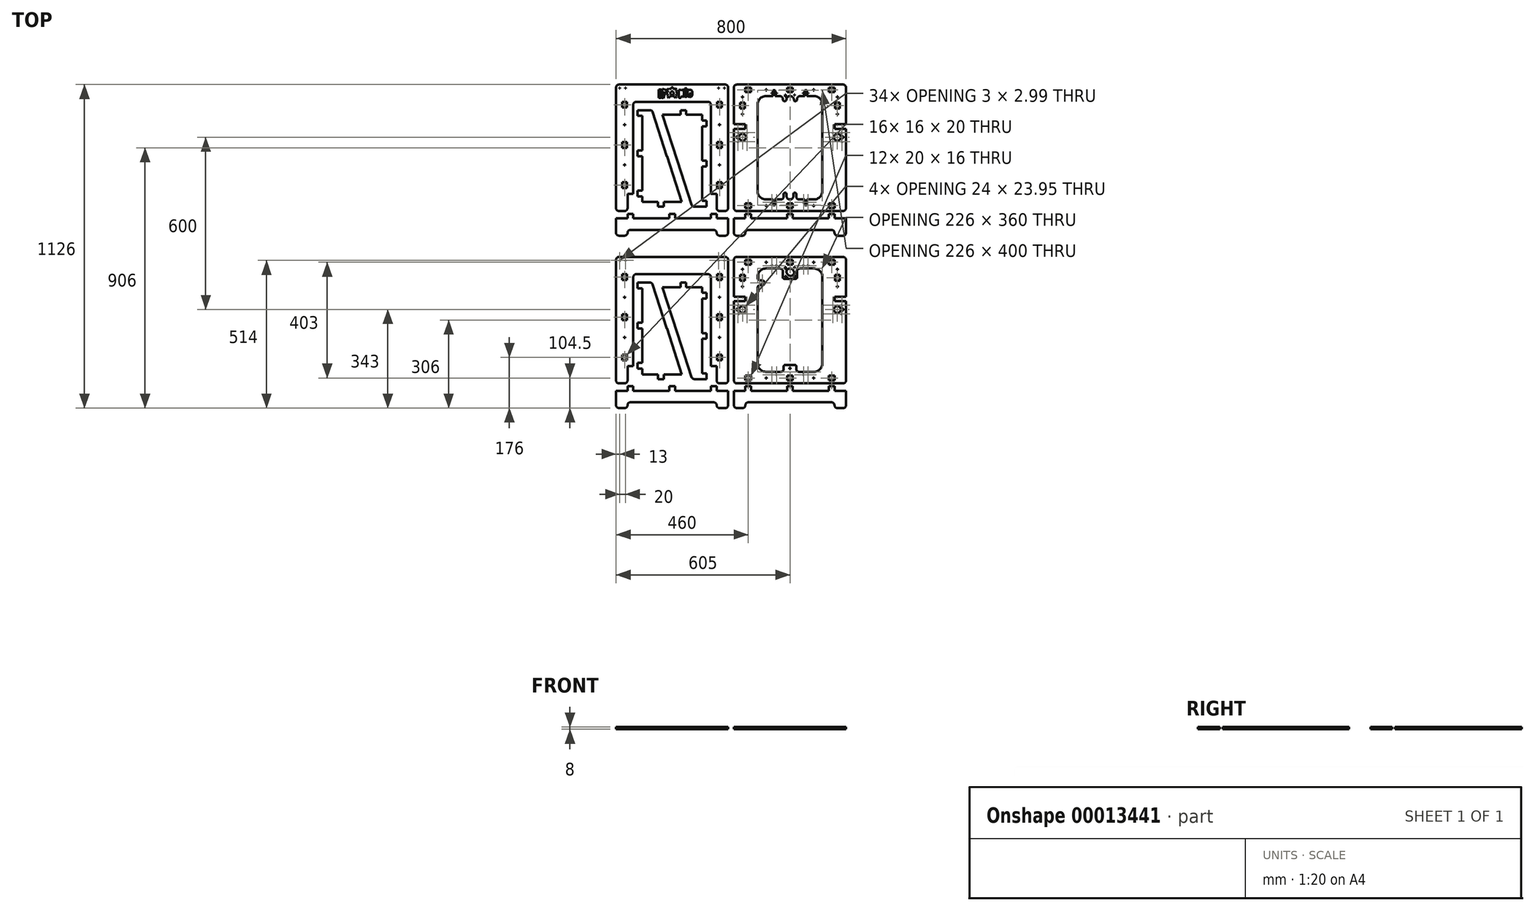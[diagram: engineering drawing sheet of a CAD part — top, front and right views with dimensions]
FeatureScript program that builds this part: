
annotation { "Feature Type Name" : "Feature", "Feature Type Description" : "" }
export const myFeature = defineFeature(function(context is Context, id is Id, definition is map)
    precondition{}
    {
        {
            var Q0;
            Q0=qCreatedBy(makeId("Top.planeOp"),FACE);
            var sketch = newSketch(context, id + "F0", { "sketchPlane" : qUnion([Q0])});
            skLineSegment(sketch, "E0", {"start": v(-368.75, 123.08) * mm, "end": v(-367.51, 123.31) * mm});
            skLineSegment(sketch, "E1", {"start": v(-367.51, 123.31) * mm, "end": v(-366.32, 123.7) * mm});
            skLineSegment(sketch, "E2", {"start": v(-366.32, 123.7) * mm, "end": v(-365.18, 124.24) * mm});
            skLineSegment(sketch, "E3", {"start": v(-365.18, 124.24) * mm, "end": v(-364.12, 124.9) * mm});
            skLineSegment(sketch, "E4", {"start": v(-364.12, 124.9) * mm, "end": v(-363.16, 125.7) * mm});
            skLineSegment(sketch, "E5", {"start": v(-363.16, 125.7) * mm, "end": v(-362.3, 126.63) * mm});
            skLineSegment(sketch, "E6", {"start": v(-362.3, 126.63) * mm, "end": v(-361.56, 127.64) * mm});
            skLineSegment(sketch, "E7", {"start": v(-361.56, 127.64) * mm, "end": v(-360.95, 128.74) * mm});
            skLineSegment(sketch, "E8", {"start": v(-360.95, 128.74) * mm, "end": v(-360.49, 129.9) * mm});
            skLineSegment(sketch, "E9", {"start": v(-360.49, 129.9) * mm, "end": v(-360.18, 131.13) * mm});
            skLineSegment(sketch, "E10", {"start": v(-360.18, 131.13) * mm, "end": v(-360.02, 132.37) * mm});
            skLineSegment(sketch, "E11", {"start": v(-360.02, 132.37) * mm, "end": v(-360.02, 133) * mm});
            skLineSegment(sketch, "E12", {"start": v(-360.02, 133) * mm, "end": v(-360, 133) * mm});
            skLineSegment(sketch, "E13", {"start": v(-360, 133) * mm, "end": v(-360, 183) * mm});
            skLineSegment(sketch, "E14", {"start": v(-360, 183) * mm, "end": v(-340, 183) * mm});
            skLineSegment(sketch, "E15", {"start": v(-340, 183) * mm, "end": v(-340, 493) * mm});
            skLineSegment(sketch, "E16", {"start": v(-340, 493) * mm, "end": v(-339.98, 493) * mm});
            skLineSegment(sketch, "E17", {"start": v(-339.98, 493) * mm, "end": v(-339.98, 493.63) * mm});
            skLineSegment(sketch, "E18", {"start": v(-339.98, 493.63) * mm, "end": v(-339.82, 494.87) * mm});
            skLineSegment(sketch, "E19", {"start": v(-339.82, 494.87) * mm, "end": v(-339.51, 496.09) * mm});
            skLineSegment(sketch, "E20", {"start": v(-339.51, 496.09) * mm, "end": v(-339.05, 497.26) * mm});
            skLineSegment(sketch, "E21", {"start": v(-339.05, 497.26) * mm, "end": v(-338.44, 498.36) * mm});
            skLineSegment(sketch, "E22", {"start": v(-338.44, 498.36) * mm, "end": v(-337.7, 499.37) * mm});
            skLineSegment(sketch, "E23", {"start": v(-337.7, 499.37) * mm, "end": v(-336.85, 500.3) * mm});
            skLineSegment(sketch, "E24", {"start": v(-336.85, 500.3) * mm, "end": v(-335.88, 501.1) * mm});
            skLineSegment(sketch, "E25", {"start": v(-335.88, 501.1) * mm, "end": v(-334.82, 501.76) * mm});
            skLineSegment(sketch, "E26", {"start": v(-334.82, 501.76) * mm, "end": v(-333.68, 502.3) * mm});
            skLineSegment(sketch, "E27", {"start": v(-333.68, 502.3) * mm, "end": v(-332.49, 502.7) * mm});
            skLineSegment(sketch, "E28", {"start": v(-332.49, 502.7) * mm, "end": v(-331.25, 502.92) * mm});
            skLineSegment(sketch, "E29", {"start": v(-331.25, 502.92) * mm, "end": v(-330, 503) * mm});
            skLineSegment(sketch, "E30", {"start": v(-330, 503) * mm, "end": v(-80, 503) * mm});
            skLineSegment(sketch, "E31", {"start": v(-80, 503) * mm, "end": v(-80, 502.98) * mm});
            skLineSegment(sketch, "E32", {"start": v(-80, 502.98) * mm, "end": v(-79.37, 502.98) * mm});
            skLineSegment(sketch, "E33", {"start": v(-79.37, 502.98) * mm, "end": v(-78.13, 502.82) * mm});
            skLineSegment(sketch, "E34", {"start": v(-78.13, 502.82) * mm, "end": v(-76.9, 502.5) * mm});
            skLineSegment(sketch, "E35", {"start": v(-76.9, 502.5) * mm, "end": v(-75.74, 502.05) * mm});
            skLineSegment(sketch, "E36", {"start": v(-75.74, 502.05) * mm, "end": v(-74.64, 501.44) * mm});
            skLineSegment(sketch, "E37", {"start": v(-74.64, 501.44) * mm, "end": v(-73.63, 500.7) * mm});
            skLineSegment(sketch, "E38", {"start": v(-73.63, 500.7) * mm, "end": v(-72.71, 499.85) * mm});
            skLineSegment(sketch, "E39", {"start": v(-72.71, 499.85) * mm, "end": v(-71.9, 498.88) * mm});
            skLineSegment(sketch, "E40", {"start": v(-71.9, 498.88) * mm, "end": v(-71.24, 497.82) * mm});
            skLineSegment(sketch, "E41", {"start": v(-71.24, 497.82) * mm, "end": v(-70.7, 496.68) * mm});
            skLineSegment(sketch, "E42", {"start": v(-70.7, 496.68) * mm, "end": v(-70.31, 495.5) * mm});
            skLineSegment(sketch, "E43", {"start": v(-70.31, 495.5) * mm, "end": v(-70.08, 494.25) * mm});
            skLineSegment(sketch, "E44", {"start": v(-70.08, 494.25) * mm, "end": v(-70, 493) * mm});
            skLineSegment(sketch, "E45", {"start": v(-70, 493) * mm, "end": v(-70, 183) * mm});
            skLineSegment(sketch, "E46", {"start": v(-70, 183) * mm, "end": v(-50, 183) * mm});
            skLineSegment(sketch, "E47", {"start": v(-50, 183) * mm, "end": v(-50, 133) * mm});
            skLineSegment(sketch, "E48", {"start": v(-50, 133) * mm, "end": v(-49.92, 131.75) * mm});
            skLineSegment(sketch, "E49", {"start": v(-49.92, 131.75) * mm, "end": v(-49.69, 130.51) * mm});
            skLineSegment(sketch, "E50", {"start": v(-49.69, 130.51) * mm, "end": v(-49.3, 129.32) * mm});
            skLineSegment(sketch, "E51", {"start": v(-49.3, 129.32) * mm, "end": v(-48.76, 128.18) * mm});
            skLineSegment(sketch, "E52", {"start": v(-48.76, 128.18) * mm, "end": v(-48.1, 127.12) * mm});
            skLineSegment(sketch, "E53", {"start": v(-48.1, 127.12) * mm, "end": v(-47.29, 126.16) * mm});
            skLineSegment(sketch, "E54", {"start": v(-47.29, 126.16) * mm, "end": v(-46.37, 125.3) * mm});
            skLineSegment(sketch, "E55", {"start": v(-46.37, 125.3) * mm, "end": v(-45.36, 124.56) * mm});
            skLineSegment(sketch, "E56", {"start": v(-45.36, 124.56) * mm, "end": v(-44.26, 123.95) * mm});
            skLineSegment(sketch, "E57", {"start": v(-44.26, 123.95) * mm, "end": v(-43.1, 123.49) * mm});
            skLineSegment(sketch, "E58", {"start": v(-43.1, 123.49) * mm, "end": v(-41.87, 123.18) * mm});
            skLineSegment(sketch, "E59", {"start": v(-41.87, 123.18) * mm, "end": v(-40.63, 123.02) * mm});
            skLineSegment(sketch, "E60", {"start": v(-40.63, 123.02) * mm, "end": v(-40, 123.02) * mm});
            skLineSegment(sketch, "E61", {"start": v(-40, 123.02) * mm, "end": v(-40, 123) * mm});
            skLineSegment(sketch, "E62", {"start": v(-40, 123) * mm, "end": v(-20, 123) * mm});
            skLineSegment(sketch, "E63", {"start": v(-20, 123) * mm, "end": v(-18.75, 123.08) * mm});
            skLineSegment(sketch, "E64", {"start": v(-18.75, 123.08) * mm, "end": v(-17.51, 123.31) * mm});
            skLineSegment(sketch, "E65", {"start": v(-17.51, 123.31) * mm, "end": v(-16.32, 123.7) * mm});
            skLineSegment(sketch, "E66", {"start": v(-16.32, 123.7) * mm, "end": v(-15.18, 124.24) * mm});
            skLineSegment(sketch, "E67", {"start": v(-15.18, 124.24) * mm, "end": v(-14.12, 124.9) * mm});
            skLineSegment(sketch, "E68", {"start": v(-14.12, 124.9) * mm, "end": v(-13.15, 125.7) * mm});
            skLineSegment(sketch, "E69", {"start": v(-13.15, 125.7) * mm, "end": v(-12.3, 126.63) * mm});
            skLineSegment(sketch, "E70", {"start": v(-12.3, 126.63) * mm, "end": v(-11.56, 127.64) * mm});
            skLineSegment(sketch, "E71", {"start": v(-11.56, 127.64) * mm, "end": v(-10.95, 128.74) * mm});
            skLineSegment(sketch, "E72", {"start": v(-10.95, 128.74) * mm, "end": v(-10.49, 129.9) * mm});
            skLineSegment(sketch, "E73", {"start": v(-10.49, 129.9) * mm, "end": v(-10.18, 131.13) * mm});
            skLineSegment(sketch, "E74", {"start": v(-10.18, 131.13) * mm, "end": v(-10.02, 132.37) * mm});
            skLineSegment(sketch, "E75", {"start": v(-10.02, 132.37) * mm, "end": v(-10.02, 133) * mm});
            skLineSegment(sketch, "E76", {"start": v(-10.02, 133) * mm, "end": v(-10, 133) * mm});
            skLineSegment(sketch, "E77", {"start": v(-10, 133) * mm, "end": v(-10, 553) * mm});
            skLineSegment(sketch, "E78", {"start": v(-10, 553) * mm, "end": v(-10.08, 554.25) * mm});
            skLineSegment(sketch, "E79", {"start": v(-10.08, 554.25) * mm, "end": v(-10.31, 555.5) * mm});
            skLineSegment(sketch, "E80", {"start": v(-10.31, 555.5) * mm, "end": v(-10.7, 556.68) * mm});
            skLineSegment(sketch, "E81", {"start": v(-10.7, 556.68) * mm, "end": v(-11.24, 557.82) * mm});
            skLineSegment(sketch, "E82", {"start": v(-11.24, 557.82) * mm, "end": v(-11.9, 558.88) * mm});
            skLineSegment(sketch, "E83", {"start": v(-11.9, 558.88) * mm, "end": v(-12.71, 559.85) * mm});
            skLineSegment(sketch, "E84", {"start": v(-12.71, 559.85) * mm, "end": v(-13.63, 560.7) * mm});
            skLineSegment(sketch, "E85", {"start": v(-13.63, 560.7) * mm, "end": v(-14.64, 561.44) * mm});
            skLineSegment(sketch, "E86", {"start": v(-14.64, 561.44) * mm, "end": v(-15.74, 562.05) * mm});
            skLineSegment(sketch, "E87", {"start": v(-15.74, 562.05) * mm, "end": v(-16.9, 562.5) * mm});
            skLineSegment(sketch, "E88", {"start": v(-16.9, 562.5) * mm, "end": v(-18.13, 562.82) * mm});
            skLineSegment(sketch, "E89", {"start": v(-18.13, 562.82) * mm, "end": v(-19.37, 562.98) * mm});
            skLineSegment(sketch, "E90", {"start": v(-19.37, 562.98) * mm, "end": v(-20, 562.98) * mm});
            skLineSegment(sketch, "E91", {"start": v(-20, 562.98) * mm, "end": v(-20, 563) * mm});
            skLineSegment(sketch, "E92", {"start": v(-20, 563) * mm, "end": v(-390, 563) * mm});
            skLineSegment(sketch, "E93", {"start": v(-390, 563) * mm, "end": v(-391.25, 562.92) * mm});
            skLineSegment(sketch, "E94", {"start": v(-391.25, 562.92) * mm, "end": v(-392.49, 562.7) * mm});
            skLineSegment(sketch, "E95", {"start": v(-392.49, 562.7) * mm, "end": v(-393.68, 562.3) * mm});
            skLineSegment(sketch, "E96", {"start": v(-393.68, 562.3) * mm, "end": v(-394.82, 561.76) * mm});
            skLineSegment(sketch, "E97", {"start": v(-394.82, 561.76) * mm, "end": v(-395.88, 561.1) * mm});
            skLineSegment(sketch, "E98", {"start": v(-395.88, 561.1) * mm, "end": v(-396.85, 560.3) * mm});
            skLineSegment(sketch, "E99", {"start": v(-396.85, 560.3) * mm, "end": v(-397.7, 559.37) * mm});
            skLineSegment(sketch, "E100", {"start": v(-397.7, 559.37) * mm, "end": v(-398.44, 558.36) * mm});
            skLineSegment(sketch, "E101", {"start": v(-398.44, 558.36) * mm, "end": v(-399.05, 557.26) * mm});
            skLineSegment(sketch, "E102", {"start": v(-399.05, 557.26) * mm, "end": v(-399.51, 556.1) * mm});
            skLineSegment(sketch, "E103", {"start": v(-399.51, 556.1) * mm, "end": v(-399.82, 554.87) * mm});
            skLineSegment(sketch, "E104", {"start": v(-399.82, 554.87) * mm, "end": v(-399.98, 553.63) * mm});
            skLineSegment(sketch, "E105", {"start": v(-399.98, 553.63) * mm, "end": v(-399.98, 553) * mm});
            skLineSegment(sketch, "E106", {"start": v(-399.98, 553) * mm, "end": v(-400, 553) * mm});
            skLineSegment(sketch, "E107", {"start": v(-400, 553) * mm, "end": v(-400, 133) * mm});
            skLineSegment(sketch, "E108", {"start": v(-400, 133) * mm, "end": v(-399.92, 131.75) * mm});
            skLineSegment(sketch, "E109", {"start": v(-399.92, 131.75) * mm, "end": v(-399.69, 130.51) * mm});
            skLineSegment(sketch, "E110", {"start": v(-399.69, 130.51) * mm, "end": v(-399.3, 129.32) * mm});
            skLineSegment(sketch, "E111", {"start": v(-399.3, 129.32) * mm, "end": v(-398.76, 128.18) * mm});
            skLineSegment(sketch, "E112", {"start": v(-398.76, 128.18) * mm, "end": v(-398.09, 127.12) * mm});
            skLineSegment(sketch, "E113", {"start": v(-398.09, 127.12) * mm, "end": v(-397.3, 126.16) * mm});
            skLineSegment(sketch, "E114", {"start": v(-397.3, 126.16) * mm, "end": v(-396.37, 125.3) * mm});
            skLineSegment(sketch, "E115", {"start": v(-396.37, 125.3) * mm, "end": v(-395.36, 124.56) * mm});
            skLineSegment(sketch, "E116", {"start": v(-395.36, 124.56) * mm, "end": v(-394.26, 123.95) * mm});
            skLineSegment(sketch, "E117", {"start": v(-394.26, 123.95) * mm, "end": v(-393.09, 123.49) * mm});
            skLineSegment(sketch, "E118", {"start": v(-393.09, 123.49) * mm, "end": v(-391.87, 123.18) * mm});
            skLineSegment(sketch, "E119", {"start": v(-391.87, 123.18) * mm, "end": v(-390.63, 123.02) * mm});
            skLineSegment(sketch, "E120", {"start": v(-390.63, 123.02) * mm, "end": v(-390, 123.02) * mm});
            skLineSegment(sketch, "E121", {"start": v(-390, 123.02) * mm, "end": v(-390, 123) * mm});
            skLineSegment(sketch, "E122", {"start": v(-390, 123) * mm, "end": v(-370, 123) * mm});
            skLineSegment(sketch, "E123", {"start": v(-370, 123) * mm, "end": v(-368.75, 123.08) * mm});
            skLineSegment(sketch, "E124", {"start": v(-197.12, 519.95) * mm, "end": v(-199.32, 519.32) * mm});
            skLineSegment(sketch, "E125", {"start": v(-199.32, 519.32) * mm, "end": v(-202.61, 528.04) * mm});
            skLineSegment(sketch, "E126", {"start": v(-202.61, 528.04) * mm, "end": v(-202.21, 528.24) * mm});
            skLineSegment(sketch, "E127", {"start": v(-202.21, 528.24) * mm, "end": v(-201.83, 528.48) * mm});
            skLineSegment(sketch, "E128", {"start": v(-201.83, 528.48) * mm, "end": v(-201.47, 528.74) * mm});
            skLineSegment(sketch, "E129", {"start": v(-201.47, 528.74) * mm, "end": v(-201.13, 529.03) * mm});
            skLineSegment(sketch, "E130", {"start": v(-201.13, 529.03) * mm, "end": v(-200.8, 529.35) * mm});
            skLineSegment(sketch, "E131", {"start": v(-200.8, 529.35) * mm, "end": v(-200.52, 529.7) * mm});
            skLineSegment(sketch, "E132", {"start": v(-200.52, 529.7) * mm, "end": v(-200.25, 530.05) * mm});
            skLineSegment(sketch, "E133", {"start": v(-200.25, 530.05) * mm, "end": v(-200.02, 530.43) * mm});
            skLineSegment(sketch, "E134", {"start": v(-200.02, 530.43) * mm, "end": v(-199.82, 530.83) * mm});
            skLineSegment(sketch, "E135", {"start": v(-199.82, 530.83) * mm, "end": v(-199.65, 531.25) * mm});
            skLineSegment(sketch, "E136", {"start": v(-199.65, 531.25) * mm, "end": v(-199.5, 531.67) * mm});
            skLineSegment(sketch, "E137", {"start": v(-199.5, 531.67) * mm, "end": v(-199.4, 532.1) * mm});
            skLineSegment(sketch, "E138", {"start": v(-199.4, 532.1) * mm, "end": v(-199.33, 532.55) * mm});
            skLineSegment(sketch, "E139", {"start": v(-199.33, 532.55) * mm, "end": v(-199.3, 533) * mm});
            skLineSegment(sketch, "E140", {"start": v(-199.3, 533) * mm, "end": v(-199.3, 533.45) * mm});
            skLineSegment(sketch, "E141", {"start": v(-199.3, 533.45) * mm, "end": v(-199.33, 533.9) * mm});
            skLineSegment(sketch, "E142", {"start": v(-199.33, 533.9) * mm, "end": v(-199.4, 534.34) * mm});
            skLineSegment(sketch, "E143", {"start": v(-199.4, 534.34) * mm, "end": v(-199.5, 534.77) * mm});
            skLineSegment(sketch, "E144", {"start": v(-199.5, 534.77) * mm, "end": v(-199.64, 535.2) * mm});
            skLineSegment(sketch, "E145", {"start": v(-199.64, 535.2) * mm, "end": v(-199.81, 535.62) * mm});
            skLineSegment(sketch, "E146", {"start": v(-199.81, 535.62) * mm, "end": v(-200.02, 536) * mm});
            skLineSegment(sketch, "E147", {"start": v(-200.02, 536) * mm, "end": v(-200.25, 536.4) * mm});
            skLineSegment(sketch, "E148", {"start": v(-200.25, 536.4) * mm, "end": v(-200.52, 536.76) * mm});
            skLineSegment(sketch, "E149", {"start": v(-200.52, 536.76) * mm, "end": v(-200.8, 537.1) * mm});
            skLineSegment(sketch, "E150", {"start": v(-200.8, 537.1) * mm, "end": v(-201.12, 537.42) * mm});
            skLineSegment(sketch, "E151", {"start": v(-201.12, 537.42) * mm, "end": v(-201.47, 537.7) * mm});
            skLineSegment(sketch, "E152", {"start": v(-201.47, 537.7) * mm, "end": v(-201.83, 537.97) * mm});
            skLineSegment(sketch, "E153", {"start": v(-201.83, 537.97) * mm, "end": v(-202.21, 538.2) * mm});
            skLineSegment(sketch, "E154", {"start": v(-202.21, 538.2) * mm, "end": v(-202.6, 538.4) * mm});
            skLineSegment(sketch, "E155", {"start": v(-202.6, 538.4) * mm, "end": v(-203.02, 538.58) * mm});
            skLineSegment(sketch, "E156", {"start": v(-203.02, 538.58) * mm, "end": v(-203.45, 538.72) * mm});
            skLineSegment(sketch, "E157", {"start": v(-203.45, 538.72) * mm, "end": v(-203.89, 538.83) * mm});
            skLineSegment(sketch, "E158", {"start": v(-203.89, 538.83) * mm, "end": v(-204.33, 538.9) * mm});
            skLineSegment(sketch, "E159", {"start": v(-204.33, 538.9) * mm, "end": v(-204.78, 538.93) * mm});
            skLineSegment(sketch, "E160", {"start": v(-204.78, 538.93) * mm, "end": v(-205.22, 538.93) * mm});
            skLineSegment(sketch, "E161", {"start": v(-205.22, 538.93) * mm, "end": v(-205.67, 538.9) * mm});
            skLineSegment(sketch, "E162", {"start": v(-205.67, 538.9) * mm, "end": v(-206.11, 538.83) * mm});
            skLineSegment(sketch, "E163", {"start": v(-206.11, 538.83) * mm, "end": v(-206.55, 538.72) * mm});
            skLineSegment(sketch, "E164", {"start": v(-206.55, 538.72) * mm, "end": v(-206.98, 538.58) * mm});
            skLineSegment(sketch, "E165", {"start": v(-206.98, 538.58) * mm, "end": v(-207.4, 538.4) * mm});
            skLineSegment(sketch, "E166", {"start": v(-207.4, 538.4) * mm, "end": v(-207.79, 538.2) * mm});
            skLineSegment(sketch, "E167", {"start": v(-207.79, 538.2) * mm, "end": v(-208.17, 537.97) * mm});
            skLineSegment(sketch, "E168", {"start": v(-208.17, 537.97) * mm, "end": v(-208.53, 537.7) * mm});
            skLineSegment(sketch, "E169", {"start": v(-208.53, 537.7) * mm, "end": v(-208.88, 537.42) * mm});
            skLineSegment(sketch, "E170", {"start": v(-208.88, 537.42) * mm, "end": v(-209.2, 537.1) * mm});
            skLineSegment(sketch, "E171", {"start": v(-209.2, 537.1) * mm, "end": v(-209.48, 536.76) * mm});
            skLineSegment(sketch, "E172", {"start": v(-209.48, 536.76) * mm, "end": v(-209.75, 536.4) * mm});
            skLineSegment(sketch, "E173", {"start": v(-209.75, 536.4) * mm, "end": v(-209.98, 536) * mm});
            skLineSegment(sketch, "E174", {"start": v(-209.98, 536) * mm, "end": v(-210.19, 535.62) * mm});
            skLineSegment(sketch, "E175", {"start": v(-210.19, 535.62) * mm, "end": v(-210.36, 535.2) * mm});
            skLineSegment(sketch, "E176", {"start": v(-210.36, 535.2) * mm, "end": v(-210.5, 534.77) * mm});
            skLineSegment(sketch, "E177", {"start": v(-210.5, 534.77) * mm, "end": v(-210.6, 534.34) * mm});
            skLineSegment(sketch, "E178", {"start": v(-210.6, 534.34) * mm, "end": v(-210.67, 533.9) * mm});
            skLineSegment(sketch, "E179", {"start": v(-210.67, 533.9) * mm, "end": v(-210.7, 533.45) * mm});
            skLineSegment(sketch, "E180", {"start": v(-210.7, 533.45) * mm, "end": v(-210.7, 533) * mm});
            skLineSegment(sketch, "E181", {"start": v(-210.7, 533) * mm, "end": v(-210.67, 532.55) * mm});
            skLineSegment(sketch, "E182", {"start": v(-210.67, 532.55) * mm, "end": v(-210.6, 532.1) * mm});
            skLineSegment(sketch, "E183", {"start": v(-210.6, 532.1) * mm, "end": v(-210.5, 531.67) * mm});
            skLineSegment(sketch, "E184", {"start": v(-210.5, 531.67) * mm, "end": v(-210.35, 531.25) * mm});
            skLineSegment(sketch, "E185", {"start": v(-210.35, 531.25) * mm, "end": v(-210.18, 530.83) * mm});
            skLineSegment(sketch, "E186", {"start": v(-210.18, 530.83) * mm, "end": v(-209.98, 530.43) * mm});
            skLineSegment(sketch, "E187", {"start": v(-209.98, 530.43) * mm, "end": v(-209.75, 530.05) * mm});
            skLineSegment(sketch, "E188", {"start": v(-209.75, 530.05) * mm, "end": v(-209.48, 529.7) * mm});
            skLineSegment(sketch, "E189", {"start": v(-209.48, 529.7) * mm, "end": v(-209.2, 529.35) * mm});
            skLineSegment(sketch, "E190", {"start": v(-209.2, 529.35) * mm, "end": v(-208.87, 529.03) * mm});
            skLineSegment(sketch, "E191", {"start": v(-208.87, 529.03) * mm, "end": v(-208.53, 528.74) * mm});
            skLineSegment(sketch, "E192", {"start": v(-208.53, 528.74) * mm, "end": v(-208.17, 528.48) * mm});
            skLineSegment(sketch, "E193", {"start": v(-208.17, 528.48) * mm, "end": v(-207.79, 528.24) * mm});
            skLineSegment(sketch, "E194", {"start": v(-207.79, 528.24) * mm, "end": v(-207.25, 527.7) * mm});
            skLineSegment(sketch, "E195", {"start": v(-207.25, 527.7) * mm, "end": v(-211.02, 519.18) * mm});
            skLineSegment(sketch, "E196", {"start": v(-211.02, 519.18) * mm, "end": v(-213.12, 519.92) * mm});
            skLineSegment(sketch, "E197", {"start": v(-213.12, 519.92) * mm, "end": v(-217.54, 517.2) * mm});
            skLineSegment(sketch, "E198", {"start": v(-217.54, 517.2) * mm, "end": v(-221.07, 521) * mm});
            skLineSegment(sketch, "E199", {"start": v(-221.07, 521) * mm, "end": v(-218.28, 525.35) * mm});
            skLineSegment(sketch, "E200", {"start": v(-218.28, 525.35) * mm, "end": v(-220.15, 529.57) * mm});
            skLineSegment(sketch, "E201", {"start": v(-220.15, 529.57) * mm, "end": v(-225.2, 530.76) * mm});
            skLineSegment(sketch, "E202", {"start": v(-225.2, 530.76) * mm, "end": v(-225, 535.95) * mm});
            skLineSegment(sketch, "E203", {"start": v(-225, 535.95) * mm, "end": v(-219.96, 537.04) * mm});
            skLineSegment(sketch, "E204", {"start": v(-219.96, 537.04) * mm, "end": v(-218.3, 541.35) * mm});
            skLineSegment(sketch, "E205", {"start": v(-218.3, 541.35) * mm, "end": v(-221.03, 545.77) * mm});
            skLineSegment(sketch, "E206", {"start": v(-221.03, 545.77) * mm, "end": v(-217.21, 549.3) * mm});
            skLineSegment(sketch, "E207", {"start": v(-217.21, 549.3) * mm, "end": v(-212.88, 546.5) * mm});
            skLineSegment(sketch, "E208", {"start": v(-212.88, 546.5) * mm, "end": v(-208.66, 548.38) * mm});
            skLineSegment(sketch, "E209", {"start": v(-208.66, 548.38) * mm, "end": v(-207.47, 553.43) * mm});
            skLineSegment(sketch, "E210", {"start": v(-207.47, 553.43) * mm, "end": v(-202.27, 553.22) * mm});
            skLineSegment(sketch, "E211", {"start": v(-202.27, 553.22) * mm, "end": v(-201.18, 548.18) * mm});
            skLineSegment(sketch, "E212", {"start": v(-201.18, 548.18) * mm, "end": v(-196.88, 546.53) * mm});
            skLineSegment(sketch, "E213", {"start": v(-196.88, 546.53) * mm, "end": v(-192.46, 549.26) * mm});
            skLineSegment(sketch, "E214", {"start": v(-192.46, 549.26) * mm, "end": v(-188.93, 545.44) * mm});
            skLineSegment(sketch, "E215", {"start": v(-188.93, 545.44) * mm, "end": v(-191.72, 541.1) * mm});
            skLineSegment(sketch, "E216", {"start": v(-191.72, 541.1) * mm, "end": v(-189.85, 536.9) * mm});
            skLineSegment(sketch, "E217", {"start": v(-189.85, 536.9) * mm, "end": v(-184.8, 535.7) * mm});
            skLineSegment(sketch, "E218", {"start": v(-184.8, 535.7) * mm, "end": v(-185, 530.5) * mm});
            skLineSegment(sketch, "E219", {"start": v(-185, 530.5) * mm, "end": v(-190.04, 529.4) * mm});
            skLineSegment(sketch, "E220", {"start": v(-190.04, 529.4) * mm, "end": v(-191.7, 525.1) * mm});
            skLineSegment(sketch, "E221", {"start": v(-191.7, 525.1) * mm, "end": v(-188.97, 520.68) * mm});
            skLineSegment(sketch, "E222", {"start": v(-188.97, 520.68) * mm, "end": v(-192.79, 517.16) * mm});
            skLineSegment(sketch, "E223", {"start": v(-192.79, 517.16) * mm, "end": v(-197.12, 519.95) * mm});
            skLineSegment(sketch, "E224", {"start": v(-367.1, 549.5) * mm, "end": v(-367.28, 549.53) * mm});
            skLineSegment(sketch, "E225", {"start": v(-367.28, 549.53) * mm, "end": v(-367.46, 549.57) * mm});
            skLineSegment(sketch, "E226", {"start": v(-367.46, 549.57) * mm, "end": v(-367.64, 549.64) * mm});
            skLineSegment(sketch, "E227", {"start": v(-367.64, 549.64) * mm, "end": v(-367.8, 549.73) * mm});
            skLineSegment(sketch, "E228", {"start": v(-367.8, 549.73) * mm, "end": v(-367.96, 549.84) * mm});
            skLineSegment(sketch, "E229", {"start": v(-367.96, 549.84) * mm, "end": v(-368.1, 549.97) * mm});
            skLineSegment(sketch, "E230", {"start": v(-368.1, 549.97) * mm, "end": v(-368.21, 550.12) * mm});
            skLineSegment(sketch, "E231", {"start": v(-368.21, 550.12) * mm, "end": v(-368.31, 550.28) * mm});
            skLineSegment(sketch, "E232", {"start": v(-368.31, 550.28) * mm, "end": v(-368.4, 550.45) * mm});
            skLineSegment(sketch, "E233", {"start": v(-368.4, 550.45) * mm, "end": v(-368.45, 550.63) * mm});
            skLineSegment(sketch, "E234", {"start": v(-368.45, 550.63) * mm, "end": v(-368.49, 550.8) * mm});
            skLineSegment(sketch, "E235", {"start": v(-368.49, 550.8) * mm, "end": v(-368.5, 551) * mm});
            skLineSegment(sketch, "E236", {"start": v(-368.5, 551) * mm, "end": v(-368.49, 551.2) * mm});
            skLineSegment(sketch, "E237", {"start": v(-368.49, 551.2) * mm, "end": v(-368.45, 551.37) * mm});
            skLineSegment(sketch, "E238", {"start": v(-368.45, 551.37) * mm, "end": v(-368.4, 551.55) * mm});
            skLineSegment(sketch, "E239", {"start": v(-368.4, 551.55) * mm, "end": v(-368.31, 551.72) * mm});
            skLineSegment(sketch, "E240", {"start": v(-368.31, 551.72) * mm, "end": v(-368.21, 551.88) * mm});
            skLineSegment(sketch, "E241", {"start": v(-368.21, 551.88) * mm, "end": v(-368.1, 552.03) * mm});
            skLineSegment(sketch, "E242", {"start": v(-368.1, 552.03) * mm, "end": v(-367.96, 552.16) * mm});
            skLineSegment(sketch, "E243", {"start": v(-367.96, 552.16) * mm, "end": v(-367.8, 552.27) * mm});
            skLineSegment(sketch, "E244", {"start": v(-367.8, 552.27) * mm, "end": v(-367.64, 552.36) * mm});
            skLineSegment(sketch, "E245", {"start": v(-367.64, 552.36) * mm, "end": v(-367.46, 552.43) * mm});
            skLineSegment(sketch, "E246", {"start": v(-367.46, 552.43) * mm, "end": v(-367.28, 552.47) * mm});
            skLineSegment(sketch, "E247", {"start": v(-367.28, 552.47) * mm, "end": v(-367.1, 552.5) * mm});
            skLineSegment(sketch, "E248", {"start": v(-367.1, 552.5) * mm, "end": v(-366.9, 552.5) * mm});
            skLineSegment(sketch, "E249", {"start": v(-366.9, 552.5) * mm, "end": v(-366.72, 552.47) * mm});
            skLineSegment(sketch, "E250", {"start": v(-366.72, 552.47) * mm, "end": v(-366.54, 552.43) * mm});
            skLineSegment(sketch, "E251", {"start": v(-366.54, 552.43) * mm, "end": v(-366.36, 552.36) * mm});
            skLineSegment(sketch, "E252", {"start": v(-366.36, 552.36) * mm, "end": v(-366.2, 552.27) * mm});
            skLineSegment(sketch, "E253", {"start": v(-366.2, 552.27) * mm, "end": v(-366.04, 552.16) * mm});
            skLineSegment(sketch, "E254", {"start": v(-366.04, 552.16) * mm, "end": v(-365.9, 552.03) * mm});
            skLineSegment(sketch, "E255", {"start": v(-365.9, 552.03) * mm, "end": v(-365.79, 551.88) * mm});
            skLineSegment(sketch, "E256", {"start": v(-365.79, 551.88) * mm, "end": v(-365.69, 551.72) * mm});
            skLineSegment(sketch, "E257", {"start": v(-365.69, 551.72) * mm, "end": v(-365.6, 551.55) * mm});
            skLineSegment(sketch, "E258", {"start": v(-365.6, 551.55) * mm, "end": v(-365.55, 551.37) * mm});
            skLineSegment(sketch, "E259", {"start": v(-365.55, 551.37) * mm, "end": v(-365.51, 551.2) * mm});
            skLineSegment(sketch, "E260", {"start": v(-365.51, 551.2) * mm, "end": v(-365.5, 551) * mm});
            skLineSegment(sketch, "E261", {"start": v(-365.5, 551) * mm, "end": v(-365.51, 550.8) * mm});
            skLineSegment(sketch, "E262", {"start": v(-365.51, 550.8) * mm, "end": v(-365.55, 550.63) * mm});
            skLineSegment(sketch, "E263", {"start": v(-365.55, 550.63) * mm, "end": v(-365.6, 550.45) * mm});
            skLineSegment(sketch, "E264", {"start": v(-365.6, 550.45) * mm, "end": v(-365.69, 550.28) * mm});
            skLineSegment(sketch, "E265", {"start": v(-365.69, 550.28) * mm, "end": v(-365.79, 550.12) * mm});
            skLineSegment(sketch, "E266", {"start": v(-365.79, 550.12) * mm, "end": v(-365.9, 549.97) * mm});
            skLineSegment(sketch, "E267", {"start": v(-365.9, 549.97) * mm, "end": v(-366.04, 549.84) * mm});
            skLineSegment(sketch, "E268", {"start": v(-366.04, 549.84) * mm, "end": v(-366.2, 549.73) * mm});
            skLineSegment(sketch, "E269", {"start": v(-366.2, 549.73) * mm, "end": v(-366.36, 549.64) * mm});
            skLineSegment(sketch, "E270", {"start": v(-366.36, 549.64) * mm, "end": v(-366.54, 549.57) * mm});
            skLineSegment(sketch, "E271", {"start": v(-366.54, 549.57) * mm, "end": v(-366.72, 549.53) * mm});
            skLineSegment(sketch, "E272", {"start": v(-366.72, 549.53) * mm, "end": v(-366.9, 549.5) * mm});
            skLineSegment(sketch, "E273", {"start": v(-366.9, 549.5) * mm, "end": v(-367.1, 549.5) * mm});
            skLineSegment(sketch, "E274", {"start": v(-43.1, 549.5) * mm, "end": v(-43.28, 549.53) * mm});
            skLineSegment(sketch, "E275", {"start": v(-43.28, 549.53) * mm, "end": v(-43.46, 549.57) * mm});
            skLineSegment(sketch, "E276", {"start": v(-43.46, 549.57) * mm, "end": v(-43.64, 549.64) * mm});
            skLineSegment(sketch, "E277", {"start": v(-43.64, 549.64) * mm, "end": v(-43.8, 549.73) * mm});
            skLineSegment(sketch, "E278", {"start": v(-43.8, 549.73) * mm, "end": v(-43.96, 549.84) * mm});
            skLineSegment(sketch, "E279", {"start": v(-43.96, 549.84) * mm, "end": v(-44.1, 549.97) * mm});
            skLineSegment(sketch, "E280", {"start": v(-44.1, 549.97) * mm, "end": v(-44.21, 550.12) * mm});
            skLineSegment(sketch, "E281", {"start": v(-44.21, 550.12) * mm, "end": v(-44.31, 550.28) * mm});
            skLineSegment(sketch, "E282", {"start": v(-44.31, 550.28) * mm, "end": v(-44.4, 550.45) * mm});
            skLineSegment(sketch, "E283", {"start": v(-44.4, 550.45) * mm, "end": v(-44.45, 550.63) * mm});
            skLineSegment(sketch, "E284", {"start": v(-44.45, 550.63) * mm, "end": v(-44.49, 550.8) * mm});
            skLineSegment(sketch, "E285", {"start": v(-44.49, 550.8) * mm, "end": v(-44.5, 551) * mm});
            skLineSegment(sketch, "E286", {"start": v(-44.5, 551) * mm, "end": v(-44.49, 551.2) * mm});
            skLineSegment(sketch, "E287", {"start": v(-44.49, 551.2) * mm, "end": v(-44.45, 551.37) * mm});
            skLineSegment(sketch, "E288", {"start": v(-44.45, 551.37) * mm, "end": v(-44.4, 551.55) * mm});
            skLineSegment(sketch, "E289", {"start": v(-44.4, 551.55) * mm, "end": v(-44.31, 551.72) * mm});
            skLineSegment(sketch, "E290", {"start": v(-44.31, 551.72) * mm, "end": v(-44.21, 551.88) * mm});
            skLineSegment(sketch, "E291", {"start": v(-44.21, 551.88) * mm, "end": v(-44.1, 552.03) * mm});
            skLineSegment(sketch, "E292", {"start": v(-44.1, 552.03) * mm, "end": v(-43.96, 552.16) * mm});
            skLineSegment(sketch, "E293", {"start": v(-43.96, 552.16) * mm, "end": v(-43.8, 552.27) * mm});
            skLineSegment(sketch, "E294", {"start": v(-43.8, 552.27) * mm, "end": v(-43.64, 552.36) * mm});
            skLineSegment(sketch, "E295", {"start": v(-43.64, 552.36) * mm, "end": v(-43.46, 552.43) * mm});
            skLineSegment(sketch, "E296", {"start": v(-43.46, 552.43) * mm, "end": v(-43.28, 552.47) * mm});
            skLineSegment(sketch, "E297", {"start": v(-43.28, 552.47) * mm, "end": v(-43.1, 552.5) * mm});
            skLineSegment(sketch, "E298", {"start": v(-43.1, 552.5) * mm, "end": v(-42.9, 552.5) * mm});
            skLineSegment(sketch, "E299", {"start": v(-42.9, 552.5) * mm, "end": v(-42.72, 552.47) * mm});
            skLineSegment(sketch, "E300", {"start": v(-42.72, 552.47) * mm, "end": v(-42.54, 552.43) * mm});
            skLineSegment(sketch, "E301", {"start": v(-42.54, 552.43) * mm, "end": v(-42.36, 552.36) * mm});
            skLineSegment(sketch, "E302", {"start": v(-42.36, 552.36) * mm, "end": v(-42.2, 552.27) * mm});
            skLineSegment(sketch, "E303", {"start": v(-42.2, 552.27) * mm, "end": v(-42.04, 552.16) * mm});
            skLineSegment(sketch, "E304", {"start": v(-42.04, 552.16) * mm, "end": v(-41.9, 552.03) * mm});
            skLineSegment(sketch, "E305", {"start": v(-41.9, 552.03) * mm, "end": v(-41.79, 551.88) * mm});
            skLineSegment(sketch, "E306", {"start": v(-41.79, 551.88) * mm, "end": v(-41.69, 551.72) * mm});
            skLineSegment(sketch, "E307", {"start": v(-41.69, 551.72) * mm, "end": v(-41.6, 551.55) * mm});
            skLineSegment(sketch, "E308", {"start": v(-41.6, 551.55) * mm, "end": v(-41.55, 551.37) * mm});
            skLineSegment(sketch, "E309", {"start": v(-41.55, 551.37) * mm, "end": v(-41.51, 551.2) * mm});
            skLineSegment(sketch, "E310", {"start": v(-41.51, 551.2) * mm, "end": v(-41.5, 551) * mm});
            skLineSegment(sketch, "E311", {"start": v(-41.5, 551) * mm, "end": v(-41.51, 550.8) * mm});
            skLineSegment(sketch, "E312", {"start": v(-41.51, 550.8) * mm, "end": v(-41.55, 550.63) * mm});
            skLineSegment(sketch, "E313", {"start": v(-41.55, 550.63) * mm, "end": v(-41.6, 550.45) * mm});
            skLineSegment(sketch, "E314", {"start": v(-41.6, 550.45) * mm, "end": v(-41.69, 550.28) * mm});
            skLineSegment(sketch, "E315", {"start": v(-41.69, 550.28) * mm, "end": v(-41.79, 550.12) * mm});
            skLineSegment(sketch, "E316", {"start": v(-41.79, 550.12) * mm, "end": v(-41.9, 549.97) * mm});
            skLineSegment(sketch, "E317", {"start": v(-41.9, 549.97) * mm, "end": v(-42.04, 549.84) * mm});
            skLineSegment(sketch, "E318", {"start": v(-42.04, 549.84) * mm, "end": v(-42.2, 549.73) * mm});
            skLineSegment(sketch, "E319", {"start": v(-42.2, 549.73) * mm, "end": v(-42.36, 549.64) * mm});
            skLineSegment(sketch, "E320", {"start": v(-42.36, 549.64) * mm, "end": v(-42.54, 549.57) * mm});
            skLineSegment(sketch, "E321", {"start": v(-42.54, 549.57) * mm, "end": v(-42.72, 549.53) * mm});
            skLineSegment(sketch, "E322", {"start": v(-42.72, 549.53) * mm, "end": v(-42.9, 549.5) * mm});
            skLineSegment(sketch, "E323", {"start": v(-42.9, 549.5) * mm, "end": v(-43.1, 549.5) * mm});
            skLineSegment(sketch, "E324", {"start": v(-23.1, 549.5) * mm, "end": v(-23.28, 549.53) * mm});
            skLineSegment(sketch, "E325", {"start": v(-23.28, 549.53) * mm, "end": v(-23.46, 549.57) * mm});
            skLineSegment(sketch, "E326", {"start": v(-23.46, 549.57) * mm, "end": v(-23.64, 549.64) * mm});
            skLineSegment(sketch, "E327", {"start": v(-23.64, 549.64) * mm, "end": v(-23.8, 549.73) * mm});
            skLineSegment(sketch, "E328", {"start": v(-23.8, 549.73) * mm, "end": v(-23.96, 549.84) * mm});
            skLineSegment(sketch, "E329", {"start": v(-23.96, 549.84) * mm, "end": v(-24.1, 549.97) * mm});
            skLineSegment(sketch, "E330", {"start": v(-24.1, 549.97) * mm, "end": v(-24.21, 550.12) * mm});
            skLineSegment(sketch, "E331", {"start": v(-24.21, 550.12) * mm, "end": v(-24.31, 550.28) * mm});
            skLineSegment(sketch, "E332", {"start": v(-24.31, 550.28) * mm, "end": v(-24.4, 550.45) * mm});
            skLineSegment(sketch, "E333", {"start": v(-24.4, 550.45) * mm, "end": v(-24.45, 550.63) * mm});
            skLineSegment(sketch, "E334", {"start": v(-24.45, 550.63) * mm, "end": v(-24.49, 550.8) * mm});
            skLineSegment(sketch, "E335", {"start": v(-24.49, 550.8) * mm, "end": v(-24.5, 551) * mm});
            skLineSegment(sketch, "E336", {"start": v(-24.5, 551) * mm, "end": v(-24.49, 551.2) * mm});
            skLineSegment(sketch, "E337", {"start": v(-24.49, 551.2) * mm, "end": v(-24.45, 551.37) * mm});
            skLineSegment(sketch, "E338", {"start": v(-24.45, 551.37) * mm, "end": v(-24.4, 551.55) * mm});
            skLineSegment(sketch, "E339", {"start": v(-24.4, 551.55) * mm, "end": v(-24.31, 551.72) * mm});
            skLineSegment(sketch, "E340", {"start": v(-24.31, 551.72) * mm, "end": v(-24.21, 551.88) * mm});
            skLineSegment(sketch, "E341", {"start": v(-24.21, 551.88) * mm, "end": v(-24.1, 552.03) * mm});
            skLineSegment(sketch, "E342", {"start": v(-24.1, 552.03) * mm, "end": v(-23.96, 552.16) * mm});
            skLineSegment(sketch, "E343", {"start": v(-23.96, 552.16) * mm, "end": v(-23.8, 552.27) * mm});
            skLineSegment(sketch, "E344", {"start": v(-23.8, 552.27) * mm, "end": v(-23.64, 552.36) * mm});
            skLineSegment(sketch, "E345", {"start": v(-23.64, 552.36) * mm, "end": v(-23.46, 552.43) * mm});
            skLineSegment(sketch, "E346", {"start": v(-23.46, 552.43) * mm, "end": v(-23.28, 552.47) * mm});
            skLineSegment(sketch, "E347", {"start": v(-23.28, 552.47) * mm, "end": v(-23.1, 552.5) * mm});
            skLineSegment(sketch, "E348", {"start": v(-23.1, 552.5) * mm, "end": v(-22.9, 552.5) * mm});
            skLineSegment(sketch, "E349", {"start": v(-22.9, 552.5) * mm, "end": v(-22.72, 552.47) * mm});
            skLineSegment(sketch, "E350", {"start": v(-22.72, 552.47) * mm, "end": v(-22.54, 552.43) * mm});
            skLineSegment(sketch, "E351", {"start": v(-22.54, 552.43) * mm, "end": v(-22.36, 552.36) * mm});
            skLineSegment(sketch, "E352", {"start": v(-22.36, 552.36) * mm, "end": v(-22.2, 552.27) * mm});
            skLineSegment(sketch, "E353", {"start": v(-22.2, 552.27) * mm, "end": v(-22.04, 552.16) * mm});
            skLineSegment(sketch, "E354", {"start": v(-22.04, 552.16) * mm, "end": v(-21.9, 552.03) * mm});
            skLineSegment(sketch, "E355", {"start": v(-21.9, 552.03) * mm, "end": v(-21.79, 551.88) * mm});
            skLineSegment(sketch, "E356", {"start": v(-21.79, 551.88) * mm, "end": v(-21.69, 551.72) * mm});
            skLineSegment(sketch, "E357", {"start": v(-21.69, 551.72) * mm, "end": v(-21.6, 551.55) * mm});
            skLineSegment(sketch, "E358", {"start": v(-21.6, 551.55) * mm, "end": v(-21.55, 551.37) * mm});
            skLineSegment(sketch, "E359", {"start": v(-21.55, 551.37) * mm, "end": v(-21.51, 551.2) * mm});
            skLineSegment(sketch, "E360", {"start": v(-21.51, 551.2) * mm, "end": v(-21.5, 551) * mm});
            skLineSegment(sketch, "E361", {"start": v(-21.5, 551) * mm, "end": v(-21.51, 550.8) * mm});
            skLineSegment(sketch, "E362", {"start": v(-21.51, 550.8) * mm, "end": v(-21.55, 550.63) * mm});
            skLineSegment(sketch, "E363", {"start": v(-21.55, 550.63) * mm, "end": v(-21.6, 550.45) * mm});
            skLineSegment(sketch, "E364", {"start": v(-21.6, 550.45) * mm, "end": v(-21.69, 550.28) * mm});
            skLineSegment(sketch, "E365", {"start": v(-21.69, 550.28) * mm, "end": v(-21.79, 550.12) * mm});
            skLineSegment(sketch, "E366", {"start": v(-21.79, 550.12) * mm, "end": v(-21.9, 549.97) * mm});
            skLineSegment(sketch, "E367", {"start": v(-21.9, 549.97) * mm, "end": v(-22.04, 549.84) * mm});
            skLineSegment(sketch, "E368", {"start": v(-22.04, 549.84) * mm, "end": v(-22.2, 549.73) * mm});
            skLineSegment(sketch, "E369", {"start": v(-22.2, 549.73) * mm, "end": v(-22.36, 549.64) * mm});
            skLineSegment(sketch, "E370", {"start": v(-22.36, 549.64) * mm, "end": v(-22.54, 549.57) * mm});
            skLineSegment(sketch, "E371", {"start": v(-22.54, 549.57) * mm, "end": v(-22.72, 549.53) * mm});
            skLineSegment(sketch, "E372", {"start": v(-22.72, 549.53) * mm, "end": v(-22.9, 549.5) * mm});
            skLineSegment(sketch, "E373", {"start": v(-22.9, 549.5) * mm, "end": v(-23.1, 549.5) * mm});
            skLineSegment(sketch, "E374", {"start": v(-387.1, 549.5) * mm, "end": v(-387.28, 549.53) * mm});
            skLineSegment(sketch, "E375", {"start": v(-387.28, 549.53) * mm, "end": v(-387.46, 549.57) * mm});
            skLineSegment(sketch, "E376", {"start": v(-387.46, 549.57) * mm, "end": v(-387.64, 549.64) * mm});
            skLineSegment(sketch, "E377", {"start": v(-387.64, 549.64) * mm, "end": v(-387.8, 549.73) * mm});
            skLineSegment(sketch, "E378", {"start": v(-387.8, 549.73) * mm, "end": v(-387.96, 549.84) * mm});
            skLineSegment(sketch, "E379", {"start": v(-387.96, 549.84) * mm, "end": v(-388.1, 549.97) * mm});
            skLineSegment(sketch, "E380", {"start": v(-388.1, 549.97) * mm, "end": v(-388.21, 550.12) * mm});
            skLineSegment(sketch, "E381", {"start": v(-388.21, 550.12) * mm, "end": v(-388.31, 550.28) * mm});
            skLineSegment(sketch, "E382", {"start": v(-388.31, 550.28) * mm, "end": v(-388.4, 550.45) * mm});
            skLineSegment(sketch, "E383", {"start": v(-388.4, 550.45) * mm, "end": v(-388.45, 550.63) * mm});
            skLineSegment(sketch, "E384", {"start": v(-388.45, 550.63) * mm, "end": v(-388.49, 550.8) * mm});
            skLineSegment(sketch, "E385", {"start": v(-388.49, 550.8) * mm, "end": v(-388.5, 551) * mm});
            skLineSegment(sketch, "E386", {"start": v(-388.5, 551) * mm, "end": v(-388.49, 551.2) * mm});
            skLineSegment(sketch, "E387", {"start": v(-388.49, 551.2) * mm, "end": v(-388.45, 551.37) * mm});
            skLineSegment(sketch, "E388", {"start": v(-388.45, 551.37) * mm, "end": v(-388.4, 551.55) * mm});
            skLineSegment(sketch, "E389", {"start": v(-388.4, 551.55) * mm, "end": v(-388.31, 551.72) * mm});
            skLineSegment(sketch, "E390", {"start": v(-388.31, 551.72) * mm, "end": v(-388.21, 551.88) * mm});
            skLineSegment(sketch, "E391", {"start": v(-388.21, 551.88) * mm, "end": v(-388.1, 552.03) * mm});
            skLineSegment(sketch, "E392", {"start": v(-388.1, 552.03) * mm, "end": v(-387.96, 552.16) * mm});
            skLineSegment(sketch, "E393", {"start": v(-387.96, 552.16) * mm, "end": v(-387.8, 552.27) * mm});
            skLineSegment(sketch, "E394", {"start": v(-387.8, 552.27) * mm, "end": v(-387.64, 552.36) * mm});
            skLineSegment(sketch, "E395", {"start": v(-387.64, 552.36) * mm, "end": v(-387.46, 552.43) * mm});
            skLineSegment(sketch, "E396", {"start": v(-387.46, 552.43) * mm, "end": v(-387.28, 552.47) * mm});
            skLineSegment(sketch, "E397", {"start": v(-387.28, 552.47) * mm, "end": v(-387.1, 552.5) * mm});
            skLineSegment(sketch, "E398", {"start": v(-387.1, 552.5) * mm, "end": v(-386.9, 552.5) * mm});
            skLineSegment(sketch, "E399", {"start": v(-386.9, 552.5) * mm, "end": v(-386.72, 552.47) * mm});
            skLineSegment(sketch, "E400", {"start": v(-386.72, 552.47) * mm, "end": v(-386.54, 552.43) * mm});
            skLineSegment(sketch, "E401", {"start": v(-386.54, 552.43) * mm, "end": v(-386.36, 552.36) * mm});
            skLineSegment(sketch, "E402", {"start": v(-386.36, 552.36) * mm, "end": v(-386.2, 552.27) * mm});
            skLineSegment(sketch, "E403", {"start": v(-386.2, 552.27) * mm, "end": v(-386.04, 552.16) * mm});
            skLineSegment(sketch, "E404", {"start": v(-386.04, 552.16) * mm, "end": v(-385.9, 552.03) * mm});
            skLineSegment(sketch, "E405", {"start": v(-385.9, 552.03) * mm, "end": v(-385.79, 551.88) * mm});
            skLineSegment(sketch, "E406", {"start": v(-385.79, 551.88) * mm, "end": v(-385.69, 551.72) * mm});
            skLineSegment(sketch, "E407", {"start": v(-385.69, 551.72) * mm, "end": v(-385.6, 551.55) * mm});
            skLineSegment(sketch, "E408", {"start": v(-385.6, 551.55) * mm, "end": v(-385.55, 551.37) * mm});
            skLineSegment(sketch, "E409", {"start": v(-385.55, 551.37) * mm, "end": v(-385.51, 551.2) * mm});
            skLineSegment(sketch, "E410", {"start": v(-385.51, 551.2) * mm, "end": v(-385.5, 551) * mm});
            skLineSegment(sketch, "E411", {"start": v(-385.5, 551) * mm, "end": v(-385.51, 550.8) * mm});
            skLineSegment(sketch, "E412", {"start": v(-385.51, 550.8) * mm, "end": v(-385.55, 550.63) * mm});
            skLineSegment(sketch, "E413", {"start": v(-385.55, 550.63) * mm, "end": v(-385.6, 550.45) * mm});
            skLineSegment(sketch, "E414", {"start": v(-385.6, 550.45) * mm, "end": v(-385.69, 550.28) * mm});
            skLineSegment(sketch, "E415", {"start": v(-385.69, 550.28) * mm, "end": v(-385.79, 550.12) * mm});
            skLineSegment(sketch, "E416", {"start": v(-385.79, 550.12) * mm, "end": v(-385.9, 549.97) * mm});
            skLineSegment(sketch, "E417", {"start": v(-385.9, 549.97) * mm, "end": v(-386.04, 549.84) * mm});
            skLineSegment(sketch, "E418", {"start": v(-386.04, 549.84) * mm, "end": v(-386.2, 549.73) * mm});
            skLineSegment(sketch, "E419", {"start": v(-386.2, 549.73) * mm, "end": v(-386.36, 549.64) * mm});
            skLineSegment(sketch, "E420", {"start": v(-386.36, 549.64) * mm, "end": v(-386.54, 549.57) * mm});
            skLineSegment(sketch, "E421", {"start": v(-386.54, 549.57) * mm, "end": v(-386.72, 549.53) * mm});
            skLineSegment(sketch, "E422", {"start": v(-386.72, 549.53) * mm, "end": v(-386.9, 549.5) * mm});
            skLineSegment(sketch, "E423", {"start": v(-386.9, 549.5) * mm, "end": v(-387.1, 549.5) * mm});
            skLineSegment(sketch, "E424", {"start": v(-162.03, 546.2) * mm, "end": v(-162.03, 550.1) * mm});
            skLineSegment(sketch, "E425", {"start": v(-162.03, 550.1) * mm, "end": v(-154.32, 550.1) * mm});
            skLineSegment(sketch, "E426", {"start": v(-154.32, 550.1) * mm, "end": v(-154.32, 546.2) * mm});
            skLineSegment(sketch, "E427", {"start": v(-154.32, 546.2) * mm, "end": v(-162.03, 546.2) * mm});
            skLineSegment(sketch, "E428", {"start": v(-242.1, 517.57) * mm, "end": v(-235.89, 540.74) * mm});
            skLineSegment(sketch, "E429", {"start": v(-235.89, 540.74) * mm, "end": v(-240.34, 541.94) * mm});
            skLineSegment(sketch, "E430", {"start": v(-240.34, 541.94) * mm, "end": v(-238.8, 547.74) * mm});
            skLineSegment(sketch, "E431", {"start": v(-238.8, 547.74) * mm, "end": v(-222.32, 543.33) * mm});
            skLineSegment(sketch, "E432", {"start": v(-222.32, 543.33) * mm, "end": v(-223.88, 537.53) * mm});
            skLineSegment(sketch, "E433", {"start": v(-223.88, 537.53) * mm, "end": v(-228.35, 538.73) * mm});
            skLineSegment(sketch, "E434", {"start": v(-228.35, 538.73) * mm, "end": v(-234.56, 515.55) * mm});
            skLineSegment(sketch, "E435", {"start": v(-234.56, 515.55) * mm, "end": v(-242.1, 517.57) * mm});
            skLineSegment(sketch, "E436", {"start": v(-252.18, 542.3) * mm, "end": v(-252.18, 546.2) * mm});
            skLineSegment(sketch, "E437", {"start": v(-252.18, 546.2) * mm, "end": v(-244.47, 546.2) * mm});
            skLineSegment(sketch, "E438", {"start": v(-244.47, 546.2) * mm, "end": v(-244.47, 542.3) * mm});
            skLineSegment(sketch, "E439", {"start": v(-244.47, 542.3) * mm, "end": v(-252.18, 542.3) * mm});
            skLineSegment(sketch, "E440", {"start": v(-181.72, 516.6) * mm, "end": v(-181.72, 544.7) * mm});
            skLineSegment(sketch, "E441", {"start": v(-181.72, 544.7) * mm, "end": v(-174.1, 544.7) * mm});
            skLineSegment(sketch, "E442", {"start": v(-174.1, 544.7) * mm, "end": v(-174.24, 542.5) * mm});
            skLineSegment(sketch, "E443", {"start": v(-174.24, 542.5) * mm, "end": v(-173.19, 543.66) * mm});
            skLineSegment(sketch, "E444", {"start": v(-173.19, 543.66) * mm, "end": v(-172.03, 544.48) * mm});
            skLineSegment(sketch, "E445", {"start": v(-172.03, 544.48) * mm, "end": v(-170.77, 544.97) * mm});
            skLineSegment(sketch, "E446", {"start": v(-170.77, 544.97) * mm, "end": v(-169.4, 545.13) * mm});
            skLineSegment(sketch, "E447", {"start": v(-169.4, 545.13) * mm, "end": v(-167.78, 544.9) * mm});
            skLineSegment(sketch, "E448", {"start": v(-167.78, 544.9) * mm, "end": v(-166.4, 544.2) * mm});
            skLineSegment(sketch, "E449", {"start": v(-166.4, 544.2) * mm, "end": v(-165.36, 543.2) * mm});
            skLineSegment(sketch, "E450", {"start": v(-165.36, 543.2) * mm, "end": v(-164.8, 542.04) * mm});
            skLineSegment(sketch, "E451", {"start": v(-164.8, 542.04) * mm, "end": v(-164.5, 537.9) * mm});
            skLineSegment(sketch, "E452", {"start": v(-164.5, 537.9) * mm, "end": v(-164.5, 527.53) * mm});
            skLineSegment(sketch, "E453", {"start": v(-164.5, 527.53) * mm, "end": v(-164.6, 524.66) * mm});
            skLineSegment(sketch, "E454", {"start": v(-164.6, 524.66) * mm, "end": v(-164.89, 522.76) * mm});
            skLineSegment(sketch, "E455", {"start": v(-164.89, 522.76) * mm, "end": v(-165.5, 521.48) * mm});
            skLineSegment(sketch, "E456", {"start": v(-165.5, 521.48) * mm, "end": v(-166.52, 520.5) * mm});
            skLineSegment(sketch, "E457", {"start": v(-166.52, 520.5) * mm, "end": v(-167.88, 519.86) * mm});
            skLineSegment(sketch, "E458", {"start": v(-167.88, 519.86) * mm, "end": v(-169.5, 519.65) * mm});
            skLineSegment(sketch, "E459", {"start": v(-169.5, 519.65) * mm, "end": v(-170.83, 519.8) * mm});
            skLineSegment(sketch, "E460", {"start": v(-170.83, 519.8) * mm, "end": v(-172.07, 520.3) * mm});
            skLineSegment(sketch, "E461", {"start": v(-172.07, 520.3) * mm, "end": v(-173.2, 521.11) * mm});
            skLineSegment(sketch, "E462", {"start": v(-173.2, 521.11) * mm, "end": v(-174.24, 522.23) * mm});
            skLineSegment(sketch, "E463", {"start": v(-174.24, 522.23) * mm, "end": v(-174.24, 516.6) * mm});
            skLineSegment(sketch, "E464", {"start": v(-174.24, 516.6) * mm, "end": v(-181.72, 516.6) * mm});
            skLineSegment(sketch, "E465", {"start": v(-172.47, 525.23) * mm, "end": v(-172.15, 525.62) * mm});
            skLineSegment(sketch, "E466", {"start": v(-172.15, 525.62) * mm, "end": v(-172, 527.75) * mm});
            skLineSegment(sketch, "E467", {"start": v(-172, 527.75) * mm, "end": v(-172, 536.82) * mm});
            skLineSegment(sketch, "E468", {"start": v(-172, 536.82) * mm, "end": v(-172.14, 539.2) * mm});
            skLineSegment(sketch, "E469", {"start": v(-172.14, 539.2) * mm, "end": v(-172.46, 539.56) * mm});
            skLineSegment(sketch, "E470", {"start": v(-172.46, 539.56) * mm, "end": v(-173.07, 539.68) * mm});
            skLineSegment(sketch, "E471", {"start": v(-173.07, 539.68) * mm, "end": v(-173.68, 539.54) * mm});
            skLineSegment(sketch, "E472", {"start": v(-173.68, 539.54) * mm, "end": v(-174.02, 539.12) * mm});
            skLineSegment(sketch, "E473", {"start": v(-174.02, 539.12) * mm, "end": v(-174.2, 536.81) * mm});
            skLineSegment(sketch, "E474", {"start": v(-174.2, 536.81) * mm, "end": v(-174.2, 528.05) * mm});
            skLineSegment(sketch, "E475", {"start": v(-174.2, 528.05) * mm, "end": v(-174.02, 525.66) * mm});
            skLineSegment(sketch, "E476", {"start": v(-174.02, 525.66) * mm, "end": v(-173.66, 525.25) * mm});
            skLineSegment(sketch, "E477", {"start": v(-173.66, 525.25) * mm, "end": v(-173.05, 525.11) * mm});
            skLineSegment(sketch, "E478", {"start": v(-173.05, 525.11) * mm, "end": v(-172.47, 525.23) * mm});
            skLineSegment(sketch, "E479", {"start": v(-145.28, 519.82) * mm, "end": v(-147.24, 520.34) * mm});
            skLineSegment(sketch, "E480", {"start": v(-147.24, 520.34) * mm, "end": v(-148.85, 521.15) * mm});
            skLineSegment(sketch, "E481", {"start": v(-148.85, 521.15) * mm, "end": v(-150.06, 522.22) * mm});
            skLineSegment(sketch, "E482", {"start": v(-150.06, 522.22) * mm, "end": v(-150.92, 523.47) * mm});
            skLineSegment(sketch, "E483", {"start": v(-150.92, 523.47) * mm, "end": v(-151.46, 524.85) * mm});
            skLineSegment(sketch, "E484", {"start": v(-151.46, 524.85) * mm, "end": v(-151.76, 526.6) * mm});
            skLineSegment(sketch, "E485", {"start": v(-151.76, 526.6) * mm, "end": v(-151.85, 529.03) * mm});
            skLineSegment(sketch, "E486", {"start": v(-151.85, 529.03) * mm, "end": v(-151.85, 536.2) * mm});
            skLineSegment(sketch, "E487", {"start": v(-151.85, 536.2) * mm, "end": v(-151.64, 539.08) * mm});
            skLineSegment(sketch, "E488", {"start": v(-151.64, 539.08) * mm, "end": v(-150.98, 541.3) * mm});
            skLineSegment(sketch, "E489", {"start": v(-150.98, 541.3) * mm, "end": v(-149.83, 542.93) * mm});
            skLineSegment(sketch, "E490", {"start": v(-149.83, 542.93) * mm, "end": v(-148.13, 544.14) * mm});
            skLineSegment(sketch, "E491", {"start": v(-148.13, 544.14) * mm, "end": v(-146, 544.88) * mm});
            skLineSegment(sketch, "E492", {"start": v(-146, 544.88) * mm, "end": v(-143.57, 545.13) * mm});
            skLineSegment(sketch, "E493", {"start": v(-143.57, 545.13) * mm, "end": v(-140.7, 544.83) * mm});
            skLineSegment(sketch, "E494", {"start": v(-140.7, 544.83) * mm, "end": v(-138.37, 543.94) * mm});
            skLineSegment(sketch, "E495", {"start": v(-138.37, 543.94) * mm, "end": v(-136.63, 542.55) * mm});
            skLineSegment(sketch, "E496", {"start": v(-136.63, 542.55) * mm, "end": v(-135.5, 540.77) * mm});
            skLineSegment(sketch, "E497", {"start": v(-135.5, 540.77) * mm, "end": v(-134.88, 538.4) * mm});
            skLineSegment(sketch, "E498", {"start": v(-134.88, 538.4) * mm, "end": v(-134.68, 535.22) * mm});
            skLineSegment(sketch, "E499", {"start": v(-134.68, 535.22) * mm, "end": v(-134.68, 531.96) * mm});
            skLineSegment(sketch, "E500", {"start": v(-134.68, 531.96) * mm, "end": v(-144.37, 531.96) * mm});
            skLineSegment(sketch, "E501", {"start": v(-144.37, 531.96) * mm, "end": v(-144.37, 526.64) * mm});
            skLineSegment(sketch, "E502", {"start": v(-144.37, 526.64) * mm, "end": v(-144.13, 524.5) * mm});
            skLineSegment(sketch, "E503", {"start": v(-144.13, 524.5) * mm, "end": v(-143.77, 524.13) * mm});
            skLineSegment(sketch, "E504", {"start": v(-143.77, 524.13) * mm, "end": v(-143.2, 524) * mm});
            skLineSegment(sketch, "E505", {"start": v(-143.2, 524) * mm, "end": v(-142.49, 524.17) * mm});
            skLineSegment(sketch, "E506", {"start": v(-142.49, 524.17) * mm, "end": v(-142.06, 524.65) * mm});
            skLineSegment(sketch, "E507", {"start": v(-142.06, 524.65) * mm, "end": v(-141.77, 527.12) * mm});
            skLineSegment(sketch, "E508", {"start": v(-141.77, 527.12) * mm, "end": v(-141.77, 530.36) * mm});
            skLineSegment(sketch, "E509", {"start": v(-141.77, 530.36) * mm, "end": v(-134.68, 530.36) * mm});
            skLineSegment(sketch, "E510", {"start": v(-134.68, 530.36) * mm, "end": v(-134.68, 528.55) * mm});
            skLineSegment(sketch, "E511", {"start": v(-134.68, 528.55) * mm, "end": v(-134.96, 525.04) * mm});
            skLineSegment(sketch, "E512", {"start": v(-134.96, 525.04) * mm, "end": v(-135.44, 523.78) * mm});
            skLineSegment(sketch, "E513", {"start": v(-135.44, 523.78) * mm, "end": v(-136.3, 522.43) * mm});
            skLineSegment(sketch, "E514", {"start": v(-136.3, 522.43) * mm, "end": v(-137.5, 521.22) * mm});
            skLineSegment(sketch, "E515", {"start": v(-137.5, 521.22) * mm, "end": v(-138.98, 520.35) * mm});
            skLineSegment(sketch, "E516", {"start": v(-138.98, 520.35) * mm, "end": v(-140.81, 519.83) * mm});
            skLineSegment(sketch, "E517", {"start": v(-140.81, 519.83) * mm, "end": v(-143.05, 519.65) * mm});
            skLineSegment(sketch, "E518", {"start": v(-143.05, 519.65) * mm, "end": v(-145.28, 519.82) * mm});
            skLineSegment(sketch, "E519", {"start": v(-142.18, 537.76) * mm, "end": v(-142.38, 540.22) * mm});
            skLineSegment(sketch, "E520", {"start": v(-142.38, 540.22) * mm, "end": v(-142.7, 540.64) * mm});
            skLineSegment(sketch, "E521", {"start": v(-142.7, 540.64) * mm, "end": v(-143.22, 540.78) * mm});
            skLineSegment(sketch, "E522", {"start": v(-143.22, 540.78) * mm, "end": v(-143.85, 540.66) * mm});
            skLineSegment(sketch, "E523", {"start": v(-143.85, 540.66) * mm, "end": v(-144.18, 540.3) * mm});
            skLineSegment(sketch, "E524", {"start": v(-144.18, 540.3) * mm, "end": v(-144.37, 537.76) * mm});
            skLineSegment(sketch, "E525", {"start": v(-144.37, 537.76) * mm, "end": v(-144.37, 535.96) * mm});
            skLineSegment(sketch, "E526", {"start": v(-144.37, 535.96) * mm, "end": v(-142.18, 535.96) * mm});
            skLineSegment(sketch, "E527", {"start": v(-142.18, 535.96) * mm, "end": v(-142.18, 537.76) * mm});
            skLineSegment(sketch, "E528", {"start": v(-162.03, 520.1) * mm, "end": v(-162.03, 544.7) * mm});
            skLineSegment(sketch, "E529", {"start": v(-162.03, 544.7) * mm, "end": v(-154.32, 544.7) * mm});
            skLineSegment(sketch, "E530", {"start": v(-154.32, 544.7) * mm, "end": v(-154.32, 520.1) * mm});
            skLineSegment(sketch, "E531", {"start": v(-154.32, 520.1) * mm, "end": v(-162.03, 520.1) * mm});
            skLineSegment(sketch, "E532", {"start": v(-252.18, 516.2) * mm, "end": v(-252.18, 540.8) * mm});
            skLineSegment(sketch, "E533", {"start": v(-252.18, 540.8) * mm, "end": v(-244.47, 540.8) * mm});
            skLineSegment(sketch, "E534", {"start": v(-244.47, 540.8) * mm, "end": v(-244.47, 516.2) * mm});
            skLineSegment(sketch, "E535", {"start": v(-244.47, 516.2) * mm, "end": v(-252.18, 516.2) * mm});
            skLineSegment(sketch, "E536", {"start": v(-378, 483) * mm, "end": v(-378, 503) * mm});
            skLineSegment(sketch, "E537", {"start": v(-378, 503) * mm, "end": v(-362, 503) * mm});
            skLineSegment(sketch, "E538", {"start": v(-362, 503) * mm, "end": v(-362, 483) * mm});
            skLineSegment(sketch, "E539", {"start": v(-362, 483) * mm, "end": v(-378, 483) * mm});
            skLineSegment(sketch, "E540", {"start": v(-48, 483) * mm, "end": v(-48, 503) * mm});
            skLineSegment(sketch, "E541", {"start": v(-48, 503) * mm, "end": v(-32, 503) * mm});
            skLineSegment(sketch, "E542", {"start": v(-32, 503) * mm, "end": v(-32, 483) * mm});
            skLineSegment(sketch, "E543", {"start": v(-32, 483) * mm, "end": v(-48, 483) * mm});
            skLineSegment(sketch, "E544", {"start": v(-40.13, 421) * mm, "end": v(-40.37, 421.04) * mm});
            skLineSegment(sketch, "E545", {"start": v(-40.37, 421.04) * mm, "end": v(-40.62, 421.1) * mm});
            skLineSegment(sketch, "E546", {"start": v(-40.62, 421.1) * mm, "end": v(-40.85, 421.2) * mm});
            skLineSegment(sketch, "E547", {"start": v(-40.85, 421.2) * mm, "end": v(-41.07, 421.31) * mm});
            skLineSegment(sketch, "E548", {"start": v(-41.07, 421.31) * mm, "end": v(-41.27, 421.46) * mm});
            skLineSegment(sketch, "E549", {"start": v(-41.27, 421.46) * mm, "end": v(-41.46, 421.63) * mm});
            skLineSegment(sketch, "E550", {"start": v(-41.46, 421.63) * mm, "end": v(-41.62, 421.82) * mm});
            skLineSegment(sketch, "E551", {"start": v(-41.62, 421.82) * mm, "end": v(-41.75, 422.04) * mm});
            skLineSegment(sketch, "E552", {"start": v(-41.75, 422.04) * mm, "end": v(-41.86, 422.26) * mm});
            skLineSegment(sketch, "E553", {"start": v(-41.86, 422.26) * mm, "end": v(-41.94, 422.5) * mm});
            skLineSegment(sketch, "E554", {"start": v(-41.94, 422.5) * mm, "end": v(-41.98, 422.75) * mm});
            skLineSegment(sketch, "E555", {"start": v(-41.98, 422.75) * mm, "end": v(-42, 423) * mm});
            skLineSegment(sketch, "E556", {"start": v(-42, 423) * mm, "end": v(-41.98, 423.25) * mm});
            skLineSegment(sketch, "E557", {"start": v(-41.98, 423.25) * mm, "end": v(-41.94, 423.5) * mm});
            skLineSegment(sketch, "E558", {"start": v(-41.94, 423.5) * mm, "end": v(-41.86, 423.74) * mm});
            skLineSegment(sketch, "E559", {"start": v(-41.86, 423.74) * mm, "end": v(-41.75, 423.96) * mm});
            skLineSegment(sketch, "E560", {"start": v(-41.75, 423.96) * mm, "end": v(-41.62, 424.18) * mm});
            skLineSegment(sketch, "E561", {"start": v(-41.62, 424.18) * mm, "end": v(-41.46, 424.37) * mm});
            skLineSegment(sketch, "E562", {"start": v(-41.46, 424.37) * mm, "end": v(-41.27, 424.54) * mm});
            skLineSegment(sketch, "E563", {"start": v(-41.27, 424.54) * mm, "end": v(-41.07, 424.69) * mm});
            skLineSegment(sketch, "E564", {"start": v(-41.07, 424.69) * mm, "end": v(-40.85, 424.8) * mm});
            skLineSegment(sketch, "E565", {"start": v(-40.85, 424.8) * mm, "end": v(-40.62, 424.9) * mm});
            skLineSegment(sketch, "E566", {"start": v(-40.62, 424.9) * mm, "end": v(-40.37, 424.96) * mm});
            skLineSegment(sketch, "E567", {"start": v(-40.37, 424.96) * mm, "end": v(-40.13, 425) * mm});
            skLineSegment(sketch, "E568", {"start": v(-40.13, 425) * mm, "end": v(-39.87, 425) * mm});
            skLineSegment(sketch, "E569", {"start": v(-39.87, 425) * mm, "end": v(-39.63, 424.96) * mm});
            skLineSegment(sketch, "E570", {"start": v(-39.63, 424.96) * mm, "end": v(-39.38, 424.9) * mm});
            skLineSegment(sketch, "E571", {"start": v(-39.38, 424.9) * mm, "end": v(-39.15, 424.8) * mm});
            skLineSegment(sketch, "E572", {"start": v(-39.15, 424.8) * mm, "end": v(-38.93, 424.69) * mm});
            skLineSegment(sketch, "E573", {"start": v(-38.93, 424.69) * mm, "end": v(-38.73, 424.54) * mm});
            skLineSegment(sketch, "E574", {"start": v(-38.73, 424.54) * mm, "end": v(-38.54, 424.37) * mm});
            skLineSegment(sketch, "E575", {"start": v(-38.54, 424.37) * mm, "end": v(-38.38, 424.18) * mm});
            skLineSegment(sketch, "E576", {"start": v(-38.38, 424.18) * mm, "end": v(-38.25, 423.96) * mm});
            skLineSegment(sketch, "E577", {"start": v(-38.25, 423.96) * mm, "end": v(-38.14, 423.74) * mm});
            skLineSegment(sketch, "E578", {"start": v(-38.14, 423.74) * mm, "end": v(-38.06, 423.5) * mm});
            skLineSegment(sketch, "E579", {"start": v(-38.06, 423.5) * mm, "end": v(-38.02, 423.25) * mm});
            skLineSegment(sketch, "E580", {"start": v(-38.02, 423.25) * mm, "end": v(-38, 423) * mm});
            skLineSegment(sketch, "E581", {"start": v(-38, 423) * mm, "end": v(-38.02, 422.75) * mm});
            skLineSegment(sketch, "E582", {"start": v(-38.02, 422.75) * mm, "end": v(-38.06, 422.5) * mm});
            skLineSegment(sketch, "E583", {"start": v(-38.06, 422.5) * mm, "end": v(-38.14, 422.26) * mm});
            skLineSegment(sketch, "E584", {"start": v(-38.14, 422.26) * mm, "end": v(-38.25, 422.04) * mm});
            skLineSegment(sketch, "E585", {"start": v(-38.25, 422.04) * mm, "end": v(-38.38, 421.82) * mm});
            skLineSegment(sketch, "E586", {"start": v(-38.38, 421.82) * mm, "end": v(-38.54, 421.63) * mm});
            skLineSegment(sketch, "E587", {"start": v(-38.54, 421.63) * mm, "end": v(-38.73, 421.46) * mm});
            skLineSegment(sketch, "E588", {"start": v(-38.73, 421.46) * mm, "end": v(-38.93, 421.31) * mm});
            skLineSegment(sketch, "E589", {"start": v(-38.93, 421.31) * mm, "end": v(-39.15, 421.2) * mm});
            skLineSegment(sketch, "E590", {"start": v(-39.15, 421.2) * mm, "end": v(-39.38, 421.1) * mm});
            skLineSegment(sketch, "E591", {"start": v(-39.38, 421.1) * mm, "end": v(-39.63, 421.04) * mm});
            skLineSegment(sketch, "E592", {"start": v(-39.63, 421.04) * mm, "end": v(-39.87, 421) * mm});
            skLineSegment(sketch, "E593", {"start": v(-39.87, 421) * mm, "end": v(-40.13, 421) * mm});
            skLineSegment(sketch, "E594", {"start": v(-370.13, 421) * mm, "end": v(-370.38, 421.04) * mm});
            skLineSegment(sketch, "E595", {"start": v(-370.38, 421.04) * mm, "end": v(-370.62, 421.1) * mm});
            skLineSegment(sketch, "E596", {"start": v(-370.62, 421.1) * mm, "end": v(-370.85, 421.2) * mm});
            skLineSegment(sketch, "E597", {"start": v(-370.85, 421.2) * mm, "end": v(-371.07, 421.31) * mm});
            skLineSegment(sketch, "E598", {"start": v(-371.07, 421.31) * mm, "end": v(-371.27, 421.46) * mm});
            skLineSegment(sketch, "E599", {"start": v(-371.27, 421.46) * mm, "end": v(-371.46, 421.63) * mm});
            skLineSegment(sketch, "E600", {"start": v(-371.46, 421.63) * mm, "end": v(-371.62, 421.82) * mm});
            skLineSegment(sketch, "E601", {"start": v(-371.62, 421.82) * mm, "end": v(-371.75, 422.04) * mm});
            skLineSegment(sketch, "E602", {"start": v(-371.75, 422.04) * mm, "end": v(-371.86, 422.26) * mm});
            skLineSegment(sketch, "E603", {"start": v(-371.86, 422.26) * mm, "end": v(-371.94, 422.5) * mm});
            skLineSegment(sketch, "E604", {"start": v(-371.94, 422.5) * mm, "end": v(-371.98, 422.75) * mm});
            skLineSegment(sketch, "E605", {"start": v(-371.98, 422.75) * mm, "end": v(-372, 423) * mm});
            skLineSegment(sketch, "E606", {"start": v(-372, 423) * mm, "end": v(-371.98, 423.25) * mm});
            skLineSegment(sketch, "E607", {"start": v(-371.98, 423.25) * mm, "end": v(-371.94, 423.5) * mm});
            skLineSegment(sketch, "E608", {"start": v(-371.94, 423.5) * mm, "end": v(-371.86, 423.74) * mm});
            skLineSegment(sketch, "E609", {"start": v(-371.86, 423.74) * mm, "end": v(-371.75, 423.96) * mm});
            skLineSegment(sketch, "E610", {"start": v(-371.75, 423.96) * mm, "end": v(-371.62, 424.18) * mm});
            skLineSegment(sketch, "E611", {"start": v(-371.62, 424.18) * mm, "end": v(-371.46, 424.37) * mm});
            skLineSegment(sketch, "E612", {"start": v(-371.46, 424.37) * mm, "end": v(-371.27, 424.54) * mm});
            skLineSegment(sketch, "E613", {"start": v(-371.27, 424.54) * mm, "end": v(-371.07, 424.69) * mm});
            skLineSegment(sketch, "E614", {"start": v(-371.07, 424.69) * mm, "end": v(-370.85, 424.8) * mm});
            skLineSegment(sketch, "E615", {"start": v(-370.85, 424.8) * mm, "end": v(-370.62, 424.9) * mm});
            skLineSegment(sketch, "E616", {"start": v(-370.62, 424.9) * mm, "end": v(-370.38, 424.96) * mm});
            skLineSegment(sketch, "E617", {"start": v(-370.38, 424.96) * mm, "end": v(-370.13, 425) * mm});
            skLineSegment(sketch, "E618", {"start": v(-370.13, 425) * mm, "end": v(-369.87, 425) * mm});
            skLineSegment(sketch, "E619", {"start": v(-369.87, 425) * mm, "end": v(-369.62, 424.96) * mm});
            skLineSegment(sketch, "E620", {"start": v(-369.62, 424.96) * mm, "end": v(-369.38, 424.9) * mm});
            skLineSegment(sketch, "E621", {"start": v(-369.38, 424.9) * mm, "end": v(-369.15, 424.8) * mm});
            skLineSegment(sketch, "E622", {"start": v(-369.15, 424.8) * mm, "end": v(-368.93, 424.69) * mm});
            skLineSegment(sketch, "E623", {"start": v(-368.93, 424.69) * mm, "end": v(-368.73, 424.54) * mm});
            skLineSegment(sketch, "E624", {"start": v(-368.73, 424.54) * mm, "end": v(-368.54, 424.37) * mm});
            skLineSegment(sketch, "E625", {"start": v(-368.54, 424.37) * mm, "end": v(-368.38, 424.18) * mm});
            skLineSegment(sketch, "E626", {"start": v(-368.38, 424.18) * mm, "end": v(-368.25, 423.96) * mm});
            skLineSegment(sketch, "E627", {"start": v(-368.25, 423.96) * mm, "end": v(-368.14, 423.74) * mm});
            skLineSegment(sketch, "E628", {"start": v(-368.14, 423.74) * mm, "end": v(-368.06, 423.5) * mm});
            skLineSegment(sketch, "E629", {"start": v(-368.06, 423.5) * mm, "end": v(-368.02, 423.25) * mm});
            skLineSegment(sketch, "E630", {"start": v(-368.02, 423.25) * mm, "end": v(-368, 423) * mm});
            skLineSegment(sketch, "E631", {"start": v(-368, 423) * mm, "end": v(-368.02, 422.75) * mm});
            skLineSegment(sketch, "E632", {"start": v(-368.02, 422.75) * mm, "end": v(-368.06, 422.5) * mm});
            skLineSegment(sketch, "E633", {"start": v(-368.06, 422.5) * mm, "end": v(-368.14, 422.26) * mm});
            skLineSegment(sketch, "E634", {"start": v(-368.14, 422.26) * mm, "end": v(-368.25, 422.04) * mm});
            skLineSegment(sketch, "E635", {"start": v(-368.25, 422.04) * mm, "end": v(-368.38, 421.82) * mm});
            skLineSegment(sketch, "E636", {"start": v(-368.38, 421.82) * mm, "end": v(-368.54, 421.63) * mm});
            skLineSegment(sketch, "E637", {"start": v(-368.54, 421.63) * mm, "end": v(-368.73, 421.46) * mm});
            skLineSegment(sketch, "E638", {"start": v(-368.73, 421.46) * mm, "end": v(-368.93, 421.31) * mm});
            skLineSegment(sketch, "E639", {"start": v(-368.93, 421.31) * mm, "end": v(-369.15, 421.2) * mm});
            skLineSegment(sketch, "E640", {"start": v(-369.15, 421.2) * mm, "end": v(-369.38, 421.1) * mm});
            skLineSegment(sketch, "E641", {"start": v(-369.38, 421.1) * mm, "end": v(-369.62, 421.04) * mm});
            skLineSegment(sketch, "E642", {"start": v(-369.62, 421.04) * mm, "end": v(-369.87, 421) * mm});
            skLineSegment(sketch, "E643", {"start": v(-369.87, 421) * mm, "end": v(-370.13, 421) * mm});
            skLineSegment(sketch, "E644", {"start": v(-48, 343) * mm, "end": v(-48, 363) * mm});
            skLineSegment(sketch, "E645", {"start": v(-48, 363) * mm, "end": v(-32, 363) * mm});
            skLineSegment(sketch, "E646", {"start": v(-32, 363) * mm, "end": v(-32, 343) * mm});
            skLineSegment(sketch, "E647", {"start": v(-32, 343) * mm, "end": v(-48, 343) * mm});
            skLineSegment(sketch, "E648", {"start": v(-378, 343) * mm, "end": v(-378, 363) * mm});
            skLineSegment(sketch, "E649", {"start": v(-378, 363) * mm, "end": v(-362, 363) * mm});
            skLineSegment(sketch, "E650", {"start": v(-362, 363) * mm, "end": v(-362, 343) * mm});
            skLineSegment(sketch, "E651", {"start": v(-362, 343) * mm, "end": v(-378, 343) * mm});
            skLineSegment(sketch, "E652", {"start": v(-370.13, 281) * mm, "end": v(-370.38, 281.04) * mm});
            skLineSegment(sketch, "E653", {"start": v(-370.38, 281.04) * mm, "end": v(-370.62, 281.1) * mm});
            skLineSegment(sketch, "E654", {"start": v(-370.62, 281.1) * mm, "end": v(-370.85, 281.2) * mm});
            skLineSegment(sketch, "E655", {"start": v(-370.85, 281.2) * mm, "end": v(-371.07, 281.31) * mm});
            skLineSegment(sketch, "E656", {"start": v(-371.07, 281.31) * mm, "end": v(-371.27, 281.46) * mm});
            skLineSegment(sketch, "E657", {"start": v(-371.27, 281.46) * mm, "end": v(-371.46, 281.63) * mm});
            skLineSegment(sketch, "E658", {"start": v(-371.46, 281.63) * mm, "end": v(-371.62, 281.82) * mm});
            skLineSegment(sketch, "E659", {"start": v(-371.62, 281.82) * mm, "end": v(-371.75, 282.04) * mm});
            skLineSegment(sketch, "E660", {"start": v(-371.75, 282.04) * mm, "end": v(-371.86, 282.26) * mm});
            skLineSegment(sketch, "E661", {"start": v(-371.86, 282.26) * mm, "end": v(-371.94, 282.5) * mm});
            skLineSegment(sketch, "E662", {"start": v(-371.94, 282.5) * mm, "end": v(-371.98, 282.75) * mm});
            skLineSegment(sketch, "E663", {"start": v(-371.98, 282.75) * mm, "end": v(-372, 283) * mm});
            skLineSegment(sketch, "E664", {"start": v(-372, 283) * mm, "end": v(-371.98, 283.25) * mm});
            skLineSegment(sketch, "E665", {"start": v(-371.98, 283.25) * mm, "end": v(-371.94, 283.5) * mm});
            skLineSegment(sketch, "E666", {"start": v(-371.94, 283.5) * mm, "end": v(-371.86, 283.74) * mm});
            skLineSegment(sketch, "E667", {"start": v(-371.86, 283.74) * mm, "end": v(-371.75, 283.96) * mm});
            skLineSegment(sketch, "E668", {"start": v(-371.75, 283.96) * mm, "end": v(-371.62, 284.18) * mm});
            skLineSegment(sketch, "E669", {"start": v(-371.62, 284.18) * mm, "end": v(-371.46, 284.37) * mm});
            skLineSegment(sketch, "E670", {"start": v(-371.46, 284.37) * mm, "end": v(-371.27, 284.54) * mm});
            skLineSegment(sketch, "E671", {"start": v(-371.27, 284.54) * mm, "end": v(-371.07, 284.69) * mm});
            skLineSegment(sketch, "E672", {"start": v(-371.07, 284.69) * mm, "end": v(-370.85, 284.8) * mm});
            skLineSegment(sketch, "E673", {"start": v(-370.85, 284.8) * mm, "end": v(-370.62, 284.9) * mm});
            skLineSegment(sketch, "E674", {"start": v(-370.62, 284.9) * mm, "end": v(-370.38, 284.96) * mm});
            skLineSegment(sketch, "E675", {"start": v(-370.38, 284.96) * mm, "end": v(-370.13, 285) * mm});
            skLineSegment(sketch, "E676", {"start": v(-370.13, 285) * mm, "end": v(-369.87, 285) * mm});
            skLineSegment(sketch, "E677", {"start": v(-369.87, 285) * mm, "end": v(-369.62, 284.96) * mm});
            skLineSegment(sketch, "E678", {"start": v(-369.62, 284.96) * mm, "end": v(-369.38, 284.9) * mm});
            skLineSegment(sketch, "E679", {"start": v(-369.38, 284.9) * mm, "end": v(-369.15, 284.8) * mm});
            skLineSegment(sketch, "E680", {"start": v(-369.15, 284.8) * mm, "end": v(-368.93, 284.69) * mm});
            skLineSegment(sketch, "E681", {"start": v(-368.93, 284.69) * mm, "end": v(-368.73, 284.54) * mm});
            skLineSegment(sketch, "E682", {"start": v(-368.73, 284.54) * mm, "end": v(-368.54, 284.37) * mm});
            skLineSegment(sketch, "E683", {"start": v(-368.54, 284.37) * mm, "end": v(-368.38, 284.18) * mm});
            skLineSegment(sketch, "E684", {"start": v(-368.38, 284.18) * mm, "end": v(-368.25, 283.96) * mm});
            skLineSegment(sketch, "E685", {"start": v(-368.25, 283.96) * mm, "end": v(-368.14, 283.74) * mm});
            skLineSegment(sketch, "E686", {"start": v(-368.14, 283.74) * mm, "end": v(-368.06, 283.5) * mm});
            skLineSegment(sketch, "E687", {"start": v(-368.06, 283.5) * mm, "end": v(-368.02, 283.25) * mm});
            skLineSegment(sketch, "E688", {"start": v(-368.02, 283.25) * mm, "end": v(-368, 283) * mm});
            skLineSegment(sketch, "E689", {"start": v(-368, 283) * mm, "end": v(-368.02, 282.75) * mm});
            skLineSegment(sketch, "E690", {"start": v(-368.02, 282.75) * mm, "end": v(-368.06, 282.5) * mm});
            skLineSegment(sketch, "E691", {"start": v(-368.06, 282.5) * mm, "end": v(-368.14, 282.26) * mm});
            skLineSegment(sketch, "E692", {"start": v(-368.14, 282.26) * mm, "end": v(-368.25, 282.04) * mm});
            skLineSegment(sketch, "E693", {"start": v(-368.25, 282.04) * mm, "end": v(-368.38, 281.82) * mm});
            skLineSegment(sketch, "E694", {"start": v(-368.38, 281.82) * mm, "end": v(-368.54, 281.63) * mm});
            skLineSegment(sketch, "E695", {"start": v(-368.54, 281.63) * mm, "end": v(-368.73, 281.46) * mm});
            skLineSegment(sketch, "E696", {"start": v(-368.73, 281.46) * mm, "end": v(-368.93, 281.31) * mm});
            skLineSegment(sketch, "E697", {"start": v(-368.93, 281.31) * mm, "end": v(-369.15, 281.2) * mm});
            skLineSegment(sketch, "E698", {"start": v(-369.15, 281.2) * mm, "end": v(-369.38, 281.1) * mm});
            skLineSegment(sketch, "E699", {"start": v(-369.38, 281.1) * mm, "end": v(-369.62, 281.04) * mm});
            skLineSegment(sketch, "E700", {"start": v(-369.62, 281.04) * mm, "end": v(-369.87, 281) * mm});
            skLineSegment(sketch, "E701", {"start": v(-369.87, 281) * mm, "end": v(-370.13, 281) * mm});
            skLineSegment(sketch, "E702", {"start": v(-40.13, 281) * mm, "end": v(-40.37, 281.04) * mm});
            skLineSegment(sketch, "E703", {"start": v(-40.37, 281.04) * mm, "end": v(-40.62, 281.1) * mm});
            skLineSegment(sketch, "E704", {"start": v(-40.62, 281.1) * mm, "end": v(-40.85, 281.2) * mm});
            skLineSegment(sketch, "E705", {"start": v(-40.85, 281.2) * mm, "end": v(-41.07, 281.31) * mm});
            skLineSegment(sketch, "E706", {"start": v(-41.07, 281.31) * mm, "end": v(-41.27, 281.46) * mm});
            skLineSegment(sketch, "E707", {"start": v(-41.27, 281.46) * mm, "end": v(-41.46, 281.63) * mm});
            skLineSegment(sketch, "E708", {"start": v(-41.46, 281.63) * mm, "end": v(-41.62, 281.82) * mm});
            skLineSegment(sketch, "E709", {"start": v(-41.62, 281.82) * mm, "end": v(-41.75, 282.04) * mm});
            skLineSegment(sketch, "E710", {"start": v(-41.75, 282.04) * mm, "end": v(-41.86, 282.26) * mm});
            skLineSegment(sketch, "E711", {"start": v(-41.86, 282.26) * mm, "end": v(-41.94, 282.5) * mm});
            skLineSegment(sketch, "E712", {"start": v(-41.94, 282.5) * mm, "end": v(-41.98, 282.75) * mm});
            skLineSegment(sketch, "E713", {"start": v(-41.98, 282.75) * mm, "end": v(-42, 283) * mm});
            skLineSegment(sketch, "E714", {"start": v(-42, 283) * mm, "end": v(-41.98, 283.25) * mm});
            skLineSegment(sketch, "E715", {"start": v(-41.98, 283.25) * mm, "end": v(-41.94, 283.5) * mm});
            skLineSegment(sketch, "E716", {"start": v(-41.94, 283.5) * mm, "end": v(-41.86, 283.74) * mm});
            skLineSegment(sketch, "E717", {"start": v(-41.86, 283.74) * mm, "end": v(-41.75, 283.96) * mm});
            skLineSegment(sketch, "E718", {"start": v(-41.75, 283.96) * mm, "end": v(-41.62, 284.18) * mm});
            skLineSegment(sketch, "E719", {"start": v(-41.62, 284.18) * mm, "end": v(-41.46, 284.37) * mm});
            skLineSegment(sketch, "E720", {"start": v(-41.46, 284.37) * mm, "end": v(-41.27, 284.54) * mm});
            skLineSegment(sketch, "E721", {"start": v(-41.27, 284.54) * mm, "end": v(-41.07, 284.69) * mm});
            skLineSegment(sketch, "E722", {"start": v(-41.07, 284.69) * mm, "end": v(-40.85, 284.8) * mm});
            skLineSegment(sketch, "E723", {"start": v(-40.85, 284.8) * mm, "end": v(-40.62, 284.9) * mm});
            skLineSegment(sketch, "E724", {"start": v(-40.62, 284.9) * mm, "end": v(-40.37, 284.96) * mm});
            skLineSegment(sketch, "E725", {"start": v(-40.37, 284.96) * mm, "end": v(-40.13, 285) * mm});
            skLineSegment(sketch, "E726", {"start": v(-40.13, 285) * mm, "end": v(-39.87, 285) * mm});
            skLineSegment(sketch, "E727", {"start": v(-39.87, 285) * mm, "end": v(-39.63, 284.96) * mm});
            skLineSegment(sketch, "E728", {"start": v(-39.63, 284.96) * mm, "end": v(-39.38, 284.9) * mm});
            skLineSegment(sketch, "E729", {"start": v(-39.38, 284.9) * mm, "end": v(-39.15, 284.8) * mm});
            skLineSegment(sketch, "E730", {"start": v(-39.15, 284.8) * mm, "end": v(-38.93, 284.69) * mm});
            skLineSegment(sketch, "E731", {"start": v(-38.93, 284.69) * mm, "end": v(-38.73, 284.54) * mm});
            skLineSegment(sketch, "E732", {"start": v(-38.73, 284.54) * mm, "end": v(-38.54, 284.37) * mm});
            skLineSegment(sketch, "E733", {"start": v(-38.54, 284.37) * mm, "end": v(-38.38, 284.18) * mm});
            skLineSegment(sketch, "E734", {"start": v(-38.38, 284.18) * mm, "end": v(-38.25, 283.96) * mm});
            skLineSegment(sketch, "E735", {"start": v(-38.25, 283.96) * mm, "end": v(-38.14, 283.74) * mm});
            skLineSegment(sketch, "E736", {"start": v(-38.14, 283.74) * mm, "end": v(-38.06, 283.5) * mm});
            skLineSegment(sketch, "E737", {"start": v(-38.06, 283.5) * mm, "end": v(-38.02, 283.25) * mm});
            skLineSegment(sketch, "E738", {"start": v(-38.02, 283.25) * mm, "end": v(-38, 283) * mm});
            skLineSegment(sketch, "E739", {"start": v(-38, 283) * mm, "end": v(-38.02, 282.75) * mm});
            skLineSegment(sketch, "E740", {"start": v(-38.02, 282.75) * mm, "end": v(-38.06, 282.5) * mm});
            skLineSegment(sketch, "E741", {"start": v(-38.06, 282.5) * mm, "end": v(-38.14, 282.26) * mm});
            skLineSegment(sketch, "E742", {"start": v(-38.14, 282.26) * mm, "end": v(-38.25, 282.04) * mm});
            skLineSegment(sketch, "E743", {"start": v(-38.25, 282.04) * mm, "end": v(-38.38, 281.82) * mm});
            skLineSegment(sketch, "E744", {"start": v(-38.38, 281.82) * mm, "end": v(-38.54, 281.63) * mm});
            skLineSegment(sketch, "E745", {"start": v(-38.54, 281.63) * mm, "end": v(-38.73, 281.46) * mm});
            skLineSegment(sketch, "E746", {"start": v(-38.73, 281.46) * mm, "end": v(-38.93, 281.31) * mm});
            skLineSegment(sketch, "E747", {"start": v(-38.93, 281.31) * mm, "end": v(-39.15, 281.2) * mm});
            skLineSegment(sketch, "E748", {"start": v(-39.15, 281.2) * mm, "end": v(-39.38, 281.1) * mm});
            skLineSegment(sketch, "E749", {"start": v(-39.38, 281.1) * mm, "end": v(-39.63, 281.04) * mm});
            skLineSegment(sketch, "E750", {"start": v(-39.63, 281.04) * mm, "end": v(-39.87, 281) * mm});
            skLineSegment(sketch, "E751", {"start": v(-39.87, 281) * mm, "end": v(-40.13, 281) * mm});
            skLineSegment(sketch, "E752", {"start": v(-378, 203) * mm, "end": v(-378, 223) * mm});
            skLineSegment(sketch, "E753", {"start": v(-378, 223) * mm, "end": v(-362, 223) * mm});
            skLineSegment(sketch, "E754", {"start": v(-362, 223) * mm, "end": v(-362, 203) * mm});
            skLineSegment(sketch, "E755", {"start": v(-362, 203) * mm, "end": v(-378, 203) * mm});
            skLineSegment(sketch, "E756", {"start": v(-48, 203) * mm, "end": v(-48, 223) * mm});
            skLineSegment(sketch, "E757", {"start": v(-48, 223) * mm, "end": v(-32, 223) * mm});
            skLineSegment(sketch, "E758", {"start": v(-32, 223) * mm, "end": v(-32, 203) * mm});
            skLineSegment(sketch, "E759", {"start": v(-32, 203) * mm, "end": v(-48, 203) * mm});
            skLineSegment(sketch, "E760", {"start": v(391.25, 123.08) * mm, "end": v(392.49, 123.31) * mm});
            skLineSegment(sketch, "E761", {"start": v(392.49, 123.31) * mm, "end": v(393.68, 123.7) * mm});
            skLineSegment(sketch, "E762", {"start": v(393.68, 123.7) * mm, "end": v(394.82, 124.24) * mm});
            skLineSegment(sketch, "E763", {"start": v(394.82, 124.24) * mm, "end": v(395.88, 124.9) * mm});
            skLineSegment(sketch, "E764", {"start": v(395.88, 124.9) * mm, "end": v(396.85, 125.7) * mm});
            skLineSegment(sketch, "E765", {"start": v(396.85, 125.7) * mm, "end": v(397.7, 126.63) * mm});
            skLineSegment(sketch, "E766", {"start": v(397.7, 126.63) * mm, "end": v(398.44, 127.64) * mm});
            skLineSegment(sketch, "E767", {"start": v(398.44, 127.64) * mm, "end": v(399.05, 128.74) * mm});
            skLineSegment(sketch, "E768", {"start": v(399.05, 128.74) * mm, "end": v(399.51, 129.9) * mm});
            skLineSegment(sketch, "E769", {"start": v(399.51, 129.9) * mm, "end": v(399.82, 131.13) * mm});
            skLineSegment(sketch, "E770", {"start": v(399.82, 131.13) * mm, "end": v(399.98, 132.37) * mm});
            skLineSegment(sketch, "E771", {"start": v(399.98, 132.37) * mm, "end": v(399.98, 133) * mm});
            skLineSegment(sketch, "E772", {"start": v(399.98, 133) * mm, "end": v(400, 133) * mm});
            skLineSegment(sketch, "E773", {"start": v(400, 133) * mm, "end": v(400, 409) * mm});
            skLineSegment(sketch, "E774", {"start": v(400, 409) * mm, "end": v(360, 409) * mm});
            skLineSegment(sketch, "E775", {"start": v(360, 409) * mm, "end": v(360, 425) * mm});
            skLineSegment(sketch, "E776", {"start": v(360, 425) * mm, "end": v(400, 425) * mm});
            skLineSegment(sketch, "E777", {"start": v(400, 425) * mm, "end": v(400, 553) * mm});
            skLineSegment(sketch, "E778", {"start": v(400, 553) * mm, "end": v(399.92, 554.25) * mm});
            skLineSegment(sketch, "E779", {"start": v(399.92, 554.25) * mm, "end": v(399.69, 555.5) * mm});
            skLineSegment(sketch, "E780", {"start": v(399.69, 555.5) * mm, "end": v(399.3, 556.68) * mm});
            skLineSegment(sketch, "E781", {"start": v(399.3, 556.68) * mm, "end": v(398.76, 557.82) * mm});
            skLineSegment(sketch, "E782", {"start": v(398.76, 557.82) * mm, "end": v(398.09, 558.88) * mm});
            skLineSegment(sketch, "E783", {"start": v(398.09, 558.88) * mm, "end": v(397.3, 559.85) * mm});
            skLineSegment(sketch, "E784", {"start": v(397.3, 559.85) * mm, "end": v(396.37, 560.7) * mm});
            skLineSegment(sketch, "E785", {"start": v(396.37, 560.7) * mm, "end": v(395.36, 561.44) * mm});
            skLineSegment(sketch, "E786", {"start": v(395.36, 561.44) * mm, "end": v(394.26, 562.05) * mm});
            skLineSegment(sketch, "E787", {"start": v(394.26, 562.05) * mm, "end": v(393.09, 562.5) * mm});
            skLineSegment(sketch, "E788", {"start": v(393.09, 562.5) * mm, "end": v(391.87, 562.82) * mm});
            skLineSegment(sketch, "E789", {"start": v(391.87, 562.82) * mm, "end": v(390.63, 562.98) * mm});
            skLineSegment(sketch, "E790", {"start": v(390.63, 562.98) * mm, "end": v(390, 562.98) * mm});
            skLineSegment(sketch, "E791", {"start": v(390, 562.98) * mm, "end": v(390, 563) * mm});
            skLineSegment(sketch, "E792", {"start": v(390, 563) * mm, "end": v(20, 563) * mm});
            skLineSegment(sketch, "E793", {"start": v(20, 563) * mm, "end": v(18.75, 562.92) * mm});
            skLineSegment(sketch, "E794", {"start": v(18.75, 562.92) * mm, "end": v(17.51, 562.7) * mm});
            skLineSegment(sketch, "E795", {"start": v(17.51, 562.7) * mm, "end": v(16.32, 562.3) * mm});
            skLineSegment(sketch, "E796", {"start": v(16.32, 562.3) * mm, "end": v(15.18, 561.76) * mm});
            skLineSegment(sketch, "E797", {"start": v(15.18, 561.76) * mm, "end": v(14.12, 561.1) * mm});
            skLineSegment(sketch, "E798", {"start": v(14.12, 561.1) * mm, "end": v(13.15, 560.3) * mm});
            skLineSegment(sketch, "E799", {"start": v(13.15, 560.3) * mm, "end": v(12.3, 559.37) * mm});
            skLineSegment(sketch, "E800", {"start": v(12.3, 559.37) * mm, "end": v(11.56, 558.36) * mm});
            skLineSegment(sketch, "E801", {"start": v(11.56, 558.36) * mm, "end": v(10.95, 557.26) * mm});
            skLineSegment(sketch, "E802", {"start": v(10.95, 557.26) * mm, "end": v(10.49, 556.1) * mm});
            skLineSegment(sketch, "E803", {"start": v(10.49, 556.1) * mm, "end": v(10.18, 554.87) * mm});
            skLineSegment(sketch, "E804", {"start": v(10.18, 554.87) * mm, "end": v(10.02, 553.63) * mm});
            skLineSegment(sketch, "E805", {"start": v(10.02, 553.63) * mm, "end": v(10.02, 553) * mm});
            skLineSegment(sketch, "E806", {"start": v(10.02, 553) * mm, "end": v(10, 553) * mm});
            skLineSegment(sketch, "E807", {"start": v(10, 553) * mm, "end": v(10, 425) * mm});
            skLineSegment(sketch, "E808", {"start": v(10, 425) * mm, "end": v(50, 425) * mm});
            skLineSegment(sketch, "E809", {"start": v(50, 425) * mm, "end": v(50, 409) * mm});
            skLineSegment(sketch, "E810", {"start": v(50, 409) * mm, "end": v(10, 409) * mm});
            skLineSegment(sketch, "E811", {"start": v(10, 409) * mm, "end": v(10, 133) * mm});
            skLineSegment(sketch, "E812", {"start": v(10, 133) * mm, "end": v(10.08, 131.75) * mm});
            skLineSegment(sketch, "E813", {"start": v(10.08, 131.75) * mm, "end": v(10.31, 130.51) * mm});
            skLineSegment(sketch, "E814", {"start": v(10.31, 130.51) * mm, "end": v(10.7, 129.32) * mm});
            skLineSegment(sketch, "E815", {"start": v(10.7, 129.32) * mm, "end": v(11.24, 128.18) * mm});
            skLineSegment(sketch, "E816", {"start": v(11.24, 128.18) * mm, "end": v(11.9, 127.12) * mm});
            skLineSegment(sketch, "E817", {"start": v(11.9, 127.12) * mm, "end": v(12.71, 126.16) * mm});
            skLineSegment(sketch, "E818", {"start": v(12.71, 126.16) * mm, "end": v(13.63, 125.3) * mm});
            skLineSegment(sketch, "E819", {"start": v(13.63, 125.3) * mm, "end": v(14.64, 124.56) * mm});
            skLineSegment(sketch, "E820", {"start": v(14.64, 124.56) * mm, "end": v(15.74, 123.95) * mm});
            skLineSegment(sketch, "E821", {"start": v(15.74, 123.95) * mm, "end": v(16.9, 123.49) * mm});
            skLineSegment(sketch, "E822", {"start": v(16.9, 123.49) * mm, "end": v(18.13, 123.18) * mm});
            skLineSegment(sketch, "E823", {"start": v(18.13, 123.18) * mm, "end": v(19.37, 123.02) * mm});
            skLineSegment(sketch, "E824", {"start": v(19.37, 123.02) * mm, "end": v(20, 123.02) * mm});
            skLineSegment(sketch, "E825", {"start": v(20, 123.02) * mm, "end": v(20, 123) * mm});
            skLineSegment(sketch, "E826", {"start": v(20, 123) * mm, "end": v(390, 123) * mm});
            skLineSegment(sketch, "E827", {"start": v(390, 123) * mm, "end": v(391.25, 123.08) * mm});
            skLineSegment(sketch, "E828", {"start": v(340, 536.5) * mm, "end": v(340, 552.5) * mm});
            skLineSegment(sketch, "E829", {"start": v(340, 552.5) * mm, "end": v(360, 552.5) * mm});
            skLineSegment(sketch, "E830", {"start": v(360, 552.5) * mm, "end": v(360, 536.5) * mm});
            skLineSegment(sketch, "E831", {"start": v(360, 536.5) * mm, "end": v(340, 536.5) * mm});
            skLineSegment(sketch, "E832", {"start": v(195, 536.5) * mm, "end": v(195, 552.5) * mm});
            skLineSegment(sketch, "E833", {"start": v(195, 552.5) * mm, "end": v(215, 552.5) * mm});
            skLineSegment(sketch, "E834", {"start": v(215, 552.5) * mm, "end": v(215, 536.5) * mm});
            skLineSegment(sketch, "E835", {"start": v(215, 536.5) * mm, "end": v(195, 536.5) * mm});
            skLineSegment(sketch, "E836", {"start": v(50, 536.5) * mm, "end": v(50, 552.5) * mm});
            skLineSegment(sketch, "E837", {"start": v(50, 552.5) * mm, "end": v(70, 552.5) * mm});
            skLineSegment(sketch, "E838", {"start": v(70, 552.5) * mm, "end": v(70, 536.5) * mm});
            skLineSegment(sketch, "E839", {"start": v(70, 536.5) * mm, "end": v(50, 536.5) * mm});
            skLineSegment(sketch, "E840", {"start": v(122.37, 542.5) * mm, "end": v(122.12, 542.54) * mm});
            skLineSegment(sketch, "E841", {"start": v(122.12, 542.54) * mm, "end": v(121.88, 542.6) * mm});
            skLineSegment(sketch, "E842", {"start": v(121.88, 542.6) * mm, "end": v(121.65, 542.7) * mm});
            skLineSegment(sketch, "E843", {"start": v(121.65, 542.7) * mm, "end": v(121.43, 542.8) * mm});
            skLineSegment(sketch, "E844", {"start": v(121.43, 542.8) * mm, "end": v(121.22, 542.96) * mm});
            skLineSegment(sketch, "E845", {"start": v(121.22, 542.96) * mm, "end": v(121.04, 543.13) * mm});
            skLineSegment(sketch, "E846", {"start": v(121.04, 543.13) * mm, "end": v(120.88, 543.32) * mm});
            skLineSegment(sketch, "E847", {"start": v(120.88, 543.32) * mm, "end": v(120.75, 543.54) * mm});
            skLineSegment(sketch, "E848", {"start": v(120.75, 543.54) * mm, "end": v(120.64, 543.76) * mm});
            skLineSegment(sketch, "E849", {"start": v(120.64, 543.76) * mm, "end": v(120.56, 544) * mm});
            skLineSegment(sketch, "E850", {"start": v(120.56, 544) * mm, "end": v(120.52, 544.25) * mm});
            skLineSegment(sketch, "E851", {"start": v(120.52, 544.25) * mm, "end": v(120.5, 544.5) * mm});
            skLineSegment(sketch, "E852", {"start": v(120.5, 544.5) * mm, "end": v(120.52, 544.75) * mm});
            skLineSegment(sketch, "E853", {"start": v(120.52, 544.75) * mm, "end": v(120.56, 545) * mm});
            skLineSegment(sketch, "E854", {"start": v(120.56, 545) * mm, "end": v(120.64, 545.24) * mm});
            skLineSegment(sketch, "E855", {"start": v(120.64, 545.24) * mm, "end": v(120.75, 545.46) * mm});
            skLineSegment(sketch, "E856", {"start": v(120.75, 545.46) * mm, "end": v(120.88, 545.68) * mm});
            skLineSegment(sketch, "E857", {"start": v(120.88, 545.68) * mm, "end": v(121.04, 545.87) * mm});
            skLineSegment(sketch, "E858", {"start": v(121.04, 545.87) * mm, "end": v(121.22, 546.04) * mm});
            skLineSegment(sketch, "E859", {"start": v(121.22, 546.04) * mm, "end": v(121.43, 546.2) * mm});
            skLineSegment(sketch, "E860", {"start": v(121.43, 546.2) * mm, "end": v(121.65, 546.3) * mm});
            skLineSegment(sketch, "E861", {"start": v(121.65, 546.3) * mm, "end": v(121.88, 546.4) * mm});
            skLineSegment(sketch, "E862", {"start": v(121.88, 546.4) * mm, "end": v(122.12, 546.46) * mm});
            skLineSegment(sketch, "E863", {"start": v(122.12, 546.46) * mm, "end": v(122.37, 546.5) * mm});
            skLineSegment(sketch, "E864", {"start": v(122.37, 546.5) * mm, "end": v(122.63, 546.5) * mm});
            skLineSegment(sketch, "E865", {"start": v(122.63, 546.5) * mm, "end": v(122.88, 546.46) * mm});
            skLineSegment(sketch, "E866", {"start": v(122.88, 546.46) * mm, "end": v(123.12, 546.4) * mm});
            skLineSegment(sketch, "E867", {"start": v(123.12, 546.4) * mm, "end": v(123.35, 546.3) * mm});
            skLineSegment(sketch, "E868", {"start": v(123.35, 546.3) * mm, "end": v(123.57, 546.2) * mm});
            skLineSegment(sketch, "E869", {"start": v(123.57, 546.2) * mm, "end": v(123.78, 546.04) * mm});
            skLineSegment(sketch, "E870", {"start": v(123.78, 546.04) * mm, "end": v(123.96, 545.87) * mm});
            skLineSegment(sketch, "E871", {"start": v(123.96, 545.87) * mm, "end": v(124.12, 545.68) * mm});
            skLineSegment(sketch, "E872", {"start": v(124.12, 545.68) * mm, "end": v(124.25, 545.46) * mm});
            skLineSegment(sketch, "E873", {"start": v(124.25, 545.46) * mm, "end": v(124.36, 545.24) * mm});
            skLineSegment(sketch, "E874", {"start": v(124.36, 545.24) * mm, "end": v(124.44, 545) * mm});
            skLineSegment(sketch, "E875", {"start": v(124.44, 545) * mm, "end": v(124.48, 544.75) * mm});
            skLineSegment(sketch, "E876", {"start": v(124.48, 544.75) * mm, "end": v(124.5, 544.5) * mm});
            skLineSegment(sketch, "E877", {"start": v(124.5, 544.5) * mm, "end": v(124.48, 544.25) * mm});
            skLineSegment(sketch, "E878", {"start": v(124.48, 544.25) * mm, "end": v(124.44, 544) * mm});
            skLineSegment(sketch, "E879", {"start": v(124.44, 544) * mm, "end": v(124.36, 543.76) * mm});
            skLineSegment(sketch, "E880", {"start": v(124.36, 543.76) * mm, "end": v(124.25, 543.54) * mm});
            skLineSegment(sketch, "E881", {"start": v(124.25, 543.54) * mm, "end": v(124.12, 543.32) * mm});
            skLineSegment(sketch, "E882", {"start": v(124.12, 543.32) * mm, "end": v(123.96, 543.13) * mm});
            skLineSegment(sketch, "E883", {"start": v(123.96, 543.13) * mm, "end": v(123.78, 542.96) * mm});
            skLineSegment(sketch, "E884", {"start": v(123.78, 542.96) * mm, "end": v(123.57, 542.8) * mm});
            skLineSegment(sketch, "E885", {"start": v(123.57, 542.8) * mm, "end": v(123.35, 542.7) * mm});
            skLineSegment(sketch, "E886", {"start": v(123.35, 542.7) * mm, "end": v(123.12, 542.6) * mm});
            skLineSegment(sketch, "E887", {"start": v(123.12, 542.6) * mm, "end": v(122.88, 542.54) * mm});
            skLineSegment(sketch, "E888", {"start": v(122.88, 542.54) * mm, "end": v(122.63, 542.5) * mm});
            skLineSegment(sketch, "E889", {"start": v(122.63, 542.5) * mm, "end": v(122.37, 542.5) * mm});
            skLineSegment(sketch, "E890", {"start": v(287.37, 542.5) * mm, "end": v(287.12, 542.54) * mm});
            skLineSegment(sketch, "E891", {"start": v(287.12, 542.54) * mm, "end": v(286.88, 542.6) * mm});
            skLineSegment(sketch, "E892", {"start": v(286.88, 542.6) * mm, "end": v(286.65, 542.7) * mm});
            skLineSegment(sketch, "E893", {"start": v(286.65, 542.7) * mm, "end": v(286.43, 542.8) * mm});
            skLineSegment(sketch, "E894", {"start": v(286.43, 542.8) * mm, "end": v(286.23, 542.96) * mm});
            skLineSegment(sketch, "E895", {"start": v(286.23, 542.96) * mm, "end": v(286.04, 543.13) * mm});
            skLineSegment(sketch, "E896", {"start": v(286.04, 543.13) * mm, "end": v(285.88, 543.32) * mm});
            skLineSegment(sketch, "E897", {"start": v(285.88, 543.32) * mm, "end": v(285.75, 543.54) * mm});
            skLineSegment(sketch, "E898", {"start": v(285.75, 543.54) * mm, "end": v(285.64, 543.76) * mm});
            skLineSegment(sketch, "E899", {"start": v(285.64, 543.76) * mm, "end": v(285.56, 544) * mm});
            skLineSegment(sketch, "E900", {"start": v(285.56, 544) * mm, "end": v(285.52, 544.25) * mm});
            skLineSegment(sketch, "E901", {"start": v(285.52, 544.25) * mm, "end": v(285.5, 544.5) * mm});
            skLineSegment(sketch, "E902", {"start": v(285.5, 544.5) * mm, "end": v(285.52, 544.75) * mm});
            skLineSegment(sketch, "E903", {"start": v(285.52, 544.75) * mm, "end": v(285.56, 545) * mm});
            skLineSegment(sketch, "E904", {"start": v(285.56, 545) * mm, "end": v(285.64, 545.24) * mm});
            skLineSegment(sketch, "E905", {"start": v(285.64, 545.24) * mm, "end": v(285.75, 545.46) * mm});
            skLineSegment(sketch, "E906", {"start": v(285.75, 545.46) * mm, "end": v(285.88, 545.68) * mm});
            skLineSegment(sketch, "E907", {"start": v(285.88, 545.68) * mm, "end": v(286.04, 545.87) * mm});
            skLineSegment(sketch, "E908", {"start": v(286.04, 545.87) * mm, "end": v(286.23, 546.04) * mm});
            skLineSegment(sketch, "E909", {"start": v(286.23, 546.04) * mm, "end": v(286.43, 546.2) * mm});
            skLineSegment(sketch, "E910", {"start": v(286.43, 546.2) * mm, "end": v(286.65, 546.3) * mm});
            skLineSegment(sketch, "E911", {"start": v(286.65, 546.3) * mm, "end": v(286.88, 546.4) * mm});
            skLineSegment(sketch, "E912", {"start": v(286.88, 546.4) * mm, "end": v(287.12, 546.46) * mm});
            skLineSegment(sketch, "E913", {"start": v(287.12, 546.46) * mm, "end": v(287.37, 546.5) * mm});
            skLineSegment(sketch, "E914", {"start": v(287.37, 546.5) * mm, "end": v(287.63, 546.5) * mm});
            skLineSegment(sketch, "E915", {"start": v(287.63, 546.5) * mm, "end": v(287.88, 546.46) * mm});
            skLineSegment(sketch, "E916", {"start": v(287.88, 546.46) * mm, "end": v(288.12, 546.4) * mm});
            skLineSegment(sketch, "E917", {"start": v(288.12, 546.4) * mm, "end": v(288.35, 546.3) * mm});
            skLineSegment(sketch, "E918", {"start": v(288.35, 546.3) * mm, "end": v(288.57, 546.2) * mm});
            skLineSegment(sketch, "E919", {"start": v(288.57, 546.2) * mm, "end": v(288.77, 546.04) * mm});
            skLineSegment(sketch, "E920", {"start": v(288.77, 546.04) * mm, "end": v(288.96, 545.87) * mm});
            skLineSegment(sketch, "E921", {"start": v(288.96, 545.87) * mm, "end": v(289.12, 545.68) * mm});
            skLineSegment(sketch, "E922", {"start": v(289.12, 545.68) * mm, "end": v(289.25, 545.46) * mm});
            skLineSegment(sketch, "E923", {"start": v(289.25, 545.46) * mm, "end": v(289.36, 545.24) * mm});
            skLineSegment(sketch, "E924", {"start": v(289.36, 545.24) * mm, "end": v(289.44, 545) * mm});
            skLineSegment(sketch, "E925", {"start": v(289.44, 545) * mm, "end": v(289.48, 544.75) * mm});
            skLineSegment(sketch, "E926", {"start": v(289.48, 544.75) * mm, "end": v(289.5, 544.5) * mm});
            skLineSegment(sketch, "E927", {"start": v(289.5, 544.5) * mm, "end": v(289.48, 544.25) * mm});
            skLineSegment(sketch, "E928", {"start": v(289.48, 544.25) * mm, "end": v(289.44, 544) * mm});
            skLineSegment(sketch, "E929", {"start": v(289.44, 544) * mm, "end": v(289.36, 543.76) * mm});
            skLineSegment(sketch, "E930", {"start": v(289.36, 543.76) * mm, "end": v(289.25, 543.54) * mm});
            skLineSegment(sketch, "E931", {"start": v(289.25, 543.54) * mm, "end": v(289.12, 543.32) * mm});
            skLineSegment(sketch, "E932", {"start": v(289.12, 543.32) * mm, "end": v(288.96, 543.13) * mm});
            skLineSegment(sketch, "E933", {"start": v(288.96, 543.13) * mm, "end": v(288.77, 542.96) * mm});
            skLineSegment(sketch, "E934", {"start": v(288.77, 542.96) * mm, "end": v(288.57, 542.8) * mm});
            skLineSegment(sketch, "E935", {"start": v(288.57, 542.8) * mm, "end": v(288.35, 542.7) * mm});
            skLineSegment(sketch, "E936", {"start": v(288.35, 542.7) * mm, "end": v(288.12, 542.6) * mm});
            skLineSegment(sketch, "E937", {"start": v(288.12, 542.6) * mm, "end": v(287.88, 542.54) * mm});
            skLineSegment(sketch, "E938", {"start": v(287.88, 542.54) * mm, "end": v(287.63, 542.5) * mm});
            skLineSegment(sketch, "E939", {"start": v(287.63, 542.5) * mm, "end": v(287.37, 542.5) * mm});
            skLineSegment(sketch, "E940", {"start": v(146, 143) * mm, "end": v(146, 163) * mm});
            skLineSegment(sketch, "E941", {"start": v(146, 163) * mm, "end": v(122, 163) * mm});
            skLineSegment(sketch, "E942", {"start": v(122, 163) * mm, "end": v(122, 163.06) * mm});
            skLineSegment(sketch, "E943", {"start": v(122, 163.06) * mm, "end": v(120.12, 163.06) * mm});
            skLineSegment(sketch, "E944", {"start": v(120.12, 163.06) * mm, "end": v(116.38, 163.53) * mm});
            skLineSegment(sketch, "E945", {"start": v(116.38, 163.53) * mm, "end": v(112.73, 164.47) * mm});
            skLineSegment(sketch, "E946", {"start": v(112.73, 164.47) * mm, "end": v(109.23, 165.85) * mm});
            skLineSegment(sketch, "E947", {"start": v(109.23, 165.85) * mm, "end": v(105.93, 167.67) * mm});
            skLineSegment(sketch, "E948", {"start": v(105.93, 167.67) * mm, "end": v(102.88, 169.89) * mm});
            skLineSegment(sketch, "E949", {"start": v(102.88, 169.89) * mm, "end": v(100.13, 172.46) * mm});
            skLineSegment(sketch, "E950", {"start": v(100.13, 172.46) * mm, "end": v(97.73, 175.37) * mm});
            skLineSegment(sketch, "E951", {"start": v(97.73, 175.37) * mm, "end": v(95.71, 178.55) * mm});
            skLineSegment(sketch, "E952", {"start": v(95.71, 178.55) * mm, "end": v(94.1, 181.96) * mm});
            skLineSegment(sketch, "E953", {"start": v(94.1, 181.96) * mm, "end": v(92.94, 185.54) * mm});
            skLineSegment(sketch, "E954", {"start": v(92.94, 185.54) * mm, "end": v(92.24, 189.24) * mm});
            skLineSegment(sketch, "E955", {"start": v(92.24, 189.24) * mm, "end": v(92, 193) * mm});
            skLineSegment(sketch, "E956", {"start": v(92, 193) * mm, "end": v(92, 493) * mm});
            skLineSegment(sketch, "E957", {"start": v(92, 493) * mm, "end": v(92.06, 493) * mm});
            skLineSegment(sketch, "E958", {"start": v(92.06, 493) * mm, "end": v(92.06, 494.88) * mm});
            skLineSegment(sketch, "E959", {"start": v(92.06, 494.88) * mm, "end": v(92.53, 498.62) * mm});
            skLineSegment(sketch, "E960", {"start": v(92.53, 498.62) * mm, "end": v(93.47, 502.27) * mm});
            skLineSegment(sketch, "E961", {"start": v(93.47, 502.27) * mm, "end": v(94.86, 505.77) * mm});
            skLineSegment(sketch, "E962", {"start": v(94.86, 505.77) * mm, "end": v(96.67, 509.07) * mm});
            skLineSegment(sketch, "E963", {"start": v(96.67, 509.07) * mm, "end": v(98.88, 512.12) * mm});
            skLineSegment(sketch, "E964", {"start": v(98.88, 512.12) * mm, "end": v(101.46, 514.87) * mm});
            skLineSegment(sketch, "E965", {"start": v(101.46, 514.87) * mm, "end": v(104.37, 517.27) * mm});
            skLineSegment(sketch, "E966", {"start": v(104.37, 517.27) * mm, "end": v(107.55, 519.3) * mm});
            skLineSegment(sketch, "E967", {"start": v(107.55, 519.3) * mm, "end": v(110.96, 520.9) * mm});
            skLineSegment(sketch, "E968", {"start": v(110.96, 520.9) * mm, "end": v(114.54, 522.06) * mm});
            skLineSegment(sketch, "E969", {"start": v(114.54, 522.06) * mm, "end": v(118.24, 522.76) * mm});
            skLineSegment(sketch, "E970", {"start": v(118.24, 522.76) * mm, "end": v(122, 523) * mm});
            skLineSegment(sketch, "E971", {"start": v(122, 523) * mm, "end": v(146, 523) * mm});
            skLineSegment(sketch, "E972", {"start": v(146, 523) * mm, "end": v(146, 543) * mm});
            skLineSegment(sketch, "E973", {"start": v(146, 543) * mm, "end": v(154, 543) * mm});
            skLineSegment(sketch, "E974", {"start": v(154, 543) * mm, "end": v(154, 523) * mm});
            skLineSegment(sketch, "E975", {"start": v(154, 523) * mm, "end": v(170, 523) * mm});
            skLineSegment(sketch, "E976", {"start": v(170, 523) * mm, "end": v(170, 522.98) * mm});
            skLineSegment(sketch, "E977", {"start": v(170, 522.98) * mm, "end": v(170.63, 522.98) * mm});
            skLineSegment(sketch, "E978", {"start": v(170.63, 522.98) * mm, "end": v(171.87, 522.82) * mm});
            skLineSegment(sketch, "E979", {"start": v(171.87, 522.82) * mm, "end": v(173.1, 522.5) * mm});
            skLineSegment(sketch, "E980", {"start": v(173.1, 522.5) * mm, "end": v(174.26, 522.05) * mm});
            skLineSegment(sketch, "E981", {"start": v(174.26, 522.05) * mm, "end": v(175.36, 521.44) * mm});
            skLineSegment(sketch, "E982", {"start": v(175.36, 521.44) * mm, "end": v(176.37, 520.7) * mm});
            skLineSegment(sketch, "E983", {"start": v(176.37, 520.7) * mm, "end": v(177.29, 519.85) * mm});
            skLineSegment(sketch, "E984", {"start": v(177.29, 519.85) * mm, "end": v(178.1, 518.88) * mm});
            skLineSegment(sketch, "E985", {"start": v(178.1, 518.88) * mm, "end": v(178.76, 517.82) * mm});
            skLineSegment(sketch, "E986", {"start": v(178.76, 517.82) * mm, "end": v(179.3, 516.68) * mm});
            skLineSegment(sketch, "E987", {"start": v(179.3, 516.68) * mm, "end": v(179.69, 515.5) * mm});
            skLineSegment(sketch, "E988", {"start": v(179.69, 515.5) * mm, "end": v(179.92, 514.25) * mm});
            skLineSegment(sketch, "E989", {"start": v(179.92, 514.25) * mm, "end": v(180, 513) * mm});
            skLineSegment(sketch, "E990", {"start": v(180, 513) * mm, "end": v(180, 511.5) * mm});
            skLineSegment(sketch, "E991", {"start": v(180, 511.5) * mm, "end": v(180.05, 510.7) * mm});
            skLineSegment(sketch, "E992", {"start": v(180.05, 510.7) * mm, "end": v(180.2, 509.88) * mm});
            skLineSegment(sketch, "E993", {"start": v(180.2, 509.88) * mm, "end": v(180.46, 509.11) * mm});
            skLineSegment(sketch, "E994", {"start": v(180.46, 509.11) * mm, "end": v(180.8, 508.37) * mm});
            skLineSegment(sketch, "E995", {"start": v(180.8, 508.37) * mm, "end": v(181.24, 507.68) * mm});
            skLineSegment(sketch, "E996", {"start": v(181.24, 507.68) * mm, "end": v(181.76, 507.05) * mm});
            skLineSegment(sketch, "E997", {"start": v(181.76, 507.05) * mm, "end": v(182.36, 506.5) * mm});
            skLineSegment(sketch, "E998", {"start": v(182.36, 506.5) * mm, "end": v(183.02, 506) * mm});
            skLineSegment(sketch, "E999", {"start": v(183.02, 506) * mm, "end": v(183.73, 505.62) * mm});
            skLineSegment(sketch, "E1000", {"start": v(183.73, 505.62) * mm, "end": v(184.5, 505.32) * mm});
            skLineSegment(sketch, "E1001", {"start": v(184.5, 505.32) * mm, "end": v(185.28, 505.12) * mm});
            skLineSegment(sketch, "E1002", {"start": v(185.28, 505.12) * mm, "end": v(186.1, 505) * mm});
            skLineSegment(sketch, "E1003", {"start": v(186.1, 505) * mm, "end": v(186.9, 505) * mm});
            skLineSegment(sketch, "E1004", {"start": v(186.9, 505) * mm, "end": v(187.72, 505.12) * mm});
            skLineSegment(sketch, "E1005", {"start": v(187.72, 505.12) * mm, "end": v(188.5, 505.32) * mm});
            skLineSegment(sketch, "E1006", {"start": v(188.5, 505.32) * mm, "end": v(189.27, 505.62) * mm});
            skLineSegment(sketch, "E1007", {"start": v(189.27, 505.62) * mm, "end": v(189.98, 506) * mm});
            skLineSegment(sketch, "E1008", {"start": v(189.98, 506) * mm, "end": v(190.64, 506.5) * mm});
            skLineSegment(sketch, "E1009", {"start": v(190.64, 506.5) * mm, "end": v(191.24, 507.05) * mm});
            skLineSegment(sketch, "E1010", {"start": v(191.24, 507.05) * mm, "end": v(191.76, 507.68) * mm});
            skLineSegment(sketch, "E1011", {"start": v(191.76, 507.68) * mm, "end": v(192.2, 508.37) * mm});
            skLineSegment(sketch, "E1012", {"start": v(192.2, 508.37) * mm, "end": v(192.54, 509.11) * mm});
            skLineSegment(sketch, "E1013", {"start": v(192.54, 509.11) * mm, "end": v(192.8, 509.88) * mm});
            skLineSegment(sketch, "E1014", {"start": v(192.8, 509.88) * mm, "end": v(192.95, 510.7) * mm});
            skLineSegment(sketch, "E1015", {"start": v(192.95, 510.7) * mm, "end": v(193, 511.5) * mm});
            skLineSegment(sketch, "E1016", {"start": v(193, 511.5) * mm, "end": v(193.03, 511.5) * mm});
            skLineSegment(sketch, "E1017", {"start": v(193.03, 511.5) * mm, "end": v(193.1, 512.5) * mm});
            skLineSegment(sketch, "E1018", {"start": v(193.1, 512.5) * mm, "end": v(193.38, 513.98) * mm});
            skLineSegment(sketch, "E1019", {"start": v(193.38, 513.98) * mm, "end": v(193.84, 515.42) * mm});
            skLineSegment(sketch, "E1020", {"start": v(193.84, 515.42) * mm, "end": v(194.48, 516.78) * mm});
            skLineSegment(sketch, "E1021", {"start": v(194.48, 516.78) * mm, "end": v(195.3, 518.05) * mm});
            skLineSegment(sketch, "E1022", {"start": v(195.3, 518.05) * mm, "end": v(196.25, 519.2) * mm});
            skLineSegment(sketch, "E1023", {"start": v(196.25, 519.2) * mm, "end": v(197.35, 520.25) * mm});
            skLineSegment(sketch, "E1024", {"start": v(197.35, 520.25) * mm, "end": v(198.57, 521.13) * mm});
            skLineSegment(sketch, "E1025", {"start": v(198.57, 521.13) * mm, "end": v(199.9, 521.86) * mm});
            skLineSegment(sketch, "E1026", {"start": v(199.9, 521.86) * mm, "end": v(201.3, 522.4) * mm});
            skLineSegment(sketch, "E1027", {"start": v(201.3, 522.4) * mm, "end": v(202.75, 522.8) * mm});
            skLineSegment(sketch, "E1028", {"start": v(202.75, 522.8) * mm, "end": v(204.25, 522.98) * mm});
            skLineSegment(sketch, "E1029", {"start": v(204.25, 522.98) * mm, "end": v(205.75, 522.98) * mm});
            skLineSegment(sketch, "E1030", {"start": v(205.75, 522.98) * mm, "end": v(207.25, 522.8) * mm});
            skLineSegment(sketch, "E1031", {"start": v(207.25, 522.8) * mm, "end": v(208.7, 522.4) * mm});
            skLineSegment(sketch, "E1032", {"start": v(208.7, 522.4) * mm, "end": v(210.1, 521.86) * mm});
            skLineSegment(sketch, "E1033", {"start": v(210.1, 521.86) * mm, "end": v(211.43, 521.13) * mm});
            skLineSegment(sketch, "E1034", {"start": v(211.43, 521.13) * mm, "end": v(212.65, 520.25) * mm});
            skLineSegment(sketch, "E1035", {"start": v(212.65, 520.25) * mm, "end": v(213.75, 519.2) * mm});
            skLineSegment(sketch, "E1036", {"start": v(213.75, 519.2) * mm, "end": v(213.88, 519.1) * mm});
            skLineSegment(sketch, "E1037", {"start": v(213.88, 519.1) * mm, "end": v(214, 518.98) * mm});
            skLineSegment(sketch, "E1038", {"start": v(214, 518.98) * mm, "end": v(214.14, 518.87) * mm});
            skLineSegment(sketch, "E1039", {"start": v(214.14, 518.87) * mm, "end": v(214.27, 518.76) * mm});
            skLineSegment(sketch, "E1040", {"start": v(214.27, 518.76) * mm, "end": v(214.4, 518.65) * mm});
            skLineSegment(sketch, "E1041", {"start": v(214.4, 518.65) * mm, "end": v(214.55, 518.55) * mm});
            skLineSegment(sketch, "E1042", {"start": v(214.55, 518.55) * mm, "end": v(214.69, 518.45) * mm});
            skLineSegment(sketch, "E1043", {"start": v(214.69, 518.45) * mm, "end": v(214.83, 518.35) * mm});
            skLineSegment(sketch, "E1044", {"start": v(214.83, 518.35) * mm, "end": v(215.94, 517.33) * mm});
            skLineSegment(sketch, "E1045", {"start": v(215.94, 517.33) * mm, "end": v(216.92, 516.18) * mm});
            skLineSegment(sketch, "E1046", {"start": v(216.92, 516.18) * mm, "end": v(217.74, 514.92) * mm});
            skLineSegment(sketch, "E1047", {"start": v(217.74, 514.92) * mm, "end": v(218.4, 513.57) * mm});
            skLineSegment(sketch, "E1048", {"start": v(218.4, 513.57) * mm, "end": v(218.89, 512.14) * mm});
            skLineSegment(sketch, "E1049", {"start": v(218.89, 512.14) * mm, "end": v(219.2, 510.66) * mm});
            skLineSegment(sketch, "E1050", {"start": v(219.2, 510.66) * mm, "end": v(219.3, 509.16) * mm});
            skLineSegment(sketch, "E1051", {"start": v(219.3, 509.16) * mm, "end": v(219.23, 507.66) * mm});
            skLineSegment(sketch, "E1052", {"start": v(219.23, 507.66) * mm, "end": v(219.07, 506.76) * mm});
            skLineSegment(sketch, "E1053", {"start": v(219.07, 506.76) * mm, "end": v(219.36, 506.5) * mm});
            skLineSegment(sketch, "E1054", {"start": v(219.36, 506.5) * mm, "end": v(220.02, 506) * mm});
            skLineSegment(sketch, "E1055", {"start": v(220.02, 506) * mm, "end": v(220.73, 505.62) * mm});
            skLineSegment(sketch, "E1056", {"start": v(220.73, 505.62) * mm, "end": v(221.5, 505.32) * mm});
            skLineSegment(sketch, "E1057", {"start": v(221.5, 505.32) * mm, "end": v(222.28, 505.12) * mm});
            skLineSegment(sketch, "E1058", {"start": v(222.28, 505.12) * mm, "end": v(223.1, 505) * mm});
            skLineSegment(sketch, "E1059", {"start": v(223.1, 505) * mm, "end": v(223.9, 505) * mm});
            skLineSegment(sketch, "E1060", {"start": v(223.9, 505) * mm, "end": v(224.72, 505.12) * mm});
            skLineSegment(sketch, "E1061", {"start": v(224.72, 505.12) * mm, "end": v(225.5, 505.32) * mm});
            skLineSegment(sketch, "E1062", {"start": v(225.5, 505.32) * mm, "end": v(226.27, 505.62) * mm});
            skLineSegment(sketch, "E1063", {"start": v(226.27, 505.62) * mm, "end": v(226.98, 506) * mm});
            skLineSegment(sketch, "E1064", {"start": v(226.98, 506) * mm, "end": v(227.64, 506.5) * mm});
            skLineSegment(sketch, "E1065", {"start": v(227.64, 506.5) * mm, "end": v(228.24, 507.05) * mm});
            skLineSegment(sketch, "E1066", {"start": v(228.24, 507.05) * mm, "end": v(228.76, 507.68) * mm});
            skLineSegment(sketch, "E1067", {"start": v(228.76, 507.68) * mm, "end": v(229.2, 508.37) * mm});
            skLineSegment(sketch, "E1068", {"start": v(229.2, 508.37) * mm, "end": v(229.54, 509.11) * mm});
            skLineSegment(sketch, "E1069", {"start": v(229.54, 509.11) * mm, "end": v(229.8, 509.88) * mm});
            skLineSegment(sketch, "E1070", {"start": v(229.8, 509.88) * mm, "end": v(229.95, 510.7) * mm});
            skLineSegment(sketch, "E1071", {"start": v(229.95, 510.7) * mm, "end": v(230, 511.5) * mm});
            skLineSegment(sketch, "E1072", {"start": v(230, 511.5) * mm, "end": v(230, 513) * mm});
            skLineSegment(sketch, "E1073", {"start": v(230, 513) * mm, "end": v(230.08, 514.25) * mm});
            skLineSegment(sketch, "E1074", {"start": v(230.08, 514.25) * mm, "end": v(230.31, 515.5) * mm});
            skLineSegment(sketch, "E1075", {"start": v(230.31, 515.5) * mm, "end": v(230.7, 516.68) * mm});
            skLineSegment(sketch, "E1076", {"start": v(230.7, 516.68) * mm, "end": v(231.24, 517.82) * mm});
            skLineSegment(sketch, "E1077", {"start": v(231.24, 517.82) * mm, "end": v(231.9, 518.88) * mm});
            skLineSegment(sketch, "E1078", {"start": v(231.9, 518.88) * mm, "end": v(232.71, 519.85) * mm});
            skLineSegment(sketch, "E1079", {"start": v(232.71, 519.85) * mm, "end": v(233.63, 520.7) * mm});
            skLineSegment(sketch, "E1080", {"start": v(233.63, 520.7) * mm, "end": v(234.64, 521.44) * mm});
            skLineSegment(sketch, "E1081", {"start": v(234.64, 521.44) * mm, "end": v(235.74, 522.05) * mm});
            skLineSegment(sketch, "E1082", {"start": v(235.74, 522.05) * mm, "end": v(236.9, 522.5) * mm});
            skLineSegment(sketch, "E1083", {"start": v(236.9, 522.5) * mm, "end": v(238.13, 522.82) * mm});
            skLineSegment(sketch, "E1084", {"start": v(238.13, 522.82) * mm, "end": v(239.37, 522.98) * mm});
            skLineSegment(sketch, "E1085", {"start": v(239.37, 522.98) * mm, "end": v(240, 522.98) * mm});
            skLineSegment(sketch, "E1086", {"start": v(240, 522.98) * mm, "end": v(240, 523) * mm});
            skLineSegment(sketch, "E1087", {"start": v(240, 523) * mm, "end": v(256, 523) * mm});
            skLineSegment(sketch, "E1088", {"start": v(256, 523) * mm, "end": v(256, 543) * mm});
            skLineSegment(sketch, "E1089", {"start": v(256, 543) * mm, "end": v(264, 543) * mm});
            skLineSegment(sketch, "E1090", {"start": v(264, 543) * mm, "end": v(264, 523) * mm});
            skLineSegment(sketch, "E1091", {"start": v(264, 523) * mm, "end": v(288, 523) * mm});
            skLineSegment(sketch, "E1092", {"start": v(288, 523) * mm, "end": v(288, 522.94) * mm});
            skLineSegment(sketch, "E1093", {"start": v(288, 522.94) * mm, "end": v(289.88, 522.94) * mm});
            skLineSegment(sketch, "E1094", {"start": v(289.88, 522.94) * mm, "end": v(293.62, 522.47) * mm});
            skLineSegment(sketch, "E1095", {"start": v(293.62, 522.47) * mm, "end": v(297.27, 521.53) * mm});
            skLineSegment(sketch, "E1096", {"start": v(297.27, 521.53) * mm, "end": v(300.77, 520.14) * mm});
            skLineSegment(sketch, "E1097", {"start": v(300.77, 520.14) * mm, "end": v(304.07, 518.33) * mm});
            skLineSegment(sketch, "E1098", {"start": v(304.07, 518.33) * mm, "end": v(307.12, 516.12) * mm});
            skLineSegment(sketch, "E1099", {"start": v(307.12, 516.12) * mm, "end": v(309.87, 513.54) * mm});
            skLineSegment(sketch, "E1100", {"start": v(309.87, 513.54) * mm, "end": v(312.27, 510.63) * mm});
            skLineSegment(sketch, "E1101", {"start": v(312.27, 510.63) * mm, "end": v(314.29, 507.45) * mm});
            skLineSegment(sketch, "E1102", {"start": v(314.29, 507.45) * mm, "end": v(315.9, 504.04) * mm});
            skLineSegment(sketch, "E1103", {"start": v(315.9, 504.04) * mm, "end": v(317.06, 500.46) * mm});
            skLineSegment(sketch, "E1104", {"start": v(317.06, 500.46) * mm, "end": v(317.76, 496.76) * mm});
            skLineSegment(sketch, "E1105", {"start": v(317.76, 496.76) * mm, "end": v(318, 493) * mm});
            skLineSegment(sketch, "E1106", {"start": v(318, 493) * mm, "end": v(318, 193) * mm});
            skLineSegment(sketch, "E1107", {"start": v(318, 193) * mm, "end": v(317.94, 193) * mm});
            skLineSegment(sketch, "E1108", {"start": v(317.94, 193) * mm, "end": v(317.94, 191.12) * mm});
            skLineSegment(sketch, "E1109", {"start": v(317.94, 191.12) * mm, "end": v(317.47, 187.38) * mm});
            skLineSegment(sketch, "E1110", {"start": v(317.47, 187.38) * mm, "end": v(316.53, 183.73) * mm});
            skLineSegment(sketch, "E1111", {"start": v(316.53, 183.73) * mm, "end": v(315.14, 180.23) * mm});
            skLineSegment(sketch, "E1112", {"start": v(315.14, 180.23) * mm, "end": v(313.33, 176.93) * mm});
            skLineSegment(sketch, "E1113", {"start": v(313.33, 176.93) * mm, "end": v(311.12, 173.88) * mm});
            skLineSegment(sketch, "E1114", {"start": v(311.12, 173.88) * mm, "end": v(308.54, 171.13) * mm});
            skLineSegment(sketch, "E1115", {"start": v(308.54, 171.13) * mm, "end": v(305.63, 168.73) * mm});
            skLineSegment(sketch, "E1116", {"start": v(305.63, 168.73) * mm, "end": v(302.45, 166.71) * mm});
            skLineSegment(sketch, "E1117", {"start": v(302.45, 166.71) * mm, "end": v(299.04, 165.1) * mm});
            skLineSegment(sketch, "E1118", {"start": v(299.04, 165.1) * mm, "end": v(295.46, 163.94) * mm});
            skLineSegment(sketch, "E1119", {"start": v(295.46, 163.94) * mm, "end": v(291.76, 163.24) * mm});
            skLineSegment(sketch, "E1120", {"start": v(291.76, 163.24) * mm, "end": v(288, 163) * mm});
            skLineSegment(sketch, "E1121", {"start": v(288, 163) * mm, "end": v(264, 163) * mm});
            skLineSegment(sketch, "E1122", {"start": v(264, 163) * mm, "end": v(264, 143) * mm});
            skLineSegment(sketch, "E1123", {"start": v(264, 143) * mm, "end": v(256, 143) * mm});
            skLineSegment(sketch, "E1124", {"start": v(256, 143) * mm, "end": v(256, 163) * mm});
            skLineSegment(sketch, "E1125", {"start": v(256, 163) * mm, "end": v(237, 163) * mm});
            skLineSegment(sketch, "E1126", {"start": v(237, 163) * mm, "end": v(237, 163.02) * mm});
            skLineSegment(sketch, "E1127", {"start": v(237, 163.02) * mm, "end": v(236.37, 163.02) * mm});
            skLineSegment(sketch, "E1128", {"start": v(236.37, 163.02) * mm, "end": v(235.13, 163.18) * mm});
            skLineSegment(sketch, "E1129", {"start": v(235.13, 163.18) * mm, "end": v(233.9, 163.49) * mm});
            skLineSegment(sketch, "E1130", {"start": v(233.9, 163.49) * mm, "end": v(232.74, 163.95) * mm});
            skLineSegment(sketch, "E1131", {"start": v(232.74, 163.95) * mm, "end": v(231.64, 164.56) * mm});
            skLineSegment(sketch, "E1132", {"start": v(231.64, 164.56) * mm, "end": v(230.63, 165.3) * mm});
            skLineSegment(sketch, "E1133", {"start": v(230.63, 165.3) * mm, "end": v(229.71, 166.16) * mm});
            skLineSegment(sketch, "E1134", {"start": v(229.71, 166.16) * mm, "end": v(228.9, 167.12) * mm});
            skLineSegment(sketch, "E1135", {"start": v(228.9, 167.12) * mm, "end": v(228.24, 168.18) * mm});
            skLineSegment(sketch, "E1136", {"start": v(228.24, 168.18) * mm, "end": v(227.7, 169.32) * mm});
            skLineSegment(sketch, "E1137", {"start": v(227.7, 169.32) * mm, "end": v(227.31, 170.51) * mm});
            skLineSegment(sketch, "E1138", {"start": v(227.31, 170.51) * mm, "end": v(227.08, 171.75) * mm});
            skLineSegment(sketch, "E1139", {"start": v(227.08, 171.75) * mm, "end": v(227, 173) * mm});
            skLineSegment(sketch, "E1140", {"start": v(227, 173) * mm, "end": v(227, 182) * mm});
            skLineSegment(sketch, "E1141", {"start": v(227, 182) * mm, "end": v(226.96, 182.63) * mm});
            skLineSegment(sketch, "E1142", {"start": v(226.96, 182.63) * mm, "end": v(226.84, 183.24) * mm});
            skLineSegment(sketch, "E1143", {"start": v(226.84, 183.24) * mm, "end": v(226.65, 183.84) * mm});
            skLineSegment(sketch, "E1144", {"start": v(226.65, 183.84) * mm, "end": v(226.38, 184.4) * mm});
            skLineSegment(sketch, "E1145", {"start": v(226.38, 184.4) * mm, "end": v(226.04, 184.94) * mm});
            skLineSegment(sketch, "E1146", {"start": v(226.04, 184.94) * mm, "end": v(225.65, 185.42) * mm});
            skLineSegment(sketch, "E1147", {"start": v(225.65, 185.42) * mm, "end": v(225.19, 185.85) * mm});
            skLineSegment(sketch, "E1148", {"start": v(225.19, 185.85) * mm, "end": v(224.68, 186.22) * mm});
            skLineSegment(sketch, "E1149", {"start": v(224.68, 186.22) * mm, "end": v(224.13, 186.52) * mm});
            skLineSegment(sketch, "E1150", {"start": v(224.13, 186.52) * mm, "end": v(223.54, 186.75) * mm});
            skLineSegment(sketch, "E1151", {"start": v(223.54, 186.75) * mm, "end": v(222.94, 186.91) * mm});
            skLineSegment(sketch, "E1152", {"start": v(222.94, 186.91) * mm, "end": v(222.31, 187) * mm});
            skLineSegment(sketch, "E1153", {"start": v(222.31, 187) * mm, "end": v(221.69, 187) * mm});
            skLineSegment(sketch, "E1154", {"start": v(221.69, 187) * mm, "end": v(221.06, 186.91) * mm});
            skLineSegment(sketch, "E1155", {"start": v(221.06, 186.91) * mm, "end": v(220.46, 186.75) * mm});
            skLineSegment(sketch, "E1156", {"start": v(220.46, 186.75) * mm, "end": v(219.87, 186.52) * mm});
            skLineSegment(sketch, "E1157", {"start": v(219.87, 186.52) * mm, "end": v(219.32, 186.22) * mm});
            skLineSegment(sketch, "E1158", {"start": v(219.32, 186.22) * mm, "end": v(218.81, 185.85) * mm});
            skLineSegment(sketch, "E1159", {"start": v(218.81, 185.85) * mm, "end": v(218.35, 185.42) * mm});
            skLineSegment(sketch, "E1160", {"start": v(218.35, 185.42) * mm, "end": v(217.96, 184.94) * mm});
            skLineSegment(sketch, "E1161", {"start": v(217.96, 184.94) * mm, "end": v(217.62, 184.4) * mm});
            skLineSegment(sketch, "E1162", {"start": v(217.62, 184.4) * mm, "end": v(217.35, 183.84) * mm});
            skLineSegment(sketch, "E1163", {"start": v(217.35, 183.84) * mm, "end": v(217.16, 183.24) * mm});
            skLineSegment(sketch, "E1164", {"start": v(217.16, 183.24) * mm, "end": v(217.04, 182.63) * mm});
            skLineSegment(sketch, "E1165", {"start": v(217.04, 182.63) * mm, "end": v(217, 182) * mm});
            skLineSegment(sketch, "E1166", {"start": v(217, 182) * mm, "end": v(217, 175) * mm});
            skLineSegment(sketch, "E1167", {"start": v(217, 175) * mm, "end": v(216.9, 173.5) * mm});
            skLineSegment(sketch, "E1168", {"start": v(216.9, 173.5) * mm, "end": v(216.62, 172.02) * mm});
            skLineSegment(sketch, "E1169", {"start": v(216.62, 172.02) * mm, "end": v(216.16, 170.58) * mm});
            skLineSegment(sketch, "E1170", {"start": v(216.16, 170.58) * mm, "end": v(215.52, 169.22) * mm});
            skLineSegment(sketch, "E1171", {"start": v(215.52, 169.22) * mm, "end": v(214.7, 167.95) * mm});
            skLineSegment(sketch, "E1172", {"start": v(214.7, 167.95) * mm, "end": v(213.75, 166.78) * mm});
            skLineSegment(sketch, "E1173", {"start": v(213.75, 166.78) * mm, "end": v(212.65, 165.75) * mm});
            skLineSegment(sketch, "E1174", {"start": v(212.65, 165.75) * mm, "end": v(211.43, 164.87) * mm});
            skLineSegment(sketch, "E1175", {"start": v(211.43, 164.87) * mm, "end": v(210.1, 164.14) * mm});
            skLineSegment(sketch, "E1176", {"start": v(210.1, 164.14) * mm, "end": v(208.7, 163.59) * mm});
            skLineSegment(sketch, "E1177", {"start": v(208.7, 163.59) * mm, "end": v(207.25, 163.21) * mm});
            skLineSegment(sketch, "E1178", {"start": v(207.25, 163.21) * mm, "end": v(205.75, 163.02) * mm});
            skLineSegment(sketch, "E1179", {"start": v(205.75, 163.02) * mm, "end": v(205, 163.02) * mm});
            skLineSegment(sketch, "E1180", {"start": v(205, 163.02) * mm, "end": v(205, 163) * mm});
            skLineSegment(sketch, "E1181", {"start": v(205, 163) * mm, "end": v(203.5, 163.1) * mm});
            skLineSegment(sketch, "E1182", {"start": v(203.5, 163.1) * mm, "end": v(202.02, 163.38) * mm});
            skLineSegment(sketch, "E1183", {"start": v(202.02, 163.38) * mm, "end": v(200.58, 163.84) * mm});
            skLineSegment(sketch, "E1184", {"start": v(200.58, 163.84) * mm, "end": v(199.22, 164.48) * mm});
            skLineSegment(sketch, "E1185", {"start": v(199.22, 164.48) * mm, "end": v(197.95, 165.3) * mm});
            skLineSegment(sketch, "E1186", {"start": v(197.95, 165.3) * mm, "end": v(196.78, 166.25) * mm});
            skLineSegment(sketch, "E1187", {"start": v(196.78, 166.25) * mm, "end": v(195.75, 167.35) * mm});
            skLineSegment(sketch, "E1188", {"start": v(195.75, 167.35) * mm, "end": v(194.87, 168.57) * mm});
            skLineSegment(sketch, "E1189", {"start": v(194.87, 168.57) * mm, "end": v(194.14, 169.9) * mm});
            skLineSegment(sketch, "E1190", {"start": v(194.14, 169.9) * mm, "end": v(193.59, 171.3) * mm});
            skLineSegment(sketch, "E1191", {"start": v(193.59, 171.3) * mm, "end": v(193.21, 172.75) * mm});
            skLineSegment(sketch, "E1192", {"start": v(193.21, 172.75) * mm, "end": v(193.02, 174.25) * mm});
            skLineSegment(sketch, "E1193", {"start": v(193.02, 174.25) * mm, "end": v(193.02, 175) * mm});
            skLineSegment(sketch, "E1194", {"start": v(193.02, 175) * mm, "end": v(193, 175) * mm});
            skLineSegment(sketch, "E1195", {"start": v(193, 175) * mm, "end": v(193, 182) * mm});
            skLineSegment(sketch, "E1196", {"start": v(193, 182) * mm, "end": v(192.96, 182.63) * mm});
            skLineSegment(sketch, "E1197", {"start": v(192.96, 182.63) * mm, "end": v(192.84, 183.24) * mm});
            skLineSegment(sketch, "E1198", {"start": v(192.84, 183.24) * mm, "end": v(192.65, 183.84) * mm});
            skLineSegment(sketch, "E1199", {"start": v(192.65, 183.84) * mm, "end": v(192.38, 184.4) * mm});
            skLineSegment(sketch, "E1200", {"start": v(192.38, 184.4) * mm, "end": v(192.04, 184.94) * mm});
            skLineSegment(sketch, "E1201", {"start": v(192.04, 184.94) * mm, "end": v(191.65, 185.42) * mm});
            skLineSegment(sketch, "E1202", {"start": v(191.65, 185.42) * mm, "end": v(191.19, 185.85) * mm});
            skLineSegment(sketch, "E1203", {"start": v(191.19, 185.85) * mm, "end": v(190.68, 186.22) * mm});
            skLineSegment(sketch, "E1204", {"start": v(190.68, 186.22) * mm, "end": v(190.13, 186.52) * mm});
            skLineSegment(sketch, "E1205", {"start": v(190.13, 186.52) * mm, "end": v(189.54, 186.75) * mm});
            skLineSegment(sketch, "E1206", {"start": v(189.54, 186.75) * mm, "end": v(188.94, 186.91) * mm});
            skLineSegment(sketch, "E1207", {"start": v(188.94, 186.91) * mm, "end": v(188.31, 187) * mm});
            skLineSegment(sketch, "E1208", {"start": v(188.31, 187) * mm, "end": v(188, 187) * mm});
            skLineSegment(sketch, "E1209", {"start": v(188, 187) * mm, "end": v(188, 187) * mm});
            skLineSegment(sketch, "E1210", {"start": v(188, 187) * mm, "end": v(187.37, 186.96) * mm});
            skLineSegment(sketch, "E1211", {"start": v(187.37, 186.96) * mm, "end": v(186.76, 186.84) * mm});
            skLineSegment(sketch, "E1212", {"start": v(186.76, 186.84) * mm, "end": v(186.16, 186.65) * mm});
            skLineSegment(sketch, "E1213", {"start": v(186.16, 186.65) * mm, "end": v(185.6, 186.38) * mm});
            skLineSegment(sketch, "E1214", {"start": v(185.6, 186.38) * mm, "end": v(185.06, 186.04) * mm});
            skLineSegment(sketch, "E1215", {"start": v(185.06, 186.04) * mm, "end": v(184.58, 185.65) * mm});
            skLineSegment(sketch, "E1216", {"start": v(184.58, 185.65) * mm, "end": v(184.15, 185.19) * mm});
            skLineSegment(sketch, "E1217", {"start": v(184.15, 185.19) * mm, "end": v(183.78, 184.68) * mm});
            skLineSegment(sketch, "E1218", {"start": v(183.78, 184.68) * mm, "end": v(183.48, 184.13) * mm});
            skLineSegment(sketch, "E1219", {"start": v(183.48, 184.13) * mm, "end": v(183.25, 183.54) * mm});
            skLineSegment(sketch, "E1220", {"start": v(183.25, 183.54) * mm, "end": v(183.09, 182.94) * mm});
            skLineSegment(sketch, "E1221", {"start": v(183.09, 182.94) * mm, "end": v(183.01, 182.31) * mm});
            skLineSegment(sketch, "E1222", {"start": v(183.01, 182.31) * mm, "end": v(183.01, 182) * mm});
            skLineSegment(sketch, "E1223", {"start": v(183.01, 182) * mm, "end": v(183, 182) * mm});
            skLineSegment(sketch, "E1224", {"start": v(183, 182) * mm, "end": v(183, 173) * mm});
            skLineSegment(sketch, "E1225", {"start": v(183, 173) * mm, "end": v(182.92, 171.75) * mm});
            skLineSegment(sketch, "E1226", {"start": v(182.92, 171.75) * mm, "end": v(182.69, 170.51) * mm});
            skLineSegment(sketch, "E1227", {"start": v(182.69, 170.51) * mm, "end": v(182.3, 169.32) * mm});
            skLineSegment(sketch, "E1228", {"start": v(182.3, 169.32) * mm, "end": v(181.76, 168.18) * mm});
            skLineSegment(sketch, "E1229", {"start": v(181.76, 168.18) * mm, "end": v(181.1, 167.12) * mm});
            skLineSegment(sketch, "E1230", {"start": v(181.1, 167.12) * mm, "end": v(180.29, 166.16) * mm});
            skLineSegment(sketch, "E1231", {"start": v(180.29, 166.16) * mm, "end": v(179.37, 165.3) * mm});
            skLineSegment(sketch, "E1232", {"start": v(179.37, 165.3) * mm, "end": v(178.36, 164.56) * mm});
            skLineSegment(sketch, "E1233", {"start": v(178.36, 164.56) * mm, "end": v(177.26, 163.95) * mm});
            skLineSegment(sketch, "E1234", {"start": v(177.26, 163.95) * mm, "end": v(176.1, 163.49) * mm});
            skLineSegment(sketch, "E1235", {"start": v(176.1, 163.49) * mm, "end": v(174.87, 163.18) * mm});
            skLineSegment(sketch, "E1236", {"start": v(174.87, 163.18) * mm, "end": v(173.63, 163.02) * mm});
            skLineSegment(sketch, "E1237", {"start": v(173.63, 163.02) * mm, "end": v(173, 163.02) * mm});
            skLineSegment(sketch, "E1238", {"start": v(173, 163.02) * mm, "end": v(173, 163) * mm});
            skLineSegment(sketch, "E1239", {"start": v(173, 163) * mm, "end": v(154, 163) * mm});
            skLineSegment(sketch, "E1240", {"start": v(154, 163) * mm, "end": v(154, 143) * mm});
            skLineSegment(sketch, "E1241", {"start": v(154, 143) * mm, "end": v(146, 143) * mm});
            skLineSegment(sketch, "E1242", {"start": v(141.9, 531.5) * mm, "end": v(141.72, 531.53) * mm});
            skLineSegment(sketch, "E1243", {"start": v(141.72, 531.53) * mm, "end": v(141.54, 531.57) * mm});
            skLineSegment(sketch, "E1244", {"start": v(141.54, 531.57) * mm, "end": v(141.36, 531.64) * mm});
            skLineSegment(sketch, "E1245", {"start": v(141.36, 531.64) * mm, "end": v(141.2, 531.73) * mm});
            skLineSegment(sketch, "E1246", {"start": v(141.2, 531.73) * mm, "end": v(141.04, 531.84) * mm});
            skLineSegment(sketch, "E1247", {"start": v(141.04, 531.84) * mm, "end": v(140.9, 531.97) * mm});
            skLineSegment(sketch, "E1248", {"start": v(140.9, 531.97) * mm, "end": v(140.79, 532.12) * mm});
            skLineSegment(sketch, "E1249", {"start": v(140.79, 532.12) * mm, "end": v(140.69, 532.28) * mm});
            skLineSegment(sketch, "E1250", {"start": v(140.69, 532.28) * mm, "end": v(140.6, 532.45) * mm});
            skLineSegment(sketch, "E1251", {"start": v(140.6, 532.45) * mm, "end": v(140.55, 532.63) * mm});
            skLineSegment(sketch, "E1252", {"start": v(140.55, 532.63) * mm, "end": v(140.51, 532.81) * mm});
            skLineSegment(sketch, "E1253", {"start": v(140.51, 532.81) * mm, "end": v(140.5, 533) * mm});
            skLineSegment(sketch, "E1254", {"start": v(140.5, 533) * mm, "end": v(140.51, 533.2) * mm});
            skLineSegment(sketch, "E1255", {"start": v(140.51, 533.2) * mm, "end": v(140.55, 533.37) * mm});
            skLineSegment(sketch, "E1256", {"start": v(140.55, 533.37) * mm, "end": v(140.6, 533.55) * mm});
            skLineSegment(sketch, "E1257", {"start": v(140.6, 533.55) * mm, "end": v(140.69, 533.72) * mm});
            skLineSegment(sketch, "E1258", {"start": v(140.69, 533.72) * mm, "end": v(140.79, 533.88) * mm});
            skLineSegment(sketch, "E1259", {"start": v(140.79, 533.88) * mm, "end": v(140.9, 534.03) * mm});
            skLineSegment(sketch, "E1260", {"start": v(140.9, 534.03) * mm, "end": v(141.04, 534.16) * mm});
            skLineSegment(sketch, "E1261", {"start": v(141.04, 534.16) * mm, "end": v(141.2, 534.27) * mm});
            skLineSegment(sketch, "E1262", {"start": v(141.2, 534.27) * mm, "end": v(141.36, 534.36) * mm});
            skLineSegment(sketch, "E1263", {"start": v(141.36, 534.36) * mm, "end": v(141.54, 534.43) * mm});
            skLineSegment(sketch, "E1264", {"start": v(141.54, 534.43) * mm, "end": v(141.72, 534.47) * mm});
            skLineSegment(sketch, "E1265", {"start": v(141.72, 534.47) * mm, "end": v(141.9, 534.5) * mm});
            skLineSegment(sketch, "E1266", {"start": v(141.9, 534.5) * mm, "end": v(142.1, 534.5) * mm});
            skLineSegment(sketch, "E1267", {"start": v(142.1, 534.5) * mm, "end": v(142.28, 534.47) * mm});
            skLineSegment(sketch, "E1268", {"start": v(142.28, 534.47) * mm, "end": v(142.46, 534.43) * mm});
            skLineSegment(sketch, "E1269", {"start": v(142.46, 534.43) * mm, "end": v(142.64, 534.36) * mm});
            skLineSegment(sketch, "E1270", {"start": v(142.64, 534.36) * mm, "end": v(142.8, 534.27) * mm});
            skLineSegment(sketch, "E1271", {"start": v(142.8, 534.27) * mm, "end": v(142.96, 534.16) * mm});
            skLineSegment(sketch, "E1272", {"start": v(142.96, 534.16) * mm, "end": v(143.1, 534.03) * mm});
            skLineSegment(sketch, "E1273", {"start": v(143.1, 534.03) * mm, "end": v(143.21, 533.88) * mm});
            skLineSegment(sketch, "E1274", {"start": v(143.21, 533.88) * mm, "end": v(143.31, 533.72) * mm});
            skLineSegment(sketch, "E1275", {"start": v(143.31, 533.72) * mm, "end": v(143.4, 533.55) * mm});
            skLineSegment(sketch, "E1276", {"start": v(143.4, 533.55) * mm, "end": v(143.45, 533.37) * mm});
            skLineSegment(sketch, "E1277", {"start": v(143.45, 533.37) * mm, "end": v(143.49, 533.2) * mm});
            skLineSegment(sketch, "E1278", {"start": v(143.49, 533.2) * mm, "end": v(143.5, 533) * mm});
            skLineSegment(sketch, "E1279", {"start": v(143.5, 533) * mm, "end": v(143.49, 532.81) * mm});
            skLineSegment(sketch, "E1280", {"start": v(143.49, 532.81) * mm, "end": v(143.45, 532.63) * mm});
            skLineSegment(sketch, "E1281", {"start": v(143.45, 532.63) * mm, "end": v(143.4, 532.45) * mm});
            skLineSegment(sketch, "E1282", {"start": v(143.4, 532.45) * mm, "end": v(143.31, 532.28) * mm});
            skLineSegment(sketch, "E1283", {"start": v(143.31, 532.28) * mm, "end": v(143.21, 532.12) * mm});
            skLineSegment(sketch, "E1284", {"start": v(143.21, 532.12) * mm, "end": v(143.1, 531.97) * mm});
            skLineSegment(sketch, "E1285", {"start": v(143.1, 531.97) * mm, "end": v(142.96, 531.84) * mm});
            skLineSegment(sketch, "E1286", {"start": v(142.96, 531.84) * mm, "end": v(142.8, 531.73) * mm});
            skLineSegment(sketch, "E1287", {"start": v(142.8, 531.73) * mm, "end": v(142.64, 531.64) * mm});
            skLineSegment(sketch, "E1288", {"start": v(142.64, 531.64) * mm, "end": v(142.46, 531.57) * mm});
            skLineSegment(sketch, "E1289", {"start": v(142.46, 531.57) * mm, "end": v(142.28, 531.53) * mm});
            skLineSegment(sketch, "E1290", {"start": v(142.28, 531.53) * mm, "end": v(142.1, 531.5) * mm});
            skLineSegment(sketch, "E1291", {"start": v(142.1, 531.5) * mm, "end": v(141.9, 531.5) * mm});
            skLineSegment(sketch, "E1292", {"start": v(267.9, 531.5) * mm, "end": v(267.72, 531.53) * mm});
            skLineSegment(sketch, "E1293", {"start": v(267.72, 531.53) * mm, "end": v(267.54, 531.57) * mm});
            skLineSegment(sketch, "E1294", {"start": v(267.54, 531.57) * mm, "end": v(267.36, 531.64) * mm});
            skLineSegment(sketch, "E1295", {"start": v(267.36, 531.64) * mm, "end": v(267.2, 531.73) * mm});
            skLineSegment(sketch, "E1296", {"start": v(267.2, 531.73) * mm, "end": v(267.04, 531.84) * mm});
            skLineSegment(sketch, "E1297", {"start": v(267.04, 531.84) * mm, "end": v(266.9, 531.97) * mm});
            skLineSegment(sketch, "E1298", {"start": v(266.9, 531.97) * mm, "end": v(266.79, 532.12) * mm});
            skLineSegment(sketch, "E1299", {"start": v(266.79, 532.12) * mm, "end": v(266.69, 532.28) * mm});
            skLineSegment(sketch, "E1300", {"start": v(266.69, 532.28) * mm, "end": v(266.6, 532.45) * mm});
            skLineSegment(sketch, "E1301", {"start": v(266.6, 532.45) * mm, "end": v(266.55, 532.63) * mm});
            skLineSegment(sketch, "E1302", {"start": v(266.55, 532.63) * mm, "end": v(266.51, 532.81) * mm});
            skLineSegment(sketch, "E1303", {"start": v(266.51, 532.81) * mm, "end": v(266.5, 533) * mm});
            skLineSegment(sketch, "E1304", {"start": v(266.5, 533) * mm, "end": v(266.51, 533.2) * mm});
            skLineSegment(sketch, "E1305", {"start": v(266.51, 533.2) * mm, "end": v(266.55, 533.37) * mm});
            skLineSegment(sketch, "E1306", {"start": v(266.55, 533.37) * mm, "end": v(266.6, 533.55) * mm});
            skLineSegment(sketch, "E1307", {"start": v(266.6, 533.55) * mm, "end": v(266.69, 533.72) * mm});
            skLineSegment(sketch, "E1308", {"start": v(266.69, 533.72) * mm, "end": v(266.79, 533.88) * mm});
            skLineSegment(sketch, "E1309", {"start": v(266.79, 533.88) * mm, "end": v(266.9, 534.03) * mm});
            skLineSegment(sketch, "E1310", {"start": v(266.9, 534.03) * mm, "end": v(267.04, 534.16) * mm});
            skLineSegment(sketch, "E1311", {"start": v(267.04, 534.16) * mm, "end": v(267.2, 534.27) * mm});
            skLineSegment(sketch, "E1312", {"start": v(267.2, 534.27) * mm, "end": v(267.36, 534.36) * mm});
            skLineSegment(sketch, "E1313", {"start": v(267.36, 534.36) * mm, "end": v(267.54, 534.43) * mm});
            skLineSegment(sketch, "E1314", {"start": v(267.54, 534.43) * mm, "end": v(267.72, 534.47) * mm});
            skLineSegment(sketch, "E1315", {"start": v(267.72, 534.47) * mm, "end": v(267.9, 534.5) * mm});
            skLineSegment(sketch, "E1316", {"start": v(267.9, 534.5) * mm, "end": v(268.1, 534.5) * mm});
            skLineSegment(sketch, "E1317", {"start": v(268.1, 534.5) * mm, "end": v(268.28, 534.47) * mm});
            skLineSegment(sketch, "E1318", {"start": v(268.28, 534.47) * mm, "end": v(268.46, 534.43) * mm});
            skLineSegment(sketch, "E1319", {"start": v(268.46, 534.43) * mm, "end": v(268.64, 534.36) * mm});
            skLineSegment(sketch, "E1320", {"start": v(268.64, 534.36) * mm, "end": v(268.8, 534.27) * mm});
            skLineSegment(sketch, "E1321", {"start": v(268.8, 534.27) * mm, "end": v(268.96, 534.16) * mm});
            skLineSegment(sketch, "E1322", {"start": v(268.96, 534.16) * mm, "end": v(269.1, 534.03) * mm});
            skLineSegment(sketch, "E1323", {"start": v(269.1, 534.03) * mm, "end": v(269.21, 533.88) * mm});
            skLineSegment(sketch, "E1324", {"start": v(269.21, 533.88) * mm, "end": v(269.31, 533.72) * mm});
            skLineSegment(sketch, "E1325", {"start": v(269.31, 533.72) * mm, "end": v(269.4, 533.55) * mm});
            skLineSegment(sketch, "E1326", {"start": v(269.4, 533.55) * mm, "end": v(269.45, 533.37) * mm});
            skLineSegment(sketch, "E1327", {"start": v(269.45, 533.37) * mm, "end": v(269.49, 533.2) * mm});
            skLineSegment(sketch, "E1328", {"start": v(269.49, 533.2) * mm, "end": v(269.5, 533) * mm});
            skLineSegment(sketch, "E1329", {"start": v(269.5, 533) * mm, "end": v(269.49, 532.81) * mm});
            skLineSegment(sketch, "E1330", {"start": v(269.49, 532.81) * mm, "end": v(269.45, 532.63) * mm});
            skLineSegment(sketch, "E1331", {"start": v(269.45, 532.63) * mm, "end": v(269.4, 532.45) * mm});
            skLineSegment(sketch, "E1332", {"start": v(269.4, 532.45) * mm, "end": v(269.31, 532.28) * mm});
            skLineSegment(sketch, "E1333", {"start": v(269.31, 532.28) * mm, "end": v(269.21, 532.12) * mm});
            skLineSegment(sketch, "E1334", {"start": v(269.21, 532.12) * mm, "end": v(269.1, 531.97) * mm});
            skLineSegment(sketch, "E1335", {"start": v(269.1, 531.97) * mm, "end": v(268.96, 531.84) * mm});
            skLineSegment(sketch, "E1336", {"start": v(268.96, 531.84) * mm, "end": v(268.8, 531.73) * mm});
            skLineSegment(sketch, "E1337", {"start": v(268.8, 531.73) * mm, "end": v(268.64, 531.64) * mm});
            skLineSegment(sketch, "E1338", {"start": v(268.64, 531.64) * mm, "end": v(268.46, 531.57) * mm});
            skLineSegment(sketch, "E1339", {"start": v(268.46, 531.57) * mm, "end": v(268.28, 531.53) * mm});
            skLineSegment(sketch, "E1340", {"start": v(268.28, 531.53) * mm, "end": v(268.1, 531.5) * mm});
            skLineSegment(sketch, "E1341", {"start": v(268.1, 531.5) * mm, "end": v(267.9, 531.5) * mm});
            skLineSegment(sketch, "E1342", {"start": v(251.9, 531.5) * mm, "end": v(251.72, 531.53) * mm});
            skLineSegment(sketch, "E1343", {"start": v(251.72, 531.53) * mm, "end": v(251.54, 531.57) * mm});
            skLineSegment(sketch, "E1344", {"start": v(251.54, 531.57) * mm, "end": v(251.36, 531.64) * mm});
            skLineSegment(sketch, "E1345", {"start": v(251.36, 531.64) * mm, "end": v(251.2, 531.73) * mm});
            skLineSegment(sketch, "E1346", {"start": v(251.2, 531.73) * mm, "end": v(251.04, 531.84) * mm});
            skLineSegment(sketch, "E1347", {"start": v(251.04, 531.84) * mm, "end": v(250.9, 531.97) * mm});
            skLineSegment(sketch, "E1348", {"start": v(250.9, 531.97) * mm, "end": v(250.79, 532.12) * mm});
            skLineSegment(sketch, "E1349", {"start": v(250.79, 532.12) * mm, "end": v(250.69, 532.28) * mm});
            skLineSegment(sketch, "E1350", {"start": v(250.69, 532.28) * mm, "end": v(250.6, 532.45) * mm});
            skLineSegment(sketch, "E1351", {"start": v(250.6, 532.45) * mm, "end": v(250.55, 532.63) * mm});
            skLineSegment(sketch, "E1352", {"start": v(250.55, 532.63) * mm, "end": v(250.51, 532.81) * mm});
            skLineSegment(sketch, "E1353", {"start": v(250.51, 532.81) * mm, "end": v(250.5, 533) * mm});
            skLineSegment(sketch, "E1354", {"start": v(250.5, 533) * mm, "end": v(250.51, 533.2) * mm});
            skLineSegment(sketch, "E1355", {"start": v(250.51, 533.2) * mm, "end": v(250.55, 533.37) * mm});
            skLineSegment(sketch, "E1356", {"start": v(250.55, 533.37) * mm, "end": v(250.6, 533.55) * mm});
            skLineSegment(sketch, "E1357", {"start": v(250.6, 533.55) * mm, "end": v(250.69, 533.72) * mm});
            skLineSegment(sketch, "E1358", {"start": v(250.69, 533.72) * mm, "end": v(250.79, 533.88) * mm});
            skLineSegment(sketch, "E1359", {"start": v(250.79, 533.88) * mm, "end": v(250.9, 534.03) * mm});
            skLineSegment(sketch, "E1360", {"start": v(250.9, 534.03) * mm, "end": v(251.04, 534.16) * mm});
            skLineSegment(sketch, "E1361", {"start": v(251.04, 534.16) * mm, "end": v(251.2, 534.27) * mm});
            skLineSegment(sketch, "E1362", {"start": v(251.2, 534.27) * mm, "end": v(251.36, 534.36) * mm});
            skLineSegment(sketch, "E1363", {"start": v(251.36, 534.36) * mm, "end": v(251.54, 534.43) * mm});
            skLineSegment(sketch, "E1364", {"start": v(251.54, 534.43) * mm, "end": v(251.72, 534.47) * mm});
            skLineSegment(sketch, "E1365", {"start": v(251.72, 534.47) * mm, "end": v(251.9, 534.5) * mm});
            skLineSegment(sketch, "E1366", {"start": v(251.9, 534.5) * mm, "end": v(252.1, 534.5) * mm});
            skLineSegment(sketch, "E1367", {"start": v(252.1, 534.5) * mm, "end": v(252.28, 534.47) * mm});
            skLineSegment(sketch, "E1368", {"start": v(252.28, 534.47) * mm, "end": v(252.46, 534.43) * mm});
            skLineSegment(sketch, "E1369", {"start": v(252.46, 534.43) * mm, "end": v(252.64, 534.36) * mm});
            skLineSegment(sketch, "E1370", {"start": v(252.64, 534.36) * mm, "end": v(252.8, 534.27) * mm});
            skLineSegment(sketch, "E1371", {"start": v(252.8, 534.27) * mm, "end": v(252.96, 534.16) * mm});
            skLineSegment(sketch, "E1372", {"start": v(252.96, 534.16) * mm, "end": v(253.1, 534.03) * mm});
            skLineSegment(sketch, "E1373", {"start": v(253.1, 534.03) * mm, "end": v(253.21, 533.88) * mm});
            skLineSegment(sketch, "E1374", {"start": v(253.21, 533.88) * mm, "end": v(253.31, 533.72) * mm});
            skLineSegment(sketch, "E1375", {"start": v(253.31, 533.72) * mm, "end": v(253.4, 533.55) * mm});
            skLineSegment(sketch, "E1376", {"start": v(253.4, 533.55) * mm, "end": v(253.45, 533.37) * mm});
            skLineSegment(sketch, "E1377", {"start": v(253.45, 533.37) * mm, "end": v(253.49, 533.2) * mm});
            skLineSegment(sketch, "E1378", {"start": v(253.49, 533.2) * mm, "end": v(253.5, 533) * mm});
            skLineSegment(sketch, "E1379", {"start": v(253.5, 533) * mm, "end": v(253.49, 532.81) * mm});
            skLineSegment(sketch, "E1380", {"start": v(253.49, 532.81) * mm, "end": v(253.45, 532.63) * mm});
            skLineSegment(sketch, "E1381", {"start": v(253.45, 532.63) * mm, "end": v(253.4, 532.45) * mm});
            skLineSegment(sketch, "E1382", {"start": v(253.4, 532.45) * mm, "end": v(253.31, 532.28) * mm});
            skLineSegment(sketch, "E1383", {"start": v(253.31, 532.28) * mm, "end": v(253.21, 532.12) * mm});
            skLineSegment(sketch, "E1384", {"start": v(253.21, 532.12) * mm, "end": v(253.1, 531.97) * mm});
            skLineSegment(sketch, "E1385", {"start": v(253.1, 531.97) * mm, "end": v(252.96, 531.84) * mm});
            skLineSegment(sketch, "E1386", {"start": v(252.96, 531.84) * mm, "end": v(252.8, 531.73) * mm});
            skLineSegment(sketch, "E1387", {"start": v(252.8, 531.73) * mm, "end": v(252.64, 531.64) * mm});
            skLineSegment(sketch, "E1388", {"start": v(252.64, 531.64) * mm, "end": v(252.46, 531.57) * mm});
            skLineSegment(sketch, "E1389", {"start": v(252.46, 531.57) * mm, "end": v(252.28, 531.53) * mm});
            skLineSegment(sketch, "E1390", {"start": v(252.28, 531.53) * mm, "end": v(252.1, 531.5) * mm});
            skLineSegment(sketch, "E1391", {"start": v(252.1, 531.5) * mm, "end": v(251.9, 531.5) * mm});
            skLineSegment(sketch, "E1392", {"start": v(157.9, 531.5) * mm, "end": v(157.72, 531.53) * mm});
            skLineSegment(sketch, "E1393", {"start": v(157.72, 531.53) * mm, "end": v(157.54, 531.57) * mm});
            skLineSegment(sketch, "E1394", {"start": v(157.54, 531.57) * mm, "end": v(157.36, 531.64) * mm});
            skLineSegment(sketch, "E1395", {"start": v(157.36, 531.64) * mm, "end": v(157.2, 531.73) * mm});
            skLineSegment(sketch, "E1396", {"start": v(157.2, 531.73) * mm, "end": v(157.04, 531.84) * mm});
            skLineSegment(sketch, "E1397", {"start": v(157.04, 531.84) * mm, "end": v(156.9, 531.97) * mm});
            skLineSegment(sketch, "E1398", {"start": v(156.9, 531.97) * mm, "end": v(156.79, 532.12) * mm});
            skLineSegment(sketch, "E1399", {"start": v(156.79, 532.12) * mm, "end": v(156.69, 532.28) * mm});
            skLineSegment(sketch, "E1400", {"start": v(156.69, 532.28) * mm, "end": v(156.6, 532.45) * mm});
            skLineSegment(sketch, "E1401", {"start": v(156.6, 532.45) * mm, "end": v(156.55, 532.63) * mm});
            skLineSegment(sketch, "E1402", {"start": v(156.55, 532.63) * mm, "end": v(156.51, 532.81) * mm});
            skLineSegment(sketch, "E1403", {"start": v(156.51, 532.81) * mm, "end": v(156.5, 533) * mm});
            skLineSegment(sketch, "E1404", {"start": v(156.5, 533) * mm, "end": v(156.51, 533.2) * mm});
            skLineSegment(sketch, "E1405", {"start": v(156.51, 533.2) * mm, "end": v(156.55, 533.37) * mm});
            skLineSegment(sketch, "E1406", {"start": v(156.55, 533.37) * mm, "end": v(156.6, 533.55) * mm});
            skLineSegment(sketch, "E1407", {"start": v(156.6, 533.55) * mm, "end": v(156.69, 533.72) * mm});
            skLineSegment(sketch, "E1408", {"start": v(156.69, 533.72) * mm, "end": v(156.79, 533.88) * mm});
            skLineSegment(sketch, "E1409", {"start": v(156.79, 533.88) * mm, "end": v(156.9, 534.03) * mm});
            skLineSegment(sketch, "E1410", {"start": v(156.9, 534.03) * mm, "end": v(157.04, 534.16) * mm});
            skLineSegment(sketch, "E1411", {"start": v(157.04, 534.16) * mm, "end": v(157.2, 534.27) * mm});
            skLineSegment(sketch, "E1412", {"start": v(157.2, 534.27) * mm, "end": v(157.36, 534.36) * mm});
            skLineSegment(sketch, "E1413", {"start": v(157.36, 534.36) * mm, "end": v(157.54, 534.43) * mm});
            skLineSegment(sketch, "E1414", {"start": v(157.54, 534.43) * mm, "end": v(157.72, 534.47) * mm});
            skLineSegment(sketch, "E1415", {"start": v(157.72, 534.47) * mm, "end": v(157.9, 534.5) * mm});
            skLineSegment(sketch, "E1416", {"start": v(157.9, 534.5) * mm, "end": v(158.1, 534.5) * mm});
            skLineSegment(sketch, "E1417", {"start": v(158.1, 534.5) * mm, "end": v(158.28, 534.47) * mm});
            skLineSegment(sketch, "E1418", {"start": v(158.28, 534.47) * mm, "end": v(158.46, 534.43) * mm});
            skLineSegment(sketch, "E1419", {"start": v(158.46, 534.43) * mm, "end": v(158.64, 534.36) * mm});
            skLineSegment(sketch, "E1420", {"start": v(158.64, 534.36) * mm, "end": v(158.8, 534.27) * mm});
            skLineSegment(sketch, "E1421", {"start": v(158.8, 534.27) * mm, "end": v(158.96, 534.16) * mm});
            skLineSegment(sketch, "E1422", {"start": v(158.96, 534.16) * mm, "end": v(159.1, 534.03) * mm});
            skLineSegment(sketch, "E1423", {"start": v(159.1, 534.03) * mm, "end": v(159.21, 533.88) * mm});
            skLineSegment(sketch, "E1424", {"start": v(159.21, 533.88) * mm, "end": v(159.31, 533.72) * mm});
            skLineSegment(sketch, "E1425", {"start": v(159.31, 533.72) * mm, "end": v(159.4, 533.55) * mm});
            skLineSegment(sketch, "E1426", {"start": v(159.4, 533.55) * mm, "end": v(159.45, 533.37) * mm});
            skLineSegment(sketch, "E1427", {"start": v(159.45, 533.37) * mm, "end": v(159.49, 533.2) * mm});
            skLineSegment(sketch, "E1428", {"start": v(159.49, 533.2) * mm, "end": v(159.5, 533) * mm});
            skLineSegment(sketch, "E1429", {"start": v(159.5, 533) * mm, "end": v(159.49, 532.81) * mm});
            skLineSegment(sketch, "E1430", {"start": v(159.49, 532.81) * mm, "end": v(159.45, 532.63) * mm});
            skLineSegment(sketch, "E1431", {"start": v(159.45, 532.63) * mm, "end": v(159.4, 532.45) * mm});
            skLineSegment(sketch, "E1432", {"start": v(159.4, 532.45) * mm, "end": v(159.31, 532.28) * mm});
            skLineSegment(sketch, "E1433", {"start": v(159.31, 532.28) * mm, "end": v(159.21, 532.12) * mm});
            skLineSegment(sketch, "E1434", {"start": v(159.21, 532.12) * mm, "end": v(159.1, 531.97) * mm});
            skLineSegment(sketch, "E1435", {"start": v(159.1, 531.97) * mm, "end": v(158.96, 531.84) * mm});
            skLineSegment(sketch, "E1436", {"start": v(158.96, 531.84) * mm, "end": v(158.8, 531.73) * mm});
            skLineSegment(sketch, "E1437", {"start": v(158.8, 531.73) * mm, "end": v(158.64, 531.64) * mm});
            skLineSegment(sketch, "E1438", {"start": v(158.64, 531.64) * mm, "end": v(158.46, 531.57) * mm});
            skLineSegment(sketch, "E1439", {"start": v(158.46, 531.57) * mm, "end": v(158.28, 531.53) * mm});
            skLineSegment(sketch, "E1440", {"start": v(158.28, 531.53) * mm, "end": v(158.1, 531.5) * mm});
            skLineSegment(sketch, "E1441", {"start": v(158.1, 531.5) * mm, "end": v(157.9, 531.5) * mm});
            skLineSegment(sketch, "E1442", {"start": v(220.4, 525) * mm, "end": v(220.32, 525) * mm});
            skLineSegment(sketch, "E1443", {"start": v(220.32, 525) * mm, "end": v(220.22, 525.03) * mm});
            skLineSegment(sketch, "E1444", {"start": v(220.22, 525.03) * mm, "end": v(220.19, 525.03) * mm});
            skLineSegment(sketch, "E1445", {"start": v(220.19, 525.03) * mm, "end": v(220.06, 525.07) * mm});
            skLineSegment(sketch, "E1446", {"start": v(220.06, 525.07) * mm, "end": v(219.93, 525.11) * mm});
            skLineSegment(sketch, "E1447", {"start": v(219.93, 525.11) * mm, "end": v(219.86, 525.14) * mm});
            skLineSegment(sketch, "E1448", {"start": v(219.86, 525.14) * mm, "end": v(219.8, 525.17) * mm});
            skLineSegment(sketch, "E1449", {"start": v(219.8, 525.17) * mm, "end": v(219.7, 525.23) * mm});
            skLineSegment(sketch, "E1450", {"start": v(219.7, 525.23) * mm, "end": v(219.59, 525.3) * mm});
            skLineSegment(sketch, "E1451", {"start": v(219.59, 525.3) * mm, "end": v(219.54, 525.34) * mm});
            skLineSegment(sketch, "E1452", {"start": v(219.54, 525.34) * mm, "end": v(219.48, 525.4) * mm});
            skLineSegment(sketch, "E1453", {"start": v(219.48, 525.4) * mm, "end": v(219.4, 525.47) * mm});
            skLineSegment(sketch, "E1454", {"start": v(219.4, 525.47) * mm, "end": v(219.38, 525.5) * mm});
            skLineSegment(sketch, "E1455", {"start": v(219.38, 525.5) * mm, "end": v(219.3, 525.6) * mm});
            skLineSegment(sketch, "E1456", {"start": v(219.3, 525.6) * mm, "end": v(219.22, 525.7) * mm});
            skLineSegment(sketch, "E1457", {"start": v(219.22, 525.7) * mm, "end": v(219.2, 525.75) * mm});
            skLineSegment(sketch, "E1458", {"start": v(219.2, 525.75) * mm, "end": v(219.19, 525.78) * mm});
            skLineSegment(sketch, "E1459", {"start": v(219.19, 525.78) * mm, "end": v(219.16, 525.83) * mm});
            skLineSegment(sketch, "E1460", {"start": v(219.16, 525.83) * mm, "end": v(219.1, 525.95) * mm});
            skLineSegment(sketch, "E1461", {"start": v(219.1, 525.95) * mm, "end": v(219.06, 526.08) * mm});
            skLineSegment(sketch, "E1462", {"start": v(219.06, 526.08) * mm, "end": v(219.05, 526.13) * mm});
            skLineSegment(sketch, "E1463", {"start": v(219.05, 526.13) * mm, "end": v(219.03, 526.2) * mm});
            skLineSegment(sketch, "E1464", {"start": v(219.03, 526.2) * mm, "end": v(219.01, 526.3) * mm});
            skLineSegment(sketch, "E1465", {"start": v(219.01, 526.3) * mm, "end": v(219, 526.34) * mm});
            skLineSegment(sketch, "E1466", {"start": v(219, 526.34) * mm, "end": v(219, 526.47) * mm});
            skLineSegment(sketch, "E1467", {"start": v(219, 526.47) * mm, "end": v(219, 526.6) * mm});
            skLineSegment(sketch, "E1468", {"start": v(219, 526.6) * mm, "end": v(219, 526.66) * mm});
            skLineSegment(sketch, "E1469", {"start": v(219, 526.66) * mm, "end": v(219.01, 526.7) * mm});
            skLineSegment(sketch, "E1470", {"start": v(219.01, 526.7) * mm, "end": v(219.02, 526.74) * mm});
            skLineSegment(sketch, "E1471", {"start": v(219.02, 526.74) * mm, "end": v(219.05, 526.87) * mm});
            skLineSegment(sketch, "E1472", {"start": v(219.05, 526.87) * mm, "end": v(219.09, 527) * mm});
            skLineSegment(sketch, "E1473", {"start": v(219.09, 527) * mm, "end": v(219.1, 527.05) * mm});
            skLineSegment(sketch, "E1474", {"start": v(219.1, 527.05) * mm, "end": v(219.14, 527.13) * mm});
            skLineSegment(sketch, "E1475", {"start": v(219.14, 527.13) * mm, "end": v(219.19, 527.22) * mm});
            skLineSegment(sketch, "E1476", {"start": v(219.19, 527.22) * mm, "end": v(219.2, 527.25) * mm});
            skLineSegment(sketch, "E1477", {"start": v(219.2, 527.25) * mm, "end": v(219.27, 527.36) * mm});
            skLineSegment(sketch, "E1478", {"start": v(219.27, 527.36) * mm, "end": v(219.35, 527.47) * mm});
            skLineSegment(sketch, "E1479", {"start": v(219.35, 527.47) * mm, "end": v(219.4, 527.53) * mm});
            skLineSegment(sketch, "E1480", {"start": v(219.4, 527.53) * mm, "end": v(219.45, 527.57) * mm});
            skLineSegment(sketch, "E1481", {"start": v(219.45, 527.57) * mm, "end": v(219.54, 527.66) * mm});
            skLineSegment(sketch, "E1482", {"start": v(219.54, 527.66) * mm, "end": v(219.65, 527.74) * mm});
            skLineSegment(sketch, "E1483", {"start": v(219.65, 527.74) * mm, "end": v(219.7, 527.77) * mm});
            skLineSegment(sketch, "E1484", {"start": v(219.7, 527.77) * mm, "end": v(219.77, 527.8) * mm});
            skLineSegment(sketch, "E1485", {"start": v(219.77, 527.8) * mm, "end": v(219.86, 527.86) * mm});
            skLineSegment(sketch, "E1486", {"start": v(219.86, 527.86) * mm, "end": v(219.9, 527.87) * mm});
            skLineSegment(sketch, "E1487", {"start": v(219.9, 527.87) * mm, "end": v(220.01, 527.92) * mm});
            skLineSegment(sketch, "E1488", {"start": v(220.01, 527.92) * mm, "end": v(220.14, 527.96) * mm});
            skLineSegment(sketch, "E1489", {"start": v(220.14, 527.96) * mm, "end": v(220.22, 527.97) * mm});
            skLineSegment(sketch, "E1490", {"start": v(220.22, 527.97) * mm, "end": v(220.28, 527.98) * mm});
            skLineSegment(sketch, "E1491", {"start": v(220.28, 527.98) * mm, "end": v(220.4, 528) * mm});
            skLineSegment(sketch, "E1492", {"start": v(220.4, 528) * mm, "end": v(220.54, 528) * mm});
            skLineSegment(sketch, "E1493", {"start": v(220.54, 528) * mm, "end": v(220.6, 528) * mm});
            skLineSegment(sketch, "E1494", {"start": v(220.6, 528) * mm, "end": v(220.68, 528) * mm});
            skLineSegment(sketch, "E1495", {"start": v(220.68, 528) * mm, "end": v(220.78, 527.97) * mm});
            skLineSegment(sketch, "E1496", {"start": v(220.78, 527.97) * mm, "end": v(220.81, 527.97) * mm});
            skLineSegment(sketch, "E1497", {"start": v(220.81, 527.97) * mm, "end": v(220.94, 527.93) * mm});
            skLineSegment(sketch, "E1498", {"start": v(220.94, 527.93) * mm, "end": v(221.07, 527.9) * mm});
            skLineSegment(sketch, "E1499", {"start": v(221.07, 527.9) * mm, "end": v(221.14, 527.86) * mm});
            skLineSegment(sketch, "E1500", {"start": v(221.14, 527.86) * mm, "end": v(221.2, 527.83) * mm});
            skLineSegment(sketch, "E1501", {"start": v(221.2, 527.83) * mm, "end": v(221.3, 527.77) * mm});
            skLineSegment(sketch, "E1502", {"start": v(221.3, 527.77) * mm, "end": v(221.41, 527.7) * mm});
            skLineSegment(sketch, "E1503", {"start": v(221.41, 527.7) * mm, "end": v(221.46, 527.66) * mm});
            skLineSegment(sketch, "E1504", {"start": v(221.46, 527.66) * mm, "end": v(221.52, 527.6) * mm});
            skLineSegment(sketch, "E1505", {"start": v(221.52, 527.6) * mm, "end": v(221.6, 527.53) * mm});
            skLineSegment(sketch, "E1506", {"start": v(221.6, 527.53) * mm, "end": v(221.62, 527.5) * mm});
            skLineSegment(sketch, "E1507", {"start": v(221.62, 527.5) * mm, "end": v(221.7, 527.4) * mm});
            skLineSegment(sketch, "E1508", {"start": v(221.7, 527.4) * mm, "end": v(221.78, 527.3) * mm});
            skLineSegment(sketch, "E1509", {"start": v(221.78, 527.3) * mm, "end": v(221.81, 527.22) * mm});
            skLineSegment(sketch, "E1510", {"start": v(221.81, 527.22) * mm, "end": v(221.84, 527.17) * mm});
            skLineSegment(sketch, "E1511", {"start": v(221.84, 527.17) * mm, "end": v(221.9, 527.05) * mm});
            skLineSegment(sketch, "E1512", {"start": v(221.9, 527.05) * mm, "end": v(221.94, 526.92) * mm});
            skLineSegment(sketch, "E1513", {"start": v(221.94, 526.92) * mm, "end": v(221.95, 526.87) * mm});
            skLineSegment(sketch, "E1514", {"start": v(221.95, 526.87) * mm, "end": v(221.97, 526.8) * mm});
            skLineSegment(sketch, "E1515", {"start": v(221.97, 526.8) * mm, "end": v(221.99, 526.7) * mm});
            skLineSegment(sketch, "E1516", {"start": v(221.99, 526.7) * mm, "end": v(222, 526.66) * mm});
            skLineSegment(sketch, "E1517", {"start": v(222, 526.66) * mm, "end": v(222, 526.53) * mm});
            skLineSegment(sketch, "E1518", {"start": v(222, 526.53) * mm, "end": v(222, 526.4) * mm});
            skLineSegment(sketch, "E1519", {"start": v(222, 526.4) * mm, "end": v(221.99, 526.3) * mm});
            skLineSegment(sketch, "E1520", {"start": v(221.99, 526.3) * mm, "end": v(221.98, 526.26) * mm});
            skLineSegment(sketch, "E1521", {"start": v(221.98, 526.26) * mm, "end": v(221.95, 526.13) * mm});
            skLineSegment(sketch, "E1522", {"start": v(221.95, 526.13) * mm, "end": v(221.91, 526) * mm});
            skLineSegment(sketch, "E1523", {"start": v(221.91, 526) * mm, "end": v(221.9, 525.95) * mm});
            skLineSegment(sketch, "E1524", {"start": v(221.9, 525.95) * mm, "end": v(221.86, 525.87) * mm});
            skLineSegment(sketch, "E1525", {"start": v(221.86, 525.87) * mm, "end": v(221.81, 525.78) * mm});
            skLineSegment(sketch, "E1526", {"start": v(221.81, 525.78) * mm, "end": v(221.8, 525.75) * mm});
            skLineSegment(sketch, "E1527", {"start": v(221.8, 525.75) * mm, "end": v(221.73, 525.64) * mm});
            skLineSegment(sketch, "E1528", {"start": v(221.73, 525.64) * mm, "end": v(221.65, 525.53) * mm});
            skLineSegment(sketch, "E1529", {"start": v(221.65, 525.53) * mm, "end": v(221.6, 525.47) * mm});
            skLineSegment(sketch, "E1530", {"start": v(221.6, 525.47) * mm, "end": v(221.55, 525.43) * mm});
            skLineSegment(sketch, "E1531", {"start": v(221.55, 525.43) * mm, "end": v(221.46, 525.34) * mm});
            skLineSegment(sketch, "E1532", {"start": v(221.46, 525.34) * mm, "end": v(221.35, 525.26) * mm});
            skLineSegment(sketch, "E1533", {"start": v(221.35, 525.26) * mm, "end": v(221.3, 525.23) * mm});
            skLineSegment(sketch, "E1534", {"start": v(221.3, 525.23) * mm, "end": v(221.23, 525.2) * mm});
            skLineSegment(sketch, "E1535", {"start": v(221.23, 525.2) * mm, "end": v(221.14, 525.14) * mm});
            skLineSegment(sketch, "E1536", {"start": v(221.14, 525.14) * mm, "end": v(221.11, 525.13) * mm});
            skLineSegment(sketch, "E1537", {"start": v(221.11, 525.13) * mm, "end": v(220.99, 525.08) * mm});
            skLineSegment(sketch, "E1538", {"start": v(220.99, 525.08) * mm, "end": v(220.86, 525.04) * mm});
            skLineSegment(sketch, "E1539", {"start": v(220.86, 525.04) * mm, "end": v(220.8, 525.03) * mm});
            skLineSegment(sketch, "E1540", {"start": v(220.8, 525.03) * mm, "end": v(220.78, 525.03) * mm});
            skLineSegment(sketch, "E1541", {"start": v(220.78, 525.03) * mm, "end": v(220.72, 525.02) * mm});
            skLineSegment(sketch, "E1542", {"start": v(220.72, 525.02) * mm, "end": v(220.6, 525) * mm});
            skLineSegment(sketch, "E1543", {"start": v(220.6, 525) * mm, "end": v(220.46, 525) * mm});
            skLineSegment(sketch, "E1544", {"start": v(220.46, 525) * mm, "end": v(220.4, 525) * mm});
            skLineSegment(sketch, "E1545", {"start": v(189.54, 520.7) * mm, "end": v(189.36, 520.75) * mm});
            skLineSegment(sketch, "E1546", {"start": v(189.36, 520.75) * mm, "end": v(189.18, 520.82) * mm});
            skLineSegment(sketch, "E1547", {"start": v(189.18, 520.82) * mm, "end": v(189.02, 520.9) * mm});
            skLineSegment(sketch, "E1548", {"start": v(189.02, 520.9) * mm, "end": v(188.86, 521.02) * mm});
            skLineSegment(sketch, "E1549", {"start": v(188.86, 521.02) * mm, "end": v(188.72, 521.14) * mm});
            skLineSegment(sketch, "E1550", {"start": v(188.72, 521.14) * mm, "end": v(188.6, 521.3) * mm});
            skLineSegment(sketch, "E1551", {"start": v(188.6, 521.3) * mm, "end": v(188.5, 521.44) * mm});
            skLineSegment(sketch, "E1552", {"start": v(188.5, 521.44) * mm, "end": v(188.41, 521.6) * mm});
            skLineSegment(sketch, "E1553", {"start": v(188.41, 521.6) * mm, "end": v(188.35, 521.8) * mm});
            skLineSegment(sketch, "E1554", {"start": v(188.35, 521.8) * mm, "end": v(188.32, 521.98) * mm});
            skLineSegment(sketch, "E1555", {"start": v(188.32, 521.98) * mm, "end": v(188.3, 522.16) * mm});
            skLineSegment(sketch, "E1556", {"start": v(188.3, 522.16) * mm, "end": v(188.3, 522.26) * mm});
            skLineSegment(sketch, "E1557", {"start": v(188.3, 522.26) * mm, "end": v(188.28, 522.35) * mm});
            skLineSegment(sketch, "E1558", {"start": v(188.28, 522.35) * mm, "end": v(188.24, 522.54) * mm});
            skLineSegment(sketch, "E1559", {"start": v(188.24, 522.54) * mm, "end": v(188.23, 522.73) * mm});
            skLineSegment(sketch, "E1560", {"start": v(188.23, 522.73) * mm, "end": v(188.24, 522.82) * mm});
            skLineSegment(sketch, "E1561", {"start": v(188.24, 522.82) * mm, "end": v(188.2, 522.92) * mm});
            skLineSegment(sketch, "E1562", {"start": v(188.2, 522.92) * mm, "end": v(188.18, 523.1) * mm});
            skLineSegment(sketch, "E1563", {"start": v(188.18, 523.1) * mm, "end": v(188.17, 523.3) * mm});
            skLineSegment(sketch, "E1564", {"start": v(188.17, 523.3) * mm, "end": v(188.18, 523.4) * mm});
            skLineSegment(sketch, "E1565", {"start": v(188.18, 523.4) * mm, "end": v(188.15, 523.48) * mm});
            skLineSegment(sketch, "E1566", {"start": v(188.15, 523.48) * mm, "end": v(188.12, 523.67) * mm});
            skLineSegment(sketch, "E1567", {"start": v(188.12, 523.67) * mm, "end": v(188.12, 523.86) * mm});
            skLineSegment(sketch, "E1568", {"start": v(188.12, 523.86) * mm, "end": v(188.13, 523.95) * mm});
            skLineSegment(sketch, "E1569", {"start": v(188.13, 523.95) * mm, "end": v(188.1, 524.05) * mm});
            skLineSegment(sketch, "E1570", {"start": v(188.1, 524.05) * mm, "end": v(188.08, 524.23) * mm});
            skLineSegment(sketch, "E1571", {"start": v(188.08, 524.23) * mm, "end": v(188.08, 524.42) * mm});
            skLineSegment(sketch, "E1572", {"start": v(188.08, 524.42) * mm, "end": v(188.09, 524.52) * mm});
            skLineSegment(sketch, "E1573", {"start": v(188.09, 524.52) * mm, "end": v(188.07, 524.6) * mm});
            skLineSegment(sketch, "E1574", {"start": v(188.07, 524.6) * mm, "end": v(188.04, 524.8) * mm});
            skLineSegment(sketch, "E1575", {"start": v(188.04, 524.8) * mm, "end": v(188.05, 525) * mm});
            skLineSegment(sketch, "E1576", {"start": v(188.05, 525) * mm, "end": v(188.06, 525.08) * mm});
            skLineSegment(sketch, "E1577", {"start": v(188.06, 525.08) * mm, "end": v(188.04, 525.18) * mm});
            skLineSegment(sketch, "E1578", {"start": v(188.04, 525.18) * mm, "end": v(188.02, 525.37) * mm});
            skLineSegment(sketch, "E1579", {"start": v(188.02, 525.37) * mm, "end": v(188.03, 525.55) * mm});
            skLineSegment(sketch, "E1580", {"start": v(188.03, 525.55) * mm, "end": v(188.04, 525.65) * mm});
            skLineSegment(sketch, "E1581", {"start": v(188.04, 525.65) * mm, "end": v(188.02, 525.75) * mm});
            skLineSegment(sketch, "E1582", {"start": v(188.02, 525.75) * mm, "end": v(188, 525.93) * mm});
            skLineSegment(sketch, "E1583", {"start": v(188, 525.93) * mm, "end": v(188.01, 526.12) * mm});
            skLineSegment(sketch, "E1584", {"start": v(188.01, 526.12) * mm, "end": v(188.03, 526.22) * mm});
            skLineSegment(sketch, "E1585", {"start": v(188.03, 526.22) * mm, "end": v(188.01, 526.3) * mm});
            skLineSegment(sketch, "E1586", {"start": v(188.01, 526.3) * mm, "end": v(188, 526.5) * mm});
            skLineSegment(sketch, "E1587", {"start": v(188, 526.5) * mm, "end": v(188.01, 526.7) * mm});
            skLineSegment(sketch, "E1588", {"start": v(188.01, 526.7) * mm, "end": v(188.05, 526.87) * mm});
            skLineSegment(sketch, "E1589", {"start": v(188.05, 526.87) * mm, "end": v(188.1, 527.05) * mm});
            skLineSegment(sketch, "E1590", {"start": v(188.1, 527.05) * mm, "end": v(188.19, 527.22) * mm});
            skLineSegment(sketch, "E1591", {"start": v(188.19, 527.22) * mm, "end": v(188.29, 527.38) * mm});
            skLineSegment(sketch, "E1592", {"start": v(188.29, 527.38) * mm, "end": v(188.4, 527.53) * mm});
            skLineSegment(sketch, "E1593", {"start": v(188.4, 527.53) * mm, "end": v(188.54, 527.66) * mm});
            skLineSegment(sketch, "E1594", {"start": v(188.54, 527.66) * mm, "end": v(188.7, 527.77) * mm});
            skLineSegment(sketch, "E1595", {"start": v(188.7, 527.77) * mm, "end": v(188.86, 527.86) * mm});
            skLineSegment(sketch, "E1596", {"start": v(188.86, 527.86) * mm, "end": v(189.04, 527.93) * mm});
            skLineSegment(sketch, "E1597", {"start": v(189.04, 527.93) * mm, "end": v(189.22, 527.97) * mm});
            skLineSegment(sketch, "E1598", {"start": v(189.22, 527.97) * mm, "end": v(189.4, 528) * mm});
            skLineSegment(sketch, "E1599", {"start": v(189.4, 528) * mm, "end": v(189.6, 528) * mm});
            skLineSegment(sketch, "E1600", {"start": v(189.6, 528) * mm, "end": v(189.78, 527.97) * mm});
            skLineSegment(sketch, "E1601", {"start": v(189.78, 527.97) * mm, "end": v(189.96, 527.93) * mm});
            skLineSegment(sketch, "E1602", {"start": v(189.96, 527.93) * mm, "end": v(190.14, 527.86) * mm});
            skLineSegment(sketch, "E1603", {"start": v(190.14, 527.86) * mm, "end": v(190.3, 527.77) * mm});
            skLineSegment(sketch, "E1604", {"start": v(190.3, 527.77) * mm, "end": v(190.46, 527.66) * mm});
            skLineSegment(sketch, "E1605", {"start": v(190.46, 527.66) * mm, "end": v(190.6, 527.53) * mm});
            skLineSegment(sketch, "E1606", {"start": v(190.6, 527.53) * mm, "end": v(190.71, 527.38) * mm});
            skLineSegment(sketch, "E1607", {"start": v(190.71, 527.38) * mm, "end": v(190.81, 527.22) * mm});
            skLineSegment(sketch, "E1608", {"start": v(190.81, 527.22) * mm, "end": v(190.9, 527.05) * mm});
            skLineSegment(sketch, "E1609", {"start": v(190.9, 527.05) * mm, "end": v(190.95, 526.87) * mm});
            skLineSegment(sketch, "E1610", {"start": v(190.95, 526.87) * mm, "end": v(190.99, 526.7) * mm});
            skLineSegment(sketch, "E1611", {"start": v(190.99, 526.7) * mm, "end": v(191, 526.5) * mm});
            skLineSegment(sketch, "E1612", {"start": v(191, 526.5) * mm, "end": v(190.99, 526.3) * mm});
            skLineSegment(sketch, "E1613", {"start": v(190.99, 526.3) * mm, "end": v(190.97, 526.24) * mm});
            skLineSegment(sketch, "E1614", {"start": v(190.97, 526.24) * mm, "end": v(190.99, 526.17) * mm});
            skLineSegment(sketch, "E1615", {"start": v(190.99, 526.17) * mm, "end": v(191, 526) * mm});
            skLineSegment(sketch, "E1616", {"start": v(191, 526) * mm, "end": v(191, 525.8) * mm});
            skLineSegment(sketch, "E1617", {"start": v(191, 525.8) * mm, "end": v(190.98, 525.73) * mm});
            skLineSegment(sketch, "E1618", {"start": v(190.98, 525.73) * mm, "end": v(191, 525.66) * mm});
            skLineSegment(sketch, "E1619", {"start": v(191, 525.66) * mm, "end": v(191.02, 525.47) * mm});
            skLineSegment(sketch, "E1620", {"start": v(191.02, 525.47) * mm, "end": v(191.01, 525.28) * mm});
            skLineSegment(sketch, "E1621", {"start": v(191.01, 525.28) * mm, "end": v(191, 525.2) * mm});
            skLineSegment(sketch, "E1622", {"start": v(191, 525.2) * mm, "end": v(191.02, 525.14) * mm});
            skLineSegment(sketch, "E1623", {"start": v(191.02, 525.14) * mm, "end": v(191.04, 524.96) * mm});
            skLineSegment(sketch, "E1624", {"start": v(191.04, 524.96) * mm, "end": v(191.04, 524.77) * mm});
            skLineSegment(sketch, "E1625", {"start": v(191.04, 524.77) * mm, "end": v(191.03, 524.7) * mm});
            skLineSegment(sketch, "E1626", {"start": v(191.03, 524.7) * mm, "end": v(191.05, 524.63) * mm});
            skLineSegment(sketch, "E1627", {"start": v(191.05, 524.63) * mm, "end": v(191.07, 524.44) * mm});
            skLineSegment(sketch, "E1628", {"start": v(191.07, 524.44) * mm, "end": v(191.07, 524.25) * mm});
            skLineSegment(sketch, "E1629", {"start": v(191.07, 524.25) * mm, "end": v(191.07, 524.18) * mm});
            skLineSegment(sketch, "E1630", {"start": v(191.07, 524.18) * mm, "end": v(191.08, 524.12) * mm});
            skLineSegment(sketch, "E1631", {"start": v(191.08, 524.12) * mm, "end": v(191.11, 523.93) * mm});
            skLineSegment(sketch, "E1632", {"start": v(191.11, 523.93) * mm, "end": v(191.12, 523.74) * mm});
            skLineSegment(sketch, "E1633", {"start": v(191.12, 523.74) * mm, "end": v(191.11, 523.67) * mm});
            skLineSegment(sketch, "E1634", {"start": v(191.11, 523.67) * mm, "end": v(191.13, 523.6) * mm});
            skLineSegment(sketch, "E1635", {"start": v(191.13, 523.6) * mm, "end": v(191.16, 523.42) * mm});
            skLineSegment(sketch, "E1636", {"start": v(191.16, 523.42) * mm, "end": v(191.17, 523.23) * mm});
            skLineSegment(sketch, "E1637", {"start": v(191.17, 523.23) * mm, "end": v(191.16, 523.16) * mm});
            skLineSegment(sketch, "E1638", {"start": v(191.16, 523.16) * mm, "end": v(191.19, 523.1) * mm});
            skLineSegment(sketch, "E1639", {"start": v(191.19, 523.1) * mm, "end": v(191.22, 522.9) * mm});
            skLineSegment(sketch, "E1640", {"start": v(191.22, 522.9) * mm, "end": v(191.23, 522.72) * mm});
            skLineSegment(sketch, "E1641", {"start": v(191.23, 522.72) * mm, "end": v(191.23, 522.65) * mm});
            skLineSegment(sketch, "E1642", {"start": v(191.23, 522.65) * mm, "end": v(191.25, 522.58) * mm});
            skLineSegment(sketch, "E1643", {"start": v(191.25, 522.58) * mm, "end": v(191.29, 522.4) * mm});
            skLineSegment(sketch, "E1644", {"start": v(191.29, 522.4) * mm, "end": v(191.3, 522.2) * mm});
            skLineSegment(sketch, "E1645", {"start": v(191.3, 522.2) * mm, "end": v(191.3, 522.02) * mm});
            skLineSegment(sketch, "E1646", {"start": v(191.3, 522.02) * mm, "end": v(191.26, 521.83) * mm});
            skLineSegment(sketch, "E1647", {"start": v(191.26, 521.83) * mm, "end": v(191.2, 521.65) * mm});
            skLineSegment(sketch, "E1648", {"start": v(191.2, 521.65) * mm, "end": v(191.13, 521.48) * mm});
            skLineSegment(sketch, "E1649", {"start": v(191.13, 521.48) * mm, "end": v(191.03, 521.32) * mm});
            skLineSegment(sketch, "E1650", {"start": v(191.03, 521.32) * mm, "end": v(190.9, 521.17) * mm});
            skLineSegment(sketch, "E1651", {"start": v(190.9, 521.17) * mm, "end": v(190.77, 521.04) * mm});
            skLineSegment(sketch, "E1652", {"start": v(190.77, 521.04) * mm, "end": v(190.62, 520.93) * mm});
            skLineSegment(sketch, "E1653", {"start": v(190.62, 520.93) * mm, "end": v(190.46, 520.84) * mm});
            skLineSegment(sketch, "E1654", {"start": v(190.46, 520.84) * mm, "end": v(190.28, 520.77) * mm});
            skLineSegment(sketch, "E1655", {"start": v(190.28, 520.77) * mm, "end": v(190.1, 520.72) * mm});
            skLineSegment(sketch, "E1656", {"start": v(190.1, 520.72) * mm, "end": v(189.92, 520.7) * mm});
            skLineSegment(sketch, "E1657", {"start": v(189.92, 520.7) * mm, "end": v(189.73, 520.7) * mm});
            skLineSegment(sketch, "E1658", {"start": v(189.73, 520.7) * mm, "end": v(189.54, 520.7) * mm});
            skLineSegment(sketch, "E1659", {"start": v(369.87, 518) * mm, "end": v(369.62, 518.04) * mm});
            skLineSegment(sketch, "E1660", {"start": v(369.62, 518.04) * mm, "end": v(369.38, 518.1) * mm});
            skLineSegment(sketch, "E1661", {"start": v(369.38, 518.1) * mm, "end": v(369.15, 518.2) * mm});
            skLineSegment(sketch, "E1662", {"start": v(369.15, 518.2) * mm, "end": v(368.93, 518.3) * mm});
            skLineSegment(sketch, "E1663", {"start": v(368.93, 518.3) * mm, "end": v(368.73, 518.46) * mm});
            skLineSegment(sketch, "E1664", {"start": v(368.73, 518.46) * mm, "end": v(368.54, 518.63) * mm});
            skLineSegment(sketch, "E1665", {"start": v(368.54, 518.63) * mm, "end": v(368.38, 518.82) * mm});
            skLineSegment(sketch, "E1666", {"start": v(368.38, 518.82) * mm, "end": v(368.25, 519.04) * mm});
            skLineSegment(sketch, "E1667", {"start": v(368.25, 519.04) * mm, "end": v(368.14, 519.26) * mm});
            skLineSegment(sketch, "E1668", {"start": v(368.14, 519.26) * mm, "end": v(368.06, 519.5) * mm});
            skLineSegment(sketch, "E1669", {"start": v(368.06, 519.5) * mm, "end": v(368.02, 519.75) * mm});
            skLineSegment(sketch, "E1670", {"start": v(368.02, 519.75) * mm, "end": v(368, 520) * mm});
            skLineSegment(sketch, "E1671", {"start": v(368, 520) * mm, "end": v(368.02, 520.25) * mm});
            skLineSegment(sketch, "E1672", {"start": v(368.02, 520.25) * mm, "end": v(368.06, 520.5) * mm});
            skLineSegment(sketch, "E1673", {"start": v(368.06, 520.5) * mm, "end": v(368.14, 520.74) * mm});
            skLineSegment(sketch, "E1674", {"start": v(368.14, 520.74) * mm, "end": v(368.25, 520.96) * mm});
            skLineSegment(sketch, "E1675", {"start": v(368.25, 520.96) * mm, "end": v(368.38, 521.18) * mm});
            skLineSegment(sketch, "E1676", {"start": v(368.38, 521.18) * mm, "end": v(368.54, 521.37) * mm});
            skLineSegment(sketch, "E1677", {"start": v(368.54, 521.37) * mm, "end": v(368.73, 521.54) * mm});
            skLineSegment(sketch, "E1678", {"start": v(368.73, 521.54) * mm, "end": v(368.93, 521.7) * mm});
            skLineSegment(sketch, "E1679", {"start": v(368.93, 521.7) * mm, "end": v(369.15, 521.8) * mm});
            skLineSegment(sketch, "E1680", {"start": v(369.15, 521.8) * mm, "end": v(369.38, 521.9) * mm});
            skLineSegment(sketch, "E1681", {"start": v(369.38, 521.9) * mm, "end": v(369.62, 521.96) * mm});
            skLineSegment(sketch, "E1682", {"start": v(369.62, 521.96) * mm, "end": v(369.87, 522) * mm});
            skLineSegment(sketch, "E1683", {"start": v(369.87, 522) * mm, "end": v(370.13, 522) * mm});
            skLineSegment(sketch, "E1684", {"start": v(370.13, 522) * mm, "end": v(370.38, 521.96) * mm});
            skLineSegment(sketch, "E1685", {"start": v(370.38, 521.96) * mm, "end": v(370.62, 521.9) * mm});
            skLineSegment(sketch, "E1686", {"start": v(370.62, 521.9) * mm, "end": v(370.85, 521.8) * mm});
            skLineSegment(sketch, "E1687", {"start": v(370.85, 521.8) * mm, "end": v(371.07, 521.7) * mm});
            skLineSegment(sketch, "E1688", {"start": v(371.07, 521.7) * mm, "end": v(371.27, 521.54) * mm});
            skLineSegment(sketch, "E1689", {"start": v(371.27, 521.54) * mm, "end": v(371.46, 521.37) * mm});
            skLineSegment(sketch, "E1690", {"start": v(371.46, 521.37) * mm, "end": v(371.62, 521.18) * mm});
            skLineSegment(sketch, "E1691", {"start": v(371.62, 521.18) * mm, "end": v(371.75, 520.96) * mm});
            skLineSegment(sketch, "E1692", {"start": v(371.75, 520.96) * mm, "end": v(371.86, 520.74) * mm});
            skLineSegment(sketch, "E1693", {"start": v(371.86, 520.74) * mm, "end": v(371.94, 520.5) * mm});
            skLineSegment(sketch, "E1694", {"start": v(371.94, 520.5) * mm, "end": v(371.98, 520.25) * mm});
            skLineSegment(sketch, "E1695", {"start": v(371.98, 520.25) * mm, "end": v(372, 520) * mm});
            skLineSegment(sketch, "E1696", {"start": v(372, 520) * mm, "end": v(371.98, 519.75) * mm});
            skLineSegment(sketch, "E1697", {"start": v(371.98, 519.75) * mm, "end": v(371.94, 519.5) * mm});
            skLineSegment(sketch, "E1698", {"start": v(371.94, 519.5) * mm, "end": v(371.86, 519.26) * mm});
            skLineSegment(sketch, "E1699", {"start": v(371.86, 519.26) * mm, "end": v(371.75, 519.04) * mm});
            skLineSegment(sketch, "E1700", {"start": v(371.75, 519.04) * mm, "end": v(371.62, 518.82) * mm});
            skLineSegment(sketch, "E1701", {"start": v(371.62, 518.82) * mm, "end": v(371.46, 518.63) * mm});
            skLineSegment(sketch, "E1702", {"start": v(371.46, 518.63) * mm, "end": v(371.27, 518.46) * mm});
            skLineSegment(sketch, "E1703", {"start": v(371.27, 518.46) * mm, "end": v(371.07, 518.3) * mm});
            skLineSegment(sketch, "E1704", {"start": v(371.07, 518.3) * mm, "end": v(370.85, 518.2) * mm});
            skLineSegment(sketch, "E1705", {"start": v(370.85, 518.2) * mm, "end": v(370.62, 518.1) * mm});
            skLineSegment(sketch, "E1706", {"start": v(370.62, 518.1) * mm, "end": v(370.38, 518.04) * mm});
            skLineSegment(sketch, "E1707", {"start": v(370.38, 518.04) * mm, "end": v(370.13, 518) * mm});
            skLineSegment(sketch, "E1708", {"start": v(370.13, 518) * mm, "end": v(369.87, 518) * mm});
            skLineSegment(sketch, "E1709", {"start": v(39.87, 518) * mm, "end": v(39.63, 518.04) * mm});
            skLineSegment(sketch, "E1710", {"start": v(39.63, 518.04) * mm, "end": v(39.38, 518.1) * mm});
            skLineSegment(sketch, "E1711", {"start": v(39.38, 518.1) * mm, "end": v(39.15, 518.2) * mm});
            skLineSegment(sketch, "E1712", {"start": v(39.15, 518.2) * mm, "end": v(38.93, 518.3) * mm});
            skLineSegment(sketch, "E1713", {"start": v(38.93, 518.3) * mm, "end": v(38.73, 518.46) * mm});
            skLineSegment(sketch, "E1714", {"start": v(38.73, 518.46) * mm, "end": v(38.54, 518.63) * mm});
            skLineSegment(sketch, "E1715", {"start": v(38.54, 518.63) * mm, "end": v(38.38, 518.82) * mm});
            skLineSegment(sketch, "E1716", {"start": v(38.38, 518.82) * mm, "end": v(38.25, 519.04) * mm});
            skLineSegment(sketch, "E1717", {"start": v(38.25, 519.04) * mm, "end": v(38.14, 519.26) * mm});
            skLineSegment(sketch, "E1718", {"start": v(38.14, 519.26) * mm, "end": v(38.06, 519.5) * mm});
            skLineSegment(sketch, "E1719", {"start": v(38.06, 519.5) * mm, "end": v(38.02, 519.75) * mm});
            skLineSegment(sketch, "E1720", {"start": v(38.02, 519.75) * mm, "end": v(38, 520) * mm});
            skLineSegment(sketch, "E1721", {"start": v(38, 520) * mm, "end": v(38.02, 520.25) * mm});
            skLineSegment(sketch, "E1722", {"start": v(38.02, 520.25) * mm, "end": v(38.06, 520.5) * mm});
            skLineSegment(sketch, "E1723", {"start": v(38.06, 520.5) * mm, "end": v(38.14, 520.74) * mm});
            skLineSegment(sketch, "E1724", {"start": v(38.14, 520.74) * mm, "end": v(38.25, 520.96) * mm});
            skLineSegment(sketch, "E1725", {"start": v(38.25, 520.96) * mm, "end": v(38.38, 521.18) * mm});
            skLineSegment(sketch, "E1726", {"start": v(38.38, 521.18) * mm, "end": v(38.54, 521.37) * mm});
            skLineSegment(sketch, "E1727", {"start": v(38.54, 521.37) * mm, "end": v(38.73, 521.54) * mm});
            skLineSegment(sketch, "E1728", {"start": v(38.73, 521.54) * mm, "end": v(38.93, 521.7) * mm});
            skLineSegment(sketch, "E1729", {"start": v(38.93, 521.7) * mm, "end": v(39.15, 521.8) * mm});
            skLineSegment(sketch, "E1730", {"start": v(39.15, 521.8) * mm, "end": v(39.38, 521.9) * mm});
            skLineSegment(sketch, "E1731", {"start": v(39.38, 521.9) * mm, "end": v(39.63, 521.96) * mm});
            skLineSegment(sketch, "E1732", {"start": v(39.63, 521.96) * mm, "end": v(39.87, 522) * mm});
            skLineSegment(sketch, "E1733", {"start": v(39.87, 522) * mm, "end": v(40.13, 522) * mm});
            skLineSegment(sketch, "E1734", {"start": v(40.13, 522) * mm, "end": v(40.37, 521.96) * mm});
            skLineSegment(sketch, "E1735", {"start": v(40.37, 521.96) * mm, "end": v(40.62, 521.9) * mm});
            skLineSegment(sketch, "E1736", {"start": v(40.62, 521.9) * mm, "end": v(40.85, 521.8) * mm});
            skLineSegment(sketch, "E1737", {"start": v(40.85, 521.8) * mm, "end": v(41.07, 521.7) * mm});
            skLineSegment(sketch, "E1738", {"start": v(41.07, 521.7) * mm, "end": v(41.27, 521.54) * mm});
            skLineSegment(sketch, "E1739", {"start": v(41.27, 521.54) * mm, "end": v(41.46, 521.37) * mm});
            skLineSegment(sketch, "E1740", {"start": v(41.46, 521.37) * mm, "end": v(41.62, 521.18) * mm});
            skLineSegment(sketch, "E1741", {"start": v(41.62, 521.18) * mm, "end": v(41.75, 520.96) * mm});
            skLineSegment(sketch, "E1742", {"start": v(41.75, 520.96) * mm, "end": v(41.86, 520.74) * mm});
            skLineSegment(sketch, "E1743", {"start": v(41.86, 520.74) * mm, "end": v(41.94, 520.5) * mm});
            skLineSegment(sketch, "E1744", {"start": v(41.94, 520.5) * mm, "end": v(41.98, 520.25) * mm});
            skLineSegment(sketch, "E1745", {"start": v(41.98, 520.25) * mm, "end": v(42, 520) * mm});
            skLineSegment(sketch, "E1746", {"start": v(42, 520) * mm, "end": v(41.98, 519.75) * mm});
            skLineSegment(sketch, "E1747", {"start": v(41.98, 519.75) * mm, "end": v(41.94, 519.5) * mm});
            skLineSegment(sketch, "E1748", {"start": v(41.94, 519.5) * mm, "end": v(41.86, 519.26) * mm});
            skLineSegment(sketch, "E1749", {"start": v(41.86, 519.26) * mm, "end": v(41.75, 519.04) * mm});
            skLineSegment(sketch, "E1750", {"start": v(41.75, 519.04) * mm, "end": v(41.62, 518.82) * mm});
            skLineSegment(sketch, "E1751", {"start": v(41.62, 518.82) * mm, "end": v(41.46, 518.63) * mm});
            skLineSegment(sketch, "E1752", {"start": v(41.46, 518.63) * mm, "end": v(41.27, 518.46) * mm});
            skLineSegment(sketch, "E1753", {"start": v(41.27, 518.46) * mm, "end": v(41.07, 518.3) * mm});
            skLineSegment(sketch, "E1754", {"start": v(41.07, 518.3) * mm, "end": v(40.85, 518.2) * mm});
            skLineSegment(sketch, "E1755", {"start": v(40.85, 518.2) * mm, "end": v(40.62, 518.1) * mm});
            skLineSegment(sketch, "E1756", {"start": v(40.62, 518.1) * mm, "end": v(40.37, 518.04) * mm});
            skLineSegment(sketch, "E1757", {"start": v(40.37, 518.04) * mm, "end": v(40.13, 518) * mm});
            skLineSegment(sketch, "E1758", {"start": v(40.13, 518) * mm, "end": v(39.87, 518) * mm});
            skLineSegment(sketch, "E1759", {"start": v(32, 480) * mm, "end": v(32, 500) * mm});
            skLineSegment(sketch, "E1760", {"start": v(32, 500) * mm, "end": v(48, 500) * mm});
            skLineSegment(sketch, "E1761", {"start": v(48, 500) * mm, "end": v(48, 480) * mm});
            skLineSegment(sketch, "E1762", {"start": v(48, 480) * mm, "end": v(32, 480) * mm});
            skLineSegment(sketch, "E1763", {"start": v(362, 480) * mm, "end": v(362, 500) * mm});
            skLineSegment(sketch, "E1764", {"start": v(362, 500) * mm, "end": v(378, 500) * mm});
            skLineSegment(sketch, "E1765", {"start": v(378, 500) * mm, "end": v(378, 480) * mm});
            skLineSegment(sketch, "E1766", {"start": v(378, 480) * mm, "end": v(362, 480) * mm});
            skLineSegment(sketch, "E1767", {"start": v(39.87, 458) * mm, "end": v(39.63, 458.04) * mm});
            skLineSegment(sketch, "E1768", {"start": v(39.63, 458.04) * mm, "end": v(39.38, 458.1) * mm});
            skLineSegment(sketch, "E1769", {"start": v(39.38, 458.1) * mm, "end": v(39.15, 458.2) * mm});
            skLineSegment(sketch, "E1770", {"start": v(39.15, 458.2) * mm, "end": v(38.93, 458.3) * mm});
            skLineSegment(sketch, "E1771", {"start": v(38.93, 458.3) * mm, "end": v(38.73, 458.46) * mm});
            skLineSegment(sketch, "E1772", {"start": v(38.73, 458.46) * mm, "end": v(38.54, 458.63) * mm});
            skLineSegment(sketch, "E1773", {"start": v(38.54, 458.63) * mm, "end": v(38.38, 458.82) * mm});
            skLineSegment(sketch, "E1774", {"start": v(38.38, 458.82) * mm, "end": v(38.25, 459.04) * mm});
            skLineSegment(sketch, "E1775", {"start": v(38.25, 459.04) * mm, "end": v(38.14, 459.26) * mm});
            skLineSegment(sketch, "E1776", {"start": v(38.14, 459.26) * mm, "end": v(38.06, 459.5) * mm});
            skLineSegment(sketch, "E1777", {"start": v(38.06, 459.5) * mm, "end": v(38.02, 459.75) * mm});
            skLineSegment(sketch, "E1778", {"start": v(38.02, 459.75) * mm, "end": v(38, 460) * mm});
            skLineSegment(sketch, "E1779", {"start": v(38, 460) * mm, "end": v(38.02, 460.25) * mm});
            skLineSegment(sketch, "E1780", {"start": v(38.02, 460.25) * mm, "end": v(38.06, 460.5) * mm});
            skLineSegment(sketch, "E1781", {"start": v(38.06, 460.5) * mm, "end": v(38.14, 460.74) * mm});
            skLineSegment(sketch, "E1782", {"start": v(38.14, 460.74) * mm, "end": v(38.25, 460.96) * mm});
            skLineSegment(sketch, "E1783", {"start": v(38.25, 460.96) * mm, "end": v(38.38, 461.18) * mm});
            skLineSegment(sketch, "E1784", {"start": v(38.38, 461.18) * mm, "end": v(38.54, 461.37) * mm});
            skLineSegment(sketch, "E1785", {"start": v(38.54, 461.37) * mm, "end": v(38.73, 461.54) * mm});
            skLineSegment(sketch, "E1786", {"start": v(38.73, 461.54) * mm, "end": v(38.93, 461.7) * mm});
            skLineSegment(sketch, "E1787", {"start": v(38.93, 461.7) * mm, "end": v(39.15, 461.8) * mm});
            skLineSegment(sketch, "E1788", {"start": v(39.15, 461.8) * mm, "end": v(39.38, 461.9) * mm});
            skLineSegment(sketch, "E1789", {"start": v(39.38, 461.9) * mm, "end": v(39.63, 461.96) * mm});
            skLineSegment(sketch, "E1790", {"start": v(39.63, 461.96) * mm, "end": v(39.87, 462) * mm});
            skLineSegment(sketch, "E1791", {"start": v(39.87, 462) * mm, "end": v(40.13, 462) * mm});
            skLineSegment(sketch, "E1792", {"start": v(40.13, 462) * mm, "end": v(40.37, 461.96) * mm});
            skLineSegment(sketch, "E1793", {"start": v(40.37, 461.96) * mm, "end": v(40.62, 461.9) * mm});
            skLineSegment(sketch, "E1794", {"start": v(40.62, 461.9) * mm, "end": v(40.85, 461.8) * mm});
            skLineSegment(sketch, "E1795", {"start": v(40.85, 461.8) * mm, "end": v(41.07, 461.7) * mm});
            skLineSegment(sketch, "E1796", {"start": v(41.07, 461.7) * mm, "end": v(41.27, 461.54) * mm});
            skLineSegment(sketch, "E1797", {"start": v(41.27, 461.54) * mm, "end": v(41.46, 461.37) * mm});
            skLineSegment(sketch, "E1798", {"start": v(41.46, 461.37) * mm, "end": v(41.62, 461.18) * mm});
            skLineSegment(sketch, "E1799", {"start": v(41.62, 461.18) * mm, "end": v(41.75, 460.96) * mm});
            skLineSegment(sketch, "E1800", {"start": v(41.75, 460.96) * mm, "end": v(41.86, 460.74) * mm});
            skLineSegment(sketch, "E1801", {"start": v(41.86, 460.74) * mm, "end": v(41.94, 460.5) * mm});
            skLineSegment(sketch, "E1802", {"start": v(41.94, 460.5) * mm, "end": v(41.98, 460.25) * mm});
            skLineSegment(sketch, "E1803", {"start": v(41.98, 460.25) * mm, "end": v(42, 460) * mm});
            skLineSegment(sketch, "E1804", {"start": v(42, 460) * mm, "end": v(41.98, 459.75) * mm});
            skLineSegment(sketch, "E1805", {"start": v(41.98, 459.75) * mm, "end": v(41.94, 459.5) * mm});
            skLineSegment(sketch, "E1806", {"start": v(41.94, 459.5) * mm, "end": v(41.86, 459.26) * mm});
            skLineSegment(sketch, "E1807", {"start": v(41.86, 459.26) * mm, "end": v(41.75, 459.04) * mm});
            skLineSegment(sketch, "E1808", {"start": v(41.75, 459.04) * mm, "end": v(41.62, 458.82) * mm});
            skLineSegment(sketch, "E1809", {"start": v(41.62, 458.82) * mm, "end": v(41.46, 458.63) * mm});
            skLineSegment(sketch, "E1810", {"start": v(41.46, 458.63) * mm, "end": v(41.27, 458.46) * mm});
            skLineSegment(sketch, "E1811", {"start": v(41.27, 458.46) * mm, "end": v(41.07, 458.3) * mm});
            skLineSegment(sketch, "E1812", {"start": v(41.07, 458.3) * mm, "end": v(40.85, 458.2) * mm});
            skLineSegment(sketch, "E1813", {"start": v(40.85, 458.2) * mm, "end": v(40.62, 458.1) * mm});
            skLineSegment(sketch, "E1814", {"start": v(40.62, 458.1) * mm, "end": v(40.37, 458.04) * mm});
            skLineSegment(sketch, "E1815", {"start": v(40.37, 458.04) * mm, "end": v(40.13, 458) * mm});
            skLineSegment(sketch, "E1816", {"start": v(40.13, 458) * mm, "end": v(39.87, 458) * mm});
            skLineSegment(sketch, "E1817", {"start": v(369.87, 458) * mm, "end": v(369.62, 458.04) * mm});
            skLineSegment(sketch, "E1818", {"start": v(369.62, 458.04) * mm, "end": v(369.38, 458.1) * mm});
            skLineSegment(sketch, "E1819", {"start": v(369.38, 458.1) * mm, "end": v(369.15, 458.2) * mm});
            skLineSegment(sketch, "E1820", {"start": v(369.15, 458.2) * mm, "end": v(368.93, 458.3) * mm});
            skLineSegment(sketch, "E1821", {"start": v(368.93, 458.3) * mm, "end": v(368.73, 458.46) * mm});
            skLineSegment(sketch, "E1822", {"start": v(368.73, 458.46) * mm, "end": v(368.54, 458.63) * mm});
            skLineSegment(sketch, "E1823", {"start": v(368.54, 458.63) * mm, "end": v(368.38, 458.82) * mm});
            skLineSegment(sketch, "E1824", {"start": v(368.38, 458.82) * mm, "end": v(368.25, 459.04) * mm});
            skLineSegment(sketch, "E1825", {"start": v(368.25, 459.04) * mm, "end": v(368.14, 459.26) * mm});
            skLineSegment(sketch, "E1826", {"start": v(368.14, 459.26) * mm, "end": v(368.06, 459.5) * mm});
            skLineSegment(sketch, "E1827", {"start": v(368.06, 459.5) * mm, "end": v(368.02, 459.75) * mm});
            skLineSegment(sketch, "E1828", {"start": v(368.02, 459.75) * mm, "end": v(368, 460) * mm});
            skLineSegment(sketch, "E1829", {"start": v(368, 460) * mm, "end": v(368.02, 460.25) * mm});
            skLineSegment(sketch, "E1830", {"start": v(368.02, 460.25) * mm, "end": v(368.06, 460.5) * mm});
            skLineSegment(sketch, "E1831", {"start": v(368.06, 460.5) * mm, "end": v(368.14, 460.74) * mm});
            skLineSegment(sketch, "E1832", {"start": v(368.14, 460.74) * mm, "end": v(368.25, 460.96) * mm});
            skLineSegment(sketch, "E1833", {"start": v(368.25, 460.96) * mm, "end": v(368.38, 461.18) * mm});
            skLineSegment(sketch, "E1834", {"start": v(368.38, 461.18) * mm, "end": v(368.54, 461.37) * mm});
            skLineSegment(sketch, "E1835", {"start": v(368.54, 461.37) * mm, "end": v(368.73, 461.54) * mm});
            skLineSegment(sketch, "E1836", {"start": v(368.73, 461.54) * mm, "end": v(368.93, 461.7) * mm});
            skLineSegment(sketch, "E1837", {"start": v(368.93, 461.7) * mm, "end": v(369.15, 461.8) * mm});
            skLineSegment(sketch, "E1838", {"start": v(369.15, 461.8) * mm, "end": v(369.38, 461.9) * mm});
            skLineSegment(sketch, "E1839", {"start": v(369.38, 461.9) * mm, "end": v(369.62, 461.96) * mm});
            skLineSegment(sketch, "E1840", {"start": v(369.62, 461.96) * mm, "end": v(369.87, 462) * mm});
            skLineSegment(sketch, "E1841", {"start": v(369.87, 462) * mm, "end": v(370.13, 462) * mm});
            skLineSegment(sketch, "E1842", {"start": v(370.13, 462) * mm, "end": v(370.38, 461.96) * mm});
            skLineSegment(sketch, "E1843", {"start": v(370.38, 461.96) * mm, "end": v(370.62, 461.9) * mm});
            skLineSegment(sketch, "E1844", {"start": v(370.62, 461.9) * mm, "end": v(370.85, 461.8) * mm});
            skLineSegment(sketch, "E1845", {"start": v(370.85, 461.8) * mm, "end": v(371.07, 461.7) * mm});
            skLineSegment(sketch, "E1846", {"start": v(371.07, 461.7) * mm, "end": v(371.27, 461.54) * mm});
            skLineSegment(sketch, "E1847", {"start": v(371.27, 461.54) * mm, "end": v(371.46, 461.37) * mm});
            skLineSegment(sketch, "E1848", {"start": v(371.46, 461.37) * mm, "end": v(371.62, 461.18) * mm});
            skLineSegment(sketch, "E1849", {"start": v(371.62, 461.18) * mm, "end": v(371.75, 460.96) * mm});
            skLineSegment(sketch, "E1850", {"start": v(371.75, 460.96) * mm, "end": v(371.86, 460.74) * mm});
            skLineSegment(sketch, "E1851", {"start": v(371.86, 460.74) * mm, "end": v(371.94, 460.5) * mm});
            skLineSegment(sketch, "E1852", {"start": v(371.94, 460.5) * mm, "end": v(371.98, 460.25) * mm});
            skLineSegment(sketch, "E1853", {"start": v(371.98, 460.25) * mm, "end": v(372, 460) * mm});
            skLineSegment(sketch, "E1854", {"start": v(372, 460) * mm, "end": v(371.98, 459.75) * mm});
            skLineSegment(sketch, "E1855", {"start": v(371.98, 459.75) * mm, "end": v(371.94, 459.5) * mm});
            skLineSegment(sketch, "E1856", {"start": v(371.94, 459.5) * mm, "end": v(371.86, 459.26) * mm});
            skLineSegment(sketch, "E1857", {"start": v(371.86, 459.26) * mm, "end": v(371.75, 459.04) * mm});
            skLineSegment(sketch, "E1858", {"start": v(371.75, 459.04) * mm, "end": v(371.62, 458.82) * mm});
            skLineSegment(sketch, "E1859", {"start": v(371.62, 458.82) * mm, "end": v(371.46, 458.63) * mm});
            skLineSegment(sketch, "E1860", {"start": v(371.46, 458.63) * mm, "end": v(371.27, 458.46) * mm});
            skLineSegment(sketch, "E1861", {"start": v(371.27, 458.46) * mm, "end": v(371.07, 458.3) * mm});
            skLineSegment(sketch, "E1862", {"start": v(371.07, 458.3) * mm, "end": v(370.85, 458.2) * mm});
            skLineSegment(sketch, "E1863", {"start": v(370.85, 458.2) * mm, "end": v(370.62, 458.1) * mm});
            skLineSegment(sketch, "E1864", {"start": v(370.62, 458.1) * mm, "end": v(370.38, 458.04) * mm});
            skLineSegment(sketch, "E1865", {"start": v(370.38, 458.04) * mm, "end": v(370.13, 458) * mm});
            skLineSegment(sketch, "E1866", {"start": v(370.13, 458) * mm, "end": v(369.87, 458) * mm});
            skLineSegment(sketch, "E1867", {"start": v(354.4, 394) * mm, "end": v(354.22, 394.03) * mm});
            skLineSegment(sketch, "E1868", {"start": v(354.22, 394.03) * mm, "end": v(354.04, 394.07) * mm});
            skLineSegment(sketch, "E1869", {"start": v(354.04, 394.07) * mm, "end": v(353.86, 394.14) * mm});
            skLineSegment(sketch, "E1870", {"start": v(353.86, 394.14) * mm, "end": v(353.7, 394.23) * mm});
            skLineSegment(sketch, "E1871", {"start": v(353.7, 394.23) * mm, "end": v(353.54, 394.34) * mm});
            skLineSegment(sketch, "E1872", {"start": v(353.54, 394.34) * mm, "end": v(353.4, 394.47) * mm});
            skLineSegment(sketch, "E1873", {"start": v(353.4, 394.47) * mm, "end": v(353.29, 394.62) * mm});
            skLineSegment(sketch, "E1874", {"start": v(353.29, 394.62) * mm, "end": v(353.19, 394.78) * mm});
            skLineSegment(sketch, "E1875", {"start": v(353.19, 394.78) * mm, "end": v(353.1, 394.95) * mm});
            skLineSegment(sketch, "E1876", {"start": v(353.1, 394.95) * mm, "end": v(353.05, 395.13) * mm});
            skLineSegment(sketch, "E1877", {"start": v(353.05, 395.13) * mm, "end": v(353.01, 395.31) * mm});
            skLineSegment(sketch, "E1878", {"start": v(353.01, 395.31) * mm, "end": v(353, 395.5) * mm});
            skLineSegment(sketch, "E1879", {"start": v(353, 395.5) * mm, "end": v(353.01, 395.69) * mm});
            skLineSegment(sketch, "E1880", {"start": v(353.01, 395.69) * mm, "end": v(353.05, 395.87) * mm});
            skLineSegment(sketch, "E1881", {"start": v(353.05, 395.87) * mm, "end": v(353.1, 396.05) * mm});
            skLineSegment(sketch, "E1882", {"start": v(353.1, 396.05) * mm, "end": v(353.19, 396.22) * mm});
            skLineSegment(sketch, "E1883", {"start": v(353.19, 396.22) * mm, "end": v(353.29, 396.38) * mm});
            skLineSegment(sketch, "E1884", {"start": v(353.29, 396.38) * mm, "end": v(353.4, 396.53) * mm});
            skLineSegment(sketch, "E1885", {"start": v(353.4, 396.53) * mm, "end": v(353.54, 396.66) * mm});
            skLineSegment(sketch, "E1886", {"start": v(353.54, 396.66) * mm, "end": v(353.7, 396.77) * mm});
            skLineSegment(sketch, "E1887", {"start": v(353.7, 396.77) * mm, "end": v(353.86, 396.86) * mm});
            skLineSegment(sketch, "E1888", {"start": v(353.86, 396.86) * mm, "end": v(354.04, 396.93) * mm});
            skLineSegment(sketch, "E1889", {"start": v(354.04, 396.93) * mm, "end": v(354.22, 396.97) * mm});
            skLineSegment(sketch, "E1890", {"start": v(354.22, 396.97) * mm, "end": v(354.4, 397) * mm});
            skLineSegment(sketch, "E1891", {"start": v(354.4, 397) * mm, "end": v(354.6, 397) * mm});
            skLineSegment(sketch, "E1892", {"start": v(354.6, 397) * mm, "end": v(354.78, 396.97) * mm});
            skLineSegment(sketch, "E1893", {"start": v(354.78, 396.97) * mm, "end": v(354.96, 396.93) * mm});
            skLineSegment(sketch, "E1894", {"start": v(354.96, 396.93) * mm, "end": v(355.14, 396.86) * mm});
            skLineSegment(sketch, "E1895", {"start": v(355.14, 396.86) * mm, "end": v(355.3, 396.77) * mm});
            skLineSegment(sketch, "E1896", {"start": v(355.3, 396.77) * mm, "end": v(355.46, 396.66) * mm});
            skLineSegment(sketch, "E1897", {"start": v(355.46, 396.66) * mm, "end": v(355.6, 396.53) * mm});
            skLineSegment(sketch, "E1898", {"start": v(355.6, 396.53) * mm, "end": v(355.71, 396.38) * mm});
            skLineSegment(sketch, "E1899", {"start": v(355.71, 396.38) * mm, "end": v(355.81, 396.22) * mm});
            skLineSegment(sketch, "E1900", {"start": v(355.81, 396.22) * mm, "end": v(355.9, 396.05) * mm});
            skLineSegment(sketch, "E1901", {"start": v(355.9, 396.05) * mm, "end": v(355.95, 395.87) * mm});
            skLineSegment(sketch, "E1902", {"start": v(355.95, 395.87) * mm, "end": v(355.99, 395.69) * mm});
            skLineSegment(sketch, "E1903", {"start": v(355.99, 395.69) * mm, "end": v(356, 395.5) * mm});
            skLineSegment(sketch, "E1904", {"start": v(356, 395.5) * mm, "end": v(355.99, 395.31) * mm});
            skLineSegment(sketch, "E1905", {"start": v(355.99, 395.31) * mm, "end": v(355.95, 395.13) * mm});
            skLineSegment(sketch, "E1906", {"start": v(355.95, 395.13) * mm, "end": v(355.9, 394.95) * mm});
            skLineSegment(sketch, "E1907", {"start": v(355.9, 394.95) * mm, "end": v(355.81, 394.78) * mm});
            skLineSegment(sketch, "E1908", {"start": v(355.81, 394.78) * mm, "end": v(355.71, 394.62) * mm});
            skLineSegment(sketch, "E1909", {"start": v(355.71, 394.62) * mm, "end": v(355.6, 394.47) * mm});
            skLineSegment(sketch, "E1910", {"start": v(355.6, 394.47) * mm, "end": v(355.46, 394.34) * mm});
            skLineSegment(sketch, "E1911", {"start": v(355.46, 394.34) * mm, "end": v(355.3, 394.23) * mm});
            skLineSegment(sketch, "E1912", {"start": v(355.3, 394.23) * mm, "end": v(355.14, 394.14) * mm});
            skLineSegment(sketch, "E1913", {"start": v(355.14, 394.14) * mm, "end": v(354.96, 394.07) * mm});
            skLineSegment(sketch, "E1914", {"start": v(354.96, 394.07) * mm, "end": v(354.78, 394.03) * mm});
            skLineSegment(sketch, "E1915", {"start": v(354.78, 394.03) * mm, "end": v(354.6, 394) * mm});
            skLineSegment(sketch, "E1916", {"start": v(354.6, 394) * mm, "end": v(354.4, 394) * mm});
            skLineSegment(sketch, "E1917", {"start": v(24.4, 394) * mm, "end": v(24.22, 394.03) * mm});
            skLineSegment(sketch, "E1918", {"start": v(24.22, 394.03) * mm, "end": v(24.04, 394.07) * mm});
            skLineSegment(sketch, "E1919", {"start": v(24.04, 394.07) * mm, "end": v(23.86, 394.14) * mm});
            skLineSegment(sketch, "E1920", {"start": v(23.86, 394.14) * mm, "end": v(23.7, 394.23) * mm});
            skLineSegment(sketch, "E1921", {"start": v(23.7, 394.23) * mm, "end": v(23.54, 394.34) * mm});
            skLineSegment(sketch, "E1922", {"start": v(23.54, 394.34) * mm, "end": v(23.4, 394.47) * mm});
            skLineSegment(sketch, "E1923", {"start": v(23.4, 394.47) * mm, "end": v(23.29, 394.62) * mm});
            skLineSegment(sketch, "E1924", {"start": v(23.29, 394.62) * mm, "end": v(23.19, 394.78) * mm});
            skLineSegment(sketch, "E1925", {"start": v(23.19, 394.78) * mm, "end": v(23.1, 394.95) * mm});
            skLineSegment(sketch, "E1926", {"start": v(23.1, 394.95) * mm, "end": v(23.05, 395.13) * mm});
            skLineSegment(sketch, "E1927", {"start": v(23.05, 395.13) * mm, "end": v(23.01, 395.31) * mm});
            skLineSegment(sketch, "E1928", {"start": v(23.01, 395.31) * mm, "end": v(23, 395.5) * mm});
            skLineSegment(sketch, "E1929", {"start": v(23, 395.5) * mm, "end": v(23.01, 395.69) * mm});
            skLineSegment(sketch, "E1930", {"start": v(23.01, 395.69) * mm, "end": v(23.05, 395.87) * mm});
            skLineSegment(sketch, "E1931", {"start": v(23.05, 395.87) * mm, "end": v(23.1, 396.05) * mm});
            skLineSegment(sketch, "E1932", {"start": v(23.1, 396.05) * mm, "end": v(23.19, 396.22) * mm});
            skLineSegment(sketch, "E1933", {"start": v(23.19, 396.22) * mm, "end": v(23.29, 396.38) * mm});
            skLineSegment(sketch, "E1934", {"start": v(23.29, 396.38) * mm, "end": v(23.4, 396.53) * mm});
            skLineSegment(sketch, "E1935", {"start": v(23.4, 396.53) * mm, "end": v(23.54, 396.66) * mm});
            skLineSegment(sketch, "E1936", {"start": v(23.54, 396.66) * mm, "end": v(23.7, 396.77) * mm});
            skLineSegment(sketch, "E1937", {"start": v(23.7, 396.77) * mm, "end": v(23.86, 396.86) * mm});
            skLineSegment(sketch, "E1938", {"start": v(23.86, 396.86) * mm, "end": v(24.04, 396.93) * mm});
            skLineSegment(sketch, "E1939", {"start": v(24.04, 396.93) * mm, "end": v(24.22, 396.97) * mm});
            skLineSegment(sketch, "E1940", {"start": v(24.22, 396.97) * mm, "end": v(24.4, 397) * mm});
            skLineSegment(sketch, "E1941", {"start": v(24.4, 397) * mm, "end": v(24.6, 397) * mm});
            skLineSegment(sketch, "E1942", {"start": v(24.6, 397) * mm, "end": v(24.78, 396.97) * mm});
            skLineSegment(sketch, "E1943", {"start": v(24.78, 396.97) * mm, "end": v(24.96, 396.93) * mm});
            skLineSegment(sketch, "E1944", {"start": v(24.96, 396.93) * mm, "end": v(25.14, 396.86) * mm});
            skLineSegment(sketch, "E1945", {"start": v(25.14, 396.86) * mm, "end": v(25.3, 396.77) * mm});
            skLineSegment(sketch, "E1946", {"start": v(25.3, 396.77) * mm, "end": v(25.46, 396.66) * mm});
            skLineSegment(sketch, "E1947", {"start": v(25.46, 396.66) * mm, "end": v(25.6, 396.53) * mm});
            skLineSegment(sketch, "E1948", {"start": v(25.6, 396.53) * mm, "end": v(25.71, 396.38) * mm});
            skLineSegment(sketch, "E1949", {"start": v(25.71, 396.38) * mm, "end": v(25.81, 396.22) * mm});
            skLineSegment(sketch, "E1950", {"start": v(25.81, 396.22) * mm, "end": v(25.9, 396.05) * mm});
            skLineSegment(sketch, "E1951", {"start": v(25.9, 396.05) * mm, "end": v(25.95, 395.87) * mm});
            skLineSegment(sketch, "E1952", {"start": v(25.95, 395.87) * mm, "end": v(25.99, 395.69) * mm});
            skLineSegment(sketch, "E1953", {"start": v(25.99, 395.69) * mm, "end": v(26, 395.5) * mm});
            skLineSegment(sketch, "E1954", {"start": v(26, 395.5) * mm, "end": v(25.99, 395.31) * mm});
            skLineSegment(sketch, "E1955", {"start": v(25.99, 395.31) * mm, "end": v(25.95, 395.13) * mm});
            skLineSegment(sketch, "E1956", {"start": v(25.95, 395.13) * mm, "end": v(25.9, 394.95) * mm});
            skLineSegment(sketch, "E1957", {"start": v(25.9, 394.95) * mm, "end": v(25.81, 394.78) * mm});
            skLineSegment(sketch, "E1958", {"start": v(25.81, 394.78) * mm, "end": v(25.71, 394.62) * mm});
            skLineSegment(sketch, "E1959", {"start": v(25.71, 394.62) * mm, "end": v(25.6, 394.47) * mm});
            skLineSegment(sketch, "E1960", {"start": v(25.6, 394.47) * mm, "end": v(25.46, 394.34) * mm});
            skLineSegment(sketch, "E1961", {"start": v(25.46, 394.34) * mm, "end": v(25.3, 394.23) * mm});
            skLineSegment(sketch, "E1962", {"start": v(25.3, 394.23) * mm, "end": v(25.14, 394.14) * mm});
            skLineSegment(sketch, "E1963", {"start": v(25.14, 394.14) * mm, "end": v(24.96, 394.07) * mm});
            skLineSegment(sketch, "E1964", {"start": v(24.96, 394.07) * mm, "end": v(24.78, 394.03) * mm});
            skLineSegment(sketch, "E1965", {"start": v(24.78, 394.03) * mm, "end": v(24.6, 394) * mm});
            skLineSegment(sketch, "E1966", {"start": v(24.6, 394) * mm, "end": v(24.4, 394) * mm});
            skLineSegment(sketch, "E1967", {"start": v(385.4, 394) * mm, "end": v(385.22, 394.03) * mm});
            skLineSegment(sketch, "E1968", {"start": v(385.22, 394.03) * mm, "end": v(385.04, 394.07) * mm});
            skLineSegment(sketch, "E1969", {"start": v(385.04, 394.07) * mm, "end": v(384.86, 394.14) * mm});
            skLineSegment(sketch, "E1970", {"start": v(384.86, 394.14) * mm, "end": v(384.7, 394.23) * mm});
            skLineSegment(sketch, "E1971", {"start": v(384.7, 394.23) * mm, "end": v(384.54, 394.34) * mm});
            skLineSegment(sketch, "E1972", {"start": v(384.54, 394.34) * mm, "end": v(384.4, 394.47) * mm});
            skLineSegment(sketch, "E1973", {"start": v(384.4, 394.47) * mm, "end": v(384.29, 394.62) * mm});
            skLineSegment(sketch, "E1974", {"start": v(384.29, 394.62) * mm, "end": v(384.19, 394.78) * mm});
            skLineSegment(sketch, "E1975", {"start": v(384.19, 394.78) * mm, "end": v(384.1, 394.95) * mm});
            skLineSegment(sketch, "E1976", {"start": v(384.1, 394.95) * mm, "end": v(384.05, 395.13) * mm});
            skLineSegment(sketch, "E1977", {"start": v(384.05, 395.13) * mm, "end": v(384.01, 395.31) * mm});
            skLineSegment(sketch, "E1978", {"start": v(384.01, 395.31) * mm, "end": v(384, 395.5) * mm});
            skLineSegment(sketch, "E1979", {"start": v(384, 395.5) * mm, "end": v(384.01, 395.69) * mm});
            skLineSegment(sketch, "E1980", {"start": v(384.01, 395.69) * mm, "end": v(384.05, 395.87) * mm});
            skLineSegment(sketch, "E1981", {"start": v(384.05, 395.87) * mm, "end": v(384.1, 396.05) * mm});
            skLineSegment(sketch, "E1982", {"start": v(384.1, 396.05) * mm, "end": v(384.19, 396.22) * mm});
            skLineSegment(sketch, "E1983", {"start": v(384.19, 396.22) * mm, "end": v(384.29, 396.38) * mm});
            skLineSegment(sketch, "E1984", {"start": v(384.29, 396.38) * mm, "end": v(384.4, 396.53) * mm});
            skLineSegment(sketch, "E1985", {"start": v(384.4, 396.53) * mm, "end": v(384.54, 396.66) * mm});
            skLineSegment(sketch, "E1986", {"start": v(384.54, 396.66) * mm, "end": v(384.7, 396.77) * mm});
            skLineSegment(sketch, "E1987", {"start": v(384.7, 396.77) * mm, "end": v(384.86, 396.86) * mm});
            skLineSegment(sketch, "E1988", {"start": v(384.86, 396.86) * mm, "end": v(385.04, 396.93) * mm});
            skLineSegment(sketch, "E1989", {"start": v(385.04, 396.93) * mm, "end": v(385.22, 396.97) * mm});
            skLineSegment(sketch, "E1990", {"start": v(385.22, 396.97) * mm, "end": v(385.4, 397) * mm});
            skLineSegment(sketch, "E1991", {"start": v(385.4, 397) * mm, "end": v(385.6, 397) * mm});
            skLineSegment(sketch, "E1992", {"start": v(385.6, 397) * mm, "end": v(385.78, 396.97) * mm});
            skLineSegment(sketch, "E1993", {"start": v(385.78, 396.97) * mm, "end": v(385.96, 396.93) * mm});
            skLineSegment(sketch, "E1994", {"start": v(385.96, 396.93) * mm, "end": v(386.14, 396.86) * mm});
            skLineSegment(sketch, "E1995", {"start": v(386.14, 396.86) * mm, "end": v(386.3, 396.77) * mm});
            skLineSegment(sketch, "E1996", {"start": v(386.3, 396.77) * mm, "end": v(386.46, 396.66) * mm});
            skLineSegment(sketch, "E1997", {"start": v(386.46, 396.66) * mm, "end": v(386.6, 396.53) * mm});
            skLineSegment(sketch, "E1998", {"start": v(386.6, 396.53) * mm, "end": v(386.71, 396.38) * mm});
            skLineSegment(sketch, "E1999", {"start": v(386.71, 396.38) * mm, "end": v(386.81, 396.22) * mm});
            skLineSegment(sketch, "E2000", {"start": v(386.81, 396.22) * mm, "end": v(386.9, 396.05) * mm});
            skLineSegment(sketch, "E2001", {"start": v(386.9, 396.05) * mm, "end": v(386.95, 395.87) * mm});
            skLineSegment(sketch, "E2002", {"start": v(386.95, 395.87) * mm, "end": v(386.99, 395.69) * mm});
            skLineSegment(sketch, "E2003", {"start": v(386.99, 395.69) * mm, "end": v(387, 395.5) * mm});
            skLineSegment(sketch, "E2004", {"start": v(387, 395.5) * mm, "end": v(386.99, 395.31) * mm});
            skLineSegment(sketch, "E2005", {"start": v(386.99, 395.31) * mm, "end": v(386.95, 395.13) * mm});
            skLineSegment(sketch, "E2006", {"start": v(386.95, 395.13) * mm, "end": v(386.9, 394.95) * mm});
            skLineSegment(sketch, "E2007", {"start": v(386.9, 394.95) * mm, "end": v(386.81, 394.78) * mm});
            skLineSegment(sketch, "E2008", {"start": v(386.81, 394.78) * mm, "end": v(386.71, 394.62) * mm});
            skLineSegment(sketch, "E2009", {"start": v(386.71, 394.62) * mm, "end": v(386.6, 394.47) * mm});
            skLineSegment(sketch, "E2010", {"start": v(386.6, 394.47) * mm, "end": v(386.46, 394.34) * mm});
            skLineSegment(sketch, "E2011", {"start": v(386.46, 394.34) * mm, "end": v(386.3, 394.23) * mm});
            skLineSegment(sketch, "E2012", {"start": v(386.3, 394.23) * mm, "end": v(386.14, 394.14) * mm});
            skLineSegment(sketch, "E2013", {"start": v(386.14, 394.14) * mm, "end": v(385.96, 394.07) * mm});
            skLineSegment(sketch, "E2014", {"start": v(385.96, 394.07) * mm, "end": v(385.78, 394.03) * mm});
            skLineSegment(sketch, "E2015", {"start": v(385.78, 394.03) * mm, "end": v(385.6, 394) * mm});
            skLineSegment(sketch, "E2016", {"start": v(385.6, 394) * mm, "end": v(385.4, 394) * mm});
            skLineSegment(sketch, "E2017", {"start": v(55.4, 394) * mm, "end": v(55.22, 394.03) * mm});
            skLineSegment(sketch, "E2018", {"start": v(55.22, 394.03) * mm, "end": v(55.04, 394.07) * mm});
            skLineSegment(sketch, "E2019", {"start": v(55.04, 394.07) * mm, "end": v(54.86, 394.14) * mm});
            skLineSegment(sketch, "E2020", {"start": v(54.86, 394.14) * mm, "end": v(54.7, 394.23) * mm});
            skLineSegment(sketch, "E2021", {"start": v(54.7, 394.23) * mm, "end": v(54.54, 394.34) * mm});
            skLineSegment(sketch, "E2022", {"start": v(54.54, 394.34) * mm, "end": v(54.4, 394.47) * mm});
            skLineSegment(sketch, "E2023", {"start": v(54.4, 394.47) * mm, "end": v(54.29, 394.62) * mm});
            skLineSegment(sketch, "E2024", {"start": v(54.29, 394.62) * mm, "end": v(54.19, 394.78) * mm});
            skLineSegment(sketch, "E2025", {"start": v(54.19, 394.78) * mm, "end": v(54.1, 394.95) * mm});
            skLineSegment(sketch, "E2026", {"start": v(54.1, 394.95) * mm, "end": v(54.05, 395.13) * mm});
            skLineSegment(sketch, "E2027", {"start": v(54.05, 395.13) * mm, "end": v(54.01, 395.31) * mm});
            skLineSegment(sketch, "E2028", {"start": v(54.01, 395.31) * mm, "end": v(54, 395.5) * mm});
            skLineSegment(sketch, "E2029", {"start": v(54, 395.5) * mm, "end": v(54.01, 395.69) * mm});
            skLineSegment(sketch, "E2030", {"start": v(54.01, 395.69) * mm, "end": v(54.05, 395.87) * mm});
            skLineSegment(sketch, "E2031", {"start": v(54.05, 395.87) * mm, "end": v(54.1, 396.05) * mm});
            skLineSegment(sketch, "E2032", {"start": v(54.1, 396.05) * mm, "end": v(54.19, 396.22) * mm});
            skLineSegment(sketch, "E2033", {"start": v(54.19, 396.22) * mm, "end": v(54.29, 396.38) * mm});
            skLineSegment(sketch, "E2034", {"start": v(54.29, 396.38) * mm, "end": v(54.4, 396.53) * mm});
            skLineSegment(sketch, "E2035", {"start": v(54.4, 396.53) * mm, "end": v(54.54, 396.66) * mm});
            skLineSegment(sketch, "E2036", {"start": v(54.54, 396.66) * mm, "end": v(54.7, 396.77) * mm});
            skLineSegment(sketch, "E2037", {"start": v(54.7, 396.77) * mm, "end": v(54.86, 396.86) * mm});
            skLineSegment(sketch, "E2038", {"start": v(54.86, 396.86) * mm, "end": v(55.04, 396.93) * mm});
            skLineSegment(sketch, "E2039", {"start": v(55.04, 396.93) * mm, "end": v(55.22, 396.97) * mm});
            skLineSegment(sketch, "E2040", {"start": v(55.22, 396.97) * mm, "end": v(55.4, 397) * mm});
            skLineSegment(sketch, "E2041", {"start": v(55.4, 397) * mm, "end": v(55.6, 397) * mm});
            skLineSegment(sketch, "E2042", {"start": v(55.6, 397) * mm, "end": v(55.78, 396.97) * mm});
            skLineSegment(sketch, "E2043", {"start": v(55.78, 396.97) * mm, "end": v(55.96, 396.93) * mm});
            skLineSegment(sketch, "E2044", {"start": v(55.96, 396.93) * mm, "end": v(56.14, 396.86) * mm});
            skLineSegment(sketch, "E2045", {"start": v(56.14, 396.86) * mm, "end": v(56.3, 396.77) * mm});
            skLineSegment(sketch, "E2046", {"start": v(56.3, 396.77) * mm, "end": v(56.46, 396.66) * mm});
            skLineSegment(sketch, "E2047", {"start": v(56.46, 396.66) * mm, "end": v(56.6, 396.53) * mm});
            skLineSegment(sketch, "E2048", {"start": v(56.6, 396.53) * mm, "end": v(56.71, 396.38) * mm});
            skLineSegment(sketch, "E2049", {"start": v(56.71, 396.38) * mm, "end": v(56.81, 396.22) * mm});
            skLineSegment(sketch, "E2050", {"start": v(56.81, 396.22) * mm, "end": v(56.9, 396.05) * mm});
            skLineSegment(sketch, "E2051", {"start": v(56.9, 396.05) * mm, "end": v(56.95, 395.87) * mm});
            skLineSegment(sketch, "E2052", {"start": v(56.95, 395.87) * mm, "end": v(56.99, 395.69) * mm});
            skLineSegment(sketch, "E2053", {"start": v(56.99, 395.69) * mm, "end": v(57, 395.5) * mm});
            skLineSegment(sketch, "E2054", {"start": v(57, 395.5) * mm, "end": v(56.99, 395.31) * mm});
            skLineSegment(sketch, "E2055", {"start": v(56.99, 395.31) * mm, "end": v(56.95, 395.13) * mm});
            skLineSegment(sketch, "E2056", {"start": v(56.95, 395.13) * mm, "end": v(56.9, 394.95) * mm});
            skLineSegment(sketch, "E2057", {"start": v(56.9, 394.95) * mm, "end": v(56.81, 394.78) * mm});
            skLineSegment(sketch, "E2058", {"start": v(56.81, 394.78) * mm, "end": v(56.71, 394.62) * mm});
            skLineSegment(sketch, "E2059", {"start": v(56.71, 394.62) * mm, "end": v(56.6, 394.47) * mm});
            skLineSegment(sketch, "E2060", {"start": v(56.6, 394.47) * mm, "end": v(56.46, 394.34) * mm});
            skLineSegment(sketch, "E2061", {"start": v(56.46, 394.34) * mm, "end": v(56.3, 394.23) * mm});
            skLineSegment(sketch, "E2062", {"start": v(56.3, 394.23) * mm, "end": v(56.14, 394.14) * mm});
            skLineSegment(sketch, "E2063", {"start": v(56.14, 394.14) * mm, "end": v(55.96, 394.07) * mm});
            skLineSegment(sketch, "E2064", {"start": v(55.96, 394.07) * mm, "end": v(55.78, 394.03) * mm});
            skLineSegment(sketch, "E2065", {"start": v(55.78, 394.03) * mm, "end": v(55.6, 394) * mm});
            skLineSegment(sketch, "E2066", {"start": v(55.6, 394) * mm, "end": v(55.4, 394) * mm});
            skLineSegment(sketch, "E2067", {"start": v(369.25, 368.02) * mm, "end": v(367.75, 368.21) * mm});
            skLineSegment(sketch, "E2068", {"start": v(367.75, 368.21) * mm, "end": v(366.3, 368.59) * mm});
            skLineSegment(sketch, "E2069", {"start": v(366.3, 368.59) * mm, "end": v(364.9, 369.14) * mm});
            skLineSegment(sketch, "E2070", {"start": v(364.9, 369.14) * mm, "end": v(363.57, 369.87) * mm});
            skLineSegment(sketch, "E2071", {"start": v(363.57, 369.87) * mm, "end": v(362.35, 370.75) * mm});
            skLineSegment(sketch, "E2072", {"start": v(362.35, 370.75) * mm, "end": v(361.25, 371.79) * mm});
            skLineSegment(sketch, "E2073", {"start": v(361.25, 371.79) * mm, "end": v(360.3, 372.95) * mm});
            skLineSegment(sketch, "E2074", {"start": v(360.3, 372.95) * mm, "end": v(359.48, 374.22) * mm});
            skLineSegment(sketch, "E2075", {"start": v(359.48, 374.22) * mm, "end": v(358.84, 375.58) * mm});
            skLineSegment(sketch, "E2076", {"start": v(358.84, 375.58) * mm, "end": v(358.38, 377.02) * mm});
            skLineSegment(sketch, "E2077", {"start": v(358.38, 377.02) * mm, "end": v(358.1, 378.5) * mm});
            skLineSegment(sketch, "E2078", {"start": v(358.1, 378.5) * mm, "end": v(358, 380) * mm});
            skLineSegment(sketch, "E2079", {"start": v(358, 380) * mm, "end": v(358.1, 381.5) * mm});
            skLineSegment(sketch, "E2080", {"start": v(358.1, 381.5) * mm, "end": v(358.38, 382.98) * mm});
            skLineSegment(sketch, "E2081", {"start": v(358.38, 382.98) * mm, "end": v(358.84, 384.42) * mm});
            skLineSegment(sketch, "E2082", {"start": v(358.84, 384.42) * mm, "end": v(359.48, 385.78) * mm});
            skLineSegment(sketch, "E2083", {"start": v(359.48, 385.78) * mm, "end": v(360.3, 387.05) * mm});
            skLineSegment(sketch, "E2084", {"start": v(360.3, 387.05) * mm, "end": v(361.25, 388.21) * mm});
            skLineSegment(sketch, "E2085", {"start": v(361.25, 388.21) * mm, "end": v(362.35, 389.25) * mm});
            skLineSegment(sketch, "E2086", {"start": v(362.35, 389.25) * mm, "end": v(363.57, 390.13) * mm});
            skLineSegment(sketch, "E2087", {"start": v(363.57, 390.13) * mm, "end": v(364.9, 390.86) * mm});
            skLineSegment(sketch, "E2088", {"start": v(364.9, 390.86) * mm, "end": v(366.3, 391.41) * mm});
            skLineSegment(sketch, "E2089", {"start": v(366.3, 391.41) * mm, "end": v(367.75, 391.79) * mm});
            skLineSegment(sketch, "E2090", {"start": v(367.75, 391.79) * mm, "end": v(369.25, 391.98) * mm});
            skLineSegment(sketch, "E2091", {"start": v(369.25, 391.98) * mm, "end": v(370.75, 391.98) * mm});
            skLineSegment(sketch, "E2092", {"start": v(370.75, 391.98) * mm, "end": v(372.25, 391.79) * mm});
            skLineSegment(sketch, "E2093", {"start": v(372.25, 391.79) * mm, "end": v(373.7, 391.41) * mm});
            skLineSegment(sketch, "E2094", {"start": v(373.7, 391.41) * mm, "end": v(375.1, 390.86) * mm});
            skLineSegment(sketch, "E2095", {"start": v(375.1, 390.86) * mm, "end": v(376.43, 390.13) * mm});
            skLineSegment(sketch, "E2096", {"start": v(376.43, 390.13) * mm, "end": v(377.65, 389.25) * mm});
            skLineSegment(sketch, "E2097", {"start": v(377.65, 389.25) * mm, "end": v(378.75, 388.21) * mm});
            skLineSegment(sketch, "E2098", {"start": v(378.75, 388.21) * mm, "end": v(379.7, 387.05) * mm});
            skLineSegment(sketch, "E2099", {"start": v(379.7, 387.05) * mm, "end": v(380.52, 385.78) * mm});
            skLineSegment(sketch, "E2100", {"start": v(380.52, 385.78) * mm, "end": v(381.16, 384.42) * mm});
            skLineSegment(sketch, "E2101", {"start": v(381.16, 384.42) * mm, "end": v(381.62, 382.98) * mm});
            skLineSegment(sketch, "E2102", {"start": v(381.62, 382.98) * mm, "end": v(381.9, 381.5) * mm});
            skLineSegment(sketch, "E2103", {"start": v(381.9, 381.5) * mm, "end": v(382, 380) * mm});
            skLineSegment(sketch, "E2104", {"start": v(382, 380) * mm, "end": v(381.9, 378.5) * mm});
            skLineSegment(sketch, "E2105", {"start": v(381.9, 378.5) * mm, "end": v(381.62, 377.02) * mm});
            skLineSegment(sketch, "E2106", {"start": v(381.62, 377.02) * mm, "end": v(381.16, 375.58) * mm});
            skLineSegment(sketch, "E2107", {"start": v(381.16, 375.58) * mm, "end": v(380.52, 374.22) * mm});
            skLineSegment(sketch, "E2108", {"start": v(380.52, 374.22) * mm, "end": v(379.7, 372.95) * mm});
            skLineSegment(sketch, "E2109", {"start": v(379.7, 372.95) * mm, "end": v(378.75, 371.79) * mm});
            skLineSegment(sketch, "E2110", {"start": v(378.75, 371.79) * mm, "end": v(377.65, 370.75) * mm});
            skLineSegment(sketch, "E2111", {"start": v(377.65, 370.75) * mm, "end": v(376.43, 369.87) * mm});
            skLineSegment(sketch, "E2112", {"start": v(376.43, 369.87) * mm, "end": v(375.1, 369.14) * mm});
            skLineSegment(sketch, "E2113", {"start": v(375.1, 369.14) * mm, "end": v(373.7, 368.59) * mm});
            skLineSegment(sketch, "E2114", {"start": v(373.7, 368.59) * mm, "end": v(372.25, 368.21) * mm});
            skLineSegment(sketch, "E2115", {"start": v(372.25, 368.21) * mm, "end": v(370.75, 368.02) * mm});
            skLineSegment(sketch, "E2116", {"start": v(370.75, 368.02) * mm, "end": v(369.25, 368.02) * mm});
            skLineSegment(sketch, "E2117", {"start": v(39.25, 368.02) * mm, "end": v(37.75, 368.21) * mm});
            skLineSegment(sketch, "E2118", {"start": v(37.75, 368.21) * mm, "end": v(36.3, 368.59) * mm});
            skLineSegment(sketch, "E2119", {"start": v(36.3, 368.59) * mm, "end": v(34.9, 369.14) * mm});
            skLineSegment(sketch, "E2120", {"start": v(34.9, 369.14) * mm, "end": v(33.57, 369.87) * mm});
            skLineSegment(sketch, "E2121", {"start": v(33.57, 369.87) * mm, "end": v(32.35, 370.75) * mm});
            skLineSegment(sketch, "E2122", {"start": v(32.35, 370.75) * mm, "end": v(31.25, 371.79) * mm});
            skLineSegment(sketch, "E2123", {"start": v(31.25, 371.79) * mm, "end": v(30.3, 372.95) * mm});
            skLineSegment(sketch, "E2124", {"start": v(30.3, 372.95) * mm, "end": v(29.48, 374.22) * mm});
            skLineSegment(sketch, "E2125", {"start": v(29.48, 374.22) * mm, "end": v(28.84, 375.58) * mm});
            skLineSegment(sketch, "E2126", {"start": v(28.84, 375.58) * mm, "end": v(28.38, 377.02) * mm});
            skLineSegment(sketch, "E2127", {"start": v(28.38, 377.02) * mm, "end": v(28.1, 378.5) * mm});
            skLineSegment(sketch, "E2128", {"start": v(28.1, 378.5) * mm, "end": v(28, 380) * mm});
            skLineSegment(sketch, "E2129", {"start": v(28, 380) * mm, "end": v(28.1, 381.5) * mm});
            skLineSegment(sketch, "E2130", {"start": v(28.1, 381.5) * mm, "end": v(28.38, 382.98) * mm});
            skLineSegment(sketch, "E2131", {"start": v(28.38, 382.98) * mm, "end": v(28.84, 384.42) * mm});
            skLineSegment(sketch, "E2132", {"start": v(28.84, 384.42) * mm, "end": v(29.48, 385.78) * mm});
            skLineSegment(sketch, "E2133", {"start": v(29.48, 385.78) * mm, "end": v(30.3, 387.05) * mm});
            skLineSegment(sketch, "E2134", {"start": v(30.3, 387.05) * mm, "end": v(31.25, 388.21) * mm});
            skLineSegment(sketch, "E2135", {"start": v(31.25, 388.21) * mm, "end": v(32.35, 389.25) * mm});
            skLineSegment(sketch, "E2136", {"start": v(32.35, 389.25) * mm, "end": v(33.57, 390.13) * mm});
            skLineSegment(sketch, "E2137", {"start": v(33.57, 390.13) * mm, "end": v(34.9, 390.86) * mm});
            skLineSegment(sketch, "E2138", {"start": v(34.9, 390.86) * mm, "end": v(36.3, 391.41) * mm});
            skLineSegment(sketch, "E2139", {"start": v(36.3, 391.41) * mm, "end": v(37.75, 391.79) * mm});
            skLineSegment(sketch, "E2140", {"start": v(37.75, 391.79) * mm, "end": v(39.25, 391.98) * mm});
            skLineSegment(sketch, "E2141", {"start": v(39.25, 391.98) * mm, "end": v(40.75, 391.98) * mm});
            skLineSegment(sketch, "E2142", {"start": v(40.75, 391.98) * mm, "end": v(42.25, 391.79) * mm});
            skLineSegment(sketch, "E2143", {"start": v(42.25, 391.79) * mm, "end": v(43.7, 391.41) * mm});
            skLineSegment(sketch, "E2144", {"start": v(43.7, 391.41) * mm, "end": v(45.1, 390.86) * mm});
            skLineSegment(sketch, "E2145", {"start": v(45.1, 390.86) * mm, "end": v(46.43, 390.13) * mm});
            skLineSegment(sketch, "E2146", {"start": v(46.43, 390.13) * mm, "end": v(47.65, 389.25) * mm});
            skLineSegment(sketch, "E2147", {"start": v(47.65, 389.25) * mm, "end": v(48.75, 388.21) * mm});
            skLineSegment(sketch, "E2148", {"start": v(48.75, 388.21) * mm, "end": v(49.7, 387.05) * mm});
            skLineSegment(sketch, "E2149", {"start": v(49.7, 387.05) * mm, "end": v(50.52, 385.78) * mm});
            skLineSegment(sketch, "E2150", {"start": v(50.52, 385.78) * mm, "end": v(51.16, 384.42) * mm});
            skLineSegment(sketch, "E2151", {"start": v(51.16, 384.42) * mm, "end": v(51.62, 382.98) * mm});
            skLineSegment(sketch, "E2152", {"start": v(51.62, 382.98) * mm, "end": v(51.9, 381.5) * mm});
            skLineSegment(sketch, "E2153", {"start": v(51.9, 381.5) * mm, "end": v(52, 380) * mm});
            skLineSegment(sketch, "E2154", {"start": v(52, 380) * mm, "end": v(51.9, 378.5) * mm});
            skLineSegment(sketch, "E2155", {"start": v(51.9, 378.5) * mm, "end": v(51.62, 377.02) * mm});
            skLineSegment(sketch, "E2156", {"start": v(51.62, 377.02) * mm, "end": v(51.16, 375.58) * mm});
            skLineSegment(sketch, "E2157", {"start": v(51.16, 375.58) * mm, "end": v(50.52, 374.22) * mm});
            skLineSegment(sketch, "E2158", {"start": v(50.52, 374.22) * mm, "end": v(49.7, 372.95) * mm});
            skLineSegment(sketch, "E2159", {"start": v(49.7, 372.95) * mm, "end": v(48.75, 371.79) * mm});
            skLineSegment(sketch, "E2160", {"start": v(48.75, 371.79) * mm, "end": v(47.65, 370.75) * mm});
            skLineSegment(sketch, "E2161", {"start": v(47.65, 370.75) * mm, "end": v(46.43, 369.87) * mm});
            skLineSegment(sketch, "E2162", {"start": v(46.43, 369.87) * mm, "end": v(45.1, 369.14) * mm});
            skLineSegment(sketch, "E2163", {"start": v(45.1, 369.14) * mm, "end": v(43.7, 368.59) * mm});
            skLineSegment(sketch, "E2164", {"start": v(43.7, 368.59) * mm, "end": v(42.25, 368.21) * mm});
            skLineSegment(sketch, "E2165", {"start": v(42.25, 368.21) * mm, "end": v(40.75, 368.02) * mm});
            skLineSegment(sketch, "E2166", {"start": v(40.75, 368.02) * mm, "end": v(39.25, 368.02) * mm});
            skLineSegment(sketch, "E2167", {"start": v(22.75, 376) * mm, "end": v(22.25, 376.07) * mm});
            skLineSegment(sketch, "E2168", {"start": v(22.25, 376.07) * mm, "end": v(21.76, 376.2) * mm});
            skLineSegment(sketch, "E2169", {"start": v(21.76, 376.2) * mm, "end": v(21.3, 376.38) * mm});
            skLineSegment(sketch, "E2170", {"start": v(21.3, 376.38) * mm, "end": v(20.86, 376.62) * mm});
            skLineSegment(sketch, "E2171", {"start": v(20.86, 376.62) * mm, "end": v(20.45, 376.92) * mm});
            skLineSegment(sketch, "E2172", {"start": v(20.45, 376.92) * mm, "end": v(20.08, 377.26) * mm});
            skLineSegment(sketch, "E2173", {"start": v(20.08, 377.26) * mm, "end": v(19.76, 377.65) * mm});
            skLineSegment(sketch, "E2174", {"start": v(19.76, 377.65) * mm, "end": v(19.5, 378.07) * mm});
            skLineSegment(sketch, "E2175", {"start": v(19.5, 378.07) * mm, "end": v(19.28, 378.53) * mm});
            skLineSegment(sketch, "E2176", {"start": v(19.28, 378.53) * mm, "end": v(19.13, 379) * mm});
            skLineSegment(sketch, "E2177", {"start": v(19.13, 379) * mm, "end": v(19.03, 379.5) * mm});
            skLineSegment(sketch, "E2178", {"start": v(19.03, 379.5) * mm, "end": v(19, 380) * mm});
            skLineSegment(sketch, "E2179", {"start": v(19, 380) * mm, "end": v(19.03, 380.5) * mm});
            skLineSegment(sketch, "E2180", {"start": v(19.03, 380.5) * mm, "end": v(19.13, 381) * mm});
            skLineSegment(sketch, "E2181", {"start": v(19.13, 381) * mm, "end": v(19.28, 381.47) * mm});
            skLineSegment(sketch, "E2182", {"start": v(19.28, 381.47) * mm, "end": v(19.5, 381.93) * mm});
            skLineSegment(sketch, "E2183", {"start": v(19.5, 381.93) * mm, "end": v(19.76, 382.35) * mm});
            skLineSegment(sketch, "E2184", {"start": v(19.76, 382.35) * mm, "end": v(20.08, 382.74) * mm});
            skLineSegment(sketch, "E2185", {"start": v(20.08, 382.74) * mm, "end": v(20.45, 383.08) * mm});
            skLineSegment(sketch, "E2186", {"start": v(20.45, 383.08) * mm, "end": v(20.86, 383.38) * mm});
            skLineSegment(sketch, "E2187", {"start": v(20.86, 383.38) * mm, "end": v(21.3, 383.62) * mm});
            skLineSegment(sketch, "E2188", {"start": v(21.3, 383.62) * mm, "end": v(21.76, 383.8) * mm});
            skLineSegment(sketch, "E2189", {"start": v(21.76, 383.8) * mm, "end": v(22.25, 383.93) * mm});
            skLineSegment(sketch, "E2190", {"start": v(22.25, 383.93) * mm, "end": v(22.75, 384) * mm});
            skLineSegment(sketch, "E2191", {"start": v(22.75, 384) * mm, "end": v(23.25, 384) * mm});
            skLineSegment(sketch, "E2192", {"start": v(23.25, 384) * mm, "end": v(23.75, 383.93) * mm});
            skLineSegment(sketch, "E2193", {"start": v(23.75, 383.93) * mm, "end": v(24.24, 383.8) * mm});
            skLineSegment(sketch, "E2194", {"start": v(24.24, 383.8) * mm, "end": v(24.7, 383.62) * mm});
            skLineSegment(sketch, "E2195", {"start": v(24.7, 383.62) * mm, "end": v(25.14, 383.38) * mm});
            skLineSegment(sketch, "E2196", {"start": v(25.14, 383.38) * mm, "end": v(25.55, 383.08) * mm});
            skLineSegment(sketch, "E2197", {"start": v(25.55, 383.08) * mm, "end": v(25.92, 382.74) * mm});
            skLineSegment(sketch, "E2198", {"start": v(25.92, 382.74) * mm, "end": v(26.24, 382.35) * mm});
            skLineSegment(sketch, "E2199", {"start": v(26.24, 382.35) * mm, "end": v(26.5, 381.93) * mm});
            skLineSegment(sketch, "E2200", {"start": v(26.5, 381.93) * mm, "end": v(26.72, 381.47) * mm});
            skLineSegment(sketch, "E2201", {"start": v(26.72, 381.47) * mm, "end": v(26.87, 381) * mm});
            skLineSegment(sketch, "E2202", {"start": v(26.87, 381) * mm, "end": v(26.97, 380.5) * mm});
            skLineSegment(sketch, "E2203", {"start": v(26.97, 380.5) * mm, "end": v(27, 380) * mm});
            skLineSegment(sketch, "E2204", {"start": v(27, 380) * mm, "end": v(26.97, 379.5) * mm});
            skLineSegment(sketch, "E2205", {"start": v(26.97, 379.5) * mm, "end": v(26.87, 379) * mm});
            skLineSegment(sketch, "E2206", {"start": v(26.87, 379) * mm, "end": v(26.72, 378.53) * mm});
            skLineSegment(sketch, "E2207", {"start": v(26.72, 378.53) * mm, "end": v(26.5, 378.07) * mm});
            skLineSegment(sketch, "E2208", {"start": v(26.5, 378.07) * mm, "end": v(26.24, 377.65) * mm});
            skLineSegment(sketch, "E2209", {"start": v(26.24, 377.65) * mm, "end": v(25.92, 377.26) * mm});
            skLineSegment(sketch, "E2210", {"start": v(25.92, 377.26) * mm, "end": v(25.55, 376.92) * mm});
            skLineSegment(sketch, "E2211", {"start": v(25.55, 376.92) * mm, "end": v(25.14, 376.62) * mm});
            skLineSegment(sketch, "E2212", {"start": v(25.14, 376.62) * mm, "end": v(24.7, 376.38) * mm});
            skLineSegment(sketch, "E2213", {"start": v(24.7, 376.38) * mm, "end": v(24.24, 376.2) * mm});
            skLineSegment(sketch, "E2214", {"start": v(24.24, 376.2) * mm, "end": v(23.75, 376.07) * mm});
            skLineSegment(sketch, "E2215", {"start": v(23.75, 376.07) * mm, "end": v(23.25, 376) * mm});
            skLineSegment(sketch, "E2216", {"start": v(23.25, 376) * mm, "end": v(22.75, 376) * mm});
            skLineSegment(sketch, "E2217", {"start": v(386.75, 376) * mm, "end": v(386.25, 376.07) * mm});
            skLineSegment(sketch, "E2218", {"start": v(386.25, 376.07) * mm, "end": v(385.76, 376.2) * mm});
            skLineSegment(sketch, "E2219", {"start": v(385.76, 376.2) * mm, "end": v(385.3, 376.38) * mm});
            skLineSegment(sketch, "E2220", {"start": v(385.3, 376.38) * mm, "end": v(384.86, 376.62) * mm});
            skLineSegment(sketch, "E2221", {"start": v(384.86, 376.62) * mm, "end": v(384.45, 376.92) * mm});
            skLineSegment(sketch, "E2222", {"start": v(384.45, 376.92) * mm, "end": v(384.08, 377.26) * mm});
            skLineSegment(sketch, "E2223", {"start": v(384.08, 377.26) * mm, "end": v(383.76, 377.65) * mm});
            skLineSegment(sketch, "E2224", {"start": v(383.76, 377.65) * mm, "end": v(383.5, 378.07) * mm});
            skLineSegment(sketch, "E2225", {"start": v(383.5, 378.07) * mm, "end": v(383.28, 378.53) * mm});
            skLineSegment(sketch, "E2226", {"start": v(383.28, 378.53) * mm, "end": v(383.13, 379) * mm});
            skLineSegment(sketch, "E2227", {"start": v(383.13, 379) * mm, "end": v(383.03, 379.5) * mm});
            skLineSegment(sketch, "E2228", {"start": v(383.03, 379.5) * mm, "end": v(383, 380) * mm});
            skLineSegment(sketch, "E2229", {"start": v(383, 380) * mm, "end": v(383.03, 380.5) * mm});
            skLineSegment(sketch, "E2230", {"start": v(383.03, 380.5) * mm, "end": v(383.13, 381) * mm});
            skLineSegment(sketch, "E2231", {"start": v(383.13, 381) * mm, "end": v(383.28, 381.47) * mm});
            skLineSegment(sketch, "E2232", {"start": v(383.28, 381.47) * mm, "end": v(383.5, 381.93) * mm});
            skLineSegment(sketch, "E2233", {"start": v(383.5, 381.93) * mm, "end": v(383.76, 382.35) * mm});
            skLineSegment(sketch, "E2234", {"start": v(383.76, 382.35) * mm, "end": v(384.08, 382.74) * mm});
            skLineSegment(sketch, "E2235", {"start": v(384.08, 382.74) * mm, "end": v(384.45, 383.08) * mm});
            skLineSegment(sketch, "E2236", {"start": v(384.45, 383.08) * mm, "end": v(384.86, 383.38) * mm});
            skLineSegment(sketch, "E2237", {"start": v(384.86, 383.38) * mm, "end": v(385.3, 383.62) * mm});
            skLineSegment(sketch, "E2238", {"start": v(385.3, 383.62) * mm, "end": v(385.76, 383.8) * mm});
            skLineSegment(sketch, "E2239", {"start": v(385.76, 383.8) * mm, "end": v(386.25, 383.93) * mm});
            skLineSegment(sketch, "E2240", {"start": v(386.25, 383.93) * mm, "end": v(386.75, 384) * mm});
            skLineSegment(sketch, "E2241", {"start": v(386.75, 384) * mm, "end": v(387.25, 384) * mm});
            skLineSegment(sketch, "E2242", {"start": v(387.25, 384) * mm, "end": v(387.75, 383.93) * mm});
            skLineSegment(sketch, "E2243", {"start": v(387.75, 383.93) * mm, "end": v(388.24, 383.8) * mm});
            skLineSegment(sketch, "E2244", {"start": v(388.24, 383.8) * mm, "end": v(388.7, 383.62) * mm});
            skLineSegment(sketch, "E2245", {"start": v(388.7, 383.62) * mm, "end": v(389.14, 383.38) * mm});
            skLineSegment(sketch, "E2246", {"start": v(389.14, 383.38) * mm, "end": v(389.55, 383.08) * mm});
            skLineSegment(sketch, "E2247", {"start": v(389.55, 383.08) * mm, "end": v(389.92, 382.74) * mm});
            skLineSegment(sketch, "E2248", {"start": v(389.92, 382.74) * mm, "end": v(390.24, 382.35) * mm});
            skLineSegment(sketch, "E2249", {"start": v(390.24, 382.35) * mm, "end": v(390.5, 381.93) * mm});
            skLineSegment(sketch, "E2250", {"start": v(390.5, 381.93) * mm, "end": v(390.72, 381.47) * mm});
            skLineSegment(sketch, "E2251", {"start": v(390.72, 381.47) * mm, "end": v(390.87, 381) * mm});
            skLineSegment(sketch, "E2252", {"start": v(390.87, 381) * mm, "end": v(390.97, 380.5) * mm});
            skLineSegment(sketch, "E2253", {"start": v(390.97, 380.5) * mm, "end": v(391, 380) * mm});
            skLineSegment(sketch, "E2254", {"start": v(391, 380) * mm, "end": v(390.97, 379.5) * mm});
            skLineSegment(sketch, "E2255", {"start": v(390.97, 379.5) * mm, "end": v(390.87, 379) * mm});
            skLineSegment(sketch, "E2256", {"start": v(390.87, 379) * mm, "end": v(390.72, 378.53) * mm});
            skLineSegment(sketch, "E2257", {"start": v(390.72, 378.53) * mm, "end": v(390.5, 378.07) * mm});
            skLineSegment(sketch, "E2258", {"start": v(390.5, 378.07) * mm, "end": v(390.24, 377.65) * mm});
            skLineSegment(sketch, "E2259", {"start": v(390.24, 377.65) * mm, "end": v(389.92, 377.26) * mm});
            skLineSegment(sketch, "E2260", {"start": v(389.92, 377.26) * mm, "end": v(389.55, 376.92) * mm});
            skLineSegment(sketch, "E2261", {"start": v(389.55, 376.92) * mm, "end": v(389.14, 376.62) * mm});
            skLineSegment(sketch, "E2262", {"start": v(389.14, 376.62) * mm, "end": v(388.7, 376.38) * mm});
            skLineSegment(sketch, "E2263", {"start": v(388.7, 376.38) * mm, "end": v(388.24, 376.2) * mm});
            skLineSegment(sketch, "E2264", {"start": v(388.24, 376.2) * mm, "end": v(387.75, 376.07) * mm});
            skLineSegment(sketch, "E2265", {"start": v(387.75, 376.07) * mm, "end": v(387.25, 376) * mm});
            skLineSegment(sketch, "E2266", {"start": v(387.25, 376) * mm, "end": v(386.75, 376) * mm});
            skLineSegment(sketch, "E2267", {"start": v(354.4, 363) * mm, "end": v(354.22, 363.03) * mm});
            skLineSegment(sketch, "E2268", {"start": v(354.22, 363.03) * mm, "end": v(354.04, 363.07) * mm});
            skLineSegment(sketch, "E2269", {"start": v(354.04, 363.07) * mm, "end": v(353.86, 363.14) * mm});
            skLineSegment(sketch, "E2270", {"start": v(353.86, 363.14) * mm, "end": v(353.7, 363.23) * mm});
            skLineSegment(sketch, "E2271", {"start": v(353.7, 363.23) * mm, "end": v(353.54, 363.34) * mm});
            skLineSegment(sketch, "E2272", {"start": v(353.54, 363.34) * mm, "end": v(353.4, 363.47) * mm});
            skLineSegment(sketch, "E2273", {"start": v(353.4, 363.47) * mm, "end": v(353.29, 363.62) * mm});
            skLineSegment(sketch, "E2274", {"start": v(353.29, 363.62) * mm, "end": v(353.19, 363.78) * mm});
            skLineSegment(sketch, "E2275", {"start": v(353.19, 363.78) * mm, "end": v(353.1, 363.95) * mm});
            skLineSegment(sketch, "E2276", {"start": v(353.1, 363.95) * mm, "end": v(353.05, 364.13) * mm});
            skLineSegment(sketch, "E2277", {"start": v(353.05, 364.13) * mm, "end": v(353.01, 364.31) * mm});
            skLineSegment(sketch, "E2278", {"start": v(353.01, 364.31) * mm, "end": v(353, 364.5) * mm});
            skLineSegment(sketch, "E2279", {"start": v(353, 364.5) * mm, "end": v(353.01, 364.69) * mm});
            skLineSegment(sketch, "E2280", {"start": v(353.01, 364.69) * mm, "end": v(353.05, 364.87) * mm});
            skLineSegment(sketch, "E2281", {"start": v(353.05, 364.87) * mm, "end": v(353.1, 365.05) * mm});
            skLineSegment(sketch, "E2282", {"start": v(353.1, 365.05) * mm, "end": v(353.19, 365.22) * mm});
            skLineSegment(sketch, "E2283", {"start": v(353.19, 365.22) * mm, "end": v(353.29, 365.38) * mm});
            skLineSegment(sketch, "E2284", {"start": v(353.29, 365.38) * mm, "end": v(353.4, 365.53) * mm});
            skLineSegment(sketch, "E2285", {"start": v(353.4, 365.53) * mm, "end": v(353.54, 365.66) * mm});
            skLineSegment(sketch, "E2286", {"start": v(353.54, 365.66) * mm, "end": v(353.7, 365.77) * mm});
            skLineSegment(sketch, "E2287", {"start": v(353.7, 365.77) * mm, "end": v(353.86, 365.86) * mm});
            skLineSegment(sketch, "E2288", {"start": v(353.86, 365.86) * mm, "end": v(354.04, 365.93) * mm});
            skLineSegment(sketch, "E2289", {"start": v(354.04, 365.93) * mm, "end": v(354.22, 365.97) * mm});
            skLineSegment(sketch, "E2290", {"start": v(354.22, 365.97) * mm, "end": v(354.4, 366) * mm});
            skLineSegment(sketch, "E2291", {"start": v(354.4, 366) * mm, "end": v(354.6, 366) * mm});
            skLineSegment(sketch, "E2292", {"start": v(354.6, 366) * mm, "end": v(354.78, 365.97) * mm});
            skLineSegment(sketch, "E2293", {"start": v(354.78, 365.97) * mm, "end": v(354.96, 365.93) * mm});
            skLineSegment(sketch, "E2294", {"start": v(354.96, 365.93) * mm, "end": v(355.14, 365.86) * mm});
            skLineSegment(sketch, "E2295", {"start": v(355.14, 365.86) * mm, "end": v(355.3, 365.77) * mm});
            skLineSegment(sketch, "E2296", {"start": v(355.3, 365.77) * mm, "end": v(355.46, 365.66) * mm});
            skLineSegment(sketch, "E2297", {"start": v(355.46, 365.66) * mm, "end": v(355.6, 365.53) * mm});
            skLineSegment(sketch, "E2298", {"start": v(355.6, 365.53) * mm, "end": v(355.71, 365.38) * mm});
            skLineSegment(sketch, "E2299", {"start": v(355.71, 365.38) * mm, "end": v(355.81, 365.22) * mm});
            skLineSegment(sketch, "E2300", {"start": v(355.81, 365.22) * mm, "end": v(355.9, 365.05) * mm});
            skLineSegment(sketch, "E2301", {"start": v(355.9, 365.05) * mm, "end": v(355.95, 364.87) * mm});
            skLineSegment(sketch, "E2302", {"start": v(355.95, 364.87) * mm, "end": v(355.99, 364.69) * mm});
            skLineSegment(sketch, "E2303", {"start": v(355.99, 364.69) * mm, "end": v(356, 364.5) * mm});
            skLineSegment(sketch, "E2304", {"start": v(356, 364.5) * mm, "end": v(355.99, 364.31) * mm});
            skLineSegment(sketch, "E2305", {"start": v(355.99, 364.31) * mm, "end": v(355.95, 364.13) * mm});
            skLineSegment(sketch, "E2306", {"start": v(355.95, 364.13) * mm, "end": v(355.9, 363.95) * mm});
            skLineSegment(sketch, "E2307", {"start": v(355.9, 363.95) * mm, "end": v(355.81, 363.78) * mm});
            skLineSegment(sketch, "E2308", {"start": v(355.81, 363.78) * mm, "end": v(355.71, 363.62) * mm});
            skLineSegment(sketch, "E2309", {"start": v(355.71, 363.62) * mm, "end": v(355.6, 363.47) * mm});
            skLineSegment(sketch, "E2310", {"start": v(355.6, 363.47) * mm, "end": v(355.46, 363.34) * mm});
            skLineSegment(sketch, "E2311", {"start": v(355.46, 363.34) * mm, "end": v(355.3, 363.23) * mm});
            skLineSegment(sketch, "E2312", {"start": v(355.3, 363.23) * mm, "end": v(355.14, 363.14) * mm});
            skLineSegment(sketch, "E2313", {"start": v(355.14, 363.14) * mm, "end": v(354.96, 363.07) * mm});
            skLineSegment(sketch, "E2314", {"start": v(354.96, 363.07) * mm, "end": v(354.78, 363.03) * mm});
            skLineSegment(sketch, "E2315", {"start": v(354.78, 363.03) * mm, "end": v(354.6, 363) * mm});
            skLineSegment(sketch, "E2316", {"start": v(354.6, 363) * mm, "end": v(354.4, 363) * mm});
            skLineSegment(sketch, "E2317", {"start": v(24.4, 363) * mm, "end": v(24.22, 363.03) * mm});
            skLineSegment(sketch, "E2318", {"start": v(24.22, 363.03) * mm, "end": v(24.04, 363.07) * mm});
            skLineSegment(sketch, "E2319", {"start": v(24.04, 363.07) * mm, "end": v(23.86, 363.14) * mm});
            skLineSegment(sketch, "E2320", {"start": v(23.86, 363.14) * mm, "end": v(23.7, 363.23) * mm});
            skLineSegment(sketch, "E2321", {"start": v(23.7, 363.23) * mm, "end": v(23.54, 363.34) * mm});
            skLineSegment(sketch, "E2322", {"start": v(23.54, 363.34) * mm, "end": v(23.4, 363.47) * mm});
            skLineSegment(sketch, "E2323", {"start": v(23.4, 363.47) * mm, "end": v(23.29, 363.62) * mm});
            skLineSegment(sketch, "E2324", {"start": v(23.29, 363.62) * mm, "end": v(23.19, 363.78) * mm});
            skLineSegment(sketch, "E2325", {"start": v(23.19, 363.78) * mm, "end": v(23.1, 363.95) * mm});
            skLineSegment(sketch, "E2326", {"start": v(23.1, 363.95) * mm, "end": v(23.05, 364.13) * mm});
            skLineSegment(sketch, "E2327", {"start": v(23.05, 364.13) * mm, "end": v(23.01, 364.31) * mm});
            skLineSegment(sketch, "E2328", {"start": v(23.01, 364.31) * mm, "end": v(23, 364.5) * mm});
            skLineSegment(sketch, "E2329", {"start": v(23, 364.5) * mm, "end": v(23.01, 364.69) * mm});
            skLineSegment(sketch, "E2330", {"start": v(23.01, 364.69) * mm, "end": v(23.05, 364.87) * mm});
            skLineSegment(sketch, "E2331", {"start": v(23.05, 364.87) * mm, "end": v(23.1, 365.05) * mm});
            skLineSegment(sketch, "E2332", {"start": v(23.1, 365.05) * mm, "end": v(23.19, 365.22) * mm});
            skLineSegment(sketch, "E2333", {"start": v(23.19, 365.22) * mm, "end": v(23.29, 365.38) * mm});
            skLineSegment(sketch, "E2334", {"start": v(23.29, 365.38) * mm, "end": v(23.4, 365.53) * mm});
            skLineSegment(sketch, "E2335", {"start": v(23.4, 365.53) * mm, "end": v(23.54, 365.66) * mm});
            skLineSegment(sketch, "E2336", {"start": v(23.54, 365.66) * mm, "end": v(23.7, 365.77) * mm});
            skLineSegment(sketch, "E2337", {"start": v(23.7, 365.77) * mm, "end": v(23.86, 365.86) * mm});
            skLineSegment(sketch, "E2338", {"start": v(23.86, 365.86) * mm, "end": v(24.04, 365.93) * mm});
            skLineSegment(sketch, "E2339", {"start": v(24.04, 365.93) * mm, "end": v(24.22, 365.97) * mm});
            skLineSegment(sketch, "E2340", {"start": v(24.22, 365.97) * mm, "end": v(24.4, 366) * mm});
            skLineSegment(sketch, "E2341", {"start": v(24.4, 366) * mm, "end": v(24.6, 366) * mm});
            skLineSegment(sketch, "E2342", {"start": v(24.6, 366) * mm, "end": v(24.78, 365.97) * mm});
            skLineSegment(sketch, "E2343", {"start": v(24.78, 365.97) * mm, "end": v(24.96, 365.93) * mm});
            skLineSegment(sketch, "E2344", {"start": v(24.96, 365.93) * mm, "end": v(25.14, 365.86) * mm});
            skLineSegment(sketch, "E2345", {"start": v(25.14, 365.86) * mm, "end": v(25.3, 365.77) * mm});
            skLineSegment(sketch, "E2346", {"start": v(25.3, 365.77) * mm, "end": v(25.46, 365.66) * mm});
            skLineSegment(sketch, "E2347", {"start": v(25.46, 365.66) * mm, "end": v(25.6, 365.53) * mm});
            skLineSegment(sketch, "E2348", {"start": v(25.6, 365.53) * mm, "end": v(25.71, 365.38) * mm});
            skLineSegment(sketch, "E2349", {"start": v(25.71, 365.38) * mm, "end": v(25.81, 365.22) * mm});
            skLineSegment(sketch, "E2350", {"start": v(25.81, 365.22) * mm, "end": v(25.9, 365.05) * mm});
            skLineSegment(sketch, "E2351", {"start": v(25.9, 365.05) * mm, "end": v(25.95, 364.87) * mm});
            skLineSegment(sketch, "E2352", {"start": v(25.95, 364.87) * mm, "end": v(25.99, 364.69) * mm});
            skLineSegment(sketch, "E2353", {"start": v(25.99, 364.69) * mm, "end": v(26, 364.5) * mm});
            skLineSegment(sketch, "E2354", {"start": v(26, 364.5) * mm, "end": v(25.99, 364.31) * mm});
            skLineSegment(sketch, "E2355", {"start": v(25.99, 364.31) * mm, "end": v(25.95, 364.13) * mm});
            skLineSegment(sketch, "E2356", {"start": v(25.95, 364.13) * mm, "end": v(25.9, 363.95) * mm});
            skLineSegment(sketch, "E2357", {"start": v(25.9, 363.95) * mm, "end": v(25.81, 363.78) * mm});
            skLineSegment(sketch, "E2358", {"start": v(25.81, 363.78) * mm, "end": v(25.71, 363.62) * mm});
            skLineSegment(sketch, "E2359", {"start": v(25.71, 363.62) * mm, "end": v(25.6, 363.47) * mm});
            skLineSegment(sketch, "E2360", {"start": v(25.6, 363.47) * mm, "end": v(25.46, 363.34) * mm});
            skLineSegment(sketch, "E2361", {"start": v(25.46, 363.34) * mm, "end": v(25.3, 363.23) * mm});
            skLineSegment(sketch, "E2362", {"start": v(25.3, 363.23) * mm, "end": v(25.14, 363.14) * mm});
            skLineSegment(sketch, "E2363", {"start": v(25.14, 363.14) * mm, "end": v(24.96, 363.07) * mm});
            skLineSegment(sketch, "E2364", {"start": v(24.96, 363.07) * mm, "end": v(24.78, 363.03) * mm});
            skLineSegment(sketch, "E2365", {"start": v(24.78, 363.03) * mm, "end": v(24.6, 363) * mm});
            skLineSegment(sketch, "E2366", {"start": v(24.6, 363) * mm, "end": v(24.4, 363) * mm});
            skLineSegment(sketch, "E2367", {"start": v(385.4, 363) * mm, "end": v(385.22, 363.03) * mm});
            skLineSegment(sketch, "E2368", {"start": v(385.22, 363.03) * mm, "end": v(385.04, 363.07) * mm});
            skLineSegment(sketch, "E2369", {"start": v(385.04, 363.07) * mm, "end": v(384.86, 363.14) * mm});
            skLineSegment(sketch, "E2370", {"start": v(384.86, 363.14) * mm, "end": v(384.7, 363.23) * mm});
            skLineSegment(sketch, "E2371", {"start": v(384.7, 363.23) * mm, "end": v(384.54, 363.34) * mm});
            skLineSegment(sketch, "E2372", {"start": v(384.54, 363.34) * mm, "end": v(384.4, 363.47) * mm});
            skLineSegment(sketch, "E2373", {"start": v(384.4, 363.47) * mm, "end": v(384.29, 363.62) * mm});
            skLineSegment(sketch, "E2374", {"start": v(384.29, 363.62) * mm, "end": v(384.19, 363.78) * mm});
            skLineSegment(sketch, "E2375", {"start": v(384.19, 363.78) * mm, "end": v(384.1, 363.95) * mm});
            skLineSegment(sketch, "E2376", {"start": v(384.1, 363.95) * mm, "end": v(384.05, 364.13) * mm});
            skLineSegment(sketch, "E2377", {"start": v(384.05, 364.13) * mm, "end": v(384.01, 364.31) * mm});
            skLineSegment(sketch, "E2378", {"start": v(384.01, 364.31) * mm, "end": v(384, 364.5) * mm});
            skLineSegment(sketch, "E2379", {"start": v(384, 364.5) * mm, "end": v(384.01, 364.69) * mm});
            skLineSegment(sketch, "E2380", {"start": v(384.01, 364.69) * mm, "end": v(384.05, 364.87) * mm});
            skLineSegment(sketch, "E2381", {"start": v(384.05, 364.87) * mm, "end": v(384.1, 365.05) * mm});
            skLineSegment(sketch, "E2382", {"start": v(384.1, 365.05) * mm, "end": v(384.19, 365.22) * mm});
            skLineSegment(sketch, "E2383", {"start": v(384.19, 365.22) * mm, "end": v(384.29, 365.38) * mm});
            skLineSegment(sketch, "E2384", {"start": v(384.29, 365.38) * mm, "end": v(384.4, 365.53) * mm});
            skLineSegment(sketch, "E2385", {"start": v(384.4, 365.53) * mm, "end": v(384.54, 365.66) * mm});
            skLineSegment(sketch, "E2386", {"start": v(384.54, 365.66) * mm, "end": v(384.7, 365.77) * mm});
            skLineSegment(sketch, "E2387", {"start": v(384.7, 365.77) * mm, "end": v(384.86, 365.86) * mm});
            skLineSegment(sketch, "E2388", {"start": v(384.86, 365.86) * mm, "end": v(385.04, 365.93) * mm});
            skLineSegment(sketch, "E2389", {"start": v(385.04, 365.93) * mm, "end": v(385.22, 365.97) * mm});
            skLineSegment(sketch, "E2390", {"start": v(385.22, 365.97) * mm, "end": v(385.4, 366) * mm});
            skLineSegment(sketch, "E2391", {"start": v(385.4, 366) * mm, "end": v(385.6, 366) * mm});
            skLineSegment(sketch, "E2392", {"start": v(385.6, 366) * mm, "end": v(385.78, 365.97) * mm});
            skLineSegment(sketch, "E2393", {"start": v(385.78, 365.97) * mm, "end": v(385.96, 365.93) * mm});
            skLineSegment(sketch, "E2394", {"start": v(385.96, 365.93) * mm, "end": v(386.14, 365.86) * mm});
            skLineSegment(sketch, "E2395", {"start": v(386.14, 365.86) * mm, "end": v(386.3, 365.77) * mm});
            skLineSegment(sketch, "E2396", {"start": v(386.3, 365.77) * mm, "end": v(386.46, 365.66) * mm});
            skLineSegment(sketch, "E2397", {"start": v(386.46, 365.66) * mm, "end": v(386.6, 365.53) * mm});
            skLineSegment(sketch, "E2398", {"start": v(386.6, 365.53) * mm, "end": v(386.71, 365.38) * mm});
            skLineSegment(sketch, "E2399", {"start": v(386.71, 365.38) * mm, "end": v(386.81, 365.22) * mm});
            skLineSegment(sketch, "E2400", {"start": v(386.81, 365.22) * mm, "end": v(386.9, 365.05) * mm});
            skLineSegment(sketch, "E2401", {"start": v(386.9, 365.05) * mm, "end": v(386.95, 364.87) * mm});
            skLineSegment(sketch, "E2402", {"start": v(386.95, 364.87) * mm, "end": v(386.99, 364.69) * mm});
            skLineSegment(sketch, "E2403", {"start": v(386.99, 364.69) * mm, "end": v(387, 364.5) * mm});
            skLineSegment(sketch, "E2404", {"start": v(387, 364.5) * mm, "end": v(386.99, 364.31) * mm});
            skLineSegment(sketch, "E2405", {"start": v(386.99, 364.31) * mm, "end": v(386.95, 364.13) * mm});
            skLineSegment(sketch, "E2406", {"start": v(386.95, 364.13) * mm, "end": v(386.9, 363.95) * mm});
            skLineSegment(sketch, "E2407", {"start": v(386.9, 363.95) * mm, "end": v(386.81, 363.78) * mm});
            skLineSegment(sketch, "E2408", {"start": v(386.81, 363.78) * mm, "end": v(386.71, 363.62) * mm});
            skLineSegment(sketch, "E2409", {"start": v(386.71, 363.62) * mm, "end": v(386.6, 363.47) * mm});
            skLineSegment(sketch, "E2410", {"start": v(386.6, 363.47) * mm, "end": v(386.46, 363.34) * mm});
            skLineSegment(sketch, "E2411", {"start": v(386.46, 363.34) * mm, "end": v(386.3, 363.23) * mm});
            skLineSegment(sketch, "E2412", {"start": v(386.3, 363.23) * mm, "end": v(386.14, 363.14) * mm});
            skLineSegment(sketch, "E2413", {"start": v(386.14, 363.14) * mm, "end": v(385.96, 363.07) * mm});
            skLineSegment(sketch, "E2414", {"start": v(385.96, 363.07) * mm, "end": v(385.78, 363.03) * mm});
            skLineSegment(sketch, "E2415", {"start": v(385.78, 363.03) * mm, "end": v(385.6, 363) * mm});
            skLineSegment(sketch, "E2416", {"start": v(385.6, 363) * mm, "end": v(385.4, 363) * mm});
            skLineSegment(sketch, "E2417", {"start": v(55.4, 363) * mm, "end": v(55.22, 363.03) * mm});
            skLineSegment(sketch, "E2418", {"start": v(55.22, 363.03) * mm, "end": v(55.04, 363.07) * mm});
            skLineSegment(sketch, "E2419", {"start": v(55.04, 363.07) * mm, "end": v(54.86, 363.14) * mm});
            skLineSegment(sketch, "E2420", {"start": v(54.86, 363.14) * mm, "end": v(54.7, 363.23) * mm});
            skLineSegment(sketch, "E2421", {"start": v(54.7, 363.23) * mm, "end": v(54.54, 363.34) * mm});
            skLineSegment(sketch, "E2422", {"start": v(54.54, 363.34) * mm, "end": v(54.4, 363.47) * mm});
            skLineSegment(sketch, "E2423", {"start": v(54.4, 363.47) * mm, "end": v(54.29, 363.62) * mm});
            skLineSegment(sketch, "E2424", {"start": v(54.29, 363.62) * mm, "end": v(54.19, 363.78) * mm});
            skLineSegment(sketch, "E2425", {"start": v(54.19, 363.78) * mm, "end": v(54.1, 363.95) * mm});
            skLineSegment(sketch, "E2426", {"start": v(54.1, 363.95) * mm, "end": v(54.05, 364.13) * mm});
            skLineSegment(sketch, "E2427", {"start": v(54.05, 364.13) * mm, "end": v(54.01, 364.31) * mm});
            skLineSegment(sketch, "E2428", {"start": v(54.01, 364.31) * mm, "end": v(54, 364.5) * mm});
            skLineSegment(sketch, "E2429", {"start": v(54, 364.5) * mm, "end": v(54.01, 364.69) * mm});
            skLineSegment(sketch, "E2430", {"start": v(54.01, 364.69) * mm, "end": v(54.05, 364.87) * mm});
            skLineSegment(sketch, "E2431", {"start": v(54.05, 364.87) * mm, "end": v(54.1, 365.05) * mm});
            skLineSegment(sketch, "E2432", {"start": v(54.1, 365.05) * mm, "end": v(54.19, 365.22) * mm});
            skLineSegment(sketch, "E2433", {"start": v(54.19, 365.22) * mm, "end": v(54.29, 365.38) * mm});
            skLineSegment(sketch, "E2434", {"start": v(54.29, 365.38) * mm, "end": v(54.4, 365.53) * mm});
            skLineSegment(sketch, "E2435", {"start": v(54.4, 365.53) * mm, "end": v(54.54, 365.66) * mm});
            skLineSegment(sketch, "E2436", {"start": v(54.54, 365.66) * mm, "end": v(54.7, 365.77) * mm});
            skLineSegment(sketch, "E2437", {"start": v(54.7, 365.77) * mm, "end": v(54.86, 365.86) * mm});
            skLineSegment(sketch, "E2438", {"start": v(54.86, 365.86) * mm, "end": v(55.04, 365.93) * mm});
            skLineSegment(sketch, "E2439", {"start": v(55.04, 365.93) * mm, "end": v(55.22, 365.97) * mm});
            skLineSegment(sketch, "E2440", {"start": v(55.22, 365.97) * mm, "end": v(55.4, 366) * mm});
            skLineSegment(sketch, "E2441", {"start": v(55.4, 366) * mm, "end": v(55.6, 366) * mm});
            skLineSegment(sketch, "E2442", {"start": v(55.6, 366) * mm, "end": v(55.78, 365.97) * mm});
            skLineSegment(sketch, "E2443", {"start": v(55.78, 365.97) * mm, "end": v(55.96, 365.93) * mm});
            skLineSegment(sketch, "E2444", {"start": v(55.96, 365.93) * mm, "end": v(56.14, 365.86) * mm});
            skLineSegment(sketch, "E2445", {"start": v(56.14, 365.86) * mm, "end": v(56.3, 365.77) * mm});
            skLineSegment(sketch, "E2446", {"start": v(56.3, 365.77) * mm, "end": v(56.46, 365.66) * mm});
            skLineSegment(sketch, "E2447", {"start": v(56.46, 365.66) * mm, "end": v(56.6, 365.53) * mm});
            skLineSegment(sketch, "E2448", {"start": v(56.6, 365.53) * mm, "end": v(56.71, 365.38) * mm});
            skLineSegment(sketch, "E2449", {"start": v(56.71, 365.38) * mm, "end": v(56.81, 365.22) * mm});
            skLineSegment(sketch, "E2450", {"start": v(56.81, 365.22) * mm, "end": v(56.9, 365.05) * mm});
            skLineSegment(sketch, "E2451", {"start": v(56.9, 365.05) * mm, "end": v(56.95, 364.87) * mm});
            skLineSegment(sketch, "E2452", {"start": v(56.95, 364.87) * mm, "end": v(56.99, 364.69) * mm});
            skLineSegment(sketch, "E2453", {"start": v(56.99, 364.69) * mm, "end": v(57, 364.5) * mm});
            skLineSegment(sketch, "E2454", {"start": v(57, 364.5) * mm, "end": v(56.99, 364.31) * mm});
            skLineSegment(sketch, "E2455", {"start": v(56.99, 364.31) * mm, "end": v(56.95, 364.13) * mm});
            skLineSegment(sketch, "E2456", {"start": v(56.95, 364.13) * mm, "end": v(56.9, 363.95) * mm});
            skLineSegment(sketch, "E2457", {"start": v(56.9, 363.95) * mm, "end": v(56.81, 363.78) * mm});
            skLineSegment(sketch, "E2458", {"start": v(56.81, 363.78) * mm, "end": v(56.71, 363.62) * mm});
            skLineSegment(sketch, "E2459", {"start": v(56.71, 363.62) * mm, "end": v(56.6, 363.47) * mm});
            skLineSegment(sketch, "E2460", {"start": v(56.6, 363.47) * mm, "end": v(56.46, 363.34) * mm});
            skLineSegment(sketch, "E2461", {"start": v(56.46, 363.34) * mm, "end": v(56.3, 363.23) * mm});
            skLineSegment(sketch, "E2462", {"start": v(56.3, 363.23) * mm, "end": v(56.14, 363.14) * mm});
            skLineSegment(sketch, "E2463", {"start": v(56.14, 363.14) * mm, "end": v(55.96, 363.07) * mm});
            skLineSegment(sketch, "E2464", {"start": v(55.96, 363.07) * mm, "end": v(55.78, 363.03) * mm});
            skLineSegment(sketch, "E2465", {"start": v(55.78, 363.03) * mm, "end": v(55.6, 363) * mm});
            skLineSegment(sketch, "E2466", {"start": v(55.6, 363) * mm, "end": v(55.4, 363) * mm});
            skLineSegment(sketch, "E2467", {"start": v(267.9, 151.5) * mm, "end": v(267.72, 151.53) * mm});
            skLineSegment(sketch, "E2468", {"start": v(267.72, 151.53) * mm, "end": v(267.54, 151.57) * mm});
            skLineSegment(sketch, "E2469", {"start": v(267.54, 151.57) * mm, "end": v(267.36, 151.64) * mm});
            skLineSegment(sketch, "E2470", {"start": v(267.36, 151.64) * mm, "end": v(267.2, 151.73) * mm});
            skLineSegment(sketch, "E2471", {"start": v(267.2, 151.73) * mm, "end": v(267.04, 151.84) * mm});
            skLineSegment(sketch, "E2472", {"start": v(267.04, 151.84) * mm, "end": v(266.9, 151.97) * mm});
            skLineSegment(sketch, "E2473", {"start": v(266.9, 151.97) * mm, "end": v(266.79, 152.12) * mm});
            skLineSegment(sketch, "E2474", {"start": v(266.79, 152.12) * mm, "end": v(266.69, 152.28) * mm});
            skLineSegment(sketch, "E2475", {"start": v(266.69, 152.28) * mm, "end": v(266.6, 152.45) * mm});
            skLineSegment(sketch, "E2476", {"start": v(266.6, 152.45) * mm, "end": v(266.55, 152.63) * mm});
            skLineSegment(sketch, "E2477", {"start": v(266.55, 152.63) * mm, "end": v(266.51, 152.81) * mm});
            skLineSegment(sketch, "E2478", {"start": v(266.51, 152.81) * mm, "end": v(266.5, 153) * mm});
            skLineSegment(sketch, "E2479", {"start": v(266.5, 153) * mm, "end": v(266.51, 153.19) * mm});
            skLineSegment(sketch, "E2480", {"start": v(266.51, 153.19) * mm, "end": v(266.55, 153.37) * mm});
            skLineSegment(sketch, "E2481", {"start": v(266.55, 153.37) * mm, "end": v(266.6, 153.55) * mm});
            skLineSegment(sketch, "E2482", {"start": v(266.6, 153.55) * mm, "end": v(266.69, 153.72) * mm});
            skLineSegment(sketch, "E2483", {"start": v(266.69, 153.72) * mm, "end": v(266.79, 153.88) * mm});
            skLineSegment(sketch, "E2484", {"start": v(266.79, 153.88) * mm, "end": v(266.9, 154.03) * mm});
            skLineSegment(sketch, "E2485", {"start": v(266.9, 154.03) * mm, "end": v(267.04, 154.16) * mm});
            skLineSegment(sketch, "E2486", {"start": v(267.04, 154.16) * mm, "end": v(267.2, 154.27) * mm});
            skLineSegment(sketch, "E2487", {"start": v(267.2, 154.27) * mm, "end": v(267.36, 154.36) * mm});
            skLineSegment(sketch, "E2488", {"start": v(267.36, 154.36) * mm, "end": v(267.54, 154.43) * mm});
            skLineSegment(sketch, "E2489", {"start": v(267.54, 154.43) * mm, "end": v(267.72, 154.47) * mm});
            skLineSegment(sketch, "E2490", {"start": v(267.72, 154.47) * mm, "end": v(267.9, 154.5) * mm});
            skLineSegment(sketch, "E2491", {"start": v(267.9, 154.5) * mm, "end": v(268.1, 154.5) * mm});
            skLineSegment(sketch, "E2492", {"start": v(268.1, 154.5) * mm, "end": v(268.28, 154.47) * mm});
            skLineSegment(sketch, "E2493", {"start": v(268.28, 154.47) * mm, "end": v(268.46, 154.43) * mm});
            skLineSegment(sketch, "E2494", {"start": v(268.46, 154.43) * mm, "end": v(268.64, 154.36) * mm});
            skLineSegment(sketch, "E2495", {"start": v(268.64, 154.36) * mm, "end": v(268.8, 154.27) * mm});
            skLineSegment(sketch, "E2496", {"start": v(268.8, 154.27) * mm, "end": v(268.96, 154.16) * mm});
            skLineSegment(sketch, "E2497", {"start": v(268.96, 154.16) * mm, "end": v(269.1, 154.03) * mm});
            skLineSegment(sketch, "E2498", {"start": v(269.1, 154.03) * mm, "end": v(269.21, 153.88) * mm});
            skLineSegment(sketch, "E2499", {"start": v(269.21, 153.88) * mm, "end": v(269.31, 153.72) * mm});
            skLineSegment(sketch, "E2500", {"start": v(269.31, 153.72) * mm, "end": v(269.4, 153.55) * mm});
            skLineSegment(sketch, "E2501", {"start": v(269.4, 153.55) * mm, "end": v(269.45, 153.37) * mm});
            skLineSegment(sketch, "E2502", {"start": v(269.45, 153.37) * mm, "end": v(269.49, 153.19) * mm});
            skLineSegment(sketch, "E2503", {"start": v(269.49, 153.19) * mm, "end": v(269.5, 153) * mm});
            skLineSegment(sketch, "E2504", {"start": v(269.5, 153) * mm, "end": v(269.49, 152.81) * mm});
            skLineSegment(sketch, "E2505", {"start": v(269.49, 152.81) * mm, "end": v(269.45, 152.63) * mm});
            skLineSegment(sketch, "E2506", {"start": v(269.45, 152.63) * mm, "end": v(269.4, 152.45) * mm});
            skLineSegment(sketch, "E2507", {"start": v(269.4, 152.45) * mm, "end": v(269.31, 152.28) * mm});
            skLineSegment(sketch, "E2508", {"start": v(269.31, 152.28) * mm, "end": v(269.21, 152.12) * mm});
            skLineSegment(sketch, "E2509", {"start": v(269.21, 152.12) * mm, "end": v(269.1, 151.97) * mm});
            skLineSegment(sketch, "E2510", {"start": v(269.1, 151.97) * mm, "end": v(268.96, 151.84) * mm});
            skLineSegment(sketch, "E2511", {"start": v(268.96, 151.84) * mm, "end": v(268.8, 151.73) * mm});
            skLineSegment(sketch, "E2512", {"start": v(268.8, 151.73) * mm, "end": v(268.64, 151.64) * mm});
            skLineSegment(sketch, "E2513", {"start": v(268.64, 151.64) * mm, "end": v(268.46, 151.57) * mm});
            skLineSegment(sketch, "E2514", {"start": v(268.46, 151.57) * mm, "end": v(268.28, 151.53) * mm});
            skLineSegment(sketch, "E2515", {"start": v(268.28, 151.53) * mm, "end": v(268.1, 151.5) * mm});
            skLineSegment(sketch, "E2516", {"start": v(268.1, 151.5) * mm, "end": v(267.9, 151.5) * mm});
            skLineSegment(sketch, "E2517", {"start": v(251.9, 151.5) * mm, "end": v(251.72, 151.53) * mm});
            skLineSegment(sketch, "E2518", {"start": v(251.72, 151.53) * mm, "end": v(251.54, 151.57) * mm});
            skLineSegment(sketch, "E2519", {"start": v(251.54, 151.57) * mm, "end": v(251.36, 151.64) * mm});
            skLineSegment(sketch, "E2520", {"start": v(251.36, 151.64) * mm, "end": v(251.2, 151.73) * mm});
            skLineSegment(sketch, "E2521", {"start": v(251.2, 151.73) * mm, "end": v(251.04, 151.84) * mm});
            skLineSegment(sketch, "E2522", {"start": v(251.04, 151.84) * mm, "end": v(250.9, 151.97) * mm});
            skLineSegment(sketch, "E2523", {"start": v(250.9, 151.97) * mm, "end": v(250.79, 152.12) * mm});
            skLineSegment(sketch, "E2524", {"start": v(250.79, 152.12) * mm, "end": v(250.69, 152.28) * mm});
            skLineSegment(sketch, "E2525", {"start": v(250.69, 152.28) * mm, "end": v(250.6, 152.45) * mm});
            skLineSegment(sketch, "E2526", {"start": v(250.6, 152.45) * mm, "end": v(250.55, 152.63) * mm});
            skLineSegment(sketch, "E2527", {"start": v(250.55, 152.63) * mm, "end": v(250.51, 152.81) * mm});
            skLineSegment(sketch, "E2528", {"start": v(250.51, 152.81) * mm, "end": v(250.5, 153) * mm});
            skLineSegment(sketch, "E2529", {"start": v(250.5, 153) * mm, "end": v(250.51, 153.19) * mm});
            skLineSegment(sketch, "E2530", {"start": v(250.51, 153.19) * mm, "end": v(250.55, 153.37) * mm});
            skLineSegment(sketch, "E2531", {"start": v(250.55, 153.37) * mm, "end": v(250.6, 153.55) * mm});
            skLineSegment(sketch, "E2532", {"start": v(250.6, 153.55) * mm, "end": v(250.69, 153.72) * mm});
            skLineSegment(sketch, "E2533", {"start": v(250.69, 153.72) * mm, "end": v(250.79, 153.88) * mm});
            skLineSegment(sketch, "E2534", {"start": v(250.79, 153.88) * mm, "end": v(250.9, 154.03) * mm});
            skLineSegment(sketch, "E2535", {"start": v(250.9, 154.03) * mm, "end": v(251.04, 154.16) * mm});
            skLineSegment(sketch, "E2536", {"start": v(251.04, 154.16) * mm, "end": v(251.2, 154.27) * mm});
            skLineSegment(sketch, "E2537", {"start": v(251.2, 154.27) * mm, "end": v(251.36, 154.36) * mm});
            skLineSegment(sketch, "E2538", {"start": v(251.36, 154.36) * mm, "end": v(251.54, 154.43) * mm});
            skLineSegment(sketch, "E2539", {"start": v(251.54, 154.43) * mm, "end": v(251.72, 154.47) * mm});
            skLineSegment(sketch, "E2540", {"start": v(251.72, 154.47) * mm, "end": v(251.9, 154.5) * mm});
            skLineSegment(sketch, "E2541", {"start": v(251.9, 154.5) * mm, "end": v(252.1, 154.5) * mm});
            skLineSegment(sketch, "E2542", {"start": v(252.1, 154.5) * mm, "end": v(252.28, 154.47) * mm});
            skLineSegment(sketch, "E2543", {"start": v(252.28, 154.47) * mm, "end": v(252.46, 154.43) * mm});
            skLineSegment(sketch, "E2544", {"start": v(252.46, 154.43) * mm, "end": v(252.64, 154.36) * mm});
            skLineSegment(sketch, "E2545", {"start": v(252.64, 154.36) * mm, "end": v(252.8, 154.27) * mm});
            skLineSegment(sketch, "E2546", {"start": v(252.8, 154.27) * mm, "end": v(252.96, 154.16) * mm});
            skLineSegment(sketch, "E2547", {"start": v(252.96, 154.16) * mm, "end": v(253.1, 154.03) * mm});
            skLineSegment(sketch, "E2548", {"start": v(253.1, 154.03) * mm, "end": v(253.21, 153.88) * mm});
            skLineSegment(sketch, "E2549", {"start": v(253.21, 153.88) * mm, "end": v(253.31, 153.72) * mm});
            skLineSegment(sketch, "E2550", {"start": v(253.31, 153.72) * mm, "end": v(253.4, 153.55) * mm});
            skLineSegment(sketch, "E2551", {"start": v(253.4, 153.55) * mm, "end": v(253.45, 153.37) * mm});
            skLineSegment(sketch, "E2552", {"start": v(253.45, 153.37) * mm, "end": v(253.49, 153.19) * mm});
            skLineSegment(sketch, "E2553", {"start": v(253.49, 153.19) * mm, "end": v(253.5, 153) * mm});
            skLineSegment(sketch, "E2554", {"start": v(253.5, 153) * mm, "end": v(253.49, 152.81) * mm});
            skLineSegment(sketch, "E2555", {"start": v(253.49, 152.81) * mm, "end": v(253.45, 152.63) * mm});
            skLineSegment(sketch, "E2556", {"start": v(253.45, 152.63) * mm, "end": v(253.4, 152.45) * mm});
            skLineSegment(sketch, "E2557", {"start": v(253.4, 152.45) * mm, "end": v(253.31, 152.28) * mm});
            skLineSegment(sketch, "E2558", {"start": v(253.31, 152.28) * mm, "end": v(253.21, 152.12) * mm});
            skLineSegment(sketch, "E2559", {"start": v(253.21, 152.12) * mm, "end": v(253.1, 151.97) * mm});
            skLineSegment(sketch, "E2560", {"start": v(253.1, 151.97) * mm, "end": v(252.96, 151.84) * mm});
            skLineSegment(sketch, "E2561", {"start": v(252.96, 151.84) * mm, "end": v(252.8, 151.73) * mm});
            skLineSegment(sketch, "E2562", {"start": v(252.8, 151.73) * mm, "end": v(252.64, 151.64) * mm});
            skLineSegment(sketch, "E2563", {"start": v(252.64, 151.64) * mm, "end": v(252.46, 151.57) * mm});
            skLineSegment(sketch, "E2564", {"start": v(252.46, 151.57) * mm, "end": v(252.28, 151.53) * mm});
            skLineSegment(sketch, "E2565", {"start": v(252.28, 151.53) * mm, "end": v(252.1, 151.5) * mm});
            skLineSegment(sketch, "E2566", {"start": v(252.1, 151.5) * mm, "end": v(251.9, 151.5) * mm});
            skLineSegment(sketch, "E2567", {"start": v(157.9, 151.5) * mm, "end": v(157.72, 151.53) * mm});
            skLineSegment(sketch, "E2568", {"start": v(157.72, 151.53) * mm, "end": v(157.54, 151.57) * mm});
            skLineSegment(sketch, "E2569", {"start": v(157.54, 151.57) * mm, "end": v(157.36, 151.64) * mm});
            skLineSegment(sketch, "E2570", {"start": v(157.36, 151.64) * mm, "end": v(157.2, 151.73) * mm});
            skLineSegment(sketch, "E2571", {"start": v(157.2, 151.73) * mm, "end": v(157.04, 151.84) * mm});
            skLineSegment(sketch, "E2572", {"start": v(157.04, 151.84) * mm, "end": v(156.9, 151.97) * mm});
            skLineSegment(sketch, "E2573", {"start": v(156.9, 151.97) * mm, "end": v(156.79, 152.12) * mm});
            skLineSegment(sketch, "E2574", {"start": v(156.79, 152.12) * mm, "end": v(156.69, 152.28) * mm});
            skLineSegment(sketch, "E2575", {"start": v(156.69, 152.28) * mm, "end": v(156.6, 152.45) * mm});
            skLineSegment(sketch, "E2576", {"start": v(156.6, 152.45) * mm, "end": v(156.55, 152.63) * mm});
            skLineSegment(sketch, "E2577", {"start": v(156.55, 152.63) * mm, "end": v(156.51, 152.81) * mm});
            skLineSegment(sketch, "E2578", {"start": v(156.51, 152.81) * mm, "end": v(156.5, 153) * mm});
            skLineSegment(sketch, "E2579", {"start": v(156.5, 153) * mm, "end": v(156.51, 153.19) * mm});
            skLineSegment(sketch, "E2580", {"start": v(156.51, 153.19) * mm, "end": v(156.55, 153.37) * mm});
            skLineSegment(sketch, "E2581", {"start": v(156.55, 153.37) * mm, "end": v(156.6, 153.55) * mm});
            skLineSegment(sketch, "E2582", {"start": v(156.6, 153.55) * mm, "end": v(156.69, 153.72) * mm});
            skLineSegment(sketch, "E2583", {"start": v(156.69, 153.72) * mm, "end": v(156.79, 153.88) * mm});
            skLineSegment(sketch, "E2584", {"start": v(156.79, 153.88) * mm, "end": v(156.9, 154.03) * mm});
            skLineSegment(sketch, "E2585", {"start": v(156.9, 154.03) * mm, "end": v(157.04, 154.16) * mm});
            skLineSegment(sketch, "E2586", {"start": v(157.04, 154.16) * mm, "end": v(157.2, 154.27) * mm});
            skLineSegment(sketch, "E2587", {"start": v(157.2, 154.27) * mm, "end": v(157.36, 154.36) * mm});
            skLineSegment(sketch, "E2588", {"start": v(157.36, 154.36) * mm, "end": v(157.54, 154.43) * mm});
            skLineSegment(sketch, "E2589", {"start": v(157.54, 154.43) * mm, "end": v(157.72, 154.47) * mm});
            skLineSegment(sketch, "E2590", {"start": v(157.72, 154.47) * mm, "end": v(157.9, 154.5) * mm});
            skLineSegment(sketch, "E2591", {"start": v(157.9, 154.5) * mm, "end": v(158.1, 154.5) * mm});
            skLineSegment(sketch, "E2592", {"start": v(158.1, 154.5) * mm, "end": v(158.28, 154.47) * mm});
            skLineSegment(sketch, "E2593", {"start": v(158.28, 154.47) * mm, "end": v(158.46, 154.43) * mm});
            skLineSegment(sketch, "E2594", {"start": v(158.46, 154.43) * mm, "end": v(158.64, 154.36) * mm});
            skLineSegment(sketch, "E2595", {"start": v(158.64, 154.36) * mm, "end": v(158.8, 154.27) * mm});
            skLineSegment(sketch, "E2596", {"start": v(158.8, 154.27) * mm, "end": v(158.96, 154.16) * mm});
            skLineSegment(sketch, "E2597", {"start": v(158.96, 154.16) * mm, "end": v(159.1, 154.03) * mm});
            skLineSegment(sketch, "E2598", {"start": v(159.1, 154.03) * mm, "end": v(159.21, 153.88) * mm});
            skLineSegment(sketch, "E2599", {"start": v(159.21, 153.88) * mm, "end": v(159.31, 153.72) * mm});
            skLineSegment(sketch, "E2600", {"start": v(159.31, 153.72) * mm, "end": v(159.4, 153.55) * mm});
            skLineSegment(sketch, "E2601", {"start": v(159.4, 153.55) * mm, "end": v(159.45, 153.37) * mm});
            skLineSegment(sketch, "E2602", {"start": v(159.45, 153.37) * mm, "end": v(159.49, 153.19) * mm});
            skLineSegment(sketch, "E2603", {"start": v(159.49, 153.19) * mm, "end": v(159.5, 153) * mm});
            skLineSegment(sketch, "E2604", {"start": v(159.5, 153) * mm, "end": v(159.49, 152.81) * mm});
            skLineSegment(sketch, "E2605", {"start": v(159.49, 152.81) * mm, "end": v(159.45, 152.63) * mm});
            skLineSegment(sketch, "E2606", {"start": v(159.45, 152.63) * mm, "end": v(159.4, 152.45) * mm});
            skLineSegment(sketch, "E2607", {"start": v(159.4, 152.45) * mm, "end": v(159.31, 152.28) * mm});
            skLineSegment(sketch, "E2608", {"start": v(159.31, 152.28) * mm, "end": v(159.21, 152.12) * mm});
            skLineSegment(sketch, "E2609", {"start": v(159.21, 152.12) * mm, "end": v(159.1, 151.97) * mm});
            skLineSegment(sketch, "E2610", {"start": v(159.1, 151.97) * mm, "end": v(158.96, 151.84) * mm});
            skLineSegment(sketch, "E2611", {"start": v(158.96, 151.84) * mm, "end": v(158.8, 151.73) * mm});
            skLineSegment(sketch, "E2612", {"start": v(158.8, 151.73) * mm, "end": v(158.64, 151.64) * mm});
            skLineSegment(sketch, "E2613", {"start": v(158.64, 151.64) * mm, "end": v(158.46, 151.57) * mm});
            skLineSegment(sketch, "E2614", {"start": v(158.46, 151.57) * mm, "end": v(158.28, 151.53) * mm});
            skLineSegment(sketch, "E2615", {"start": v(158.28, 151.53) * mm, "end": v(158.1, 151.5) * mm});
            skLineSegment(sketch, "E2616", {"start": v(158.1, 151.5) * mm, "end": v(157.9, 151.5) * mm});
            skLineSegment(sketch, "E2617", {"start": v(141.9, 151.5) * mm, "end": v(141.72, 151.53) * mm});
            skLineSegment(sketch, "E2618", {"start": v(141.72, 151.53) * mm, "end": v(141.54, 151.57) * mm});
            skLineSegment(sketch, "E2619", {"start": v(141.54, 151.57) * mm, "end": v(141.36, 151.64) * mm});
            skLineSegment(sketch, "E2620", {"start": v(141.36, 151.64) * mm, "end": v(141.2, 151.73) * mm});
            skLineSegment(sketch, "E2621", {"start": v(141.2, 151.73) * mm, "end": v(141.04, 151.84) * mm});
            skLineSegment(sketch, "E2622", {"start": v(141.04, 151.84) * mm, "end": v(140.9, 151.97) * mm});
            skLineSegment(sketch, "E2623", {"start": v(140.9, 151.97) * mm, "end": v(140.79, 152.12) * mm});
            skLineSegment(sketch, "E2624", {"start": v(140.79, 152.12) * mm, "end": v(140.69, 152.28) * mm});
            skLineSegment(sketch, "E2625", {"start": v(140.69, 152.28) * mm, "end": v(140.6, 152.45) * mm});
            skLineSegment(sketch, "E2626", {"start": v(140.6, 152.45) * mm, "end": v(140.55, 152.63) * mm});
            skLineSegment(sketch, "E2627", {"start": v(140.55, 152.63) * mm, "end": v(140.51, 152.81) * mm});
            skLineSegment(sketch, "E2628", {"start": v(140.51, 152.81) * mm, "end": v(140.5, 153) * mm});
            skLineSegment(sketch, "E2629", {"start": v(140.5, 153) * mm, "end": v(140.51, 153.19) * mm});
            skLineSegment(sketch, "E2630", {"start": v(140.51, 153.19) * mm, "end": v(140.55, 153.37) * mm});
            skLineSegment(sketch, "E2631", {"start": v(140.55, 153.37) * mm, "end": v(140.6, 153.55) * mm});
            skLineSegment(sketch, "E2632", {"start": v(140.6, 153.55) * mm, "end": v(140.69, 153.72) * mm});
            skLineSegment(sketch, "E2633", {"start": v(140.69, 153.72) * mm, "end": v(140.79, 153.88) * mm});
            skLineSegment(sketch, "E2634", {"start": v(140.79, 153.88) * mm, "end": v(140.9, 154.03) * mm});
            skLineSegment(sketch, "E2635", {"start": v(140.9, 154.03) * mm, "end": v(141.04, 154.16) * mm});
            skLineSegment(sketch, "E2636", {"start": v(141.04, 154.16) * mm, "end": v(141.2, 154.27) * mm});
            skLineSegment(sketch, "E2637", {"start": v(141.2, 154.27) * mm, "end": v(141.36, 154.36) * mm});
            skLineSegment(sketch, "E2638", {"start": v(141.36, 154.36) * mm, "end": v(141.54, 154.43) * mm});
            skLineSegment(sketch, "E2639", {"start": v(141.54, 154.43) * mm, "end": v(141.72, 154.47) * mm});
            skLineSegment(sketch, "E2640", {"start": v(141.72, 154.47) * mm, "end": v(141.9, 154.5) * mm});
            skLineSegment(sketch, "E2641", {"start": v(141.9, 154.5) * mm, "end": v(142.1, 154.5) * mm});
            skLineSegment(sketch, "E2642", {"start": v(142.1, 154.5) * mm, "end": v(142.28, 154.47) * mm});
            skLineSegment(sketch, "E2643", {"start": v(142.28, 154.47) * mm, "end": v(142.46, 154.43) * mm});
            skLineSegment(sketch, "E2644", {"start": v(142.46, 154.43) * mm, "end": v(142.64, 154.36) * mm});
            skLineSegment(sketch, "E2645", {"start": v(142.64, 154.36) * mm, "end": v(142.8, 154.27) * mm});
            skLineSegment(sketch, "E2646", {"start": v(142.8, 154.27) * mm, "end": v(142.96, 154.16) * mm});
            skLineSegment(sketch, "E2647", {"start": v(142.96, 154.16) * mm, "end": v(143.1, 154.03) * mm});
            skLineSegment(sketch, "E2648", {"start": v(143.1, 154.03) * mm, "end": v(143.21, 153.88) * mm});
            skLineSegment(sketch, "E2649", {"start": v(143.21, 153.88) * mm, "end": v(143.31, 153.72) * mm});
            skLineSegment(sketch, "E2650", {"start": v(143.31, 153.72) * mm, "end": v(143.4, 153.55) * mm});
            skLineSegment(sketch, "E2651", {"start": v(143.4, 153.55) * mm, "end": v(143.45, 153.37) * mm});
            skLineSegment(sketch, "E2652", {"start": v(143.45, 153.37) * mm, "end": v(143.49, 153.19) * mm});
            skLineSegment(sketch, "E2653", {"start": v(143.49, 153.19) * mm, "end": v(143.5, 153) * mm});
            skLineSegment(sketch, "E2654", {"start": v(143.5, 153) * mm, "end": v(143.49, 152.81) * mm});
            skLineSegment(sketch, "E2655", {"start": v(143.49, 152.81) * mm, "end": v(143.45, 152.63) * mm});
            skLineSegment(sketch, "E2656", {"start": v(143.45, 152.63) * mm, "end": v(143.4, 152.45) * mm});
            skLineSegment(sketch, "E2657", {"start": v(143.4, 152.45) * mm, "end": v(143.31, 152.28) * mm});
            skLineSegment(sketch, "E2658", {"start": v(143.31, 152.28) * mm, "end": v(143.21, 152.12) * mm});
            skLineSegment(sketch, "E2659", {"start": v(143.21, 152.12) * mm, "end": v(143.1, 151.97) * mm});
            skLineSegment(sketch, "E2660", {"start": v(143.1, 151.97) * mm, "end": v(142.96, 151.84) * mm});
            skLineSegment(sketch, "E2661", {"start": v(142.96, 151.84) * mm, "end": v(142.8, 151.73) * mm});
            skLineSegment(sketch, "E2662", {"start": v(142.8, 151.73) * mm, "end": v(142.64, 151.64) * mm});
            skLineSegment(sketch, "E2663", {"start": v(142.64, 151.64) * mm, "end": v(142.46, 151.57) * mm});
            skLineSegment(sketch, "E2664", {"start": v(142.46, 151.57) * mm, "end": v(142.28, 151.53) * mm});
            skLineSegment(sketch, "E2665", {"start": v(142.28, 151.53) * mm, "end": v(142.1, 151.5) * mm});
            skLineSegment(sketch, "E2666", {"start": v(142.1, 151.5) * mm, "end": v(141.9, 151.5) * mm});
            skLineSegment(sketch, "E2667", {"start": v(50, 133.5) * mm, "end": v(50, 149.5) * mm});
            skLineSegment(sketch, "E2668", {"start": v(50, 149.5) * mm, "end": v(70, 149.5) * mm});
            skLineSegment(sketch, "E2669", {"start": v(70, 149.5) * mm, "end": v(70, 133.5) * mm});
            skLineSegment(sketch, "E2670", {"start": v(70, 133.5) * mm, "end": v(50, 133.5) * mm});
            skLineSegment(sketch, "E2671", {"start": v(340, 133.5) * mm, "end": v(340, 149.5) * mm});
            skLineSegment(sketch, "E2672", {"start": v(340, 149.5) * mm, "end": v(360, 149.5) * mm});
            skLineSegment(sketch, "E2673", {"start": v(360, 149.5) * mm, "end": v(360, 133.5) * mm});
            skLineSegment(sketch, "E2674", {"start": v(360, 133.5) * mm, "end": v(340, 133.5) * mm});
            skLineSegment(sketch, "E2675", {"start": v(195, 133.5) * mm, "end": v(195, 149.5) * mm});
            skLineSegment(sketch, "E2676", {"start": v(195, 149.5) * mm, "end": v(215, 149.5) * mm});
            skLineSegment(sketch, "E2677", {"start": v(215, 149.5) * mm, "end": v(215, 133.5) * mm});
            skLineSegment(sketch, "E2678", {"start": v(215, 133.5) * mm, "end": v(195, 133.5) * mm});
            skLineSegment(sketch, "E2679", {"start": v(122.37, 139.5) * mm, "end": v(122.12, 139.53) * mm});
            skLineSegment(sketch, "E2680", {"start": v(122.12, 139.53) * mm, "end": v(121.88, 139.6) * mm});
            skLineSegment(sketch, "E2681", {"start": v(121.88, 139.6) * mm, "end": v(121.65, 139.7) * mm});
            skLineSegment(sketch, "E2682", {"start": v(121.65, 139.7) * mm, "end": v(121.43, 139.81) * mm});
            skLineSegment(sketch, "E2683", {"start": v(121.43, 139.81) * mm, "end": v(121.22, 139.96) * mm});
            skLineSegment(sketch, "E2684", {"start": v(121.22, 139.96) * mm, "end": v(121.04, 140.13) * mm});
            skLineSegment(sketch, "E2685", {"start": v(121.04, 140.13) * mm, "end": v(120.88, 140.32) * mm});
            skLineSegment(sketch, "E2686", {"start": v(120.88, 140.32) * mm, "end": v(120.75, 140.54) * mm});
            skLineSegment(sketch, "E2687", {"start": v(120.75, 140.54) * mm, "end": v(120.64, 140.76) * mm});
            skLineSegment(sketch, "E2688", {"start": v(120.64, 140.76) * mm, "end": v(120.56, 141) * mm});
            skLineSegment(sketch, "E2689", {"start": v(120.56, 141) * mm, "end": v(120.52, 141.25) * mm});
            skLineSegment(sketch, "E2690", {"start": v(120.52, 141.25) * mm, "end": v(120.5, 141.5) * mm});
            skLineSegment(sketch, "E2691", {"start": v(120.5, 141.5) * mm, "end": v(120.52, 141.75) * mm});
            skLineSegment(sketch, "E2692", {"start": v(120.52, 141.75) * mm, "end": v(120.56, 142) * mm});
            skLineSegment(sketch, "E2693", {"start": v(120.56, 142) * mm, "end": v(120.64, 142.24) * mm});
            skLineSegment(sketch, "E2694", {"start": v(120.64, 142.24) * mm, "end": v(120.75, 142.46) * mm});
            skLineSegment(sketch, "E2695", {"start": v(120.75, 142.46) * mm, "end": v(120.88, 142.68) * mm});
            skLineSegment(sketch, "E2696", {"start": v(120.88, 142.68) * mm, "end": v(121.04, 142.87) * mm});
            skLineSegment(sketch, "E2697", {"start": v(121.04, 142.87) * mm, "end": v(121.22, 143.04) * mm});
            skLineSegment(sketch, "E2698", {"start": v(121.22, 143.04) * mm, "end": v(121.43, 143.19) * mm});
            skLineSegment(sketch, "E2699", {"start": v(121.43, 143.19) * mm, "end": v(121.65, 143.3) * mm});
            skLineSegment(sketch, "E2700", {"start": v(121.65, 143.3) * mm, "end": v(121.88, 143.4) * mm});
            skLineSegment(sketch, "E2701", {"start": v(121.88, 143.4) * mm, "end": v(122.12, 143.47) * mm});
            skLineSegment(sketch, "E2702", {"start": v(122.12, 143.47) * mm, "end": v(122.37, 143.5) * mm});
            skLineSegment(sketch, "E2703", {"start": v(122.37, 143.5) * mm, "end": v(122.63, 143.5) * mm});
            skLineSegment(sketch, "E2704", {"start": v(122.63, 143.5) * mm, "end": v(122.88, 143.47) * mm});
            skLineSegment(sketch, "E2705", {"start": v(122.88, 143.47) * mm, "end": v(123.12, 143.4) * mm});
            skLineSegment(sketch, "E2706", {"start": v(123.12, 143.4) * mm, "end": v(123.35, 143.3) * mm});
            skLineSegment(sketch, "E2707", {"start": v(123.35, 143.3) * mm, "end": v(123.57, 143.19) * mm});
            skLineSegment(sketch, "E2708", {"start": v(123.57, 143.19) * mm, "end": v(123.78, 143.04) * mm});
            skLineSegment(sketch, "E2709", {"start": v(123.78, 143.04) * mm, "end": v(123.96, 142.87) * mm});
            skLineSegment(sketch, "E2710", {"start": v(123.96, 142.87) * mm, "end": v(124.12, 142.68) * mm});
            skLineSegment(sketch, "E2711", {"start": v(124.12, 142.68) * mm, "end": v(124.25, 142.46) * mm});
            skLineSegment(sketch, "E2712", {"start": v(124.25, 142.46) * mm, "end": v(124.36, 142.24) * mm});
            skLineSegment(sketch, "E2713", {"start": v(124.36, 142.24) * mm, "end": v(124.44, 142) * mm});
            skLineSegment(sketch, "E2714", {"start": v(124.44, 142) * mm, "end": v(124.48, 141.75) * mm});
            skLineSegment(sketch, "E2715", {"start": v(124.48, 141.75) * mm, "end": v(124.5, 141.5) * mm});
            skLineSegment(sketch, "E2716", {"start": v(124.5, 141.5) * mm, "end": v(124.48, 141.25) * mm});
            skLineSegment(sketch, "E2717", {"start": v(124.48, 141.25) * mm, "end": v(124.44, 141) * mm});
            skLineSegment(sketch, "E2718", {"start": v(124.44, 141) * mm, "end": v(124.36, 140.76) * mm});
            skLineSegment(sketch, "E2719", {"start": v(124.36, 140.76) * mm, "end": v(124.25, 140.54) * mm});
            skLineSegment(sketch, "E2720", {"start": v(124.25, 140.54) * mm, "end": v(124.12, 140.32) * mm});
            skLineSegment(sketch, "E2721", {"start": v(124.12, 140.32) * mm, "end": v(123.96, 140.13) * mm});
            skLineSegment(sketch, "E2722", {"start": v(123.96, 140.13) * mm, "end": v(123.78, 139.96) * mm});
            skLineSegment(sketch, "E2723", {"start": v(123.78, 139.96) * mm, "end": v(123.57, 139.81) * mm});
            skLineSegment(sketch, "E2724", {"start": v(123.57, 139.81) * mm, "end": v(123.35, 139.7) * mm});
            skLineSegment(sketch, "E2725", {"start": v(123.35, 139.7) * mm, "end": v(123.12, 139.6) * mm});
            skLineSegment(sketch, "E2726", {"start": v(123.12, 139.6) * mm, "end": v(122.88, 139.53) * mm});
            skLineSegment(sketch, "E2727", {"start": v(122.88, 139.53) * mm, "end": v(122.63, 139.5) * mm});
            skLineSegment(sketch, "E2728", {"start": v(122.63, 139.5) * mm, "end": v(122.37, 139.5) * mm});
            skLineSegment(sketch, "E2729", {"start": v(287.37, 139.5) * mm, "end": v(287.12, 139.53) * mm});
            skLineSegment(sketch, "E2730", {"start": v(287.12, 139.53) * mm, "end": v(286.88, 139.6) * mm});
            skLineSegment(sketch, "E2731", {"start": v(286.88, 139.6) * mm, "end": v(286.65, 139.7) * mm});
            skLineSegment(sketch, "E2732", {"start": v(286.65, 139.7) * mm, "end": v(286.43, 139.81) * mm});
            skLineSegment(sketch, "E2733", {"start": v(286.43, 139.81) * mm, "end": v(286.23, 139.96) * mm});
            skLineSegment(sketch, "E2734", {"start": v(286.23, 139.96) * mm, "end": v(286.04, 140.13) * mm});
            skLineSegment(sketch, "E2735", {"start": v(286.04, 140.13) * mm, "end": v(285.88, 140.32) * mm});
            skLineSegment(sketch, "E2736", {"start": v(285.88, 140.32) * mm, "end": v(285.75, 140.54) * mm});
            skLineSegment(sketch, "E2737", {"start": v(285.75, 140.54) * mm, "end": v(285.64, 140.76) * mm});
            skLineSegment(sketch, "E2738", {"start": v(285.64, 140.76) * mm, "end": v(285.56, 141) * mm});
            skLineSegment(sketch, "E2739", {"start": v(285.56, 141) * mm, "end": v(285.52, 141.25) * mm});
            skLineSegment(sketch, "E2740", {"start": v(285.52, 141.25) * mm, "end": v(285.5, 141.5) * mm});
            skLineSegment(sketch, "E2741", {"start": v(285.5, 141.5) * mm, "end": v(285.52, 141.75) * mm});
            skLineSegment(sketch, "E2742", {"start": v(285.52, 141.75) * mm, "end": v(285.56, 142) * mm});
            skLineSegment(sketch, "E2743", {"start": v(285.56, 142) * mm, "end": v(285.64, 142.24) * mm});
            skLineSegment(sketch, "E2744", {"start": v(285.64, 142.24) * mm, "end": v(285.75, 142.46) * mm});
            skLineSegment(sketch, "E2745", {"start": v(285.75, 142.46) * mm, "end": v(285.88, 142.68) * mm});
            skLineSegment(sketch, "E2746", {"start": v(285.88, 142.68) * mm, "end": v(286.04, 142.87) * mm});
            skLineSegment(sketch, "E2747", {"start": v(286.04, 142.87) * mm, "end": v(286.23, 143.04) * mm});
            skLineSegment(sketch, "E2748", {"start": v(286.23, 143.04) * mm, "end": v(286.43, 143.19) * mm});
            skLineSegment(sketch, "E2749", {"start": v(286.43, 143.19) * mm, "end": v(286.65, 143.3) * mm});
            skLineSegment(sketch, "E2750", {"start": v(286.65, 143.3) * mm, "end": v(286.88, 143.4) * mm});
            skLineSegment(sketch, "E2751", {"start": v(286.88, 143.4) * mm, "end": v(287.12, 143.47) * mm});
            skLineSegment(sketch, "E2752", {"start": v(287.12, 143.47) * mm, "end": v(287.37, 143.5) * mm});
            skLineSegment(sketch, "E2753", {"start": v(287.37, 143.5) * mm, "end": v(287.63, 143.5) * mm});
            skLineSegment(sketch, "E2754", {"start": v(287.63, 143.5) * mm, "end": v(287.88, 143.47) * mm});
            skLineSegment(sketch, "E2755", {"start": v(287.88, 143.47) * mm, "end": v(288.12, 143.4) * mm});
            skLineSegment(sketch, "E2756", {"start": v(288.12, 143.4) * mm, "end": v(288.35, 143.3) * mm});
            skLineSegment(sketch, "E2757", {"start": v(288.35, 143.3) * mm, "end": v(288.57, 143.19) * mm});
            skLineSegment(sketch, "E2758", {"start": v(288.57, 143.19) * mm, "end": v(288.77, 143.04) * mm});
            skLineSegment(sketch, "E2759", {"start": v(288.77, 143.04) * mm, "end": v(288.96, 142.87) * mm});
            skLineSegment(sketch, "E2760", {"start": v(288.96, 142.87) * mm, "end": v(289.12, 142.68) * mm});
            skLineSegment(sketch, "E2761", {"start": v(289.12, 142.68) * mm, "end": v(289.25, 142.46) * mm});
            skLineSegment(sketch, "E2762", {"start": v(289.25, 142.46) * mm, "end": v(289.36, 142.24) * mm});
            skLineSegment(sketch, "E2763", {"start": v(289.36, 142.24) * mm, "end": v(289.44, 142) * mm});
            skLineSegment(sketch, "E2764", {"start": v(289.44, 142) * mm, "end": v(289.48, 141.75) * mm});
            skLineSegment(sketch, "E2765", {"start": v(289.48, 141.75) * mm, "end": v(289.5, 141.5) * mm});
            skLineSegment(sketch, "E2766", {"start": v(289.5, 141.5) * mm, "end": v(289.48, 141.25) * mm});
            skLineSegment(sketch, "E2767", {"start": v(289.48, 141.25) * mm, "end": v(289.44, 141) * mm});
            skLineSegment(sketch, "E2768", {"start": v(289.44, 141) * mm, "end": v(289.36, 140.76) * mm});
            skLineSegment(sketch, "E2769", {"start": v(289.36, 140.76) * mm, "end": v(289.25, 140.54) * mm});
            skLineSegment(sketch, "E2770", {"start": v(289.25, 140.54) * mm, "end": v(289.12, 140.32) * mm});
            skLineSegment(sketch, "E2771", {"start": v(289.12, 140.32) * mm, "end": v(288.96, 140.13) * mm});
            skLineSegment(sketch, "E2772", {"start": v(288.96, 140.13) * mm, "end": v(288.77, 139.96) * mm});
            skLineSegment(sketch, "E2773", {"start": v(288.77, 139.96) * mm, "end": v(288.57, 139.81) * mm});
            skLineSegment(sketch, "E2774", {"start": v(288.57, 139.81) * mm, "end": v(288.35, 139.7) * mm});
            skLineSegment(sketch, "E2775", {"start": v(288.35, 139.7) * mm, "end": v(288.12, 139.6) * mm});
            skLineSegment(sketch, "E2776", {"start": v(288.12, 139.6) * mm, "end": v(287.88, 139.53) * mm});
            skLineSegment(sketch, "E2777", {"start": v(287.88, 139.53) * mm, "end": v(287.63, 139.5) * mm});
            skLineSegment(sketch, "E2778", {"start": v(287.63, 139.5) * mm, "end": v(287.37, 139.5) * mm});
            skLineSegment(sketch, "E2779", {"start": v(-234, 154) * mm, "end": v(-171, 154) * mm});
            skLineSegment(sketch, "E2780", {"start": v(-171, 154) * mm, "end": v(-222.99, 314) * mm});
            skLineSegment(sketch, "E2781", {"start": v(-222.99, 314) * mm, "end": v(-223, 314) * mm});
            skLineSegment(sketch, "E2782", {"start": v(-223, 314) * mm, "end": v(-272.94, 467.68) * mm});
            skLineSegment(sketch, "E2783", {"start": v(-272.94, 467.68) * mm, "end": v(-273.48, 468.82) * mm});
            skLineSegment(sketch, "E2784", {"start": v(-273.48, 468.82) * mm, "end": v(-274.15, 469.88) * mm});
            skLineSegment(sketch, "E2785", {"start": v(-274.15, 469.88) * mm, "end": v(-274.95, 470.85) * mm});
            skLineSegment(sketch, "E2786", {"start": v(-274.95, 470.85) * mm, "end": v(-275.87, 471.7) * mm});
            skLineSegment(sketch, "E2787", {"start": v(-275.87, 471.7) * mm, "end": v(-276.88, 472.44) * mm});
            skLineSegment(sketch, "E2788", {"start": v(-276.88, 472.44) * mm, "end": v(-277.98, 473.05) * mm});
            skLineSegment(sketch, "E2789", {"start": v(-277.98, 473.05) * mm, "end": v(-279.15, 473.5) * mm});
            skLineSegment(sketch, "E2790", {"start": v(-279.15, 473.5) * mm, "end": v(-280.37, 473.82) * mm});
            skLineSegment(sketch, "E2791", {"start": v(-280.37, 473.82) * mm, "end": v(-281.61, 473.98) * mm});
            skLineSegment(sketch, "E2792", {"start": v(-281.61, 473.98) * mm, "end": v(-299, 473.98) * mm});
            skLineSegment(sketch, "E2793", {"start": v(-299, 473.98) * mm, "end": v(-299, 474) * mm});
            skLineSegment(sketch, "E2794", {"start": v(-299, 474) * mm, "end": v(-325, 474) * mm});
            skLineSegment(sketch, "E2795", {"start": v(-325, 474) * mm, "end": v(-325, 454) * mm});
            skLineSegment(sketch, "E2796", {"start": v(-325, 454) * mm, "end": v(-309, 454) * mm});
            skLineSegment(sketch, "E2797", {"start": v(-309, 454) * mm, "end": v(-309, 334) * mm});
            skLineSegment(sketch, "E2798", {"start": v(-309, 334) * mm, "end": v(-325, 334) * mm});
            skLineSegment(sketch, "E2799", {"start": v(-325, 334) * mm, "end": v(-325, 314) * mm});
            skLineSegment(sketch, "E2800", {"start": v(-325, 314) * mm, "end": v(-309, 314) * mm});
            skLineSegment(sketch, "E2801", {"start": v(-309, 314) * mm, "end": v(-309, 194) * mm});
            skLineSegment(sketch, "E2802", {"start": v(-309, 194) * mm, "end": v(-325, 194) * mm});
            skLineSegment(sketch, "E2803", {"start": v(-325, 194) * mm, "end": v(-325, 174) * mm});
            skLineSegment(sketch, "E2804", {"start": v(-325, 174) * mm, "end": v(-309, 174) * mm});
            skLineSegment(sketch, "E2805", {"start": v(-309, 174) * mm, "end": v(-309, 154) * mm});
            skLineSegment(sketch, "E2806", {"start": v(-309, 154) * mm, "end": v(-254, 154) * mm});
            skLineSegment(sketch, "E2807", {"start": v(-254, 154) * mm, "end": v(-254, 138) * mm});
            skLineSegment(sketch, "E2808", {"start": v(-254, 138) * mm, "end": v(-234, 138) * mm});
            skLineSegment(sketch, "E2809", {"start": v(-234, 138) * mm, "end": v(-234, 154) * mm});
            skLineSegment(sketch, "E2810", {"start": v(-85, 158) * mm, "end": v(-101, 158) * mm});
            skLineSegment(sketch, "E2811", {"start": v(-101, 158) * mm, "end": v(-101, 278) * mm});
            skLineSegment(sketch, "E2812", {"start": v(-101, 278) * mm, "end": v(-85, 278) * mm});
            skLineSegment(sketch, "E2813", {"start": v(-85, 278) * mm, "end": v(-85, 298) * mm});
            skLineSegment(sketch, "E2814", {"start": v(-85, 298) * mm, "end": v(-101, 298) * mm});
            skLineSegment(sketch, "E2815", {"start": v(-101, 298) * mm, "end": v(-101, 418) * mm});
            skLineSegment(sketch, "E2816", {"start": v(-101, 418) * mm, "end": v(-85, 418) * mm});
            skLineSegment(sketch, "E2817", {"start": v(-85, 418) * mm, "end": v(-85, 438) * mm});
            skLineSegment(sketch, "E2818", {"start": v(-85, 438) * mm, "end": v(-101, 438) * mm});
            skLineSegment(sketch, "E2819", {"start": v(-101, 438) * mm, "end": v(-101, 458) * mm});
            skLineSegment(sketch, "E2820", {"start": v(-101, 458) * mm, "end": v(-156, 458) * mm});
            skLineSegment(sketch, "E2821", {"start": v(-156, 458) * mm, "end": v(-156, 474) * mm});
            skLineSegment(sketch, "E2822", {"start": v(-156, 474) * mm, "end": v(-176, 474) * mm});
            skLineSegment(sketch, "E2823", {"start": v(-176, 474) * mm, "end": v(-176, 458) * mm});
            skLineSegment(sketch, "E2824", {"start": v(-176, 458) * mm, "end": v(-239, 458) * mm});
            skLineSegment(sketch, "E2825", {"start": v(-239, 458) * mm, "end": v(-187.01, 298) * mm});
            skLineSegment(sketch, "E2826", {"start": v(-187.01, 298) * mm, "end": v(-187, 298) * mm});
            skLineSegment(sketch, "E2827", {"start": v(-187, 298) * mm, "end": v(-137.06, 144.32) * mm});
            skLineSegment(sketch, "E2828", {"start": v(-137.06, 144.32) * mm, "end": v(-136.52, 143.18) * mm});
            skLineSegment(sketch, "E2829", {"start": v(-136.52, 143.18) * mm, "end": v(-135.85, 142.12) * mm});
            skLineSegment(sketch, "E2830", {"start": v(-135.85, 142.12) * mm, "end": v(-135.05, 141.16) * mm});
            skLineSegment(sketch, "E2831", {"start": v(-135.05, 141.16) * mm, "end": v(-134.13, 140.3) * mm});
            skLineSegment(sketch, "E2832", {"start": v(-134.13, 140.3) * mm, "end": v(-133.12, 139.56) * mm});
            skLineSegment(sketch, "E2833", {"start": v(-133.12, 139.56) * mm, "end": v(-132.02, 138.95) * mm});
            skLineSegment(sketch, "E2834", {"start": v(-132.02, 138.95) * mm, "end": v(-130.85, 138.49) * mm});
            skLineSegment(sketch, "E2835", {"start": v(-130.85, 138.49) * mm, "end": v(-129.63, 138.18) * mm});
            skLineSegment(sketch, "E2836", {"start": v(-129.63, 138.18) * mm, "end": v(-128.39, 138.02) * mm});
            skLineSegment(sketch, "E2837", {"start": v(-128.39, 138.02) * mm, "end": v(-111, 138.02) * mm});
            skLineSegment(sketch, "E2838", {"start": v(-111, 138.02) * mm, "end": v(-111, 138) * mm});
            skLineSegment(sketch, "E2839", {"start": v(-111, 138) * mm, "end": v(-85, 138) * mm});
            skLineSegment(sketch, "E2840", {"start": v(-85, 138) * mm, "end": v(-85, 158) * mm});
            skLineSegment(sketch, "E2841", {"start": v(-370, 37.02) * mm, "end": v(-369.37, 37.02) * mm});
            skLineSegment(sketch, "E2842", {"start": v(-369.37, 37.02) * mm, "end": v(-368.13, 37.18) * mm});
            skLineSegment(sketch, "E2843", {"start": v(-368.13, 37.18) * mm, "end": v(-366.91, 37.49) * mm});
            skLineSegment(sketch, "E2844", {"start": v(-366.91, 37.49) * mm, "end": v(-365.74, 37.95) * mm});
            skLineSegment(sketch, "E2845", {"start": v(-365.74, 37.95) * mm, "end": v(-364.64, 38.56) * mm});
            skLineSegment(sketch, "E2846", {"start": v(-364.64, 38.56) * mm, "end": v(-363.63, 39.3) * mm});
            skLineSegment(sketch, "E2847", {"start": v(-363.63, 39.3) * mm, "end": v(-362.7, 40.16) * mm});
            skLineSegment(sketch, "E2848", {"start": v(-362.7, 40.16) * mm, "end": v(-361.91, 41.12) * mm});
            skLineSegment(sketch, "E2849", {"start": v(-361.91, 41.12) * mm, "end": v(-361.24, 42.18) * mm});
            skLineSegment(sketch, "E2850", {"start": v(-361.24, 42.18) * mm, "end": v(-360.7, 43.32) * mm});
            skLineSegment(sketch, "E2851", {"start": v(-360.7, 43.32) * mm, "end": v(-360.31, 44.51) * mm});
            skLineSegment(sketch, "E2852", {"start": v(-360.31, 44.51) * mm, "end": v(-360.08, 45.75) * mm});
            skLineSegment(sketch, "E2853", {"start": v(-360.08, 45.75) * mm, "end": v(-360, 47) * mm});
            skLineSegment(sketch, "E2854", {"start": v(-360, 47) * mm, "end": v(-359.98, 47) * mm});
            skLineSegment(sketch, "E2855", {"start": v(-359.98, 47) * mm, "end": v(-359.98, 47.63) * mm});
            skLineSegment(sketch, "E2856", {"start": v(-359.98, 47.63) * mm, "end": v(-359.82, 48.87) * mm});
            skLineSegment(sketch, "E2857", {"start": v(-359.82, 48.87) * mm, "end": v(-359.51, 50.1) * mm});
            skLineSegment(sketch, "E2858", {"start": v(-359.51, 50.1) * mm, "end": v(-359.05, 51.26) * mm});
            skLineSegment(sketch, "E2859", {"start": v(-359.05, 51.26) * mm, "end": v(-358.44, 52.36) * mm});
            skLineSegment(sketch, "E2860", {"start": v(-358.44, 52.36) * mm, "end": v(-357.7, 53.37) * mm});
            skLineSegment(sketch, "E2861", {"start": v(-357.7, 53.37) * mm, "end": v(-356.85, 54.3) * mm});
            skLineSegment(sketch, "E2862", {"start": v(-356.85, 54.3) * mm, "end": v(-355.88, 55.1) * mm});
            skLineSegment(sketch, "E2863", {"start": v(-355.88, 55.1) * mm, "end": v(-354.82, 55.76) * mm});
            skLineSegment(sketch, "E2864", {"start": v(-354.82, 55.76) * mm, "end": v(-353.68, 56.3) * mm});
            skLineSegment(sketch, "E2865", {"start": v(-353.68, 56.3) * mm, "end": v(-352.49, 56.69) * mm});
            skLineSegment(sketch, "E2866", {"start": v(-352.49, 56.69) * mm, "end": v(-351.25, 56.92) * mm});
            skLineSegment(sketch, "E2867", {"start": v(-351.25, 56.92) * mm, "end": v(-350, 57) * mm});
            skLineSegment(sketch, "E2868", {"start": v(-350, 57) * mm, "end": v(-60, 57) * mm});
            skLineSegment(sketch, "E2869", {"start": v(-60, 57) * mm, "end": v(-60, 56.98) * mm});
            skLineSegment(sketch, "E2870", {"start": v(-60, 56.98) * mm, "end": v(-59.37, 56.98) * mm});
            skLineSegment(sketch, "E2871", {"start": v(-59.37, 56.98) * mm, "end": v(-58.13, 56.82) * mm});
            skLineSegment(sketch, "E2872", {"start": v(-58.13, 56.82) * mm, "end": v(-56.9, 56.51) * mm});
            skLineSegment(sketch, "E2873", {"start": v(-56.9, 56.51) * mm, "end": v(-55.74, 56.05) * mm});
            skLineSegment(sketch, "E2874", {"start": v(-55.74, 56.05) * mm, "end": v(-54.64, 55.44) * mm});
            skLineSegment(sketch, "E2875", {"start": v(-54.64, 55.44) * mm, "end": v(-53.63, 54.7) * mm});
            skLineSegment(sketch, "E2876", {"start": v(-53.63, 54.7) * mm, "end": v(-52.71, 53.84) * mm});
            skLineSegment(sketch, "E2877", {"start": v(-52.71, 53.84) * mm, "end": v(-51.9, 52.88) * mm});
            skLineSegment(sketch, "E2878", {"start": v(-51.9, 52.88) * mm, "end": v(-51.24, 51.82) * mm});
            skLineSegment(sketch, "E2879", {"start": v(-51.24, 51.82) * mm, "end": v(-50.7, 50.68) * mm});
            skLineSegment(sketch, "E2880", {"start": v(-50.7, 50.68) * mm, "end": v(-50.31, 49.49) * mm});
            skLineSegment(sketch, "E2881", {"start": v(-50.31, 49.49) * mm, "end": v(-50.08, 48.25) * mm});
            skLineSegment(sketch, "E2882", {"start": v(-50.08, 48.25) * mm, "end": v(-49.92, 45.75) * mm});
            skLineSegment(sketch, "E2883", {"start": v(-49.92, 45.75) * mm, "end": v(-49.69, 44.51) * mm});
            skLineSegment(sketch, "E2884", {"start": v(-49.69, 44.51) * mm, "end": v(-49.3, 43.32) * mm});
            skLineSegment(sketch, "E2885", {"start": v(-49.3, 43.32) * mm, "end": v(-48.76, 42.18) * mm});
            skLineSegment(sketch, "E2886", {"start": v(-48.76, 42.18) * mm, "end": v(-48.1, 41.12) * mm});
            skLineSegment(sketch, "E2887", {"start": v(-48.1, 41.12) * mm, "end": v(-47.29, 40.16) * mm});
            skLineSegment(sketch, "E2888", {"start": v(-47.29, 40.16) * mm, "end": v(-46.37, 39.3) * mm});
            skLineSegment(sketch, "E2889", {"start": v(-46.37, 39.3) * mm, "end": v(-45.36, 38.56) * mm});
            skLineSegment(sketch, "E2890", {"start": v(-45.36, 38.56) * mm, "end": v(-44.26, 37.95) * mm});
            skLineSegment(sketch, "E2891", {"start": v(-44.26, 37.95) * mm, "end": v(-43.1, 37.49) * mm});
            skLineSegment(sketch, "E2892", {"start": v(-43.1, 37.49) * mm, "end": v(-41.87, 37.18) * mm});
            skLineSegment(sketch, "E2893", {"start": v(-41.87, 37.18) * mm, "end": v(-40.63, 37.02) * mm});
            skLineSegment(sketch, "E2894", {"start": v(-40.63, 37.02) * mm, "end": v(-40, 37.02) * mm});
            skLineSegment(sketch, "E2895", {"start": v(-40, 37.02) * mm, "end": v(-40, 37) * mm});
            skLineSegment(sketch, "E2896", {"start": v(-40, 37) * mm, "end": v(-20, 37) * mm});
            skLineSegment(sketch, "E2897", {"start": v(-20, 37) * mm, "end": v(-18.75, 37.08) * mm});
            skLineSegment(sketch, "E2898", {"start": v(-18.75, 37.08) * mm, "end": v(-17.51, 37.31) * mm});
            skLineSegment(sketch, "E2899", {"start": v(-17.51, 37.31) * mm, "end": v(-16.32, 37.7) * mm});
            skLineSegment(sketch, "E2900", {"start": v(-16.32, 37.7) * mm, "end": v(-15.18, 38.24) * mm});
            skLineSegment(sketch, "E2901", {"start": v(-15.18, 38.24) * mm, "end": v(-14.12, 38.9) * mm});
            skLineSegment(sketch, "E2902", {"start": v(-14.12, 38.9) * mm, "end": v(-13.15, 39.7) * mm});
            skLineSegment(sketch, "E2903", {"start": v(-13.15, 39.7) * mm, "end": v(-12.3, 40.63) * mm});
            skLineSegment(sketch, "E2904", {"start": v(-12.3, 40.63) * mm, "end": v(-11.56, 41.64) * mm});
            skLineSegment(sketch, "E2905", {"start": v(-11.56, 41.64) * mm, "end": v(-10.95, 42.74) * mm});
            skLineSegment(sketch, "E2906", {"start": v(-10.95, 42.74) * mm, "end": v(-10.49, 43.9) * mm});
            skLineSegment(sketch, "E2907", {"start": v(-10.49, 43.9) * mm, "end": v(-10.18, 45.13) * mm});
            skLineSegment(sketch, "E2908", {"start": v(-10.18, 45.13) * mm, "end": v(-10.02, 46.37) * mm});
            skLineSegment(sketch, "E2909", {"start": v(-10.02, 46.37) * mm, "end": v(-10.02, 47) * mm});
            skLineSegment(sketch, "E2910", {"start": v(-10.02, 47) * mm, "end": v(-10, 47) * mm});
            skLineSegment(sketch, "E2911", {"start": v(-10, 47) * mm, "end": v(-10, 97) * mm});
            skLineSegment(sketch, "E2912", {"start": v(-10, 97) * mm, "end": v(-50, 97) * mm});
            skLineSegment(sketch, "E2913", {"start": v(-50, 97) * mm, "end": v(-50, 113) * mm});
            skLineSegment(sketch, "E2914", {"start": v(-50, 113) * mm, "end": v(-70, 113) * mm});
            skLineSegment(sketch, "E2915", {"start": v(-70, 113) * mm, "end": v(-70, 97) * mm});
            skLineSegment(sketch, "E2916", {"start": v(-70, 97) * mm, "end": v(-195, 97) * mm});
            skLineSegment(sketch, "E2917", {"start": v(-195, 97) * mm, "end": v(-195, 113) * mm});
            skLineSegment(sketch, "E2918", {"start": v(-195, 113) * mm, "end": v(-215, 113) * mm});
            skLineSegment(sketch, "E2919", {"start": v(-215, 113) * mm, "end": v(-215, 97) * mm});
            skLineSegment(sketch, "E2920", {"start": v(-215, 97) * mm, "end": v(-340, 97) * mm});
            skLineSegment(sketch, "E2921", {"start": v(-340, 97) * mm, "end": v(-340, 113) * mm});
            skLineSegment(sketch, "E2922", {"start": v(-340, 113) * mm, "end": v(-360, 113) * mm});
            skLineSegment(sketch, "E2923", {"start": v(-360, 113) * mm, "end": v(-360, 97) * mm});
            skLineSegment(sketch, "E2924", {"start": v(-360, 97) * mm, "end": v(-400, 97) * mm});
            skLineSegment(sketch, "E2925", {"start": v(-400, 97) * mm, "end": v(-400, 47) * mm});
            skLineSegment(sketch, "E2926", {"start": v(-400, 47) * mm, "end": v(-399.92, 45.75) * mm});
            skLineSegment(sketch, "E2927", {"start": v(-399.92, 45.75) * mm, "end": v(-399.69, 44.51) * mm});
            skLineSegment(sketch, "E2928", {"start": v(-399.69, 44.51) * mm, "end": v(-399.3, 43.32) * mm});
            skLineSegment(sketch, "E2929", {"start": v(-399.3, 43.32) * mm, "end": v(-398.76, 42.18) * mm});
            skLineSegment(sketch, "E2930", {"start": v(-398.76, 42.18) * mm, "end": v(-398.09, 41.12) * mm});
            skLineSegment(sketch, "E2931", {"start": v(-398.09, 41.12) * mm, "end": v(-397.3, 40.16) * mm});
            skLineSegment(sketch, "E2932", {"start": v(-397.3, 40.16) * mm, "end": v(-396.37, 39.3) * mm});
            skLineSegment(sketch, "E2933", {"start": v(-396.37, 39.3) * mm, "end": v(-395.36, 38.56) * mm});
            skLineSegment(sketch, "E2934", {"start": v(-395.36, 38.56) * mm, "end": v(-394.26, 37.95) * mm});
            skLineSegment(sketch, "E2935", {"start": v(-394.26, 37.95) * mm, "end": v(-393.09, 37.49) * mm});
            skLineSegment(sketch, "E2936", {"start": v(-393.09, 37.49) * mm, "end": v(-391.87, 37.18) * mm});
            skLineSegment(sketch, "E2937", {"start": v(-391.87, 37.18) * mm, "end": v(-390.63, 37.02) * mm});
            skLineSegment(sketch, "E2938", {"start": v(-390.63, 37.02) * mm, "end": v(-390, 37.02) * mm});
            skLineSegment(sketch, "E2939", {"start": v(-390, 37.02) * mm, "end": v(-390, 37) * mm});
            skLineSegment(sketch, "E2940", {"start": v(-390, 37) * mm, "end": v(-370, 37) * mm});
            skLineSegment(sketch, "E2941", {"start": v(-370, 37) * mm, "end": v(-370, 37.02) * mm});
            skLineSegment(sketch, "E2942", {"start": v(40, 37.02) * mm, "end": v(40.63, 37.02) * mm});
            skLineSegment(sketch, "E2943", {"start": v(40.63, 37.02) * mm, "end": v(41.87, 37.18) * mm});
            skLineSegment(sketch, "E2944", {"start": v(41.87, 37.18) * mm, "end": v(43.1, 37.49) * mm});
            skLineSegment(sketch, "E2945", {"start": v(43.1, 37.49) * mm, "end": v(44.26, 37.95) * mm});
            skLineSegment(sketch, "E2946", {"start": v(44.26, 37.95) * mm, "end": v(45.36, 38.56) * mm});
            skLineSegment(sketch, "E2947", {"start": v(45.36, 38.56) * mm, "end": v(46.37, 39.3) * mm});
            skLineSegment(sketch, "E2948", {"start": v(46.37, 39.3) * mm, "end": v(47.29, 40.16) * mm});
            skLineSegment(sketch, "E2949", {"start": v(47.29, 40.16) * mm, "end": v(48.1, 41.12) * mm});
            skLineSegment(sketch, "E2950", {"start": v(48.1, 41.12) * mm, "end": v(48.76, 42.18) * mm});
            skLineSegment(sketch, "E2951", {"start": v(48.76, 42.18) * mm, "end": v(49.3, 43.32) * mm});
            skLineSegment(sketch, "E2952", {"start": v(49.3, 43.32) * mm, "end": v(49.69, 44.51) * mm});
            skLineSegment(sketch, "E2953", {"start": v(49.69, 44.51) * mm, "end": v(49.92, 45.75) * mm});
            skLineSegment(sketch, "E2954", {"start": v(49.92, 45.75) * mm, "end": v(50, 47) * mm});
            skLineSegment(sketch, "E2955", {"start": v(50, 47) * mm, "end": v(50.02, 47) * mm});
            skLineSegment(sketch, "E2956", {"start": v(50.02, 47) * mm, "end": v(50.02, 47.63) * mm});
            skLineSegment(sketch, "E2957", {"start": v(50.02, 47.63) * mm, "end": v(50.18, 48.87) * mm});
            skLineSegment(sketch, "E2958", {"start": v(50.18, 48.87) * mm, "end": v(50.49, 50.1) * mm});
            skLineSegment(sketch, "E2959", {"start": v(50.49, 50.1) * mm, "end": v(50.95, 51.26) * mm});
            skLineSegment(sketch, "E2960", {"start": v(50.95, 51.26) * mm, "end": v(51.56, 52.36) * mm});
            skLineSegment(sketch, "E2961", {"start": v(51.56, 52.36) * mm, "end": v(52.3, 53.37) * mm});
            skLineSegment(sketch, "E2962", {"start": v(52.3, 53.37) * mm, "end": v(53.15, 54.3) * mm});
            skLineSegment(sketch, "E2963", {"start": v(53.15, 54.3) * mm, "end": v(54.12, 55.1) * mm});
            skLineSegment(sketch, "E2964", {"start": v(54.12, 55.1) * mm, "end": v(55.18, 55.76) * mm});
            skLineSegment(sketch, "E2965", {"start": v(55.18, 55.76) * mm, "end": v(56.32, 56.3) * mm});
            skLineSegment(sketch, "E2966", {"start": v(56.32, 56.3) * mm, "end": v(57.51, 56.69) * mm});
            skLineSegment(sketch, "E2967", {"start": v(57.51, 56.69) * mm, "end": v(58.75, 56.92) * mm});
            skLineSegment(sketch, "E2968", {"start": v(58.75, 56.92) * mm, "end": v(60, 57) * mm});
            skLineSegment(sketch, "E2969", {"start": v(60, 57) * mm, "end": v(350, 57) * mm});
            skLineSegment(sketch, "E2970", {"start": v(350, 57) * mm, "end": v(350, 56.98) * mm});
            skLineSegment(sketch, "E2971", {"start": v(350, 56.98) * mm, "end": v(350.63, 56.98) * mm});
            skLineSegment(sketch, "E2972", {"start": v(350.63, 56.98) * mm, "end": v(351.87, 56.82) * mm});
            skLineSegment(sketch, "E2973", {"start": v(351.87, 56.82) * mm, "end": v(353.09, 56.51) * mm});
            skLineSegment(sketch, "E2974", {"start": v(353.09, 56.51) * mm, "end": v(354.26, 56.05) * mm});
            skLineSegment(sketch, "E2975", {"start": v(354.26, 56.05) * mm, "end": v(355.36, 55.44) * mm});
            skLineSegment(sketch, "E2976", {"start": v(355.36, 55.44) * mm, "end": v(356.37, 54.7) * mm});
            skLineSegment(sketch, "E2977", {"start": v(356.37, 54.7) * mm, "end": v(357.3, 53.84) * mm});
            skLineSegment(sketch, "E2978", {"start": v(357.3, 53.84) * mm, "end": v(358.09, 52.88) * mm});
            skLineSegment(sketch, "E2979", {"start": v(358.09, 52.88) * mm, "end": v(358.76, 51.82) * mm});
            skLineSegment(sketch, "E2980", {"start": v(358.76, 51.82) * mm, "end": v(359.3, 50.68) * mm});
            skLineSegment(sketch, "E2981", {"start": v(359.3, 50.68) * mm, "end": v(359.69, 49.49) * mm});
            skLineSegment(sketch, "E2982", {"start": v(359.69, 49.49) * mm, "end": v(359.92, 48.25) * mm});
            skLineSegment(sketch, "E2983", {"start": v(359.92, 48.25) * mm, "end": v(360.08, 45.75) * mm});
            skLineSegment(sketch, "E2984", {"start": v(360.08, 45.75) * mm, "end": v(360.31, 44.51) * mm});
            skLineSegment(sketch, "E2985", {"start": v(360.31, 44.51) * mm, "end": v(360.7, 43.32) * mm});
            skLineSegment(sketch, "E2986", {"start": v(360.7, 43.32) * mm, "end": v(361.24, 42.18) * mm});
            skLineSegment(sketch, "E2987", {"start": v(361.24, 42.18) * mm, "end": v(361.91, 41.12) * mm});
            skLineSegment(sketch, "E2988", {"start": v(361.91, 41.12) * mm, "end": v(362.7, 40.16) * mm});
            skLineSegment(sketch, "E2989", {"start": v(362.7, 40.16) * mm, "end": v(363.63, 39.3) * mm});
            skLineSegment(sketch, "E2990", {"start": v(363.63, 39.3) * mm, "end": v(364.64, 38.56) * mm});
            skLineSegment(sketch, "E2991", {"start": v(364.64, 38.56) * mm, "end": v(365.74, 37.95) * mm});
            skLineSegment(sketch, "E2992", {"start": v(365.74, 37.95) * mm, "end": v(366.91, 37.49) * mm});
            skLineSegment(sketch, "E2993", {"start": v(366.91, 37.49) * mm, "end": v(368.13, 37.18) * mm});
            skLineSegment(sketch, "E2994", {"start": v(368.13, 37.18) * mm, "end": v(369.37, 37.02) * mm});
            skLineSegment(sketch, "E2995", {"start": v(369.37, 37.02) * mm, "end": v(370, 37.02) * mm});
            skLineSegment(sketch, "E2996", {"start": v(370, 37.02) * mm, "end": v(370, 37) * mm});
            skLineSegment(sketch, "E2997", {"start": v(370, 37) * mm, "end": v(390, 37) * mm});
            skLineSegment(sketch, "E2998", {"start": v(390, 37) * mm, "end": v(391.25, 37.08) * mm});
            skLineSegment(sketch, "E2999", {"start": v(391.25, 37.08) * mm, "end": v(392.49, 37.31) * mm});
            skLineSegment(sketch, "E3000", {"start": v(392.49, 37.31) * mm, "end": v(393.68, 37.7) * mm});
            skLineSegment(sketch, "E3001", {"start": v(393.68, 37.7) * mm, "end": v(394.82, 38.24) * mm});
            skLineSegment(sketch, "E3002", {"start": v(394.82, 38.24) * mm, "end": v(395.88, 38.9) * mm});
            skLineSegment(sketch, "E3003", {"start": v(395.88, 38.9) * mm, "end": v(396.85, 39.7) * mm});
            skLineSegment(sketch, "E3004", {"start": v(396.85, 39.7) * mm, "end": v(397.7, 40.63) * mm});
            skLineSegment(sketch, "E3005", {"start": v(397.7, 40.63) * mm, "end": v(398.44, 41.64) * mm});
            skLineSegment(sketch, "E3006", {"start": v(398.44, 41.64) * mm, "end": v(399.05, 42.74) * mm});
            skLineSegment(sketch, "E3007", {"start": v(399.05, 42.74) * mm, "end": v(399.51, 43.9) * mm});
            skLineSegment(sketch, "E3008", {"start": v(399.51, 43.9) * mm, "end": v(399.82, 45.13) * mm});
            skLineSegment(sketch, "E3009", {"start": v(399.82, 45.13) * mm, "end": v(399.98, 46.37) * mm});
            skLineSegment(sketch, "E3010", {"start": v(399.98, 46.37) * mm, "end": v(399.98, 47) * mm});
            skLineSegment(sketch, "E3011", {"start": v(399.98, 47) * mm, "end": v(400, 47) * mm});
            skLineSegment(sketch, "E3012", {"start": v(400, 47) * mm, "end": v(400, 97) * mm});
            skLineSegment(sketch, "E3013", {"start": v(400, 97) * mm, "end": v(360, 97) * mm});
            skLineSegment(sketch, "E3014", {"start": v(360, 97) * mm, "end": v(360, 113) * mm});
            skLineSegment(sketch, "E3015", {"start": v(360, 113) * mm, "end": v(340, 113) * mm});
            skLineSegment(sketch, "E3016", {"start": v(340, 113) * mm, "end": v(340, 97) * mm});
            skLineSegment(sketch, "E3017", {"start": v(340, 97) * mm, "end": v(215, 97) * mm});
            skLineSegment(sketch, "E3018", {"start": v(215, 97) * mm, "end": v(215, 113) * mm});
            skLineSegment(sketch, "E3019", {"start": v(215, 113) * mm, "end": v(195, 113) * mm});
            skLineSegment(sketch, "E3020", {"start": v(195, 113) * mm, "end": v(195, 97) * mm});
            skLineSegment(sketch, "E3021", {"start": v(195, 97) * mm, "end": v(70, 97) * mm});
            skLineSegment(sketch, "E3022", {"start": v(70, 97) * mm, "end": v(70, 113) * mm});
            skLineSegment(sketch, "E3023", {"start": v(70, 113) * mm, "end": v(50, 113) * mm});
            skLineSegment(sketch, "E3024", {"start": v(50, 113) * mm, "end": v(50, 97) * mm});
            skLineSegment(sketch, "E3025", {"start": v(50, 97) * mm, "end": v(10, 97) * mm});
            skLineSegment(sketch, "E3026", {"start": v(10, 97) * mm, "end": v(10, 47) * mm});
            skLineSegment(sketch, "E3027", {"start": v(10, 47) * mm, "end": v(10.08, 45.75) * mm});
            skLineSegment(sketch, "E3028", {"start": v(10.08, 45.75) * mm, "end": v(10.31, 44.51) * mm});
            skLineSegment(sketch, "E3029", {"start": v(10.31, 44.51) * mm, "end": v(10.7, 43.32) * mm});
            skLineSegment(sketch, "E3030", {"start": v(10.7, 43.32) * mm, "end": v(11.24, 42.18) * mm});
            skLineSegment(sketch, "E3031", {"start": v(11.24, 42.18) * mm, "end": v(11.9, 41.12) * mm});
            skLineSegment(sketch, "E3032", {"start": v(11.9, 41.12) * mm, "end": v(12.71, 40.16) * mm});
            skLineSegment(sketch, "E3033", {"start": v(12.71, 40.16) * mm, "end": v(13.63, 39.3) * mm});
            skLineSegment(sketch, "E3034", {"start": v(13.63, 39.3) * mm, "end": v(14.64, 38.56) * mm});
            skLineSegment(sketch, "E3035", {"start": v(14.64, 38.56) * mm, "end": v(15.74, 37.95) * mm});
            skLineSegment(sketch, "E3036", {"start": v(15.74, 37.95) * mm, "end": v(16.9, 37.49) * mm});
            skLineSegment(sketch, "E3037", {"start": v(16.9, 37.49) * mm, "end": v(18.13, 37.18) * mm});
            skLineSegment(sketch, "E3038", {"start": v(18.13, 37.18) * mm, "end": v(19.37, 37.02) * mm});
            skLineSegment(sketch, "E3039", {"start": v(19.37, 37.02) * mm, "end": v(20, 37.02) * mm});
            skLineSegment(sketch, "E3040", {"start": v(20, 37.02) * mm, "end": v(20, 37) * mm});
            skLineSegment(sketch, "E3041", {"start": v(20, 37) * mm, "end": v(40, 37) * mm});
            skLineSegment(sketch, "E3042", {"start": v(40, 37) * mm, "end": v(40, 37.02) * mm});
            skLineSegment(sketch, "E3043", {"start": v(-368.75, -476.92) * mm, "end": v(-367.51, -476.69) * mm});
            skLineSegment(sketch, "E3044", {"start": v(-367.51, -476.69) * mm, "end": v(-366.32, -476.3) * mm});
            skLineSegment(sketch, "E3045", {"start": v(-366.32, -476.3) * mm, "end": v(-365.18, -475.76) * mm});
            skLineSegment(sketch, "E3046", {"start": v(-365.18, -475.76) * mm, "end": v(-364.12, -475.1) * mm});
            skLineSegment(sketch, "E3047", {"start": v(-364.12, -475.1) * mm, "end": v(-363.16, -474.29) * mm});
            skLineSegment(sketch, "E3048", {"start": v(-363.16, -474.29) * mm, "end": v(-362.3, -473.37) * mm});
            skLineSegment(sketch, "E3049", {"start": v(-362.3, -473.37) * mm, "end": v(-361.56, -472.36) * mm});
            skLineSegment(sketch, "E3050", {"start": v(-361.56, -472.36) * mm, "end": v(-360.95, -471.26) * mm});
            skLineSegment(sketch, "E3051", {"start": v(-360.95, -471.26) * mm, "end": v(-360.49, -470.1) * mm});
            skLineSegment(sketch, "E3052", {"start": v(-360.49, -470.1) * mm, "end": v(-360.18, -468.87) * mm});
            skLineSegment(sketch, "E3053", {"start": v(-360.18, -468.87) * mm, "end": v(-360.02, -467.63) * mm});
            skLineSegment(sketch, "E3054", {"start": v(-360.02, -467.63) * mm, "end": v(-360.02, -467) * mm});
            skLineSegment(sketch, "E3055", {"start": v(-360.02, -467) * mm, "end": v(-360, -467) * mm});
            skLineSegment(sketch, "E3056", {"start": v(-360, -467) * mm, "end": v(-360, -417) * mm});
            skLineSegment(sketch, "E3057", {"start": v(-360, -417) * mm, "end": v(-340, -417) * mm});
            skLineSegment(sketch, "E3058", {"start": v(-340, -417) * mm, "end": v(-340, -107) * mm});
            skLineSegment(sketch, "E3059", {"start": v(-340, -107) * mm, "end": v(-339.98, -107) * mm});
            skLineSegment(sketch, "E3060", {"start": v(-339.98, -107) * mm, "end": v(-339.98, -106.37) * mm});
            skLineSegment(sketch, "E3061", {"start": v(-339.98, -106.37) * mm, "end": v(-339.82, -105.13) * mm});
            skLineSegment(sketch, "E3062", {"start": v(-339.82, -105.13) * mm, "end": v(-339.51, -103.9) * mm});
            skLineSegment(sketch, "E3063", {"start": v(-339.51, -103.9) * mm, "end": v(-339.05, -102.74) * mm});
            skLineSegment(sketch, "E3064", {"start": v(-339.05, -102.74) * mm, "end": v(-338.44, -101.64) * mm});
            skLineSegment(sketch, "E3065", {"start": v(-338.44, -101.64) * mm, "end": v(-337.7, -100.63) * mm});
            skLineSegment(sketch, "E3066", {"start": v(-337.7, -100.63) * mm, "end": v(-336.85, -99.7) * mm});
            skLineSegment(sketch, "E3067", {"start": v(-336.85, -99.7) * mm, "end": v(-335.88, -98.9) * mm});
            skLineSegment(sketch, "E3068", {"start": v(-335.88, -98.9) * mm, "end": v(-334.82, -98.24) * mm});
            skLineSegment(sketch, "E3069", {"start": v(-334.82, -98.24) * mm, "end": v(-333.68, -97.7) * mm});
            skLineSegment(sketch, "E3070", {"start": v(-333.68, -97.7) * mm, "end": v(-332.49, -97.31) * mm});
            skLineSegment(sketch, "E3071", {"start": v(-332.49, -97.31) * mm, "end": v(-331.25, -97.08) * mm});
            skLineSegment(sketch, "E3072", {"start": v(-331.25, -97.08) * mm, "end": v(-330, -97) * mm});
            skLineSegment(sketch, "E3073", {"start": v(-330, -97) * mm, "end": v(-80, -97) * mm});
            skLineSegment(sketch, "E3074", {"start": v(-80, -97) * mm, "end": v(-80, -97.02) * mm});
            skLineSegment(sketch, "E3075", {"start": v(-80, -97.02) * mm, "end": v(-79.37, -97.02) * mm});
            skLineSegment(sketch, "E3076", {"start": v(-79.37, -97.02) * mm, "end": v(-78.13, -97.18) * mm});
            skLineSegment(sketch, "E3077", {"start": v(-78.13, -97.18) * mm, "end": v(-76.9, -97.49) * mm});
            skLineSegment(sketch, "E3078", {"start": v(-76.9, -97.49) * mm, "end": v(-75.74, -97.95) * mm});
            skLineSegment(sketch, "E3079", {"start": v(-75.74, -97.95) * mm, "end": v(-74.64, -98.56) * mm});
            skLineSegment(sketch, "E3080", {"start": v(-74.64, -98.56) * mm, "end": v(-73.63, -99.3) * mm});
            skLineSegment(sketch, "E3081", {"start": v(-73.63, -99.3) * mm, "end": v(-72.71, -100.16) * mm});
            skLineSegment(sketch, "E3082", {"start": v(-72.71, -100.16) * mm, "end": v(-71.9, -101.12) * mm});
            skLineSegment(sketch, "E3083", {"start": v(-71.9, -101.12) * mm, "end": v(-71.24, -102.18) * mm});
            skLineSegment(sketch, "E3084", {"start": v(-71.24, -102.18) * mm, "end": v(-70.7, -103.32) * mm});
            skLineSegment(sketch, "E3085", {"start": v(-70.7, -103.32) * mm, "end": v(-70.31, -104.51) * mm});
            skLineSegment(sketch, "E3086", {"start": v(-70.31, -104.51) * mm, "end": v(-70.08, -105.75) * mm});
            skLineSegment(sketch, "E3087", {"start": v(-70.08, -105.75) * mm, "end": v(-70, -107) * mm});
            skLineSegment(sketch, "E3088", {"start": v(-70, -107) * mm, "end": v(-70, -417) * mm});
            skLineSegment(sketch, "E3089", {"start": v(-70, -417) * mm, "end": v(-50, -417) * mm});
            skLineSegment(sketch, "E3090", {"start": v(-50, -417) * mm, "end": v(-50, -467) * mm});
            skLineSegment(sketch, "E3091", {"start": v(-50, -467) * mm, "end": v(-49.92, -468.25) * mm});
            skLineSegment(sketch, "E3092", {"start": v(-49.92, -468.25) * mm, "end": v(-49.69, -469.49) * mm});
            skLineSegment(sketch, "E3093", {"start": v(-49.69, -469.49) * mm, "end": v(-49.3, -470.68) * mm});
            skLineSegment(sketch, "E3094", {"start": v(-49.3, -470.68) * mm, "end": v(-48.76, -471.82) * mm});
            skLineSegment(sketch, "E3095", {"start": v(-48.76, -471.82) * mm, "end": v(-48.1, -472.88) * mm});
            skLineSegment(sketch, "E3096", {"start": v(-48.1, -472.88) * mm, "end": v(-47.29, -473.85) * mm});
            skLineSegment(sketch, "E3097", {"start": v(-47.29, -473.85) * mm, "end": v(-46.37, -474.7) * mm});
            skLineSegment(sketch, "E3098", {"start": v(-46.37, -474.7) * mm, "end": v(-45.36, -475.44) * mm});
            skLineSegment(sketch, "E3099", {"start": v(-45.36, -475.44) * mm, "end": v(-44.26, -476.05) * mm});
            skLineSegment(sketch, "E3100", {"start": v(-44.26, -476.05) * mm, "end": v(-43.1, -476.51) * mm});
            skLineSegment(sketch, "E3101", {"start": v(-43.1, -476.51) * mm, "end": v(-41.87, -476.82) * mm});
            skLineSegment(sketch, "E3102", {"start": v(-41.87, -476.82) * mm, "end": v(-40.63, -476.98) * mm});
            skLineSegment(sketch, "E3103", {"start": v(-40.63, -476.98) * mm, "end": v(-40, -476.98) * mm});
            skLineSegment(sketch, "E3104", {"start": v(-40, -476.98) * mm, "end": v(-40, -477) * mm});
            skLineSegment(sketch, "E3105", {"start": v(-40, -477) * mm, "end": v(-20, -477) * mm});
            skLineSegment(sketch, "E3106", {"start": v(-20, -477) * mm, "end": v(-18.75, -476.92) * mm});
            skLineSegment(sketch, "E3107", {"start": v(-18.75, -476.92) * mm, "end": v(-17.51, -476.69) * mm});
            skLineSegment(sketch, "E3108", {"start": v(-17.51, -476.69) * mm, "end": v(-16.32, -476.3) * mm});
            skLineSegment(sketch, "E3109", {"start": v(-16.32, -476.3) * mm, "end": v(-15.18, -475.76) * mm});
            skLineSegment(sketch, "E3110", {"start": v(-15.18, -475.76) * mm, "end": v(-14.12, -475.1) * mm});
            skLineSegment(sketch, "E3111", {"start": v(-14.12, -475.1) * mm, "end": v(-13.15, -474.29) * mm});
            skLineSegment(sketch, "E3112", {"start": v(-13.15, -474.29) * mm, "end": v(-12.3, -473.37) * mm});
            skLineSegment(sketch, "E3113", {"start": v(-12.3, -473.37) * mm, "end": v(-11.56, -472.36) * mm});
            skLineSegment(sketch, "E3114", {"start": v(-11.56, -472.36) * mm, "end": v(-10.95, -471.26) * mm});
            skLineSegment(sketch, "E3115", {"start": v(-10.95, -471.26) * mm, "end": v(-10.49, -470.1) * mm});
            skLineSegment(sketch, "E3116", {"start": v(-10.49, -470.1) * mm, "end": v(-10.18, -468.87) * mm});
            skLineSegment(sketch, "E3117", {"start": v(-10.18, -468.87) * mm, "end": v(-10.02, -467.63) * mm});
            skLineSegment(sketch, "E3118", {"start": v(-10.02, -467.63) * mm, "end": v(-10.02, -467) * mm});
            skLineSegment(sketch, "E3119", {"start": v(-10.02, -467) * mm, "end": v(-10, -467) * mm});
            skLineSegment(sketch, "E3120", {"start": v(-10, -467) * mm, "end": v(-10, -47) * mm});
            skLineSegment(sketch, "E3121", {"start": v(-10, -47) * mm, "end": v(-10.08, -45.75) * mm});
            skLineSegment(sketch, "E3122", {"start": v(-10.08, -45.75) * mm, "end": v(-10.31, -44.51) * mm});
            skLineSegment(sketch, "E3123", {"start": v(-10.31, -44.51) * mm, "end": v(-10.7, -43.32) * mm});
            skLineSegment(sketch, "E3124", {"start": v(-10.7, -43.32) * mm, "end": v(-11.24, -42.18) * mm});
            skLineSegment(sketch, "E3125", {"start": v(-11.24, -42.18) * mm, "end": v(-11.9, -41.12) * mm});
            skLineSegment(sketch, "E3126", {"start": v(-11.9, -41.12) * mm, "end": v(-12.71, -40.16) * mm});
            skLineSegment(sketch, "E3127", {"start": v(-12.71, -40.16) * mm, "end": v(-13.63, -39.3) * mm});
            skLineSegment(sketch, "E3128", {"start": v(-13.63, -39.3) * mm, "end": v(-14.64, -38.56) * mm});
            skLineSegment(sketch, "E3129", {"start": v(-14.64, -38.56) * mm, "end": v(-15.74, -37.95) * mm});
            skLineSegment(sketch, "E3130", {"start": v(-15.74, -37.95) * mm, "end": v(-16.9, -37.49) * mm});
            skLineSegment(sketch, "E3131", {"start": v(-16.9, -37.49) * mm, "end": v(-18.13, -37.18) * mm});
            skLineSegment(sketch, "E3132", {"start": v(-18.13, -37.18) * mm, "end": v(-19.37, -37.02) * mm});
            skLineSegment(sketch, "E3133", {"start": v(-19.37, -37.02) * mm, "end": v(-20, -37.02) * mm});
            skLineSegment(sketch, "E3134", {"start": v(-20, -37.02) * mm, "end": v(-20, -37) * mm});
            skLineSegment(sketch, "E3135", {"start": v(-20, -37) * mm, "end": v(-390, -37) * mm});
            skLineSegment(sketch, "E3136", {"start": v(-390, -37) * mm, "end": v(-391.25, -37.08) * mm});
            skLineSegment(sketch, "E3137", {"start": v(-391.25, -37.08) * mm, "end": v(-392.49, -37.31) * mm});
            skLineSegment(sketch, "E3138", {"start": v(-392.49, -37.31) * mm, "end": v(-393.68, -37.7) * mm});
            skLineSegment(sketch, "E3139", {"start": v(-393.68, -37.7) * mm, "end": v(-394.82, -38.24) * mm});
            skLineSegment(sketch, "E3140", {"start": v(-394.82, -38.24) * mm, "end": v(-395.88, -38.9) * mm});
            skLineSegment(sketch, "E3141", {"start": v(-395.88, -38.9) * mm, "end": v(-396.85, -39.7) * mm});
            skLineSegment(sketch, "E3142", {"start": v(-396.85, -39.7) * mm, "end": v(-397.7, -40.63) * mm});
            skLineSegment(sketch, "E3143", {"start": v(-397.7, -40.63) * mm, "end": v(-398.44, -41.64) * mm});
            skLineSegment(sketch, "E3144", {"start": v(-398.44, -41.64) * mm, "end": v(-399.05, -42.74) * mm});
            skLineSegment(sketch, "E3145", {"start": v(-399.05, -42.74) * mm, "end": v(-399.51, -43.9) * mm});
            skLineSegment(sketch, "E3146", {"start": v(-399.51, -43.9) * mm, "end": v(-399.82, -45.13) * mm});
            skLineSegment(sketch, "E3147", {"start": v(-399.82, -45.13) * mm, "end": v(-399.98, -46.37) * mm});
            skLineSegment(sketch, "E3148", {"start": v(-399.98, -46.37) * mm, "end": v(-399.98, -47) * mm});
            skLineSegment(sketch, "E3149", {"start": v(-399.98, -47) * mm, "end": v(-400, -47) * mm});
            skLineSegment(sketch, "E3150", {"start": v(-400, -47) * mm, "end": v(-400, -467) * mm});
            skLineSegment(sketch, "E3151", {"start": v(-400, -467) * mm, "end": v(-399.92, -468.25) * mm});
            skLineSegment(sketch, "E3152", {"start": v(-399.92, -468.25) * mm, "end": v(-399.69, -469.49) * mm});
            skLineSegment(sketch, "E3153", {"start": v(-399.69, -469.49) * mm, "end": v(-399.3, -470.68) * mm});
            skLineSegment(sketch, "E3154", {"start": v(-399.3, -470.68) * mm, "end": v(-398.76, -471.82) * mm});
            skLineSegment(sketch, "E3155", {"start": v(-398.76, -471.82) * mm, "end": v(-398.09, -472.88) * mm});
            skLineSegment(sketch, "E3156", {"start": v(-398.09, -472.88) * mm, "end": v(-397.3, -473.85) * mm});
            skLineSegment(sketch, "E3157", {"start": v(-397.3, -473.85) * mm, "end": v(-396.37, -474.7) * mm});
            skLineSegment(sketch, "E3158", {"start": v(-396.37, -474.7) * mm, "end": v(-395.36, -475.44) * mm});
            skLineSegment(sketch, "E3159", {"start": v(-395.36, -475.44) * mm, "end": v(-394.26, -476.05) * mm});
            skLineSegment(sketch, "E3160", {"start": v(-394.26, -476.05) * mm, "end": v(-393.09, -476.51) * mm});
            skLineSegment(sketch, "E3161", {"start": v(-393.09, -476.51) * mm, "end": v(-391.87, -476.82) * mm});
            skLineSegment(sketch, "E3162", {"start": v(-391.87, -476.82) * mm, "end": v(-390.63, -476.98) * mm});
            skLineSegment(sketch, "E3163", {"start": v(-390.63, -476.98) * mm, "end": v(-390, -476.98) * mm});
            skLineSegment(sketch, "E3164", {"start": v(-390, -476.98) * mm, "end": v(-390, -477) * mm});
            skLineSegment(sketch, "E3165", {"start": v(-390, -477) * mm, "end": v(-370, -477) * mm});
            skLineSegment(sketch, "E3166", {"start": v(-370, -477) * mm, "end": v(-368.75, -476.92) * mm});
            skLineSegment(sketch, "E3167", {"start": v(-23.1, -50.5) * mm, "end": v(-23.28, -50.47) * mm});
            skLineSegment(sketch, "E3168", {"start": v(-23.28, -50.47) * mm, "end": v(-23.46, -50.43) * mm});
            skLineSegment(sketch, "E3169", {"start": v(-23.46, -50.43) * mm, "end": v(-23.64, -50.36) * mm});
            skLineSegment(sketch, "E3170", {"start": v(-23.64, -50.36) * mm, "end": v(-23.8, -50.27) * mm});
            skLineSegment(sketch, "E3171", {"start": v(-23.8, -50.27) * mm, "end": v(-23.96, -50.16) * mm});
            skLineSegment(sketch, "E3172", {"start": v(-23.96, -50.16) * mm, "end": v(-24.1, -50.03) * mm});
            skLineSegment(sketch, "E3173", {"start": v(-24.1, -50.03) * mm, "end": v(-24.21, -49.88) * mm});
            skLineSegment(sketch, "E3174", {"start": v(-24.21, -49.88) * mm, "end": v(-24.31, -49.72) * mm});
            skLineSegment(sketch, "E3175", {"start": v(-24.31, -49.72) * mm, "end": v(-24.4, -49.55) * mm});
            skLineSegment(sketch, "E3176", {"start": v(-24.4, -49.55) * mm, "end": v(-24.45, -49.37) * mm});
            skLineSegment(sketch, "E3177", {"start": v(-24.45, -49.37) * mm, "end": v(-24.49, -49.19) * mm});
            skLineSegment(sketch, "E3178", {"start": v(-24.49, -49.19) * mm, "end": v(-24.5, -49) * mm});
            skLineSegment(sketch, "E3179", {"start": v(-24.5, -49) * mm, "end": v(-24.49, -48.81) * mm});
            skLineSegment(sketch, "E3180", {"start": v(-24.49, -48.81) * mm, "end": v(-24.45, -48.63) * mm});
            skLineSegment(sketch, "E3181", {"start": v(-24.45, -48.63) * mm, "end": v(-24.4, -48.45) * mm});
            skLineSegment(sketch, "E3182", {"start": v(-24.4, -48.45) * mm, "end": v(-24.31, -48.28) * mm});
            skLineSegment(sketch, "E3183", {"start": v(-24.31, -48.28) * mm, "end": v(-24.21, -48.12) * mm});
            skLineSegment(sketch, "E3184", {"start": v(-24.21, -48.12) * mm, "end": v(-24.1, -47.97) * mm});
            skLineSegment(sketch, "E3185", {"start": v(-24.1, -47.97) * mm, "end": v(-23.96, -47.84) * mm});
            skLineSegment(sketch, "E3186", {"start": v(-23.96, -47.84) * mm, "end": v(-23.8, -47.73) * mm});
            skLineSegment(sketch, "E3187", {"start": v(-23.8, -47.73) * mm, "end": v(-23.64, -47.64) * mm});
            skLineSegment(sketch, "E3188", {"start": v(-23.64, -47.64) * mm, "end": v(-23.46, -47.57) * mm});
            skLineSegment(sketch, "E3189", {"start": v(-23.46, -47.57) * mm, "end": v(-23.28, -47.53) * mm});
            skLineSegment(sketch, "E3190", {"start": v(-23.28, -47.53) * mm, "end": v(-23.1, -47.5) * mm});
            skLineSegment(sketch, "E3191", {"start": v(-23.1, -47.5) * mm, "end": v(-22.9, -47.5) * mm});
            skLineSegment(sketch, "E3192", {"start": v(-22.9, -47.5) * mm, "end": v(-22.72, -47.53) * mm});
            skLineSegment(sketch, "E3193", {"start": v(-22.72, -47.53) * mm, "end": v(-22.54, -47.57) * mm});
            skLineSegment(sketch, "E3194", {"start": v(-22.54, -47.57) * mm, "end": v(-22.36, -47.64) * mm});
            skLineSegment(sketch, "E3195", {"start": v(-22.36, -47.64) * mm, "end": v(-22.2, -47.73) * mm});
            skLineSegment(sketch, "E3196", {"start": v(-22.2, -47.73) * mm, "end": v(-22.04, -47.84) * mm});
            skLineSegment(sketch, "E3197", {"start": v(-22.04, -47.84) * mm, "end": v(-21.9, -47.97) * mm});
            skLineSegment(sketch, "E3198", {"start": v(-21.9, -47.97) * mm, "end": v(-21.79, -48.12) * mm});
            skLineSegment(sketch, "E3199", {"start": v(-21.79, -48.12) * mm, "end": v(-21.69, -48.28) * mm});
            skLineSegment(sketch, "E3200", {"start": v(-21.69, -48.28) * mm, "end": v(-21.6, -48.45) * mm});
            skLineSegment(sketch, "E3201", {"start": v(-21.6, -48.45) * mm, "end": v(-21.55, -48.63) * mm});
            skLineSegment(sketch, "E3202", {"start": v(-21.55, -48.63) * mm, "end": v(-21.51, -48.81) * mm});
            skLineSegment(sketch, "E3203", {"start": v(-21.51, -48.81) * mm, "end": v(-21.5, -49) * mm});
            skLineSegment(sketch, "E3204", {"start": v(-21.5, -49) * mm, "end": v(-21.51, -49.19) * mm});
            skLineSegment(sketch, "E3205", {"start": v(-21.51, -49.19) * mm, "end": v(-21.55, -49.37) * mm});
            skLineSegment(sketch, "E3206", {"start": v(-21.55, -49.37) * mm, "end": v(-21.6, -49.55) * mm});
            skLineSegment(sketch, "E3207", {"start": v(-21.6, -49.55) * mm, "end": v(-21.69, -49.72) * mm});
            skLineSegment(sketch, "E3208", {"start": v(-21.69, -49.72) * mm, "end": v(-21.79, -49.88) * mm});
            skLineSegment(sketch, "E3209", {"start": v(-21.79, -49.88) * mm, "end": v(-21.9, -50.03) * mm});
            skLineSegment(sketch, "E3210", {"start": v(-21.9, -50.03) * mm, "end": v(-22.04, -50.16) * mm});
            skLineSegment(sketch, "E3211", {"start": v(-22.04, -50.16) * mm, "end": v(-22.2, -50.27) * mm});
            skLineSegment(sketch, "E3212", {"start": v(-22.2, -50.27) * mm, "end": v(-22.36, -50.36) * mm});
            skLineSegment(sketch, "E3213", {"start": v(-22.36, -50.36) * mm, "end": v(-22.54, -50.43) * mm});
            skLineSegment(sketch, "E3214", {"start": v(-22.54, -50.43) * mm, "end": v(-22.72, -50.47) * mm});
            skLineSegment(sketch, "E3215", {"start": v(-22.72, -50.47) * mm, "end": v(-22.9, -50.5) * mm});
            skLineSegment(sketch, "E3216", {"start": v(-22.9, -50.5) * mm, "end": v(-23.1, -50.5) * mm});
            skLineSegment(sketch, "E3217", {"start": v(-387.1, -50.5) * mm, "end": v(-387.28, -50.47) * mm});
            skLineSegment(sketch, "E3218", {"start": v(-387.28, -50.47) * mm, "end": v(-387.46, -50.43) * mm});
            skLineSegment(sketch, "E3219", {"start": v(-387.46, -50.43) * mm, "end": v(-387.64, -50.36) * mm});
            skLineSegment(sketch, "E3220", {"start": v(-387.64, -50.36) * mm, "end": v(-387.8, -50.27) * mm});
            skLineSegment(sketch, "E3221", {"start": v(-387.8, -50.27) * mm, "end": v(-387.96, -50.16) * mm});
            skLineSegment(sketch, "E3222", {"start": v(-387.96, -50.16) * mm, "end": v(-388.1, -50.03) * mm});
            skLineSegment(sketch, "E3223", {"start": v(-388.1, -50.03) * mm, "end": v(-388.21, -49.88) * mm});
            skLineSegment(sketch, "E3224", {"start": v(-388.21, -49.88) * mm, "end": v(-388.31, -49.72) * mm});
            skLineSegment(sketch, "E3225", {"start": v(-388.31, -49.72) * mm, "end": v(-388.4, -49.55) * mm});
            skLineSegment(sketch, "E3226", {"start": v(-388.4, -49.55) * mm, "end": v(-388.45, -49.37) * mm});
            skLineSegment(sketch, "E3227", {"start": v(-388.45, -49.37) * mm, "end": v(-388.49, -49.19) * mm});
            skLineSegment(sketch, "E3228", {"start": v(-388.49, -49.19) * mm, "end": v(-388.5, -49) * mm});
            skLineSegment(sketch, "E3229", {"start": v(-388.5, -49) * mm, "end": v(-388.49, -48.81) * mm});
            skLineSegment(sketch, "E3230", {"start": v(-388.49, -48.81) * mm, "end": v(-388.45, -48.63) * mm});
            skLineSegment(sketch, "E3231", {"start": v(-388.45, -48.63) * mm, "end": v(-388.4, -48.45) * mm});
            skLineSegment(sketch, "E3232", {"start": v(-388.4, -48.45) * mm, "end": v(-388.31, -48.28) * mm});
            skLineSegment(sketch, "E3233", {"start": v(-388.31, -48.28) * mm, "end": v(-388.21, -48.12) * mm});
            skLineSegment(sketch, "E3234", {"start": v(-388.21, -48.12) * mm, "end": v(-388.1, -47.97) * mm});
            skLineSegment(sketch, "E3235", {"start": v(-388.1, -47.97) * mm, "end": v(-387.96, -47.84) * mm});
            skLineSegment(sketch, "E3236", {"start": v(-387.96, -47.84) * mm, "end": v(-387.8, -47.73) * mm});
            skLineSegment(sketch, "E3237", {"start": v(-387.8, -47.73) * mm, "end": v(-387.64, -47.64) * mm});
            skLineSegment(sketch, "E3238", {"start": v(-387.64, -47.64) * mm, "end": v(-387.46, -47.57) * mm});
            skLineSegment(sketch, "E3239", {"start": v(-387.46, -47.57) * mm, "end": v(-387.28, -47.53) * mm});
            skLineSegment(sketch, "E3240", {"start": v(-387.28, -47.53) * mm, "end": v(-387.1, -47.5) * mm});
            skLineSegment(sketch, "E3241", {"start": v(-387.1, -47.5) * mm, "end": v(-386.9, -47.5) * mm});
            skLineSegment(sketch, "E3242", {"start": v(-386.9, -47.5) * mm, "end": v(-386.72, -47.53) * mm});
            skLineSegment(sketch, "E3243", {"start": v(-386.72, -47.53) * mm, "end": v(-386.54, -47.57) * mm});
            skLineSegment(sketch, "E3244", {"start": v(-386.54, -47.57) * mm, "end": v(-386.36, -47.64) * mm});
            skLineSegment(sketch, "E3245", {"start": v(-386.36, -47.64) * mm, "end": v(-386.2, -47.73) * mm});
            skLineSegment(sketch, "E3246", {"start": v(-386.2, -47.73) * mm, "end": v(-386.04, -47.84) * mm});
            skLineSegment(sketch, "E3247", {"start": v(-386.04, -47.84) * mm, "end": v(-385.9, -47.97) * mm});
            skLineSegment(sketch, "E3248", {"start": v(-385.9, -47.97) * mm, "end": v(-385.79, -48.12) * mm});
            skLineSegment(sketch, "E3249", {"start": v(-385.79, -48.12) * mm, "end": v(-385.69, -48.28) * mm});
            skLineSegment(sketch, "E3250", {"start": v(-385.69, -48.28) * mm, "end": v(-385.6, -48.45) * mm});
            skLineSegment(sketch, "E3251", {"start": v(-385.6, -48.45) * mm, "end": v(-385.55, -48.63) * mm});
            skLineSegment(sketch, "E3252", {"start": v(-385.55, -48.63) * mm, "end": v(-385.51, -48.81) * mm});
            skLineSegment(sketch, "E3253", {"start": v(-385.51, -48.81) * mm, "end": v(-385.5, -49) * mm});
            skLineSegment(sketch, "E3254", {"start": v(-385.5, -49) * mm, "end": v(-385.51, -49.19) * mm});
            skLineSegment(sketch, "E3255", {"start": v(-385.51, -49.19) * mm, "end": v(-385.55, -49.37) * mm});
            skLineSegment(sketch, "E3256", {"start": v(-385.55, -49.37) * mm, "end": v(-385.6, -49.55) * mm});
            skLineSegment(sketch, "E3257", {"start": v(-385.6, -49.55) * mm, "end": v(-385.69, -49.72) * mm});
            skLineSegment(sketch, "E3258", {"start": v(-385.69, -49.72) * mm, "end": v(-385.79, -49.88) * mm});
            skLineSegment(sketch, "E3259", {"start": v(-385.79, -49.88) * mm, "end": v(-385.9, -50.03) * mm});
            skLineSegment(sketch, "E3260", {"start": v(-385.9, -50.03) * mm, "end": v(-386.04, -50.16) * mm});
            skLineSegment(sketch, "E3261", {"start": v(-386.04, -50.16) * mm, "end": v(-386.2, -50.27) * mm});
            skLineSegment(sketch, "E3262", {"start": v(-386.2, -50.27) * mm, "end": v(-386.36, -50.36) * mm});
            skLineSegment(sketch, "E3263", {"start": v(-386.36, -50.36) * mm, "end": v(-386.54, -50.43) * mm});
            skLineSegment(sketch, "E3264", {"start": v(-386.54, -50.43) * mm, "end": v(-386.72, -50.47) * mm});
            skLineSegment(sketch, "E3265", {"start": v(-386.72, -50.47) * mm, "end": v(-386.9, -50.5) * mm});
            skLineSegment(sketch, "E3266", {"start": v(-386.9, -50.5) * mm, "end": v(-387.1, -50.5) * mm});
            skLineSegment(sketch, "E3267", {"start": v(-367.1, -50.5) * mm, "end": v(-367.28, -50.47) * mm});
            skLineSegment(sketch, "E3268", {"start": v(-367.28, -50.47) * mm, "end": v(-367.46, -50.43) * mm});
            skLineSegment(sketch, "E3269", {"start": v(-367.46, -50.43) * mm, "end": v(-367.64, -50.36) * mm});
            skLineSegment(sketch, "E3270", {"start": v(-367.64, -50.36) * mm, "end": v(-367.8, -50.27) * mm});
            skLineSegment(sketch, "E3271", {"start": v(-367.8, -50.27) * mm, "end": v(-367.96, -50.16) * mm});
            skLineSegment(sketch, "E3272", {"start": v(-367.96, -50.16) * mm, "end": v(-368.1, -50.03) * mm});
            skLineSegment(sketch, "E3273", {"start": v(-368.1, -50.03) * mm, "end": v(-368.21, -49.88) * mm});
            skLineSegment(sketch, "E3274", {"start": v(-368.21, -49.88) * mm, "end": v(-368.31, -49.72) * mm});
            skLineSegment(sketch, "E3275", {"start": v(-368.31, -49.72) * mm, "end": v(-368.4, -49.55) * mm});
            skLineSegment(sketch, "E3276", {"start": v(-368.4, -49.55) * mm, "end": v(-368.45, -49.37) * mm});
            skLineSegment(sketch, "E3277", {"start": v(-368.45, -49.37) * mm, "end": v(-368.49, -49.19) * mm});
            skLineSegment(sketch, "E3278", {"start": v(-368.49, -49.19) * mm, "end": v(-368.5, -49) * mm});
            skLineSegment(sketch, "E3279", {"start": v(-368.5, -49) * mm, "end": v(-368.49, -48.81) * mm});
            skLineSegment(sketch, "E3280", {"start": v(-368.49, -48.81) * mm, "end": v(-368.45, -48.63) * mm});
            skLineSegment(sketch, "E3281", {"start": v(-368.45, -48.63) * mm, "end": v(-368.4, -48.45) * mm});
            skLineSegment(sketch, "E3282", {"start": v(-368.4, -48.45) * mm, "end": v(-368.31, -48.28) * mm});
            skLineSegment(sketch, "E3283", {"start": v(-368.31, -48.28) * mm, "end": v(-368.21, -48.12) * mm});
            skLineSegment(sketch, "E3284", {"start": v(-368.21, -48.12) * mm, "end": v(-368.1, -47.97) * mm});
            skLineSegment(sketch, "E3285", {"start": v(-368.1, -47.97) * mm, "end": v(-367.96, -47.84) * mm});
            skLineSegment(sketch, "E3286", {"start": v(-367.96, -47.84) * mm, "end": v(-367.8, -47.73) * mm});
            skLineSegment(sketch, "E3287", {"start": v(-367.8, -47.73) * mm, "end": v(-367.64, -47.64) * mm});
            skLineSegment(sketch, "E3288", {"start": v(-367.64, -47.64) * mm, "end": v(-367.46, -47.57) * mm});
            skLineSegment(sketch, "E3289", {"start": v(-367.46, -47.57) * mm, "end": v(-367.28, -47.53) * mm});
            skLineSegment(sketch, "E3290", {"start": v(-367.28, -47.53) * mm, "end": v(-367.1, -47.5) * mm});
            skLineSegment(sketch, "E3291", {"start": v(-367.1, -47.5) * mm, "end": v(-366.9, -47.5) * mm});
            skLineSegment(sketch, "E3292", {"start": v(-366.9, -47.5) * mm, "end": v(-366.72, -47.53) * mm});
            skLineSegment(sketch, "E3293", {"start": v(-366.72, -47.53) * mm, "end": v(-366.54, -47.57) * mm});
            skLineSegment(sketch, "E3294", {"start": v(-366.54, -47.57) * mm, "end": v(-366.36, -47.64) * mm});
            skLineSegment(sketch, "E3295", {"start": v(-366.36, -47.64) * mm, "end": v(-366.2, -47.73) * mm});
            skLineSegment(sketch, "E3296", {"start": v(-366.2, -47.73) * mm, "end": v(-366.04, -47.84) * mm});
            skLineSegment(sketch, "E3297", {"start": v(-366.04, -47.84) * mm, "end": v(-365.9, -47.97) * mm});
            skLineSegment(sketch, "E3298", {"start": v(-365.9, -47.97) * mm, "end": v(-365.79, -48.12) * mm});
            skLineSegment(sketch, "E3299", {"start": v(-365.79, -48.12) * mm, "end": v(-365.69, -48.28) * mm});
            skLineSegment(sketch, "E3300", {"start": v(-365.69, -48.28) * mm, "end": v(-365.6, -48.45) * mm});
            skLineSegment(sketch, "E3301", {"start": v(-365.6, -48.45) * mm, "end": v(-365.55, -48.63) * mm});
            skLineSegment(sketch, "E3302", {"start": v(-365.55, -48.63) * mm, "end": v(-365.51, -48.81) * mm});
            skLineSegment(sketch, "E3303", {"start": v(-365.51, -48.81) * mm, "end": v(-365.5, -49) * mm});
            skLineSegment(sketch, "E3304", {"start": v(-365.5, -49) * mm, "end": v(-365.51, -49.19) * mm});
            skLineSegment(sketch, "E3305", {"start": v(-365.51, -49.19) * mm, "end": v(-365.55, -49.37) * mm});
            skLineSegment(sketch, "E3306", {"start": v(-365.55, -49.37) * mm, "end": v(-365.6, -49.55) * mm});
            skLineSegment(sketch, "E3307", {"start": v(-365.6, -49.55) * mm, "end": v(-365.69, -49.72) * mm});
            skLineSegment(sketch, "E3308", {"start": v(-365.69, -49.72) * mm, "end": v(-365.79, -49.88) * mm});
            skLineSegment(sketch, "E3309", {"start": v(-365.79, -49.88) * mm, "end": v(-365.9, -50.03) * mm});
            skLineSegment(sketch, "E3310", {"start": v(-365.9, -50.03) * mm, "end": v(-366.04, -50.16) * mm});
            skLineSegment(sketch, "E3311", {"start": v(-366.04, -50.16) * mm, "end": v(-366.2, -50.27) * mm});
            skLineSegment(sketch, "E3312", {"start": v(-366.2, -50.27) * mm, "end": v(-366.36, -50.36) * mm});
            skLineSegment(sketch, "E3313", {"start": v(-366.36, -50.36) * mm, "end": v(-366.54, -50.43) * mm});
            skLineSegment(sketch, "E3314", {"start": v(-366.54, -50.43) * mm, "end": v(-366.72, -50.47) * mm});
            skLineSegment(sketch, "E3315", {"start": v(-366.72, -50.47) * mm, "end": v(-366.9, -50.5) * mm});
            skLineSegment(sketch, "E3316", {"start": v(-366.9, -50.5) * mm, "end": v(-367.1, -50.5) * mm});
            skLineSegment(sketch, "E3317", {"start": v(-43.1, -50.5) * mm, "end": v(-43.28, -50.47) * mm});
            skLineSegment(sketch, "E3318", {"start": v(-43.28, -50.47) * mm, "end": v(-43.46, -50.43) * mm});
            skLineSegment(sketch, "E3319", {"start": v(-43.46, -50.43) * mm, "end": v(-43.64, -50.36) * mm});
            skLineSegment(sketch, "E3320", {"start": v(-43.64, -50.36) * mm, "end": v(-43.8, -50.27) * mm});
            skLineSegment(sketch, "E3321", {"start": v(-43.8, -50.27) * mm, "end": v(-43.96, -50.16) * mm});
            skLineSegment(sketch, "E3322", {"start": v(-43.96, -50.16) * mm, "end": v(-44.1, -50.03) * mm});
            skLineSegment(sketch, "E3323", {"start": v(-44.1, -50.03) * mm, "end": v(-44.21, -49.88) * mm});
            skLineSegment(sketch, "E3324", {"start": v(-44.21, -49.88) * mm, "end": v(-44.31, -49.72) * mm});
            skLineSegment(sketch, "E3325", {"start": v(-44.31, -49.72) * mm, "end": v(-44.4, -49.55) * mm});
            skLineSegment(sketch, "E3326", {"start": v(-44.4, -49.55) * mm, "end": v(-44.45, -49.37) * mm});
            skLineSegment(sketch, "E3327", {"start": v(-44.45, -49.37) * mm, "end": v(-44.49, -49.19) * mm});
            skLineSegment(sketch, "E3328", {"start": v(-44.49, -49.19) * mm, "end": v(-44.5, -49) * mm});
            skLineSegment(sketch, "E3329", {"start": v(-44.5, -49) * mm, "end": v(-44.49, -48.81) * mm});
            skLineSegment(sketch, "E3330", {"start": v(-44.49, -48.81) * mm, "end": v(-44.45, -48.63) * mm});
            skLineSegment(sketch, "E3331", {"start": v(-44.45, -48.63) * mm, "end": v(-44.4, -48.45) * mm});
            skLineSegment(sketch, "E3332", {"start": v(-44.4, -48.45) * mm, "end": v(-44.31, -48.28) * mm});
            skLineSegment(sketch, "E3333", {"start": v(-44.31, -48.28) * mm, "end": v(-44.21, -48.12) * mm});
            skLineSegment(sketch, "E3334", {"start": v(-44.21, -48.12) * mm, "end": v(-44.1, -47.97) * mm});
            skLineSegment(sketch, "E3335", {"start": v(-44.1, -47.97) * mm, "end": v(-43.96, -47.84) * mm});
            skLineSegment(sketch, "E3336", {"start": v(-43.96, -47.84) * mm, "end": v(-43.8, -47.73) * mm});
            skLineSegment(sketch, "E3337", {"start": v(-43.8, -47.73) * mm, "end": v(-43.64, -47.64) * mm});
            skLineSegment(sketch, "E3338", {"start": v(-43.64, -47.64) * mm, "end": v(-43.46, -47.57) * mm});
            skLineSegment(sketch, "E3339", {"start": v(-43.46, -47.57) * mm, "end": v(-43.28, -47.53) * mm});
            skLineSegment(sketch, "E3340", {"start": v(-43.28, -47.53) * mm, "end": v(-43.1, -47.5) * mm});
            skLineSegment(sketch, "E3341", {"start": v(-43.1, -47.5) * mm, "end": v(-42.9, -47.5) * mm});
            skLineSegment(sketch, "E3342", {"start": v(-42.9, -47.5) * mm, "end": v(-42.72, -47.53) * mm});
            skLineSegment(sketch, "E3343", {"start": v(-42.72, -47.53) * mm, "end": v(-42.54, -47.57) * mm});
            skLineSegment(sketch, "E3344", {"start": v(-42.54, -47.57) * mm, "end": v(-42.36, -47.64) * mm});
            skLineSegment(sketch, "E3345", {"start": v(-42.36, -47.64) * mm, "end": v(-42.2, -47.73) * mm});
            skLineSegment(sketch, "E3346", {"start": v(-42.2, -47.73) * mm, "end": v(-42.04, -47.84) * mm});
            skLineSegment(sketch, "E3347", {"start": v(-42.04, -47.84) * mm, "end": v(-41.9, -47.97) * mm});
            skLineSegment(sketch, "E3348", {"start": v(-41.9, -47.97) * mm, "end": v(-41.79, -48.12) * mm});
            skLineSegment(sketch, "E3349", {"start": v(-41.79, -48.12) * mm, "end": v(-41.69, -48.28) * mm});
            skLineSegment(sketch, "E3350", {"start": v(-41.69, -48.28) * mm, "end": v(-41.6, -48.45) * mm});
            skLineSegment(sketch, "E3351", {"start": v(-41.6, -48.45) * mm, "end": v(-41.55, -48.63) * mm});
            skLineSegment(sketch, "E3352", {"start": v(-41.55, -48.63) * mm, "end": v(-41.51, -48.81) * mm});
            skLineSegment(sketch, "E3353", {"start": v(-41.51, -48.81) * mm, "end": v(-41.5, -49) * mm});
            skLineSegment(sketch, "E3354", {"start": v(-41.5, -49) * mm, "end": v(-41.51, -49.19) * mm});
            skLineSegment(sketch, "E3355", {"start": v(-41.51, -49.19) * mm, "end": v(-41.55, -49.37) * mm});
            skLineSegment(sketch, "E3356", {"start": v(-41.55, -49.37) * mm, "end": v(-41.6, -49.55) * mm});
            skLineSegment(sketch, "E3357", {"start": v(-41.6, -49.55) * mm, "end": v(-41.69, -49.72) * mm});
            skLineSegment(sketch, "E3358", {"start": v(-41.69, -49.72) * mm, "end": v(-41.79, -49.88) * mm});
            skLineSegment(sketch, "E3359", {"start": v(-41.79, -49.88) * mm, "end": v(-41.9, -50.03) * mm});
            skLineSegment(sketch, "E3360", {"start": v(-41.9, -50.03) * mm, "end": v(-42.04, -50.16) * mm});
            skLineSegment(sketch, "E3361", {"start": v(-42.04, -50.16) * mm, "end": v(-42.2, -50.27) * mm});
            skLineSegment(sketch, "E3362", {"start": v(-42.2, -50.27) * mm, "end": v(-42.36, -50.36) * mm});
            skLineSegment(sketch, "E3363", {"start": v(-42.36, -50.36) * mm, "end": v(-42.54, -50.43) * mm});
            skLineSegment(sketch, "E3364", {"start": v(-42.54, -50.43) * mm, "end": v(-42.72, -50.47) * mm});
            skLineSegment(sketch, "E3365", {"start": v(-42.72, -50.47) * mm, "end": v(-42.9, -50.5) * mm});
            skLineSegment(sketch, "E3366", {"start": v(-42.9, -50.5) * mm, "end": v(-43.1, -50.5) * mm});
            skLineSegment(sketch, "E3367", {"start": v(-378, -117) * mm, "end": v(-378, -97) * mm});
            skLineSegment(sketch, "E3368", {"start": v(-378, -97) * mm, "end": v(-362, -97) * mm});
            skLineSegment(sketch, "E3369", {"start": v(-362, -97) * mm, "end": v(-362, -117) * mm});
            skLineSegment(sketch, "E3370", {"start": v(-362, -117) * mm, "end": v(-378, -117) * mm});
            skLineSegment(sketch, "E3371", {"start": v(-48, -117) * mm, "end": v(-48, -97) * mm});
            skLineSegment(sketch, "E3372", {"start": v(-48, -97) * mm, "end": v(-32, -97) * mm});
            skLineSegment(sketch, "E3373", {"start": v(-32, -97) * mm, "end": v(-32, -117) * mm});
            skLineSegment(sketch, "E3374", {"start": v(-32, -117) * mm, "end": v(-48, -117) * mm});
            skLineSegment(sketch, "E3375", {"start": v(-370.13, -179) * mm, "end": v(-370.38, -178.97) * mm});
            skLineSegment(sketch, "E3376", {"start": v(-370.38, -178.97) * mm, "end": v(-370.62, -178.9) * mm});
            skLineSegment(sketch, "E3377", {"start": v(-370.62, -178.9) * mm, "end": v(-370.85, -178.8) * mm});
            skLineSegment(sketch, "E3378", {"start": v(-370.85, -178.8) * mm, "end": v(-371.07, -178.69) * mm});
            skLineSegment(sketch, "E3379", {"start": v(-371.07, -178.69) * mm, "end": v(-371.27, -178.54) * mm});
            skLineSegment(sketch, "E3380", {"start": v(-371.27, -178.54) * mm, "end": v(-371.46, -178.37) * mm});
            skLineSegment(sketch, "E3381", {"start": v(-371.46, -178.37) * mm, "end": v(-371.62, -178.18) * mm});
            skLineSegment(sketch, "E3382", {"start": v(-371.62, -178.18) * mm, "end": v(-371.75, -177.96) * mm});
            skLineSegment(sketch, "E3383", {"start": v(-371.75, -177.96) * mm, "end": v(-371.86, -177.74) * mm});
            skLineSegment(sketch, "E3384", {"start": v(-371.86, -177.74) * mm, "end": v(-371.94, -177.5) * mm});
            skLineSegment(sketch, "E3385", {"start": v(-371.94, -177.5) * mm, "end": v(-371.98, -177.25) * mm});
            skLineSegment(sketch, "E3386", {"start": v(-371.98, -177.25) * mm, "end": v(-372, -177) * mm});
            skLineSegment(sketch, "E3387", {"start": v(-372, -177) * mm, "end": v(-371.98, -176.75) * mm});
            skLineSegment(sketch, "E3388", {"start": v(-371.98, -176.75) * mm, "end": v(-371.94, -176.5) * mm});
            skLineSegment(sketch, "E3389", {"start": v(-371.94, -176.5) * mm, "end": v(-371.86, -176.26) * mm});
            skLineSegment(sketch, "E3390", {"start": v(-371.86, -176.26) * mm, "end": v(-371.75, -176.04) * mm});
            skLineSegment(sketch, "E3391", {"start": v(-371.75, -176.04) * mm, "end": v(-371.62, -175.82) * mm});
            skLineSegment(sketch, "E3392", {"start": v(-371.62, -175.82) * mm, "end": v(-371.46, -175.63) * mm});
            skLineSegment(sketch, "E3393", {"start": v(-371.46, -175.63) * mm, "end": v(-371.27, -175.46) * mm});
            skLineSegment(sketch, "E3394", {"start": v(-371.27, -175.46) * mm, "end": v(-371.07, -175.31) * mm});
            skLineSegment(sketch, "E3395", {"start": v(-371.07, -175.31) * mm, "end": v(-370.85, -175.2) * mm});
            skLineSegment(sketch, "E3396", {"start": v(-370.85, -175.2) * mm, "end": v(-370.62, -175.1) * mm});
            skLineSegment(sketch, "E3397", {"start": v(-370.62, -175.1) * mm, "end": v(-370.38, -175.03) * mm});
            skLineSegment(sketch, "E3398", {"start": v(-370.38, -175.03) * mm, "end": v(-370.13, -175) * mm});
            skLineSegment(sketch, "E3399", {"start": v(-370.13, -175) * mm, "end": v(-369.87, -175) * mm});
            skLineSegment(sketch, "E3400", {"start": v(-369.87, -175) * mm, "end": v(-369.62, -175.03) * mm});
            skLineSegment(sketch, "E3401", {"start": v(-369.62, -175.03) * mm, "end": v(-369.38, -175.1) * mm});
            skLineSegment(sketch, "E3402", {"start": v(-369.38, -175.1) * mm, "end": v(-369.15, -175.2) * mm});
            skLineSegment(sketch, "E3403", {"start": v(-369.15, -175.2) * mm, "end": v(-368.93, -175.31) * mm});
            skLineSegment(sketch, "E3404", {"start": v(-368.93, -175.31) * mm, "end": v(-368.73, -175.46) * mm});
            skLineSegment(sketch, "E3405", {"start": v(-368.73, -175.46) * mm, "end": v(-368.54, -175.63) * mm});
            skLineSegment(sketch, "E3406", {"start": v(-368.54, -175.63) * mm, "end": v(-368.38, -175.82) * mm});
            skLineSegment(sketch, "E3407", {"start": v(-368.38, -175.82) * mm, "end": v(-368.25, -176.04) * mm});
            skLineSegment(sketch, "E3408", {"start": v(-368.25, -176.04) * mm, "end": v(-368.14, -176.26) * mm});
            skLineSegment(sketch, "E3409", {"start": v(-368.14, -176.26) * mm, "end": v(-368.06, -176.5) * mm});
            skLineSegment(sketch, "E3410", {"start": v(-368.06, -176.5) * mm, "end": v(-368.02, -176.75) * mm});
            skLineSegment(sketch, "E3411", {"start": v(-368.02, -176.75) * mm, "end": v(-368, -177) * mm});
            skLineSegment(sketch, "E3412", {"start": v(-368, -177) * mm, "end": v(-368.02, -177.25) * mm});
            skLineSegment(sketch, "E3413", {"start": v(-368.02, -177.25) * mm, "end": v(-368.06, -177.5) * mm});
            skLineSegment(sketch, "E3414", {"start": v(-368.06, -177.5) * mm, "end": v(-368.14, -177.74) * mm});
            skLineSegment(sketch, "E3415", {"start": v(-368.14, -177.74) * mm, "end": v(-368.25, -177.96) * mm});
            skLineSegment(sketch, "E3416", {"start": v(-368.25, -177.96) * mm, "end": v(-368.38, -178.18) * mm});
            skLineSegment(sketch, "E3417", {"start": v(-368.38, -178.18) * mm, "end": v(-368.54, -178.37) * mm});
            skLineSegment(sketch, "E3418", {"start": v(-368.54, -178.37) * mm, "end": v(-368.73, -178.54) * mm});
            skLineSegment(sketch, "E3419", {"start": v(-368.73, -178.54) * mm, "end": v(-368.93, -178.69) * mm});
            skLineSegment(sketch, "E3420", {"start": v(-368.93, -178.69) * mm, "end": v(-369.15, -178.8) * mm});
            skLineSegment(sketch, "E3421", {"start": v(-369.15, -178.8) * mm, "end": v(-369.38, -178.9) * mm});
            skLineSegment(sketch, "E3422", {"start": v(-369.38, -178.9) * mm, "end": v(-369.62, -178.97) * mm});
            skLineSegment(sketch, "E3423", {"start": v(-369.62, -178.97) * mm, "end": v(-369.87, -179) * mm});
            skLineSegment(sketch, "E3424", {"start": v(-369.87, -179) * mm, "end": v(-370.13, -179) * mm});
            skLineSegment(sketch, "E3425", {"start": v(-40.13, -179) * mm, "end": v(-40.37, -178.97) * mm});
            skLineSegment(sketch, "E3426", {"start": v(-40.37, -178.97) * mm, "end": v(-40.62, -178.9) * mm});
            skLineSegment(sketch, "E3427", {"start": v(-40.62, -178.9) * mm, "end": v(-40.85, -178.8) * mm});
            skLineSegment(sketch, "E3428", {"start": v(-40.85, -178.8) * mm, "end": v(-41.07, -178.69) * mm});
            skLineSegment(sketch, "E3429", {"start": v(-41.07, -178.69) * mm, "end": v(-41.27, -178.54) * mm});
            skLineSegment(sketch, "E3430", {"start": v(-41.27, -178.54) * mm, "end": v(-41.46, -178.37) * mm});
            skLineSegment(sketch, "E3431", {"start": v(-41.46, -178.37) * mm, "end": v(-41.62, -178.18) * mm});
            skLineSegment(sketch, "E3432", {"start": v(-41.62, -178.18) * mm, "end": v(-41.75, -177.96) * mm});
            skLineSegment(sketch, "E3433", {"start": v(-41.75, -177.96) * mm, "end": v(-41.86, -177.74) * mm});
            skLineSegment(sketch, "E3434", {"start": v(-41.86, -177.74) * mm, "end": v(-41.94, -177.5) * mm});
            skLineSegment(sketch, "E3435", {"start": v(-41.94, -177.5) * mm, "end": v(-41.98, -177.25) * mm});
            skLineSegment(sketch, "E3436", {"start": v(-41.98, -177.25) * mm, "end": v(-42, -177) * mm});
            skLineSegment(sketch, "E3437", {"start": v(-42, -177) * mm, "end": v(-41.98, -176.75) * mm});
            skLineSegment(sketch, "E3438", {"start": v(-41.98, -176.75) * mm, "end": v(-41.94, -176.5) * mm});
            skLineSegment(sketch, "E3439", {"start": v(-41.94, -176.5) * mm, "end": v(-41.86, -176.26) * mm});
            skLineSegment(sketch, "E3440", {"start": v(-41.86, -176.26) * mm, "end": v(-41.75, -176.04) * mm});
            skLineSegment(sketch, "E3441", {"start": v(-41.75, -176.04) * mm, "end": v(-41.62, -175.82) * mm});
            skLineSegment(sketch, "E3442", {"start": v(-41.62, -175.82) * mm, "end": v(-41.46, -175.63) * mm});
            skLineSegment(sketch, "E3443", {"start": v(-41.46, -175.63) * mm, "end": v(-41.27, -175.46) * mm});
            skLineSegment(sketch, "E3444", {"start": v(-41.27, -175.46) * mm, "end": v(-41.07, -175.31) * mm});
            skLineSegment(sketch, "E3445", {"start": v(-41.07, -175.31) * mm, "end": v(-40.85, -175.2) * mm});
            skLineSegment(sketch, "E3446", {"start": v(-40.85, -175.2) * mm, "end": v(-40.62, -175.1) * mm});
            skLineSegment(sketch, "E3447", {"start": v(-40.62, -175.1) * mm, "end": v(-40.37, -175.03) * mm});
            skLineSegment(sketch, "E3448", {"start": v(-40.37, -175.03) * mm, "end": v(-40.13, -175) * mm});
            skLineSegment(sketch, "E3449", {"start": v(-40.13, -175) * mm, "end": v(-39.87, -175) * mm});
            skLineSegment(sketch, "E3450", {"start": v(-39.87, -175) * mm, "end": v(-39.63, -175.03) * mm});
            skLineSegment(sketch, "E3451", {"start": v(-39.63, -175.03) * mm, "end": v(-39.38, -175.1) * mm});
            skLineSegment(sketch, "E3452", {"start": v(-39.38, -175.1) * mm, "end": v(-39.15, -175.2) * mm});
            skLineSegment(sketch, "E3453", {"start": v(-39.15, -175.2) * mm, "end": v(-38.93, -175.31) * mm});
            skLineSegment(sketch, "E3454", {"start": v(-38.93, -175.31) * mm, "end": v(-38.73, -175.46) * mm});
            skLineSegment(sketch, "E3455", {"start": v(-38.73, -175.46) * mm, "end": v(-38.54, -175.63) * mm});
            skLineSegment(sketch, "E3456", {"start": v(-38.54, -175.63) * mm, "end": v(-38.38, -175.82) * mm});
            skLineSegment(sketch, "E3457", {"start": v(-38.38, -175.82) * mm, "end": v(-38.25, -176.04) * mm});
            skLineSegment(sketch, "E3458", {"start": v(-38.25, -176.04) * mm, "end": v(-38.14, -176.26) * mm});
            skLineSegment(sketch, "E3459", {"start": v(-38.14, -176.26) * mm, "end": v(-38.06, -176.5) * mm});
            skLineSegment(sketch, "E3460", {"start": v(-38.06, -176.5) * mm, "end": v(-38.02, -176.75) * mm});
            skLineSegment(sketch, "E3461", {"start": v(-38.02, -176.75) * mm, "end": v(-38, -177) * mm});
            skLineSegment(sketch, "E3462", {"start": v(-38, -177) * mm, "end": v(-38.02, -177.25) * mm});
            skLineSegment(sketch, "E3463", {"start": v(-38.02, -177.25) * mm, "end": v(-38.06, -177.5) * mm});
            skLineSegment(sketch, "E3464", {"start": v(-38.06, -177.5) * mm, "end": v(-38.14, -177.74) * mm});
            skLineSegment(sketch, "E3465", {"start": v(-38.14, -177.74) * mm, "end": v(-38.25, -177.96) * mm});
            skLineSegment(sketch, "E3466", {"start": v(-38.25, -177.96) * mm, "end": v(-38.38, -178.18) * mm});
            skLineSegment(sketch, "E3467", {"start": v(-38.38, -178.18) * mm, "end": v(-38.54, -178.37) * mm});
            skLineSegment(sketch, "E3468", {"start": v(-38.54, -178.37) * mm, "end": v(-38.73, -178.54) * mm});
            skLineSegment(sketch, "E3469", {"start": v(-38.73, -178.54) * mm, "end": v(-38.93, -178.69) * mm});
            skLineSegment(sketch, "E3470", {"start": v(-38.93, -178.69) * mm, "end": v(-39.15, -178.8) * mm});
            skLineSegment(sketch, "E3471", {"start": v(-39.15, -178.8) * mm, "end": v(-39.38, -178.9) * mm});
            skLineSegment(sketch, "E3472", {"start": v(-39.38, -178.9) * mm, "end": v(-39.63, -178.97) * mm});
            skLineSegment(sketch, "E3473", {"start": v(-39.63, -178.97) * mm, "end": v(-39.87, -179) * mm});
            skLineSegment(sketch, "E3474", {"start": v(-39.87, -179) * mm, "end": v(-40.13, -179) * mm});
            skLineSegment(sketch, "E3475", {"start": v(-48, -257) * mm, "end": v(-48, -237) * mm});
            skLineSegment(sketch, "E3476", {"start": v(-48, -237) * mm, "end": v(-32, -237) * mm});
            skLineSegment(sketch, "E3477", {"start": v(-32, -237) * mm, "end": v(-32, -257) * mm});
            skLineSegment(sketch, "E3478", {"start": v(-32, -257) * mm, "end": v(-48, -257) * mm});
            skLineSegment(sketch, "E3479", {"start": v(-378, -257) * mm, "end": v(-378, -237) * mm});
            skLineSegment(sketch, "E3480", {"start": v(-378, -237) * mm, "end": v(-362, -237) * mm});
            skLineSegment(sketch, "E3481", {"start": v(-362, -237) * mm, "end": v(-362, -257) * mm});
            skLineSegment(sketch, "E3482", {"start": v(-362, -257) * mm, "end": v(-378, -257) * mm});
            skLineSegment(sketch, "E3483", {"start": v(-40.13, -319) * mm, "end": v(-40.37, -318.96) * mm});
            skLineSegment(sketch, "E3484", {"start": v(-40.37, -318.96) * mm, "end": v(-40.62, -318.9) * mm});
            skLineSegment(sketch, "E3485", {"start": v(-40.62, -318.9) * mm, "end": v(-40.85, -318.8) * mm});
            skLineSegment(sketch, "E3486", {"start": v(-40.85, -318.8) * mm, "end": v(-41.07, -318.69) * mm});
            skLineSegment(sketch, "E3487", {"start": v(-41.07, -318.69) * mm, "end": v(-41.27, -318.54) * mm});
            skLineSegment(sketch, "E3488", {"start": v(-41.27, -318.54) * mm, "end": v(-41.46, -318.37) * mm});
            skLineSegment(sketch, "E3489", {"start": v(-41.46, -318.37) * mm, "end": v(-41.62, -318.18) * mm});
            skLineSegment(sketch, "E3490", {"start": v(-41.62, -318.18) * mm, "end": v(-41.75, -317.96) * mm});
            skLineSegment(sketch, "E3491", {"start": v(-41.75, -317.96) * mm, "end": v(-41.86, -317.74) * mm});
            skLineSegment(sketch, "E3492", {"start": v(-41.86, -317.74) * mm, "end": v(-41.94, -317.5) * mm});
            skLineSegment(sketch, "E3493", {"start": v(-41.94, -317.5) * mm, "end": v(-41.98, -317.25) * mm});
            skLineSegment(sketch, "E3494", {"start": v(-41.98, -317.25) * mm, "end": v(-42, -317) * mm});
            skLineSegment(sketch, "E3495", {"start": v(-42, -317) * mm, "end": v(-41.98, -316.75) * mm});
            skLineSegment(sketch, "E3496", {"start": v(-41.98, -316.75) * mm, "end": v(-41.94, -316.5) * mm});
            skLineSegment(sketch, "E3497", {"start": v(-41.94, -316.5) * mm, "end": v(-41.86, -316.26) * mm});
            skLineSegment(sketch, "E3498", {"start": v(-41.86, -316.26) * mm, "end": v(-41.75, -316.04) * mm});
            skLineSegment(sketch, "E3499", {"start": v(-41.75, -316.04) * mm, "end": v(-41.62, -315.82) * mm});
            skLineSegment(sketch, "E3500", {"start": v(-41.62, -315.82) * mm, "end": v(-41.46, -315.63) * mm});
            skLineSegment(sketch, "E3501", {"start": v(-41.46, -315.63) * mm, "end": v(-41.27, -315.46) * mm});
            skLineSegment(sketch, "E3502", {"start": v(-41.27, -315.46) * mm, "end": v(-41.07, -315.31) * mm});
            skLineSegment(sketch, "E3503", {"start": v(-41.07, -315.31) * mm, "end": v(-40.85, -315.2) * mm});
            skLineSegment(sketch, "E3504", {"start": v(-40.85, -315.2) * mm, "end": v(-40.62, -315.1) * mm});
            skLineSegment(sketch, "E3505", {"start": v(-40.62, -315.1) * mm, "end": v(-40.37, -315.04) * mm});
            skLineSegment(sketch, "E3506", {"start": v(-40.37, -315.04) * mm, "end": v(-40.13, -315) * mm});
            skLineSegment(sketch, "E3507", {"start": v(-40.13, -315) * mm, "end": v(-39.87, -315) * mm});
            skLineSegment(sketch, "E3508", {"start": v(-39.87, -315) * mm, "end": v(-39.63, -315.04) * mm});
            skLineSegment(sketch, "E3509", {"start": v(-39.63, -315.04) * mm, "end": v(-39.38, -315.1) * mm});
            skLineSegment(sketch, "E3510", {"start": v(-39.38, -315.1) * mm, "end": v(-39.15, -315.2) * mm});
            skLineSegment(sketch, "E3511", {"start": v(-39.15, -315.2) * mm, "end": v(-38.93, -315.31) * mm});
            skLineSegment(sketch, "E3512", {"start": v(-38.93, -315.31) * mm, "end": v(-38.73, -315.46) * mm});
            skLineSegment(sketch, "E3513", {"start": v(-38.73, -315.46) * mm, "end": v(-38.54, -315.63) * mm});
            skLineSegment(sketch, "E3514", {"start": v(-38.54, -315.63) * mm, "end": v(-38.38, -315.82) * mm});
            skLineSegment(sketch, "E3515", {"start": v(-38.38, -315.82) * mm, "end": v(-38.25, -316.04) * mm});
            skLineSegment(sketch, "E3516", {"start": v(-38.25, -316.04) * mm, "end": v(-38.14, -316.26) * mm});
            skLineSegment(sketch, "E3517", {"start": v(-38.14, -316.26) * mm, "end": v(-38.06, -316.5) * mm});
            skLineSegment(sketch, "E3518", {"start": v(-38.06, -316.5) * mm, "end": v(-38.02, -316.75) * mm});
            skLineSegment(sketch, "E3519", {"start": v(-38.02, -316.75) * mm, "end": v(-38, -317) * mm});
            skLineSegment(sketch, "E3520", {"start": v(-38, -317) * mm, "end": v(-38.02, -317.25) * mm});
            skLineSegment(sketch, "E3521", {"start": v(-38.02, -317.25) * mm, "end": v(-38.06, -317.5) * mm});
            skLineSegment(sketch, "E3522", {"start": v(-38.06, -317.5) * mm, "end": v(-38.14, -317.74) * mm});
            skLineSegment(sketch, "E3523", {"start": v(-38.14, -317.74) * mm, "end": v(-38.25, -317.96) * mm});
            skLineSegment(sketch, "E3524", {"start": v(-38.25, -317.96) * mm, "end": v(-38.38, -318.18) * mm});
            skLineSegment(sketch, "E3525", {"start": v(-38.38, -318.18) * mm, "end": v(-38.54, -318.37) * mm});
            skLineSegment(sketch, "E3526", {"start": v(-38.54, -318.37) * mm, "end": v(-38.73, -318.54) * mm});
            skLineSegment(sketch, "E3527", {"start": v(-38.73, -318.54) * mm, "end": v(-38.93, -318.69) * mm});
            skLineSegment(sketch, "E3528", {"start": v(-38.93, -318.69) * mm, "end": v(-39.15, -318.8) * mm});
            skLineSegment(sketch, "E3529", {"start": v(-39.15, -318.8) * mm, "end": v(-39.38, -318.9) * mm});
            skLineSegment(sketch, "E3530", {"start": v(-39.38, -318.9) * mm, "end": v(-39.63, -318.96) * mm});
            skLineSegment(sketch, "E3531", {"start": v(-39.63, -318.96) * mm, "end": v(-39.87, -319) * mm});
            skLineSegment(sketch, "E3532", {"start": v(-39.87, -319) * mm, "end": v(-40.13, -319) * mm});
            skLineSegment(sketch, "E3533", {"start": v(-370.13, -319) * mm, "end": v(-370.38, -318.96) * mm});
            skLineSegment(sketch, "E3534", {"start": v(-370.38, -318.96) * mm, "end": v(-370.62, -318.9) * mm});
            skLineSegment(sketch, "E3535", {"start": v(-370.62, -318.9) * mm, "end": v(-370.85, -318.8) * mm});
            skLineSegment(sketch, "E3536", {"start": v(-370.85, -318.8) * mm, "end": v(-371.07, -318.69) * mm});
            skLineSegment(sketch, "E3537", {"start": v(-371.07, -318.69) * mm, "end": v(-371.27, -318.54) * mm});
            skLineSegment(sketch, "E3538", {"start": v(-371.27, -318.54) * mm, "end": v(-371.46, -318.37) * mm});
            skLineSegment(sketch, "E3539", {"start": v(-371.46, -318.37) * mm, "end": v(-371.62, -318.18) * mm});
            skLineSegment(sketch, "E3540", {"start": v(-371.62, -318.18) * mm, "end": v(-371.75, -317.96) * mm});
            skLineSegment(sketch, "E3541", {"start": v(-371.75, -317.96) * mm, "end": v(-371.86, -317.74) * mm});
            skLineSegment(sketch, "E3542", {"start": v(-371.86, -317.74) * mm, "end": v(-371.94, -317.5) * mm});
            skLineSegment(sketch, "E3543", {"start": v(-371.94, -317.5) * mm, "end": v(-371.98, -317.25) * mm});
            skLineSegment(sketch, "E3544", {"start": v(-371.98, -317.25) * mm, "end": v(-372, -317) * mm});
            skLineSegment(sketch, "E3545", {"start": v(-372, -317) * mm, "end": v(-371.98, -316.75) * mm});
            skLineSegment(sketch, "E3546", {"start": v(-371.98, -316.75) * mm, "end": v(-371.94, -316.5) * mm});
            skLineSegment(sketch, "E3547", {"start": v(-371.94, -316.5) * mm, "end": v(-371.86, -316.26) * mm});
            skLineSegment(sketch, "E3548", {"start": v(-371.86, -316.26) * mm, "end": v(-371.75, -316.04) * mm});
            skLineSegment(sketch, "E3549", {"start": v(-371.75, -316.04) * mm, "end": v(-371.62, -315.82) * mm});
            skLineSegment(sketch, "E3550", {"start": v(-371.62, -315.82) * mm, "end": v(-371.46, -315.63) * mm});
            skLineSegment(sketch, "E3551", {"start": v(-371.46, -315.63) * mm, "end": v(-371.27, -315.46) * mm});
            skLineSegment(sketch, "E3552", {"start": v(-371.27, -315.46) * mm, "end": v(-371.07, -315.31) * mm});
            skLineSegment(sketch, "E3553", {"start": v(-371.07, -315.31) * mm, "end": v(-370.85, -315.2) * mm});
            skLineSegment(sketch, "E3554", {"start": v(-370.85, -315.2) * mm, "end": v(-370.62, -315.1) * mm});
            skLineSegment(sketch, "E3555", {"start": v(-370.62, -315.1) * mm, "end": v(-370.38, -315.04) * mm});
            skLineSegment(sketch, "E3556", {"start": v(-370.38, -315.04) * mm, "end": v(-370.13, -315) * mm});
            skLineSegment(sketch, "E3557", {"start": v(-370.13, -315) * mm, "end": v(-369.87, -315) * mm});
            skLineSegment(sketch, "E3558", {"start": v(-369.87, -315) * mm, "end": v(-369.62, -315.04) * mm});
            skLineSegment(sketch, "E3559", {"start": v(-369.62, -315.04) * mm, "end": v(-369.38, -315.1) * mm});
            skLineSegment(sketch, "E3560", {"start": v(-369.38, -315.1) * mm, "end": v(-369.15, -315.2) * mm});
            skLineSegment(sketch, "E3561", {"start": v(-369.15, -315.2) * mm, "end": v(-368.93, -315.31) * mm});
            skLineSegment(sketch, "E3562", {"start": v(-368.93, -315.31) * mm, "end": v(-368.73, -315.46) * mm});
            skLineSegment(sketch, "E3563", {"start": v(-368.73, -315.46) * mm, "end": v(-368.54, -315.63) * mm});
            skLineSegment(sketch, "E3564", {"start": v(-368.54, -315.63) * mm, "end": v(-368.38, -315.82) * mm});
            skLineSegment(sketch, "E3565", {"start": v(-368.38, -315.82) * mm, "end": v(-368.25, -316.04) * mm});
            skLineSegment(sketch, "E3566", {"start": v(-368.25, -316.04) * mm, "end": v(-368.14, -316.26) * mm});
            skLineSegment(sketch, "E3567", {"start": v(-368.14, -316.26) * mm, "end": v(-368.06, -316.5) * mm});
            skLineSegment(sketch, "E3568", {"start": v(-368.06, -316.5) * mm, "end": v(-368.02, -316.75) * mm});
            skLineSegment(sketch, "E3569", {"start": v(-368.02, -316.75) * mm, "end": v(-368, -317) * mm});
            skLineSegment(sketch, "E3570", {"start": v(-368, -317) * mm, "end": v(-368.02, -317.25) * mm});
            skLineSegment(sketch, "E3571", {"start": v(-368.02, -317.25) * mm, "end": v(-368.06, -317.5) * mm});
            skLineSegment(sketch, "E3572", {"start": v(-368.06, -317.5) * mm, "end": v(-368.14, -317.74) * mm});
            skLineSegment(sketch, "E3573", {"start": v(-368.14, -317.74) * mm, "end": v(-368.25, -317.96) * mm});
            skLineSegment(sketch, "E3574", {"start": v(-368.25, -317.96) * mm, "end": v(-368.38, -318.18) * mm});
            skLineSegment(sketch, "E3575", {"start": v(-368.38, -318.18) * mm, "end": v(-368.54, -318.37) * mm});
            skLineSegment(sketch, "E3576", {"start": v(-368.54, -318.37) * mm, "end": v(-368.73, -318.54) * mm});
            skLineSegment(sketch, "E3577", {"start": v(-368.73, -318.54) * mm, "end": v(-368.93, -318.69) * mm});
            skLineSegment(sketch, "E3578", {"start": v(-368.93, -318.69) * mm, "end": v(-369.15, -318.8) * mm});
            skLineSegment(sketch, "E3579", {"start": v(-369.15, -318.8) * mm, "end": v(-369.38, -318.9) * mm});
            skLineSegment(sketch, "E3580", {"start": v(-369.38, -318.9) * mm, "end": v(-369.62, -318.96) * mm});
            skLineSegment(sketch, "E3581", {"start": v(-369.62, -318.96) * mm, "end": v(-369.87, -319) * mm});
            skLineSegment(sketch, "E3582", {"start": v(-369.87, -319) * mm, "end": v(-370.13, -319) * mm});
            skLineSegment(sketch, "E3583", {"start": v(-48, -397) * mm, "end": v(-48, -377) * mm});
            skLineSegment(sketch, "E3584", {"start": v(-48, -377) * mm, "end": v(-32, -377) * mm});
            skLineSegment(sketch, "E3585", {"start": v(-32, -377) * mm, "end": v(-32, -397) * mm});
            skLineSegment(sketch, "E3586", {"start": v(-32, -397) * mm, "end": v(-48, -397) * mm});
            skLineSegment(sketch, "E3587", {"start": v(-378, -397) * mm, "end": v(-378, -377) * mm});
            skLineSegment(sketch, "E3588", {"start": v(-378, -377) * mm, "end": v(-362, -377) * mm});
            skLineSegment(sketch, "E3589", {"start": v(-362, -377) * mm, "end": v(-362, -397) * mm});
            skLineSegment(sketch, "E3590", {"start": v(-362, -397) * mm, "end": v(-378, -397) * mm});
            skLineSegment(sketch, "E3591", {"start": v(-85, -442) * mm, "end": v(-101, -442) * mm});
            skLineSegment(sketch, "E3592", {"start": v(-101, -442) * mm, "end": v(-101, -322) * mm});
            skLineSegment(sketch, "E3593", {"start": v(-101, -322) * mm, "end": v(-85, -322) * mm});
            skLineSegment(sketch, "E3594", {"start": v(-85, -322) * mm, "end": v(-85, -302) * mm});
            skLineSegment(sketch, "E3595", {"start": v(-85, -302) * mm, "end": v(-101, -302) * mm});
            skLineSegment(sketch, "E3596", {"start": v(-101, -302) * mm, "end": v(-101, -182) * mm});
            skLineSegment(sketch, "E3597", {"start": v(-101, -182) * mm, "end": v(-85, -182) * mm});
            skLineSegment(sketch, "E3598", {"start": v(-85, -182) * mm, "end": v(-85, -162) * mm});
            skLineSegment(sketch, "E3599", {"start": v(-85, -162) * mm, "end": v(-101, -162) * mm});
            skLineSegment(sketch, "E3600", {"start": v(-101, -162) * mm, "end": v(-101, -142) * mm});
            skLineSegment(sketch, "E3601", {"start": v(-101, -142) * mm, "end": v(-156, -142) * mm});
            skLineSegment(sketch, "E3602", {"start": v(-156, -142) * mm, "end": v(-156, -126) * mm});
            skLineSegment(sketch, "E3603", {"start": v(-156, -126) * mm, "end": v(-176, -126) * mm});
            skLineSegment(sketch, "E3604", {"start": v(-176, -126) * mm, "end": v(-176, -142) * mm});
            skLineSegment(sketch, "E3605", {"start": v(-176, -142) * mm, "end": v(-239, -142) * mm});
            skLineSegment(sketch, "E3606", {"start": v(-239, -142) * mm, "end": v(-187.01, -302) * mm});
            skLineSegment(sketch, "E3607", {"start": v(-187.01, -302) * mm, "end": v(-187, -302) * mm});
            skLineSegment(sketch, "E3608", {"start": v(-187, -302) * mm, "end": v(-137.06, -455.68) * mm});
            skLineSegment(sketch, "E3609", {"start": v(-137.06, -455.68) * mm, "end": v(-136.52, -456.82) * mm});
            skLineSegment(sketch, "E3610", {"start": v(-136.52, -456.82) * mm, "end": v(-135.85, -457.88) * mm});
            skLineSegment(sketch, "E3611", {"start": v(-135.85, -457.88) * mm, "end": v(-135.05, -458.85) * mm});
            skLineSegment(sketch, "E3612", {"start": v(-135.05, -458.85) * mm, "end": v(-134.13, -459.7) * mm});
            skLineSegment(sketch, "E3613", {"start": v(-134.13, -459.7) * mm, "end": v(-133.12, -460.44) * mm});
            skLineSegment(sketch, "E3614", {"start": v(-133.12, -460.44) * mm, "end": v(-132.02, -461.05) * mm});
            skLineSegment(sketch, "E3615", {"start": v(-132.02, -461.05) * mm, "end": v(-130.85, -461.51) * mm});
            skLineSegment(sketch, "E3616", {"start": v(-130.85, -461.51) * mm, "end": v(-129.63, -461.82) * mm});
            skLineSegment(sketch, "E3617", {"start": v(-129.63, -461.82) * mm, "end": v(-128.39, -461.98) * mm});
            skLineSegment(sketch, "E3618", {"start": v(-128.39, -461.98) * mm, "end": v(-111, -461.98) * mm});
            skLineSegment(sketch, "E3619", {"start": v(-111, -461.98) * mm, "end": v(-111, -462) * mm});
            skLineSegment(sketch, "E3620", {"start": v(-111, -462) * mm, "end": v(-85, -462) * mm});
            skLineSegment(sketch, "E3621", {"start": v(-85, -462) * mm, "end": v(-85, -442) * mm});
            skLineSegment(sketch, "E3622", {"start": v(-234, -446) * mm, "end": v(-171, -446) * mm});
            skLineSegment(sketch, "E3623", {"start": v(-171, -446) * mm, "end": v(-222.99, -286) * mm});
            skLineSegment(sketch, "E3624", {"start": v(-222.99, -286) * mm, "end": v(-223, -286) * mm});
            skLineSegment(sketch, "E3625", {"start": v(-223, -286) * mm, "end": v(-272.94, -132.32) * mm});
            skLineSegment(sketch, "E3626", {"start": v(-272.94, -132.32) * mm, "end": v(-273.48, -131.18) * mm});
            skLineSegment(sketch, "E3627", {"start": v(-273.48, -131.18) * mm, "end": v(-274.15, -130.12) * mm});
            skLineSegment(sketch, "E3628", {"start": v(-274.15, -130.12) * mm, "end": v(-274.95, -129.16) * mm});
            skLineSegment(sketch, "E3629", {"start": v(-274.95, -129.16) * mm, "end": v(-275.87, -128.3) * mm});
            skLineSegment(sketch, "E3630", {"start": v(-275.87, -128.3) * mm, "end": v(-276.88, -127.56) * mm});
            skLineSegment(sketch, "E3631", {"start": v(-276.88, -127.56) * mm, "end": v(-277.98, -126.95) * mm});
            skLineSegment(sketch, "E3632", {"start": v(-277.98, -126.95) * mm, "end": v(-279.15, -126.49) * mm});
            skLineSegment(sketch, "E3633", {"start": v(-279.15, -126.49) * mm, "end": v(-280.37, -126.18) * mm});
            skLineSegment(sketch, "E3634", {"start": v(-280.37, -126.18) * mm, "end": v(-281.61, -126.02) * mm});
            skLineSegment(sketch, "E3635", {"start": v(-281.61, -126.02) * mm, "end": v(-299, -126.02) * mm});
            skLineSegment(sketch, "E3636", {"start": v(-299, -126.02) * mm, "end": v(-299, -126) * mm});
            skLineSegment(sketch, "E3637", {"start": v(-299, -126) * mm, "end": v(-325, -126) * mm});
            skLineSegment(sketch, "E3638", {"start": v(-325, -126) * mm, "end": v(-325, -146) * mm});
            skLineSegment(sketch, "E3639", {"start": v(-325, -146) * mm, "end": v(-309, -146) * mm});
            skLineSegment(sketch, "E3640", {"start": v(-309, -146) * mm, "end": v(-309, -266) * mm});
            skLineSegment(sketch, "E3641", {"start": v(-309, -266) * mm, "end": v(-325, -266) * mm});
            skLineSegment(sketch, "E3642", {"start": v(-325, -266) * mm, "end": v(-325, -286) * mm});
            skLineSegment(sketch, "E3643", {"start": v(-325, -286) * mm, "end": v(-309, -286) * mm});
            skLineSegment(sketch, "E3644", {"start": v(-309, -286) * mm, "end": v(-309, -406) * mm});
            skLineSegment(sketch, "E3645", {"start": v(-309, -406) * mm, "end": v(-325, -406) * mm});
            skLineSegment(sketch, "E3646", {"start": v(-325, -406) * mm, "end": v(-325, -426) * mm});
            skLineSegment(sketch, "E3647", {"start": v(-325, -426) * mm, "end": v(-309, -426) * mm});
            skLineSegment(sketch, "E3648", {"start": v(-309, -426) * mm, "end": v(-309, -446) * mm});
            skLineSegment(sketch, "E3649", {"start": v(-309, -446) * mm, "end": v(-254, -446) * mm});
            skLineSegment(sketch, "E3650", {"start": v(-254, -446) * mm, "end": v(-254, -462) * mm});
            skLineSegment(sketch, "E3651", {"start": v(-254, -462) * mm, "end": v(-234, -462) * mm});
            skLineSegment(sketch, "E3652", {"start": v(-234, -462) * mm, "end": v(-234, -446) * mm});
            skLineSegment(sketch, "E3653", {"start": v(-370, -562.98) * mm, "end": v(-369.37, -562.98) * mm});
            skLineSegment(sketch, "E3654", {"start": v(-369.37, -562.98) * mm, "end": v(-368.13, -562.82) * mm});
            skLineSegment(sketch, "E3655", {"start": v(-368.13, -562.82) * mm, "end": v(-366.91, -562.51) * mm});
            skLineSegment(sketch, "E3656", {"start": v(-366.91, -562.51) * mm, "end": v(-365.74, -562.05) * mm});
            skLineSegment(sketch, "E3657", {"start": v(-365.74, -562.05) * mm, "end": v(-364.64, -561.44) * mm});
            skLineSegment(sketch, "E3658", {"start": v(-364.64, -561.44) * mm, "end": v(-363.63, -560.7) * mm});
            skLineSegment(sketch, "E3659", {"start": v(-363.63, -560.7) * mm, "end": v(-362.7, -559.85) * mm});
            skLineSegment(sketch, "E3660", {"start": v(-362.7, -559.85) * mm, "end": v(-361.91, -558.88) * mm});
            skLineSegment(sketch, "E3661", {"start": v(-361.91, -558.88) * mm, "end": v(-361.24, -557.82) * mm});
            skLineSegment(sketch, "E3662", {"start": v(-361.24, -557.82) * mm, "end": v(-360.7, -556.68) * mm});
            skLineSegment(sketch, "E3663", {"start": v(-360.7, -556.68) * mm, "end": v(-360.31, -555.49) * mm});
            skLineSegment(sketch, "E3664", {"start": v(-360.31, -555.49) * mm, "end": v(-360.08, -554.25) * mm});
            skLineSegment(sketch, "E3665", {"start": v(-360.08, -554.25) * mm, "end": v(-360, -553) * mm});
            skLineSegment(sketch, "E3666", {"start": v(-360, -553) * mm, "end": v(-359.98, -553) * mm});
            skLineSegment(sketch, "E3667", {"start": v(-359.98, -553) * mm, "end": v(-359.98, -552.37) * mm});
            skLineSegment(sketch, "E3668", {"start": v(-359.98, -552.37) * mm, "end": v(-359.82, -551.13) * mm});
            skLineSegment(sketch, "E3669", {"start": v(-359.82, -551.13) * mm, "end": v(-359.51, -549.9) * mm});
            skLineSegment(sketch, "E3670", {"start": v(-359.51, -549.9) * mm, "end": v(-359.05, -548.74) * mm});
            skLineSegment(sketch, "E3671", {"start": v(-359.05, -548.74) * mm, "end": v(-358.44, -547.64) * mm});
            skLineSegment(sketch, "E3672", {"start": v(-358.44, -547.64) * mm, "end": v(-357.7, -546.63) * mm});
            skLineSegment(sketch, "E3673", {"start": v(-357.7, -546.63) * mm, "end": v(-356.85, -545.71) * mm});
            skLineSegment(sketch, "E3674", {"start": v(-356.85, -545.71) * mm, "end": v(-355.88, -544.9) * mm});
            skLineSegment(sketch, "E3675", {"start": v(-355.88, -544.9) * mm, "end": v(-354.82, -544.24) * mm});
            skLineSegment(sketch, "E3676", {"start": v(-354.82, -544.24) * mm, "end": v(-353.68, -543.7) * mm});
            skLineSegment(sketch, "E3677", {"start": v(-353.68, -543.7) * mm, "end": v(-352.49, -543.31) * mm});
            skLineSegment(sketch, "E3678", {"start": v(-352.49, -543.31) * mm, "end": v(-351.25, -543.08) * mm});
            skLineSegment(sketch, "E3679", {"start": v(-351.25, -543.08) * mm, "end": v(-350, -543) * mm});
            skLineSegment(sketch, "E3680", {"start": v(-350, -543) * mm, "end": v(-60, -543) * mm});
            skLineSegment(sketch, "E3681", {"start": v(-60, -543) * mm, "end": v(-60, -543.02) * mm});
            skLineSegment(sketch, "E3682", {"start": v(-60, -543.02) * mm, "end": v(-59.37, -543.02) * mm});
            skLineSegment(sketch, "E3683", {"start": v(-59.37, -543.02) * mm, "end": v(-58.13, -543.18) * mm});
            skLineSegment(sketch, "E3684", {"start": v(-58.13, -543.18) * mm, "end": v(-56.9, -543.49) * mm});
            skLineSegment(sketch, "E3685", {"start": v(-56.9, -543.49) * mm, "end": v(-55.74, -543.95) * mm});
            skLineSegment(sketch, "E3686", {"start": v(-55.74, -543.95) * mm, "end": v(-54.64, -544.56) * mm});
            skLineSegment(sketch, "E3687", {"start": v(-54.64, -544.56) * mm, "end": v(-53.63, -545.3) * mm});
            skLineSegment(sketch, "E3688", {"start": v(-53.63, -545.3) * mm, "end": v(-52.71, -546.15) * mm});
            skLineSegment(sketch, "E3689", {"start": v(-52.71, -546.15) * mm, "end": v(-51.9, -547.12) * mm});
            skLineSegment(sketch, "E3690", {"start": v(-51.9, -547.12) * mm, "end": v(-51.24, -548.18) * mm});
            skLineSegment(sketch, "E3691", {"start": v(-51.24, -548.18) * mm, "end": v(-50.7, -549.32) * mm});
            skLineSegment(sketch, "E3692", {"start": v(-50.7, -549.32) * mm, "end": v(-50.31, -550.51) * mm});
            skLineSegment(sketch, "E3693", {"start": v(-50.31, -550.51) * mm, "end": v(-50.08, -551.75) * mm});
            skLineSegment(sketch, "E3694", {"start": v(-50.08, -551.75) * mm, "end": v(-49.92, -554.25) * mm});
            skLineSegment(sketch, "E3695", {"start": v(-49.92, -554.25) * mm, "end": v(-49.69, -555.49) * mm});
            skLineSegment(sketch, "E3696", {"start": v(-49.69, -555.49) * mm, "end": v(-49.3, -556.68) * mm});
            skLineSegment(sketch, "E3697", {"start": v(-49.3, -556.68) * mm, "end": v(-48.76, -557.82) * mm});
            skLineSegment(sketch, "E3698", {"start": v(-48.76, -557.82) * mm, "end": v(-48.1, -558.88) * mm});
            skLineSegment(sketch, "E3699", {"start": v(-48.1, -558.88) * mm, "end": v(-47.29, -559.85) * mm});
            skLineSegment(sketch, "E3700", {"start": v(-47.29, -559.85) * mm, "end": v(-46.37, -560.7) * mm});
            skLineSegment(sketch, "E3701", {"start": v(-46.37, -560.7) * mm, "end": v(-45.36, -561.44) * mm});
            skLineSegment(sketch, "E3702", {"start": v(-45.36, -561.44) * mm, "end": v(-44.26, -562.05) * mm});
            skLineSegment(sketch, "E3703", {"start": v(-44.26, -562.05) * mm, "end": v(-43.1, -562.51) * mm});
            skLineSegment(sketch, "E3704", {"start": v(-43.1, -562.51) * mm, "end": v(-41.87, -562.82) * mm});
            skLineSegment(sketch, "E3705", {"start": v(-41.87, -562.82) * mm, "end": v(-40.63, -562.98) * mm});
            skLineSegment(sketch, "E3706", {"start": v(-40.63, -562.98) * mm, "end": v(-40, -562.98) * mm});
            skLineSegment(sketch, "E3707", {"start": v(-40, -562.98) * mm, "end": v(-40, -563) * mm});
            skLineSegment(sketch, "E3708", {"start": v(-40, -563) * mm, "end": v(-20, -563) * mm});
            skLineSegment(sketch, "E3709", {"start": v(-20, -563) * mm, "end": v(-18.75, -562.92) * mm});
            skLineSegment(sketch, "E3710", {"start": v(-18.75, -562.92) * mm, "end": v(-17.51, -562.69) * mm});
            skLineSegment(sketch, "E3711", {"start": v(-17.51, -562.69) * mm, "end": v(-16.32, -562.3) * mm});
            skLineSegment(sketch, "E3712", {"start": v(-16.32, -562.3) * mm, "end": v(-15.18, -561.76) * mm});
            skLineSegment(sketch, "E3713", {"start": v(-15.18, -561.76) * mm, "end": v(-14.12, -561.1) * mm});
            skLineSegment(sketch, "E3714", {"start": v(-14.12, -561.1) * mm, "end": v(-13.15, -560.29) * mm});
            skLineSegment(sketch, "E3715", {"start": v(-13.15, -560.29) * mm, "end": v(-12.3, -559.37) * mm});
            skLineSegment(sketch, "E3716", {"start": v(-12.3, -559.37) * mm, "end": v(-11.56, -558.36) * mm});
            skLineSegment(sketch, "E3717", {"start": v(-11.56, -558.36) * mm, "end": v(-10.95, -557.26) * mm});
            skLineSegment(sketch, "E3718", {"start": v(-10.95, -557.26) * mm, "end": v(-10.49, -556.1) * mm});
            skLineSegment(sketch, "E3719", {"start": v(-10.49, -556.1) * mm, "end": v(-10.18, -554.87) * mm});
            skLineSegment(sketch, "E3720", {"start": v(-10.18, -554.87) * mm, "end": v(-10.02, -553.63) * mm});
            skLineSegment(sketch, "E3721", {"start": v(-10.02, -553.63) * mm, "end": v(-10.02, -553) * mm});
            skLineSegment(sketch, "E3722", {"start": v(-10.02, -553) * mm, "end": v(-10, -553) * mm});
            skLineSegment(sketch, "E3723", {"start": v(-10, -553) * mm, "end": v(-10, -503) * mm});
            skLineSegment(sketch, "E3724", {"start": v(-10, -503) * mm, "end": v(-50, -503) * mm});
            skLineSegment(sketch, "E3725", {"start": v(-50, -503) * mm, "end": v(-50, -487) * mm});
            skLineSegment(sketch, "E3726", {"start": v(-50, -487) * mm, "end": v(-70, -487) * mm});
            skLineSegment(sketch, "E3727", {"start": v(-70, -487) * mm, "end": v(-70, -503) * mm});
            skLineSegment(sketch, "E3728", {"start": v(-70, -503) * mm, "end": v(-195, -503) * mm});
            skLineSegment(sketch, "E3729", {"start": v(-195, -503) * mm, "end": v(-195, -487) * mm});
            skLineSegment(sketch, "E3730", {"start": v(-195, -487) * mm, "end": v(-215, -487) * mm});
            skLineSegment(sketch, "E3731", {"start": v(-215, -487) * mm, "end": v(-215, -503) * mm});
            skLineSegment(sketch, "E3732", {"start": v(-215, -503) * mm, "end": v(-340, -503) * mm});
            skLineSegment(sketch, "E3733", {"start": v(-340, -503) * mm, "end": v(-340, -487) * mm});
            skLineSegment(sketch, "E3734", {"start": v(-340, -487) * mm, "end": v(-360, -487) * mm});
            skLineSegment(sketch, "E3735", {"start": v(-360, -487) * mm, "end": v(-360, -503) * mm});
            skLineSegment(sketch, "E3736", {"start": v(-360, -503) * mm, "end": v(-400, -503) * mm});
            skLineSegment(sketch, "E3737", {"start": v(-400, -503) * mm, "end": v(-400, -553) * mm});
            skLineSegment(sketch, "E3738", {"start": v(-400, -553) * mm, "end": v(-399.92, -554.25) * mm});
            skLineSegment(sketch, "E3739", {"start": v(-399.92, -554.25) * mm, "end": v(-399.69, -555.49) * mm});
            skLineSegment(sketch, "E3740", {"start": v(-399.69, -555.49) * mm, "end": v(-399.3, -556.68) * mm});
            skLineSegment(sketch, "E3741", {"start": v(-399.3, -556.68) * mm, "end": v(-398.76, -557.82) * mm});
            skLineSegment(sketch, "E3742", {"start": v(-398.76, -557.82) * mm, "end": v(-398.09, -558.88) * mm});
            skLineSegment(sketch, "E3743", {"start": v(-398.09, -558.88) * mm, "end": v(-397.3, -559.85) * mm});
            skLineSegment(sketch, "E3744", {"start": v(-397.3, -559.85) * mm, "end": v(-396.37, -560.7) * mm});
            skLineSegment(sketch, "E3745", {"start": v(-396.37, -560.7) * mm, "end": v(-395.36, -561.44) * mm});
            skLineSegment(sketch, "E3746", {"start": v(-395.36, -561.44) * mm, "end": v(-394.26, -562.05) * mm});
            skLineSegment(sketch, "E3747", {"start": v(-394.26, -562.05) * mm, "end": v(-393.09, -562.51) * mm});
            skLineSegment(sketch, "E3748", {"start": v(-393.09, -562.51) * mm, "end": v(-391.87, -562.82) * mm});
            skLineSegment(sketch, "E3749", {"start": v(-391.87, -562.82) * mm, "end": v(-390.63, -562.98) * mm});
            skLineSegment(sketch, "E3750", {"start": v(-390.63, -562.98) * mm, "end": v(-390, -562.98) * mm});
            skLineSegment(sketch, "E3751", {"start": v(-390, -562.98) * mm, "end": v(-390, -563) * mm});
            skLineSegment(sketch, "E3752", {"start": v(-390, -563) * mm, "end": v(-370, -563) * mm});
            skLineSegment(sketch, "E3753", {"start": v(-370, -563) * mm, "end": v(-370, -562.98) * mm});
            skLineSegment(sketch, "E3754", {"start": v(40, -562.98) * mm, "end": v(40.63, -562.98) * mm});
            skLineSegment(sketch, "E3755", {"start": v(40.63, -562.98) * mm, "end": v(41.87, -562.82) * mm});
            skLineSegment(sketch, "E3756", {"start": v(41.87, -562.82) * mm, "end": v(43.1, -562.51) * mm});
            skLineSegment(sketch, "E3757", {"start": v(43.1, -562.51) * mm, "end": v(44.26, -562.05) * mm});
            skLineSegment(sketch, "E3758", {"start": v(44.26, -562.05) * mm, "end": v(45.36, -561.44) * mm});
            skLineSegment(sketch, "E3759", {"start": v(45.36, -561.44) * mm, "end": v(46.37, -560.7) * mm});
            skLineSegment(sketch, "E3760", {"start": v(46.37, -560.7) * mm, "end": v(47.29, -559.85) * mm});
            skLineSegment(sketch, "E3761", {"start": v(47.29, -559.85) * mm, "end": v(48.1, -558.88) * mm});
            skLineSegment(sketch, "E3762", {"start": v(48.1, -558.88) * mm, "end": v(48.76, -557.82) * mm});
            skLineSegment(sketch, "E3763", {"start": v(48.76, -557.82) * mm, "end": v(49.3, -556.68) * mm});
            skLineSegment(sketch, "E3764", {"start": v(49.3, -556.68) * mm, "end": v(49.69, -555.49) * mm});
            skLineSegment(sketch, "E3765", {"start": v(49.69, -555.49) * mm, "end": v(49.92, -554.25) * mm});
            skLineSegment(sketch, "E3766", {"start": v(49.92, -554.25) * mm, "end": v(50, -553) * mm});
            skLineSegment(sketch, "E3767", {"start": v(50, -553) * mm, "end": v(50.02, -553) * mm});
            skLineSegment(sketch, "E3768", {"start": v(50.02, -553) * mm, "end": v(50.02, -552.37) * mm});
            skLineSegment(sketch, "E3769", {"start": v(50.02, -552.37) * mm, "end": v(50.18, -551.13) * mm});
            skLineSegment(sketch, "E3770", {"start": v(50.18, -551.13) * mm, "end": v(50.49, -549.9) * mm});
            skLineSegment(sketch, "E3771", {"start": v(50.49, -549.9) * mm, "end": v(50.95, -548.74) * mm});
            skLineSegment(sketch, "E3772", {"start": v(50.95, -548.74) * mm, "end": v(51.56, -547.64) * mm});
            skLineSegment(sketch, "E3773", {"start": v(51.56, -547.64) * mm, "end": v(52.3, -546.63) * mm});
            skLineSegment(sketch, "E3774", {"start": v(52.3, -546.63) * mm, "end": v(53.15, -545.71) * mm});
            skLineSegment(sketch, "E3775", {"start": v(53.15, -545.71) * mm, "end": v(54.12, -544.9) * mm});
            skLineSegment(sketch, "E3776", {"start": v(54.12, -544.9) * mm, "end": v(55.18, -544.24) * mm});
            skLineSegment(sketch, "E3777", {"start": v(55.18, -544.24) * mm, "end": v(56.32, -543.7) * mm});
            skLineSegment(sketch, "E3778", {"start": v(56.32, -543.7) * mm, "end": v(57.51, -543.31) * mm});
            skLineSegment(sketch, "E3779", {"start": v(57.51, -543.31) * mm, "end": v(58.75, -543.08) * mm});
            skLineSegment(sketch, "E3780", {"start": v(58.75, -543.08) * mm, "end": v(60, -543) * mm});
            skLineSegment(sketch, "E3781", {"start": v(60, -543) * mm, "end": v(350, -543) * mm});
            skLineSegment(sketch, "E3782", {"start": v(350, -543) * mm, "end": v(350, -543.02) * mm});
            skLineSegment(sketch, "E3783", {"start": v(350, -543.02) * mm, "end": v(350.63, -543.02) * mm});
            skLineSegment(sketch, "E3784", {"start": v(350.63, -543.02) * mm, "end": v(351.87, -543.18) * mm});
            skLineSegment(sketch, "E3785", {"start": v(351.87, -543.18) * mm, "end": v(353.09, -543.49) * mm});
            skLineSegment(sketch, "E3786", {"start": v(353.09, -543.49) * mm, "end": v(354.26, -543.95) * mm});
            skLineSegment(sketch, "E3787", {"start": v(354.26, -543.95) * mm, "end": v(355.36, -544.56) * mm});
            skLineSegment(sketch, "E3788", {"start": v(355.36, -544.56) * mm, "end": v(356.37, -545.3) * mm});
            skLineSegment(sketch, "E3789", {"start": v(356.37, -545.3) * mm, "end": v(357.3, -546.15) * mm});
            skLineSegment(sketch, "E3790", {"start": v(357.3, -546.15) * mm, "end": v(358.09, -547.12) * mm});
            skLineSegment(sketch, "E3791", {"start": v(358.09, -547.12) * mm, "end": v(358.76, -548.18) * mm});
            skLineSegment(sketch, "E3792", {"start": v(358.76, -548.18) * mm, "end": v(359.3, -549.32) * mm});
            skLineSegment(sketch, "E3793", {"start": v(359.3, -549.32) * mm, "end": v(359.69, -550.51) * mm});
            skLineSegment(sketch, "E3794", {"start": v(359.69, -550.51) * mm, "end": v(359.92, -551.75) * mm});
            skLineSegment(sketch, "E3795", {"start": v(359.92, -551.75) * mm, "end": v(360.08, -554.25) * mm});
            skLineSegment(sketch, "E3796", {"start": v(360.08, -554.25) * mm, "end": v(360.31, -555.49) * mm});
            skLineSegment(sketch, "E3797", {"start": v(360.31, -555.49) * mm, "end": v(360.7, -556.68) * mm});
            skLineSegment(sketch, "E3798", {"start": v(360.7, -556.68) * mm, "end": v(361.24, -557.82) * mm});
            skLineSegment(sketch, "E3799", {"start": v(361.24, -557.82) * mm, "end": v(361.91, -558.88) * mm});
            skLineSegment(sketch, "E3800", {"start": v(361.91, -558.88) * mm, "end": v(362.7, -559.85) * mm});
            skLineSegment(sketch, "E3801", {"start": v(362.7, -559.85) * mm, "end": v(363.63, -560.7) * mm});
            skLineSegment(sketch, "E3802", {"start": v(363.63, -560.7) * mm, "end": v(364.64, -561.44) * mm});
            skLineSegment(sketch, "E3803", {"start": v(364.64, -561.44) * mm, "end": v(365.74, -562.05) * mm});
            skLineSegment(sketch, "E3804", {"start": v(365.74, -562.05) * mm, "end": v(366.91, -562.51) * mm});
            skLineSegment(sketch, "E3805", {"start": v(366.91, -562.51) * mm, "end": v(368.13, -562.82) * mm});
            skLineSegment(sketch, "E3806", {"start": v(368.13, -562.82) * mm, "end": v(369.37, -562.98) * mm});
            skLineSegment(sketch, "E3807", {"start": v(369.37, -562.98) * mm, "end": v(370, -562.98) * mm});
            skLineSegment(sketch, "E3808", {"start": v(370, -562.98) * mm, "end": v(370, -563) * mm});
            skLineSegment(sketch, "E3809", {"start": v(370, -563) * mm, "end": v(390, -563) * mm});
            skLineSegment(sketch, "E3810", {"start": v(390, -563) * mm, "end": v(391.25, -562.92) * mm});
            skLineSegment(sketch, "E3811", {"start": v(391.25, -562.92) * mm, "end": v(392.49, -562.69) * mm});
            skLineSegment(sketch, "E3812", {"start": v(392.49, -562.69) * mm, "end": v(393.68, -562.3) * mm});
            skLineSegment(sketch, "E3813", {"start": v(393.68, -562.3) * mm, "end": v(394.82, -561.76) * mm});
            skLineSegment(sketch, "E3814", {"start": v(394.82, -561.76) * mm, "end": v(395.88, -561.1) * mm});
            skLineSegment(sketch, "E3815", {"start": v(395.88, -561.1) * mm, "end": v(396.85, -560.29) * mm});
            skLineSegment(sketch, "E3816", {"start": v(396.85, -560.29) * mm, "end": v(397.7, -559.37) * mm});
            skLineSegment(sketch, "E3817", {"start": v(397.7, -559.37) * mm, "end": v(398.44, -558.36) * mm});
            skLineSegment(sketch, "E3818", {"start": v(398.44, -558.36) * mm, "end": v(399.05, -557.26) * mm});
            skLineSegment(sketch, "E3819", {"start": v(399.05, -557.26) * mm, "end": v(399.51, -556.1) * mm});
            skLineSegment(sketch, "E3820", {"start": v(399.51, -556.1) * mm, "end": v(399.82, -554.87) * mm});
            skLineSegment(sketch, "E3821", {"start": v(399.82, -554.87) * mm, "end": v(399.98, -553.63) * mm});
            skLineSegment(sketch, "E3822", {"start": v(399.98, -553.63) * mm, "end": v(399.98, -553) * mm});
            skLineSegment(sketch, "E3823", {"start": v(399.98, -553) * mm, "end": v(400, -553) * mm});
            skLineSegment(sketch, "E3824", {"start": v(400, -553) * mm, "end": v(400, -503) * mm});
            skLineSegment(sketch, "E3825", {"start": v(400, -503) * mm, "end": v(360, -503) * mm});
            skLineSegment(sketch, "E3826", {"start": v(360, -503) * mm, "end": v(360, -487) * mm});
            skLineSegment(sketch, "E3827", {"start": v(340, -487) * mm, "end": v(340, -503) * mm});
            skLineSegment(sketch, "E3828", {"start": v(340, -503) * mm, "end": v(215, -503) * mm});
            skLineSegment(sketch, "E3829", {"start": v(215, -503) * mm, "end": v(215, -487) * mm});
            skLineSegment(sketch, "E3830", {"start": v(195, -487) * mm, "end": v(195, -503) * mm});
            skLineSegment(sketch, "E3831", {"start": v(195, -503) * mm, "end": v(70, -503) * mm});
            skLineSegment(sketch, "E3832", {"start": v(70, -503) * mm, "end": v(70, -487) * mm});
            skLineSegment(sketch, "E3833", {"start": v(391.25, -476.92) * mm, "end": v(392.49, -476.69) * mm});
            skLineSegment(sketch, "E3834", {"start": v(392.49, -476.69) * mm, "end": v(393.68, -476.3) * mm});
            skLineSegment(sketch, "E3835", {"start": v(393.68, -476.3) * mm, "end": v(394.82, -475.76) * mm});
            skLineSegment(sketch, "E3836", {"start": v(394.82, -475.76) * mm, "end": v(395.88, -475.1) * mm});
            skLineSegment(sketch, "E3837", {"start": v(395.88, -475.1) * mm, "end": v(396.85, -474.29) * mm});
            skLineSegment(sketch, "E3838", {"start": v(396.85, -474.29) * mm, "end": v(397.7, -473.37) * mm});
            skLineSegment(sketch, "E3839", {"start": v(397.7, -473.37) * mm, "end": v(398.44, -472.36) * mm});
            skLineSegment(sketch, "E3840", {"start": v(398.44, -472.36) * mm, "end": v(399.05, -471.26) * mm});
            skLineSegment(sketch, "E3841", {"start": v(399.05, -471.26) * mm, "end": v(399.51, -470.1) * mm});
            skLineSegment(sketch, "E3842", {"start": v(399.51, -470.1) * mm, "end": v(399.82, -468.87) * mm});
            skLineSegment(sketch, "E3843", {"start": v(399.82, -468.87) * mm, "end": v(399.98, -467.63) * mm});
            skLineSegment(sketch, "E3844", {"start": v(399.98, -467.63) * mm, "end": v(399.98, -467) * mm});
            skLineSegment(sketch, "E3845", {"start": v(399.98, -467) * mm, "end": v(400, -467) * mm});
            skLineSegment(sketch, "E3846", {"start": v(400, -467) * mm, "end": v(400, -191) * mm});
            skLineSegment(sketch, "E3847", {"start": v(400, -191) * mm, "end": v(360, -191) * mm});
            skLineSegment(sketch, "E3848", {"start": v(360, -191) * mm, "end": v(360, -175) * mm});
            skLineSegment(sketch, "E3849", {"start": v(360, -175) * mm, "end": v(400, -175) * mm});
            skLineSegment(sketch, "E3850", {"start": v(400, -175) * mm, "end": v(400, -47) * mm});
            skLineSegment(sketch, "E3851", {"start": v(400, -47) * mm, "end": v(399.92, -45.75) * mm});
            skLineSegment(sketch, "E3852", {"start": v(399.92, -45.75) * mm, "end": v(399.69, -44.51) * mm});
            skLineSegment(sketch, "E3853", {"start": v(399.69, -44.51) * mm, "end": v(399.3, -43.32) * mm});
            skLineSegment(sketch, "E3854", {"start": v(399.3, -43.32) * mm, "end": v(398.76, -42.18) * mm});
            skLineSegment(sketch, "E3855", {"start": v(398.76, -42.18) * mm, "end": v(398.09, -41.12) * mm});
            skLineSegment(sketch, "E3856", {"start": v(398.09, -41.12) * mm, "end": v(397.3, -40.16) * mm});
            skLineSegment(sketch, "E3857", {"start": v(397.3, -40.16) * mm, "end": v(396.37, -39.3) * mm});
            skLineSegment(sketch, "E3858", {"start": v(396.37, -39.3) * mm, "end": v(395.36, -38.56) * mm});
            skLineSegment(sketch, "E3859", {"start": v(395.36, -38.56) * mm, "end": v(394.26, -37.95) * mm});
            skLineSegment(sketch, "E3860", {"start": v(394.26, -37.95) * mm, "end": v(393.09, -37.49) * mm});
            skLineSegment(sketch, "E3861", {"start": v(393.09, -37.49) * mm, "end": v(391.87, -37.18) * mm});
            skLineSegment(sketch, "E3862", {"start": v(391.87, -37.18) * mm, "end": v(390.63, -37.02) * mm});
            skLineSegment(sketch, "E3863", {"start": v(390.63, -37.02) * mm, "end": v(390, -37.02) * mm});
            skLineSegment(sketch, "E3864", {"start": v(390, -37.02) * mm, "end": v(390, -37) * mm});
            skLineSegment(sketch, "E3865", {"start": v(390, -37) * mm, "end": v(20, -37) * mm});
            skLineSegment(sketch, "E3866", {"start": v(20, -37) * mm, "end": v(18.75, -37.08) * mm});
            skLineSegment(sketch, "E3867", {"start": v(18.75, -37.08) * mm, "end": v(17.51, -37.31) * mm});
            skLineSegment(sketch, "E3868", {"start": v(17.51, -37.31) * mm, "end": v(16.32, -37.7) * mm});
            skLineSegment(sketch, "E3869", {"start": v(16.32, -37.7) * mm, "end": v(15.18, -38.24) * mm});
            skLineSegment(sketch, "E3870", {"start": v(15.18, -38.24) * mm, "end": v(14.12, -38.9) * mm});
            skLineSegment(sketch, "E3871", {"start": v(14.12, -38.9) * mm, "end": v(13.15, -39.7) * mm});
            skLineSegment(sketch, "E3872", {"start": v(13.15, -39.7) * mm, "end": v(12.3, -40.63) * mm});
            skLineSegment(sketch, "E3873", {"start": v(12.3, -40.63) * mm, "end": v(11.56, -41.64) * mm});
            skLineSegment(sketch, "E3874", {"start": v(11.56, -41.64) * mm, "end": v(10.95, -42.74) * mm});
            skLineSegment(sketch, "E3875", {"start": v(10.95, -42.74) * mm, "end": v(10.49, -43.9) * mm});
            skLineSegment(sketch, "E3876", {"start": v(10.49, -43.9) * mm, "end": v(10.18, -45.13) * mm});
            skLineSegment(sketch, "E3877", {"start": v(10.18, -45.13) * mm, "end": v(10.02, -46.37) * mm});
            skLineSegment(sketch, "E3878", {"start": v(10.02, -46.37) * mm, "end": v(10.02, -47) * mm});
            skLineSegment(sketch, "E3879", {"start": v(10.02, -47) * mm, "end": v(10, -47) * mm});
            skLineSegment(sketch, "E3880", {"start": v(10, -47) * mm, "end": v(10, -175) * mm});
            skLineSegment(sketch, "E3881", {"start": v(10, -175) * mm, "end": v(50, -175) * mm});
            skLineSegment(sketch, "E3882", {"start": v(50, -175) * mm, "end": v(50, -191) * mm});
            skLineSegment(sketch, "E3883", {"start": v(50, -191) * mm, "end": v(10, -191) * mm});
            skLineSegment(sketch, "E3884", {"start": v(10, -191) * mm, "end": v(10, -467) * mm});
            skLineSegment(sketch, "E3885", {"start": v(10, -467) * mm, "end": v(10.08, -468.25) * mm});
            skLineSegment(sketch, "E3886", {"start": v(10.08, -468.25) * mm, "end": v(10.31, -469.49) * mm});
            skLineSegment(sketch, "E3887", {"start": v(10.31, -469.49) * mm, "end": v(10.7, -470.68) * mm});
            skLineSegment(sketch, "E3888", {"start": v(10.7, -470.68) * mm, "end": v(11.24, -471.82) * mm});
            skLineSegment(sketch, "E3889", {"start": v(11.24, -471.82) * mm, "end": v(11.9, -472.88) * mm});
            skLineSegment(sketch, "E3890", {"start": v(11.9, -472.88) * mm, "end": v(12.71, -473.85) * mm});
            skLineSegment(sketch, "E3891", {"start": v(12.71, -473.85) * mm, "end": v(13.63, -474.7) * mm});
            skLineSegment(sketch, "E3892", {"start": v(13.63, -474.7) * mm, "end": v(14.64, -475.44) * mm});
            skLineSegment(sketch, "E3893", {"start": v(14.64, -475.44) * mm, "end": v(15.74, -476.05) * mm});
            skLineSegment(sketch, "E3894", {"start": v(15.74, -476.05) * mm, "end": v(16.9, -476.51) * mm});
            skLineSegment(sketch, "E3895", {"start": v(16.9, -476.51) * mm, "end": v(18.13, -476.82) * mm});
            skLineSegment(sketch, "E3896", {"start": v(18.13, -476.82) * mm, "end": v(19.37, -476.98) * mm});
            skLineSegment(sketch, "E3897", {"start": v(19.37, -476.98) * mm, "end": v(20, -476.98) * mm});
            skLineSegment(sketch, "E3898", {"start": v(20, -476.98) * mm, "end": v(20, -477) * mm});
            skLineSegment(sketch, "E3899", {"start": v(20, -477) * mm, "end": v(390, -477) * mm});
            skLineSegment(sketch, "E3900", {"start": v(390, -477) * mm, "end": v(391.25, -476.92) * mm});
            skLineSegment(sketch, "E3901", {"start": v(340, -63.5) * mm, "end": v(340, -47.5) * mm});
            skLineSegment(sketch, "E3902", {"start": v(340, -47.5) * mm, "end": v(360, -47.5) * mm});
            skLineSegment(sketch, "E3903", {"start": v(360, -47.5) * mm, "end": v(360, -63.5) * mm});
            skLineSegment(sketch, "E3904", {"start": v(360, -63.5) * mm, "end": v(340, -63.5) * mm});
            skLineSegment(sketch, "E3905", {"start": v(195, -63.5) * mm, "end": v(195, -47.5) * mm});
            skLineSegment(sketch, "E3906", {"start": v(195, -47.5) * mm, "end": v(215, -47.5) * mm});
            skLineSegment(sketch, "E3907", {"start": v(215, -47.5) * mm, "end": v(215, -63.5) * mm});
            skLineSegment(sketch, "E3908", {"start": v(215, -63.5) * mm, "end": v(195, -63.5) * mm});
            skLineSegment(sketch, "E3909", {"start": v(50, -63.5) * mm, "end": v(50, -47.5) * mm});
            skLineSegment(sketch, "E3910", {"start": v(50, -47.5) * mm, "end": v(70, -47.5) * mm});
            skLineSegment(sketch, "E3911", {"start": v(70, -47.5) * mm, "end": v(70, -63.5) * mm});
            skLineSegment(sketch, "E3912", {"start": v(70, -63.5) * mm, "end": v(50, -63.5) * mm});
            skLineSegment(sketch, "E3913", {"start": v(122.37, -57.5) * mm, "end": v(122.12, -57.47) * mm});
            skLineSegment(sketch, "E3914", {"start": v(122.12, -57.47) * mm, "end": v(121.88, -57.4) * mm});
            skLineSegment(sketch, "E3915", {"start": v(121.88, -57.4) * mm, "end": v(121.65, -57.31) * mm});
            skLineSegment(sketch, "E3916", {"start": v(121.65, -57.31) * mm, "end": v(121.43, -57.19) * mm});
            skLineSegment(sketch, "E3917", {"start": v(121.43, -57.19) * mm, "end": v(121.22, -57.04) * mm});
            skLineSegment(sketch, "E3918", {"start": v(121.22, -57.04) * mm, "end": v(121.04, -56.87) * mm});
            skLineSegment(sketch, "E3919", {"start": v(121.04, -56.87) * mm, "end": v(120.88, -56.68) * mm});
            skLineSegment(sketch, "E3920", {"start": v(120.88, -56.68) * mm, "end": v(120.75, -56.46) * mm});
            skLineSegment(sketch, "E3921", {"start": v(120.75, -56.46) * mm, "end": v(120.64, -56.24) * mm});
            skLineSegment(sketch, "E3922", {"start": v(120.64, -56.24) * mm, "end": v(120.56, -56) * mm});
            skLineSegment(sketch, "E3923", {"start": v(120.56, -56) * mm, "end": v(120.52, -55.75) * mm});
            skLineSegment(sketch, "E3924", {"start": v(120.52, -55.75) * mm, "end": v(120.5, -55.5) * mm});
            skLineSegment(sketch, "E3925", {"start": v(120.5, -55.5) * mm, "end": v(120.52, -55.25) * mm});
            skLineSegment(sketch, "E3926", {"start": v(120.52, -55.25) * mm, "end": v(120.56, -55) * mm});
            skLineSegment(sketch, "E3927", {"start": v(120.56, -55) * mm, "end": v(120.64, -54.76) * mm});
            skLineSegment(sketch, "E3928", {"start": v(120.64, -54.76) * mm, "end": v(120.75, -54.54) * mm});
            skLineSegment(sketch, "E3929", {"start": v(120.75, -54.54) * mm, "end": v(120.88, -54.32) * mm});
            skLineSegment(sketch, "E3930", {"start": v(120.88, -54.32) * mm, "end": v(121.04, -54.13) * mm});
            skLineSegment(sketch, "E3931", {"start": v(121.04, -54.13) * mm, "end": v(121.22, -53.96) * mm});
            skLineSegment(sketch, "E3932", {"start": v(121.22, -53.96) * mm, "end": v(121.43, -53.81) * mm});
            skLineSegment(sketch, "E3933", {"start": v(121.43, -53.81) * mm, "end": v(121.65, -53.7) * mm});
            skLineSegment(sketch, "E3934", {"start": v(121.65, -53.7) * mm, "end": v(121.88, -53.6) * mm});
            skLineSegment(sketch, "E3935", {"start": v(121.88, -53.6) * mm, "end": v(122.12, -53.53) * mm});
            skLineSegment(sketch, "E3936", {"start": v(122.12, -53.53) * mm, "end": v(122.37, -53.5) * mm});
            skLineSegment(sketch, "E3937", {"start": v(122.37, -53.5) * mm, "end": v(122.63, -53.5) * mm});
            skLineSegment(sketch, "E3938", {"start": v(122.63, -53.5) * mm, "end": v(122.88, -53.53) * mm});
            skLineSegment(sketch, "E3939", {"start": v(122.88, -53.53) * mm, "end": v(123.12, -53.6) * mm});
            skLineSegment(sketch, "E3940", {"start": v(123.12, -53.6) * mm, "end": v(123.35, -53.7) * mm});
            skLineSegment(sketch, "E3941", {"start": v(123.35, -53.7) * mm, "end": v(123.57, -53.81) * mm});
            skLineSegment(sketch, "E3942", {"start": v(123.57, -53.81) * mm, "end": v(123.78, -53.96) * mm});
            skLineSegment(sketch, "E3943", {"start": v(123.78, -53.96) * mm, "end": v(123.96, -54.13) * mm});
            skLineSegment(sketch, "E3944", {"start": v(123.96, -54.13) * mm, "end": v(124.12, -54.32) * mm});
            skLineSegment(sketch, "E3945", {"start": v(124.12, -54.32) * mm, "end": v(124.25, -54.54) * mm});
            skLineSegment(sketch, "E3946", {"start": v(124.25, -54.54) * mm, "end": v(124.36, -54.76) * mm});
            skLineSegment(sketch, "E3947", {"start": v(124.36, -54.76) * mm, "end": v(124.44, -55) * mm});
            skLineSegment(sketch, "E3948", {"start": v(124.44, -55) * mm, "end": v(124.48, -55.25) * mm});
            skLineSegment(sketch, "E3949", {"start": v(124.48, -55.25) * mm, "end": v(124.5, -55.5) * mm});
            skLineSegment(sketch, "E3950", {"start": v(124.5, -55.5) * mm, "end": v(124.48, -55.75) * mm});
            skLineSegment(sketch, "E3951", {"start": v(124.48, -55.75) * mm, "end": v(124.44, -56) * mm});
            skLineSegment(sketch, "E3952", {"start": v(124.44, -56) * mm, "end": v(124.36, -56.24) * mm});
            skLineSegment(sketch, "E3953", {"start": v(124.36, -56.24) * mm, "end": v(124.25, -56.46) * mm});
            skLineSegment(sketch, "E3954", {"start": v(124.25, -56.46) * mm, "end": v(124.12, -56.68) * mm});
            skLineSegment(sketch, "E3955", {"start": v(124.12, -56.68) * mm, "end": v(123.96, -56.87) * mm});
            skLineSegment(sketch, "E3956", {"start": v(123.96, -56.87) * mm, "end": v(123.78, -57.04) * mm});
            skLineSegment(sketch, "E3957", {"start": v(123.78, -57.04) * mm, "end": v(123.57, -57.19) * mm});
            skLineSegment(sketch, "E3958", {"start": v(123.57, -57.19) * mm, "end": v(123.35, -57.31) * mm});
            skLineSegment(sketch, "E3959", {"start": v(123.35, -57.31) * mm, "end": v(123.12, -57.4) * mm});
            skLineSegment(sketch, "E3960", {"start": v(123.12, -57.4) * mm, "end": v(122.88, -57.47) * mm});
            skLineSegment(sketch, "E3961", {"start": v(122.88, -57.47) * mm, "end": v(122.63, -57.5) * mm});
            skLineSegment(sketch, "E3962", {"start": v(122.63, -57.5) * mm, "end": v(122.37, -57.5) * mm});
            skLineSegment(sketch, "E3963", {"start": v(287.37, -57.5) * mm, "end": v(287.12, -57.47) * mm});
            skLineSegment(sketch, "E3964", {"start": v(287.12, -57.47) * mm, "end": v(286.88, -57.4) * mm});
            skLineSegment(sketch, "E3965", {"start": v(286.88, -57.4) * mm, "end": v(286.65, -57.31) * mm});
            skLineSegment(sketch, "E3966", {"start": v(286.65, -57.31) * mm, "end": v(286.43, -57.19) * mm});
            skLineSegment(sketch, "E3967", {"start": v(286.43, -57.19) * mm, "end": v(286.23, -57.04) * mm});
            skLineSegment(sketch, "E3968", {"start": v(286.23, -57.04) * mm, "end": v(286.04, -56.87) * mm});
            skLineSegment(sketch, "E3969", {"start": v(286.04, -56.87) * mm, "end": v(285.88, -56.68) * mm});
            skLineSegment(sketch, "E3970", {"start": v(285.88, -56.68) * mm, "end": v(285.75, -56.46) * mm});
            skLineSegment(sketch, "E3971", {"start": v(285.75, -56.46) * mm, "end": v(285.64, -56.24) * mm});
            skLineSegment(sketch, "E3972", {"start": v(285.64, -56.24) * mm, "end": v(285.56, -56) * mm});
            skLineSegment(sketch, "E3973", {"start": v(285.56, -56) * mm, "end": v(285.52, -55.75) * mm});
            skLineSegment(sketch, "E3974", {"start": v(285.52, -55.75) * mm, "end": v(285.5, -55.5) * mm});
            skLineSegment(sketch, "E3975", {"start": v(285.5, -55.5) * mm, "end": v(285.52, -55.25) * mm});
            skLineSegment(sketch, "E3976", {"start": v(285.52, -55.25) * mm, "end": v(285.56, -55) * mm});
            skLineSegment(sketch, "E3977", {"start": v(285.56, -55) * mm, "end": v(285.64, -54.76) * mm});
            skLineSegment(sketch, "E3978", {"start": v(285.64, -54.76) * mm, "end": v(285.75, -54.54) * mm});
            skLineSegment(sketch, "E3979", {"start": v(285.75, -54.54) * mm, "end": v(285.88, -54.32) * mm});
            skLineSegment(sketch, "E3980", {"start": v(285.88, -54.32) * mm, "end": v(286.04, -54.13) * mm});
            skLineSegment(sketch, "E3981", {"start": v(286.04, -54.13) * mm, "end": v(286.23, -53.96) * mm});
            skLineSegment(sketch, "E3982", {"start": v(286.23, -53.96) * mm, "end": v(286.43, -53.81) * mm});
            skLineSegment(sketch, "E3983", {"start": v(286.43, -53.81) * mm, "end": v(286.65, -53.7) * mm});
            skLineSegment(sketch, "E3984", {"start": v(286.65, -53.7) * mm, "end": v(286.88, -53.6) * mm});
            skLineSegment(sketch, "E3985", {"start": v(286.88, -53.6) * mm, "end": v(287.12, -53.53) * mm});
            skLineSegment(sketch, "E3986", {"start": v(287.12, -53.53) * mm, "end": v(287.37, -53.5) * mm});
            skLineSegment(sketch, "E3987", {"start": v(287.37, -53.5) * mm, "end": v(287.63, -53.5) * mm});
            skLineSegment(sketch, "E3988", {"start": v(287.63, -53.5) * mm, "end": v(287.88, -53.53) * mm});
            skLineSegment(sketch, "E3989", {"start": v(287.88, -53.53) * mm, "end": v(288.12, -53.6) * mm});
            skLineSegment(sketch, "E3990", {"start": v(288.12, -53.6) * mm, "end": v(288.35, -53.7) * mm});
            skLineSegment(sketch, "E3991", {"start": v(288.35, -53.7) * mm, "end": v(288.57, -53.81) * mm});
            skLineSegment(sketch, "E3992", {"start": v(288.57, -53.81) * mm, "end": v(288.77, -53.96) * mm});
            skLineSegment(sketch, "E3993", {"start": v(288.77, -53.96) * mm, "end": v(288.96, -54.13) * mm});
            skLineSegment(sketch, "E3994", {"start": v(288.96, -54.13) * mm, "end": v(289.12, -54.32) * mm});
            skLineSegment(sketch, "E3995", {"start": v(289.12, -54.32) * mm, "end": v(289.25, -54.54) * mm});
            skLineSegment(sketch, "E3996", {"start": v(289.25, -54.54) * mm, "end": v(289.36, -54.76) * mm});
            skLineSegment(sketch, "E3997", {"start": v(289.36, -54.76) * mm, "end": v(289.44, -55) * mm});
            skLineSegment(sketch, "E3998", {"start": v(289.44, -55) * mm, "end": v(289.48, -55.25) * mm});
            skLineSegment(sketch, "E3999", {"start": v(289.48, -55.25) * mm, "end": v(289.5, -55.5) * mm});
            skLineSegment(sketch, "E4000", {"start": v(289.5, -55.5) * mm, "end": v(289.48, -55.75) * mm});
            skLineSegment(sketch, "E4001", {"start": v(289.48, -55.75) * mm, "end": v(289.44, -56) * mm});
            skLineSegment(sketch, "E4002", {"start": v(289.44, -56) * mm, "end": v(289.36, -56.24) * mm});
            skLineSegment(sketch, "E4003", {"start": v(289.36, -56.24) * mm, "end": v(289.25, -56.46) * mm});
            skLineSegment(sketch, "E4004", {"start": v(289.25, -56.46) * mm, "end": v(289.12, -56.68) * mm});
            skLineSegment(sketch, "E4005", {"start": v(289.12, -56.68) * mm, "end": v(288.96, -56.87) * mm});
            skLineSegment(sketch, "E4006", {"start": v(288.96, -56.87) * mm, "end": v(288.77, -57.04) * mm});
            skLineSegment(sketch, "E4007", {"start": v(288.77, -57.04) * mm, "end": v(288.57, -57.19) * mm});
            skLineSegment(sketch, "E4008", {"start": v(288.57, -57.19) * mm, "end": v(288.35, -57.31) * mm});
            skLineSegment(sketch, "E4009", {"start": v(288.35, -57.31) * mm, "end": v(288.12, -57.4) * mm});
            skLineSegment(sketch, "E4010", {"start": v(288.12, -57.4) * mm, "end": v(287.88, -57.47) * mm});
            skLineSegment(sketch, "E4011", {"start": v(287.88, -57.47) * mm, "end": v(287.63, -57.5) * mm});
            skLineSegment(sketch, "E4012", {"start": v(287.63, -57.5) * mm, "end": v(287.37, -57.5) * mm});
            skLineSegment(sketch, "E4013", {"start": v(157.9, -68.5) * mm, "end": v(157.72, -68.47) * mm});
            skLineSegment(sketch, "E4014", {"start": v(157.72, -68.47) * mm, "end": v(157.54, -68.43) * mm});
            skLineSegment(sketch, "E4015", {"start": v(157.54, -68.43) * mm, "end": v(157.36, -68.36) * mm});
            skLineSegment(sketch, "E4016", {"start": v(157.36, -68.36) * mm, "end": v(157.2, -68.27) * mm});
            skLineSegment(sketch, "E4017", {"start": v(157.2, -68.27) * mm, "end": v(157.04, -68.16) * mm});
            skLineSegment(sketch, "E4018", {"start": v(157.04, -68.16) * mm, "end": v(156.9, -68.03) * mm});
            skLineSegment(sketch, "E4019", {"start": v(156.9, -68.03) * mm, "end": v(156.79, -67.88) * mm});
            skLineSegment(sketch, "E4020", {"start": v(156.79, -67.88) * mm, "end": v(156.69, -67.72) * mm});
            skLineSegment(sketch, "E4021", {"start": v(156.69, -67.72) * mm, "end": v(156.6, -67.55) * mm});
            skLineSegment(sketch, "E4022", {"start": v(156.6, -67.55) * mm, "end": v(156.55, -67.37) * mm});
            skLineSegment(sketch, "E4023", {"start": v(156.55, -67.37) * mm, "end": v(156.51, -67.19) * mm});
            skLineSegment(sketch, "E4024", {"start": v(156.51, -67.19) * mm, "end": v(156.5, -67) * mm});
            skLineSegment(sketch, "E4025", {"start": v(156.5, -67) * mm, "end": v(156.51, -66.81) * mm});
            skLineSegment(sketch, "E4026", {"start": v(156.51, -66.81) * mm, "end": v(156.55, -66.63) * mm});
            skLineSegment(sketch, "E4027", {"start": v(156.55, -66.63) * mm, "end": v(156.6, -66.45) * mm});
            skLineSegment(sketch, "E4028", {"start": v(156.6, -66.45) * mm, "end": v(156.69, -66.28) * mm});
            skLineSegment(sketch, "E4029", {"start": v(156.69, -66.28) * mm, "end": v(156.79, -66.12) * mm});
            skLineSegment(sketch, "E4030", {"start": v(156.79, -66.12) * mm, "end": v(156.9, -65.97) * mm});
            skLineSegment(sketch, "E4031", {"start": v(156.9, -65.97) * mm, "end": v(157.04, -65.84) * mm});
            skLineSegment(sketch, "E4032", {"start": v(157.04, -65.84) * mm, "end": v(157.2, -65.73) * mm});
            skLineSegment(sketch, "E4033", {"start": v(157.2, -65.73) * mm, "end": v(157.36, -65.64) * mm});
            skLineSegment(sketch, "E4034", {"start": v(157.36, -65.64) * mm, "end": v(157.54, -65.57) * mm});
            skLineSegment(sketch, "E4035", {"start": v(157.54, -65.57) * mm, "end": v(157.72, -65.53) * mm});
            skLineSegment(sketch, "E4036", {"start": v(157.72, -65.53) * mm, "end": v(157.9, -65.5) * mm});
            skLineSegment(sketch, "E4037", {"start": v(157.9, -65.5) * mm, "end": v(158.1, -65.5) * mm});
            skLineSegment(sketch, "E4038", {"start": v(158.1, -65.5) * mm, "end": v(158.28, -65.53) * mm});
            skLineSegment(sketch, "E4039", {"start": v(158.28, -65.53) * mm, "end": v(158.46, -65.57) * mm});
            skLineSegment(sketch, "E4040", {"start": v(158.46, -65.57) * mm, "end": v(158.64, -65.64) * mm});
            skLineSegment(sketch, "E4041", {"start": v(158.64, -65.64) * mm, "end": v(158.8, -65.73) * mm});
            skLineSegment(sketch, "E4042", {"start": v(158.8, -65.73) * mm, "end": v(158.96, -65.84) * mm});
            skLineSegment(sketch, "E4043", {"start": v(158.96, -65.84) * mm, "end": v(159.1, -65.97) * mm});
            skLineSegment(sketch, "E4044", {"start": v(159.1, -65.97) * mm, "end": v(159.21, -66.12) * mm});
            skLineSegment(sketch, "E4045", {"start": v(159.21, -66.12) * mm, "end": v(159.31, -66.28) * mm});
            skLineSegment(sketch, "E4046", {"start": v(159.31, -66.28) * mm, "end": v(159.4, -66.45) * mm});
            skLineSegment(sketch, "E4047", {"start": v(159.4, -66.45) * mm, "end": v(159.45, -66.63) * mm});
            skLineSegment(sketch, "E4048", {"start": v(159.45, -66.63) * mm, "end": v(159.49, -66.81) * mm});
            skLineSegment(sketch, "E4049", {"start": v(159.49, -66.81) * mm, "end": v(159.5, -67) * mm});
            skLineSegment(sketch, "E4050", {"start": v(159.5, -67) * mm, "end": v(159.49, -67.19) * mm});
            skLineSegment(sketch, "E4051", {"start": v(159.49, -67.19) * mm, "end": v(159.45, -67.37) * mm});
            skLineSegment(sketch, "E4052", {"start": v(159.45, -67.37) * mm, "end": v(159.4, -67.55) * mm});
            skLineSegment(sketch, "E4053", {"start": v(159.4, -67.55) * mm, "end": v(159.31, -67.72) * mm});
            skLineSegment(sketch, "E4054", {"start": v(159.31, -67.72) * mm, "end": v(159.21, -67.88) * mm});
            skLineSegment(sketch, "E4055", {"start": v(159.21, -67.88) * mm, "end": v(159.1, -68.03) * mm});
            skLineSegment(sketch, "E4056", {"start": v(159.1, -68.03) * mm, "end": v(158.96, -68.16) * mm});
            skLineSegment(sketch, "E4057", {"start": v(158.96, -68.16) * mm, "end": v(158.8, -68.27) * mm});
            skLineSegment(sketch, "E4058", {"start": v(158.8, -68.27) * mm, "end": v(158.64, -68.36) * mm});
            skLineSegment(sketch, "E4059", {"start": v(158.64, -68.36) * mm, "end": v(158.46, -68.43) * mm});
            skLineSegment(sketch, "E4060", {"start": v(158.46, -68.43) * mm, "end": v(158.28, -68.47) * mm});
            skLineSegment(sketch, "E4061", {"start": v(158.28, -68.47) * mm, "end": v(158.1, -68.5) * mm});
            skLineSegment(sketch, "E4062", {"start": v(158.1, -68.5) * mm, "end": v(157.9, -68.5) * mm});
            skLineSegment(sketch, "E4063", {"start": v(141.9, -68.5) * mm, "end": v(141.72, -68.47) * mm});
            skLineSegment(sketch, "E4064", {"start": v(141.72, -68.47) * mm, "end": v(141.54, -68.43) * mm});
            skLineSegment(sketch, "E4065", {"start": v(141.54, -68.43) * mm, "end": v(141.36, -68.36) * mm});
            skLineSegment(sketch, "E4066", {"start": v(141.36, -68.36) * mm, "end": v(141.2, -68.27) * mm});
            skLineSegment(sketch, "E4067", {"start": v(141.2, -68.27) * mm, "end": v(141.04, -68.16) * mm});
            skLineSegment(sketch, "E4068", {"start": v(141.04, -68.16) * mm, "end": v(140.9, -68.03) * mm});
            skLineSegment(sketch, "E4069", {"start": v(140.9, -68.03) * mm, "end": v(140.79, -67.88) * mm});
            skLineSegment(sketch, "E4070", {"start": v(140.79, -67.88) * mm, "end": v(140.69, -67.72) * mm});
            skLineSegment(sketch, "E4071", {"start": v(140.69, -67.72) * mm, "end": v(140.6, -67.55) * mm});
            skLineSegment(sketch, "E4072", {"start": v(140.6, -67.55) * mm, "end": v(140.55, -67.37) * mm});
            skLineSegment(sketch, "E4073", {"start": v(140.55, -67.37) * mm, "end": v(140.51, -67.19) * mm});
            skLineSegment(sketch, "E4074", {"start": v(140.51, -67.19) * mm, "end": v(140.5, -67) * mm});
            skLineSegment(sketch, "E4075", {"start": v(140.5, -67) * mm, "end": v(140.51, -66.81) * mm});
            skLineSegment(sketch, "E4076", {"start": v(140.51, -66.81) * mm, "end": v(140.55, -66.63) * mm});
            skLineSegment(sketch, "E4077", {"start": v(140.55, -66.63) * mm, "end": v(140.6, -66.45) * mm});
            skLineSegment(sketch, "E4078", {"start": v(140.6, -66.45) * mm, "end": v(140.69, -66.28) * mm});
            skLineSegment(sketch, "E4079", {"start": v(140.69, -66.28) * mm, "end": v(140.79, -66.12) * mm});
            skLineSegment(sketch, "E4080", {"start": v(140.79, -66.12) * mm, "end": v(140.9, -65.97) * mm});
            skLineSegment(sketch, "E4081", {"start": v(140.9, -65.97) * mm, "end": v(141.04, -65.84) * mm});
            skLineSegment(sketch, "E4082", {"start": v(141.04, -65.84) * mm, "end": v(141.2, -65.73) * mm});
            skLineSegment(sketch, "E4083", {"start": v(141.2, -65.73) * mm, "end": v(141.36, -65.64) * mm});
            skLineSegment(sketch, "E4084", {"start": v(141.36, -65.64) * mm, "end": v(141.54, -65.57) * mm});
            skLineSegment(sketch, "E4085", {"start": v(141.54, -65.57) * mm, "end": v(141.72, -65.53) * mm});
            skLineSegment(sketch, "E4086", {"start": v(141.72, -65.53) * mm, "end": v(141.9, -65.5) * mm});
            skLineSegment(sketch, "E4087", {"start": v(141.9, -65.5) * mm, "end": v(142.1, -65.5) * mm});
            skLineSegment(sketch, "E4088", {"start": v(142.1, -65.5) * mm, "end": v(142.28, -65.53) * mm});
            skLineSegment(sketch, "E4089", {"start": v(142.28, -65.53) * mm, "end": v(142.46, -65.57) * mm});
            skLineSegment(sketch, "E4090", {"start": v(142.46, -65.57) * mm, "end": v(142.64, -65.64) * mm});
            skLineSegment(sketch, "E4091", {"start": v(142.64, -65.64) * mm, "end": v(142.8, -65.73) * mm});
            skLineSegment(sketch, "E4092", {"start": v(142.8, -65.73) * mm, "end": v(142.96, -65.84) * mm});
            skLineSegment(sketch, "E4093", {"start": v(142.96, -65.84) * mm, "end": v(143.1, -65.97) * mm});
            skLineSegment(sketch, "E4094", {"start": v(143.1, -65.97) * mm, "end": v(143.21, -66.12) * mm});
            skLineSegment(sketch, "E4095", {"start": v(143.21, -66.12) * mm, "end": v(143.31, -66.28) * mm});
            skLineSegment(sketch, "E4096", {"start": v(143.31, -66.28) * mm, "end": v(143.4, -66.45) * mm});
            skLineSegment(sketch, "E4097", {"start": v(143.4, -66.45) * mm, "end": v(143.45, -66.63) * mm});
            skLineSegment(sketch, "E4098", {"start": v(143.45, -66.63) * mm, "end": v(143.49, -66.81) * mm});
            skLineSegment(sketch, "E4099", {"start": v(143.49, -66.81) * mm, "end": v(143.5, -67) * mm});
            skLineSegment(sketch, "E4100", {"start": v(143.5, -67) * mm, "end": v(143.49, -67.19) * mm});
            skLineSegment(sketch, "E4101", {"start": v(143.49, -67.19) * mm, "end": v(143.45, -67.37) * mm});
            skLineSegment(sketch, "E4102", {"start": v(143.45, -67.37) * mm, "end": v(143.4, -67.55) * mm});
            skLineSegment(sketch, "E4103", {"start": v(143.4, -67.55) * mm, "end": v(143.31, -67.72) * mm});
            skLineSegment(sketch, "E4104", {"start": v(143.31, -67.72) * mm, "end": v(143.21, -67.88) * mm});
            skLineSegment(sketch, "E4105", {"start": v(143.21, -67.88) * mm, "end": v(143.1, -68.03) * mm});
            skLineSegment(sketch, "E4106", {"start": v(143.1, -68.03) * mm, "end": v(142.96, -68.16) * mm});
            skLineSegment(sketch, "E4107", {"start": v(142.96, -68.16) * mm, "end": v(142.8, -68.27) * mm});
            skLineSegment(sketch, "E4108", {"start": v(142.8, -68.27) * mm, "end": v(142.64, -68.36) * mm});
            skLineSegment(sketch, "E4109", {"start": v(142.64, -68.36) * mm, "end": v(142.46, -68.43) * mm});
            skLineSegment(sketch, "E4110", {"start": v(142.46, -68.43) * mm, "end": v(142.28, -68.47) * mm});
            skLineSegment(sketch, "E4111", {"start": v(142.28, -68.47) * mm, "end": v(142.1, -68.5) * mm});
            skLineSegment(sketch, "E4112", {"start": v(142.1, -68.5) * mm, "end": v(141.9, -68.5) * mm});
            skLineSegment(sketch, "E4113", {"start": v(267.9, -68.5) * mm, "end": v(267.72, -68.47) * mm});
            skLineSegment(sketch, "E4114", {"start": v(267.72, -68.47) * mm, "end": v(267.54, -68.43) * mm});
            skLineSegment(sketch, "E4115", {"start": v(267.54, -68.43) * mm, "end": v(267.36, -68.36) * mm});
            skLineSegment(sketch, "E4116", {"start": v(267.36, -68.36) * mm, "end": v(267.2, -68.27) * mm});
            skLineSegment(sketch, "E4117", {"start": v(267.2, -68.27) * mm, "end": v(267.04, -68.16) * mm});
            skLineSegment(sketch, "E4118", {"start": v(267.04, -68.16) * mm, "end": v(266.9, -68.03) * mm});
            skLineSegment(sketch, "E4119", {"start": v(266.9, -68.03) * mm, "end": v(266.79, -67.88) * mm});
            skLineSegment(sketch, "E4120", {"start": v(266.79, -67.88) * mm, "end": v(266.69, -67.72) * mm});
            skLineSegment(sketch, "E4121", {"start": v(266.69, -67.72) * mm, "end": v(266.6, -67.55) * mm});
            skLineSegment(sketch, "E4122", {"start": v(266.6, -67.55) * mm, "end": v(266.55, -67.37) * mm});
            skLineSegment(sketch, "E4123", {"start": v(266.55, -67.37) * mm, "end": v(266.51, -67.19) * mm});
            skLineSegment(sketch, "E4124", {"start": v(266.51, -67.19) * mm, "end": v(266.5, -67) * mm});
            skLineSegment(sketch, "E4125", {"start": v(266.5, -67) * mm, "end": v(266.51, -66.81) * mm});
            skLineSegment(sketch, "E4126", {"start": v(266.51, -66.81) * mm, "end": v(266.55, -66.63) * mm});
            skLineSegment(sketch, "E4127", {"start": v(266.55, -66.63) * mm, "end": v(266.6, -66.45) * mm});
            skLineSegment(sketch, "E4128", {"start": v(266.6, -66.45) * mm, "end": v(266.69, -66.28) * mm});
            skLineSegment(sketch, "E4129", {"start": v(266.69, -66.28) * mm, "end": v(266.79, -66.12) * mm});
            skLineSegment(sketch, "E4130", {"start": v(266.79, -66.12) * mm, "end": v(266.9, -65.97) * mm});
            skLineSegment(sketch, "E4131", {"start": v(266.9, -65.97) * mm, "end": v(267.04, -65.84) * mm});
            skLineSegment(sketch, "E4132", {"start": v(267.04, -65.84) * mm, "end": v(267.2, -65.73) * mm});
            skLineSegment(sketch, "E4133", {"start": v(267.2, -65.73) * mm, "end": v(267.36, -65.64) * mm});
            skLineSegment(sketch, "E4134", {"start": v(267.36, -65.64) * mm, "end": v(267.54, -65.57) * mm});
            skLineSegment(sketch, "E4135", {"start": v(267.54, -65.57) * mm, "end": v(267.72, -65.53) * mm});
            skLineSegment(sketch, "E4136", {"start": v(267.72, -65.53) * mm, "end": v(267.9, -65.5) * mm});
            skLineSegment(sketch, "E4137", {"start": v(267.9, -65.5) * mm, "end": v(268.1, -65.5) * mm});
            skLineSegment(sketch, "E4138", {"start": v(268.1, -65.5) * mm, "end": v(268.28, -65.53) * mm});
            skLineSegment(sketch, "E4139", {"start": v(268.28, -65.53) * mm, "end": v(268.46, -65.57) * mm});
            skLineSegment(sketch, "E4140", {"start": v(268.46, -65.57) * mm, "end": v(268.64, -65.64) * mm});
            skLineSegment(sketch, "E4141", {"start": v(268.64, -65.64) * mm, "end": v(268.8, -65.73) * mm});
            skLineSegment(sketch, "E4142", {"start": v(268.8, -65.73) * mm, "end": v(268.96, -65.84) * mm});
            skLineSegment(sketch, "E4143", {"start": v(268.96, -65.84) * mm, "end": v(269.1, -65.97) * mm});
            skLineSegment(sketch, "E4144", {"start": v(269.1, -65.97) * mm, "end": v(269.21, -66.12) * mm});
            skLineSegment(sketch, "E4145", {"start": v(269.21, -66.12) * mm, "end": v(269.31, -66.28) * mm});
            skLineSegment(sketch, "E4146", {"start": v(269.31, -66.28) * mm, "end": v(269.4, -66.45) * mm});
            skLineSegment(sketch, "E4147", {"start": v(269.4, -66.45) * mm, "end": v(269.45, -66.63) * mm});
            skLineSegment(sketch, "E4148", {"start": v(269.45, -66.63) * mm, "end": v(269.49, -66.81) * mm});
            skLineSegment(sketch, "E4149", {"start": v(269.49, -66.81) * mm, "end": v(269.5, -67) * mm});
            skLineSegment(sketch, "E4150", {"start": v(269.5, -67) * mm, "end": v(269.49, -67.19) * mm});
            skLineSegment(sketch, "E4151", {"start": v(269.49, -67.19) * mm, "end": v(269.45, -67.37) * mm});
            skLineSegment(sketch, "E4152", {"start": v(269.45, -67.37) * mm, "end": v(269.4, -67.55) * mm});
            skLineSegment(sketch, "E4153", {"start": v(269.4, -67.55) * mm, "end": v(269.31, -67.72) * mm});
            skLineSegment(sketch, "E4154", {"start": v(269.31, -67.72) * mm, "end": v(269.21, -67.88) * mm});
            skLineSegment(sketch, "E4155", {"start": v(269.21, -67.88) * mm, "end": v(269.1, -68.03) * mm});
            skLineSegment(sketch, "E4156", {"start": v(269.1, -68.03) * mm, "end": v(268.96, -68.16) * mm});
            skLineSegment(sketch, "E4157", {"start": v(268.96, -68.16) * mm, "end": v(268.8, -68.27) * mm});
            skLineSegment(sketch, "E4158", {"start": v(268.8, -68.27) * mm, "end": v(268.64, -68.36) * mm});
            skLineSegment(sketch, "E4159", {"start": v(268.64, -68.36) * mm, "end": v(268.46, -68.43) * mm});
            skLineSegment(sketch, "E4160", {"start": v(268.46, -68.43) * mm, "end": v(268.28, -68.47) * mm});
            skLineSegment(sketch, "E4161", {"start": v(268.28, -68.47) * mm, "end": v(268.1, -68.5) * mm});
            skLineSegment(sketch, "E4162", {"start": v(268.1, -68.5) * mm, "end": v(267.9, -68.5) * mm});
            skLineSegment(sketch, "E4163", {"start": v(251.9, -68.5) * mm, "end": v(251.72, -68.47) * mm});
            skLineSegment(sketch, "E4164", {"start": v(251.72, -68.47) * mm, "end": v(251.54, -68.43) * mm});
            skLineSegment(sketch, "E4165", {"start": v(251.54, -68.43) * mm, "end": v(251.36, -68.36) * mm});
            skLineSegment(sketch, "E4166", {"start": v(251.36, -68.36) * mm, "end": v(251.2, -68.27) * mm});
            skLineSegment(sketch, "E4167", {"start": v(251.2, -68.27) * mm, "end": v(251.04, -68.16) * mm});
            skLineSegment(sketch, "E4168", {"start": v(251.04, -68.16) * mm, "end": v(250.9, -68.03) * mm});
            skLineSegment(sketch, "E4169", {"start": v(250.9, -68.03) * mm, "end": v(250.79, -67.88) * mm});
            skLineSegment(sketch, "E4170", {"start": v(250.79, -67.88) * mm, "end": v(250.69, -67.72) * mm});
            skLineSegment(sketch, "E4171", {"start": v(250.69, -67.72) * mm, "end": v(250.6, -67.55) * mm});
            skLineSegment(sketch, "E4172", {"start": v(250.6, -67.55) * mm, "end": v(250.55, -67.37) * mm});
            skLineSegment(sketch, "E4173", {"start": v(250.55, -67.37) * mm, "end": v(250.51, -67.19) * mm});
            skLineSegment(sketch, "E4174", {"start": v(250.51, -67.19) * mm, "end": v(250.5, -67) * mm});
            skLineSegment(sketch, "E4175", {"start": v(250.5, -67) * mm, "end": v(250.51, -66.81) * mm});
            skLineSegment(sketch, "E4176", {"start": v(250.51, -66.81) * mm, "end": v(250.55, -66.63) * mm});
            skLineSegment(sketch, "E4177", {"start": v(250.55, -66.63) * mm, "end": v(250.6, -66.45) * mm});
            skLineSegment(sketch, "E4178", {"start": v(250.6, -66.45) * mm, "end": v(250.69, -66.28) * mm});
            skLineSegment(sketch, "E4179", {"start": v(250.69, -66.28) * mm, "end": v(250.79, -66.12) * mm});
            skLineSegment(sketch, "E4180", {"start": v(250.79, -66.12) * mm, "end": v(250.9, -65.97) * mm});
            skLineSegment(sketch, "E4181", {"start": v(250.9, -65.97) * mm, "end": v(251.04, -65.84) * mm});
            skLineSegment(sketch, "E4182", {"start": v(251.04, -65.84) * mm, "end": v(251.2, -65.73) * mm});
            skLineSegment(sketch, "E4183", {"start": v(251.2, -65.73) * mm, "end": v(251.36, -65.64) * mm});
            skLineSegment(sketch, "E4184", {"start": v(251.36, -65.64) * mm, "end": v(251.54, -65.57) * mm});
            skLineSegment(sketch, "E4185", {"start": v(251.54, -65.57) * mm, "end": v(251.72, -65.53) * mm});
            skLineSegment(sketch, "E4186", {"start": v(251.72, -65.53) * mm, "end": v(251.9, -65.5) * mm});
            skLineSegment(sketch, "E4187", {"start": v(251.9, -65.5) * mm, "end": v(252.1, -65.5) * mm});
            skLineSegment(sketch, "E4188", {"start": v(252.1, -65.5) * mm, "end": v(252.28, -65.53) * mm});
            skLineSegment(sketch, "E4189", {"start": v(252.28, -65.53) * mm, "end": v(252.46, -65.57) * mm});
            skLineSegment(sketch, "E4190", {"start": v(252.46, -65.57) * mm, "end": v(252.64, -65.64) * mm});
            skLineSegment(sketch, "E4191", {"start": v(252.64, -65.64) * mm, "end": v(252.8, -65.73) * mm});
            skLineSegment(sketch, "E4192", {"start": v(252.8, -65.73) * mm, "end": v(252.96, -65.84) * mm});
            skLineSegment(sketch, "E4193", {"start": v(252.96, -65.84) * mm, "end": v(253.1, -65.97) * mm});
            skLineSegment(sketch, "E4194", {"start": v(253.1, -65.97) * mm, "end": v(253.21, -66.12) * mm});
            skLineSegment(sketch, "E4195", {"start": v(253.21, -66.12) * mm, "end": v(253.31, -66.28) * mm});
            skLineSegment(sketch, "E4196", {"start": v(253.31, -66.28) * mm, "end": v(253.4, -66.45) * mm});
            skLineSegment(sketch, "E4197", {"start": v(253.4, -66.45) * mm, "end": v(253.45, -66.63) * mm});
            skLineSegment(sketch, "E4198", {"start": v(253.45, -66.63) * mm, "end": v(253.49, -66.81) * mm});
            skLineSegment(sketch, "E4199", {"start": v(253.49, -66.81) * mm, "end": v(253.5, -67) * mm});
            skLineSegment(sketch, "E4200", {"start": v(253.5, -67) * mm, "end": v(253.49, -67.19) * mm});
            skLineSegment(sketch, "E4201", {"start": v(253.49, -67.19) * mm, "end": v(253.45, -67.37) * mm});
            skLineSegment(sketch, "E4202", {"start": v(253.45, -67.37) * mm, "end": v(253.4, -67.55) * mm});
            skLineSegment(sketch, "E4203", {"start": v(253.4, -67.55) * mm, "end": v(253.31, -67.72) * mm});
            skLineSegment(sketch, "E4204", {"start": v(253.31, -67.72) * mm, "end": v(253.21, -67.88) * mm});
            skLineSegment(sketch, "E4205", {"start": v(253.21, -67.88) * mm, "end": v(253.1, -68.03) * mm});
            skLineSegment(sketch, "E4206", {"start": v(253.1, -68.03) * mm, "end": v(252.96, -68.16) * mm});
            skLineSegment(sketch, "E4207", {"start": v(252.96, -68.16) * mm, "end": v(252.8, -68.27) * mm});
            skLineSegment(sketch, "E4208", {"start": v(252.8, -68.27) * mm, "end": v(252.64, -68.36) * mm});
            skLineSegment(sketch, "E4209", {"start": v(252.64, -68.36) * mm, "end": v(252.46, -68.43) * mm});
            skLineSegment(sketch, "E4210", {"start": v(252.46, -68.43) * mm, "end": v(252.28, -68.47) * mm});
            skLineSegment(sketch, "E4211", {"start": v(252.28, -68.47) * mm, "end": v(252.1, -68.5) * mm});
            skLineSegment(sketch, "E4212", {"start": v(252.1, -68.5) * mm, "end": v(251.9, -68.5) * mm});
            skLineSegment(sketch, "E4213", {"start": v(220.4, -75) * mm, "end": v(220.32, -74.99) * mm});
            skLineSegment(sketch, "E4214", {"start": v(220.32, -74.99) * mm, "end": v(220.22, -74.97) * mm});
            skLineSegment(sketch, "E4215", {"start": v(220.22, -74.97) * mm, "end": v(220.19, -74.97) * mm});
            skLineSegment(sketch, "E4216", {"start": v(220.19, -74.97) * mm, "end": v(220.06, -74.93) * mm});
            skLineSegment(sketch, "E4217", {"start": v(220.06, -74.93) * mm, "end": v(219.93, -74.89) * mm});
            skLineSegment(sketch, "E4218", {"start": v(219.93, -74.89) * mm, "end": v(219.86, -74.86) * mm});
            skLineSegment(sketch, "E4219", {"start": v(219.86, -74.86) * mm, "end": v(219.8, -74.83) * mm});
            skLineSegment(sketch, "E4220", {"start": v(219.8, -74.83) * mm, "end": v(219.7, -74.77) * mm});
            skLineSegment(sketch, "E4221", {"start": v(219.7, -74.77) * mm, "end": v(219.59, -74.69) * mm});
            skLineSegment(sketch, "E4222", {"start": v(219.59, -74.69) * mm, "end": v(219.54, -74.66) * mm});
            skLineSegment(sketch, "E4223", {"start": v(219.54, -74.66) * mm, "end": v(219.48, -74.6) * mm});
            skLineSegment(sketch, "E4224", {"start": v(219.48, -74.6) * mm, "end": v(219.4, -74.53) * mm});
            skLineSegment(sketch, "E4225", {"start": v(219.4, -74.53) * mm, "end": v(219.38, -74.5) * mm});
            skLineSegment(sketch, "E4226", {"start": v(219.38, -74.5) * mm, "end": v(219.3, -74.4) * mm});
            skLineSegment(sketch, "E4227", {"start": v(219.3, -74.4) * mm, "end": v(219.22, -74.3) * mm});
            skLineSegment(sketch, "E4228", {"start": v(219.22, -74.3) * mm, "end": v(219.2, -74.25) * mm});
            skLineSegment(sketch, "E4229", {"start": v(219.2, -74.25) * mm, "end": v(219.19, -74.22) * mm});
            skLineSegment(sketch, "E4230", {"start": v(219.19, -74.22) * mm, "end": v(219.16, -74.17) * mm});
            skLineSegment(sketch, "E4231", {"start": v(219.16, -74.17) * mm, "end": v(219.1, -74.05) * mm});
            skLineSegment(sketch, "E4232", {"start": v(219.1, -74.05) * mm, "end": v(219.06, -73.92) * mm});
            skLineSegment(sketch, "E4233", {"start": v(219.06, -73.92) * mm, "end": v(219.05, -73.87) * mm});
            skLineSegment(sketch, "E4234", {"start": v(219.05, -73.87) * mm, "end": v(219.03, -73.8) * mm});
            skLineSegment(sketch, "E4235", {"start": v(219.03, -73.8) * mm, "end": v(219.01, -73.69) * mm});
            skLineSegment(sketch, "E4236", {"start": v(219.01, -73.69) * mm, "end": v(219, -73.66) * mm});
            skLineSegment(sketch, "E4237", {"start": v(219, -73.66) * mm, "end": v(219, -73.53) * mm});
            skLineSegment(sketch, "E4238", {"start": v(219, -73.53) * mm, "end": v(219, -73.39) * mm});
            skLineSegment(sketch, "E4239", {"start": v(219, -73.39) * mm, "end": v(219, -73.34) * mm});
            skLineSegment(sketch, "E4240", {"start": v(219, -73.34) * mm, "end": v(219.01, -73.31) * mm});
            skLineSegment(sketch, "E4241", {"start": v(219.01, -73.31) * mm, "end": v(219.02, -73.25) * mm});
            skLineSegment(sketch, "E4242", {"start": v(219.02, -73.25) * mm, "end": v(219.05, -73.13) * mm});
            skLineSegment(sketch, "E4243", {"start": v(219.05, -73.13) * mm, "end": v(219.09, -73) * mm});
            skLineSegment(sketch, "E4244", {"start": v(219.09, -73) * mm, "end": v(219.1, -72.95) * mm});
            skLineSegment(sketch, "E4245", {"start": v(219.1, -72.95) * mm, "end": v(219.14, -72.87) * mm});
            skLineSegment(sketch, "E4246", {"start": v(219.14, -72.87) * mm, "end": v(219.19, -72.78) * mm});
            skLineSegment(sketch, "E4247", {"start": v(219.19, -72.78) * mm, "end": v(219.2, -72.75) * mm});
            skLineSegment(sketch, "E4248", {"start": v(219.2, -72.75) * mm, "end": v(219.27, -72.64) * mm});
            skLineSegment(sketch, "E4249", {"start": v(219.27, -72.64) * mm, "end": v(219.35, -72.53) * mm});
            skLineSegment(sketch, "E4250", {"start": v(219.35, -72.53) * mm, "end": v(219.4, -72.47) * mm});
            skLineSegment(sketch, "E4251", {"start": v(219.4, -72.47) * mm, "end": v(219.45, -72.43) * mm});
            skLineSegment(sketch, "E4252", {"start": v(219.45, -72.43) * mm, "end": v(219.54, -72.34) * mm});
            skLineSegment(sketch, "E4253", {"start": v(219.54, -72.34) * mm, "end": v(219.65, -72.26) * mm});
            skLineSegment(sketch, "E4254", {"start": v(219.65, -72.26) * mm, "end": v(219.7, -72.23) * mm});
            skLineSegment(sketch, "E4255", {"start": v(219.7, -72.23) * mm, "end": v(219.77, -72.2) * mm});
            skLineSegment(sketch, "E4256", {"start": v(219.77, -72.2) * mm, "end": v(219.86, -72.14) * mm});
            skLineSegment(sketch, "E4257", {"start": v(219.86, -72.14) * mm, "end": v(219.9, -72.13) * mm});
            skLineSegment(sketch, "E4258", {"start": v(219.9, -72.13) * mm, "end": v(220.01, -72.08) * mm});
            skLineSegment(sketch, "E4259", {"start": v(220.01, -72.08) * mm, "end": v(220.14, -72.04) * mm});
            skLineSegment(sketch, "E4260", {"start": v(220.14, -72.04) * mm, "end": v(220.22, -72.03) * mm});
            skLineSegment(sketch, "E4261", {"start": v(220.22, -72.03) * mm, "end": v(220.28, -72.02) * mm});
            skLineSegment(sketch, "E4262", {"start": v(220.28, -72.02) * mm, "end": v(220.4, -72) * mm});
            skLineSegment(sketch, "E4263", {"start": v(220.4, -72) * mm, "end": v(220.54, -72) * mm});
            skLineSegment(sketch, "E4264", {"start": v(220.54, -72) * mm, "end": v(220.6, -72) * mm});
            skLineSegment(sketch, "E4265", {"start": v(220.6, -72) * mm, "end": v(220.68, -72.01) * mm});
            skLineSegment(sketch, "E4266", {"start": v(220.68, -72.01) * mm, "end": v(220.78, -72.03) * mm});
            skLineSegment(sketch, "E4267", {"start": v(220.78, -72.03) * mm, "end": v(220.81, -72.03) * mm});
            skLineSegment(sketch, "E4268", {"start": v(220.81, -72.03) * mm, "end": v(220.94, -72.07) * mm});
            skLineSegment(sketch, "E4269", {"start": v(220.94, -72.07) * mm, "end": v(221.07, -72.11) * mm});
            skLineSegment(sketch, "E4270", {"start": v(221.07, -72.11) * mm, "end": v(221.14, -72.14) * mm});
            skLineSegment(sketch, "E4271", {"start": v(221.14, -72.14) * mm, "end": v(221.2, -72.17) * mm});
            skLineSegment(sketch, "E4272", {"start": v(221.2, -72.17) * mm, "end": v(221.3, -72.23) * mm});
            skLineSegment(sketch, "E4273", {"start": v(221.3, -72.23) * mm, "end": v(221.41, -72.31) * mm});
            skLineSegment(sketch, "E4274", {"start": v(221.41, -72.31) * mm, "end": v(221.46, -72.34) * mm});
            skLineSegment(sketch, "E4275", {"start": v(221.46, -72.34) * mm, "end": v(221.52, -72.4) * mm});
            skLineSegment(sketch, "E4276", {"start": v(221.52, -72.4) * mm, "end": v(221.6, -72.47) * mm});
            skLineSegment(sketch, "E4277", {"start": v(221.6, -72.47) * mm, "end": v(221.62, -72.5) * mm});
            skLineSegment(sketch, "E4278", {"start": v(221.62, -72.5) * mm, "end": v(221.7, -72.6) * mm});
            skLineSegment(sketch, "E4279", {"start": v(221.7, -72.6) * mm, "end": v(221.78, -72.7) * mm});
            skLineSegment(sketch, "E4280", {"start": v(221.78, -72.7) * mm, "end": v(221.81, -72.78) * mm});
            skLineSegment(sketch, "E4281", {"start": v(221.81, -72.78) * mm, "end": v(221.84, -72.83) * mm});
            skLineSegment(sketch, "E4282", {"start": v(221.84, -72.83) * mm, "end": v(221.9, -72.95) * mm});
            skLineSegment(sketch, "E4283", {"start": v(221.9, -72.95) * mm, "end": v(221.94, -73.08) * mm});
            skLineSegment(sketch, "E4284", {"start": v(221.94, -73.08) * mm, "end": v(221.95, -73.13) * mm});
            skLineSegment(sketch, "E4285", {"start": v(221.95, -73.13) * mm, "end": v(221.97, -73.2) * mm});
            skLineSegment(sketch, "E4286", {"start": v(221.97, -73.2) * mm, "end": v(221.99, -73.31) * mm});
            skLineSegment(sketch, "E4287", {"start": v(221.99, -73.31) * mm, "end": v(222, -73.34) * mm});
            skLineSegment(sketch, "E4288", {"start": v(222, -73.34) * mm, "end": v(222, -73.47) * mm});
            skLineSegment(sketch, "E4289", {"start": v(222, -73.47) * mm, "end": v(222, -73.61) * mm});
            skLineSegment(sketch, "E4290", {"start": v(222, -73.61) * mm, "end": v(221.99, -73.69) * mm});
            skLineSegment(sketch, "E4291", {"start": v(221.99, -73.69) * mm, "end": v(221.98, -73.75) * mm});
            skLineSegment(sketch, "E4292", {"start": v(221.98, -73.75) * mm, "end": v(221.95, -73.87) * mm});
            skLineSegment(sketch, "E4293", {"start": v(221.95, -73.87) * mm, "end": v(221.91, -74) * mm});
            skLineSegment(sketch, "E4294", {"start": v(221.91, -74) * mm, "end": v(221.9, -74.05) * mm});
            skLineSegment(sketch, "E4295", {"start": v(221.9, -74.05) * mm, "end": v(221.86, -74.13) * mm});
            skLineSegment(sketch, "E4296", {"start": v(221.86, -74.13) * mm, "end": v(221.81, -74.22) * mm});
            skLineSegment(sketch, "E4297", {"start": v(221.81, -74.22) * mm, "end": v(221.8, -74.25) * mm});
            skLineSegment(sketch, "E4298", {"start": v(221.8, -74.25) * mm, "end": v(221.73, -74.36) * mm});
            skLineSegment(sketch, "E4299", {"start": v(221.73, -74.36) * mm, "end": v(221.65, -74.47) * mm});
            skLineSegment(sketch, "E4300", {"start": v(221.65, -74.47) * mm, "end": v(221.6, -74.53) * mm});
            skLineSegment(sketch, "E4301", {"start": v(221.6, -74.53) * mm, "end": v(221.55, -74.57) * mm});
            skLineSegment(sketch, "E4302", {"start": v(221.55, -74.57) * mm, "end": v(221.46, -74.66) * mm});
            skLineSegment(sketch, "E4303", {"start": v(221.46, -74.66) * mm, "end": v(221.35, -74.74) * mm});
            skLineSegment(sketch, "E4304", {"start": v(221.35, -74.74) * mm, "end": v(221.3, -74.77) * mm});
            skLineSegment(sketch, "E4305", {"start": v(221.3, -74.77) * mm, "end": v(221.23, -74.8) * mm});
            skLineSegment(sketch, "E4306", {"start": v(221.23, -74.8) * mm, "end": v(221.14, -74.86) * mm});
            skLineSegment(sketch, "E4307", {"start": v(221.14, -74.86) * mm, "end": v(221.11, -74.87) * mm});
            skLineSegment(sketch, "E4308", {"start": v(221.11, -74.87) * mm, "end": v(220.99, -74.92) * mm});
            skLineSegment(sketch, "E4309", {"start": v(220.99, -74.92) * mm, "end": v(220.86, -74.96) * mm});
            skLineSegment(sketch, "E4310", {"start": v(220.86, -74.96) * mm, "end": v(220.8, -74.97) * mm});
            skLineSegment(sketch, "E4311", {"start": v(220.8, -74.97) * mm, "end": v(220.78, -74.97) * mm});
            skLineSegment(sketch, "E4312", {"start": v(220.78, -74.97) * mm, "end": v(220.72, -74.98) * mm});
            skLineSegment(sketch, "E4313", {"start": v(220.72, -74.98) * mm, "end": v(220.6, -75) * mm});
            skLineSegment(sketch, "E4314", {"start": v(220.6, -75) * mm, "end": v(220.46, -75) * mm});
            skLineSegment(sketch, "E4315", {"start": v(220.46, -75) * mm, "end": v(220.4, -75) * mm});
            skLineSegment(sketch, "E4316", {"start": v(189.54, -79.3) * mm, "end": v(189.36, -79.25) * mm});
            skLineSegment(sketch, "E4317", {"start": v(189.36, -79.25) * mm, "end": v(189.18, -79.18) * mm});
            skLineSegment(sketch, "E4318", {"start": v(189.18, -79.18) * mm, "end": v(189.02, -79.1) * mm});
            skLineSegment(sketch, "E4319", {"start": v(189.02, -79.1) * mm, "end": v(188.86, -78.98) * mm});
            skLineSegment(sketch, "E4320", {"start": v(188.86, -78.98) * mm, "end": v(188.72, -78.86) * mm});
            skLineSegment(sketch, "E4321", {"start": v(188.72, -78.86) * mm, "end": v(188.6, -78.71) * mm});
            skLineSegment(sketch, "E4322", {"start": v(188.6, -78.71) * mm, "end": v(188.5, -78.56) * mm});
            skLineSegment(sketch, "E4323", {"start": v(188.5, -78.56) * mm, "end": v(188.41, -78.39) * mm});
            skLineSegment(sketch, "E4324", {"start": v(188.41, -78.39) * mm, "end": v(188.35, -78.2) * mm});
            skLineSegment(sketch, "E4325", {"start": v(188.35, -78.2) * mm, "end": v(188.32, -78.02) * mm});
            skLineSegment(sketch, "E4326", {"start": v(188.32, -78.02) * mm, "end": v(188.3, -77.84) * mm});
            skLineSegment(sketch, "E4327", {"start": v(188.3, -77.84) * mm, "end": v(188.3, -77.74) * mm});
            skLineSegment(sketch, "E4328", {"start": v(188.3, -77.74) * mm, "end": v(188.28, -77.65) * mm});
            skLineSegment(sketch, "E4329", {"start": v(188.28, -77.65) * mm, "end": v(188.24, -77.46) * mm});
            skLineSegment(sketch, "E4330", {"start": v(188.24, -77.46) * mm, "end": v(188.23, -77.27) * mm});
            skLineSegment(sketch, "E4331", {"start": v(188.23, -77.27) * mm, "end": v(188.24, -77.18) * mm});
            skLineSegment(sketch, "E4332", {"start": v(188.24, -77.18) * mm, "end": v(188.2, -77.08) * mm});
            skLineSegment(sketch, "E4333", {"start": v(188.2, -77.08) * mm, "end": v(188.18, -76.9) * mm});
            skLineSegment(sketch, "E4334", {"start": v(188.18, -76.9) * mm, "end": v(188.17, -76.7) * mm});
            skLineSegment(sketch, "E4335", {"start": v(188.17, -76.7) * mm, "end": v(188.18, -76.61) * mm});
            skLineSegment(sketch, "E4336", {"start": v(188.18, -76.61) * mm, "end": v(188.15, -76.52) * mm});
            skLineSegment(sketch, "E4337", {"start": v(188.15, -76.52) * mm, "end": v(188.12, -76.33) * mm});
            skLineSegment(sketch, "E4338", {"start": v(188.12, -76.33) * mm, "end": v(188.12, -76.14) * mm});
            skLineSegment(sketch, "E4339", {"start": v(188.12, -76.14) * mm, "end": v(188.13, -76.05) * mm});
            skLineSegment(sketch, "E4340", {"start": v(188.13, -76.05) * mm, "end": v(188.1, -75.95) * mm});
            skLineSegment(sketch, "E4341", {"start": v(188.1, -75.95) * mm, "end": v(188.08, -75.77) * mm});
            skLineSegment(sketch, "E4342", {"start": v(188.08, -75.77) * mm, "end": v(188.08, -75.58) * mm});
            skLineSegment(sketch, "E4343", {"start": v(188.08, -75.58) * mm, "end": v(188.09, -75.48) * mm});
            skLineSegment(sketch, "E4344", {"start": v(188.09, -75.48) * mm, "end": v(188.07, -75.39) * mm});
            skLineSegment(sketch, "E4345", {"start": v(188.07, -75.39) * mm, "end": v(188.04, -75.2) * mm});
            skLineSegment(sketch, "E4346", {"start": v(188.04, -75.2) * mm, "end": v(188.05, -75.01) * mm});
            skLineSegment(sketch, "E4347", {"start": v(188.05, -75.01) * mm, "end": v(188.06, -74.92) * mm});
            skLineSegment(sketch, "E4348", {"start": v(188.06, -74.92) * mm, "end": v(188.04, -74.82) * mm});
            skLineSegment(sketch, "E4349", {"start": v(188.04, -74.82) * mm, "end": v(188.02, -74.63) * mm});
            skLineSegment(sketch, "E4350", {"start": v(188.02, -74.63) * mm, "end": v(188.03, -74.45) * mm});
            skLineSegment(sketch, "E4351", {"start": v(188.03, -74.45) * mm, "end": v(188.04, -74.35) * mm});
            skLineSegment(sketch, "E4352", {"start": v(188.04, -74.35) * mm, "end": v(188.02, -74.25) * mm});
            skLineSegment(sketch, "E4353", {"start": v(188.02, -74.25) * mm, "end": v(188, -74.07) * mm});
            skLineSegment(sketch, "E4354", {"start": v(188, -74.07) * mm, "end": v(188.01, -73.88) * mm});
            skLineSegment(sketch, "E4355", {"start": v(188.01, -73.88) * mm, "end": v(188.03, -73.78) * mm});
            skLineSegment(sketch, "E4356", {"start": v(188.03, -73.78) * mm, "end": v(188.01, -73.69) * mm});
            skLineSegment(sketch, "E4357", {"start": v(188.01, -73.69) * mm, "end": v(188, -73.5) * mm});
            skLineSegment(sketch, "E4358", {"start": v(188, -73.5) * mm, "end": v(188.01, -73.31) * mm});
            skLineSegment(sketch, "E4359", {"start": v(188.01, -73.31) * mm, "end": v(188.05, -73.13) * mm});
            skLineSegment(sketch, "E4360", {"start": v(188.05, -73.13) * mm, "end": v(188.1, -72.95) * mm});
            skLineSegment(sketch, "E4361", {"start": v(188.1, -72.95) * mm, "end": v(188.19, -72.78) * mm});
            skLineSegment(sketch, "E4362", {"start": v(188.19, -72.78) * mm, "end": v(188.29, -72.62) * mm});
            skLineSegment(sketch, "E4363", {"start": v(188.29, -72.62) * mm, "end": v(188.4, -72.47) * mm});
            skLineSegment(sketch, "E4364", {"start": v(188.4, -72.47) * mm, "end": v(188.54, -72.34) * mm});
            skLineSegment(sketch, "E4365", {"start": v(188.54, -72.34) * mm, "end": v(188.7, -72.23) * mm});
            skLineSegment(sketch, "E4366", {"start": v(188.7, -72.23) * mm, "end": v(188.86, -72.14) * mm});
            skLineSegment(sketch, "E4367", {"start": v(188.86, -72.14) * mm, "end": v(189.04, -72.07) * mm});
            skLineSegment(sketch, "E4368", {"start": v(189.04, -72.07) * mm, "end": v(189.22, -72.03) * mm});
            skLineSegment(sketch, "E4369", {"start": v(189.22, -72.03) * mm, "end": v(189.4, -72) * mm});
            skLineSegment(sketch, "E4370", {"start": v(189.4, -72) * mm, "end": v(189.6, -72) * mm});
            skLineSegment(sketch, "E4371", {"start": v(189.6, -72) * mm, "end": v(189.78, -72.03) * mm});
            skLineSegment(sketch, "E4372", {"start": v(189.78, -72.03) * mm, "end": v(189.96, -72.07) * mm});
            skLineSegment(sketch, "E4373", {"start": v(189.96, -72.07) * mm, "end": v(190.14, -72.14) * mm});
            skLineSegment(sketch, "E4374", {"start": v(190.14, -72.14) * mm, "end": v(190.3, -72.23) * mm});
            skLineSegment(sketch, "E4375", {"start": v(190.3, -72.23) * mm, "end": v(190.46, -72.34) * mm});
            skLineSegment(sketch, "E4376", {"start": v(190.46, -72.34) * mm, "end": v(190.6, -72.47) * mm});
            skLineSegment(sketch, "E4377", {"start": v(190.6, -72.47) * mm, "end": v(190.71, -72.62) * mm});
            skLineSegment(sketch, "E4378", {"start": v(190.71, -72.62) * mm, "end": v(190.81, -72.78) * mm});
            skLineSegment(sketch, "E4379", {"start": v(190.81, -72.78) * mm, "end": v(190.9, -72.95) * mm});
            skLineSegment(sketch, "E4380", {"start": v(190.9, -72.95) * mm, "end": v(190.95, -73.13) * mm});
            skLineSegment(sketch, "E4381", {"start": v(190.95, -73.13) * mm, "end": v(190.99, -73.31) * mm});
            skLineSegment(sketch, "E4382", {"start": v(190.99, -73.31) * mm, "end": v(191, -73.5) * mm});
            skLineSegment(sketch, "E4383", {"start": v(191, -73.5) * mm, "end": v(190.99, -73.69) * mm});
            skLineSegment(sketch, "E4384", {"start": v(190.99, -73.69) * mm, "end": v(190.97, -73.76) * mm});
            skLineSegment(sketch, "E4385", {"start": v(190.97, -73.76) * mm, "end": v(190.99, -73.83) * mm});
            skLineSegment(sketch, "E4386", {"start": v(190.99, -73.83) * mm, "end": v(191, -74.02) * mm});
            skLineSegment(sketch, "E4387", {"start": v(191, -74.02) * mm, "end": v(191, -74.2) * mm});
            skLineSegment(sketch, "E4388", {"start": v(191, -74.2) * mm, "end": v(190.98, -74.27) * mm});
            skLineSegment(sketch, "E4389", {"start": v(190.98, -74.27) * mm, "end": v(191, -74.34) * mm});
            skLineSegment(sketch, "E4390", {"start": v(191, -74.34) * mm, "end": v(191.02, -74.53) * mm});
            skLineSegment(sketch, "E4391", {"start": v(191.02, -74.53) * mm, "end": v(191.01, -74.72) * mm});
            skLineSegment(sketch, "E4392", {"start": v(191.01, -74.72) * mm, "end": v(191, -74.79) * mm});
            skLineSegment(sketch, "E4393", {"start": v(191, -74.79) * mm, "end": v(191.02, -74.86) * mm});
            skLineSegment(sketch, "E4394", {"start": v(191.02, -74.86) * mm, "end": v(191.04, -75.04) * mm});
            skLineSegment(sketch, "E4395", {"start": v(191.04, -75.04) * mm, "end": v(191.04, -75.23) * mm});
            skLineSegment(sketch, "E4396", {"start": v(191.04, -75.23) * mm, "end": v(191.03, -75.3) * mm});
            skLineSegment(sketch, "E4397", {"start": v(191.03, -75.3) * mm, "end": v(191.05, -75.37) * mm});
            skLineSegment(sketch, "E4398", {"start": v(191.05, -75.37) * mm, "end": v(191.07, -75.56) * mm});
            skLineSegment(sketch, "E4399", {"start": v(191.07, -75.56) * mm, "end": v(191.07, -75.75) * mm});
            skLineSegment(sketch, "E4400", {"start": v(191.07, -75.75) * mm, "end": v(191.07, -75.82) * mm});
            skLineSegment(sketch, "E4401", {"start": v(191.07, -75.82) * mm, "end": v(191.08, -75.89) * mm});
            skLineSegment(sketch, "E4402", {"start": v(191.08, -75.89) * mm, "end": v(191.11, -76.07) * mm});
            skLineSegment(sketch, "E4403", {"start": v(191.11, -76.07) * mm, "end": v(191.12, -76.26) * mm});
            skLineSegment(sketch, "E4404", {"start": v(191.12, -76.26) * mm, "end": v(191.11, -76.33) * mm});
            skLineSegment(sketch, "E4405", {"start": v(191.11, -76.33) * mm, "end": v(191.13, -76.4) * mm});
            skLineSegment(sketch, "E4406", {"start": v(191.13, -76.4) * mm, "end": v(191.16, -76.58) * mm});
            skLineSegment(sketch, "E4407", {"start": v(191.16, -76.58) * mm, "end": v(191.17, -76.77) * mm});
            skLineSegment(sketch, "E4408", {"start": v(191.17, -76.77) * mm, "end": v(191.16, -76.84) * mm});
            skLineSegment(sketch, "E4409", {"start": v(191.16, -76.84) * mm, "end": v(191.19, -76.9) * mm});
            skLineSegment(sketch, "E4410", {"start": v(191.19, -76.9) * mm, "end": v(191.22, -77.1) * mm});
            skLineSegment(sketch, "E4411", {"start": v(191.22, -77.1) * mm, "end": v(191.23, -77.28) * mm});
            skLineSegment(sketch, "E4412", {"start": v(191.23, -77.28) * mm, "end": v(191.23, -77.35) * mm});
            skLineSegment(sketch, "E4413", {"start": v(191.23, -77.35) * mm, "end": v(191.25, -77.42) * mm});
            skLineSegment(sketch, "E4414", {"start": v(191.25, -77.42) * mm, "end": v(191.29, -77.6) * mm});
            skLineSegment(sketch, "E4415", {"start": v(191.29, -77.6) * mm, "end": v(191.3, -77.8) * mm});
            skLineSegment(sketch, "E4416", {"start": v(191.3, -77.8) * mm, "end": v(191.3, -77.98) * mm});
            skLineSegment(sketch, "E4417", {"start": v(191.3, -77.98) * mm, "end": v(191.26, -78.17) * mm});
            skLineSegment(sketch, "E4418", {"start": v(191.26, -78.17) * mm, "end": v(191.2, -78.35) * mm});
            skLineSegment(sketch, "E4419", {"start": v(191.2, -78.35) * mm, "end": v(191.13, -78.52) * mm});
            skLineSegment(sketch, "E4420", {"start": v(191.13, -78.52) * mm, "end": v(191.03, -78.68) * mm});
            skLineSegment(sketch, "E4421", {"start": v(191.03, -78.68) * mm, "end": v(190.9, -78.83) * mm});
            skLineSegment(sketch, "E4422", {"start": v(190.9, -78.83) * mm, "end": v(190.77, -78.96) * mm});
            skLineSegment(sketch, "E4423", {"start": v(190.77, -78.96) * mm, "end": v(190.62, -79.07) * mm});
            skLineSegment(sketch, "E4424", {"start": v(190.62, -79.07) * mm, "end": v(190.46, -79.16) * mm});
            skLineSegment(sketch, "E4425", {"start": v(190.46, -79.16) * mm, "end": v(190.28, -79.23) * mm});
            skLineSegment(sketch, "E4426", {"start": v(190.28, -79.23) * mm, "end": v(190.1, -79.28) * mm});
            skLineSegment(sketch, "E4427", {"start": v(190.1, -79.28) * mm, "end": v(189.92, -79.31) * mm});
            skLineSegment(sketch, "E4428", {"start": v(189.92, -79.31) * mm, "end": v(189.73, -79.31) * mm});
            skLineSegment(sketch, "E4429", {"start": v(189.73, -79.31) * mm, "end": v(189.54, -79.3) * mm});
            skLineSegment(sketch, "E4430", {"start": v(122, -437) * mm, "end": v(122, -436.94) * mm});
            skLineSegment(sketch, "E4431", {"start": v(122, -436.94) * mm, "end": v(120.12, -436.94) * mm});
            skLineSegment(sketch, "E4432", {"start": v(120.12, -436.94) * mm, "end": v(116.38, -436.47) * mm});
            skLineSegment(sketch, "E4433", {"start": v(116.38, -436.47) * mm, "end": v(112.73, -435.53) * mm});
            skLineSegment(sketch, "E4434", {"start": v(112.73, -435.53) * mm, "end": v(109.23, -434.14) * mm});
            skLineSegment(sketch, "E4435", {"start": v(109.23, -434.14) * mm, "end": v(105.93, -432.33) * mm});
            skLineSegment(sketch, "E4436", {"start": v(105.93, -432.33) * mm, "end": v(102.88, -430.12) * mm});
            skLineSegment(sketch, "E4437", {"start": v(102.88, -430.12) * mm, "end": v(100.13, -427.54) * mm});
            skLineSegment(sketch, "E4438", {"start": v(100.13, -427.54) * mm, "end": v(97.73, -424.63) * mm});
            skLineSegment(sketch, "E4439", {"start": v(97.73, -424.63) * mm, "end": v(95.71, -421.45) * mm});
            skLineSegment(sketch, "E4440", {"start": v(95.71, -421.45) * mm, "end": v(94.1, -418.04) * mm});
            skLineSegment(sketch, "E4441", {"start": v(94.1, -418.04) * mm, "end": v(92.94, -414.46) * mm});
            skLineSegment(sketch, "E4442", {"start": v(92.94, -414.46) * mm, "end": v(92.24, -410.76) * mm});
            skLineSegment(sketch, "E4443", {"start": v(92.24, -410.76) * mm, "end": v(92, -407) * mm});
            skLineSegment(sketch, "E4444", {"start": v(92, -407) * mm, "end": v(92, -145.4) * mm});
            skLineSegment(sketch, "E4445", {"start": v(92, -145.4) * mm, "end": v(92.02, -145.4) * mm});
            skLineSegment(sketch, "E4446", {"start": v(92.02, -145.4) * mm, "end": v(92.02, -144.77) * mm});
            skLineSegment(sketch, "E4447", {"start": v(92.02, -144.77) * mm, "end": v(92.18, -143.53) * mm});
            skLineSegment(sketch, "E4448", {"start": v(92.18, -143.53) * mm, "end": v(92.49, -142.3) * mm});
            skLineSegment(sketch, "E4449", {"start": v(92.49, -142.3) * mm, "end": v(92.95, -141.14) * mm});
            skLineSegment(sketch, "E4450", {"start": v(92.95, -141.14) * mm, "end": v(93.56, -140.04) * mm});
            skLineSegment(sketch, "E4451", {"start": v(93.56, -140.04) * mm, "end": v(94.3, -139.03) * mm});
            skLineSegment(sketch, "E4452", {"start": v(94.3, -139.03) * mm, "end": v(95.15, -138.11) * mm});
            skLineSegment(sketch, "E4453", {"start": v(95.15, -138.11) * mm, "end": v(96.12, -137.3) * mm});
            skLineSegment(sketch, "E4454", {"start": v(96.12, -137.3) * mm, "end": v(97.18, -136.64) * mm});
            skLineSegment(sketch, "E4455", {"start": v(97.18, -136.64) * mm, "end": v(98.32, -136.1) * mm});
            skLineSegment(sketch, "E4456", {"start": v(98.32, -136.1) * mm, "end": v(99.51, -135.71) * mm});
            skLineSegment(sketch, "E4457", {"start": v(99.51, -135.71) * mm, "end": v(100.75, -135.48) * mm});
            skLineSegment(sketch, "E4458", {"start": v(100.75, -135.48) * mm, "end": v(102, -135.4) * mm});
            skLineSegment(sketch, "E4459", {"start": v(102, -135.4) * mm, "end": v(108.8, -135.4) * mm});
            skLineSegment(sketch, "E4460", {"start": v(108.8, -135.4) * mm, "end": v(109.83, -135.34) * mm});
            skLineSegment(sketch, "E4461", {"start": v(109.83, -135.34) * mm, "end": v(110.84, -135.14) * mm});
            skLineSegment(sketch, "E4462", {"start": v(110.84, -135.14) * mm, "end": v(111.82, -134.82) * mm});
            skLineSegment(sketch, "E4463", {"start": v(111.82, -134.82) * mm, "end": v(112.75, -134.39) * mm});
            skLineSegment(sketch, "E4464", {"start": v(112.75, -134.39) * mm, "end": v(113.62, -133.83) * mm});
            skLineSegment(sketch, "E4465", {"start": v(113.62, -133.83) * mm, "end": v(114.41, -133.18) * mm});
            skLineSegment(sketch, "E4466", {"start": v(114.41, -133.18) * mm, "end": v(115.12, -132.43) * mm});
            skLineSegment(sketch, "E4467", {"start": v(115.12, -132.43) * mm, "end": v(115.72, -131.6) * mm});
            skLineSegment(sketch, "E4468", {"start": v(115.72, -131.6) * mm, "end": v(116.22, -130.7) * mm});
            skLineSegment(sketch, "E4469", {"start": v(116.22, -130.7) * mm, "end": v(116.6, -129.73) * mm});
            skLineSegment(sketch, "E4470", {"start": v(116.6, -129.73) * mm, "end": v(116.86, -128.74) * mm});
            skLineSegment(sketch, "E4471", {"start": v(116.86, -128.74) * mm, "end": v(116.98, -127.71) * mm});
            skLineSegment(sketch, "E4472", {"start": v(116.98, -127.71) * mm, "end": v(116.98, -127.2) * mm});
            skLineSegment(sketch, "E4473", {"start": v(116.98, -127.2) * mm, "end": v(117, -127.2) * mm});
            skLineSegment(sketch, "E4474", {"start": v(117, -127.2) * mm, "end": v(116.94, -126.17) * mm});
            skLineSegment(sketch, "E4475", {"start": v(116.94, -126.17) * mm, "end": v(116.74, -125.16) * mm});
            skLineSegment(sketch, "E4476", {"start": v(116.74, -125.16) * mm, "end": v(116.42, -124.18) * mm});
            skLineSegment(sketch, "E4477", {"start": v(116.42, -124.18) * mm, "end": v(115.99, -123.25) * mm});
            skLineSegment(sketch, "E4478", {"start": v(115.99, -123.25) * mm, "end": v(115.43, -122.38) * mm});
            skLineSegment(sketch, "E4479", {"start": v(115.43, -122.38) * mm, "end": v(114.78, -121.59) * mm});
            skLineSegment(sketch, "E4480", {"start": v(114.78, -121.59) * mm, "end": v(114.03, -120.88) * mm});
            skLineSegment(sketch, "E4481", {"start": v(114.03, -120.88) * mm, "end": v(113.2, -120.28) * mm});
            skLineSegment(sketch, "E4482", {"start": v(113.2, -120.28) * mm, "end": v(112.3, -119.78) * mm});
            skLineSegment(sketch, "E4483", {"start": v(112.3, -119.78) * mm, "end": v(111.33, -119.4) * mm});
            skLineSegment(sketch, "E4484", {"start": v(111.33, -119.4) * mm, "end": v(110.34, -119.14) * mm});
            skLineSegment(sketch, "E4485", {"start": v(110.34, -119.14) * mm, "end": v(109.31, -119.02) * mm});
            skLineSegment(sketch, "E4486", {"start": v(109.31, -119.02) * mm, "end": v(108.8, -119.02) * mm});
            skLineSegment(sketch, "E4487", {"start": v(108.8, -119.02) * mm, "end": v(108.8, -119) * mm});
            skLineSegment(sketch, "E4488", {"start": v(108.8, -119) * mm, "end": v(102, -119) * mm});
            skLineSegment(sketch, "E4489", {"start": v(102, -119) * mm, "end": v(100.75, -118.92) * mm});
            skLineSegment(sketch, "E4490", {"start": v(100.75, -118.92) * mm, "end": v(99.51, -118.69) * mm});
            skLineSegment(sketch, "E4491", {"start": v(99.51, -118.69) * mm, "end": v(98.32, -118.3) * mm});
            skLineSegment(sketch, "E4492", {"start": v(98.32, -118.3) * mm, "end": v(97.18, -117.76) * mm});
            skLineSegment(sketch, "E4493", {"start": v(97.18, -117.76) * mm, "end": v(96.12, -117.1) * mm});
            skLineSegment(sketch, "E4494", {"start": v(96.12, -117.1) * mm, "end": v(95.15, -116.3) * mm});
            skLineSegment(sketch, "E4495", {"start": v(95.15, -116.3) * mm, "end": v(94.3, -115.37) * mm});
            skLineSegment(sketch, "E4496", {"start": v(94.3, -115.37) * mm, "end": v(93.56, -114.36) * mm});
            skLineSegment(sketch, "E4497", {"start": v(93.56, -114.36) * mm, "end": v(92.95, -113.26) * mm});
            skLineSegment(sketch, "E4498", {"start": v(92.95, -113.26) * mm, "end": v(92.49, -112.1) * mm});
            skLineSegment(sketch, "E4499", {"start": v(92.49, -112.1) * mm, "end": v(92.18, -110.87) * mm});
            skLineSegment(sketch, "E4500", {"start": v(92.18, -110.87) * mm, "end": v(92.02, -109.63) * mm});
            skLineSegment(sketch, "E4501", {"start": v(92.02, -109.63) * mm, "end": v(92.02, -109) * mm});
            skLineSegment(sketch, "E4502", {"start": v(92.02, -109) * mm, "end": v(92, -109) * mm});
            skLineSegment(sketch, "E4503", {"start": v(92, -109) * mm, "end": v(92, -107) * mm});
            skLineSegment(sketch, "E4504", {"start": v(92, -107) * mm, "end": v(92.06, -107) * mm});
            skLineSegment(sketch, "E4505", {"start": v(92.06, -107) * mm, "end": v(92.06, -105.12) * mm});
            skLineSegment(sketch, "E4506", {"start": v(92.06, -105.12) * mm, "end": v(92.53, -101.38) * mm});
            skLineSegment(sketch, "E4507", {"start": v(92.53, -101.38) * mm, "end": v(93.47, -97.73) * mm});
            skLineSegment(sketch, "E4508", {"start": v(93.47, -97.73) * mm, "end": v(94.86, -94.23) * mm});
            skLineSegment(sketch, "E4509", {"start": v(94.86, -94.23) * mm, "end": v(96.67, -90.93) * mm});
            skLineSegment(sketch, "E4510", {"start": v(96.67, -90.93) * mm, "end": v(98.88, -87.88) * mm});
            skLineSegment(sketch, "E4511", {"start": v(98.88, -87.88) * mm, "end": v(101.46, -85.13) * mm});
            skLineSegment(sketch, "E4512", {"start": v(101.46, -85.13) * mm, "end": v(104.37, -82.73) * mm});
            skLineSegment(sketch, "E4513", {"start": v(104.37, -82.73) * mm, "end": v(107.55, -80.71) * mm});
            skLineSegment(sketch, "E4514", {"start": v(107.55, -80.71) * mm, "end": v(110.96, -79.1) * mm});
            skLineSegment(sketch, "E4515", {"start": v(110.96, -79.1) * mm, "end": v(114.54, -77.94) * mm});
            skLineSegment(sketch, "E4516", {"start": v(114.54, -77.94) * mm, "end": v(118.24, -77.24) * mm});
            skLineSegment(sketch, "E4517", {"start": v(118.24, -77.24) * mm, "end": v(122, -77) * mm});
            skLineSegment(sketch, "E4518", {"start": v(122, -77) * mm, "end": v(170, -77) * mm});
            skLineSegment(sketch, "E4519", {"start": v(170, -77) * mm, "end": v(170, -77.02) * mm});
            skLineSegment(sketch, "E4520", {"start": v(170, -77.02) * mm, "end": v(170.63, -77.02) * mm});
            skLineSegment(sketch, "E4521", {"start": v(170.63, -77.02) * mm, "end": v(171.87, -77.18) * mm});
            skLineSegment(sketch, "E4522", {"start": v(171.87, -77.18) * mm, "end": v(173.1, -77.49) * mm});
            skLineSegment(sketch, "E4523", {"start": v(173.1, -77.49) * mm, "end": v(174.26, -77.95) * mm});
            skLineSegment(sketch, "E4524", {"start": v(174.26, -77.95) * mm, "end": v(175.36, -78.56) * mm});
            skLineSegment(sketch, "E4525", {"start": v(175.36, -78.56) * mm, "end": v(176.37, -79.3) * mm});
            skLineSegment(sketch, "E4526", {"start": v(176.37, -79.3) * mm, "end": v(177.29, -80.16) * mm});
            skLineSegment(sketch, "E4527", {"start": v(177.29, -80.16) * mm, "end": v(178.1, -81.12) * mm});
            skLineSegment(sketch, "E4528", {"start": v(178.1, -81.12) * mm, "end": v(178.76, -82.18) * mm});
            skLineSegment(sketch, "E4529", {"start": v(178.76, -82.18) * mm, "end": v(179.3, -83.32) * mm});
            skLineSegment(sketch, "E4530", {"start": v(179.3, -83.32) * mm, "end": v(179.69, -84.51) * mm});
            skLineSegment(sketch, "E4531", {"start": v(179.69, -84.51) * mm, "end": v(179.92, -85.75) * mm});
            skLineSegment(sketch, "E4532", {"start": v(179.92, -85.75) * mm, "end": v(180, -87) * mm});
            skLineSegment(sketch, "E4533", {"start": v(180, -87) * mm, "end": v(180, -108) * mm});
            skLineSegment(sketch, "E4534", {"start": v(180, -108) * mm, "end": v(180, -108) * mm});
            skLineSegment(sketch, "E4535", {"start": v(180, -108) * mm, "end": v(180, -108.31) * mm});
            skLineSegment(sketch, "E4536", {"start": v(180, -108.31) * mm, "end": v(180.09, -108.94) * mm});
            skLineSegment(sketch, "E4537", {"start": v(180.09, -108.94) * mm, "end": v(180.25, -109.55) * mm});
            skLineSegment(sketch, "E4538", {"start": v(180.25, -109.55) * mm, "end": v(180.48, -110.13) * mm});
            skLineSegment(sketch, "E4539", {"start": v(180.48, -110.13) * mm, "end": v(180.78, -110.68) * mm});
            skLineSegment(sketch, "E4540", {"start": v(180.78, -110.68) * mm, "end": v(181.15, -111.19) * mm});
            skLineSegment(sketch, "E4541", {"start": v(181.15, -111.19) * mm, "end": v(181.58, -111.64) * mm});
            skLineSegment(sketch, "E4542", {"start": v(181.58, -111.64) * mm, "end": v(182.06, -112.05) * mm});
            skLineSegment(sketch, "E4543", {"start": v(182.06, -112.05) * mm, "end": v(182.6, -112.38) * mm});
            skLineSegment(sketch, "E4544", {"start": v(182.6, -112.38) * mm, "end": v(183.16, -112.65) * mm});
            skLineSegment(sketch, "E4545", {"start": v(183.16, -112.65) * mm, "end": v(183.76, -112.84) * mm});
            skLineSegment(sketch, "E4546", {"start": v(183.76, -112.84) * mm, "end": v(184.37, -112.96) * mm});
            skLineSegment(sketch, "E4547", {"start": v(184.37, -112.96) * mm, "end": v(185, -113) * mm});
            skLineSegment(sketch, "E4548", {"start": v(185, -113) * mm, "end": v(225, -113) * mm});
            skLineSegment(sketch, "E4549", {"start": v(225, -113) * mm, "end": v(225, -112.99) * mm});
            skLineSegment(sketch, "E4550", {"start": v(225, -112.99) * mm, "end": v(225.31, -112.99) * mm});
            skLineSegment(sketch, "E4551", {"start": v(225.31, -112.99) * mm, "end": v(225.94, -112.91) * mm});
            skLineSegment(sketch, "E4552", {"start": v(225.94, -112.91) * mm, "end": v(226.54, -112.75) * mm});
            skLineSegment(sketch, "E4553", {"start": v(226.54, -112.75) * mm, "end": v(227.13, -112.52) * mm});
            skLineSegment(sketch, "E4554", {"start": v(227.13, -112.52) * mm, "end": v(227.68, -112.22) * mm});
            skLineSegment(sketch, "E4555", {"start": v(227.68, -112.22) * mm, "end": v(228.19, -111.85) * mm});
            skLineSegment(sketch, "E4556", {"start": v(228.19, -111.85) * mm, "end": v(228.65, -111.42) * mm});
            skLineSegment(sketch, "E4557", {"start": v(228.65, -111.42) * mm, "end": v(229.04, -110.94) * mm});
            skLineSegment(sketch, "E4558", {"start": v(229.04, -110.94) * mm, "end": v(229.38, -110.4) * mm});
            skLineSegment(sketch, "E4559", {"start": v(229.38, -110.4) * mm, "end": v(229.65, -109.84) * mm});
            skLineSegment(sketch, "E4560", {"start": v(229.65, -109.84) * mm, "end": v(229.84, -109.24) * mm});
            skLineSegment(sketch, "E4561", {"start": v(229.84, -109.24) * mm, "end": v(229.96, -108.63) * mm});
            skLineSegment(sketch, "E4562", {"start": v(229.96, -108.63) * mm, "end": v(230, -108) * mm});
            skLineSegment(sketch, "E4563", {"start": v(230, -108) * mm, "end": v(230, -87) * mm});
            skLineSegment(sketch, "E4564", {"start": v(230, -87) * mm, "end": v(230.08, -85.75) * mm});
            skLineSegment(sketch, "E4565", {"start": v(230.08, -85.75) * mm, "end": v(230.31, -84.51) * mm});
            skLineSegment(sketch, "E4566", {"start": v(230.31, -84.51) * mm, "end": v(230.7, -83.32) * mm});
            skLineSegment(sketch, "E4567", {"start": v(230.7, -83.32) * mm, "end": v(231.24, -82.18) * mm});
            skLineSegment(sketch, "E4568", {"start": v(231.24, -82.18) * mm, "end": v(231.9, -81.12) * mm});
            skLineSegment(sketch, "E4569", {"start": v(231.9, -81.12) * mm, "end": v(232.71, -80.16) * mm});
            skLineSegment(sketch, "E4570", {"start": v(232.71, -80.16) * mm, "end": v(233.63, -79.3) * mm});
            skLineSegment(sketch, "E4571", {"start": v(233.63, -79.3) * mm, "end": v(234.64, -78.56) * mm});
            skLineSegment(sketch, "E4572", {"start": v(234.64, -78.56) * mm, "end": v(235.74, -77.95) * mm});
            skLineSegment(sketch, "E4573", {"start": v(235.74, -77.95) * mm, "end": v(236.9, -77.49) * mm});
            skLineSegment(sketch, "E4574", {"start": v(236.9, -77.49) * mm, "end": v(238.13, -77.18) * mm});
            skLineSegment(sketch, "E4575", {"start": v(238.13, -77.18) * mm, "end": v(239.37, -77.02) * mm});
            skLineSegment(sketch, "E4576", {"start": v(239.37, -77.02) * mm, "end": v(240, -77.02) * mm});
            skLineSegment(sketch, "E4577", {"start": v(240, -77.02) * mm, "end": v(240, -77) * mm});
            skLineSegment(sketch, "E4578", {"start": v(240, -77) * mm, "end": v(288, -77) * mm});
            skLineSegment(sketch, "E4579", {"start": v(288, -77) * mm, "end": v(288, -77.06) * mm});
            skLineSegment(sketch, "E4580", {"start": v(288, -77.06) * mm, "end": v(289.88, -77.06) * mm});
            skLineSegment(sketch, "E4581", {"start": v(289.88, -77.06) * mm, "end": v(293.62, -77.53) * mm});
            skLineSegment(sketch, "E4582", {"start": v(293.62, -77.53) * mm, "end": v(297.27, -78.47) * mm});
            skLineSegment(sketch, "E4583", {"start": v(297.27, -78.47) * mm, "end": v(300.77, -79.86) * mm});
            skLineSegment(sketch, "E4584", {"start": v(300.77, -79.86) * mm, "end": v(304.07, -81.67) * mm});
            skLineSegment(sketch, "E4585", {"start": v(304.07, -81.67) * mm, "end": v(307.12, -83.89) * mm});
            skLineSegment(sketch, "E4586", {"start": v(307.12, -83.89) * mm, "end": v(309.87, -86.46) * mm});
            skLineSegment(sketch, "E4587", {"start": v(309.87, -86.46) * mm, "end": v(312.27, -89.37) * mm});
            skLineSegment(sketch, "E4588", {"start": v(312.27, -89.37) * mm, "end": v(314.29, -92.55) * mm});
            skLineSegment(sketch, "E4589", {"start": v(314.29, -92.55) * mm, "end": v(315.9, -95.96) * mm});
            skLineSegment(sketch, "E4590", {"start": v(315.9, -95.96) * mm, "end": v(317.06, -99.54) * mm});
            skLineSegment(sketch, "E4591", {"start": v(317.06, -99.54) * mm, "end": v(317.76, -103.24) * mm});
            skLineSegment(sketch, "E4592", {"start": v(317.76, -103.24) * mm, "end": v(318, -107) * mm});
            skLineSegment(sketch, "E4593", {"start": v(318, -107) * mm, "end": v(318, -407) * mm});
            skLineSegment(sketch, "E4594", {"start": v(318, -407) * mm, "end": v(317.94, -407) * mm});
            skLineSegment(sketch, "E4595", {"start": v(317.94, -407) * mm, "end": v(317.94, -408.88) * mm});
            skLineSegment(sketch, "E4596", {"start": v(317.94, -408.88) * mm, "end": v(317.47, -412.62) * mm});
            skLineSegment(sketch, "E4597", {"start": v(317.47, -412.62) * mm, "end": v(316.53, -416.27) * mm});
            skLineSegment(sketch, "E4598", {"start": v(316.53, -416.27) * mm, "end": v(315.14, -419.77) * mm});
            skLineSegment(sketch, "E4599", {"start": v(315.14, -419.77) * mm, "end": v(313.33, -423.07) * mm});
            skLineSegment(sketch, "E4600", {"start": v(313.33, -423.07) * mm, "end": v(311.12, -426.12) * mm});
            skLineSegment(sketch, "E4601", {"start": v(311.12, -426.12) * mm, "end": v(308.54, -428.87) * mm});
            skLineSegment(sketch, "E4602", {"start": v(308.54, -428.87) * mm, "end": v(305.63, -431.27) * mm});
            skLineSegment(sketch, "E4603", {"start": v(305.63, -431.27) * mm, "end": v(302.45, -433.29) * mm});
            skLineSegment(sketch, "E4604", {"start": v(302.45, -433.29) * mm, "end": v(299.04, -434.9) * mm});
            skLineSegment(sketch, "E4605", {"start": v(299.04, -434.9) * mm, "end": v(295.46, -436.06) * mm});
            skLineSegment(sketch, "E4606", {"start": v(295.46, -436.06) * mm, "end": v(291.76, -436.76) * mm});
            skLineSegment(sketch, "E4607", {"start": v(291.76, -436.76) * mm, "end": v(288, -437) * mm});
            skLineSegment(sketch, "E4608", {"start": v(288, -437) * mm, "end": v(237, -437) * mm});
            skLineSegment(sketch, "E4609", {"start": v(237, -437) * mm, "end": v(237, -436.98) * mm});
            skLineSegment(sketch, "E4610", {"start": v(237, -436.98) * mm, "end": v(236.37, -436.98) * mm});
            skLineSegment(sketch, "E4611", {"start": v(236.37, -436.98) * mm, "end": v(235.13, -436.82) * mm});
            skLineSegment(sketch, "E4612", {"start": v(235.13, -436.82) * mm, "end": v(233.9, -436.51) * mm});
            skLineSegment(sketch, "E4613", {"start": v(233.9, -436.51) * mm, "end": v(232.74, -436.05) * mm});
            skLineSegment(sketch, "E4614", {"start": v(232.74, -436.05) * mm, "end": v(231.64, -435.44) * mm});
            skLineSegment(sketch, "E4615", {"start": v(231.64, -435.44) * mm, "end": v(230.63, -434.7) * mm});
            skLineSegment(sketch, "E4616", {"start": v(230.63, -434.7) * mm, "end": v(229.71, -433.85) * mm});
            skLineSegment(sketch, "E4617", {"start": v(229.71, -433.85) * mm, "end": v(228.9, -432.88) * mm});
            skLineSegment(sketch, "E4618", {"start": v(228.9, -432.88) * mm, "end": v(228.24, -431.82) * mm});
            skLineSegment(sketch, "E4619", {"start": v(228.24, -431.82) * mm, "end": v(227.7, -430.68) * mm});
            skLineSegment(sketch, "E4620", {"start": v(227.7, -430.68) * mm, "end": v(227.31, -429.49) * mm});
            skLineSegment(sketch, "E4621", {"start": v(227.31, -429.49) * mm, "end": v(227.08, -428.25) * mm});
            skLineSegment(sketch, "E4622", {"start": v(227.08, -428.25) * mm, "end": v(227, -427) * mm});
            skLineSegment(sketch, "E4623", {"start": v(227, -427) * mm, "end": v(227, -418) * mm});
            skLineSegment(sketch, "E4624", {"start": v(227, -418) * mm, "end": v(226.96, -417.37) * mm});
            skLineSegment(sketch, "E4625", {"start": v(226.96, -417.37) * mm, "end": v(226.84, -416.76) * mm});
            skLineSegment(sketch, "E4626", {"start": v(226.84, -416.76) * mm, "end": v(226.65, -416.16) * mm});
            skLineSegment(sketch, "E4627", {"start": v(226.65, -416.16) * mm, "end": v(226.38, -415.6) * mm});
            skLineSegment(sketch, "E4628", {"start": v(226.38, -415.6) * mm, "end": v(226.04, -415.06) * mm});
            skLineSegment(sketch, "E4629", {"start": v(226.04, -415.06) * mm, "end": v(225.65, -414.58) * mm});
            skLineSegment(sketch, "E4630", {"start": v(225.65, -414.58) * mm, "end": v(225.19, -414.15) * mm});
            skLineSegment(sketch, "E4631", {"start": v(225.19, -414.15) * mm, "end": v(224.68, -413.78) * mm});
            skLineSegment(sketch, "E4632", {"start": v(224.68, -413.78) * mm, "end": v(224.13, -413.48) * mm});
            skLineSegment(sketch, "E4633", {"start": v(224.13, -413.48) * mm, "end": v(223.54, -413.25) * mm});
            skLineSegment(sketch, "E4634", {"start": v(223.54, -413.25) * mm, "end": v(222.94, -413.09) * mm});
            skLineSegment(sketch, "E4635", {"start": v(222.94, -413.09) * mm, "end": v(222.31, -413) * mm});
            skLineSegment(sketch, "E4636", {"start": v(222.31, -413) * mm, "end": v(222, -413) * mm});
            skLineSegment(sketch, "E4637", {"start": v(222, -413) * mm, "end": v(222, -413) * mm});
            skLineSegment(sketch, "E4638", {"start": v(222, -413) * mm, "end": v(188, -413) * mm});
            skLineSegment(sketch, "E4639", {"start": v(188, -413) * mm, "end": v(187.37, -413.04) * mm});
            skLineSegment(sketch, "E4640", {"start": v(187.37, -413.04) * mm, "end": v(186.76, -413.16) * mm});
            skLineSegment(sketch, "E4641", {"start": v(186.76, -413.16) * mm, "end": v(186.16, -413.35) * mm});
            skLineSegment(sketch, "E4642", {"start": v(186.16, -413.35) * mm, "end": v(185.6, -413.62) * mm});
            skLineSegment(sketch, "E4643", {"start": v(185.6, -413.62) * mm, "end": v(185.06, -413.96) * mm});
            skLineSegment(sketch, "E4644", {"start": v(185.06, -413.96) * mm, "end": v(184.58, -414.36) * mm});
            skLineSegment(sketch, "E4645", {"start": v(184.58, -414.36) * mm, "end": v(184.15, -414.81) * mm});
            skLineSegment(sketch, "E4646", {"start": v(184.15, -414.81) * mm, "end": v(183.78, -415.32) * mm});
            skLineSegment(sketch, "E4647", {"start": v(183.78, -415.32) * mm, "end": v(183.48, -415.87) * mm});
            skLineSegment(sketch, "E4648", {"start": v(183.48, -415.87) * mm, "end": v(183.25, -416.46) * mm});
            skLineSegment(sketch, "E4649", {"start": v(183.25, -416.46) * mm, "end": v(183.09, -417.06) * mm});
            skLineSegment(sketch, "E4650", {"start": v(183.09, -417.06) * mm, "end": v(183.01, -417.69) * mm});
            skLineSegment(sketch, "E4651", {"start": v(183.01, -417.69) * mm, "end": v(183.01, -418) * mm});
            skLineSegment(sketch, "E4652", {"start": v(183.01, -418) * mm, "end": v(183, -418) * mm});
            skLineSegment(sketch, "E4653", {"start": v(183, -418) * mm, "end": v(183, -427) * mm});
            skLineSegment(sketch, "E4654", {"start": v(183, -427) * mm, "end": v(182.92, -428.25) * mm});
            skLineSegment(sketch, "E4655", {"start": v(182.92, -428.25) * mm, "end": v(182.69, -429.49) * mm});
            skLineSegment(sketch, "E4656", {"start": v(182.69, -429.49) * mm, "end": v(182.3, -430.68) * mm});
            skLineSegment(sketch, "E4657", {"start": v(182.3, -430.68) * mm, "end": v(181.76, -431.82) * mm});
            skLineSegment(sketch, "E4658", {"start": v(181.76, -431.82) * mm, "end": v(181.1, -432.88) * mm});
            skLineSegment(sketch, "E4659", {"start": v(181.1, -432.88) * mm, "end": v(180.29, -433.85) * mm});
            skLineSegment(sketch, "E4660", {"start": v(180.29, -433.85) * mm, "end": v(179.37, -434.7) * mm});
            skLineSegment(sketch, "E4661", {"start": v(179.37, -434.7) * mm, "end": v(178.36, -435.44) * mm});
            skLineSegment(sketch, "E4662", {"start": v(178.36, -435.44) * mm, "end": v(177.26, -436.05) * mm});
            skLineSegment(sketch, "E4663", {"start": v(177.26, -436.05) * mm, "end": v(176.1, -436.51) * mm});
            skLineSegment(sketch, "E4664", {"start": v(176.1, -436.51) * mm, "end": v(174.87, -436.82) * mm});
            skLineSegment(sketch, "E4665", {"start": v(174.87, -436.82) * mm, "end": v(173.63, -436.98) * mm});
            skLineSegment(sketch, "E4666", {"start": v(173.63, -436.98) * mm, "end": v(173, -436.98) * mm});
            skLineSegment(sketch, "E4667", {"start": v(173, -436.98) * mm, "end": v(173, -437) * mm});
            skLineSegment(sketch, "E4668", {"start": v(173, -437) * mm, "end": v(122, -437) * mm});
            skLineSegment(sketch, "E4669", {"start": v(205.22, -102.82) * mm, "end": v(203.76, -102.47) * mm});
            skLineSegment(sketch, "E4670", {"start": v(203.76, -102.47) * mm, "end": v(202.35, -101.94) * mm});
            skLineSegment(sketch, "E4671", {"start": v(202.35, -101.94) * mm, "end": v(201.02, -101.23) * mm});
            skLineSegment(sketch, "E4672", {"start": v(201.02, -101.23) * mm, "end": v(199.79, -100.36) * mm});
            skLineSegment(sketch, "E4673", {"start": v(199.79, -100.36) * mm, "end": v(199.65, -100.23) * mm});
            skLineSegment(sketch, "E4674", {"start": v(199.65, -100.23) * mm, "end": v(199.32, -100) * mm});
            skLineSegment(sketch, "E4675", {"start": v(199.32, -100) * mm, "end": v(199.19, -99.87) * mm});
            skLineSegment(sketch, "E4676", {"start": v(199.19, -99.87) * mm, "end": v(198.86, -99.62) * mm});
            skLineSegment(sketch, "E4677", {"start": v(198.86, -99.62) * mm, "end": v(198.73, -99.49) * mm});
            skLineSegment(sketch, "E4678", {"start": v(198.73, -99.49) * mm, "end": v(198.41, -99.24) * mm});
            skLineSegment(sketch, "E4679", {"start": v(198.41, -99.24) * mm, "end": v(198.28, -99.1) * mm});
            skLineSegment(sketch, "E4680", {"start": v(198.28, -99.1) * mm, "end": v(197.97, -98.85) * mm});
            skLineSegment(sketch, "E4681", {"start": v(197.97, -98.85) * mm, "end": v(197.84, -98.71) * mm});
            skLineSegment(sketch, "E4682", {"start": v(197.84, -98.71) * mm, "end": v(197.53, -98.45) * mm});
            skLineSegment(sketch, "E4683", {"start": v(197.53, -98.45) * mm, "end": v(197.4, -98.31) * mm});
            skLineSegment(sketch, "E4684", {"start": v(197.4, -98.31) * mm, "end": v(197.1, -98.05) * mm});
            skLineSegment(sketch, "E4685", {"start": v(197.1, -98.05) * mm, "end": v(196.97, -97.9) * mm});
            skLineSegment(sketch, "E4686", {"start": v(196.97, -97.9) * mm, "end": v(196.67, -97.63) * mm});
            skLineSegment(sketch, "E4687", {"start": v(196.67, -97.63) * mm, "end": v(196.55, -97.5) * mm});
            skLineSegment(sketch, "E4688", {"start": v(196.55, -97.5) * mm, "end": v(196.25, -97.22) * mm});
            skLineSegment(sketch, "E4689", {"start": v(196.25, -97.22) * mm, "end": v(195.3, -96.05) * mm});
            skLineSegment(sketch, "E4690", {"start": v(195.3, -96.05) * mm, "end": v(194.48, -94.78) * mm});
            skLineSegment(sketch, "E4691", {"start": v(194.48, -94.78) * mm, "end": v(193.84, -93.42) * mm});
            skLineSegment(sketch, "E4692", {"start": v(193.84, -93.42) * mm, "end": v(193.38, -91.98) * mm});
            skLineSegment(sketch, "E4693", {"start": v(193.38, -91.98) * mm, "end": v(193.1, -90.5) * mm});
            skLineSegment(sketch, "E4694", {"start": v(193.1, -90.5) * mm, "end": v(193, -89) * mm});
            skLineSegment(sketch, "E4695", {"start": v(193, -89) * mm, "end": v(193.1, -87.5) * mm});
            skLineSegment(sketch, "E4696", {"start": v(193.1, -87.5) * mm, "end": v(193.38, -86.02) * mm});
            skLineSegment(sketch, "E4697", {"start": v(193.38, -86.02) * mm, "end": v(193.84, -84.58) * mm});
            skLineSegment(sketch, "E4698", {"start": v(193.84, -84.58) * mm, "end": v(194.48, -83.22) * mm});
            skLineSegment(sketch, "E4699", {"start": v(194.48, -83.22) * mm, "end": v(195.3, -81.95) * mm});
            skLineSegment(sketch, "E4700", {"start": v(195.3, -81.95) * mm, "end": v(196.25, -80.78) * mm});
            skLineSegment(sketch, "E4701", {"start": v(196.25, -80.78) * mm, "end": v(197.35, -79.75) * mm});
            skLineSegment(sketch, "E4702", {"start": v(197.35, -79.75) * mm, "end": v(198.57, -78.87) * mm});
            skLineSegment(sketch, "E4703", {"start": v(198.57, -78.87) * mm, "end": v(199.9, -78.14) * mm});
            skLineSegment(sketch, "E4704", {"start": v(199.9, -78.14) * mm, "end": v(201.3, -77.59) * mm});
            skLineSegment(sketch, "E4705", {"start": v(201.3, -77.59) * mm, "end": v(202.75, -77.21) * mm});
            skLineSegment(sketch, "E4706", {"start": v(202.75, -77.21) * mm, "end": v(204.25, -77.02) * mm});
            skLineSegment(sketch, "E4707", {"start": v(204.25, -77.02) * mm, "end": v(205.75, -77.02) * mm});
            skLineSegment(sketch, "E4708", {"start": v(205.75, -77.02) * mm, "end": v(207.25, -77.21) * mm});
            skLineSegment(sketch, "E4709", {"start": v(207.25, -77.21) * mm, "end": v(208.7, -77.59) * mm});
            skLineSegment(sketch, "E4710", {"start": v(208.7, -77.59) * mm, "end": v(210.1, -78.14) * mm});
            skLineSegment(sketch, "E4711", {"start": v(210.1, -78.14) * mm, "end": v(211.43, -78.87) * mm});
            skLineSegment(sketch, "E4712", {"start": v(211.43, -78.87) * mm, "end": v(212.65, -79.75) * mm});
            skLineSegment(sketch, "E4713", {"start": v(212.65, -79.75) * mm, "end": v(213.75, -80.78) * mm});
            skLineSegment(sketch, "E4714", {"start": v(213.75, -80.78) * mm, "end": v(213.88, -80.9) * mm});
            skLineSegment(sketch, "E4715", {"start": v(213.88, -80.9) * mm, "end": v(214, -81.02) * mm});
            skLineSegment(sketch, "E4716", {"start": v(214, -81.02) * mm, "end": v(214.14, -81.13) * mm});
            skLineSegment(sketch, "E4717", {"start": v(214.14, -81.13) * mm, "end": v(214.27, -81.24) * mm});
            skLineSegment(sketch, "E4718", {"start": v(214.27, -81.24) * mm, "end": v(214.4, -81.35) * mm});
            skLineSegment(sketch, "E4719", {"start": v(214.4, -81.35) * mm, "end": v(214.55, -81.45) * mm});
            skLineSegment(sketch, "E4720", {"start": v(214.55, -81.45) * mm, "end": v(214.69, -81.55) * mm});
            skLineSegment(sketch, "E4721", {"start": v(214.69, -81.55) * mm, "end": v(214.83, -81.65) * mm});
            skLineSegment(sketch, "E4722", {"start": v(214.83, -81.65) * mm, "end": v(215.94, -82.67) * mm});
            skLineSegment(sketch, "E4723", {"start": v(215.94, -82.67) * mm, "end": v(216.92, -83.82) * mm});
            skLineSegment(sketch, "E4724", {"start": v(216.92, -83.82) * mm, "end": v(217.74, -85.08) * mm});
            skLineSegment(sketch, "E4725", {"start": v(217.74, -85.08) * mm, "end": v(218.4, -86.43) * mm});
            skLineSegment(sketch, "E4726", {"start": v(218.4, -86.43) * mm, "end": v(218.89, -87.86) * mm});
            skLineSegment(sketch, "E4727", {"start": v(218.89, -87.86) * mm, "end": v(219.2, -89.34) * mm});
            skLineSegment(sketch, "E4728", {"start": v(219.2, -89.34) * mm, "end": v(219.3, -90.84) * mm});
            skLineSegment(sketch, "E4729", {"start": v(219.3, -90.84) * mm, "end": v(219.23, -92.34) * mm});
            skLineSegment(sketch, "E4730", {"start": v(219.23, -92.34) * mm, "end": v(218.97, -93.83) * mm});
            skLineSegment(sketch, "E4731", {"start": v(218.97, -93.83) * mm, "end": v(218.53, -95.27) * mm});
            skLineSegment(sketch, "E4732", {"start": v(218.53, -95.27) * mm, "end": v(217.9, -96.64) * mm});
            skLineSegment(sketch, "E4733", {"start": v(217.9, -96.64) * mm, "end": v(217.11, -97.92) * mm});
            skLineSegment(sketch, "E4734", {"start": v(217.11, -97.92) * mm, "end": v(216.17, -99.1) * mm});
            skLineSegment(sketch, "E4735", {"start": v(216.17, -99.1) * mm, "end": v(215.09, -100.14) * mm});
            skLineSegment(sketch, "E4736", {"start": v(215.09, -100.14) * mm, "end": v(213.88, -101.05) * mm});
            skLineSegment(sketch, "E4737", {"start": v(213.88, -101.05) * mm, "end": v(212.57, -101.8) * mm});
            skLineSegment(sketch, "E4738", {"start": v(212.57, -101.8) * mm, "end": v(211.18, -102.37) * mm});
            skLineSegment(sketch, "E4739", {"start": v(211.18, -102.37) * mm, "end": v(209.72, -102.76) * mm});
            skLineSegment(sketch, "E4740", {"start": v(209.72, -102.76) * mm, "end": v(208.23, -102.97) * mm});
            skLineSegment(sketch, "E4741", {"start": v(208.23, -102.97) * mm, "end": v(206.72, -103) * mm});
            skLineSegment(sketch, "E4742", {"start": v(206.72, -103) * mm, "end": v(205.22, -102.82) * mm});
            skLineSegment(sketch, "E4743", {"start": v(369.87, -82) * mm, "end": v(369.62, -81.97) * mm});
            skLineSegment(sketch, "E4744", {"start": v(369.62, -81.97) * mm, "end": v(369.38, -81.9) * mm});
            skLineSegment(sketch, "E4745", {"start": v(369.38, -81.9) * mm, "end": v(369.15, -81.81) * mm});
            skLineSegment(sketch, "E4746", {"start": v(369.15, -81.81) * mm, "end": v(368.93, -81.69) * mm});
            skLineSegment(sketch, "E4747", {"start": v(368.93, -81.69) * mm, "end": v(368.73, -81.54) * mm});
            skLineSegment(sketch, "E4748", {"start": v(368.73, -81.54) * mm, "end": v(368.54, -81.37) * mm});
            skLineSegment(sketch, "E4749", {"start": v(368.54, -81.37) * mm, "end": v(368.38, -81.18) * mm});
            skLineSegment(sketch, "E4750", {"start": v(368.38, -81.18) * mm, "end": v(368.25, -80.96) * mm});
            skLineSegment(sketch, "E4751", {"start": v(368.25, -80.96) * mm, "end": v(368.14, -80.74) * mm});
            skLineSegment(sketch, "E4752", {"start": v(368.14, -80.74) * mm, "end": v(368.06, -80.5) * mm});
            skLineSegment(sketch, "E4753", {"start": v(368.06, -80.5) * mm, "end": v(368.02, -80.25) * mm});
            skLineSegment(sketch, "E4754", {"start": v(368.02, -80.25) * mm, "end": v(368, -80) * mm});
            skLineSegment(sketch, "E4755", {"start": v(368, -80) * mm, "end": v(368.02, -79.75) * mm});
            skLineSegment(sketch, "E4756", {"start": v(368.02, -79.75) * mm, "end": v(368.06, -79.5) * mm});
            skLineSegment(sketch, "E4757", {"start": v(368.06, -79.5) * mm, "end": v(368.14, -79.26) * mm});
            skLineSegment(sketch, "E4758", {"start": v(368.14, -79.26) * mm, "end": v(368.25, -79.04) * mm});
            skLineSegment(sketch, "E4759", {"start": v(368.25, -79.04) * mm, "end": v(368.38, -78.82) * mm});
            skLineSegment(sketch, "E4760", {"start": v(368.38, -78.82) * mm, "end": v(368.54, -78.63) * mm});
            skLineSegment(sketch, "E4761", {"start": v(368.54, -78.63) * mm, "end": v(368.73, -78.46) * mm});
            skLineSegment(sketch, "E4762", {"start": v(368.73, -78.46) * mm, "end": v(368.93, -78.31) * mm});
            skLineSegment(sketch, "E4763", {"start": v(368.93, -78.31) * mm, "end": v(369.15, -78.19) * mm});
            skLineSegment(sketch, "E4764", {"start": v(369.15, -78.19) * mm, "end": v(369.38, -78.1) * mm});
            skLineSegment(sketch, "E4765", {"start": v(369.38, -78.1) * mm, "end": v(369.62, -78.03) * mm});
            skLineSegment(sketch, "E4766", {"start": v(369.62, -78.03) * mm, "end": v(369.87, -78) * mm});
            skLineSegment(sketch, "E4767", {"start": v(369.87, -78) * mm, "end": v(370.13, -78) * mm});
            skLineSegment(sketch, "E4768", {"start": v(370.13, -78) * mm, "end": v(370.38, -78.03) * mm});
            skLineSegment(sketch, "E4769", {"start": v(370.38, -78.03) * mm, "end": v(370.62, -78.1) * mm});
            skLineSegment(sketch, "E4770", {"start": v(370.62, -78.1) * mm, "end": v(370.85, -78.19) * mm});
            skLineSegment(sketch, "E4771", {"start": v(370.85, -78.19) * mm, "end": v(371.07, -78.31) * mm});
            skLineSegment(sketch, "E4772", {"start": v(371.07, -78.31) * mm, "end": v(371.27, -78.46) * mm});
            skLineSegment(sketch, "E4773", {"start": v(371.27, -78.46) * mm, "end": v(371.46, -78.63) * mm});
            skLineSegment(sketch, "E4774", {"start": v(371.46, -78.63) * mm, "end": v(371.62, -78.82) * mm});
            skLineSegment(sketch, "E4775", {"start": v(371.62, -78.82) * mm, "end": v(371.75, -79.04) * mm});
            skLineSegment(sketch, "E4776", {"start": v(371.75, -79.04) * mm, "end": v(371.86, -79.26) * mm});
            skLineSegment(sketch, "E4777", {"start": v(371.86, -79.26) * mm, "end": v(371.94, -79.5) * mm});
            skLineSegment(sketch, "E4778", {"start": v(371.94, -79.5) * mm, "end": v(371.98, -79.75) * mm});
            skLineSegment(sketch, "E4779", {"start": v(371.98, -79.75) * mm, "end": v(372, -80) * mm});
            skLineSegment(sketch, "E4780", {"start": v(372, -80) * mm, "end": v(371.98, -80.25) * mm});
            skLineSegment(sketch, "E4781", {"start": v(371.98, -80.25) * mm, "end": v(371.94, -80.5) * mm});
            skLineSegment(sketch, "E4782", {"start": v(371.94, -80.5) * mm, "end": v(371.86, -80.74) * mm});
            skLineSegment(sketch, "E4783", {"start": v(371.86, -80.74) * mm, "end": v(371.75, -80.96) * mm});
            skLineSegment(sketch, "E4784", {"start": v(371.75, -80.96) * mm, "end": v(371.62, -81.18) * mm});
            skLineSegment(sketch, "E4785", {"start": v(371.62, -81.18) * mm, "end": v(371.46, -81.37) * mm});
            skLineSegment(sketch, "E4786", {"start": v(371.46, -81.37) * mm, "end": v(371.27, -81.54) * mm});
            skLineSegment(sketch, "E4787", {"start": v(371.27, -81.54) * mm, "end": v(371.07, -81.69) * mm});
            skLineSegment(sketch, "E4788", {"start": v(371.07, -81.69) * mm, "end": v(370.85, -81.81) * mm});
            skLineSegment(sketch, "E4789", {"start": v(370.85, -81.81) * mm, "end": v(370.62, -81.9) * mm});
            skLineSegment(sketch, "E4790", {"start": v(370.62, -81.9) * mm, "end": v(370.38, -81.97) * mm});
            skLineSegment(sketch, "E4791", {"start": v(370.38, -81.97) * mm, "end": v(370.13, -82) * mm});
            skLineSegment(sketch, "E4792", {"start": v(370.13, -82) * mm, "end": v(369.87, -82) * mm});
            skLineSegment(sketch, "E4793", {"start": v(39.87, -82) * mm, "end": v(39.63, -81.97) * mm});
            skLineSegment(sketch, "E4794", {"start": v(39.63, -81.97) * mm, "end": v(39.38, -81.9) * mm});
            skLineSegment(sketch, "E4795", {"start": v(39.38, -81.9) * mm, "end": v(39.15, -81.81) * mm});
            skLineSegment(sketch, "E4796", {"start": v(39.15, -81.81) * mm, "end": v(38.93, -81.69) * mm});
            skLineSegment(sketch, "E4797", {"start": v(38.93, -81.69) * mm, "end": v(38.73, -81.54) * mm});
            skLineSegment(sketch, "E4798", {"start": v(38.73, -81.54) * mm, "end": v(38.54, -81.37) * mm});
            skLineSegment(sketch, "E4799", {"start": v(38.54, -81.37) * mm, "end": v(38.38, -81.18) * mm});
            skLineSegment(sketch, "E4800", {"start": v(38.38, -81.18) * mm, "end": v(38.25, -80.96) * mm});
            skLineSegment(sketch, "E4801", {"start": v(38.25, -80.96) * mm, "end": v(38.14, -80.74) * mm});
            skLineSegment(sketch, "E4802", {"start": v(38.14, -80.74) * mm, "end": v(38.06, -80.5) * mm});
            skLineSegment(sketch, "E4803", {"start": v(38.06, -80.5) * mm, "end": v(38.02, -80.25) * mm});
            skLineSegment(sketch, "E4804", {"start": v(38.02, -80.25) * mm, "end": v(38, -80) * mm});
            skLineSegment(sketch, "E4805", {"start": v(38, -80) * mm, "end": v(38.02, -79.75) * mm});
            skLineSegment(sketch, "E4806", {"start": v(38.02, -79.75) * mm, "end": v(38.06, -79.5) * mm});
            skLineSegment(sketch, "E4807", {"start": v(38.06, -79.5) * mm, "end": v(38.14, -79.26) * mm});
            skLineSegment(sketch, "E4808", {"start": v(38.14, -79.26) * mm, "end": v(38.25, -79.04) * mm});
            skLineSegment(sketch, "E4809", {"start": v(38.25, -79.04) * mm, "end": v(38.38, -78.82) * mm});
            skLineSegment(sketch, "E4810", {"start": v(38.38, -78.82) * mm, "end": v(38.54, -78.63) * mm});
            skLineSegment(sketch, "E4811", {"start": v(38.54, -78.63) * mm, "end": v(38.73, -78.46) * mm});
            skLineSegment(sketch, "E4812", {"start": v(38.73, -78.46) * mm, "end": v(38.93, -78.31) * mm});
            skLineSegment(sketch, "E4813", {"start": v(38.93, -78.31) * mm, "end": v(39.15, -78.19) * mm});
            skLineSegment(sketch, "E4814", {"start": v(39.15, -78.19) * mm, "end": v(39.38, -78.1) * mm});
            skLineSegment(sketch, "E4815", {"start": v(39.38, -78.1) * mm, "end": v(39.63, -78.03) * mm});
            skLineSegment(sketch, "E4816", {"start": v(39.63, -78.03) * mm, "end": v(39.87, -78) * mm});
            skLineSegment(sketch, "E4817", {"start": v(39.87, -78) * mm, "end": v(40.13, -78) * mm});
            skLineSegment(sketch, "E4818", {"start": v(40.13, -78) * mm, "end": v(40.37, -78.03) * mm});
            skLineSegment(sketch, "E4819", {"start": v(40.37, -78.03) * mm, "end": v(40.62, -78.1) * mm});
            skLineSegment(sketch, "E4820", {"start": v(40.62, -78.1) * mm, "end": v(40.85, -78.19) * mm});
            skLineSegment(sketch, "E4821", {"start": v(40.85, -78.19) * mm, "end": v(41.07, -78.31) * mm});
            skLineSegment(sketch, "E4822", {"start": v(41.07, -78.31) * mm, "end": v(41.27, -78.46) * mm});
            skLineSegment(sketch, "E4823", {"start": v(41.27, -78.46) * mm, "end": v(41.46, -78.63) * mm});
            skLineSegment(sketch, "E4824", {"start": v(41.46, -78.63) * mm, "end": v(41.62, -78.82) * mm});
            skLineSegment(sketch, "E4825", {"start": v(41.62, -78.82) * mm, "end": v(41.75, -79.04) * mm});
            skLineSegment(sketch, "E4826", {"start": v(41.75, -79.04) * mm, "end": v(41.86, -79.26) * mm});
            skLineSegment(sketch, "E4827", {"start": v(41.86, -79.26) * mm, "end": v(41.94, -79.5) * mm});
            skLineSegment(sketch, "E4828", {"start": v(41.94, -79.5) * mm, "end": v(41.98, -79.75) * mm});
            skLineSegment(sketch, "E4829", {"start": v(41.98, -79.75) * mm, "end": v(42, -80) * mm});
            skLineSegment(sketch, "E4830", {"start": v(42, -80) * mm, "end": v(41.98, -80.25) * mm});
            skLineSegment(sketch, "E4831", {"start": v(41.98, -80.25) * mm, "end": v(41.94, -80.5) * mm});
            skLineSegment(sketch, "E4832", {"start": v(41.94, -80.5) * mm, "end": v(41.86, -80.74) * mm});
            skLineSegment(sketch, "E4833", {"start": v(41.86, -80.74) * mm, "end": v(41.75, -80.96) * mm});
            skLineSegment(sketch, "E4834", {"start": v(41.75, -80.96) * mm, "end": v(41.62, -81.18) * mm});
            skLineSegment(sketch, "E4835", {"start": v(41.62, -81.18) * mm, "end": v(41.46, -81.37) * mm});
            skLineSegment(sketch, "E4836", {"start": v(41.46, -81.37) * mm, "end": v(41.27, -81.54) * mm});
            skLineSegment(sketch, "E4837", {"start": v(41.27, -81.54) * mm, "end": v(41.07, -81.69) * mm});
            skLineSegment(sketch, "E4838", {"start": v(41.07, -81.69) * mm, "end": v(40.85, -81.81) * mm});
            skLineSegment(sketch, "E4839", {"start": v(40.85, -81.81) * mm, "end": v(40.62, -81.9) * mm});
            skLineSegment(sketch, "E4840", {"start": v(40.62, -81.9) * mm, "end": v(40.37, -81.97) * mm});
            skLineSegment(sketch, "E4841", {"start": v(40.37, -81.97) * mm, "end": v(40.13, -82) * mm});
            skLineSegment(sketch, "E4842", {"start": v(40.13, -82) * mm, "end": v(39.87, -82) * mm});
            skLineSegment(sketch, "E4843", {"start": v(32, -120) * mm, "end": v(32, -100) * mm});
            skLineSegment(sketch, "E4844", {"start": v(32, -100) * mm, "end": v(48, -100) * mm});
            skLineSegment(sketch, "E4845", {"start": v(48, -100) * mm, "end": v(48, -120) * mm});
            skLineSegment(sketch, "E4846", {"start": v(48, -120) * mm, "end": v(32, -120) * mm});
            skLineSegment(sketch, "E4847", {"start": v(362, -120) * mm, "end": v(362, -100) * mm});
            skLineSegment(sketch, "E4848", {"start": v(362, -100) * mm, "end": v(378, -100) * mm});
            skLineSegment(sketch, "E4849", {"start": v(378, -100) * mm, "end": v(378, -120) * mm});
            skLineSegment(sketch, "E4850", {"start": v(378, -120) * mm, "end": v(362, -120) * mm});
            skLineSegment(sketch, "E4851", {"start": v(220.4, -106) * mm, "end": v(220.22, -105.97) * mm});
            skLineSegment(sketch, "E4852", {"start": v(220.22, -105.97) * mm, "end": v(220.04, -105.93) * mm});
            skLineSegment(sketch, "E4853", {"start": v(220.04, -105.93) * mm, "end": v(219.86, -105.86) * mm});
            skLineSegment(sketch, "E4854", {"start": v(219.86, -105.86) * mm, "end": v(219.7, -105.77) * mm});
            skLineSegment(sketch, "E4855", {"start": v(219.7, -105.77) * mm, "end": v(219.54, -105.66) * mm});
            skLineSegment(sketch, "E4856", {"start": v(219.54, -105.66) * mm, "end": v(219.4, -105.53) * mm});
            skLineSegment(sketch, "E4857", {"start": v(219.4, -105.53) * mm, "end": v(219.29, -105.38) * mm});
            skLineSegment(sketch, "E4858", {"start": v(219.29, -105.38) * mm, "end": v(219.19, -105.22) * mm});
            skLineSegment(sketch, "E4859", {"start": v(219.19, -105.22) * mm, "end": v(219.1, -105.05) * mm});
            skLineSegment(sketch, "E4860", {"start": v(219.1, -105.05) * mm, "end": v(219.05, -104.87) * mm});
            skLineSegment(sketch, "E4861", {"start": v(219.05, -104.87) * mm, "end": v(219.01, -104.69) * mm});
            skLineSegment(sketch, "E4862", {"start": v(219.01, -104.69) * mm, "end": v(219, -104.5) * mm});
            skLineSegment(sketch, "E4863", {"start": v(219, -104.5) * mm, "end": v(219.01, -104.31) * mm});
            skLineSegment(sketch, "E4864", {"start": v(219.01, -104.31) * mm, "end": v(219.05, -104.13) * mm});
            skLineSegment(sketch, "E4865", {"start": v(219.05, -104.13) * mm, "end": v(219.1, -103.95) * mm});
            skLineSegment(sketch, "E4866", {"start": v(219.1, -103.95) * mm, "end": v(219.19, -103.78) * mm});
            skLineSegment(sketch, "E4867", {"start": v(219.19, -103.78) * mm, "end": v(219.29, -103.62) * mm});
            skLineSegment(sketch, "E4868", {"start": v(219.29, -103.62) * mm, "end": v(219.4, -103.47) * mm});
            skLineSegment(sketch, "E4869", {"start": v(219.4, -103.47) * mm, "end": v(219.54, -103.34) * mm});
            skLineSegment(sketch, "E4870", {"start": v(219.54, -103.34) * mm, "end": v(219.7, -103.23) * mm});
            skLineSegment(sketch, "E4871", {"start": v(219.7, -103.23) * mm, "end": v(219.86, -103.14) * mm});
            skLineSegment(sketch, "E4872", {"start": v(219.86, -103.14) * mm, "end": v(220.04, -103.07) * mm});
            skLineSegment(sketch, "E4873", {"start": v(220.04, -103.07) * mm, "end": v(220.22, -103.03) * mm});
            skLineSegment(sketch, "E4874", {"start": v(220.22, -103.03) * mm, "end": v(220.4, -103) * mm});
            skLineSegment(sketch, "E4875", {"start": v(220.4, -103) * mm, "end": v(220.6, -103) * mm});
            skLineSegment(sketch, "E4876", {"start": v(220.6, -103) * mm, "end": v(220.76, -103.02) * mm});
            skLineSegment(sketch, "E4877", {"start": v(220.76, -103.02) * mm, "end": v(220.92, -103) * mm});
            skLineSegment(sketch, "E4878", {"start": v(220.92, -103) * mm, "end": v(221.1, -103) * mm});
            skLineSegment(sketch, "E4879", {"start": v(221.1, -103) * mm, "end": v(221.27, -103.02) * mm});
            skLineSegment(sketch, "E4880", {"start": v(221.27, -103.02) * mm, "end": v(221.44, -102.99) * mm});
            skLineSegment(sketch, "E4881", {"start": v(221.44, -102.99) * mm, "end": v(221.62, -102.98) * mm});
            skLineSegment(sketch, "E4882", {"start": v(221.62, -102.98) * mm, "end": v(221.79, -103) * mm});
            skLineSegment(sketch, "E4883", {"start": v(221.79, -103) * mm, "end": v(221.95, -102.97) * mm});
            skLineSegment(sketch, "E4884", {"start": v(221.95, -102.97) * mm, "end": v(222.14, -102.96) * mm});
            skLineSegment(sketch, "E4885", {"start": v(222.14, -102.96) * mm, "end": v(222.3, -102.97) * mm});
            skLineSegment(sketch, "E4886", {"start": v(222.3, -102.97) * mm, "end": v(222.46, -102.94) * mm});
            skLineSegment(sketch, "E4887", {"start": v(222.46, -102.94) * mm, "end": v(222.65, -102.92) * mm});
            skLineSegment(sketch, "E4888", {"start": v(222.65, -102.92) * mm, "end": v(222.82, -102.93) * mm});
            skLineSegment(sketch, "E4889", {"start": v(222.82, -102.93) * mm, "end": v(222.98, -102.9) * mm});
            skLineSegment(sketch, "E4890", {"start": v(222.98, -102.9) * mm, "end": v(223.16, -102.88) * mm});
            skLineSegment(sketch, "E4891", {"start": v(223.16, -102.88) * mm, "end": v(223.33, -102.89) * mm});
            skLineSegment(sketch, "E4892", {"start": v(223.33, -102.89) * mm, "end": v(223.5, -102.85) * mm});
            skLineSegment(sketch, "E4893", {"start": v(223.5, -102.85) * mm, "end": v(223.68, -102.83) * mm});
            skLineSegment(sketch, "E4894", {"start": v(223.68, -102.83) * mm, "end": v(223.84, -102.83) * mm});
            skLineSegment(sketch, "E4895", {"start": v(223.84, -102.83) * mm, "end": v(224, -102.8) * mm});
            skLineSegment(sketch, "E4896", {"start": v(224, -102.8) * mm, "end": v(224.19, -102.77) * mm});
            skLineSegment(sketch, "E4897", {"start": v(224.19, -102.77) * mm, "end": v(224.35, -102.77) * mm});
            skLineSegment(sketch, "E4898", {"start": v(224.35, -102.77) * mm, "end": v(224.51, -102.73) * mm});
            skLineSegment(sketch, "E4899", {"start": v(224.51, -102.73) * mm, "end": v(224.7, -102.7) * mm});
            skLineSegment(sketch, "E4900", {"start": v(224.7, -102.7) * mm, "end": v(224.89, -102.7) * mm});
            skLineSegment(sketch, "E4901", {"start": v(224.89, -102.7) * mm, "end": v(225.07, -102.72) * mm});
            skLineSegment(sketch, "E4902", {"start": v(225.07, -102.72) * mm, "end": v(225.26, -102.77) * mm});
            skLineSegment(sketch, "E4903", {"start": v(225.26, -102.77) * mm, "end": v(225.43, -102.83) * mm});
            skLineSegment(sketch, "E4904", {"start": v(225.43, -102.83) * mm, "end": v(225.6, -102.92) * mm});
            skLineSegment(sketch, "E4905", {"start": v(225.6, -102.92) * mm, "end": v(225.75, -103.03) * mm});
            skLineSegment(sketch, "E4906", {"start": v(225.75, -103.03) * mm, "end": v(225.9, -103.16) * mm});
            skLineSegment(sketch, "E4907", {"start": v(225.9, -103.16) * mm, "end": v(226.01, -103.3) * mm});
            skLineSegment(sketch, "E4908", {"start": v(226.01, -103.3) * mm, "end": v(226.12, -103.46) * mm});
            skLineSegment(sketch, "E4909", {"start": v(226.12, -103.46) * mm, "end": v(226.2, -103.63) * mm});
            skLineSegment(sketch, "E4910", {"start": v(226.2, -103.63) * mm, "end": v(226.26, -103.8) * mm});
            skLineSegment(sketch, "E4911", {"start": v(226.26, -103.8) * mm, "end": v(226.3, -103.99) * mm});
            skLineSegment(sketch, "E4912", {"start": v(226.3, -103.99) * mm, "end": v(226.31, -104.18) * mm});
            skLineSegment(sketch, "E4913", {"start": v(226.31, -104.18) * mm, "end": v(226.3, -104.37) * mm});
            skLineSegment(sketch, "E4914", {"start": v(226.3, -104.37) * mm, "end": v(226.27, -104.55) * mm});
            skLineSegment(sketch, "E4915", {"start": v(226.27, -104.55) * mm, "end": v(226.22, -104.73) * mm});
            skLineSegment(sketch, "E4916", {"start": v(226.22, -104.73) * mm, "end": v(226.14, -104.9) * mm});
            skLineSegment(sketch, "E4917", {"start": v(226.14, -104.9) * mm, "end": v(226.04, -105.06) * mm});
            skLineSegment(sketch, "E4918", {"start": v(226.04, -105.06) * mm, "end": v(225.92, -105.2) * mm});
            skLineSegment(sketch, "E4919", {"start": v(225.92, -105.2) * mm, "end": v(225.79, -105.34) * mm});
            skLineSegment(sketch, "E4920", {"start": v(225.79, -105.34) * mm, "end": v(225.64, -105.45) * mm});
            skLineSegment(sketch, "E4921", {"start": v(225.64, -105.45) * mm, "end": v(225.47, -105.55) * mm});
            skLineSegment(sketch, "E4922", {"start": v(225.47, -105.55) * mm, "end": v(225.3, -105.62) * mm});
            skLineSegment(sketch, "E4923", {"start": v(225.3, -105.62) * mm, "end": v(225.12, -105.67) * mm});
            skLineSegment(sketch, "E4924", {"start": v(225.12, -105.67) * mm, "end": v(224.93, -105.7) * mm});
            skLineSegment(sketch, "E4925", {"start": v(224.93, -105.7) * mm, "end": v(224.74, -105.7) * mm});
            skLineSegment(sketch, "E4926", {"start": v(224.74, -105.7) * mm, "end": v(224.55, -105.74) * mm});
            skLineSegment(sketch, "E4927", {"start": v(224.55, -105.74) * mm, "end": v(224.37, -105.77) * mm});
            skLineSegment(sketch, "E4928", {"start": v(224.37, -105.77) * mm, "end": v(224.18, -105.77) * mm});
            skLineSegment(sketch, "E4929", {"start": v(224.18, -105.77) * mm, "end": v(224, -105.8) * mm});
            skLineSegment(sketch, "E4930", {"start": v(224, -105.8) * mm, "end": v(223.8, -105.83) * mm});
            skLineSegment(sketch, "E4931", {"start": v(223.8, -105.83) * mm, "end": v(223.62, -105.83) * mm});
            skLineSegment(sketch, "E4932", {"start": v(223.62, -105.83) * mm, "end": v(223.43, -105.86) * mm});
            skLineSegment(sketch, "E4933", {"start": v(223.43, -105.86) * mm, "end": v(223.24, -105.88) * mm});
            skLineSegment(sketch, "E4934", {"start": v(223.24, -105.88) * mm, "end": v(223.05, -105.87) * mm});
            skLineSegment(sketch, "E4935", {"start": v(223.05, -105.87) * mm, "end": v(222.86, -105.91) * mm});
            skLineSegment(sketch, "E4936", {"start": v(222.86, -105.91) * mm, "end": v(222.67, -105.92) * mm});
            skLineSegment(sketch, "E4937", {"start": v(222.67, -105.92) * mm, "end": v(222.49, -105.91) * mm});
            skLineSegment(sketch, "E4938", {"start": v(222.49, -105.91) * mm, "end": v(222.3, -105.95) * mm});
            skLineSegment(sketch, "E4939", {"start": v(222.3, -105.95) * mm, "end": v(222.1, -105.96) * mm});
            skLineSegment(sketch, "E4940", {"start": v(222.1, -105.96) * mm, "end": v(221.92, -105.94) * mm});
            skLineSegment(sketch, "E4941", {"start": v(221.92, -105.94) * mm, "end": v(221.73, -105.97) * mm});
            skLineSegment(sketch, "E4942", {"start": v(221.73, -105.97) * mm, "end": v(221.54, -105.98) * mm});
            skLineSegment(sketch, "E4943", {"start": v(221.54, -105.98) * mm, "end": v(221.35, -105.96) * mm});
            skLineSegment(sketch, "E4944", {"start": v(221.35, -105.96) * mm, "end": v(221.16, -105.99) * mm});
            skLineSegment(sketch, "E4945", {"start": v(221.16, -105.99) * mm, "end": v(220.97, -106) * mm});
            skLineSegment(sketch, "E4946", {"start": v(220.97, -106) * mm, "end": v(220.79, -105.97) * mm});
            skLineSegment(sketch, "E4947", {"start": v(220.79, -105.97) * mm, "end": v(220.6, -106) * mm});
            skLineSegment(sketch, "E4948", {"start": v(220.6, -106) * mm, "end": v(220.4, -106) * mm});
            skLineSegment(sketch, "E4949", {"start": v(193.86, -109.99) * mm, "end": v(193.67, -109.95) * mm});
            skLineSegment(sketch, "E4950", {"start": v(193.67, -109.95) * mm, "end": v(193.5, -109.88) * mm});
            skLineSegment(sketch, "E4951", {"start": v(193.5, -109.88) * mm, "end": v(193.33, -109.8) * mm});
            skLineSegment(sketch, "E4952", {"start": v(193.33, -109.8) * mm, "end": v(193.18, -109.68) * mm});
            skLineSegment(sketch, "E4953", {"start": v(193.18, -109.68) * mm, "end": v(193.04, -109.56) * mm});
            skLineSegment(sketch, "E4954", {"start": v(193.04, -109.56) * mm, "end": v(192.93, -109.43) * mm});
            skLineSegment(sketch, "E4955", {"start": v(192.93, -109.43) * mm, "end": v(192.87, -109.4) * mm});
            skLineSegment(sketch, "E4956", {"start": v(192.87, -109.4) * mm, "end": v(192.7, -109.31) * mm});
            skLineSegment(sketch, "E4957", {"start": v(192.7, -109.31) * mm, "end": v(192.55, -109.2) * mm});
            skLineSegment(sketch, "E4958", {"start": v(192.55, -109.2) * mm, "end": v(192.41, -109.07) * mm});
            skLineSegment(sketch, "E4959", {"start": v(192.41, -109.07) * mm, "end": v(192.3, -108.94) * mm});
            skLineSegment(sketch, "E4960", {"start": v(192.3, -108.94) * mm, "end": v(192.24, -108.91) * mm});
            skLineSegment(sketch, "E4961", {"start": v(192.24, -108.91) * mm, "end": v(192.08, -108.82) * mm});
            skLineSegment(sketch, "E4962", {"start": v(192.08, -108.82) * mm, "end": v(191.93, -108.7) * mm});
            skLineSegment(sketch, "E4963", {"start": v(191.93, -108.7) * mm, "end": v(191.8, -108.57) * mm});
            skLineSegment(sketch, "E4964", {"start": v(191.8, -108.57) * mm, "end": v(191.7, -108.44) * mm});
            skLineSegment(sketch, "E4965", {"start": v(191.7, -108.44) * mm, "end": v(191.63, -108.42) * mm});
            skLineSegment(sketch, "E4966", {"start": v(191.63, -108.42) * mm, "end": v(191.47, -108.32) * mm});
            skLineSegment(sketch, "E4967", {"start": v(191.47, -108.32) * mm, "end": v(191.32, -108.2) * mm});
            skLineSegment(sketch, "E4968", {"start": v(191.32, -108.2) * mm, "end": v(191.19, -108.07) * mm});
            skLineSegment(sketch, "E4969", {"start": v(191.19, -108.07) * mm, "end": v(191.09, -107.94) * mm});
            skLineSegment(sketch, "E4970", {"start": v(191.09, -107.94) * mm, "end": v(191.03, -107.9) * mm});
            skLineSegment(sketch, "E4971", {"start": v(191.03, -107.9) * mm, "end": v(190.87, -107.8) * mm});
            skLineSegment(sketch, "E4972", {"start": v(190.87, -107.8) * mm, "end": v(190.72, -107.69) * mm});
            skLineSegment(sketch, "E4973", {"start": v(190.72, -107.69) * mm, "end": v(190.59, -107.55) * mm});
            skLineSegment(sketch, "E4974", {"start": v(190.59, -107.55) * mm, "end": v(190.49, -107.42) * mm});
            skLineSegment(sketch, "E4975", {"start": v(190.49, -107.42) * mm, "end": v(190.43, -107.39) * mm});
            skLineSegment(sketch, "E4976", {"start": v(190.43, -107.39) * mm, "end": v(190.27, -107.28) * mm});
            skLineSegment(sketch, "E4977", {"start": v(190.27, -107.28) * mm, "end": v(190.13, -107.16) * mm});
            skLineSegment(sketch, "E4978", {"start": v(190.13, -107.16) * mm, "end": v(190, -107.02) * mm});
            skLineSegment(sketch, "E4979", {"start": v(190, -107.02) * mm, "end": v(189.9, -106.89) * mm});
            skLineSegment(sketch, "E4980", {"start": v(189.9, -106.89) * mm, "end": v(189.84, -106.86) * mm});
            skLineSegment(sketch, "E4981", {"start": v(189.84, -106.86) * mm, "end": v(189.69, -106.75) * mm});
            skLineSegment(sketch, "E4982", {"start": v(189.69, -106.75) * mm, "end": v(189.54, -106.63) * mm});
            skLineSegment(sketch, "E4983", {"start": v(189.54, -106.63) * mm, "end": v(189.42, -106.49) * mm});
            skLineSegment(sketch, "E4984", {"start": v(189.42, -106.49) * mm, "end": v(189.32, -106.35) * mm});
            skLineSegment(sketch, "E4985", {"start": v(189.32, -106.35) * mm, "end": v(189.26, -106.32) * mm});
            skLineSegment(sketch, "E4986", {"start": v(189.26, -106.32) * mm, "end": v(189.11, -106.2) * mm});
            skLineSegment(sketch, "E4987", {"start": v(189.11, -106.2) * mm, "end": v(188.97, -106.08) * mm});
            skLineSegment(sketch, "E4988", {"start": v(188.97, -106.08) * mm, "end": v(188.85, -105.94) * mm});
            skLineSegment(sketch, "E4989", {"start": v(188.85, -105.94) * mm, "end": v(188.76, -105.8) * mm});
            skLineSegment(sketch, "E4990", {"start": v(188.76, -105.8) * mm, "end": v(188.7, -105.77) * mm});
            skLineSegment(sketch, "E4991", {"start": v(188.7, -105.77) * mm, "end": v(188.54, -105.66) * mm});
            skLineSegment(sketch, "E4992", {"start": v(188.54, -105.66) * mm, "end": v(188.4, -105.53) * mm});
            skLineSegment(sketch, "E4993", {"start": v(188.4, -105.53) * mm, "end": v(188.29, -105.38) * mm});
            skLineSegment(sketch, "E4994", {"start": v(188.29, -105.38) * mm, "end": v(188.19, -105.22) * mm});
            skLineSegment(sketch, "E4995", {"start": v(188.19, -105.22) * mm, "end": v(188.1, -105.05) * mm});
            skLineSegment(sketch, "E4996", {"start": v(188.1, -105.05) * mm, "end": v(188.05, -104.87) * mm});
            skLineSegment(sketch, "E4997", {"start": v(188.05, -104.87) * mm, "end": v(188.01, -104.69) * mm});
            skLineSegment(sketch, "E4998", {"start": v(188.01, -104.69) * mm, "end": v(188, -104.5) * mm});
            skLineSegment(sketch, "E4999", {"start": v(188, -104.5) * mm, "end": v(188.01, -104.31) * mm});
            skLineSegment(sketch, "E5000", {"start": v(188.01, -104.31) * mm, "end": v(188.05, -104.13) * mm});
            skLineSegment(sketch, "E5001", {"start": v(188.05, -104.13) * mm, "end": v(188.1, -103.95) * mm});
            skLineSegment(sketch, "E5002", {"start": v(188.1, -103.95) * mm, "end": v(188.19, -103.78) * mm});
            skLineSegment(sketch, "E5003", {"start": v(188.19, -103.78) * mm, "end": v(188.29, -103.62) * mm});
            skLineSegment(sketch, "E5004", {"start": v(188.29, -103.62) * mm, "end": v(188.4, -103.47) * mm});
            skLineSegment(sketch, "E5005", {"start": v(188.4, -103.47) * mm, "end": v(188.54, -103.34) * mm});
            skLineSegment(sketch, "E5006", {"start": v(188.54, -103.34) * mm, "end": v(188.7, -103.23) * mm});
            skLineSegment(sketch, "E5007", {"start": v(188.7, -103.23) * mm, "end": v(188.86, -103.14) * mm});
            skLineSegment(sketch, "E5008", {"start": v(188.86, -103.14) * mm, "end": v(189.04, -103.07) * mm});
            skLineSegment(sketch, "E5009", {"start": v(189.04, -103.07) * mm, "end": v(189.22, -103.03) * mm});
            skLineSegment(sketch, "E5010", {"start": v(189.22, -103.03) * mm, "end": v(189.4, -103) * mm});
            skLineSegment(sketch, "E5011", {"start": v(189.4, -103) * mm, "end": v(189.6, -103) * mm});
            skLineSegment(sketch, "E5012", {"start": v(189.6, -103) * mm, "end": v(189.78, -103.03) * mm});
            skLineSegment(sketch, "E5013", {"start": v(189.78, -103.03) * mm, "end": v(189.96, -103.07) * mm});
            skLineSegment(sketch, "E5014", {"start": v(189.96, -103.07) * mm, "end": v(190.14, -103.14) * mm});
            skLineSegment(sketch, "E5015", {"start": v(190.14, -103.14) * mm, "end": v(190.3, -103.23) * mm});
            skLineSegment(sketch, "E5016", {"start": v(190.3, -103.23) * mm, "end": v(190.46, -103.34) * mm});
            skLineSegment(sketch, "E5017", {"start": v(190.46, -103.34) * mm, "end": v(190.6, -103.47) * mm});
            skLineSegment(sketch, "E5018", {"start": v(190.6, -103.47) * mm, "end": v(190.71, -103.62) * mm});
            skLineSegment(sketch, "E5019", {"start": v(190.71, -103.62) * mm, "end": v(190.79, -103.74) * mm});
            skLineSegment(sketch, "E5020", {"start": v(190.79, -103.74) * mm, "end": v(190.83, -103.76) * mm});
            skLineSegment(sketch, "E5021", {"start": v(190.83, -103.76) * mm, "end": v(190.98, -103.86) * mm});
            skLineSegment(sketch, "E5022", {"start": v(190.98, -103.86) * mm, "end": v(191.12, -104) * mm});
            skLineSegment(sketch, "E5023", {"start": v(191.12, -104) * mm, "end": v(191.24, -104.13) * mm});
            skLineSegment(sketch, "E5024", {"start": v(191.24, -104.13) * mm, "end": v(191.32, -104.25) * mm});
            skLineSegment(sketch, "E5025", {"start": v(191.32, -104.25) * mm, "end": v(191.36, -104.27) * mm});
            skLineSegment(sketch, "E5026", {"start": v(191.36, -104.27) * mm, "end": v(191.52, -104.38) * mm});
            skLineSegment(sketch, "E5027", {"start": v(191.52, -104.38) * mm, "end": v(191.66, -104.5) * mm});
            skLineSegment(sketch, "E5028", {"start": v(191.66, -104.5) * mm, "end": v(191.78, -104.64) * mm});
            skLineSegment(sketch, "E5029", {"start": v(191.78, -104.64) * mm, "end": v(191.86, -104.75) * mm});
            skLineSegment(sketch, "E5030", {"start": v(191.86, -104.75) * mm, "end": v(191.9, -104.77) * mm});
            skLineSegment(sketch, "E5031", {"start": v(191.9, -104.77) * mm, "end": v(192.06, -104.88) * mm});
            skLineSegment(sketch, "E5032", {"start": v(192.06, -104.88) * mm, "end": v(192.2, -105) * mm});
            skLineSegment(sketch, "E5033", {"start": v(192.2, -105) * mm, "end": v(192.33, -105.14) * mm});
            skLineSegment(sketch, "E5034", {"start": v(192.33, -105.14) * mm, "end": v(192.41, -105.25) * mm});
            skLineSegment(sketch, "E5035", {"start": v(192.41, -105.25) * mm, "end": v(192.45, -105.27) * mm});
            skLineSegment(sketch, "E5036", {"start": v(192.45, -105.27) * mm, "end": v(192.61, -105.37) * mm});
            skLineSegment(sketch, "E5037", {"start": v(192.61, -105.37) * mm, "end": v(192.76, -105.49) * mm});
            skLineSegment(sketch, "E5038", {"start": v(192.76, -105.49) * mm, "end": v(192.89, -105.62) * mm});
            skLineSegment(sketch, "E5039", {"start": v(192.89, -105.62) * mm, "end": v(192.97, -105.73) * mm});
            skLineSegment(sketch, "E5040", {"start": v(192.97, -105.73) * mm, "end": v(193, -105.75) * mm});
            skLineSegment(sketch, "E5041", {"start": v(193, -105.75) * mm, "end": v(193.17, -105.85) * mm});
            skLineSegment(sketch, "E5042", {"start": v(193.17, -105.85) * mm, "end": v(193.32, -105.97) * mm});
            skLineSegment(sketch, "E5043", {"start": v(193.32, -105.97) * mm, "end": v(193.45, -106.1) * mm});
            skLineSegment(sketch, "E5044", {"start": v(193.45, -106.1) * mm, "end": v(193.54, -106.2) * mm});
            skLineSegment(sketch, "E5045", {"start": v(193.54, -106.2) * mm, "end": v(193.58, -106.23) * mm});
            skLineSegment(sketch, "E5046", {"start": v(193.58, -106.23) * mm, "end": v(193.74, -106.32) * mm});
            skLineSegment(sketch, "E5047", {"start": v(193.74, -106.32) * mm, "end": v(193.89, -106.44) * mm});
            skLineSegment(sketch, "E5048", {"start": v(193.89, -106.44) * mm, "end": v(194.03, -106.57) * mm});
            skLineSegment(sketch, "E5049", {"start": v(194.03, -106.57) * mm, "end": v(194.11, -106.68) * mm});
            skLineSegment(sketch, "E5050", {"start": v(194.11, -106.68) * mm, "end": v(194.15, -106.7) * mm});
            skLineSegment(sketch, "E5051", {"start": v(194.15, -106.7) * mm, "end": v(194.32, -106.78) * mm});
            skLineSegment(sketch, "E5052", {"start": v(194.32, -106.78) * mm, "end": v(194.47, -106.9) * mm});
            skLineSegment(sketch, "E5053", {"start": v(194.47, -106.9) * mm, "end": v(194.6, -107.02) * mm});
            skLineSegment(sketch, "E5054", {"start": v(194.6, -107.02) * mm, "end": v(194.7, -107.13) * mm});
            skLineSegment(sketch, "E5055", {"start": v(194.7, -107.13) * mm, "end": v(194.74, -107.15) * mm});
            skLineSegment(sketch, "E5056", {"start": v(194.74, -107.15) * mm, "end": v(194.9, -107.23) * mm});
            skLineSegment(sketch, "E5057", {"start": v(194.9, -107.23) * mm, "end": v(195.06, -107.34) * mm});
            skLineSegment(sketch, "E5058", {"start": v(195.06, -107.34) * mm, "end": v(195.2, -107.47) * mm});
            skLineSegment(sketch, "E5059", {"start": v(195.2, -107.47) * mm, "end": v(195.32, -107.61) * mm});
            skLineSegment(sketch, "E5060", {"start": v(195.32, -107.61) * mm, "end": v(195.42, -107.77) * mm});
            skLineSegment(sketch, "E5061", {"start": v(195.42, -107.77) * mm, "end": v(195.5, -107.94) * mm});
            skLineSegment(sketch, "E5062", {"start": v(195.5, -107.94) * mm, "end": v(195.56, -108.12) * mm});
            skLineSegment(sketch, "E5063", {"start": v(195.56, -108.12) * mm, "end": v(195.6, -108.3) * mm});
            skLineSegment(sketch, "E5064", {"start": v(195.6, -108.3) * mm, "end": v(195.62, -108.5) * mm});
            skLineSegment(sketch, "E5065", {"start": v(195.62, -108.5) * mm, "end": v(195.6, -108.68) * mm});
            skLineSegment(sketch, "E5066", {"start": v(195.6, -108.68) * mm, "end": v(195.57, -108.87) * mm});
            skLineSegment(sketch, "E5067", {"start": v(195.57, -108.87) * mm, "end": v(195.52, -109.05) * mm});
            skLineSegment(sketch, "E5068", {"start": v(195.52, -109.05) * mm, "end": v(195.44, -109.22) * mm});
            skLineSegment(sketch, "E5069", {"start": v(195.44, -109.22) * mm, "end": v(195.34, -109.38) * mm});
            skLineSegment(sketch, "E5070", {"start": v(195.34, -109.38) * mm, "end": v(195.22, -109.52) * mm});
            skLineSegment(sketch, "E5071", {"start": v(195.22, -109.52) * mm, "end": v(195.09, -109.66) * mm});
            skLineSegment(sketch, "E5072", {"start": v(195.09, -109.66) * mm, "end": v(194.94, -109.77) * mm});
            skLineSegment(sketch, "E5073", {"start": v(194.94, -109.77) * mm, "end": v(194.77, -109.86) * mm});
            skLineSegment(sketch, "E5074", {"start": v(194.77, -109.86) * mm, "end": v(194.6, -109.93) * mm});
            skLineSegment(sketch, "E5075", {"start": v(194.6, -109.93) * mm, "end": v(194.42, -109.98) * mm});
            skLineSegment(sketch, "E5076", {"start": v(194.42, -109.98) * mm, "end": v(194.23, -110) * mm});
            skLineSegment(sketch, "E5077", {"start": v(194.23, -110) * mm, "end": v(194.04, -110.01) * mm});
            skLineSegment(sketch, "E5078", {"start": v(194.04, -110.01) * mm, "end": v(193.86, -109.99) * mm});
            skLineSegment(sketch, "E5079", {"start": v(108.4, -128.7) * mm, "end": v(108.22, -128.67) * mm});
            skLineSegment(sketch, "E5080", {"start": v(108.22, -128.67) * mm, "end": v(108.04, -128.63) * mm});
            skLineSegment(sketch, "E5081", {"start": v(108.04, -128.63) * mm, "end": v(107.86, -128.56) * mm});
            skLineSegment(sketch, "E5082", {"start": v(107.86, -128.56) * mm, "end": v(107.7, -128.47) * mm});
            skLineSegment(sketch, "E5083", {"start": v(107.7, -128.47) * mm, "end": v(107.54, -128.36) * mm});
            skLineSegment(sketch, "E5084", {"start": v(107.54, -128.36) * mm, "end": v(107.4, -128.23) * mm});
            skLineSegment(sketch, "E5085", {"start": v(107.4, -128.23) * mm, "end": v(107.29, -128.08) * mm});
            skLineSegment(sketch, "E5086", {"start": v(107.29, -128.08) * mm, "end": v(107.19, -127.92) * mm});
            skLineSegment(sketch, "E5087", {"start": v(107.19, -127.92) * mm, "end": v(107.1, -127.75) * mm});
            skLineSegment(sketch, "E5088", {"start": v(107.1, -127.75) * mm, "end": v(107.05, -127.57) * mm});
            skLineSegment(sketch, "E5089", {"start": v(107.05, -127.57) * mm, "end": v(107.01, -127.39) * mm});
            skLineSegment(sketch, "E5090", {"start": v(107.01, -127.39) * mm, "end": v(107, -127.2) * mm});
            skLineSegment(sketch, "E5091", {"start": v(107, -127.2) * mm, "end": v(107.01, -127.01) * mm});
            skLineSegment(sketch, "E5092", {"start": v(107.01, -127.01) * mm, "end": v(107.05, -126.83) * mm});
            skLineSegment(sketch, "E5093", {"start": v(107.05, -126.83) * mm, "end": v(107.1, -126.65) * mm});
            skLineSegment(sketch, "E5094", {"start": v(107.1, -126.65) * mm, "end": v(107.19, -126.48) * mm});
            skLineSegment(sketch, "E5095", {"start": v(107.19, -126.48) * mm, "end": v(107.29, -126.32) * mm});
            skLineSegment(sketch, "E5096", {"start": v(107.29, -126.32) * mm, "end": v(107.4, -126.17) * mm});
            skLineSegment(sketch, "E5097", {"start": v(107.4, -126.17) * mm, "end": v(107.54, -126.04) * mm});
            skLineSegment(sketch, "E5098", {"start": v(107.54, -126.04) * mm, "end": v(107.7, -125.93) * mm});
            skLineSegment(sketch, "E5099", {"start": v(107.7, -125.93) * mm, "end": v(107.86, -125.84) * mm});
            skLineSegment(sketch, "E5100", {"start": v(107.86, -125.84) * mm, "end": v(108.04, -125.77) * mm});
            skLineSegment(sketch, "E5101", {"start": v(108.04, -125.77) * mm, "end": v(108.22, -125.73) * mm});
            skLineSegment(sketch, "E5102", {"start": v(108.22, -125.73) * mm, "end": v(108.4, -125.7) * mm});
            skLineSegment(sketch, "E5103", {"start": v(108.4, -125.7) * mm, "end": v(108.6, -125.7) * mm});
            skLineSegment(sketch, "E5104", {"start": v(108.6, -125.7) * mm, "end": v(108.78, -125.73) * mm});
            skLineSegment(sketch, "E5105", {"start": v(108.78, -125.73) * mm, "end": v(108.96, -125.77) * mm});
            skLineSegment(sketch, "E5106", {"start": v(108.96, -125.77) * mm, "end": v(109.14, -125.84) * mm});
            skLineSegment(sketch, "E5107", {"start": v(109.14, -125.84) * mm, "end": v(109.3, -125.93) * mm});
            skLineSegment(sketch, "E5108", {"start": v(109.3, -125.93) * mm, "end": v(109.46, -126.04) * mm});
            skLineSegment(sketch, "E5109", {"start": v(109.46, -126.04) * mm, "end": v(109.6, -126.17) * mm});
            skLineSegment(sketch, "E5110", {"start": v(109.6, -126.17) * mm, "end": v(109.71, -126.32) * mm});
            skLineSegment(sketch, "E5111", {"start": v(109.71, -126.32) * mm, "end": v(109.81, -126.48) * mm});
            skLineSegment(sketch, "E5112", {"start": v(109.81, -126.48) * mm, "end": v(109.9, -126.65) * mm});
            skLineSegment(sketch, "E5113", {"start": v(109.9, -126.65) * mm, "end": v(109.95, -126.83) * mm});
            skLineSegment(sketch, "E5114", {"start": v(109.95, -126.83) * mm, "end": v(109.99, -127.01) * mm});
            skLineSegment(sketch, "E5115", {"start": v(109.99, -127.01) * mm, "end": v(110, -127.2) * mm});
            skLineSegment(sketch, "E5116", {"start": v(110, -127.2) * mm, "end": v(109.99, -127.39) * mm});
            skLineSegment(sketch, "E5117", {"start": v(109.99, -127.39) * mm, "end": v(109.95, -127.57) * mm});
            skLineSegment(sketch, "E5118", {"start": v(109.95, -127.57) * mm, "end": v(109.9, -127.75) * mm});
            skLineSegment(sketch, "E5119", {"start": v(109.9, -127.75) * mm, "end": v(109.81, -127.92) * mm});
            skLineSegment(sketch, "E5120", {"start": v(109.81, -127.92) * mm, "end": v(109.71, -128.08) * mm});
            skLineSegment(sketch, "E5121", {"start": v(109.71, -128.08) * mm, "end": v(109.6, -128.23) * mm});
            skLineSegment(sketch, "E5122", {"start": v(109.6, -128.23) * mm, "end": v(109.46, -128.36) * mm});
            skLineSegment(sketch, "E5123", {"start": v(109.46, -128.36) * mm, "end": v(109.3, -128.47) * mm});
            skLineSegment(sketch, "E5124", {"start": v(109.3, -128.47) * mm, "end": v(109.14, -128.56) * mm});
            skLineSegment(sketch, "E5125", {"start": v(109.14, -128.56) * mm, "end": v(108.96, -128.63) * mm});
            skLineSegment(sketch, "E5126", {"start": v(108.96, -128.63) * mm, "end": v(108.78, -128.67) * mm});
            skLineSegment(sketch, "E5127", {"start": v(108.78, -128.67) * mm, "end": v(108.6, -128.7) * mm});
            skLineSegment(sketch, "E5128", {"start": v(108.6, -128.7) * mm, "end": v(108.4, -128.7) * mm});
            skLineSegment(sketch, "E5129", {"start": v(98.9, -128.7) * mm, "end": v(98.72, -128.67) * mm});
            skLineSegment(sketch, "E5130", {"start": v(98.72, -128.67) * mm, "end": v(98.54, -128.63) * mm});
            skLineSegment(sketch, "E5131", {"start": v(98.54, -128.63) * mm, "end": v(98.36, -128.56) * mm});
            skLineSegment(sketch, "E5132", {"start": v(98.36, -128.56) * mm, "end": v(98.2, -128.47) * mm});
            skLineSegment(sketch, "E5133", {"start": v(98.2, -128.47) * mm, "end": v(98.04, -128.36) * mm});
            skLineSegment(sketch, "E5134", {"start": v(98.04, -128.36) * mm, "end": v(97.9, -128.23) * mm});
            skLineSegment(sketch, "E5135", {"start": v(97.9, -128.23) * mm, "end": v(97.79, -128.08) * mm});
            skLineSegment(sketch, "E5136", {"start": v(97.79, -128.08) * mm, "end": v(97.69, -127.92) * mm});
            skLineSegment(sketch, "E5137", {"start": v(97.69, -127.92) * mm, "end": v(97.6, -127.75) * mm});
            skLineSegment(sketch, "E5138", {"start": v(97.6, -127.75) * mm, "end": v(97.55, -127.57) * mm});
            skLineSegment(sketch, "E5139", {"start": v(97.55, -127.57) * mm, "end": v(97.51, -127.39) * mm});
            skLineSegment(sketch, "E5140", {"start": v(97.51, -127.39) * mm, "end": v(97.5, -127.2) * mm});
            skLineSegment(sketch, "E5141", {"start": v(97.5, -127.2) * mm, "end": v(97.51, -127.01) * mm});
            skLineSegment(sketch, "E5142", {"start": v(97.51, -127.01) * mm, "end": v(97.55, -126.83) * mm});
            skLineSegment(sketch, "E5143", {"start": v(97.55, -126.83) * mm, "end": v(97.6, -126.65) * mm});
            skLineSegment(sketch, "E5144", {"start": v(97.6, -126.65) * mm, "end": v(97.69, -126.48) * mm});
            skLineSegment(sketch, "E5145", {"start": v(97.69, -126.48) * mm, "end": v(97.79, -126.32) * mm});
            skLineSegment(sketch, "E5146", {"start": v(97.79, -126.32) * mm, "end": v(97.9, -126.17) * mm});
            skLineSegment(sketch, "E5147", {"start": v(97.9, -126.17) * mm, "end": v(98.04, -126.04) * mm});
            skLineSegment(sketch, "E5148", {"start": v(98.04, -126.04) * mm, "end": v(98.2, -125.93) * mm});
            skLineSegment(sketch, "E5149", {"start": v(98.2, -125.93) * mm, "end": v(98.36, -125.84) * mm});
            skLineSegment(sketch, "E5150", {"start": v(98.36, -125.84) * mm, "end": v(98.54, -125.77) * mm});
            skLineSegment(sketch, "E5151", {"start": v(98.54, -125.77) * mm, "end": v(98.72, -125.73) * mm});
            skLineSegment(sketch, "E5152", {"start": v(98.72, -125.73) * mm, "end": v(98.9, -125.7) * mm});
            skLineSegment(sketch, "E5153", {"start": v(98.9, -125.7) * mm, "end": v(99.1, -125.7) * mm});
            skLineSegment(sketch, "E5154", {"start": v(99.1, -125.7) * mm, "end": v(99.28, -125.73) * mm});
            skLineSegment(sketch, "E5155", {"start": v(99.28, -125.73) * mm, "end": v(99.46, -125.77) * mm});
            skLineSegment(sketch, "E5156", {"start": v(99.46, -125.77) * mm, "end": v(99.64, -125.84) * mm});
            skLineSegment(sketch, "E5157", {"start": v(99.64, -125.84) * mm, "end": v(99.8, -125.93) * mm});
            skLineSegment(sketch, "E5158", {"start": v(99.8, -125.93) * mm, "end": v(99.96, -126.04) * mm});
            skLineSegment(sketch, "E5159", {"start": v(99.96, -126.04) * mm, "end": v(100.1, -126.17) * mm});
            skLineSegment(sketch, "E5160", {"start": v(100.1, -126.17) * mm, "end": v(100.21, -126.32) * mm});
            skLineSegment(sketch, "E5161", {"start": v(100.21, -126.32) * mm, "end": v(100.31, -126.48) * mm});
            skLineSegment(sketch, "E5162", {"start": v(100.31, -126.48) * mm, "end": v(100.4, -126.65) * mm});
            skLineSegment(sketch, "E5163", {"start": v(100.4, -126.65) * mm, "end": v(100.45, -126.83) * mm});
            skLineSegment(sketch, "E5164", {"start": v(100.45, -126.83) * mm, "end": v(100.49, -127.01) * mm});
            skLineSegment(sketch, "E5165", {"start": v(100.49, -127.01) * mm, "end": v(100.5, -127.2) * mm});
            skLineSegment(sketch, "E5166", {"start": v(100.5, -127.2) * mm, "end": v(100.49, -127.39) * mm});
            skLineSegment(sketch, "E5167", {"start": v(100.49, -127.39) * mm, "end": v(100.45, -127.57) * mm});
            skLineSegment(sketch, "E5168", {"start": v(100.45, -127.57) * mm, "end": v(100.4, -127.75) * mm});
            skLineSegment(sketch, "E5169", {"start": v(100.4, -127.75) * mm, "end": v(100.31, -127.92) * mm});
            skLineSegment(sketch, "E5170", {"start": v(100.31, -127.92) * mm, "end": v(100.21, -128.08) * mm});
            skLineSegment(sketch, "E5171", {"start": v(100.21, -128.08) * mm, "end": v(100.1, -128.23) * mm});
            skLineSegment(sketch, "E5172", {"start": v(100.1, -128.23) * mm, "end": v(99.96, -128.36) * mm});
            skLineSegment(sketch, "E5173", {"start": v(99.96, -128.36) * mm, "end": v(99.8, -128.47) * mm});
            skLineSegment(sketch, "E5174", {"start": v(99.8, -128.47) * mm, "end": v(99.64, -128.56) * mm});
            skLineSegment(sketch, "E5175", {"start": v(99.64, -128.56) * mm, "end": v(99.46, -128.63) * mm});
            skLineSegment(sketch, "E5176", {"start": v(99.46, -128.63) * mm, "end": v(99.28, -128.67) * mm});
            skLineSegment(sketch, "E5177", {"start": v(99.28, -128.67) * mm, "end": v(99.1, -128.7) * mm});
            skLineSegment(sketch, "E5178", {"start": v(99.1, -128.7) * mm, "end": v(98.9, -128.7) * mm});
            skLineSegment(sketch, "E5179", {"start": v(369.87, -142) * mm, "end": v(369.62, -141.97) * mm});
            skLineSegment(sketch, "E5180", {"start": v(369.62, -141.97) * mm, "end": v(369.38, -141.9) * mm});
            skLineSegment(sketch, "E5181", {"start": v(369.38, -141.9) * mm, "end": v(369.15, -141.8) * mm});
            skLineSegment(sketch, "E5182", {"start": v(369.15, -141.8) * mm, "end": v(368.93, -141.69) * mm});
            skLineSegment(sketch, "E5183", {"start": v(368.93, -141.69) * mm, "end": v(368.73, -141.54) * mm});
            skLineSegment(sketch, "E5184", {"start": v(368.73, -141.54) * mm, "end": v(368.54, -141.37) * mm});
            skLineSegment(sketch, "E5185", {"start": v(368.54, -141.37) * mm, "end": v(368.38, -141.18) * mm});
            skLineSegment(sketch, "E5186", {"start": v(368.38, -141.18) * mm, "end": v(368.25, -140.96) * mm});
            skLineSegment(sketch, "E5187", {"start": v(368.25, -140.96) * mm, "end": v(368.14, -140.74) * mm});
            skLineSegment(sketch, "E5188", {"start": v(368.14, -140.74) * mm, "end": v(368.06, -140.5) * mm});
            skLineSegment(sketch, "E5189", {"start": v(368.06, -140.5) * mm, "end": v(368.02, -140.25) * mm});
            skLineSegment(sketch, "E5190", {"start": v(368.02, -140.25) * mm, "end": v(368, -140) * mm});
            skLineSegment(sketch, "E5191", {"start": v(368, -140) * mm, "end": v(368.02, -139.75) * mm});
            skLineSegment(sketch, "E5192", {"start": v(368.02, -139.75) * mm, "end": v(368.06, -139.5) * mm});
            skLineSegment(sketch, "E5193", {"start": v(368.06, -139.5) * mm, "end": v(368.14, -139.26) * mm});
            skLineSegment(sketch, "E5194", {"start": v(368.14, -139.26) * mm, "end": v(368.25, -139.04) * mm});
            skLineSegment(sketch, "E5195", {"start": v(368.25, -139.04) * mm, "end": v(368.38, -138.82) * mm});
            skLineSegment(sketch, "E5196", {"start": v(368.38, -138.82) * mm, "end": v(368.54, -138.63) * mm});
            skLineSegment(sketch, "E5197", {"start": v(368.54, -138.63) * mm, "end": v(368.73, -138.46) * mm});
            skLineSegment(sketch, "E5198", {"start": v(368.73, -138.46) * mm, "end": v(368.93, -138.31) * mm});
            skLineSegment(sketch, "E5199", {"start": v(368.93, -138.31) * mm, "end": v(369.15, -138.2) * mm});
            skLineSegment(sketch, "E5200", {"start": v(369.15, -138.2) * mm, "end": v(369.38, -138.1) * mm});
            skLineSegment(sketch, "E5201", {"start": v(369.38, -138.1) * mm, "end": v(369.62, -138.03) * mm});
            skLineSegment(sketch, "E5202", {"start": v(369.62, -138.03) * mm, "end": v(369.87, -138) * mm});
            skLineSegment(sketch, "E5203", {"start": v(369.87, -138) * mm, "end": v(370.13, -138) * mm});
            skLineSegment(sketch, "E5204", {"start": v(370.13, -138) * mm, "end": v(370.38, -138.03) * mm});
            skLineSegment(sketch, "E5205", {"start": v(370.38, -138.03) * mm, "end": v(370.62, -138.1) * mm});
            skLineSegment(sketch, "E5206", {"start": v(370.62, -138.1) * mm, "end": v(370.85, -138.2) * mm});
            skLineSegment(sketch, "E5207", {"start": v(370.85, -138.2) * mm, "end": v(371.07, -138.31) * mm});
            skLineSegment(sketch, "E5208", {"start": v(371.07, -138.31) * mm, "end": v(371.27, -138.46) * mm});
            skLineSegment(sketch, "E5209", {"start": v(371.27, -138.46) * mm, "end": v(371.46, -138.63) * mm});
            skLineSegment(sketch, "E5210", {"start": v(371.46, -138.63) * mm, "end": v(371.62, -138.82) * mm});
            skLineSegment(sketch, "E5211", {"start": v(371.62, -138.82) * mm, "end": v(371.75, -139.04) * mm});
            skLineSegment(sketch, "E5212", {"start": v(371.75, -139.04) * mm, "end": v(371.86, -139.26) * mm});
            skLineSegment(sketch, "E5213", {"start": v(371.86, -139.26) * mm, "end": v(371.94, -139.5) * mm});
            skLineSegment(sketch, "E5214", {"start": v(371.94, -139.5) * mm, "end": v(371.98, -139.75) * mm});
            skLineSegment(sketch, "E5215", {"start": v(371.98, -139.75) * mm, "end": v(372, -140) * mm});
            skLineSegment(sketch, "E5216", {"start": v(372, -140) * mm, "end": v(371.98, -140.25) * mm});
            skLineSegment(sketch, "E5217", {"start": v(371.98, -140.25) * mm, "end": v(371.94, -140.5) * mm});
            skLineSegment(sketch, "E5218", {"start": v(371.94, -140.5) * mm, "end": v(371.86, -140.74) * mm});
            skLineSegment(sketch, "E5219", {"start": v(371.86, -140.74) * mm, "end": v(371.75, -140.96) * mm});
            skLineSegment(sketch, "E5220", {"start": v(371.75, -140.96) * mm, "end": v(371.62, -141.18) * mm});
            skLineSegment(sketch, "E5221", {"start": v(371.62, -141.18) * mm, "end": v(371.46, -141.37) * mm});
            skLineSegment(sketch, "E5222", {"start": v(371.46, -141.37) * mm, "end": v(371.27, -141.54) * mm});
            skLineSegment(sketch, "E5223", {"start": v(371.27, -141.54) * mm, "end": v(371.07, -141.69) * mm});
            skLineSegment(sketch, "E5224", {"start": v(371.07, -141.69) * mm, "end": v(370.85, -141.8) * mm});
            skLineSegment(sketch, "E5225", {"start": v(370.85, -141.8) * mm, "end": v(370.62, -141.9) * mm});
            skLineSegment(sketch, "E5226", {"start": v(370.62, -141.9) * mm, "end": v(370.38, -141.97) * mm});
            skLineSegment(sketch, "E5227", {"start": v(370.38, -141.97) * mm, "end": v(370.13, -142) * mm});
            skLineSegment(sketch, "E5228", {"start": v(370.13, -142) * mm, "end": v(369.87, -142) * mm});
            skLineSegment(sketch, "E5229", {"start": v(39.87, -142) * mm, "end": v(39.63, -141.97) * mm});
            skLineSegment(sketch, "E5230", {"start": v(39.63, -141.97) * mm, "end": v(39.38, -141.9) * mm});
            skLineSegment(sketch, "E5231", {"start": v(39.38, -141.9) * mm, "end": v(39.15, -141.8) * mm});
            skLineSegment(sketch, "E5232", {"start": v(39.15, -141.8) * mm, "end": v(38.93, -141.69) * mm});
            skLineSegment(sketch, "E5233", {"start": v(38.93, -141.69) * mm, "end": v(38.73, -141.54) * mm});
            skLineSegment(sketch, "E5234", {"start": v(38.73, -141.54) * mm, "end": v(38.54, -141.37) * mm});
            skLineSegment(sketch, "E5235", {"start": v(38.54, -141.37) * mm, "end": v(38.38, -141.18) * mm});
            skLineSegment(sketch, "E5236", {"start": v(38.38, -141.18) * mm, "end": v(38.25, -140.96) * mm});
            skLineSegment(sketch, "E5237", {"start": v(38.25, -140.96) * mm, "end": v(38.14, -140.74) * mm});
            skLineSegment(sketch, "E5238", {"start": v(38.14, -140.74) * mm, "end": v(38.06, -140.5) * mm});
            skLineSegment(sketch, "E5239", {"start": v(38.06, -140.5) * mm, "end": v(38.02, -140.25) * mm});
            skLineSegment(sketch, "E5240", {"start": v(38.02, -140.25) * mm, "end": v(38, -140) * mm});
            skLineSegment(sketch, "E5241", {"start": v(38, -140) * mm, "end": v(38.02, -139.75) * mm});
            skLineSegment(sketch, "E5242", {"start": v(38.02, -139.75) * mm, "end": v(38.06, -139.5) * mm});
            skLineSegment(sketch, "E5243", {"start": v(38.06, -139.5) * mm, "end": v(38.14, -139.26) * mm});
            skLineSegment(sketch, "E5244", {"start": v(38.14, -139.26) * mm, "end": v(38.25, -139.04) * mm});
            skLineSegment(sketch, "E5245", {"start": v(38.25, -139.04) * mm, "end": v(38.38, -138.82) * mm});
            skLineSegment(sketch, "E5246", {"start": v(38.38, -138.82) * mm, "end": v(38.54, -138.63) * mm});
            skLineSegment(sketch, "E5247", {"start": v(38.54, -138.63) * mm, "end": v(38.73, -138.46) * mm});
            skLineSegment(sketch, "E5248", {"start": v(38.73, -138.46) * mm, "end": v(38.93, -138.31) * mm});
            skLineSegment(sketch, "E5249", {"start": v(38.93, -138.31) * mm, "end": v(39.15, -138.2) * mm});
            skLineSegment(sketch, "E5250", {"start": v(39.15, -138.2) * mm, "end": v(39.38, -138.1) * mm});
            skLineSegment(sketch, "E5251", {"start": v(39.38, -138.1) * mm, "end": v(39.63, -138.03) * mm});
            skLineSegment(sketch, "E5252", {"start": v(39.63, -138.03) * mm, "end": v(39.87, -138) * mm});
            skLineSegment(sketch, "E5253", {"start": v(39.87, -138) * mm, "end": v(40.13, -138) * mm});
            skLineSegment(sketch, "E5254", {"start": v(40.13, -138) * mm, "end": v(40.37, -138.03) * mm});
            skLineSegment(sketch, "E5255", {"start": v(40.37, -138.03) * mm, "end": v(40.62, -138.1) * mm});
            skLineSegment(sketch, "E5256", {"start": v(40.62, -138.1) * mm, "end": v(40.85, -138.2) * mm});
            skLineSegment(sketch, "E5257", {"start": v(40.85, -138.2) * mm, "end": v(41.07, -138.31) * mm});
            skLineSegment(sketch, "E5258", {"start": v(41.07, -138.31) * mm, "end": v(41.27, -138.46) * mm});
            skLineSegment(sketch, "E5259", {"start": v(41.27, -138.46) * mm, "end": v(41.46, -138.63) * mm});
            skLineSegment(sketch, "E5260", {"start": v(41.46, -138.63) * mm, "end": v(41.62, -138.82) * mm});
            skLineSegment(sketch, "E5261", {"start": v(41.62, -138.82) * mm, "end": v(41.75, -139.04) * mm});
            skLineSegment(sketch, "E5262", {"start": v(41.75, -139.04) * mm, "end": v(41.86, -139.26) * mm});
            skLineSegment(sketch, "E5263", {"start": v(41.86, -139.26) * mm, "end": v(41.94, -139.5) * mm});
            skLineSegment(sketch, "E5264", {"start": v(41.94, -139.5) * mm, "end": v(41.98, -139.75) * mm});
            skLineSegment(sketch, "E5265", {"start": v(41.98, -139.75) * mm, "end": v(42, -140) * mm});
            skLineSegment(sketch, "E5266", {"start": v(42, -140) * mm, "end": v(41.98, -140.25) * mm});
            skLineSegment(sketch, "E5267", {"start": v(41.98, -140.25) * mm, "end": v(41.94, -140.5) * mm});
            skLineSegment(sketch, "E5268", {"start": v(41.94, -140.5) * mm, "end": v(41.86, -140.74) * mm});
            skLineSegment(sketch, "E5269", {"start": v(41.86, -140.74) * mm, "end": v(41.75, -140.96) * mm});
            skLineSegment(sketch, "E5270", {"start": v(41.75, -140.96) * mm, "end": v(41.62, -141.18) * mm});
            skLineSegment(sketch, "E5271", {"start": v(41.62, -141.18) * mm, "end": v(41.46, -141.37) * mm});
            skLineSegment(sketch, "E5272", {"start": v(41.46, -141.37) * mm, "end": v(41.27, -141.54) * mm});
            skLineSegment(sketch, "E5273", {"start": v(41.27, -141.54) * mm, "end": v(41.07, -141.69) * mm});
            skLineSegment(sketch, "E5274", {"start": v(41.07, -141.69) * mm, "end": v(40.85, -141.8) * mm});
            skLineSegment(sketch, "E5275", {"start": v(40.85, -141.8) * mm, "end": v(40.62, -141.9) * mm});
            skLineSegment(sketch, "E5276", {"start": v(40.62, -141.9) * mm, "end": v(40.37, -141.97) * mm});
            skLineSegment(sketch, "E5277", {"start": v(40.37, -141.97) * mm, "end": v(40.13, -142) * mm});
            skLineSegment(sketch, "E5278", {"start": v(40.13, -142) * mm, "end": v(39.87, -142) * mm});
            skLineSegment(sketch, "E5279", {"start": v(55.4, -206) * mm, "end": v(55.22, -205.97) * mm});
            skLineSegment(sketch, "E5280", {"start": v(55.22, -205.97) * mm, "end": v(55.04, -205.93) * mm});
            skLineSegment(sketch, "E5281", {"start": v(55.04, -205.93) * mm, "end": v(54.86, -205.86) * mm});
            skLineSegment(sketch, "E5282", {"start": v(54.86, -205.86) * mm, "end": v(54.7, -205.77) * mm});
            skLineSegment(sketch, "E5283", {"start": v(54.7, -205.77) * mm, "end": v(54.54, -205.66) * mm});
            skLineSegment(sketch, "E5284", {"start": v(54.54, -205.66) * mm, "end": v(54.4, -205.53) * mm});
            skLineSegment(sketch, "E5285", {"start": v(54.4, -205.53) * mm, "end": v(54.29, -205.38) * mm});
            skLineSegment(sketch, "E5286", {"start": v(54.29, -205.38) * mm, "end": v(54.19, -205.22) * mm});
            skLineSegment(sketch, "E5287", {"start": v(54.19, -205.22) * mm, "end": v(54.1, -205.05) * mm});
            skLineSegment(sketch, "E5288", {"start": v(54.1, -205.05) * mm, "end": v(54.05, -204.87) * mm});
            skLineSegment(sketch, "E5289", {"start": v(54.05, -204.87) * mm, "end": v(54.01, -204.69) * mm});
            skLineSegment(sketch, "E5290", {"start": v(54.01, -204.69) * mm, "end": v(54, -204.5) * mm});
            skLineSegment(sketch, "E5291", {"start": v(54, -204.5) * mm, "end": v(54.01, -204.31) * mm});
            skLineSegment(sketch, "E5292", {"start": v(54.01, -204.31) * mm, "end": v(54.05, -204.13) * mm});
            skLineSegment(sketch, "E5293", {"start": v(54.05, -204.13) * mm, "end": v(54.1, -203.95) * mm});
            skLineSegment(sketch, "E5294", {"start": v(54.1, -203.95) * mm, "end": v(54.19, -203.78) * mm});
            skLineSegment(sketch, "E5295", {"start": v(54.19, -203.78) * mm, "end": v(54.29, -203.62) * mm});
            skLineSegment(sketch, "E5296", {"start": v(54.29, -203.62) * mm, "end": v(54.4, -203.47) * mm});
            skLineSegment(sketch, "E5297", {"start": v(54.4, -203.47) * mm, "end": v(54.54, -203.34) * mm});
            skLineSegment(sketch, "E5298", {"start": v(54.54, -203.34) * mm, "end": v(54.7, -203.23) * mm});
            skLineSegment(sketch, "E5299", {"start": v(54.7, -203.23) * mm, "end": v(54.86, -203.14) * mm});
            skLineSegment(sketch, "E5300", {"start": v(54.86, -203.14) * mm, "end": v(55.04, -203.07) * mm});
            skLineSegment(sketch, "E5301", {"start": v(55.04, -203.07) * mm, "end": v(55.22, -203.03) * mm});
            skLineSegment(sketch, "E5302", {"start": v(55.22, -203.03) * mm, "end": v(55.4, -203) * mm});
            skLineSegment(sketch, "E5303", {"start": v(55.4, -203) * mm, "end": v(55.6, -203) * mm});
            skLineSegment(sketch, "E5304", {"start": v(55.6, -203) * mm, "end": v(55.78, -203.03) * mm});
            skLineSegment(sketch, "E5305", {"start": v(55.78, -203.03) * mm, "end": v(55.96, -203.07) * mm});
            skLineSegment(sketch, "E5306", {"start": v(55.96, -203.07) * mm, "end": v(56.14, -203.14) * mm});
            skLineSegment(sketch, "E5307", {"start": v(56.14, -203.14) * mm, "end": v(56.3, -203.23) * mm});
            skLineSegment(sketch, "E5308", {"start": v(56.3, -203.23) * mm, "end": v(56.46, -203.34) * mm});
            skLineSegment(sketch, "E5309", {"start": v(56.46, -203.34) * mm, "end": v(56.6, -203.47) * mm});
            skLineSegment(sketch, "E5310", {"start": v(56.6, -203.47) * mm, "end": v(56.71, -203.62) * mm});
            skLineSegment(sketch, "E5311", {"start": v(56.71, -203.62) * mm, "end": v(56.81, -203.78) * mm});
            skLineSegment(sketch, "E5312", {"start": v(56.81, -203.78) * mm, "end": v(56.9, -203.95) * mm});
            skLineSegment(sketch, "E5313", {"start": v(56.9, -203.95) * mm, "end": v(56.95, -204.13) * mm});
            skLineSegment(sketch, "E5314", {"start": v(56.95, -204.13) * mm, "end": v(56.99, -204.31) * mm});
            skLineSegment(sketch, "E5315", {"start": v(56.99, -204.31) * mm, "end": v(57, -204.5) * mm});
            skLineSegment(sketch, "E5316", {"start": v(57, -204.5) * mm, "end": v(56.99, -204.69) * mm});
            skLineSegment(sketch, "E5317", {"start": v(56.99, -204.69) * mm, "end": v(56.95, -204.87) * mm});
            skLineSegment(sketch, "E5318", {"start": v(56.95, -204.87) * mm, "end": v(56.9, -205.05) * mm});
            skLineSegment(sketch, "E5319", {"start": v(56.9, -205.05) * mm, "end": v(56.81, -205.22) * mm});
            skLineSegment(sketch, "E5320", {"start": v(56.81, -205.22) * mm, "end": v(56.71, -205.38) * mm});
            skLineSegment(sketch, "E5321", {"start": v(56.71, -205.38) * mm, "end": v(56.6, -205.53) * mm});
            skLineSegment(sketch, "E5322", {"start": v(56.6, -205.53) * mm, "end": v(56.46, -205.66) * mm});
            skLineSegment(sketch, "E5323", {"start": v(56.46, -205.66) * mm, "end": v(56.3, -205.77) * mm});
            skLineSegment(sketch, "E5324", {"start": v(56.3, -205.77) * mm, "end": v(56.14, -205.86) * mm});
            skLineSegment(sketch, "E5325", {"start": v(56.14, -205.86) * mm, "end": v(55.96, -205.93) * mm});
            skLineSegment(sketch, "E5326", {"start": v(55.96, -205.93) * mm, "end": v(55.78, -205.97) * mm});
            skLineSegment(sketch, "E5327", {"start": v(55.78, -205.97) * mm, "end": v(55.6, -206) * mm});
            skLineSegment(sketch, "E5328", {"start": v(55.6, -206) * mm, "end": v(55.4, -206) * mm});
            skLineSegment(sketch, "E5329", {"start": v(354.4, -206) * mm, "end": v(354.22, -205.97) * mm});
            skLineSegment(sketch, "E5330", {"start": v(354.22, -205.97) * mm, "end": v(354.04, -205.93) * mm});
            skLineSegment(sketch, "E5331", {"start": v(354.04, -205.93) * mm, "end": v(353.86, -205.86) * mm});
            skLineSegment(sketch, "E5332", {"start": v(353.86, -205.86) * mm, "end": v(353.7, -205.77) * mm});
            skLineSegment(sketch, "E5333", {"start": v(353.7, -205.77) * mm, "end": v(353.54, -205.66) * mm});
            skLineSegment(sketch, "E5334", {"start": v(353.54, -205.66) * mm, "end": v(353.4, -205.53) * mm});
            skLineSegment(sketch, "E5335", {"start": v(353.4, -205.53) * mm, "end": v(353.29, -205.38) * mm});
            skLineSegment(sketch, "E5336", {"start": v(353.29, -205.38) * mm, "end": v(353.19, -205.22) * mm});
            skLineSegment(sketch, "E5337", {"start": v(353.19, -205.22) * mm, "end": v(353.1, -205.05) * mm});
            skLineSegment(sketch, "E5338", {"start": v(353.1, -205.05) * mm, "end": v(353.05, -204.87) * mm});
            skLineSegment(sketch, "E5339", {"start": v(353.05, -204.87) * mm, "end": v(353.01, -204.69) * mm});
            skLineSegment(sketch, "E5340", {"start": v(353.01, -204.69) * mm, "end": v(353, -204.5) * mm});
            skLineSegment(sketch, "E5341", {"start": v(353, -204.5) * mm, "end": v(353.01, -204.31) * mm});
            skLineSegment(sketch, "E5342", {"start": v(353.01, -204.31) * mm, "end": v(353.05, -204.13) * mm});
            skLineSegment(sketch, "E5343", {"start": v(353.05, -204.13) * mm, "end": v(353.1, -203.95) * mm});
            skLineSegment(sketch, "E5344", {"start": v(353.1, -203.95) * mm, "end": v(353.19, -203.78) * mm});
            skLineSegment(sketch, "E5345", {"start": v(353.19, -203.78) * mm, "end": v(353.29, -203.62) * mm});
            skLineSegment(sketch, "E5346", {"start": v(353.29, -203.62) * mm, "end": v(353.4, -203.47) * mm});
            skLineSegment(sketch, "E5347", {"start": v(353.4, -203.47) * mm, "end": v(353.54, -203.34) * mm});
            skLineSegment(sketch, "E5348", {"start": v(353.54, -203.34) * mm, "end": v(353.7, -203.23) * mm});
            skLineSegment(sketch, "E5349", {"start": v(353.7, -203.23) * mm, "end": v(353.86, -203.14) * mm});
            skLineSegment(sketch, "E5350", {"start": v(353.86, -203.14) * mm, "end": v(354.04, -203.07) * mm});
            skLineSegment(sketch, "E5351", {"start": v(354.04, -203.07) * mm, "end": v(354.22, -203.03) * mm});
            skLineSegment(sketch, "E5352", {"start": v(354.22, -203.03) * mm, "end": v(354.4, -203) * mm});
            skLineSegment(sketch, "E5353", {"start": v(354.4, -203) * mm, "end": v(354.6, -203) * mm});
            skLineSegment(sketch, "E5354", {"start": v(354.6, -203) * mm, "end": v(354.78, -203.03) * mm});
            skLineSegment(sketch, "E5355", {"start": v(354.78, -203.03) * mm, "end": v(354.96, -203.07) * mm});
            skLineSegment(sketch, "E5356", {"start": v(354.96, -203.07) * mm, "end": v(355.14, -203.14) * mm});
            skLineSegment(sketch, "E5357", {"start": v(355.14, -203.14) * mm, "end": v(355.3, -203.23) * mm});
            skLineSegment(sketch, "E5358", {"start": v(355.3, -203.23) * mm, "end": v(355.46, -203.34) * mm});
            skLineSegment(sketch, "E5359", {"start": v(355.46, -203.34) * mm, "end": v(355.6, -203.47) * mm});
            skLineSegment(sketch, "E5360", {"start": v(355.6, -203.47) * mm, "end": v(355.71, -203.62) * mm});
            skLineSegment(sketch, "E5361", {"start": v(355.71, -203.62) * mm, "end": v(355.81, -203.78) * mm});
            skLineSegment(sketch, "E5362", {"start": v(355.81, -203.78) * mm, "end": v(355.9, -203.95) * mm});
            skLineSegment(sketch, "E5363", {"start": v(355.9, -203.95) * mm, "end": v(355.95, -204.13) * mm});
            skLineSegment(sketch, "E5364", {"start": v(355.95, -204.13) * mm, "end": v(355.99, -204.31) * mm});
            skLineSegment(sketch, "E5365", {"start": v(355.99, -204.31) * mm, "end": v(356, -204.5) * mm});
            skLineSegment(sketch, "E5366", {"start": v(356, -204.5) * mm, "end": v(355.99, -204.69) * mm});
            skLineSegment(sketch, "E5367", {"start": v(355.99, -204.69) * mm, "end": v(355.95, -204.87) * mm});
            skLineSegment(sketch, "E5368", {"start": v(355.95, -204.87) * mm, "end": v(355.9, -205.05) * mm});
            skLineSegment(sketch, "E5369", {"start": v(355.9, -205.05) * mm, "end": v(355.81, -205.22) * mm});
            skLineSegment(sketch, "E5370", {"start": v(355.81, -205.22) * mm, "end": v(355.71, -205.38) * mm});
            skLineSegment(sketch, "E5371", {"start": v(355.71, -205.38) * mm, "end": v(355.6, -205.53) * mm});
            skLineSegment(sketch, "E5372", {"start": v(355.6, -205.53) * mm, "end": v(355.46, -205.66) * mm});
            skLineSegment(sketch, "E5373", {"start": v(355.46, -205.66) * mm, "end": v(355.3, -205.77) * mm});
            skLineSegment(sketch, "E5374", {"start": v(355.3, -205.77) * mm, "end": v(355.14, -205.86) * mm});
            skLineSegment(sketch, "E5375", {"start": v(355.14, -205.86) * mm, "end": v(354.96, -205.93) * mm});
            skLineSegment(sketch, "E5376", {"start": v(354.96, -205.93) * mm, "end": v(354.78, -205.97) * mm});
            skLineSegment(sketch, "E5377", {"start": v(354.78, -205.97) * mm, "end": v(354.6, -206) * mm});
            skLineSegment(sketch, "E5378", {"start": v(354.6, -206) * mm, "end": v(354.4, -206) * mm});
            skLineSegment(sketch, "E5379", {"start": v(24.4, -206) * mm, "end": v(24.22, -205.97) * mm});
            skLineSegment(sketch, "E5380", {"start": v(24.22, -205.97) * mm, "end": v(24.04, -205.93) * mm});
            skLineSegment(sketch, "E5381", {"start": v(24.04, -205.93) * mm, "end": v(23.86, -205.86) * mm});
            skLineSegment(sketch, "E5382", {"start": v(23.86, -205.86) * mm, "end": v(23.7, -205.77) * mm});
            skLineSegment(sketch, "E5383", {"start": v(23.7, -205.77) * mm, "end": v(23.54, -205.66) * mm});
            skLineSegment(sketch, "E5384", {"start": v(23.54, -205.66) * mm, "end": v(23.4, -205.53) * mm});
            skLineSegment(sketch, "E5385", {"start": v(23.4, -205.53) * mm, "end": v(23.29, -205.38) * mm});
            skLineSegment(sketch, "E5386", {"start": v(23.29, -205.38) * mm, "end": v(23.19, -205.22) * mm});
            skLineSegment(sketch, "E5387", {"start": v(23.19, -205.22) * mm, "end": v(23.1, -205.05) * mm});
            skLineSegment(sketch, "E5388", {"start": v(23.1, -205.05) * mm, "end": v(23.05, -204.87) * mm});
            skLineSegment(sketch, "E5389", {"start": v(23.05, -204.87) * mm, "end": v(23.01, -204.69) * mm});
            skLineSegment(sketch, "E5390", {"start": v(23.01, -204.69) * mm, "end": v(23, -204.5) * mm});
            skLineSegment(sketch, "E5391", {"start": v(23, -204.5) * mm, "end": v(23.01, -204.31) * mm});
            skLineSegment(sketch, "E5392", {"start": v(23.01, -204.31) * mm, "end": v(23.05, -204.13) * mm});
            skLineSegment(sketch, "E5393", {"start": v(23.05, -204.13) * mm, "end": v(23.1, -203.95) * mm});
            skLineSegment(sketch, "E5394", {"start": v(23.1, -203.95) * mm, "end": v(23.19, -203.78) * mm});
            skLineSegment(sketch, "E5395", {"start": v(23.19, -203.78) * mm, "end": v(23.29, -203.62) * mm});
            skLineSegment(sketch, "E5396", {"start": v(23.29, -203.62) * mm, "end": v(23.4, -203.47) * mm});
            skLineSegment(sketch, "E5397", {"start": v(23.4, -203.47) * mm, "end": v(23.54, -203.34) * mm});
            skLineSegment(sketch, "E5398", {"start": v(23.54, -203.34) * mm, "end": v(23.7, -203.23) * mm});
            skLineSegment(sketch, "E5399", {"start": v(23.7, -203.23) * mm, "end": v(23.86, -203.14) * mm});
            skLineSegment(sketch, "E5400", {"start": v(23.86, -203.14) * mm, "end": v(24.04, -203.07) * mm});
            skLineSegment(sketch, "E5401", {"start": v(24.04, -203.07) * mm, "end": v(24.22, -203.03) * mm});
            skLineSegment(sketch, "E5402", {"start": v(24.22, -203.03) * mm, "end": v(24.4, -203) * mm});
            skLineSegment(sketch, "E5403", {"start": v(24.4, -203) * mm, "end": v(24.6, -203) * mm});
            skLineSegment(sketch, "E5404", {"start": v(24.6, -203) * mm, "end": v(24.78, -203.03) * mm});
            skLineSegment(sketch, "E5405", {"start": v(24.78, -203.03) * mm, "end": v(24.96, -203.07) * mm});
            skLineSegment(sketch, "E5406", {"start": v(24.96, -203.07) * mm, "end": v(25.14, -203.14) * mm});
            skLineSegment(sketch, "E5407", {"start": v(25.14, -203.14) * mm, "end": v(25.3, -203.23) * mm});
            skLineSegment(sketch, "E5408", {"start": v(25.3, -203.23) * mm, "end": v(25.46, -203.34) * mm});
            skLineSegment(sketch, "E5409", {"start": v(25.46, -203.34) * mm, "end": v(25.6, -203.47) * mm});
            skLineSegment(sketch, "E5410", {"start": v(25.6, -203.47) * mm, "end": v(25.71, -203.62) * mm});
            skLineSegment(sketch, "E5411", {"start": v(25.71, -203.62) * mm, "end": v(25.81, -203.78) * mm});
            skLineSegment(sketch, "E5412", {"start": v(25.81, -203.78) * mm, "end": v(25.9, -203.95) * mm});
            skLineSegment(sketch, "E5413", {"start": v(25.9, -203.95) * mm, "end": v(25.95, -204.13) * mm});
            skLineSegment(sketch, "E5414", {"start": v(25.95, -204.13) * mm, "end": v(25.99, -204.31) * mm});
            skLineSegment(sketch, "E5415", {"start": v(25.99, -204.31) * mm, "end": v(26, -204.5) * mm});
            skLineSegment(sketch, "E5416", {"start": v(26, -204.5) * mm, "end": v(25.99, -204.69) * mm});
            skLineSegment(sketch, "E5417", {"start": v(25.99, -204.69) * mm, "end": v(25.95, -204.87) * mm});
            skLineSegment(sketch, "E5418", {"start": v(25.95, -204.87) * mm, "end": v(25.9, -205.05) * mm});
            skLineSegment(sketch, "E5419", {"start": v(25.9, -205.05) * mm, "end": v(25.81, -205.22) * mm});
            skLineSegment(sketch, "E5420", {"start": v(25.81, -205.22) * mm, "end": v(25.71, -205.38) * mm});
            skLineSegment(sketch, "E5421", {"start": v(25.71, -205.38) * mm, "end": v(25.6, -205.53) * mm});
            skLineSegment(sketch, "E5422", {"start": v(25.6, -205.53) * mm, "end": v(25.46, -205.66) * mm});
            skLineSegment(sketch, "E5423", {"start": v(25.46, -205.66) * mm, "end": v(25.3, -205.77) * mm});
            skLineSegment(sketch, "E5424", {"start": v(25.3, -205.77) * mm, "end": v(25.14, -205.86) * mm});
            skLineSegment(sketch, "E5425", {"start": v(25.14, -205.86) * mm, "end": v(24.96, -205.93) * mm});
            skLineSegment(sketch, "E5426", {"start": v(24.96, -205.93) * mm, "end": v(24.78, -205.97) * mm});
            skLineSegment(sketch, "E5427", {"start": v(24.78, -205.97) * mm, "end": v(24.6, -206) * mm});
            skLineSegment(sketch, "E5428", {"start": v(24.6, -206) * mm, "end": v(24.4, -206) * mm});
            skLineSegment(sketch, "E5429", {"start": v(385.4, -206) * mm, "end": v(385.22, -205.97) * mm});
            skLineSegment(sketch, "E5430", {"start": v(385.22, -205.97) * mm, "end": v(385.04, -205.93) * mm});
            skLineSegment(sketch, "E5431", {"start": v(385.04, -205.93) * mm, "end": v(384.86, -205.86) * mm});
            skLineSegment(sketch, "E5432", {"start": v(384.86, -205.86) * mm, "end": v(384.7, -205.77) * mm});
            skLineSegment(sketch, "E5433", {"start": v(384.7, -205.77) * mm, "end": v(384.54, -205.66) * mm});
            skLineSegment(sketch, "E5434", {"start": v(384.54, -205.66) * mm, "end": v(384.4, -205.53) * mm});
            skLineSegment(sketch, "E5435", {"start": v(384.4, -205.53) * mm, "end": v(384.29, -205.38) * mm});
            skLineSegment(sketch, "E5436", {"start": v(384.29, -205.38) * mm, "end": v(384.19, -205.22) * mm});
            skLineSegment(sketch, "E5437", {"start": v(384.19, -205.22) * mm, "end": v(384.1, -205.05) * mm});
            skLineSegment(sketch, "E5438", {"start": v(384.1, -205.05) * mm, "end": v(384.05, -204.87) * mm});
            skLineSegment(sketch, "E5439", {"start": v(384.05, -204.87) * mm, "end": v(384.01, -204.69) * mm});
            skLineSegment(sketch, "E5440", {"start": v(384.01, -204.69) * mm, "end": v(384, -204.5) * mm});
            skLineSegment(sketch, "E5441", {"start": v(384, -204.5) * mm, "end": v(384.01, -204.31) * mm});
            skLineSegment(sketch, "E5442", {"start": v(384.01, -204.31) * mm, "end": v(384.05, -204.13) * mm});
            skLineSegment(sketch, "E5443", {"start": v(384.05, -204.13) * mm, "end": v(384.1, -203.95) * mm});
            skLineSegment(sketch, "E5444", {"start": v(384.1, -203.95) * mm, "end": v(384.19, -203.78) * mm});
            skLineSegment(sketch, "E5445", {"start": v(384.19, -203.78) * mm, "end": v(384.29, -203.62) * mm});
            skLineSegment(sketch, "E5446", {"start": v(384.29, -203.62) * mm, "end": v(384.4, -203.47) * mm});
            skLineSegment(sketch, "E5447", {"start": v(384.4, -203.47) * mm, "end": v(384.54, -203.34) * mm});
            skLineSegment(sketch, "E5448", {"start": v(384.54, -203.34) * mm, "end": v(384.7, -203.23) * mm});
            skLineSegment(sketch, "E5449", {"start": v(384.7, -203.23) * mm, "end": v(384.86, -203.14) * mm});
            skLineSegment(sketch, "E5450", {"start": v(384.86, -203.14) * mm, "end": v(385.04, -203.07) * mm});
            skLineSegment(sketch, "E5451", {"start": v(385.04, -203.07) * mm, "end": v(385.22, -203.03) * mm});
            skLineSegment(sketch, "E5452", {"start": v(385.22, -203.03) * mm, "end": v(385.4, -203) * mm});
            skLineSegment(sketch, "E5453", {"start": v(385.4, -203) * mm, "end": v(385.6, -203) * mm});
            skLineSegment(sketch, "E5454", {"start": v(385.6, -203) * mm, "end": v(385.78, -203.03) * mm});
            skLineSegment(sketch, "E5455", {"start": v(385.78, -203.03) * mm, "end": v(385.96, -203.07) * mm});
            skLineSegment(sketch, "E5456", {"start": v(385.96, -203.07) * mm, "end": v(386.14, -203.14) * mm});
            skLineSegment(sketch, "E5457", {"start": v(386.14, -203.14) * mm, "end": v(386.3, -203.23) * mm});
            skLineSegment(sketch, "E5458", {"start": v(386.3, -203.23) * mm, "end": v(386.46, -203.34) * mm});
            skLineSegment(sketch, "E5459", {"start": v(386.46, -203.34) * mm, "end": v(386.6, -203.47) * mm});
            skLineSegment(sketch, "E5460", {"start": v(386.6, -203.47) * mm, "end": v(386.71, -203.62) * mm});
            skLineSegment(sketch, "E5461", {"start": v(386.71, -203.62) * mm, "end": v(386.81, -203.78) * mm});
            skLineSegment(sketch, "E5462", {"start": v(386.81, -203.78) * mm, "end": v(386.9, -203.95) * mm});
            skLineSegment(sketch, "E5463", {"start": v(386.9, -203.95) * mm, "end": v(386.95, -204.13) * mm});
            skLineSegment(sketch, "E5464", {"start": v(386.95, -204.13) * mm, "end": v(386.99, -204.31) * mm});
            skLineSegment(sketch, "E5465", {"start": v(386.99, -204.31) * mm, "end": v(387, -204.5) * mm});
            skLineSegment(sketch, "E5466", {"start": v(387, -204.5) * mm, "end": v(386.99, -204.69) * mm});
            skLineSegment(sketch, "E5467", {"start": v(386.99, -204.69) * mm, "end": v(386.95, -204.87) * mm});
            skLineSegment(sketch, "E5468", {"start": v(386.95, -204.87) * mm, "end": v(386.9, -205.05) * mm});
            skLineSegment(sketch, "E5469", {"start": v(386.9, -205.05) * mm, "end": v(386.81, -205.22) * mm});
            skLineSegment(sketch, "E5470", {"start": v(386.81, -205.22) * mm, "end": v(386.71, -205.38) * mm});
            skLineSegment(sketch, "E5471", {"start": v(386.71, -205.38) * mm, "end": v(386.6, -205.53) * mm});
            skLineSegment(sketch, "E5472", {"start": v(386.6, -205.53) * mm, "end": v(386.46, -205.66) * mm});
            skLineSegment(sketch, "E5473", {"start": v(386.46, -205.66) * mm, "end": v(386.3, -205.77) * mm});
            skLineSegment(sketch, "E5474", {"start": v(386.3, -205.77) * mm, "end": v(386.14, -205.86) * mm});
            skLineSegment(sketch, "E5475", {"start": v(386.14, -205.86) * mm, "end": v(385.96, -205.93) * mm});
            skLineSegment(sketch, "E5476", {"start": v(385.96, -205.93) * mm, "end": v(385.78, -205.97) * mm});
            skLineSegment(sketch, "E5477", {"start": v(385.78, -205.97) * mm, "end": v(385.6, -206) * mm});
            skLineSegment(sketch, "E5478", {"start": v(385.6, -206) * mm, "end": v(385.4, -206) * mm});
            skLineSegment(sketch, "E5479", {"start": v(369.25, -231.98) * mm, "end": v(367.75, -231.79) * mm});
            skLineSegment(sketch, "E5480", {"start": v(367.75, -231.79) * mm, "end": v(366.3, -231.41) * mm});
            skLineSegment(sketch, "E5481", {"start": v(366.3, -231.41) * mm, "end": v(364.9, -230.86) * mm});
            skLineSegment(sketch, "E5482", {"start": v(364.9, -230.86) * mm, "end": v(363.57, -230.13) * mm});
            skLineSegment(sketch, "E5483", {"start": v(363.57, -230.13) * mm, "end": v(362.35, -229.25) * mm});
            skLineSegment(sketch, "E5484", {"start": v(362.35, -229.25) * mm, "end": v(361.25, -228.22) * mm});
            skLineSegment(sketch, "E5485", {"start": v(361.25, -228.22) * mm, "end": v(360.3, -227.05) * mm});
            skLineSegment(sketch, "E5486", {"start": v(360.3, -227.05) * mm, "end": v(359.48, -225.78) * mm});
            skLineSegment(sketch, "E5487", {"start": v(359.48, -225.78) * mm, "end": v(358.84, -224.42) * mm});
            skLineSegment(sketch, "E5488", {"start": v(358.84, -224.42) * mm, "end": v(358.38, -222.98) * mm});
            skLineSegment(sketch, "E5489", {"start": v(358.38, -222.98) * mm, "end": v(358.1, -221.5) * mm});
            skLineSegment(sketch, "E5490", {"start": v(358.1, -221.5) * mm, "end": v(358, -220) * mm});
            skLineSegment(sketch, "E5491", {"start": v(358, -220) * mm, "end": v(358.1, -218.5) * mm});
            skLineSegment(sketch, "E5492", {"start": v(358.1, -218.5) * mm, "end": v(358.38, -217.02) * mm});
            skLineSegment(sketch, "E5493", {"start": v(358.38, -217.02) * mm, "end": v(358.84, -215.58) * mm});
            skLineSegment(sketch, "E5494", {"start": v(358.84, -215.58) * mm, "end": v(359.48, -214.22) * mm});
            skLineSegment(sketch, "E5495", {"start": v(359.48, -214.22) * mm, "end": v(360.3, -212.95) * mm});
            skLineSegment(sketch, "E5496", {"start": v(360.3, -212.95) * mm, "end": v(361.25, -211.78) * mm});
            skLineSegment(sketch, "E5497", {"start": v(361.25, -211.78) * mm, "end": v(362.35, -210.75) * mm});
            skLineSegment(sketch, "E5498", {"start": v(362.35, -210.75) * mm, "end": v(363.57, -209.87) * mm});
            skLineSegment(sketch, "E5499", {"start": v(363.57, -209.87) * mm, "end": v(364.9, -209.14) * mm});
            skLineSegment(sketch, "E5500", {"start": v(364.9, -209.14) * mm, "end": v(366.3, -208.59) * mm});
            skLineSegment(sketch, "E5501", {"start": v(366.3, -208.59) * mm, "end": v(367.75, -208.21) * mm});
            skLineSegment(sketch, "E5502", {"start": v(367.75, -208.21) * mm, "end": v(369.25, -208.02) * mm});
            skLineSegment(sketch, "E5503", {"start": v(369.25, -208.02) * mm, "end": v(370.75, -208.02) * mm});
            skLineSegment(sketch, "E5504", {"start": v(370.75, -208.02) * mm, "end": v(372.25, -208.21) * mm});
            skLineSegment(sketch, "E5505", {"start": v(372.25, -208.21) * mm, "end": v(373.7, -208.59) * mm});
            skLineSegment(sketch, "E5506", {"start": v(373.7, -208.59) * mm, "end": v(375.1, -209.14) * mm});
            skLineSegment(sketch, "E5507", {"start": v(375.1, -209.14) * mm, "end": v(376.43, -209.87) * mm});
            skLineSegment(sketch, "E5508", {"start": v(376.43, -209.87) * mm, "end": v(377.65, -210.75) * mm});
            skLineSegment(sketch, "E5509", {"start": v(377.65, -210.75) * mm, "end": v(378.75, -211.78) * mm});
            skLineSegment(sketch, "E5510", {"start": v(378.75, -211.78) * mm, "end": v(379.7, -212.95) * mm});
            skLineSegment(sketch, "E5511", {"start": v(379.7, -212.95) * mm, "end": v(380.52, -214.22) * mm});
            skLineSegment(sketch, "E5512", {"start": v(380.52, -214.22) * mm, "end": v(381.16, -215.58) * mm});
            skLineSegment(sketch, "E5513", {"start": v(381.16, -215.58) * mm, "end": v(381.62, -217.02) * mm});
            skLineSegment(sketch, "E5514", {"start": v(381.62, -217.02) * mm, "end": v(381.9, -218.5) * mm});
            skLineSegment(sketch, "E5515", {"start": v(381.9, -218.5) * mm, "end": v(382, -220) * mm});
            skLineSegment(sketch, "E5516", {"start": v(382, -220) * mm, "end": v(381.9, -221.5) * mm});
            skLineSegment(sketch, "E5517", {"start": v(381.9, -221.5) * mm, "end": v(381.62, -222.98) * mm});
            skLineSegment(sketch, "E5518", {"start": v(381.62, -222.98) * mm, "end": v(381.16, -224.42) * mm});
            skLineSegment(sketch, "E5519", {"start": v(381.16, -224.42) * mm, "end": v(380.52, -225.78) * mm});
            skLineSegment(sketch, "E5520", {"start": v(380.52, -225.78) * mm, "end": v(379.7, -227.05) * mm});
            skLineSegment(sketch, "E5521", {"start": v(379.7, -227.05) * mm, "end": v(378.75, -228.22) * mm});
            skLineSegment(sketch, "E5522", {"start": v(378.75, -228.22) * mm, "end": v(377.65, -229.25) * mm});
            skLineSegment(sketch, "E5523", {"start": v(377.65, -229.25) * mm, "end": v(376.43, -230.13) * mm});
            skLineSegment(sketch, "E5524", {"start": v(376.43, -230.13) * mm, "end": v(375.1, -230.86) * mm});
            skLineSegment(sketch, "E5525", {"start": v(375.1, -230.86) * mm, "end": v(373.7, -231.41) * mm});
            skLineSegment(sketch, "E5526", {"start": v(373.7, -231.41) * mm, "end": v(372.25, -231.79) * mm});
            skLineSegment(sketch, "E5527", {"start": v(372.25, -231.79) * mm, "end": v(370.75, -231.98) * mm});
            skLineSegment(sketch, "E5528", {"start": v(370.75, -231.98) * mm, "end": v(369.25, -231.98) * mm});
            skLineSegment(sketch, "E5529", {"start": v(39.25, -231.98) * mm, "end": v(37.75, -231.79) * mm});
            skLineSegment(sketch, "E5530", {"start": v(37.75, -231.79) * mm, "end": v(36.3, -231.41) * mm});
            skLineSegment(sketch, "E5531", {"start": v(36.3, -231.41) * mm, "end": v(34.9, -230.86) * mm});
            skLineSegment(sketch, "E5532", {"start": v(34.9, -230.86) * mm, "end": v(33.57, -230.13) * mm});
            skLineSegment(sketch, "E5533", {"start": v(33.57, -230.13) * mm, "end": v(32.35, -229.25) * mm});
            skLineSegment(sketch, "E5534", {"start": v(32.35, -229.25) * mm, "end": v(31.25, -228.22) * mm});
            skLineSegment(sketch, "E5535", {"start": v(31.25, -228.22) * mm, "end": v(30.3, -227.05) * mm});
            skLineSegment(sketch, "E5536", {"start": v(30.3, -227.05) * mm, "end": v(29.48, -225.78) * mm});
            skLineSegment(sketch, "E5537", {"start": v(29.48, -225.78) * mm, "end": v(28.84, -224.42) * mm});
            skLineSegment(sketch, "E5538", {"start": v(28.84, -224.42) * mm, "end": v(28.38, -222.98) * mm});
            skLineSegment(sketch, "E5539", {"start": v(28.38, -222.98) * mm, "end": v(28.1, -221.5) * mm});
            skLineSegment(sketch, "E5540", {"start": v(28.1, -221.5) * mm, "end": v(28, -220) * mm});
            skLineSegment(sketch, "E5541", {"start": v(28, -220) * mm, "end": v(28.1, -218.5) * mm});
            skLineSegment(sketch, "E5542", {"start": v(28.1, -218.5) * mm, "end": v(28.38, -217.02) * mm});
            skLineSegment(sketch, "E5543", {"start": v(28.38, -217.02) * mm, "end": v(28.84, -215.58) * mm});
            skLineSegment(sketch, "E5544", {"start": v(28.84, -215.58) * mm, "end": v(29.48, -214.22) * mm});
            skLineSegment(sketch, "E5545", {"start": v(29.48, -214.22) * mm, "end": v(30.3, -212.95) * mm});
            skLineSegment(sketch, "E5546", {"start": v(30.3, -212.95) * mm, "end": v(31.25, -211.78) * mm});
            skLineSegment(sketch, "E5547", {"start": v(31.25, -211.78) * mm, "end": v(32.35, -210.75) * mm});
            skLineSegment(sketch, "E5548", {"start": v(32.35, -210.75) * mm, "end": v(33.57, -209.87) * mm});
            skLineSegment(sketch, "E5549", {"start": v(33.57, -209.87) * mm, "end": v(34.9, -209.14) * mm});
            skLineSegment(sketch, "E5550", {"start": v(34.9, -209.14) * mm, "end": v(36.3, -208.59) * mm});
            skLineSegment(sketch, "E5551", {"start": v(36.3, -208.59) * mm, "end": v(37.75, -208.21) * mm});
            skLineSegment(sketch, "E5552", {"start": v(37.75, -208.21) * mm, "end": v(39.25, -208.02) * mm});
            skLineSegment(sketch, "E5553", {"start": v(39.25, -208.02) * mm, "end": v(40.75, -208.02) * mm});
            skLineSegment(sketch, "E5554", {"start": v(40.75, -208.02) * mm, "end": v(42.25, -208.21) * mm});
            skLineSegment(sketch, "E5555", {"start": v(42.25, -208.21) * mm, "end": v(43.7, -208.59) * mm});
            skLineSegment(sketch, "E5556", {"start": v(43.7, -208.59) * mm, "end": v(45.1, -209.14) * mm});
            skLineSegment(sketch, "E5557", {"start": v(45.1, -209.14) * mm, "end": v(46.43, -209.87) * mm});
            skLineSegment(sketch, "E5558", {"start": v(46.43, -209.87) * mm, "end": v(47.65, -210.75) * mm});
            skLineSegment(sketch, "E5559", {"start": v(47.65, -210.75) * mm, "end": v(48.75, -211.78) * mm});
            skLineSegment(sketch, "E5560", {"start": v(48.75, -211.78) * mm, "end": v(49.7, -212.95) * mm});
            skLineSegment(sketch, "E5561", {"start": v(49.7, -212.95) * mm, "end": v(50.52, -214.22) * mm});
            skLineSegment(sketch, "E5562", {"start": v(50.52, -214.22) * mm, "end": v(51.16, -215.58) * mm});
            skLineSegment(sketch, "E5563", {"start": v(51.16, -215.58) * mm, "end": v(51.62, -217.02) * mm});
            skLineSegment(sketch, "E5564", {"start": v(51.62, -217.02) * mm, "end": v(51.9, -218.5) * mm});
            skLineSegment(sketch, "E5565", {"start": v(51.9, -218.5) * mm, "end": v(52, -220) * mm});
            skLineSegment(sketch, "E5566", {"start": v(52, -220) * mm, "end": v(51.9, -221.5) * mm});
            skLineSegment(sketch, "E5567", {"start": v(51.9, -221.5) * mm, "end": v(51.62, -222.98) * mm});
            skLineSegment(sketch, "E5568", {"start": v(51.62, -222.98) * mm, "end": v(51.16, -224.42) * mm});
            skLineSegment(sketch, "E5569", {"start": v(51.16, -224.42) * mm, "end": v(50.52, -225.78) * mm});
            skLineSegment(sketch, "E5570", {"start": v(50.52, -225.78) * mm, "end": v(49.7, -227.05) * mm});
            skLineSegment(sketch, "E5571", {"start": v(49.7, -227.05) * mm, "end": v(48.75, -228.22) * mm});
            skLineSegment(sketch, "E5572", {"start": v(48.75, -228.22) * mm, "end": v(47.65, -229.25) * mm});
            skLineSegment(sketch, "E5573", {"start": v(47.65, -229.25) * mm, "end": v(46.43, -230.13) * mm});
            skLineSegment(sketch, "E5574", {"start": v(46.43, -230.13) * mm, "end": v(45.1, -230.86) * mm});
            skLineSegment(sketch, "E5575", {"start": v(45.1, -230.86) * mm, "end": v(43.7, -231.41) * mm});
            skLineSegment(sketch, "E5576", {"start": v(43.7, -231.41) * mm, "end": v(42.25, -231.79) * mm});
            skLineSegment(sketch, "E5577", {"start": v(42.25, -231.79) * mm, "end": v(40.75, -231.98) * mm});
            skLineSegment(sketch, "E5578", {"start": v(40.75, -231.98) * mm, "end": v(39.25, -231.98) * mm});
            skLineSegment(sketch, "E5579", {"start": v(22.75, -224) * mm, "end": v(22.25, -223.93) * mm});
            skLineSegment(sketch, "E5580", {"start": v(22.25, -223.93) * mm, "end": v(21.76, -223.8) * mm});
            skLineSegment(sketch, "E5581", {"start": v(21.76, -223.8) * mm, "end": v(21.3, -223.62) * mm});
            skLineSegment(sketch, "E5582", {"start": v(21.3, -223.62) * mm, "end": v(20.86, -223.38) * mm});
            skLineSegment(sketch, "E5583", {"start": v(20.86, -223.38) * mm, "end": v(20.45, -223.08) * mm});
            skLineSegment(sketch, "E5584", {"start": v(20.45, -223.08) * mm, "end": v(20.08, -222.74) * mm});
            skLineSegment(sketch, "E5585", {"start": v(20.08, -222.74) * mm, "end": v(19.76, -222.35) * mm});
            skLineSegment(sketch, "E5586", {"start": v(19.76, -222.35) * mm, "end": v(19.5, -221.93) * mm});
            skLineSegment(sketch, "E5587", {"start": v(19.5, -221.93) * mm, "end": v(19.28, -221.47) * mm});
            skLineSegment(sketch, "E5588", {"start": v(19.28, -221.47) * mm, "end": v(19.13, -221) * mm});
            skLineSegment(sketch, "E5589", {"start": v(19.13, -221) * mm, "end": v(19.03, -220.5) * mm});
            skLineSegment(sketch, "E5590", {"start": v(19.03, -220.5) * mm, "end": v(19, -220) * mm});
            skLineSegment(sketch, "E5591", {"start": v(19, -220) * mm, "end": v(19.03, -219.5) * mm});
            skLineSegment(sketch, "E5592", {"start": v(19.03, -219.5) * mm, "end": v(19.13, -219) * mm});
            skLineSegment(sketch, "E5593", {"start": v(19.13, -219) * mm, "end": v(19.28, -218.53) * mm});
            skLineSegment(sketch, "E5594", {"start": v(19.28, -218.53) * mm, "end": v(19.5, -218.07) * mm});
            skLineSegment(sketch, "E5595", {"start": v(19.5, -218.07) * mm, "end": v(19.76, -217.65) * mm});
            skLineSegment(sketch, "E5596", {"start": v(19.76, -217.65) * mm, "end": v(20.08, -217.26) * mm});
            skLineSegment(sketch, "E5597", {"start": v(20.08, -217.26) * mm, "end": v(20.45, -216.92) * mm});
            skLineSegment(sketch, "E5598", {"start": v(20.45, -216.92) * mm, "end": v(20.86, -216.62) * mm});
            skLineSegment(sketch, "E5599", {"start": v(20.86, -216.62) * mm, "end": v(21.3, -216.38) * mm});
            skLineSegment(sketch, "E5600", {"start": v(21.3, -216.38) * mm, "end": v(21.76, -216.2) * mm});
            skLineSegment(sketch, "E5601", {"start": v(21.76, -216.2) * mm, "end": v(22.25, -216.07) * mm});
            skLineSegment(sketch, "E5602", {"start": v(22.25, -216.07) * mm, "end": v(22.75, -216) * mm});
            skLineSegment(sketch, "E5603", {"start": v(22.75, -216) * mm, "end": v(23.25, -216) * mm});
            skLineSegment(sketch, "E5604", {"start": v(23.25, -216) * mm, "end": v(23.75, -216.07) * mm});
            skLineSegment(sketch, "E5605", {"start": v(23.75, -216.07) * mm, "end": v(24.24, -216.2) * mm});
            skLineSegment(sketch, "E5606", {"start": v(24.24, -216.2) * mm, "end": v(24.7, -216.38) * mm});
            skLineSegment(sketch, "E5607", {"start": v(24.7, -216.38) * mm, "end": v(25.14, -216.62) * mm});
            skLineSegment(sketch, "E5608", {"start": v(25.14, -216.62) * mm, "end": v(25.55, -216.92) * mm});
            skLineSegment(sketch, "E5609", {"start": v(25.55, -216.92) * mm, "end": v(25.92, -217.26) * mm});
            skLineSegment(sketch, "E5610", {"start": v(25.92, -217.26) * mm, "end": v(26.24, -217.65) * mm});
            skLineSegment(sketch, "E5611", {"start": v(26.24, -217.65) * mm, "end": v(26.5, -218.07) * mm});
            skLineSegment(sketch, "E5612", {"start": v(26.5, -218.07) * mm, "end": v(26.72, -218.53) * mm});
            skLineSegment(sketch, "E5613", {"start": v(26.72, -218.53) * mm, "end": v(26.87, -219) * mm});
            skLineSegment(sketch, "E5614", {"start": v(26.87, -219) * mm, "end": v(26.97, -219.5) * mm});
            skLineSegment(sketch, "E5615", {"start": v(26.97, -219.5) * mm, "end": v(27, -220) * mm});
            skLineSegment(sketch, "E5616", {"start": v(27, -220) * mm, "end": v(26.97, -220.5) * mm});
            skLineSegment(sketch, "E5617", {"start": v(26.97, -220.5) * mm, "end": v(26.87, -221) * mm});
            skLineSegment(sketch, "E5618", {"start": v(26.87, -221) * mm, "end": v(26.72, -221.47) * mm});
            skLineSegment(sketch, "E5619", {"start": v(26.72, -221.47) * mm, "end": v(26.5, -221.93) * mm});
            skLineSegment(sketch, "E5620", {"start": v(26.5, -221.93) * mm, "end": v(26.24, -222.35) * mm});
            skLineSegment(sketch, "E5621", {"start": v(26.24, -222.35) * mm, "end": v(25.92, -222.74) * mm});
            skLineSegment(sketch, "E5622", {"start": v(25.92, -222.74) * mm, "end": v(25.55, -223.08) * mm});
            skLineSegment(sketch, "E5623", {"start": v(25.55, -223.08) * mm, "end": v(25.14, -223.38) * mm});
            skLineSegment(sketch, "E5624", {"start": v(25.14, -223.38) * mm, "end": v(24.7, -223.62) * mm});
            skLineSegment(sketch, "E5625", {"start": v(24.7, -223.62) * mm, "end": v(24.24, -223.8) * mm});
            skLineSegment(sketch, "E5626", {"start": v(24.24, -223.8) * mm, "end": v(23.75, -223.93) * mm});
            skLineSegment(sketch, "E5627", {"start": v(23.75, -223.93) * mm, "end": v(23.25, -224) * mm});
            skLineSegment(sketch, "E5628", {"start": v(23.25, -224) * mm, "end": v(22.75, -224) * mm});
            skLineSegment(sketch, "E5629", {"start": v(386.75, -224) * mm, "end": v(386.25, -223.93) * mm});
            skLineSegment(sketch, "E5630", {"start": v(386.25, -223.93) * mm, "end": v(385.76, -223.8) * mm});
            skLineSegment(sketch, "E5631", {"start": v(385.76, -223.8) * mm, "end": v(385.3, -223.62) * mm});
            skLineSegment(sketch, "E5632", {"start": v(385.3, -223.62) * mm, "end": v(384.86, -223.38) * mm});
            skLineSegment(sketch, "E5633", {"start": v(384.86, -223.38) * mm, "end": v(384.45, -223.08) * mm});
            skLineSegment(sketch, "E5634", {"start": v(384.45, -223.08) * mm, "end": v(384.08, -222.74) * mm});
            skLineSegment(sketch, "E5635", {"start": v(384.08, -222.74) * mm, "end": v(383.76, -222.35) * mm});
            skLineSegment(sketch, "E5636", {"start": v(383.76, -222.35) * mm, "end": v(383.5, -221.93) * mm});
            skLineSegment(sketch, "E5637", {"start": v(383.5, -221.93) * mm, "end": v(383.28, -221.47) * mm});
            skLineSegment(sketch, "E5638", {"start": v(383.28, -221.47) * mm, "end": v(383.13, -221) * mm});
            skLineSegment(sketch, "E5639", {"start": v(383.13, -221) * mm, "end": v(383.03, -220.5) * mm});
            skLineSegment(sketch, "E5640", {"start": v(383.03, -220.5) * mm, "end": v(383, -220) * mm});
            skLineSegment(sketch, "E5641", {"start": v(383, -220) * mm, "end": v(383.03, -219.5) * mm});
            skLineSegment(sketch, "E5642", {"start": v(383.03, -219.5) * mm, "end": v(383.13, -219) * mm});
            skLineSegment(sketch, "E5643", {"start": v(383.13, -219) * mm, "end": v(383.28, -218.53) * mm});
            skLineSegment(sketch, "E5644", {"start": v(383.28, -218.53) * mm, "end": v(383.5, -218.07) * mm});
            skLineSegment(sketch, "E5645", {"start": v(383.5, -218.07) * mm, "end": v(383.76, -217.65) * mm});
            skLineSegment(sketch, "E5646", {"start": v(383.76, -217.65) * mm, "end": v(384.08, -217.26) * mm});
            skLineSegment(sketch, "E5647", {"start": v(384.08, -217.26) * mm, "end": v(384.45, -216.92) * mm});
            skLineSegment(sketch, "E5648", {"start": v(384.45, -216.92) * mm, "end": v(384.86, -216.62) * mm});
            skLineSegment(sketch, "E5649", {"start": v(384.86, -216.62) * mm, "end": v(385.3, -216.38) * mm});
            skLineSegment(sketch, "E5650", {"start": v(385.3, -216.38) * mm, "end": v(385.76, -216.2) * mm});
            skLineSegment(sketch, "E5651", {"start": v(385.76, -216.2) * mm, "end": v(386.25, -216.07) * mm});
            skLineSegment(sketch, "E5652", {"start": v(386.25, -216.07) * mm, "end": v(386.75, -216) * mm});
            skLineSegment(sketch, "E5653", {"start": v(386.75, -216) * mm, "end": v(387.25, -216) * mm});
            skLineSegment(sketch, "E5654", {"start": v(387.25, -216) * mm, "end": v(387.75, -216.07) * mm});
            skLineSegment(sketch, "E5655", {"start": v(387.75, -216.07) * mm, "end": v(388.24, -216.2) * mm});
            skLineSegment(sketch, "E5656", {"start": v(388.24, -216.2) * mm, "end": v(388.7, -216.38) * mm});
            skLineSegment(sketch, "E5657", {"start": v(388.7, -216.38) * mm, "end": v(389.14, -216.62) * mm});
            skLineSegment(sketch, "E5658", {"start": v(389.14, -216.62) * mm, "end": v(389.55, -216.92) * mm});
            skLineSegment(sketch, "E5659", {"start": v(389.55, -216.92) * mm, "end": v(389.92, -217.26) * mm});
            skLineSegment(sketch, "E5660", {"start": v(389.92, -217.26) * mm, "end": v(390.24, -217.65) * mm});
            skLineSegment(sketch, "E5661", {"start": v(390.24, -217.65) * mm, "end": v(390.5, -218.07) * mm});
            skLineSegment(sketch, "E5662", {"start": v(390.5, -218.07) * mm, "end": v(390.72, -218.53) * mm});
            skLineSegment(sketch, "E5663", {"start": v(390.72, -218.53) * mm, "end": v(390.87, -219) * mm});
            skLineSegment(sketch, "E5664", {"start": v(390.87, -219) * mm, "end": v(390.97, -219.5) * mm});
            skLineSegment(sketch, "E5665", {"start": v(390.97, -219.5) * mm, "end": v(391, -220) * mm});
            skLineSegment(sketch, "E5666", {"start": v(391, -220) * mm, "end": v(390.97, -220.5) * mm});
            skLineSegment(sketch, "E5667", {"start": v(390.97, -220.5) * mm, "end": v(390.87, -221) * mm});
            skLineSegment(sketch, "E5668", {"start": v(390.87, -221) * mm, "end": v(390.72, -221.47) * mm});
            skLineSegment(sketch, "E5669", {"start": v(390.72, -221.47) * mm, "end": v(390.5, -221.93) * mm});
            skLineSegment(sketch, "E5670", {"start": v(390.5, -221.93) * mm, "end": v(390.24, -222.35) * mm});
            skLineSegment(sketch, "E5671", {"start": v(390.24, -222.35) * mm, "end": v(389.92, -222.74) * mm});
            skLineSegment(sketch, "E5672", {"start": v(389.92, -222.74) * mm, "end": v(389.55, -223.08) * mm});
            skLineSegment(sketch, "E5673", {"start": v(389.55, -223.08) * mm, "end": v(389.14, -223.38) * mm});
            skLineSegment(sketch, "E5674", {"start": v(389.14, -223.38) * mm, "end": v(388.7, -223.62) * mm});
            skLineSegment(sketch, "E5675", {"start": v(388.7, -223.62) * mm, "end": v(388.24, -223.8) * mm});
            skLineSegment(sketch, "E5676", {"start": v(388.24, -223.8) * mm, "end": v(387.75, -223.93) * mm});
            skLineSegment(sketch, "E5677", {"start": v(387.75, -223.93) * mm, "end": v(387.25, -224) * mm});
            skLineSegment(sketch, "E5678", {"start": v(387.25, -224) * mm, "end": v(386.75, -224) * mm});
            skLineSegment(sketch, "E5679", {"start": v(55.4, -237) * mm, "end": v(55.22, -236.97) * mm});
            skLineSegment(sketch, "E5680", {"start": v(55.22, -236.97) * mm, "end": v(55.04, -236.93) * mm});
            skLineSegment(sketch, "E5681", {"start": v(55.04, -236.93) * mm, "end": v(54.86, -236.86) * mm});
            skLineSegment(sketch, "E5682", {"start": v(54.86, -236.86) * mm, "end": v(54.7, -236.77) * mm});
            skLineSegment(sketch, "E5683", {"start": v(54.7, -236.77) * mm, "end": v(54.54, -236.66) * mm});
            skLineSegment(sketch, "E5684", {"start": v(54.54, -236.66) * mm, "end": v(54.4, -236.53) * mm});
            skLineSegment(sketch, "E5685", {"start": v(54.4, -236.53) * mm, "end": v(54.29, -236.38) * mm});
            skLineSegment(sketch, "E5686", {"start": v(54.29, -236.38) * mm, "end": v(54.19, -236.22) * mm});
            skLineSegment(sketch, "E5687", {"start": v(54.19, -236.22) * mm, "end": v(54.1, -236.05) * mm});
            skLineSegment(sketch, "E5688", {"start": v(54.1, -236.05) * mm, "end": v(54.05, -235.87) * mm});
            skLineSegment(sketch, "E5689", {"start": v(54.05, -235.87) * mm, "end": v(54.01, -235.69) * mm});
            skLineSegment(sketch, "E5690", {"start": v(54.01, -235.69) * mm, "end": v(54, -235.5) * mm});
            skLineSegment(sketch, "E5691", {"start": v(54, -235.5) * mm, "end": v(54.01, -235.31) * mm});
            skLineSegment(sketch, "E5692", {"start": v(54.01, -235.31) * mm, "end": v(54.05, -235.13) * mm});
            skLineSegment(sketch, "E5693", {"start": v(54.05, -235.13) * mm, "end": v(54.1, -234.95) * mm});
            skLineSegment(sketch, "E5694", {"start": v(54.1, -234.95) * mm, "end": v(54.19, -234.78) * mm});
            skLineSegment(sketch, "E5695", {"start": v(54.19, -234.78) * mm, "end": v(54.29, -234.62) * mm});
            skLineSegment(sketch, "E5696", {"start": v(54.29, -234.62) * mm, "end": v(54.4, -234.47) * mm});
            skLineSegment(sketch, "E5697", {"start": v(54.4, -234.47) * mm, "end": v(54.54, -234.34) * mm});
            skLineSegment(sketch, "E5698", {"start": v(54.54, -234.34) * mm, "end": v(54.7, -234.23) * mm});
            skLineSegment(sketch, "E5699", {"start": v(54.7, -234.23) * mm, "end": v(54.86, -234.14) * mm});
            skLineSegment(sketch, "E5700", {"start": v(54.86, -234.14) * mm, "end": v(55.04, -234.07) * mm});
            skLineSegment(sketch, "E5701", {"start": v(55.04, -234.07) * mm, "end": v(55.22, -234.03) * mm});
            skLineSegment(sketch, "E5702", {"start": v(55.22, -234.03) * mm, "end": v(55.4, -234) * mm});
            skLineSegment(sketch, "E5703", {"start": v(55.4, -234) * mm, "end": v(55.6, -234) * mm});
            skLineSegment(sketch, "E5704", {"start": v(55.6, -234) * mm, "end": v(55.78, -234.03) * mm});
            skLineSegment(sketch, "E5705", {"start": v(55.78, -234.03) * mm, "end": v(55.96, -234.07) * mm});
            skLineSegment(sketch, "E5706", {"start": v(55.96, -234.07) * mm, "end": v(56.14, -234.14) * mm});
            skLineSegment(sketch, "E5707", {"start": v(56.14, -234.14) * mm, "end": v(56.3, -234.23) * mm});
            skLineSegment(sketch, "E5708", {"start": v(56.3, -234.23) * mm, "end": v(56.46, -234.34) * mm});
            skLineSegment(sketch, "E5709", {"start": v(56.46, -234.34) * mm, "end": v(56.6, -234.47) * mm});
            skLineSegment(sketch, "E5710", {"start": v(56.6, -234.47) * mm, "end": v(56.71, -234.62) * mm});
            skLineSegment(sketch, "E5711", {"start": v(56.71, -234.62) * mm, "end": v(56.81, -234.78) * mm});
            skLineSegment(sketch, "E5712", {"start": v(56.81, -234.78) * mm, "end": v(56.9, -234.95) * mm});
            skLineSegment(sketch, "E5713", {"start": v(56.9, -234.95) * mm, "end": v(56.95, -235.13) * mm});
            skLineSegment(sketch, "E5714", {"start": v(56.95, -235.13) * mm, "end": v(56.99, -235.31) * mm});
            skLineSegment(sketch, "E5715", {"start": v(56.99, -235.31) * mm, "end": v(57, -235.5) * mm});
            skLineSegment(sketch, "E5716", {"start": v(57, -235.5) * mm, "end": v(56.99, -235.69) * mm});
            skLineSegment(sketch, "E5717", {"start": v(56.99, -235.69) * mm, "end": v(56.95, -235.87) * mm});
            skLineSegment(sketch, "E5718", {"start": v(56.95, -235.87) * mm, "end": v(56.9, -236.05) * mm});
            skLineSegment(sketch, "E5719", {"start": v(56.9, -236.05) * mm, "end": v(56.81, -236.22) * mm});
            skLineSegment(sketch, "E5720", {"start": v(56.81, -236.22) * mm, "end": v(56.71, -236.38) * mm});
            skLineSegment(sketch, "E5721", {"start": v(56.71, -236.38) * mm, "end": v(56.6, -236.53) * mm});
            skLineSegment(sketch, "E5722", {"start": v(56.6, -236.53) * mm, "end": v(56.46, -236.66) * mm});
            skLineSegment(sketch, "E5723", {"start": v(56.46, -236.66) * mm, "end": v(56.3, -236.77) * mm});
            skLineSegment(sketch, "E5724", {"start": v(56.3, -236.77) * mm, "end": v(56.14, -236.86) * mm});
            skLineSegment(sketch, "E5725", {"start": v(56.14, -236.86) * mm, "end": v(55.96, -236.93) * mm});
            skLineSegment(sketch, "E5726", {"start": v(55.96, -236.93) * mm, "end": v(55.78, -236.97) * mm});
            skLineSegment(sketch, "E5727", {"start": v(55.78, -236.97) * mm, "end": v(55.6, -237) * mm});
            skLineSegment(sketch, "E5728", {"start": v(55.6, -237) * mm, "end": v(55.4, -237) * mm});
            skLineSegment(sketch, "E5729", {"start": v(354.4, -237) * mm, "end": v(354.22, -236.97) * mm});
            skLineSegment(sketch, "E5730", {"start": v(354.22, -236.97) * mm, "end": v(354.04, -236.93) * mm});
            skLineSegment(sketch, "E5731", {"start": v(354.04, -236.93) * mm, "end": v(353.86, -236.86) * mm});
            skLineSegment(sketch, "E5732", {"start": v(353.86, -236.86) * mm, "end": v(353.7, -236.77) * mm});
            skLineSegment(sketch, "E5733", {"start": v(353.7, -236.77) * mm, "end": v(353.54, -236.66) * mm});
            skLineSegment(sketch, "E5734", {"start": v(353.54, -236.66) * mm, "end": v(353.4, -236.53) * mm});
            skLineSegment(sketch, "E5735", {"start": v(353.4, -236.53) * mm, "end": v(353.29, -236.38) * mm});
            skLineSegment(sketch, "E5736", {"start": v(353.29, -236.38) * mm, "end": v(353.19, -236.22) * mm});
            skLineSegment(sketch, "E5737", {"start": v(353.19, -236.22) * mm, "end": v(353.1, -236.05) * mm});
            skLineSegment(sketch, "E5738", {"start": v(353.1, -236.05) * mm, "end": v(353.05, -235.87) * mm});
            skLineSegment(sketch, "E5739", {"start": v(353.05, -235.87) * mm, "end": v(353.01, -235.69) * mm});
            skLineSegment(sketch, "E5740", {"start": v(353.01, -235.69) * mm, "end": v(353, -235.5) * mm});
            skLineSegment(sketch, "E5741", {"start": v(353, -235.5) * mm, "end": v(353.01, -235.31) * mm});
            skLineSegment(sketch, "E5742", {"start": v(353.01, -235.31) * mm, "end": v(353.05, -235.13) * mm});
            skLineSegment(sketch, "E5743", {"start": v(353.05, -235.13) * mm, "end": v(353.1, -234.95) * mm});
            skLineSegment(sketch, "E5744", {"start": v(353.1, -234.95) * mm, "end": v(353.19, -234.78) * mm});
            skLineSegment(sketch, "E5745", {"start": v(353.19, -234.78) * mm, "end": v(353.29, -234.62) * mm});
            skLineSegment(sketch, "E5746", {"start": v(353.29, -234.62) * mm, "end": v(353.4, -234.47) * mm});
            skLineSegment(sketch, "E5747", {"start": v(353.4, -234.47) * mm, "end": v(353.54, -234.34) * mm});
            skLineSegment(sketch, "E5748", {"start": v(353.54, -234.34) * mm, "end": v(353.7, -234.23) * mm});
            skLineSegment(sketch, "E5749", {"start": v(353.7, -234.23) * mm, "end": v(353.86, -234.14) * mm});
            skLineSegment(sketch, "E5750", {"start": v(353.86, -234.14) * mm, "end": v(354.04, -234.07) * mm});
            skLineSegment(sketch, "E5751", {"start": v(354.04, -234.07) * mm, "end": v(354.22, -234.03) * mm});
            skLineSegment(sketch, "E5752", {"start": v(354.22, -234.03) * mm, "end": v(354.4, -234) * mm});
            skLineSegment(sketch, "E5753", {"start": v(354.4, -234) * mm, "end": v(354.6, -234) * mm});
            skLineSegment(sketch, "E5754", {"start": v(354.6, -234) * mm, "end": v(354.78, -234.03) * mm});
            skLineSegment(sketch, "E5755", {"start": v(354.78, -234.03) * mm, "end": v(354.96, -234.07) * mm});
            skLineSegment(sketch, "E5756", {"start": v(354.96, -234.07) * mm, "end": v(355.14, -234.14) * mm});
            skLineSegment(sketch, "E5757", {"start": v(355.14, -234.14) * mm, "end": v(355.3, -234.23) * mm});
            skLineSegment(sketch, "E5758", {"start": v(355.3, -234.23) * mm, "end": v(355.46, -234.34) * mm});
            skLineSegment(sketch, "E5759", {"start": v(355.46, -234.34) * mm, "end": v(355.6, -234.47) * mm});
            skLineSegment(sketch, "E5760", {"start": v(355.6, -234.47) * mm, "end": v(355.71, -234.62) * mm});
            skLineSegment(sketch, "E5761", {"start": v(355.71, -234.62) * mm, "end": v(355.81, -234.78) * mm});
            skLineSegment(sketch, "E5762", {"start": v(355.81, -234.78) * mm, "end": v(355.9, -234.95) * mm});
            skLineSegment(sketch, "E5763", {"start": v(355.9, -234.95) * mm, "end": v(355.95, -235.13) * mm});
            skLineSegment(sketch, "E5764", {"start": v(355.95, -235.13) * mm, "end": v(355.99, -235.31) * mm});
            skLineSegment(sketch, "E5765", {"start": v(355.99, -235.31) * mm, "end": v(356, -235.5) * mm});
            skLineSegment(sketch, "E5766", {"start": v(356, -235.5) * mm, "end": v(355.99, -235.69) * mm});
            skLineSegment(sketch, "E5767", {"start": v(355.99, -235.69) * mm, "end": v(355.95, -235.87) * mm});
            skLineSegment(sketch, "E5768", {"start": v(355.95, -235.87) * mm, "end": v(355.9, -236.05) * mm});
            skLineSegment(sketch, "E5769", {"start": v(355.9, -236.05) * mm, "end": v(355.81, -236.22) * mm});
            skLineSegment(sketch, "E5770", {"start": v(355.81, -236.22) * mm, "end": v(355.71, -236.38) * mm});
            skLineSegment(sketch, "E5771", {"start": v(355.71, -236.38) * mm, "end": v(355.6, -236.53) * mm});
            skLineSegment(sketch, "E5772", {"start": v(355.6, -236.53) * mm, "end": v(355.46, -236.66) * mm});
            skLineSegment(sketch, "E5773", {"start": v(355.46, -236.66) * mm, "end": v(355.3, -236.77) * mm});
            skLineSegment(sketch, "E5774", {"start": v(355.3, -236.77) * mm, "end": v(355.14, -236.86) * mm});
            skLineSegment(sketch, "E5775", {"start": v(355.14, -236.86) * mm, "end": v(354.96, -236.93) * mm});
            skLineSegment(sketch, "E5776", {"start": v(354.96, -236.93) * mm, "end": v(354.78, -236.97) * mm});
            skLineSegment(sketch, "E5777", {"start": v(354.78, -236.97) * mm, "end": v(354.6, -237) * mm});
            skLineSegment(sketch, "E5778", {"start": v(354.6, -237) * mm, "end": v(354.4, -237) * mm});
            skLineSegment(sketch, "E5779", {"start": v(24.4, -237) * mm, "end": v(24.22, -236.97) * mm});
            skLineSegment(sketch, "E5780", {"start": v(24.22, -236.97) * mm, "end": v(24.04, -236.93) * mm});
            skLineSegment(sketch, "E5781", {"start": v(24.04, -236.93) * mm, "end": v(23.86, -236.86) * mm});
            skLineSegment(sketch, "E5782", {"start": v(23.86, -236.86) * mm, "end": v(23.7, -236.77) * mm});
            skLineSegment(sketch, "E5783", {"start": v(23.7, -236.77) * mm, "end": v(23.54, -236.66) * mm});
            skLineSegment(sketch, "E5784", {"start": v(23.54, -236.66) * mm, "end": v(23.4, -236.53) * mm});
            skLineSegment(sketch, "E5785", {"start": v(23.4, -236.53) * mm, "end": v(23.29, -236.38) * mm});
            skLineSegment(sketch, "E5786", {"start": v(23.29, -236.38) * mm, "end": v(23.19, -236.22) * mm});
            skLineSegment(sketch, "E5787", {"start": v(23.19, -236.22) * mm, "end": v(23.1, -236.05) * mm});
            skLineSegment(sketch, "E5788", {"start": v(23.1, -236.05) * mm, "end": v(23.05, -235.87) * mm});
            skLineSegment(sketch, "E5789", {"start": v(23.05, -235.87) * mm, "end": v(23.01, -235.69) * mm});
            skLineSegment(sketch, "E5790", {"start": v(23.01, -235.69) * mm, "end": v(23, -235.5) * mm});
            skLineSegment(sketch, "E5791", {"start": v(23, -235.5) * mm, "end": v(23.01, -235.31) * mm});
            skLineSegment(sketch, "E5792", {"start": v(23.01, -235.31) * mm, "end": v(23.05, -235.13) * mm});
            skLineSegment(sketch, "E5793", {"start": v(23.05, -235.13) * mm, "end": v(23.1, -234.95) * mm});
            skLineSegment(sketch, "E5794", {"start": v(23.1, -234.95) * mm, "end": v(23.19, -234.78) * mm});
            skLineSegment(sketch, "E5795", {"start": v(23.19, -234.78) * mm, "end": v(23.29, -234.62) * mm});
            skLineSegment(sketch, "E5796", {"start": v(23.29, -234.62) * mm, "end": v(23.4, -234.47) * mm});
            skLineSegment(sketch, "E5797", {"start": v(23.4, -234.47) * mm, "end": v(23.54, -234.34) * mm});
            skLineSegment(sketch, "E5798", {"start": v(23.54, -234.34) * mm, "end": v(23.7, -234.23) * mm});
            skLineSegment(sketch, "E5799", {"start": v(23.7, -234.23) * mm, "end": v(23.86, -234.14) * mm});
            skLineSegment(sketch, "E5800", {"start": v(23.86, -234.14) * mm, "end": v(24.04, -234.07) * mm});
            skLineSegment(sketch, "E5801", {"start": v(24.04, -234.07) * mm, "end": v(24.22, -234.03) * mm});
            skLineSegment(sketch, "E5802", {"start": v(24.22, -234.03) * mm, "end": v(24.4, -234) * mm});
            skLineSegment(sketch, "E5803", {"start": v(24.4, -234) * mm, "end": v(24.6, -234) * mm});
            skLineSegment(sketch, "E5804", {"start": v(24.6, -234) * mm, "end": v(24.78, -234.03) * mm});
            skLineSegment(sketch, "E5805", {"start": v(24.78, -234.03) * mm, "end": v(24.96, -234.07) * mm});
            skLineSegment(sketch, "E5806", {"start": v(24.96, -234.07) * mm, "end": v(25.14, -234.14) * mm});
            skLineSegment(sketch, "E5807", {"start": v(25.14, -234.14) * mm, "end": v(25.3, -234.23) * mm});
            skLineSegment(sketch, "E5808", {"start": v(25.3, -234.23) * mm, "end": v(25.46, -234.34) * mm});
            skLineSegment(sketch, "E5809", {"start": v(25.46, -234.34) * mm, "end": v(25.6, -234.47) * mm});
            skLineSegment(sketch, "E5810", {"start": v(25.6, -234.47) * mm, "end": v(25.71, -234.62) * mm});
            skLineSegment(sketch, "E5811", {"start": v(25.71, -234.62) * mm, "end": v(25.81, -234.78) * mm});
            skLineSegment(sketch, "E5812", {"start": v(25.81, -234.78) * mm, "end": v(25.9, -234.95) * mm});
            skLineSegment(sketch, "E5813", {"start": v(25.9, -234.95) * mm, "end": v(25.95, -235.13) * mm});
            skLineSegment(sketch, "E5814", {"start": v(25.95, -235.13) * mm, "end": v(25.99, -235.31) * mm});
            skLineSegment(sketch, "E5815", {"start": v(25.99, -235.31) * mm, "end": v(26, -235.5) * mm});
            skLineSegment(sketch, "E5816", {"start": v(26, -235.5) * mm, "end": v(25.99, -235.69) * mm});
            skLineSegment(sketch, "E5817", {"start": v(25.99, -235.69) * mm, "end": v(25.95, -235.87) * mm});
            skLineSegment(sketch, "E5818", {"start": v(25.95, -235.87) * mm, "end": v(25.9, -236.05) * mm});
            skLineSegment(sketch, "E5819", {"start": v(25.9, -236.05) * mm, "end": v(25.81, -236.22) * mm});
            skLineSegment(sketch, "E5820", {"start": v(25.81, -236.22) * mm, "end": v(25.71, -236.38) * mm});
            skLineSegment(sketch, "E5821", {"start": v(25.71, -236.38) * mm, "end": v(25.6, -236.53) * mm});
            skLineSegment(sketch, "E5822", {"start": v(25.6, -236.53) * mm, "end": v(25.46, -236.66) * mm});
            skLineSegment(sketch, "E5823", {"start": v(25.46, -236.66) * mm, "end": v(25.3, -236.77) * mm});
            skLineSegment(sketch, "E5824", {"start": v(25.3, -236.77) * mm, "end": v(25.14, -236.86) * mm});
            skLineSegment(sketch, "E5825", {"start": v(25.14, -236.86) * mm, "end": v(24.96, -236.93) * mm});
            skLineSegment(sketch, "E5826", {"start": v(24.96, -236.93) * mm, "end": v(24.78, -236.97) * mm});
            skLineSegment(sketch, "E5827", {"start": v(24.78, -236.97) * mm, "end": v(24.6, -237) * mm});
            skLineSegment(sketch, "E5828", {"start": v(24.6, -237) * mm, "end": v(24.4, -237) * mm});
            skLineSegment(sketch, "E5829", {"start": v(385.4, -237) * mm, "end": v(385.22, -236.97) * mm});
            skLineSegment(sketch, "E5830", {"start": v(385.22, -236.97) * mm, "end": v(385.04, -236.93) * mm});
            skLineSegment(sketch, "E5831", {"start": v(385.04, -236.93) * mm, "end": v(384.86, -236.86) * mm});
            skLineSegment(sketch, "E5832", {"start": v(384.86, -236.86) * mm, "end": v(384.7, -236.77) * mm});
            skLineSegment(sketch, "E5833", {"start": v(384.7, -236.77) * mm, "end": v(384.54, -236.66) * mm});
            skLineSegment(sketch, "E5834", {"start": v(384.54, -236.66) * mm, "end": v(384.4, -236.53) * mm});
            skLineSegment(sketch, "E5835", {"start": v(384.4, -236.53) * mm, "end": v(384.29, -236.38) * mm});
            skLineSegment(sketch, "E5836", {"start": v(384.29, -236.38) * mm, "end": v(384.19, -236.22) * mm});
            skLineSegment(sketch, "E5837", {"start": v(384.19, -236.22) * mm, "end": v(384.1, -236.05) * mm});
            skLineSegment(sketch, "E5838", {"start": v(384.1, -236.05) * mm, "end": v(384.05, -235.87) * mm});
            skLineSegment(sketch, "E5839", {"start": v(384.05, -235.87) * mm, "end": v(384.01, -235.69) * mm});
            skLineSegment(sketch, "E5840", {"start": v(384.01, -235.69) * mm, "end": v(384, -235.5) * mm});
            skLineSegment(sketch, "E5841", {"start": v(384, -235.5) * mm, "end": v(384.01, -235.31) * mm});
            skLineSegment(sketch, "E5842", {"start": v(384.01, -235.31) * mm, "end": v(384.05, -235.13) * mm});
            skLineSegment(sketch, "E5843", {"start": v(384.05, -235.13) * mm, "end": v(384.1, -234.95) * mm});
            skLineSegment(sketch, "E5844", {"start": v(384.1, -234.95) * mm, "end": v(384.19, -234.78) * mm});
            skLineSegment(sketch, "E5845", {"start": v(384.19, -234.78) * mm, "end": v(384.29, -234.62) * mm});
            skLineSegment(sketch, "E5846", {"start": v(384.29, -234.62) * mm, "end": v(384.4, -234.47) * mm});
            skLineSegment(sketch, "E5847", {"start": v(384.4, -234.47) * mm, "end": v(384.54, -234.34) * mm});
            skLineSegment(sketch, "E5848", {"start": v(384.54, -234.34) * mm, "end": v(384.7, -234.23) * mm});
            skLineSegment(sketch, "E5849", {"start": v(384.7, -234.23) * mm, "end": v(384.86, -234.14) * mm});
            skLineSegment(sketch, "E5850", {"start": v(384.86, -234.14) * mm, "end": v(385.04, -234.07) * mm});
            skLineSegment(sketch, "E5851", {"start": v(385.04, -234.07) * mm, "end": v(385.22, -234.03) * mm});
            skLineSegment(sketch, "E5852", {"start": v(385.22, -234.03) * mm, "end": v(385.4, -234) * mm});
            skLineSegment(sketch, "E5853", {"start": v(385.4, -234) * mm, "end": v(385.6, -234) * mm});
            skLineSegment(sketch, "E5854", {"start": v(385.6, -234) * mm, "end": v(385.78, -234.03) * mm});
            skLineSegment(sketch, "E5855", {"start": v(385.78, -234.03) * mm, "end": v(385.96, -234.07) * mm});
            skLineSegment(sketch, "E5856", {"start": v(385.96, -234.07) * mm, "end": v(386.14, -234.14) * mm});
            skLineSegment(sketch, "E5857", {"start": v(386.14, -234.14) * mm, "end": v(386.3, -234.23) * mm});
            skLineSegment(sketch, "E5858", {"start": v(386.3, -234.23) * mm, "end": v(386.46, -234.34) * mm});
            skLineSegment(sketch, "E5859", {"start": v(386.46, -234.34) * mm, "end": v(386.6, -234.47) * mm});
            skLineSegment(sketch, "E5860", {"start": v(386.6, -234.47) * mm, "end": v(386.71, -234.62) * mm});
            skLineSegment(sketch, "E5861", {"start": v(386.71, -234.62) * mm, "end": v(386.81, -234.78) * mm});
            skLineSegment(sketch, "E5862", {"start": v(386.81, -234.78) * mm, "end": v(386.9, -234.95) * mm});
            skLineSegment(sketch, "E5863", {"start": v(386.9, -234.95) * mm, "end": v(386.95, -235.13) * mm});
            skLineSegment(sketch, "E5864", {"start": v(386.95, -235.13) * mm, "end": v(386.99, -235.31) * mm});
            skLineSegment(sketch, "E5865", {"start": v(386.99, -235.31) * mm, "end": v(387, -235.5) * mm});
            skLineSegment(sketch, "E5866", {"start": v(387, -235.5) * mm, "end": v(386.99, -235.69) * mm});
            skLineSegment(sketch, "E5867", {"start": v(386.99, -235.69) * mm, "end": v(386.95, -235.87) * mm});
            skLineSegment(sketch, "E5868", {"start": v(386.95, -235.87) * mm, "end": v(386.9, -236.05) * mm});
            skLineSegment(sketch, "E5869", {"start": v(386.9, -236.05) * mm, "end": v(386.81, -236.22) * mm});
            skLineSegment(sketch, "E5870", {"start": v(386.81, -236.22) * mm, "end": v(386.71, -236.38) * mm});
            skLineSegment(sketch, "E5871", {"start": v(386.71, -236.38) * mm, "end": v(386.6, -236.53) * mm});
            skLineSegment(sketch, "E5872", {"start": v(386.6, -236.53) * mm, "end": v(386.46, -236.66) * mm});
            skLineSegment(sketch, "E5873", {"start": v(386.46, -236.66) * mm, "end": v(386.3, -236.77) * mm});
            skLineSegment(sketch, "E5874", {"start": v(386.3, -236.77) * mm, "end": v(386.14, -236.86) * mm});
            skLineSegment(sketch, "E5875", {"start": v(386.14, -236.86) * mm, "end": v(385.96, -236.93) * mm});
            skLineSegment(sketch, "E5876", {"start": v(385.96, -236.93) * mm, "end": v(385.78, -236.97) * mm});
            skLineSegment(sketch, "E5877", {"start": v(385.78, -236.97) * mm, "end": v(385.6, -237) * mm});
            skLineSegment(sketch, "E5878", {"start": v(385.6, -237) * mm, "end": v(385.4, -237) * mm});
            skLineSegment(sketch, "E5879", {"start": v(204.84, -427.5) * mm, "end": v(204.53, -427.46) * mm});
            skLineSegment(sketch, "E5880", {"start": v(204.53, -427.46) * mm, "end": v(204.23, -427.38) * mm});
            skLineSegment(sketch, "E5881", {"start": v(204.23, -427.38) * mm, "end": v(203.94, -427.26) * mm});
            skLineSegment(sketch, "E5882", {"start": v(203.94, -427.26) * mm, "end": v(203.66, -427.11) * mm});
            skLineSegment(sketch, "E5883", {"start": v(203.66, -427.11) * mm, "end": v(203.4, -426.93) * mm});
            skLineSegment(sketch, "E5884", {"start": v(203.4, -426.93) * mm, "end": v(203.18, -426.71) * mm});
            skLineSegment(sketch, "E5885", {"start": v(203.18, -426.71) * mm, "end": v(202.98, -426.47) * mm});
            skLineSegment(sketch, "E5886", {"start": v(202.98, -426.47) * mm, "end": v(202.8, -426.2) * mm});
            skLineSegment(sketch, "E5887", {"start": v(202.8, -426.2) * mm, "end": v(202.68, -425.92) * mm});
            skLineSegment(sketch, "E5888", {"start": v(202.68, -425.92) * mm, "end": v(202.58, -425.62) * mm});
            skLineSegment(sketch, "E5889", {"start": v(202.58, -425.62) * mm, "end": v(202.52, -425.31) * mm});
            skLineSegment(sketch, "E5890", {"start": v(202.52, -425.31) * mm, "end": v(202.5, -425) * mm});
            skLineSegment(sketch, "E5891", {"start": v(202.5, -425) * mm, "end": v(202.52, -424.69) * mm});
            skLineSegment(sketch, "E5892", {"start": v(202.52, -424.69) * mm, "end": v(202.58, -424.38) * mm});
            skLineSegment(sketch, "E5893", {"start": v(202.58, -424.38) * mm, "end": v(202.68, -424.08) * mm});
            skLineSegment(sketch, "E5894", {"start": v(202.68, -424.08) * mm, "end": v(202.8, -423.8) * mm});
            skLineSegment(sketch, "E5895", {"start": v(202.8, -423.8) * mm, "end": v(202.98, -423.53) * mm});
            skLineSegment(sketch, "E5896", {"start": v(202.98, -423.53) * mm, "end": v(203.18, -423.29) * mm});
            skLineSegment(sketch, "E5897", {"start": v(203.18, -423.29) * mm, "end": v(203.4, -423.07) * mm});
            skLineSegment(sketch, "E5898", {"start": v(203.4, -423.07) * mm, "end": v(203.66, -422.89) * mm});
            skLineSegment(sketch, "E5899", {"start": v(203.66, -422.89) * mm, "end": v(203.94, -422.74) * mm});
            skLineSegment(sketch, "E5900", {"start": v(203.94, -422.74) * mm, "end": v(204.23, -422.62) * mm});
            skLineSegment(sketch, "E5901", {"start": v(204.23, -422.62) * mm, "end": v(204.53, -422.54) * mm});
            skLineSegment(sketch, "E5902", {"start": v(204.53, -422.54) * mm, "end": v(204.84, -422.5) * mm});
            skLineSegment(sketch, "E5903", {"start": v(204.84, -422.5) * mm, "end": v(205.16, -422.5) * mm});
            skLineSegment(sketch, "E5904", {"start": v(205.16, -422.5) * mm, "end": v(205.47, -422.54) * mm});
            skLineSegment(sketch, "E5905", {"start": v(205.47, -422.54) * mm, "end": v(205.77, -422.62) * mm});
            skLineSegment(sketch, "E5906", {"start": v(205.77, -422.62) * mm, "end": v(206.06, -422.74) * mm});
            skLineSegment(sketch, "E5907", {"start": v(206.06, -422.74) * mm, "end": v(206.34, -422.89) * mm});
            skLineSegment(sketch, "E5908", {"start": v(206.34, -422.89) * mm, "end": v(206.6, -423.07) * mm});
            skLineSegment(sketch, "E5909", {"start": v(206.6, -423.07) * mm, "end": v(206.82, -423.29) * mm});
            skLineSegment(sketch, "E5910", {"start": v(206.82, -423.29) * mm, "end": v(207.02, -423.53) * mm});
            skLineSegment(sketch, "E5911", {"start": v(207.02, -423.53) * mm, "end": v(207.2, -423.8) * mm});
            skLineSegment(sketch, "E5912", {"start": v(207.2, -423.8) * mm, "end": v(207.32, -424.08) * mm});
            skLineSegment(sketch, "E5913", {"start": v(207.32, -424.08) * mm, "end": v(207.42, -424.38) * mm});
            skLineSegment(sketch, "E5914", {"start": v(207.42, -424.38) * mm, "end": v(207.48, -424.69) * mm});
            skLineSegment(sketch, "E5915", {"start": v(207.48, -424.69) * mm, "end": v(207.5, -425) * mm});
            skLineSegment(sketch, "E5916", {"start": v(207.5, -425) * mm, "end": v(207.48, -425.31) * mm});
            skLineSegment(sketch, "E5917", {"start": v(207.48, -425.31) * mm, "end": v(207.42, -425.62) * mm});
            skLineSegment(sketch, "E5918", {"start": v(207.42, -425.62) * mm, "end": v(207.32, -425.92) * mm});
            skLineSegment(sketch, "E5919", {"start": v(207.32, -425.92) * mm, "end": v(207.2, -426.2) * mm});
            skLineSegment(sketch, "E5920", {"start": v(207.2, -426.2) * mm, "end": v(207.02, -426.47) * mm});
            skLineSegment(sketch, "E5921", {"start": v(207.02, -426.47) * mm, "end": v(206.82, -426.71) * mm});
            skLineSegment(sketch, "E5922", {"start": v(206.82, -426.71) * mm, "end": v(206.6, -426.93) * mm});
            skLineSegment(sketch, "E5923", {"start": v(206.6, -426.93) * mm, "end": v(206.34, -427.11) * mm});
            skLineSegment(sketch, "E5924", {"start": v(206.34, -427.11) * mm, "end": v(206.06, -427.26) * mm});
            skLineSegment(sketch, "E5925", {"start": v(206.06, -427.26) * mm, "end": v(205.77, -427.38) * mm});
            skLineSegment(sketch, "E5926", {"start": v(205.77, -427.38) * mm, "end": v(205.47, -427.46) * mm});
            skLineSegment(sketch, "E5927", {"start": v(205.47, -427.46) * mm, "end": v(205.16, -427.5) * mm});
            skLineSegment(sketch, "E5928", {"start": v(205.16, -427.5) * mm, "end": v(204.84, -427.5) * mm});
            skLineSegment(sketch, "E5929", {"start": v(141.9, -448.5) * mm, "end": v(141.72, -448.47) * mm});
            skLineSegment(sketch, "E5930", {"start": v(141.72, -448.47) * mm, "end": v(141.54, -448.43) * mm});
            skLineSegment(sketch, "E5931", {"start": v(141.54, -448.43) * mm, "end": v(141.36, -448.36) * mm});
            skLineSegment(sketch, "E5932", {"start": v(141.36, -448.36) * mm, "end": v(141.2, -448.27) * mm});
            skLineSegment(sketch, "E5933", {"start": v(141.2, -448.27) * mm, "end": v(141.04, -448.16) * mm});
            skLineSegment(sketch, "E5934", {"start": v(141.04, -448.16) * mm, "end": v(140.9, -448.03) * mm});
            skLineSegment(sketch, "E5935", {"start": v(140.9, -448.03) * mm, "end": v(140.79, -447.88) * mm});
            skLineSegment(sketch, "E5936", {"start": v(140.79, -447.88) * mm, "end": v(140.69, -447.72) * mm});
            skLineSegment(sketch, "E5937", {"start": v(140.69, -447.72) * mm, "end": v(140.6, -447.55) * mm});
            skLineSegment(sketch, "E5938", {"start": v(140.6, -447.55) * mm, "end": v(140.55, -447.37) * mm});
            skLineSegment(sketch, "E5939", {"start": v(140.55, -447.37) * mm, "end": v(140.51, -447.19) * mm});
            skLineSegment(sketch, "E5940", {"start": v(140.51, -447.19) * mm, "end": v(140.5, -447) * mm});
            skLineSegment(sketch, "E5941", {"start": v(140.5, -447) * mm, "end": v(140.51, -446.81) * mm});
            skLineSegment(sketch, "E5942", {"start": v(140.51, -446.81) * mm, "end": v(140.55, -446.63) * mm});
            skLineSegment(sketch, "E5943", {"start": v(140.55, -446.63) * mm, "end": v(140.6, -446.45) * mm});
            skLineSegment(sketch, "E5944", {"start": v(140.6, -446.45) * mm, "end": v(140.69, -446.28) * mm});
            skLineSegment(sketch, "E5945", {"start": v(140.69, -446.28) * mm, "end": v(140.79, -446.12) * mm});
            skLineSegment(sketch, "E5946", {"start": v(140.79, -446.12) * mm, "end": v(140.9, -445.97) * mm});
            skLineSegment(sketch, "E5947", {"start": v(140.9, -445.97) * mm, "end": v(141.04, -445.84) * mm});
            skLineSegment(sketch, "E5948", {"start": v(141.04, -445.84) * mm, "end": v(141.2, -445.73) * mm});
            skLineSegment(sketch, "E5949", {"start": v(141.2, -445.73) * mm, "end": v(141.36, -445.64) * mm});
            skLineSegment(sketch, "E5950", {"start": v(141.36, -445.64) * mm, "end": v(141.54, -445.57) * mm});
            skLineSegment(sketch, "E5951", {"start": v(141.54, -445.57) * mm, "end": v(141.72, -445.53) * mm});
            skLineSegment(sketch, "E5952", {"start": v(141.72, -445.53) * mm, "end": v(141.9, -445.5) * mm});
            skLineSegment(sketch, "E5953", {"start": v(141.9, -445.5) * mm, "end": v(142.1, -445.5) * mm});
            skLineSegment(sketch, "E5954", {"start": v(142.1, -445.5) * mm, "end": v(142.28, -445.53) * mm});
            skLineSegment(sketch, "E5955", {"start": v(142.28, -445.53) * mm, "end": v(142.46, -445.57) * mm});
            skLineSegment(sketch, "E5956", {"start": v(142.46, -445.57) * mm, "end": v(142.64, -445.64) * mm});
            skLineSegment(sketch, "E5957", {"start": v(142.64, -445.64) * mm, "end": v(142.8, -445.73) * mm});
            skLineSegment(sketch, "E5958", {"start": v(142.8, -445.73) * mm, "end": v(142.96, -445.84) * mm});
            skLineSegment(sketch, "E5959", {"start": v(142.96, -445.84) * mm, "end": v(143.1, -445.97) * mm});
            skLineSegment(sketch, "E5960", {"start": v(143.1, -445.97) * mm, "end": v(143.21, -446.12) * mm});
            skLineSegment(sketch, "E5961", {"start": v(143.21, -446.12) * mm, "end": v(143.31, -446.28) * mm});
            skLineSegment(sketch, "E5962", {"start": v(143.31, -446.28) * mm, "end": v(143.4, -446.45) * mm});
            skLineSegment(sketch, "E5963", {"start": v(143.4, -446.45) * mm, "end": v(143.45, -446.63) * mm});
            skLineSegment(sketch, "E5964", {"start": v(143.45, -446.63) * mm, "end": v(143.49, -446.81) * mm});
            skLineSegment(sketch, "E5965", {"start": v(143.49, -446.81) * mm, "end": v(143.5, -447) * mm});
            skLineSegment(sketch, "E5966", {"start": v(143.5, -447) * mm, "end": v(143.49, -447.19) * mm});
            skLineSegment(sketch, "E5967", {"start": v(143.49, -447.19) * mm, "end": v(143.45, -447.37) * mm});
            skLineSegment(sketch, "E5968", {"start": v(143.45, -447.37) * mm, "end": v(143.4, -447.55) * mm});
            skLineSegment(sketch, "E5969", {"start": v(143.4, -447.55) * mm, "end": v(143.31, -447.72) * mm});
            skLineSegment(sketch, "E5970", {"start": v(143.31, -447.72) * mm, "end": v(143.21, -447.88) * mm});
            skLineSegment(sketch, "E5971", {"start": v(143.21, -447.88) * mm, "end": v(143.1, -448.03) * mm});
            skLineSegment(sketch, "E5972", {"start": v(143.1, -448.03) * mm, "end": v(142.96, -448.16) * mm});
            skLineSegment(sketch, "E5973", {"start": v(142.96, -448.16) * mm, "end": v(142.8, -448.27) * mm});
            skLineSegment(sketch, "E5974", {"start": v(142.8, -448.27) * mm, "end": v(142.64, -448.36) * mm});
            skLineSegment(sketch, "E5975", {"start": v(142.64, -448.36) * mm, "end": v(142.46, -448.43) * mm});
            skLineSegment(sketch, "E5976", {"start": v(142.46, -448.43) * mm, "end": v(142.28, -448.47) * mm});
            skLineSegment(sketch, "E5977", {"start": v(142.28, -448.47) * mm, "end": v(142.1, -448.5) * mm});
            skLineSegment(sketch, "E5978", {"start": v(142.1, -448.5) * mm, "end": v(141.9, -448.5) * mm});
            skLineSegment(sketch, "E5979", {"start": v(267.9, -448.5) * mm, "end": v(267.72, -448.47) * mm});
            skLineSegment(sketch, "E5980", {"start": v(267.72, -448.47) * mm, "end": v(267.54, -448.43) * mm});
            skLineSegment(sketch, "E5981", {"start": v(267.54, -448.43) * mm, "end": v(267.36, -448.36) * mm});
            skLineSegment(sketch, "E5982", {"start": v(267.36, -448.36) * mm, "end": v(267.2, -448.27) * mm});
            skLineSegment(sketch, "E5983", {"start": v(267.2, -448.27) * mm, "end": v(267.04, -448.16) * mm});
            skLineSegment(sketch, "E5984", {"start": v(267.04, -448.16) * mm, "end": v(266.9, -448.03) * mm});
            skLineSegment(sketch, "E5985", {"start": v(266.9, -448.03) * mm, "end": v(266.79, -447.88) * mm});
            skLineSegment(sketch, "E5986", {"start": v(266.79, -447.88) * mm, "end": v(266.69, -447.72) * mm});
            skLineSegment(sketch, "E5987", {"start": v(266.69, -447.72) * mm, "end": v(266.6, -447.55) * mm});
            skLineSegment(sketch, "E5988", {"start": v(266.6, -447.55) * mm, "end": v(266.55, -447.37) * mm});
            skLineSegment(sketch, "E5989", {"start": v(266.55, -447.37) * mm, "end": v(266.51, -447.19) * mm});
            skLineSegment(sketch, "E5990", {"start": v(266.51, -447.19) * mm, "end": v(266.5, -447) * mm});
            skLineSegment(sketch, "E5991", {"start": v(266.5, -447) * mm, "end": v(266.51, -446.81) * mm});
            skLineSegment(sketch, "E5992", {"start": v(266.51, -446.81) * mm, "end": v(266.55, -446.63) * mm});
            skLineSegment(sketch, "E5993", {"start": v(266.55, -446.63) * mm, "end": v(266.6, -446.45) * mm});
            skLineSegment(sketch, "E5994", {"start": v(266.6, -446.45) * mm, "end": v(266.69, -446.28) * mm});
            skLineSegment(sketch, "E5995", {"start": v(266.69, -446.28) * mm, "end": v(266.79, -446.12) * mm});
            skLineSegment(sketch, "E5996", {"start": v(266.79, -446.12) * mm, "end": v(266.9, -445.97) * mm});
            skLineSegment(sketch, "E5997", {"start": v(266.9, -445.97) * mm, "end": v(267.04, -445.84) * mm});
            skLineSegment(sketch, "E5998", {"start": v(267.04, -445.84) * mm, "end": v(267.2, -445.73) * mm});
            skLineSegment(sketch, "E5999", {"start": v(267.2, -445.73) * mm, "end": v(267.36, -445.64) * mm});
            skLineSegment(sketch, "E6000", {"start": v(267.36, -445.64) * mm, "end": v(267.54, -445.57) * mm});
            skLineSegment(sketch, "E6001", {"start": v(267.54, -445.57) * mm, "end": v(267.72, -445.53) * mm});
            skLineSegment(sketch, "E6002", {"start": v(267.72, -445.53) * mm, "end": v(267.9, -445.5) * mm});
            skLineSegment(sketch, "E6003", {"start": v(267.9, -445.5) * mm, "end": v(268.1, -445.5) * mm});
            skLineSegment(sketch, "E6004", {"start": v(268.1, -445.5) * mm, "end": v(268.28, -445.53) * mm});
            skLineSegment(sketch, "E6005", {"start": v(268.28, -445.53) * mm, "end": v(268.46, -445.57) * mm});
            skLineSegment(sketch, "E6006", {"start": v(268.46, -445.57) * mm, "end": v(268.64, -445.64) * mm});
            skLineSegment(sketch, "E6007", {"start": v(268.64, -445.64) * mm, "end": v(268.8, -445.73) * mm});
            skLineSegment(sketch, "E6008", {"start": v(268.8, -445.73) * mm, "end": v(268.96, -445.84) * mm});
            skLineSegment(sketch, "E6009", {"start": v(268.96, -445.84) * mm, "end": v(269.1, -445.97) * mm});
            skLineSegment(sketch, "E6010", {"start": v(269.1, -445.97) * mm, "end": v(269.21, -446.12) * mm});
            skLineSegment(sketch, "E6011", {"start": v(269.21, -446.12) * mm, "end": v(269.31, -446.28) * mm});
            skLineSegment(sketch, "E6012", {"start": v(269.31, -446.28) * mm, "end": v(269.4, -446.45) * mm});
            skLineSegment(sketch, "E6013", {"start": v(269.4, -446.45) * mm, "end": v(269.45, -446.63) * mm});
            skLineSegment(sketch, "E6014", {"start": v(269.45, -446.63) * mm, "end": v(269.49, -446.81) * mm});
            skLineSegment(sketch, "E6015", {"start": v(269.49, -446.81) * mm, "end": v(269.5, -447) * mm});
            skLineSegment(sketch, "E6016", {"start": v(269.5, -447) * mm, "end": v(269.49, -447.19) * mm});
            skLineSegment(sketch, "E6017", {"start": v(269.49, -447.19) * mm, "end": v(269.45, -447.37) * mm});
            skLineSegment(sketch, "E6018", {"start": v(269.45, -447.37) * mm, "end": v(269.4, -447.55) * mm});
            skLineSegment(sketch, "E6019", {"start": v(269.4, -447.55) * mm, "end": v(269.31, -447.72) * mm});
            skLineSegment(sketch, "E6020", {"start": v(269.31, -447.72) * mm, "end": v(269.21, -447.88) * mm});
            skLineSegment(sketch, "E6021", {"start": v(269.21, -447.88) * mm, "end": v(269.1, -448.03) * mm});
            skLineSegment(sketch, "E6022", {"start": v(269.1, -448.03) * mm, "end": v(268.96, -448.16) * mm});
            skLineSegment(sketch, "E6023", {"start": v(268.96, -448.16) * mm, "end": v(268.8, -448.27) * mm});
            skLineSegment(sketch, "E6024", {"start": v(268.8, -448.27) * mm, "end": v(268.64, -448.36) * mm});
            skLineSegment(sketch, "E6025", {"start": v(268.64, -448.36) * mm, "end": v(268.46, -448.43) * mm});
            skLineSegment(sketch, "E6026", {"start": v(268.46, -448.43) * mm, "end": v(268.28, -448.47) * mm});
            skLineSegment(sketch, "E6027", {"start": v(268.28, -448.47) * mm, "end": v(268.1, -448.5) * mm});
            skLineSegment(sketch, "E6028", {"start": v(268.1, -448.5) * mm, "end": v(267.9, -448.5) * mm});
            skLineSegment(sketch, "E6029", {"start": v(251.9, -448.5) * mm, "end": v(251.72, -448.47) * mm});
            skLineSegment(sketch, "E6030", {"start": v(251.72, -448.47) * mm, "end": v(251.54, -448.43) * mm});
            skLineSegment(sketch, "E6031", {"start": v(251.54, -448.43) * mm, "end": v(251.36, -448.36) * mm});
            skLineSegment(sketch, "E6032", {"start": v(251.36, -448.36) * mm, "end": v(251.2, -448.27) * mm});
            skLineSegment(sketch, "E6033", {"start": v(251.2, -448.27) * mm, "end": v(251.04, -448.16) * mm});
            skLineSegment(sketch, "E6034", {"start": v(251.04, -448.16) * mm, "end": v(250.9, -448.03) * mm});
            skLineSegment(sketch, "E6035", {"start": v(250.9, -448.03) * mm, "end": v(250.79, -447.88) * mm});
            skLineSegment(sketch, "E6036", {"start": v(250.79, -447.88) * mm, "end": v(250.69, -447.72) * mm});
            skLineSegment(sketch, "E6037", {"start": v(250.69, -447.72) * mm, "end": v(250.6, -447.55) * mm});
            skLineSegment(sketch, "E6038", {"start": v(250.6, -447.55) * mm, "end": v(250.55, -447.37) * mm});
            skLineSegment(sketch, "E6039", {"start": v(250.55, -447.37) * mm, "end": v(250.51, -447.19) * mm});
            skLineSegment(sketch, "E6040", {"start": v(250.51, -447.19) * mm, "end": v(250.5, -447) * mm});
            skLineSegment(sketch, "E6041", {"start": v(250.5, -447) * mm, "end": v(250.51, -446.81) * mm});
            skLineSegment(sketch, "E6042", {"start": v(250.51, -446.81) * mm, "end": v(250.55, -446.63) * mm});
            skLineSegment(sketch, "E6043", {"start": v(250.55, -446.63) * mm, "end": v(250.6, -446.45) * mm});
            skLineSegment(sketch, "E6044", {"start": v(250.6, -446.45) * mm, "end": v(250.69, -446.28) * mm});
            skLineSegment(sketch, "E6045", {"start": v(250.69, -446.28) * mm, "end": v(250.79, -446.12) * mm});
            skLineSegment(sketch, "E6046", {"start": v(250.79, -446.12) * mm, "end": v(250.9, -445.97) * mm});
            skLineSegment(sketch, "E6047", {"start": v(250.9, -445.97) * mm, "end": v(251.04, -445.84) * mm});
            skLineSegment(sketch, "E6048", {"start": v(251.04, -445.84) * mm, "end": v(251.2, -445.73) * mm});
            skLineSegment(sketch, "E6049", {"start": v(251.2, -445.73) * mm, "end": v(251.36, -445.64) * mm});
            skLineSegment(sketch, "E6050", {"start": v(251.36, -445.64) * mm, "end": v(251.54, -445.57) * mm});
            skLineSegment(sketch, "E6051", {"start": v(251.54, -445.57) * mm, "end": v(251.72, -445.53) * mm});
            skLineSegment(sketch, "E6052", {"start": v(251.72, -445.53) * mm, "end": v(251.9, -445.5) * mm});
            skLineSegment(sketch, "E6053", {"start": v(251.9, -445.5) * mm, "end": v(252.1, -445.5) * mm});
            skLineSegment(sketch, "E6054", {"start": v(252.1, -445.5) * mm, "end": v(252.28, -445.53) * mm});
            skLineSegment(sketch, "E6055", {"start": v(252.28, -445.53) * mm, "end": v(252.46, -445.57) * mm});
            skLineSegment(sketch, "E6056", {"start": v(252.46, -445.57) * mm, "end": v(252.64, -445.64) * mm});
            skLineSegment(sketch, "E6057", {"start": v(252.64, -445.64) * mm, "end": v(252.8, -445.73) * mm});
            skLineSegment(sketch, "E6058", {"start": v(252.8, -445.73) * mm, "end": v(252.96, -445.84) * mm});
            skLineSegment(sketch, "E6059", {"start": v(252.96, -445.84) * mm, "end": v(253.1, -445.97) * mm});
            skLineSegment(sketch, "E6060", {"start": v(253.1, -445.97) * mm, "end": v(253.21, -446.12) * mm});
            skLineSegment(sketch, "E6061", {"start": v(253.21, -446.12) * mm, "end": v(253.31, -446.28) * mm});
            skLineSegment(sketch, "E6062", {"start": v(253.31, -446.28) * mm, "end": v(253.4, -446.45) * mm});
            skLineSegment(sketch, "E6063", {"start": v(253.4, -446.45) * mm, "end": v(253.45, -446.63) * mm});
            skLineSegment(sketch, "E6064", {"start": v(253.45, -446.63) * mm, "end": v(253.49, -446.81) * mm});
            skLineSegment(sketch, "E6065", {"start": v(253.49, -446.81) * mm, "end": v(253.5, -447) * mm});
            skLineSegment(sketch, "E6066", {"start": v(253.5, -447) * mm, "end": v(253.49, -447.19) * mm});
            skLineSegment(sketch, "E6067", {"start": v(253.49, -447.19) * mm, "end": v(253.45, -447.37) * mm});
            skLineSegment(sketch, "E6068", {"start": v(253.45, -447.37) * mm, "end": v(253.4, -447.55) * mm});
            skLineSegment(sketch, "E6069", {"start": v(253.4, -447.55) * mm, "end": v(253.31, -447.72) * mm});
            skLineSegment(sketch, "E6070", {"start": v(253.31, -447.72) * mm, "end": v(253.21, -447.88) * mm});
            skLineSegment(sketch, "E6071", {"start": v(253.21, -447.88) * mm, "end": v(253.1, -448.03) * mm});
            skLineSegment(sketch, "E6072", {"start": v(253.1, -448.03) * mm, "end": v(252.96, -448.16) * mm});
            skLineSegment(sketch, "E6073", {"start": v(252.96, -448.16) * mm, "end": v(252.8, -448.27) * mm});
            skLineSegment(sketch, "E6074", {"start": v(252.8, -448.27) * mm, "end": v(252.64, -448.36) * mm});
            skLineSegment(sketch, "E6075", {"start": v(252.64, -448.36) * mm, "end": v(252.46, -448.43) * mm});
            skLineSegment(sketch, "E6076", {"start": v(252.46, -448.43) * mm, "end": v(252.28, -448.47) * mm});
            skLineSegment(sketch, "E6077", {"start": v(252.28, -448.47) * mm, "end": v(252.1, -448.5) * mm});
            skLineSegment(sketch, "E6078", {"start": v(252.1, -448.5) * mm, "end": v(251.9, -448.5) * mm});
            skLineSegment(sketch, "E6079", {"start": v(157.9, -448.5) * mm, "end": v(157.72, -448.47) * mm});
            skLineSegment(sketch, "E6080", {"start": v(157.72, -448.47) * mm, "end": v(157.54, -448.43) * mm});
            skLineSegment(sketch, "E6081", {"start": v(157.54, -448.43) * mm, "end": v(157.36, -448.36) * mm});
            skLineSegment(sketch, "E6082", {"start": v(157.36, -448.36) * mm, "end": v(157.2, -448.27) * mm});
            skLineSegment(sketch, "E6083", {"start": v(157.2, -448.27) * mm, "end": v(157.04, -448.16) * mm});
            skLineSegment(sketch, "E6084", {"start": v(157.04, -448.16) * mm, "end": v(156.9, -448.03) * mm});
            skLineSegment(sketch, "E6085", {"start": v(156.9, -448.03) * mm, "end": v(156.79, -447.88) * mm});
            skLineSegment(sketch, "E6086", {"start": v(156.79, -447.88) * mm, "end": v(156.69, -447.72) * mm});
            skLineSegment(sketch, "E6087", {"start": v(156.69, -447.72) * mm, "end": v(156.6, -447.55) * mm});
            skLineSegment(sketch, "E6088", {"start": v(156.6, -447.55) * mm, "end": v(156.55, -447.37) * mm});
            skLineSegment(sketch, "E6089", {"start": v(156.55, -447.37) * mm, "end": v(156.51, -447.19) * mm});
            skLineSegment(sketch, "E6090", {"start": v(156.51, -447.19) * mm, "end": v(156.5, -447) * mm});
            skLineSegment(sketch, "E6091", {"start": v(156.5, -447) * mm, "end": v(156.51, -446.81) * mm});
            skLineSegment(sketch, "E6092", {"start": v(156.51, -446.81) * mm, "end": v(156.55, -446.63) * mm});
            skLineSegment(sketch, "E6093", {"start": v(156.55, -446.63) * mm, "end": v(156.6, -446.45) * mm});
            skLineSegment(sketch, "E6094", {"start": v(156.6, -446.45) * mm, "end": v(156.69, -446.28) * mm});
            skLineSegment(sketch, "E6095", {"start": v(156.69, -446.28) * mm, "end": v(156.79, -446.12) * mm});
            skLineSegment(sketch, "E6096", {"start": v(156.79, -446.12) * mm, "end": v(156.9, -445.97) * mm});
            skLineSegment(sketch, "E6097", {"start": v(156.9, -445.97) * mm, "end": v(157.04, -445.84) * mm});
            skLineSegment(sketch, "E6098", {"start": v(157.04, -445.84) * mm, "end": v(157.2, -445.73) * mm});
            skLineSegment(sketch, "E6099", {"start": v(157.2, -445.73) * mm, "end": v(157.36, -445.64) * mm});
            skLineSegment(sketch, "E6100", {"start": v(157.36, -445.64) * mm, "end": v(157.54, -445.57) * mm});
            skLineSegment(sketch, "E6101", {"start": v(157.54, -445.57) * mm, "end": v(157.72, -445.53) * mm});
            skLineSegment(sketch, "E6102", {"start": v(157.72, -445.53) * mm, "end": v(157.9, -445.5) * mm});
            skLineSegment(sketch, "E6103", {"start": v(157.9, -445.5) * mm, "end": v(158.1, -445.5) * mm});
            skLineSegment(sketch, "E6104", {"start": v(158.1, -445.5) * mm, "end": v(158.28, -445.53) * mm});
            skLineSegment(sketch, "E6105", {"start": v(158.28, -445.53) * mm, "end": v(158.46, -445.57) * mm});
            skLineSegment(sketch, "E6106", {"start": v(158.46, -445.57) * mm, "end": v(158.64, -445.64) * mm});
            skLineSegment(sketch, "E6107", {"start": v(158.64, -445.64) * mm, "end": v(158.8, -445.73) * mm});
            skLineSegment(sketch, "E6108", {"start": v(158.8, -445.73) * mm, "end": v(158.96, -445.84) * mm});
            skLineSegment(sketch, "E6109", {"start": v(158.96, -445.84) * mm, "end": v(159.1, -445.97) * mm});
            skLineSegment(sketch, "E6110", {"start": v(159.1, -445.97) * mm, "end": v(159.21, -446.12) * mm});
            skLineSegment(sketch, "E6111", {"start": v(159.21, -446.12) * mm, "end": v(159.31, -446.28) * mm});
            skLineSegment(sketch, "E6112", {"start": v(159.31, -446.28) * mm, "end": v(159.4, -446.45) * mm});
            skLineSegment(sketch, "E6113", {"start": v(159.4, -446.45) * mm, "end": v(159.45, -446.63) * mm});
            skLineSegment(sketch, "E6114", {"start": v(159.45, -446.63) * mm, "end": v(159.49, -446.81) * mm});
            skLineSegment(sketch, "E6115", {"start": v(159.49, -446.81) * mm, "end": v(159.5, -447) * mm});
            skLineSegment(sketch, "E6116", {"start": v(159.5, -447) * mm, "end": v(159.49, -447.19) * mm});
            skLineSegment(sketch, "E6117", {"start": v(159.49, -447.19) * mm, "end": v(159.45, -447.37) * mm});
            skLineSegment(sketch, "E6118", {"start": v(159.45, -447.37) * mm, "end": v(159.4, -447.55) * mm});
            skLineSegment(sketch, "E6119", {"start": v(159.4, -447.55) * mm, "end": v(159.31, -447.72) * mm});
            skLineSegment(sketch, "E6120", {"start": v(159.31, -447.72) * mm, "end": v(159.21, -447.88) * mm});
            skLineSegment(sketch, "E6121", {"start": v(159.21, -447.88) * mm, "end": v(159.1, -448.03) * mm});
            skLineSegment(sketch, "E6122", {"start": v(159.1, -448.03) * mm, "end": v(158.96, -448.16) * mm});
            skLineSegment(sketch, "E6123", {"start": v(158.96, -448.16) * mm, "end": v(158.8, -448.27) * mm});
            skLineSegment(sketch, "E6124", {"start": v(158.8, -448.27) * mm, "end": v(158.64, -448.36) * mm});
            skLineSegment(sketch, "E6125", {"start": v(158.64, -448.36) * mm, "end": v(158.46, -448.43) * mm});
            skLineSegment(sketch, "E6126", {"start": v(158.46, -448.43) * mm, "end": v(158.28, -448.47) * mm});
            skLineSegment(sketch, "E6127", {"start": v(158.28, -448.47) * mm, "end": v(158.1, -448.5) * mm});
            skLineSegment(sketch, "E6128", {"start": v(158.1, -448.5) * mm, "end": v(157.9, -448.5) * mm});
            skLineSegment(sketch, "E6129", {"start": v(50, -466.5) * mm, "end": v(50, -450.5) * mm});
            skLineSegment(sketch, "E6130", {"start": v(50, -450.5) * mm, "end": v(70, -450.5) * mm});
            skLineSegment(sketch, "E6131", {"start": v(70, -450.5) * mm, "end": v(70, -466.5) * mm});
            skLineSegment(sketch, "E6132", {"start": v(70, -466.5) * mm, "end": v(50, -466.5) * mm});
            skLineSegment(sketch, "E6133", {"start": v(340, -466.5) * mm, "end": v(340, -450.5) * mm});
            skLineSegment(sketch, "E6134", {"start": v(340, -450.5) * mm, "end": v(360, -450.5) * mm});
            skLineSegment(sketch, "E6135", {"start": v(360, -450.5) * mm, "end": v(360, -466.5) * mm});
            skLineSegment(sketch, "E6136", {"start": v(360, -466.5) * mm, "end": v(340, -466.5) * mm});
            skLineSegment(sketch, "E6137", {"start": v(195, -466.5) * mm, "end": v(195, -450.5) * mm});
            skLineSegment(sketch, "E6138", {"start": v(195, -450.5) * mm, "end": v(215, -450.5) * mm});
            skLineSegment(sketch, "E6139", {"start": v(215, -450.5) * mm, "end": v(215, -466.5) * mm});
            skLineSegment(sketch, "E6140", {"start": v(215, -466.5) * mm, "end": v(195, -466.5) * mm});
            skLineSegment(sketch, "E6141", {"start": v(122.37, -460.5) * mm, "end": v(122.12, -460.46) * mm});
            skLineSegment(sketch, "E6142", {"start": v(122.12, -460.46) * mm, "end": v(121.88, -460.4) * mm});
            skLineSegment(sketch, "E6143", {"start": v(121.88, -460.4) * mm, "end": v(121.65, -460.3) * mm});
            skLineSegment(sketch, "E6144", {"start": v(121.65, -460.3) * mm, "end": v(121.43, -460.19) * mm});
            skLineSegment(sketch, "E6145", {"start": v(121.43, -460.19) * mm, "end": v(121.22, -460.04) * mm});
            skLineSegment(sketch, "E6146", {"start": v(121.22, -460.04) * mm, "end": v(121.04, -459.87) * mm});
            skLineSegment(sketch, "E6147", {"start": v(121.04, -459.87) * mm, "end": v(120.88, -459.68) * mm});
            skLineSegment(sketch, "E6148", {"start": v(120.88, -459.68) * mm, "end": v(120.75, -459.46) * mm});
            skLineSegment(sketch, "E6149", {"start": v(120.75, -459.46) * mm, "end": v(120.64, -459.24) * mm});
            skLineSegment(sketch, "E6150", {"start": v(120.64, -459.24) * mm, "end": v(120.56, -459) * mm});
            skLineSegment(sketch, "E6151", {"start": v(120.56, -459) * mm, "end": v(120.52, -458.75) * mm});
            skLineSegment(sketch, "E6152", {"start": v(120.52, -458.75) * mm, "end": v(120.5, -458.5) * mm});
            skLineSegment(sketch, "E6153", {"start": v(120.5, -458.5) * mm, "end": v(120.52, -458.25) * mm});
            skLineSegment(sketch, "E6154", {"start": v(120.52, -458.25) * mm, "end": v(120.56, -458) * mm});
            skLineSegment(sketch, "E6155", {"start": v(120.56, -458) * mm, "end": v(120.64, -457.76) * mm});
            skLineSegment(sketch, "E6156", {"start": v(120.64, -457.76) * mm, "end": v(120.75, -457.54) * mm});
            skLineSegment(sketch, "E6157", {"start": v(120.75, -457.54) * mm, "end": v(120.88, -457.32) * mm});
            skLineSegment(sketch, "E6158", {"start": v(120.88, -457.32) * mm, "end": v(121.04, -457.13) * mm});
            skLineSegment(sketch, "E6159", {"start": v(121.04, -457.13) * mm, "end": v(121.22, -456.96) * mm});
            skLineSegment(sketch, "E6160", {"start": v(121.22, -456.96) * mm, "end": v(121.43, -456.81) * mm});
            skLineSegment(sketch, "E6161", {"start": v(121.43, -456.81) * mm, "end": v(121.65, -456.7) * mm});
            skLineSegment(sketch, "E6162", {"start": v(121.65, -456.7) * mm, "end": v(121.88, -456.6) * mm});
            skLineSegment(sketch, "E6163", {"start": v(121.88, -456.6) * mm, "end": v(122.12, -456.54) * mm});
            skLineSegment(sketch, "E6164", {"start": v(122.12, -456.54) * mm, "end": v(122.37, -456.5) * mm});
            skLineSegment(sketch, "E6165", {"start": v(122.37, -456.5) * mm, "end": v(122.63, -456.5) * mm});
            skLineSegment(sketch, "E6166", {"start": v(122.63, -456.5) * mm, "end": v(122.88, -456.54) * mm});
            skLineSegment(sketch, "E6167", {"start": v(122.88, -456.54) * mm, "end": v(123.12, -456.6) * mm});
            skLineSegment(sketch, "E6168", {"start": v(123.12, -456.6) * mm, "end": v(123.35, -456.7) * mm});
            skLineSegment(sketch, "E6169", {"start": v(123.35, -456.7) * mm, "end": v(123.57, -456.81) * mm});
            skLineSegment(sketch, "E6170", {"start": v(123.57, -456.81) * mm, "end": v(123.78, -456.96) * mm});
            skLineSegment(sketch, "E6171", {"start": v(123.78, -456.96) * mm, "end": v(123.96, -457.13) * mm});
            skLineSegment(sketch, "E6172", {"start": v(123.96, -457.13) * mm, "end": v(124.12, -457.32) * mm});
            skLineSegment(sketch, "E6173", {"start": v(124.12, -457.32) * mm, "end": v(124.25, -457.54) * mm});
            skLineSegment(sketch, "E6174", {"start": v(124.25, -457.54) * mm, "end": v(124.36, -457.76) * mm});
            skLineSegment(sketch, "E6175", {"start": v(124.36, -457.76) * mm, "end": v(124.44, -458) * mm});
            skLineSegment(sketch, "E6176", {"start": v(124.44, -458) * mm, "end": v(124.48, -458.25) * mm});
            skLineSegment(sketch, "E6177", {"start": v(124.48, -458.25) * mm, "end": v(124.5, -458.5) * mm});
            skLineSegment(sketch, "E6178", {"start": v(124.5, -458.5) * mm, "end": v(124.48, -458.75) * mm});
            skLineSegment(sketch, "E6179", {"start": v(124.48, -458.75) * mm, "end": v(124.44, -459) * mm});
            skLineSegment(sketch, "E6180", {"start": v(124.44, -459) * mm, "end": v(124.36, -459.24) * mm});
            skLineSegment(sketch, "E6181", {"start": v(124.36, -459.24) * mm, "end": v(124.25, -459.46) * mm});
            skLineSegment(sketch, "E6182", {"start": v(124.25, -459.46) * mm, "end": v(124.12, -459.68) * mm});
            skLineSegment(sketch, "E6183", {"start": v(124.12, -459.68) * mm, "end": v(123.96, -459.87) * mm});
            skLineSegment(sketch, "E6184", {"start": v(123.96, -459.87) * mm, "end": v(123.78, -460.04) * mm});
            skLineSegment(sketch, "E6185", {"start": v(123.78, -460.04) * mm, "end": v(123.57, -460.19) * mm});
            skLineSegment(sketch, "E6186", {"start": v(123.57, -460.19) * mm, "end": v(123.35, -460.3) * mm});
            skLineSegment(sketch, "E6187", {"start": v(123.35, -460.3) * mm, "end": v(123.12, -460.4) * mm});
            skLineSegment(sketch, "E6188", {"start": v(123.12, -460.4) * mm, "end": v(122.88, -460.46) * mm});
            skLineSegment(sketch, "E6189", {"start": v(122.88, -460.46) * mm, "end": v(122.63, -460.5) * mm});
            skLineSegment(sketch, "E6190", {"start": v(122.63, -460.5) * mm, "end": v(122.37, -460.5) * mm});
            skLineSegment(sketch, "E6191", {"start": v(287.37, -460.5) * mm, "end": v(287.12, -460.46) * mm});
            skLineSegment(sketch, "E6192", {"start": v(287.12, -460.46) * mm, "end": v(286.88, -460.4) * mm});
            skLineSegment(sketch, "E6193", {"start": v(286.88, -460.4) * mm, "end": v(286.65, -460.3) * mm});
            skLineSegment(sketch, "E6194", {"start": v(286.65, -460.3) * mm, "end": v(286.43, -460.19) * mm});
            skLineSegment(sketch, "E6195", {"start": v(286.43, -460.19) * mm, "end": v(286.23, -460.04) * mm});
            skLineSegment(sketch, "E6196", {"start": v(286.23, -460.04) * mm, "end": v(286.04, -459.87) * mm});
            skLineSegment(sketch, "E6197", {"start": v(286.04, -459.87) * mm, "end": v(285.88, -459.68) * mm});
            skLineSegment(sketch, "E6198", {"start": v(285.88, -459.68) * mm, "end": v(285.75, -459.46) * mm});
            skLineSegment(sketch, "E6199", {"start": v(285.75, -459.46) * mm, "end": v(285.64, -459.24) * mm});
            skLineSegment(sketch, "E6200", {"start": v(285.64, -459.24) * mm, "end": v(285.56, -459) * mm});
            skLineSegment(sketch, "E6201", {"start": v(285.56, -459) * mm, "end": v(285.52, -458.75) * mm});
            skLineSegment(sketch, "E6202", {"start": v(285.52, -458.75) * mm, "end": v(285.5, -458.5) * mm});
            skLineSegment(sketch, "E6203", {"start": v(285.5, -458.5) * mm, "end": v(285.52, -458.25) * mm});
            skLineSegment(sketch, "E6204", {"start": v(285.52, -458.25) * mm, "end": v(285.56, -458) * mm});
            skLineSegment(sketch, "E6205", {"start": v(285.56, -458) * mm, "end": v(285.64, -457.76) * mm});
            skLineSegment(sketch, "E6206", {"start": v(285.64, -457.76) * mm, "end": v(285.75, -457.54) * mm});
            skLineSegment(sketch, "E6207", {"start": v(285.75, -457.54) * mm, "end": v(285.88, -457.32) * mm});
            skLineSegment(sketch, "E6208", {"start": v(285.88, -457.32) * mm, "end": v(286.04, -457.13) * mm});
            skLineSegment(sketch, "E6209", {"start": v(286.04, -457.13) * mm, "end": v(286.23, -456.96) * mm});
            skLineSegment(sketch, "E6210", {"start": v(286.23, -456.96) * mm, "end": v(286.43, -456.81) * mm});
            skLineSegment(sketch, "E6211", {"start": v(286.43, -456.81) * mm, "end": v(286.65, -456.7) * mm});
            skLineSegment(sketch, "E6212", {"start": v(286.65, -456.7) * mm, "end": v(286.88, -456.6) * mm});
            skLineSegment(sketch, "E6213", {"start": v(286.88, -456.6) * mm, "end": v(287.12, -456.54) * mm});
            skLineSegment(sketch, "E6214", {"start": v(287.12, -456.54) * mm, "end": v(287.37, -456.5) * mm});
            skLineSegment(sketch, "E6215", {"start": v(287.37, -456.5) * mm, "end": v(287.63, -456.5) * mm});
            skLineSegment(sketch, "E6216", {"start": v(287.63, -456.5) * mm, "end": v(287.88, -456.54) * mm});
            skLineSegment(sketch, "E6217", {"start": v(287.88, -456.54) * mm, "end": v(288.12, -456.6) * mm});
            skLineSegment(sketch, "E6218", {"start": v(288.12, -456.6) * mm, "end": v(288.35, -456.7) * mm});
            skLineSegment(sketch, "E6219", {"start": v(288.35, -456.7) * mm, "end": v(288.57, -456.81) * mm});
            skLineSegment(sketch, "E6220", {"start": v(288.57, -456.81) * mm, "end": v(288.77, -456.96) * mm});
            skLineSegment(sketch, "E6221", {"start": v(288.77, -456.96) * mm, "end": v(288.96, -457.13) * mm});
            skLineSegment(sketch, "E6222", {"start": v(288.96, -457.13) * mm, "end": v(289.12, -457.32) * mm});
            skLineSegment(sketch, "E6223", {"start": v(289.12, -457.32) * mm, "end": v(289.25, -457.54) * mm});
            skLineSegment(sketch, "E6224", {"start": v(289.25, -457.54) * mm, "end": v(289.36, -457.76) * mm});
            skLineSegment(sketch, "E6225", {"start": v(289.36, -457.76) * mm, "end": v(289.44, -458) * mm});
            skLineSegment(sketch, "E6226", {"start": v(289.44, -458) * mm, "end": v(289.48, -458.25) * mm});
            skLineSegment(sketch, "E6227", {"start": v(289.48, -458.25) * mm, "end": v(289.5, -458.5) * mm});
            skLineSegment(sketch, "E6228", {"start": v(289.5, -458.5) * mm, "end": v(289.48, -458.75) * mm});
            skLineSegment(sketch, "E6229", {"start": v(289.48, -458.75) * mm, "end": v(289.44, -459) * mm});
            skLineSegment(sketch, "E6230", {"start": v(289.44, -459) * mm, "end": v(289.36, -459.24) * mm});
            skLineSegment(sketch, "E6231", {"start": v(289.36, -459.24) * mm, "end": v(289.25, -459.46) * mm});
            skLineSegment(sketch, "E6232", {"start": v(289.25, -459.46) * mm, "end": v(289.12, -459.68) * mm});
            skLineSegment(sketch, "E6233", {"start": v(289.12, -459.68) * mm, "end": v(288.96, -459.87) * mm});
            skLineSegment(sketch, "E6234", {"start": v(288.96, -459.87) * mm, "end": v(288.77, -460.04) * mm});
            skLineSegment(sketch, "E6235", {"start": v(288.77, -460.04) * mm, "end": v(288.57, -460.19) * mm});
            skLineSegment(sketch, "E6236", {"start": v(288.57, -460.19) * mm, "end": v(288.35, -460.3) * mm});
            skLineSegment(sketch, "E6237", {"start": v(288.35, -460.3) * mm, "end": v(288.12, -460.4) * mm});
            skLineSegment(sketch, "E6238", {"start": v(288.12, -460.4) * mm, "end": v(287.88, -460.46) * mm});
            skLineSegment(sketch, "E6239", {"start": v(287.88, -460.46) * mm, "end": v(287.63, -460.5) * mm});
            skLineSegment(sketch, "E6240", {"start": v(287.63, -460.5) * mm, "end": v(287.37, -460.5) * mm});
            skLineSegment(sketch, "E6241", {"start": v(360, -487) * mm, "end": v(340, -487) * mm});
            skLineSegment(sketch, "E6242", {"start": v(215, -487) * mm, "end": v(195, -487) * mm});
            skLineSegment(sketch, "E6243", {"start": v(70, -487) * mm, "end": v(50, -487) * mm});
            skLineSegment(sketch, "E6244", {"start": v(50, -487) * mm, "end": v(50, -503) * mm});
            skLineSegment(sketch, "E6245", {"start": v(50, -503) * mm, "end": v(10, -503) * mm});
            skLineSegment(sketch, "E6246", {"start": v(10, -503) * mm, "end": v(10, -553) * mm});
            skLineSegment(sketch, "E6247", {"start": v(10, -553) * mm, "end": v(10.08, -554.25) * mm});
            skLineSegment(sketch, "E6248", {"start": v(10.08, -554.25) * mm, "end": v(10.31, -555.49) * mm});
            skLineSegment(sketch, "E6249", {"start": v(10.31, -555.49) * mm, "end": v(10.7, -556.68) * mm});
            skLineSegment(sketch, "E6250", {"start": v(10.7, -556.68) * mm, "end": v(11.24, -557.82) * mm});
            skLineSegment(sketch, "E6251", {"start": v(11.24, -557.82) * mm, "end": v(11.9, -558.88) * mm});
            skLineSegment(sketch, "E6252", {"start": v(11.9, -558.88) * mm, "end": v(12.71, -559.85) * mm});
            skLineSegment(sketch, "E6253", {"start": v(12.71, -559.85) * mm, "end": v(13.63, -560.7) * mm});
            skLineSegment(sketch, "E6254", {"start": v(13.63, -560.7) * mm, "end": v(14.64, -561.44) * mm});
            skLineSegment(sketch, "E6255", {"start": v(14.64, -561.44) * mm, "end": v(15.74, -562.05) * mm});
            skLineSegment(sketch, "E6256", {"start": v(15.74, -562.05) * mm, "end": v(16.9, -562.51) * mm});
            skLineSegment(sketch, "E6257", {"start": v(16.9, -562.51) * mm, "end": v(18.13, -562.82) * mm});
            skLineSegment(sketch, "E6258", {"start": v(18.13, -562.82) * mm, "end": v(19.37, -562.98) * mm});
            skLineSegment(sketch, "E6259", {"start": v(19.37, -562.98) * mm, "end": v(20, -562.98) * mm});
            skLineSegment(sketch, "E6260", {"start": v(20, -562.98) * mm, "end": v(20, -563) * mm});
            skLineSegment(sketch, "E6261", {"start": v(20, -563) * mm, "end": v(40, -563) * mm});
            skLineSegment(sketch, "E6262", {"start": v(40, -563) * mm, "end": v(40, -562.98) * mm});
            skSolve(sketch);
        }
        {
            var Q0;
            Q0=makeQuery(id+"F0.imprint","IMPRINT",FACE,{"disambiguationData":[TD([[makeQuery(id+"F0.imprint","IMPRINT",EDGE,{"derivedFrom":sQuery(id+"F0.wireOp",EDGE,"E760")}),1.0]])]});
            var Q1;
            Q1=makeQuery(id+"F0.imprint","IMPRINT",FACE,{"disambiguationData":[TD([[makeQuery(id+"F0.imprint","IMPRINT",EDGE,{"derivedFrom":sQuery(id+"F0.wireOp",EDGE,"E0")}),1.0]])]});
            var Q2;
            Q2=makeQuery(id+"F0.imprint","IMPRINT",FACE,{"disambiguationData":[TD([[makeQuery(id+"F0.imprint","IMPRINT",EDGE,{"derivedFrom":sQuery(id+"F0.wireOp",EDGE,"E3043")}),1.0]])]});
            var Q3;
            Q3=makeQuery(id+"F0.imprint","IMPRINT",FACE,{"disambiguationData":[TD([[makeQuery(id+"F0.imprint","IMPRINT",EDGE,{"derivedFrom":sQuery(id+"F0.wireOp",EDGE,"E3833")}),1.0]])]});
            var Q4;
            Q4=makeQuery(id+"F0.imprint","IMPRINT",FACE,{"disambiguationData":[TD([[makeQuery(id+"F0.imprint","IMPRINT",EDGE,{"derivedFrom":sQuery(id+"F0.wireOp",EDGE,"E3622")}),1.0]])]});
            var Q5;
            Q5=makeQuery(id+"F0.imprint","IMPRINT",FACE,{"disambiguationData":[TD([[makeQuery(id+"F0.imprint","IMPRINT",EDGE,{"derivedFrom":sQuery(id+"F0.wireOp",EDGE,"E3591")}),1.0]])]});
            var Q6;
            Q6=makeQuery(id+"F0.imprint","IMPRINT",FACE,{"disambiguationData":[TD([[makeQuery(id+"F0.imprint","IMPRINT",EDGE,{"derivedFrom":sQuery(id+"F0.wireOp",EDGE,"E2779")}),1.0]])]});
            var Q7;
            Q7=makeQuery(id+"F0.imprint","IMPRINT",FACE,{"disambiguationData":[TD([[makeQuery(id+"F0.imprint","IMPRINT",EDGE,{"derivedFrom":sQuery(id+"F0.wireOp",EDGE,"E2810")}),1.0]])]});
            var Q8;
            Q8=makeQuery(id+"F0.imprint","IMPRINT",FACE,{"disambiguationData":[TD([[makeQuery(id+"F0.imprint","IMPRINT",EDGE,{"derivedFrom":sQuery(id+"F0.wireOp",EDGE,"E2841")}),1.0]])]});
            var Q9;
            Q9=makeQuery(id+"F0.imprint","IMPRINT",FACE,{"disambiguationData":[TD([[makeQuery(id+"F0.imprint","IMPRINT",EDGE,{"derivedFrom":sQuery(id+"F0.wireOp",EDGE,"E2942")}),1.0]])]});
            var Q10;
            Q10=makeQuery(id+"F0.imprint","IMPRINT",FACE,{"disambiguationData":[TD([[makeQuery(id+"F0.imprint","IMPRINT",EDGE,{"derivedFrom":sQuery(id+"F0.wireOp",EDGE,"E3653")}),1.0]])]});
            var Q11;
            Q11=makeQuery(id+"F0.imprint","IMPRINT",FACE,{"disambiguationData":[TD([[makeQuery(id+"F0.imprint","IMPRINT",EDGE,{"derivedFrom":sQuery(id+"F0.wireOp",EDGE,"E3754")}),1.0]])]});
            extrude(context, id + "F1", {"entities" : qUnion([Q0, Q1, Q2, Q3, Q4, Q5, Q6, Q7, Q8, Q9, Q10, Q11]), "depth" : 8 * mm});
        }
    });
